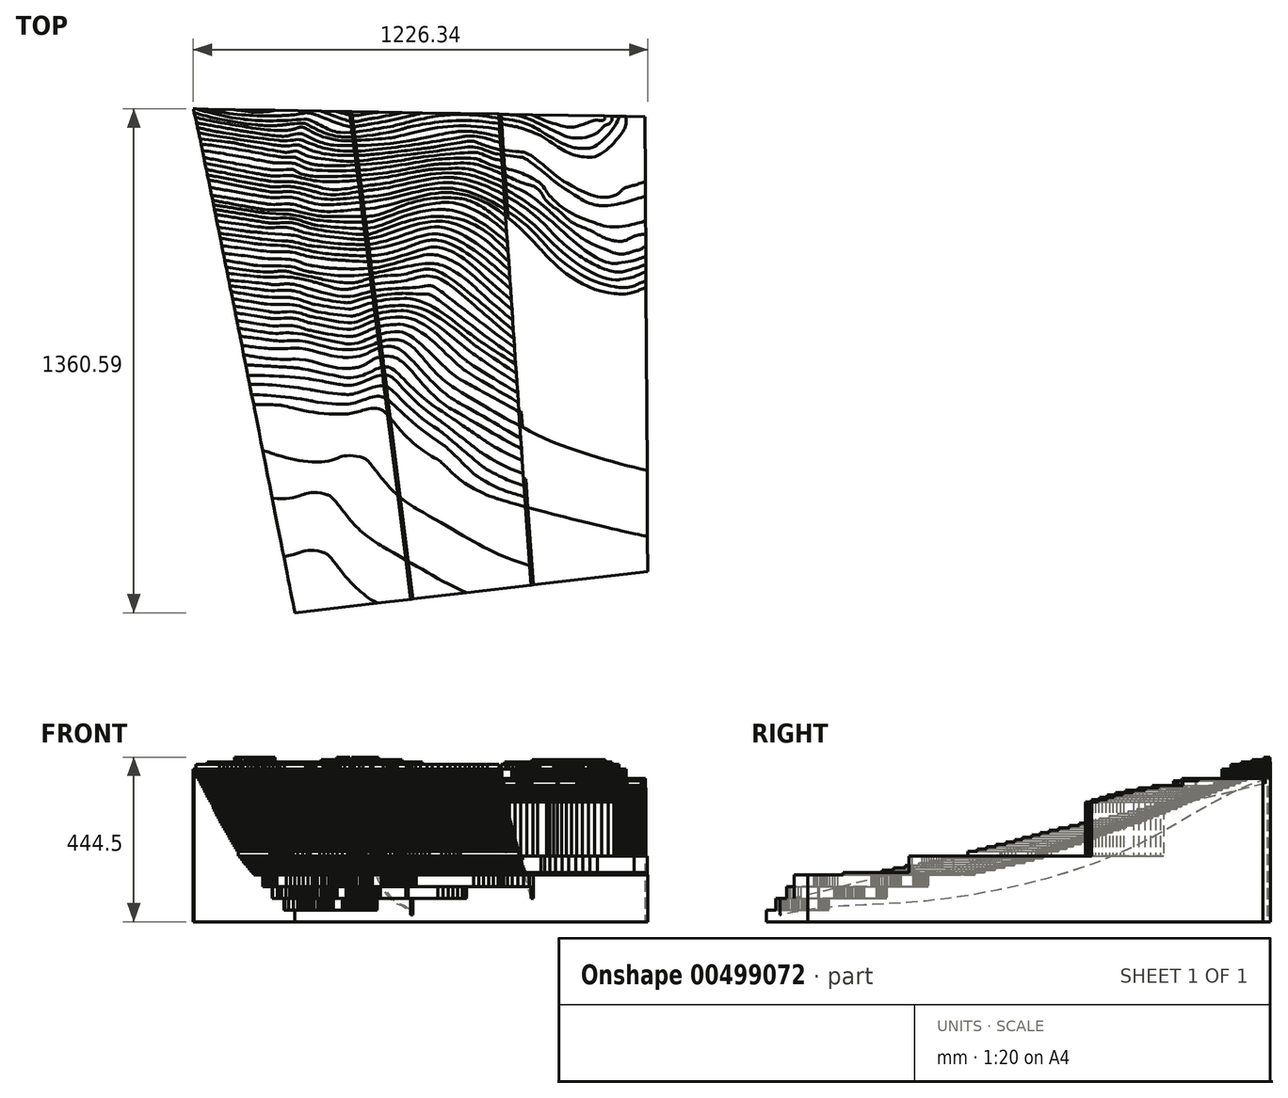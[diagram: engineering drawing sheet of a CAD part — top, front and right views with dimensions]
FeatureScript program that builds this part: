
annotation { "Feature Type Name" : "Feature", "Feature Type Description" : "" }
export const myFeature = defineFeature(function(context is Context, id is Id, definition is map)
    precondition{}
    {
        {
            var Q0;
            Q0=qCreatedBy(makeId("Top.planeOp"),FACE);
            var sketch = newSketch(context, id + "F0", { "sketchPlane" : qUnion([Q0])});
            skLineSegment(sketch, "E0", {"start": v(-613.2, 679.89) * mm, "end": v(-613.14, 679.9) * mm});
            skLineSegment(sketch, "E1", {"start": v(-613.14, 679.9) * mm, "end": v(-612.74, 678.97) * mm});
            skLineSegment(sketch, "E2", {"start": v(-612.74, 678.97) * mm, "end": v(-611.9, 676.1) * mm});
            skLineSegment(sketch, "E3", {"start": v(-611.9, 676.1) * mm, "end": v(-610.7, 671.38) * mm});
            skLineSegment(sketch, "E4", {"start": v(-610.7, 671.38) * mm, "end": v(-609.15, 664.84) * mm});
            skLineSegment(sketch, "E5", {"start": v(-609.15, 664.84) * mm, "end": v(-607.27, 656.56) * mm});
            skLineSegment(sketch, "E6", {"start": v(-607.27, 656.56) * mm, "end": v(-605.06, 646.58) * mm});
            skLineSegment(sketch, "E7", {"start": v(-605.06, 646.58) * mm, "end": v(-602.54, 634.99) * mm});
            skLineSegment(sketch, "E8", {"start": v(-602.54, 634.99) * mm, "end": v(-599.72, 621.83) * mm});
            skLineSegment(sketch, "E9", {"start": v(-599.72, 621.83) * mm, "end": v(-596.61, 607.18) * mm});
            skLineSegment(sketch, "E10", {"start": v(-596.61, 607.18) * mm, "end": v(-593.23, 591.1) * mm});
            skLineSegment(sketch, "E11", {"start": v(-593.23, 591.1) * mm, "end": v(-589.58, 573.63) * mm});
            skLineSegment(sketch, "E12", {"start": v(-589.58, 573.63) * mm, "end": v(-585.69, 554.85) * mm});
            skLineSegment(sketch, "E13", {"start": v(-585.69, 554.85) * mm, "end": v(-581.55, 534.83) * mm});
            skLineSegment(sketch, "E14", {"start": v(-581.55, 534.83) * mm, "end": v(-577.19, 513.62) * mm});
            skLineSegment(sketch, "E15", {"start": v(-577.19, 513.62) * mm, "end": v(-572.6, 491.29) * mm});
            skLineSegment(sketch, "E16", {"start": v(-572.6, 491.29) * mm, "end": v(-567.83, 467.9) * mm});
            skLineSegment(sketch, "E17", {"start": v(-567.83, 467.9) * mm, "end": v(-562.86, 443.5) * mm});
            skLineSegment(sketch, "E18", {"start": v(-562.86, 443.5) * mm, "end": v(-557.7, 418.17) * mm});
            skLineSegment(sketch, "E19", {"start": v(-557.7, 418.17) * mm, "end": v(-552.4, 391.97) * mm});
            skLineSegment(sketch, "E20", {"start": v(-552.4, 391.97) * mm, "end": v(-546.93, 364.95) * mm});
            skLineSegment(sketch, "E21", {"start": v(-546.93, 364.95) * mm, "end": v(-541.31, 337.18) * mm});
            skLineSegment(sketch, "E22", {"start": v(-541.31, 337.18) * mm, "end": v(-535.57, 308.73) * mm});
            skLineSegment(sketch, "E23", {"start": v(-535.57, 308.73) * mm, "end": v(-529.72, 279.65) * mm});
            skLineSegment(sketch, "E24", {"start": v(-529.72, 279.65) * mm, "end": v(-523.75, 250.01) * mm});
            skLineSegment(sketch, "E25", {"start": v(-523.75, 250.01) * mm, "end": v(-517.7, 219.87) * mm});
            skLineSegment(sketch, "E26", {"start": v(-517.7, 219.87) * mm, "end": v(-511.56, 189.3) * mm});
            skLineSegment(sketch, "E27", {"start": v(-511.56, 189.3) * mm, "end": v(-505.36, 158.34) * mm});
            skLineSegment(sketch, "E28", {"start": v(-505.36, 158.34) * mm, "end": v(-499.1, 127.08) * mm});
            skLineSegment(sketch, "E29", {"start": v(-499.1, 127.08) * mm, "end": v(-492.79, 95.56) * mm});
            skLineSegment(sketch, "E30", {"start": v(-492.79, 95.56) * mm, "end": v(-486.45, 63.85) * mm});
            skLineSegment(sketch, "E31", {"start": v(-486.45, 63.85) * mm, "end": v(-480.1, 32.02) * mm});
            skLineSegment(sketch, "E32", {"start": v(-480.1, 32.02) * mm, "end": v(-473.73, 0.13) * mm});
            skLineSegment(sketch, "E33", {"start": v(-473.73, 0.13) * mm, "end": v(-467.36, -31.77) * mm});
            skLineSegment(sketch, "E34", {"start": v(-467.36, -31.77) * mm, "end": v(-461.02, -63.6) * mm});
            skLineSegment(sketch, "E35", {"start": v(-461.02, -63.6) * mm, "end": v(-454.7, -95.31) * mm});
            skLineSegment(sketch, "E36", {"start": v(-454.7, -95.31) * mm, "end": v(-448.43, -126.84) * mm});
            skLineSegment(sketch, "E37", {"start": v(-448.43, -126.84) * mm, "end": v(-442.2, -158.12) * mm});
            skLineSegment(sketch, "E38", {"start": v(-442.2, -158.12) * mm, "end": v(-436.05, -189.08) * mm});
            skLineSegment(sketch, "E39", {"start": v(-436.05, -189.08) * mm, "end": v(-429.96, -219.67) * mm});
            skLineSegment(sketch, "E40", {"start": v(-429.96, -219.67) * mm, "end": v(-423.97, -249.82) * mm});
            skLineSegment(sketch, "E41", {"start": v(-423.97, -249.82) * mm, "end": v(-418.09, -279.48) * mm});
            skLineSegment(sketch, "E42", {"start": v(-418.09, -279.48) * mm, "end": v(-412.3, -308.58) * mm});
            skLineSegment(sketch, "E43", {"start": v(-412.3, -308.58) * mm, "end": v(-406.66, -337.06) * mm});
            skLineSegment(sketch, "E44", {"start": v(-406.66, -337.06) * mm, "end": v(-401.15, -364.85) * mm});
            skLineSegment(sketch, "E45", {"start": v(-401.15, -364.85) * mm, "end": v(-395.78, -391.89) * mm});
            skLineSegment(sketch, "E46", {"start": v(-395.78, -391.89) * mm, "end": v(-390.59, -418.12) * mm});
            skLineSegment(sketch, "E47", {"start": v(-390.59, -418.12) * mm, "end": v(-385.56, -443.48) * mm});
            skLineSegment(sketch, "E48", {"start": v(-385.56, -443.48) * mm, "end": v(-380.72, -467.9) * mm});
            skLineSegment(sketch, "E49", {"start": v(-380.72, -467.9) * mm, "end": v(-376.09, -491.34) * mm});
            skLineSegment(sketch, "E50", {"start": v(-376.09, -491.34) * mm, "end": v(-371.66, -513.7) * mm});
            skLineSegment(sketch, "E51", {"start": v(-371.66, -513.7) * mm, "end": v(-367.45, -534.95) * mm});
            skLineSegment(sketch, "E52", {"start": v(-367.45, -534.95) * mm, "end": v(-363.49, -555.02) * mm});
            skLineSegment(sketch, "E53", {"start": v(-363.49, -555.02) * mm, "end": v(-359.76, -573.83) * mm});
            skLineSegment(sketch, "E54", {"start": v(-359.76, -573.83) * mm, "end": v(-356.3, -591.34) * mm});
            skLineSegment(sketch, "E55", {"start": v(-356.3, -591.34) * mm, "end": v(-353.11, -607.47) * mm});
            skLineSegment(sketch, "E56", {"start": v(-353.11, -607.47) * mm, "end": v(-350.2, -622.18) * mm});
            skLineSegment(sketch, "E57", {"start": v(-350.2, -622.18) * mm, "end": v(-347.6, -635.38) * mm});
            skLineSegment(sketch, "E58", {"start": v(-347.6, -635.38) * mm, "end": v(-345.3, -647.03) * mm});
            skLineSegment(sketch, "E59", {"start": v(-345.3, -647.03) * mm, "end": v(-343.32, -657.06) * mm});
            skLineSegment(sketch, "E60", {"start": v(-343.32, -657.06) * mm, "end": v(-341.67, -665.4) * mm});
            skLineSegment(sketch, "E61", {"start": v(-341.67, -665.4) * mm, "end": v(-340.37, -672) * mm});
            skLineSegment(sketch, "E62", {"start": v(-340.37, -672) * mm, "end": v(-339.42, -676.8) * mm});
            skLineSegment(sketch, "E63", {"start": v(-339.42, -676.8) * mm, "end": v(-338.85, -679.71) * mm});
            skLineSegment(sketch, "E64", {"start": v(-338.85, -679.71) * mm, "end": v(-338.65, -680.7) * mm});
            skLineSegment(sketch, "E65", {"start": v(-338.65, -680.7) * mm, "end": v(-35.7, -645.1) * mm});
            skLineSegment(sketch, "E66", {"start": v(-35.7, -645.1) * mm, "end": v(613.2, -568.85) * mm});
            skLineSegment(sketch, "E67", {"start": v(613.2, -568.85) * mm, "end": v(605.8, 659.03) * mm});
            skLineSegment(sketch, "E68", {"start": v(605.8, 659.03) * mm, "end": v(-613.2, 679.89) * mm});
            skLineSegment(sketch, "E69", {"start": v(-185.14, 673.3) * mm, "end": v(-19.73, -643.77) * mm});
            skLineSegment(sketch, "E70", {"start": v(210.98, 665.78) * mm, "end": v(297.85, -605.9) * mm});
            skLineSegment(sketch, "E71", {"start": v(605.8, 600.01) * mm, "end": v(605.27, 598.86) * mm});
            skLineSegment(sketch, "E72", {"start": v(605.27, 598.86) * mm, "end": v(603.88, 595.32) * mm});
            skLineSegment(sketch, "E73", {"start": v(603.88, 595.32) * mm, "end": v(602.44, 590.8) * mm});
            skLineSegment(sketch, "E74", {"start": v(602.44, 590.8) * mm, "end": v(601.41, 586.4) * mm});
            skLineSegment(sketch, "E75", {"start": v(601.41, 586.4) * mm, "end": v(600.73, 582.17) * mm});
            skLineSegment(sketch, "E76", {"start": v(600.73, 582.17) * mm, "end": v(600.34, 578.06) * mm});
            skLineSegment(sketch, "E77", {"start": v(600.34, 578.06) * mm, "end": v(600.17, 574.07) * mm});
            skLineSegment(sketch, "E78", {"start": v(600.17, 574.07) * mm, "end": v(600.14, 570.2) * mm});
            skLineSegment(sketch, "E79", {"start": v(600.14, 570.2) * mm, "end": v(600.2, 566.43) * mm});
            skLineSegment(sketch, "E80", {"start": v(600.2, 566.43) * mm, "end": v(600.27, 562.76) * mm});
            skLineSegment(sketch, "E81", {"start": v(600.27, 562.76) * mm, "end": v(600.3, 559.18) * mm});
            skLineSegment(sketch, "E82", {"start": v(600.3, 559.18) * mm, "end": v(600.2, 555.69) * mm});
            skLineSegment(sketch, "E83", {"start": v(600.2, 555.69) * mm, "end": v(599.93, 552.26) * mm});
            skLineSegment(sketch, "E84", {"start": v(599.93, 552.26) * mm, "end": v(599.4, 548.9) * mm});
            skLineSegment(sketch, "E85", {"start": v(599.4, 548.9) * mm, "end": v(598.57, 545.6) * mm});
            skLineSegment(sketch, "E86", {"start": v(598.57, 545.6) * mm, "end": v(597.34, 542.34) * mm});
            skLineSegment(sketch, "E87", {"start": v(597.34, 542.34) * mm, "end": v(596.14, 539.9) * mm});
            skLineSegment(sketch, "E88", {"start": v(596.14, 539.9) * mm, "end": v(595.67, 539.13) * mm});
            skLineSegment(sketch, "E89", {"start": v(595.67, 539.13) * mm, "end": v(595.16, 538.27) * mm});
            skLineSegment(sketch, "E90", {"start": v(595.16, 538.27) * mm, "end": v(593.4, 535.81) * mm});
            skLineSegment(sketch, "E91", {"start": v(593.4, 535.81) * mm, "end": v(590.8, 532.83) * mm});
            skLineSegment(sketch, "E92", {"start": v(590.8, 532.83) * mm, "end": v(587.93, 530.12) * mm});
            skLineSegment(sketch, "E93", {"start": v(587.93, 530.12) * mm, "end": v(584.83, 527.67) * mm});
            skLineSegment(sketch, "E94", {"start": v(584.83, 527.67) * mm, "end": v(581.56, 525.43) * mm});
            skLineSegment(sketch, "E95", {"start": v(581.56, 525.43) * mm, "end": v(578.16, 523.35) * mm});
            skLineSegment(sketch, "E96", {"start": v(578.16, 523.35) * mm, "end": v(574.67, 521.39) * mm});
            skLineSegment(sketch, "E97", {"start": v(574.67, 521.39) * mm, "end": v(571.16, 519.51) * mm});
            skLineSegment(sketch, "E98", {"start": v(571.16, 519.51) * mm, "end": v(567.66, 517.68) * mm});
            skLineSegment(sketch, "E99", {"start": v(567.66, 517.68) * mm, "end": v(564.23, 515.85) * mm});
            skLineSegment(sketch, "E100", {"start": v(564.23, 515.85) * mm, "end": v(560.91, 513.97) * mm});
            skLineSegment(sketch, "E101", {"start": v(560.91, 513.97) * mm, "end": v(557.76, 512.02) * mm});
            skLineSegment(sketch, "E102", {"start": v(557.76, 512.02) * mm, "end": v(554.82, 509.94) * mm});
            skLineSegment(sketch, "E103", {"start": v(554.82, 509.94) * mm, "end": v(552.14, 507.7) * mm});
            skLineSegment(sketch, "E104", {"start": v(552.14, 507.7) * mm, "end": v(549.76, 505.25) * mm});
            skLineSegment(sketch, "E105", {"start": v(549.76, 505.25) * mm, "end": v(548.2, 503.26) * mm});
            skLineSegment(sketch, "E106", {"start": v(548.2, 503.26) * mm, "end": v(547.75, 502.56) * mm});
            skLineSegment(sketch, "E107", {"start": v(547.75, 502.56) * mm, "end": v(547.27, 501.83) * mm});
            skLineSegment(sketch, "E108", {"start": v(547.27, 501.83) * mm, "end": v(545.82, 499.63) * mm});
            skLineSegment(sketch, "E109", {"start": v(545.82, 499.63) * mm, "end": v(543.69, 496.55) * mm});
            skLineSegment(sketch, "E110", {"start": v(543.69, 496.55) * mm, "end": v(541.33, 493.35) * mm});
            skLineSegment(sketch, "E111", {"start": v(541.33, 493.35) * mm, "end": v(538.73, 490.1) * mm});
            skLineSegment(sketch, "E112", {"start": v(538.73, 490.1) * mm, "end": v(535.88, 486.82) * mm});
            skLineSegment(sketch, "E113", {"start": v(535.88, 486.82) * mm, "end": v(532.77, 483.59) * mm});
            skLineSegment(sketch, "E114", {"start": v(532.77, 483.59) * mm, "end": v(529.4, 480.44) * mm});
            skLineSegment(sketch, "E115", {"start": v(529.4, 480.44) * mm, "end": v(525.72, 477.44) * mm});
            skLineSegment(sketch, "E116", {"start": v(525.72, 477.44) * mm, "end": v(521.75, 474.61) * mm});
            skLineSegment(sketch, "E117", {"start": v(521.75, 474.61) * mm, "end": v(517.47, 472.03) * mm});
            skLineSegment(sketch, "E118", {"start": v(517.47, 472.03) * mm, "end": v(512.86, 469.73) * mm});
            skLineSegment(sketch, "E119", {"start": v(512.86, 469.73) * mm, "end": v(507.91, 467.77) * mm});
            skLineSegment(sketch, "E120", {"start": v(507.91, 467.77) * mm, "end": v(502.62, 466.19) * mm});
            skLineSegment(sketch, "E121", {"start": v(502.62, 466.19) * mm, "end": v(496.96, 465.04) * mm});
            skLineSegment(sketch, "E122", {"start": v(496.96, 465.04) * mm, "end": v(490.92, 464.38) * mm});
            skLineSegment(sketch, "E123", {"start": v(490.92, 464.38) * mm, "end": v(486.1, 464.22) * mm});
            skLineSegment(sketch, "E124", {"start": v(486.1, 464.22) * mm, "end": v(484.5, 464.26) * mm});
            skLineSegment(sketch, "E125", {"start": v(484.5, 464.26) * mm, "end": v(481.06, 464.34) * mm});
            skLineSegment(sketch, "E126", {"start": v(481.06, 464.34) * mm, "end": v(470.76, 464.96) * mm});
            skLineSegment(sketch, "E127", {"start": v(470.76, 464.96) * mm, "end": v(458.56, 466.4) * mm});
            skLineSegment(sketch, "E128", {"start": v(458.56, 466.4) * mm, "end": v(447.67, 468.54) * mm});
            skLineSegment(sketch, "E129", {"start": v(447.67, 468.54) * mm, "end": v(437.86, 471.4) * mm});
            skLineSegment(sketch, "E130", {"start": v(437.86, 471.4) * mm, "end": v(428.9, 474.96) * mm});
            skLineSegment(sketch, "E131", {"start": v(428.9, 474.96) * mm, "end": v(420.54, 479.23) * mm});
            skLineSegment(sketch, "E132", {"start": v(420.54, 479.23) * mm, "end": v(412.57, 484.19) * mm});
            skLineSegment(sketch, "E133", {"start": v(412.57, 484.19) * mm, "end": v(404.75, 489.83) * mm});
            skLineSegment(sketch, "E134", {"start": v(404.75, 489.83) * mm, "end": v(396.84, 496.16) * mm});
            skLineSegment(sketch, "E135", {"start": v(396.84, 496.16) * mm, "end": v(388.6, 503.17) * mm});
            skLineSegment(sketch, "E136", {"start": v(388.6, 503.17) * mm, "end": v(379.82, 510.84) * mm});
            skLineSegment(sketch, "E137", {"start": v(379.82, 510.84) * mm, "end": v(370.25, 519.18) * mm});
            skLineSegment(sketch, "E138", {"start": v(370.25, 519.18) * mm, "end": v(359.67, 528.18) * mm});
            skLineSegment(sketch, "E139", {"start": v(359.67, 528.18) * mm, "end": v(347.83, 537.83) * mm});
            skLineSegment(sketch, "E140", {"start": v(347.83, 537.83) * mm, "end": v(334.5, 548.13) * mm});
            skLineSegment(sketch, "E141", {"start": v(334.5, 548.13) * mm, "end": v(323.27, 556.4) * mm});
            skLineSegment(sketch, "E142", {"start": v(323.27, 556.4) * mm, "end": v(319.47, 559.07) * mm});
            skLineSegment(sketch, "E143", {"start": v(319.47, 559.07) * mm, "end": v(317.5, 560.46) * mm});
            skLineSegment(sketch, "E144", {"start": v(317.5, 560.46) * mm, "end": v(311.46, 564.41) * mm});
            skLineSegment(sketch, "E145", {"start": v(311.46, 564.41) * mm, "end": v(304.02, 568.78) * mm});
            skLineSegment(sketch, "E146", {"start": v(304.02, 568.78) * mm, "end": v(297.09, 572.28) * mm});
            skLineSegment(sketch, "E147", {"start": v(297.09, 572.28) * mm, "end": v(290.6, 575) * mm});
            skLineSegment(sketch, "E148", {"start": v(290.6, 575) * mm, "end": v(284.51, 577.07) * mm});
            skLineSegment(sketch, "E149", {"start": v(284.51, 577.07) * mm, "end": v(278.75, 578.57) * mm});
            skLineSegment(sketch, "E150", {"start": v(278.75, 578.57) * mm, "end": v(273.26, 579.6) * mm});
            skLineSegment(sketch, "E151", {"start": v(273.26, 579.6) * mm, "end": v(267.98, 580.29) * mm});
            skLineSegment(sketch, "E152", {"start": v(267.98, 580.29) * mm, "end": v(262.85, 580.7) * mm});
            skLineSegment(sketch, "E153", {"start": v(262.85, 580.7) * mm, "end": v(257.82, 580.98) * mm});
            skLineSegment(sketch, "E154", {"start": v(257.82, 580.98) * mm, "end": v(252.81, 581.2) * mm});
            skLineSegment(sketch, "E155", {"start": v(252.81, 581.2) * mm, "end": v(247.77, 581.47) * mm});
            skLineSegment(sketch, "E156", {"start": v(247.77, 581.47) * mm, "end": v(242.65, 581.9) * mm});
            skLineSegment(sketch, "E157", {"start": v(242.65, 581.9) * mm, "end": v(237.38, 582.57) * mm});
            skLineSegment(sketch, "E158", {"start": v(237.38, 582.57) * mm, "end": v(231.9, 583.6) * mm});
            skLineSegment(sketch, "E159", {"start": v(231.9, 583.6) * mm, "end": v(227.58, 584.68) * mm});
            skLineSegment(sketch, "E160", {"start": v(227.58, 584.68) * mm, "end": v(226.16, 585.1) * mm});
            skLineSegment(sketch, "E161", {"start": v(226.16, 585.1) * mm, "end": v(224.65, 585.56) * mm});
            skLineSegment(sketch, "E162", {"start": v(224.65, 585.56) * mm, "end": v(220.17, 586.96) * mm});
            skLineSegment(sketch, "E163", {"start": v(220.17, 586.96) * mm, "end": v(214, 588.97) * mm});
            skLineSegment(sketch, "E164", {"start": v(214, 588.97) * mm, "end": v(207.69, 591.08) * mm});
            skLineSegment(sketch, "E165", {"start": v(207.69, 591.08) * mm, "end": v(201.23, 593.26) * mm});
            skLineSegment(sketch, "E166", {"start": v(201.23, 593.26) * mm, "end": v(194.65, 595.43) * mm});
            skLineSegment(sketch, "E167", {"start": v(194.65, 595.43) * mm, "end": v(187.98, 597.57) * mm});
            skLineSegment(sketch, "E168", {"start": v(187.98, 597.57) * mm, "end": v(181.22, 599.6) * mm});
            skLineSegment(sketch, "E169", {"start": v(181.22, 599.6) * mm, "end": v(174.38, 601.51) * mm});
            skLineSegment(sketch, "E170", {"start": v(174.38, 601.51) * mm, "end": v(167.5, 603.23) * mm});
            skLineSegment(sketch, "E171", {"start": v(167.5, 603.23) * mm, "end": v(160.57, 604.71) * mm});
            skLineSegment(sketch, "E172", {"start": v(160.57, 604.71) * mm, "end": v(153.63, 605.9) * mm});
            skLineSegment(sketch, "E173", {"start": v(153.63, 605.9) * mm, "end": v(146.7, 606.76) * mm});
            skLineSegment(sketch, "E174", {"start": v(146.7, 606.76) * mm, "end": v(139.77, 607.24) * mm});
            skLineSegment(sketch, "E175", {"start": v(139.77, 607.24) * mm, "end": v(132.88, 607.27) * mm});
            skLineSegment(sketch, "E176", {"start": v(132.88, 607.27) * mm, "end": v(126.04, 606.83) * mm});
            skLineSegment(sketch, "E177", {"start": v(126.04, 606.83) * mm, "end": v(120.95, 606.17) * mm});
            skLineSegment(sketch, "E178", {"start": v(120.95, 606.17) * mm, "end": v(119.27, 605.86) * mm});
            skLineSegment(sketch, "E179", {"start": v(119.27, 605.86) * mm, "end": v(118.3, 605.68) * mm});
            skLineSegment(sketch, "E180", {"start": v(118.3, 605.68) * mm, "end": v(115.38, 605.14) * mm});
            skLineSegment(sketch, "E181", {"start": v(115.38, 605.14) * mm, "end": v(110.5, 604.26) * mm});
            skLineSegment(sketch, "E182", {"start": v(110.5, 604.26) * mm, "end": v(104.68, 603.22) * mm});
            skLineSegment(sketch, "E183", {"start": v(104.68, 603.22) * mm, "end": v(97.99, 602.04) * mm});
            skLineSegment(sketch, "E184", {"start": v(97.99, 602.04) * mm, "end": v(90.48, 600.74) * mm});
            skLineSegment(sketch, "E185", {"start": v(90.48, 600.74) * mm, "end": v(82.22, 599.31) * mm});
            skLineSegment(sketch, "E186", {"start": v(82.22, 599.31) * mm, "end": v(73.26, 597.8) * mm});
            skLineSegment(sketch, "E187", {"start": v(73.26, 597.8) * mm, "end": v(63.66, 596.18) * mm});
            skLineSegment(sketch, "E188", {"start": v(63.66, 596.18) * mm, "end": v(53.5, 594.5) * mm});
            skLineSegment(sketch, "E189", {"start": v(53.5, 594.5) * mm, "end": v(42.82, 592.75) * mm});
            skLineSegment(sketch, "E190", {"start": v(42.82, 592.75) * mm, "end": v(31.68, 590.95) * mm});
            skLineSegment(sketch, "E191", {"start": v(31.68, 590.95) * mm, "end": v(20.15, 589.12) * mm});
            skLineSegment(sketch, "E192", {"start": v(20.15, 589.12) * mm, "end": v(8.29, 587.27) * mm});
            skLineSegment(sketch, "E193", {"start": v(8.29, 587.27) * mm, "end": v(-3.85, 585.41) * mm});
            skLineSegment(sketch, "E194", {"start": v(-3.85, 585.41) * mm, "end": v(-16.2, 583.56) * mm});
            skLineSegment(sketch, "E195", {"start": v(-16.2, 583.56) * mm, "end": v(-28.7, 581.72) * mm});
            skLineSegment(sketch, "E196", {"start": v(-28.7, 581.72) * mm, "end": v(-41.28, 579.92) * mm});
            skLineSegment(sketch, "E197", {"start": v(-41.28, 579.92) * mm, "end": v(-53.9, 578.16) * mm});
            skLineSegment(sketch, "E198", {"start": v(-53.9, 578.16) * mm, "end": v(-66.5, 576.47) * mm});
            skLineSegment(sketch, "E199", {"start": v(-66.5, 576.47) * mm, "end": v(-79, 574.84) * mm});
            skLineSegment(sketch, "E200", {"start": v(-79, 574.84) * mm, "end": v(-91.35, 573.3) * mm});
            skLineSegment(sketch, "E201", {"start": v(-91.35, 573.3) * mm, "end": v(-103.5, 571.85) * mm});
            skLineSegment(sketch, "E202", {"start": v(-103.5, 571.85) * mm, "end": v(-115.37, 570.52) * mm});
            skLineSegment(sketch, "E203", {"start": v(-115.37, 570.52) * mm, "end": v(-126.91, 569.31) * mm});
            skLineSegment(sketch, "E204", {"start": v(-126.91, 569.31) * mm, "end": v(-138.07, 568.25) * mm});
            skLineSegment(sketch, "E205", {"start": v(-138.07, 568.25) * mm, "end": v(-148.77, 567.33) * mm});
            skLineSegment(sketch, "E206", {"start": v(-148.77, 567.33) * mm, "end": v(-158.96, 566.58) * mm});
            skLineSegment(sketch, "E207", {"start": v(-158.96, 566.58) * mm, "end": v(-168.58, 566.01) * mm});
            skLineSegment(sketch, "E208", {"start": v(-168.58, 566.01) * mm, "end": v(-177.56, 565.63) * mm});
            skLineSegment(sketch, "E209", {"start": v(-177.56, 565.63) * mm, "end": v(-185.86, 565.46) * mm});
            skLineSegment(sketch, "E210", {"start": v(-185.86, 565.46) * mm, "end": v(-193.4, 565.5) * mm});
            skLineSegment(sketch, "E211", {"start": v(-193.4, 565.5) * mm, "end": v(-198.44, 565.67) * mm});
            skLineSegment(sketch, "E212", {"start": v(-198.44, 565.67) * mm, "end": v(-200.12, 565.78) * mm});
            skLineSegment(sketch, "E213", {"start": v(-200.12, 565.78) * mm, "end": v(-202.26, 565.91) * mm});
            skLineSegment(sketch, "E214", {"start": v(-202.26, 565.91) * mm, "end": v(-208.66, 566.36) * mm});
            skLineSegment(sketch, "E215", {"start": v(-208.66, 566.36) * mm, "end": v(-216.6, 567) * mm});
            skLineSegment(sketch, "E216", {"start": v(-216.6, 567) * mm, "end": v(-224.03, 567.7) * mm});
            skLineSegment(sketch, "E217", {"start": v(-224.03, 567.7) * mm, "end": v(-231.06, 568.53) * mm});
            skLineSegment(sketch, "E218", {"start": v(-231.06, 568.53) * mm, "end": v(-237.8, 569.48) * mm});
            skLineSegment(sketch, "E219", {"start": v(-237.8, 569.48) * mm, "end": v(-244.32, 570.59) * mm});
            skLineSegment(sketch, "E220", {"start": v(-244.32, 570.59) * mm, "end": v(-250.74, 571.88) * mm});
            skLineSegment(sketch, "E221", {"start": v(-250.74, 571.88) * mm, "end": v(-257.17, 573.37) * mm});
            skLineSegment(sketch, "E222", {"start": v(-257.17, 573.37) * mm, "end": v(-263.68, 575.09) * mm});
            skLineSegment(sketch, "E223", {"start": v(-263.68, 575.09) * mm, "end": v(-270.4, 577.06) * mm});
            skLineSegment(sketch, "E224", {"start": v(-270.4, 577.06) * mm, "end": v(-277.4, 579.32) * mm});
            skLineSegment(sketch, "E225", {"start": v(-277.4, 579.32) * mm, "end": v(-284.8, 581.88) * mm});
            skLineSegment(sketch, "E226", {"start": v(-284.8, 581.88) * mm, "end": v(-292.7, 584.76) * mm});
            skLineSegment(sketch, "E227", {"start": v(-292.7, 584.76) * mm, "end": v(-301.2, 588) * mm});
            skLineSegment(sketch, "E228", {"start": v(-301.2, 588) * mm, "end": v(-310.4, 591.62) * mm});
            skLineSegment(sketch, "E229", {"start": v(-310.4, 591.62) * mm, "end": v(-317.88, 594.63) * mm});
            skLineSegment(sketch, "E230", {"start": v(-317.88, 594.63) * mm, "end": v(-320.38, 595.64) * mm});
            skLineSegment(sketch, "E231", {"start": v(-320.38, 595.64) * mm, "end": v(-321.66, 596.16) * mm});
            skLineSegment(sketch, "E232", {"start": v(-321.66, 596.16) * mm, "end": v(-325.77, 597.08) * mm});
            skLineSegment(sketch, "E233", {"start": v(-325.77, 597.08) * mm, "end": v(-331.45, 597.34) * mm});
            skLineSegment(sketch, "E234", {"start": v(-331.45, 597.34) * mm, "end": v(-337.54, 596.77) * mm});
            skLineSegment(sketch, "E235", {"start": v(-337.54, 596.77) * mm, "end": v(-344.17, 595.74) * mm});
            skLineSegment(sketch, "E236", {"start": v(-344.17, 595.74) * mm, "end": v(-351.48, 594.6) * mm});
            skLineSegment(sketch, "E237", {"start": v(-351.48, 594.6) * mm, "end": v(-359.6, 593.72) * mm});
            skLineSegment(sketch, "E238", {"start": v(-359.6, 593.72) * mm, "end": v(-368.63, 593.46) * mm});
            skLineSegment(sketch, "E239", {"start": v(-368.63, 593.46) * mm, "end": v(-376.23, 593.85) * mm});
            skLineSegment(sketch, "E240", {"start": v(-376.23, 593.85) * mm, "end": v(-378.74, 594.16) * mm});
            skLineSegment(sketch, "E241", {"start": v(-378.74, 594.16) * mm, "end": v(-382.7, 594.64) * mm});
            skLineSegment(sketch, "E242", {"start": v(-382.7, 594.64) * mm, "end": v(-394.59, 596.12) * mm});
            skLineSegment(sketch, "E243", {"start": v(-394.59, 596.12) * mm, "end": v(-409.77, 598.03) * mm});
            skLineSegment(sketch, "E244", {"start": v(-409.77, 598.03) * mm, "end": v(-424.3, 599.88) * mm});
            skLineSegment(sketch, "E245", {"start": v(-424.3, 599.88) * mm, "end": v(-438.15, 601.7) * mm});
            skLineSegment(sketch, "E246", {"start": v(-438.15, 601.7) * mm, "end": v(-451.33, 603.44) * mm});
            skLineSegment(sketch, "E247", {"start": v(-451.33, 603.44) * mm, "end": v(-463.84, 605.13) * mm});
            skLineSegment(sketch, "E248", {"start": v(-463.84, 605.13) * mm, "end": v(-475.66, 606.77) * mm});
            skLineSegment(sketch, "E249", {"start": v(-475.66, 606.77) * mm, "end": v(-486.8, 608.34) * mm});
            skLineSegment(sketch, "E250", {"start": v(-486.8, 608.34) * mm, "end": v(-497.26, 609.86) * mm});
            skLineSegment(sketch, "E251", {"start": v(-497.26, 609.86) * mm, "end": v(-507.02, 611.3) * mm});
            skLineSegment(sketch, "E252", {"start": v(-507.02, 611.3) * mm, "end": v(-516.1, 612.7) * mm});
            skLineSegment(sketch, "E253", {"start": v(-516.1, 612.7) * mm, "end": v(-524.45, 614.02) * mm});
            skLineSegment(sketch, "E254", {"start": v(-524.45, 614.02) * mm, "end": v(-532.11, 615.27) * mm});
            skLineSegment(sketch, "E255", {"start": v(-532.11, 615.27) * mm, "end": v(-539.06, 616.46) * mm});
            skLineSegment(sketch, "E256", {"start": v(-539.06, 616.46) * mm, "end": v(-545.3, 617.58) * mm});
            skLineSegment(sketch, "E257", {"start": v(-545.3, 617.58) * mm, "end": v(-549.44, 618.35) * mm});
            skLineSegment(sketch, "E258", {"start": v(-549.44, 618.35) * mm, "end": v(-550.82, 618.62) * mm});
            skLineSegment(sketch, "E259", {"start": v(-550.82, 618.62) * mm, "end": v(-552.1, 618.87) * mm});
            skLineSegment(sketch, "E260", {"start": v(-552.1, 618.87) * mm, "end": v(-555.94, 619.64) * mm});
            skLineSegment(sketch, "E261", {"start": v(-555.94, 619.64) * mm, "end": v(-560.97, 620.67) * mm});
            skLineSegment(sketch, "E262", {"start": v(-560.97, 620.67) * mm, "end": v(-565.86, 621.7) * mm});
            skLineSegment(sketch, "E263", {"start": v(-565.86, 621.7) * mm, "end": v(-570.6, 622.7) * mm});
            skLineSegment(sketch, "E264", {"start": v(-570.6, 622.7) * mm, "end": v(-575.13, 623.7) * mm});
            skLineSegment(sketch, "E265", {"start": v(-575.13, 623.7) * mm, "end": v(-579.45, 624.65) * mm});
            skLineSegment(sketch, "E266", {"start": v(-579.45, 624.65) * mm, "end": v(-583.5, 625.57) * mm});
            skLineSegment(sketch, "E267", {"start": v(-583.5, 625.57) * mm, "end": v(-587.26, 626.43) * mm});
            skLineSegment(sketch, "E268", {"start": v(-587.26, 626.43) * mm, "end": v(-590.7, 627.23) * mm});
            skLineSegment(sketch, "E269", {"start": v(-590.7, 627.23) * mm, "end": v(-593.8, 627.96) * mm});
            skLineSegment(sketch, "E270", {"start": v(-593.8, 627.96) * mm, "end": v(-596.5, 628.6) * mm});
            skLineSegment(sketch, "E271", {"start": v(-596.5, 628.6) * mm, "end": v(-598.78, 629.15) * mm});
            skLineSegment(sketch, "E272", {"start": v(-598.78, 629.15) * mm, "end": v(-600.6, 629.6) * mm});
            skLineSegment(sketch, "E273", {"start": v(-600.6, 629.6) * mm, "end": v(-601.95, 629.93) * mm});
            skLineSegment(sketch, "E274", {"start": v(-601.95, 629.93) * mm, "end": v(-602.79, 630.13) * mm});
            skLineSegment(sketch, "E275", {"start": v(-602.79, 630.13) * mm, "end": v(-603.07, 630.2) * mm});
            skLineSegment(sketch, "E276", {"start": v(551.81, 549.34) * mm, "end": v(552.44, 554.91) * mm});
            skLineSegment(sketch, "E277", {"start": v(552.44, 554.91) * mm, "end": v(551.81, 549.34) * mm});
            skLineSegment(sketch, "E278", {"start": v(607.88, 486.1) * mm, "end": v(606.78, 485.45) * mm});
            skLineSegment(sketch, "E279", {"start": v(606.78, 485.45) * mm, "end": v(603.41, 483.65) * mm});
            skLineSegment(sketch, "E280", {"start": v(603.41, 483.65) * mm, "end": v(598.9, 481.49) * mm});
            skLineSegment(sketch, "E281", {"start": v(598.9, 481.49) * mm, "end": v(594.36, 479.58) * mm});
            skLineSegment(sketch, "E282", {"start": v(594.36, 479.58) * mm, "end": v(589.84, 477.89) * mm});
            skLineSegment(sketch, "E283", {"start": v(589.84, 477.89) * mm, "end": v(585.37, 476.4) * mm});
            skLineSegment(sketch, "E284", {"start": v(585.37, 476.4) * mm, "end": v(580.97, 475.06) * mm});
            skLineSegment(sketch, "E285", {"start": v(580.97, 475.06) * mm, "end": v(576.68, 473.86) * mm});
            skLineSegment(sketch, "E286", {"start": v(576.68, 473.86) * mm, "end": v(572.53, 472.76) * mm});
            skLineSegment(sketch, "E287", {"start": v(572.53, 472.76) * mm, "end": v(568.54, 471.75) * mm});
            skLineSegment(sketch, "E288", {"start": v(568.54, 471.75) * mm, "end": v(564.76, 470.77) * mm});
            skLineSegment(sketch, "E289", {"start": v(564.76, 470.77) * mm, "end": v(561.2, 469.82) * mm});
            skLineSegment(sketch, "E290", {"start": v(561.2, 469.82) * mm, "end": v(557.9, 468.84) * mm});
            skLineSegment(sketch, "E291", {"start": v(557.9, 468.84) * mm, "end": v(554.9, 467.83) * mm});
            skLineSegment(sketch, "E292", {"start": v(554.9, 467.83) * mm, "end": v(552.2, 466.74) * mm});
            skLineSegment(sketch, "E293", {"start": v(552.2, 466.74) * mm, "end": v(549.87, 465.55) * mm});
            skLineSegment(sketch, "E294", {"start": v(549.87, 465.55) * mm, "end": v(548.38, 464.6) * mm});
            skLineSegment(sketch, "E295", {"start": v(548.38, 464.6) * mm, "end": v(547.92, 464.23) * mm});
            skLineSegment(sketch, "E296", {"start": v(547.92, 464.23) * mm, "end": v(547.48, 463.88) * mm});
            skLineSegment(sketch, "E297", {"start": v(547.48, 463.88) * mm, "end": v(546.2, 462.75) * mm});
            skLineSegment(sketch, "E298", {"start": v(546.2, 462.75) * mm, "end": v(544.47, 461.1) * mm});
            skLineSegment(sketch, "E299", {"start": v(544.47, 461.1) * mm, "end": v(542.71, 459.34) * mm});
            skLineSegment(sketch, "E300", {"start": v(542.71, 459.34) * mm, "end": v(540.86, 457.5) * mm});
            skLineSegment(sketch, "E301", {"start": v(540.86, 457.5) * mm, "end": v(538.87, 455.6) * mm});
            skLineSegment(sketch, "E302", {"start": v(538.87, 455.6) * mm, "end": v(536.69, 453.68) * mm});
            skLineSegment(sketch, "E303", {"start": v(536.69, 453.68) * mm, "end": v(534.26, 451.78) * mm});
            skLineSegment(sketch, "E304", {"start": v(534.26, 451.78) * mm, "end": v(531.55, 449.94) * mm});
            skLineSegment(sketch, "E305", {"start": v(531.55, 449.94) * mm, "end": v(528.5, 448.18) * mm});
            skLineSegment(sketch, "E306", {"start": v(528.5, 448.18) * mm, "end": v(525.04, 446.55) * mm});
            skLineSegment(sketch, "E307", {"start": v(525.04, 446.55) * mm, "end": v(521.15, 445.08) * mm});
            skLineSegment(sketch, "E308", {"start": v(521.15, 445.08) * mm, "end": v(516.77, 443.8) * mm});
            skLineSegment(sketch, "E309", {"start": v(516.77, 443.8) * mm, "end": v(511.84, 442.75) * mm});
            skLineSegment(sketch, "E310", {"start": v(511.84, 442.75) * mm, "end": v(506.31, 441.97) * mm});
            skLineSegment(sketch, "E311", {"start": v(506.31, 441.97) * mm, "end": v(500.15, 441.48) * mm});
            skLineSegment(sketch, "E312", {"start": v(500.15, 441.48) * mm, "end": v(495, 441.32) * mm});
            skLineSegment(sketch, "E313", {"start": v(495, 441.32) * mm, "end": v(493.3, 441.33) * mm});
            skLineSegment(sketch, "E314", {"start": v(493.3, 441.33) * mm, "end": v(491.4, 441.34) * mm});
            skLineSegment(sketch, "E315", {"start": v(491.4, 441.34) * mm, "end": v(485.72, 441.86) * mm});
            skLineSegment(sketch, "E316", {"start": v(485.72, 441.86) * mm, "end": v(477.55, 443.29) * mm});
            skLineSegment(sketch, "E317", {"start": v(477.55, 443.29) * mm, "end": v(468.94, 445.5) * mm});
            skLineSegment(sketch, "E318", {"start": v(468.94, 445.5) * mm, "end": v(460.03, 448.36) * mm});
            skLineSegment(sketch, "E319", {"start": v(460.03, 448.36) * mm, "end": v(450.97, 451.74) * mm});
            skLineSegment(sketch, "E320", {"start": v(450.97, 451.74) * mm, "end": v(441.91, 455.51) * mm});
            skLineSegment(sketch, "E321", {"start": v(441.91, 455.51) * mm, "end": v(433.01, 459.54) * mm});
            skLineSegment(sketch, "E322", {"start": v(433.01, 459.54) * mm, "end": v(424.4, 463.7) * mm});
            skLineSegment(sketch, "E323", {"start": v(424.4, 463.7) * mm, "end": v(416.26, 467.85) * mm});
            skLineSegment(sketch, "E324", {"start": v(416.26, 467.85) * mm, "end": v(408.7, 471.88) * mm});
            skLineSegment(sketch, "E325", {"start": v(408.7, 471.88) * mm, "end": v(401.9, 475.64) * mm});
            skLineSegment(sketch, "E326", {"start": v(401.9, 475.64) * mm, "end": v(396.01, 479) * mm});
            skLineSegment(sketch, "E327", {"start": v(396.01, 479) * mm, "end": v(391.16, 481.85) * mm});
            skLineSegment(sketch, "E328", {"start": v(391.16, 481.85) * mm, "end": v(387.51, 484.05) * mm});
            skLineSegment(sketch, "E329", {"start": v(387.51, 484.05) * mm, "end": v(385.22, 485.46) * mm});
            skLineSegment(sketch, "E330", {"start": v(385.22, 485.46) * mm, "end": v(384.42, 485.96) * mm});
            skLineSegment(sketch, "E331", {"start": v(384.42, 485.96) * mm, "end": v(382.25, 487.5) * mm});
            skLineSegment(sketch, "E332", {"start": v(382.25, 487.5) * mm, "end": v(375.81, 492.26) * mm});
            skLineSegment(sketch, "E333", {"start": v(375.81, 492.26) * mm, "end": v(367.48, 498.66) * mm});
            skLineSegment(sketch, "E334", {"start": v(367.48, 498.66) * mm, "end": v(359.4, 505.1) * mm});
            skLineSegment(sketch, "E335", {"start": v(359.4, 505.1) * mm, "end": v(351.57, 511.5) * mm});
            skLineSegment(sketch, "E336", {"start": v(351.57, 511.5) * mm, "end": v(344, 517.81) * mm});
            skLineSegment(sketch, "E337", {"start": v(344, 517.81) * mm, "end": v(336.68, 523.97) * mm});
            skLineSegment(sketch, "E338", {"start": v(336.68, 523.97) * mm, "end": v(329.61, 529.92) * mm});
            skLineSegment(sketch, "E339", {"start": v(329.61, 529.92) * mm, "end": v(322.8, 535.58) * mm});
            skLineSegment(sketch, "E340", {"start": v(322.8, 535.58) * mm, "end": v(316.21, 540.9) * mm});
            skLineSegment(sketch, "E341", {"start": v(316.21, 540.9) * mm, "end": v(309.87, 545.8) * mm});
            skLineSegment(sketch, "E342", {"start": v(309.87, 545.8) * mm, "end": v(303.77, 550.23) * mm});
            skLineSegment(sketch, "E343", {"start": v(303.77, 550.23) * mm, "end": v(297.9, 554.13) * mm});
            skLineSegment(sketch, "E344", {"start": v(297.9, 554.13) * mm, "end": v(292.28, 557.42) * mm});
            skLineSegment(sketch, "E345", {"start": v(292.28, 557.42) * mm, "end": v(286.88, 560.05) * mm});
            skLineSegment(sketch, "E346", {"start": v(286.88, 560.05) * mm, "end": v(281.7, 561.95) * mm});
            skLineSegment(sketch, "E347", {"start": v(281.7, 561.95) * mm, "end": v(278.01, 562.88) * mm});
            skLineSegment(sketch, "E348", {"start": v(278.01, 562.88) * mm, "end": v(276.76, 563.05) * mm});
            skLineSegment(sketch, "E349", {"start": v(276.76, 563.05) * mm, "end": v(275.56, 563.23) * mm});
            skLineSegment(sketch, "E350", {"start": v(275.56, 563.23) * mm, "end": v(271.94, 563.66) * mm});
            skLineSegment(sketch, "E351", {"start": v(271.94, 563.66) * mm, "end": v(265.25, 564.4) * mm});
            skLineSegment(sketch, "E352", {"start": v(265.25, 564.4) * mm, "end": v(257.16, 565.26) * mm});
            skLineSegment(sketch, "E353", {"start": v(257.16, 565.26) * mm, "end": v(248.15, 566.2) * mm});
            skLineSegment(sketch, "E354", {"start": v(248.15, 566.2) * mm, "end": v(238.7, 567.2) * mm});
            skLineSegment(sketch, "E355", {"start": v(238.7, 567.2) * mm, "end": v(229.3, 568.22) * mm});
            skLineSegment(sketch, "E356", {"start": v(229.3, 568.22) * mm, "end": v(220.41, 569.26) * mm});
            skLineSegment(sketch, "E357", {"start": v(220.41, 569.26) * mm, "end": v(214.49, 570) * mm});
            skLineSegment(sketch, "E358", {"start": v(214.49, 570) * mm, "end": v(212.52, 570.27) * mm});
            skLineSegment(sketch, "E359", {"start": v(212.52, 570.27) * mm, "end": v(211.54, 570.4) * mm});
            skLineSegment(sketch, "E360", {"start": v(211.54, 570.4) * mm, "end": v(208.62, 570.96) * mm});
            skLineSegment(sketch, "E361", {"start": v(208.62, 570.96) * mm, "end": v(204.2, 571.99) * mm});
            skLineSegment(sketch, "E362", {"start": v(204.2, 571.99) * mm, "end": v(199.38, 573.3) * mm});
            skLineSegment(sketch, "E363", {"start": v(199.38, 573.3) * mm, "end": v(194.22, 574.86) * mm});
            skLineSegment(sketch, "E364", {"start": v(194.22, 574.86) * mm, "end": v(188.82, 576.6) * mm});
            skLineSegment(sketch, "E365", {"start": v(188.82, 576.6) * mm, "end": v(183.25, 578.48) * mm});
            skLineSegment(sketch, "E366", {"start": v(183.25, 578.48) * mm, "end": v(177.63, 580.43) * mm});
            skLineSegment(sketch, "E367", {"start": v(177.63, 580.43) * mm, "end": v(172.01, 582.42) * mm});
            skLineSegment(sketch, "E368", {"start": v(172.01, 582.42) * mm, "end": v(166.51, 584.39) * mm});
            skLineSegment(sketch, "E369", {"start": v(166.51, 584.39) * mm, "end": v(161.2, 586.27) * mm});
            skLineSegment(sketch, "E370", {"start": v(161.2, 586.27) * mm, "end": v(156.17, 588.04) * mm});
            skLineSegment(sketch, "E371", {"start": v(156.17, 588.04) * mm, "end": v(151.52, 589.63) * mm});
            skLineSegment(sketch, "E372", {"start": v(151.52, 589.63) * mm, "end": v(147.32, 590.98) * mm});
            skLineSegment(sketch, "E373", {"start": v(147.32, 590.98) * mm, "end": v(143.66, 592.06) * mm});
            skLineSegment(sketch, "E374", {"start": v(143.66, 592.06) * mm, "end": v(140.64, 592.8) * mm});
            skLineSegment(sketch, "E375", {"start": v(140.64, 592.8) * mm, "end": v(138.92, 593.11) * mm});
            skLineSegment(sketch, "E376", {"start": v(138.92, 593.11) * mm, "end": v(138.35, 593.16) * mm});
            skLineSegment(sketch, "E377", {"start": v(138.35, 593.16) * mm, "end": v(137.69, 593.2) * mm});
            skLineSegment(sketch, "E378", {"start": v(137.69, 593.2) * mm, "end": v(135.7, 593.14) * mm});
            skLineSegment(sketch, "E379", {"start": v(135.7, 593.14) * mm, "end": v(131.72, 592.8) * mm});
            skLineSegment(sketch, "E380", {"start": v(131.72, 592.8) * mm, "end": v(126.58, 592.2) * mm});
            skLineSegment(sketch, "E381", {"start": v(126.58, 592.2) * mm, "end": v(120.46, 591.37) * mm});
            skLineSegment(sketch, "E382", {"start": v(120.46, 591.37) * mm, "end": v(113.55, 590.34) * mm});
            skLineSegment(sketch, "E383", {"start": v(113.55, 590.34) * mm, "end": v(106.03, 589.15) * mm});
            skLineSegment(sketch, "E384", {"start": v(106.03, 589.15) * mm, "end": v(98.09, 587.85) * mm});
            skLineSegment(sketch, "E385", {"start": v(98.09, 587.85) * mm, "end": v(89.9, 586.47) * mm});
            skLineSegment(sketch, "E386", {"start": v(89.9, 586.47) * mm, "end": v(81.65, 585.04) * mm});
            skLineSegment(sketch, "E387", {"start": v(81.65, 585.04) * mm, "end": v(73.52, 583.6) * mm});
            skLineSegment(sketch, "E388", {"start": v(73.52, 583.6) * mm, "end": v(65.7, 582.21) * mm});
            skLineSegment(sketch, "E389", {"start": v(65.7, 582.21) * mm, "end": v(58.38, 580.89) * mm});
            skLineSegment(sketch, "E390", {"start": v(58.38, 580.89) * mm, "end": v(51.72, 579.68) * mm});
            skLineSegment(sketch, "E391", {"start": v(51.72, 579.68) * mm, "end": v(45.92, 578.62) * mm});
            skLineSegment(sketch, "E392", {"start": v(45.92, 578.62) * mm, "end": v(41.15, 577.74) * mm});
            skLineSegment(sketch, "E393", {"start": v(41.15, 577.74) * mm, "end": v(38.5, 577.26) * mm});
            skLineSegment(sketch, "E394", {"start": v(38.5, 577.26) * mm, "end": v(37.61, 577.1) * mm});
            skLineSegment(sketch, "E395", {"start": v(37.61, 577.1) * mm, "end": v(37.15, 577) * mm});
            skLineSegment(sketch, "E396", {"start": v(37.15, 577) * mm, "end": v(35.75, 576.78) * mm});
            skLineSegment(sketch, "E397", {"start": v(35.75, 576.78) * mm, "end": v(33.07, 576.38) * mm});
            skLineSegment(sketch, "E398", {"start": v(33.07, 576.38) * mm, "end": v(29.63, 575.89) * mm});
            skLineSegment(sketch, "E399", {"start": v(29.63, 575.89) * mm, "end": v(25.47, 575.31) * mm});
            skLineSegment(sketch, "E400", {"start": v(25.47, 575.31) * mm, "end": v(20.66, 574.66) * mm});
            skLineSegment(sketch, "E401", {"start": v(20.66, 574.66) * mm, "end": v(15.24, 573.95) * mm});
            skLineSegment(sketch, "E402", {"start": v(15.24, 573.95) * mm, "end": v(9.26, 573.18) * mm});
            skLineSegment(sketch, "E403", {"start": v(9.26, 573.18) * mm, "end": v(2.78, 572.35) * mm});
            skLineSegment(sketch, "E404", {"start": v(2.78, 572.35) * mm, "end": v(-4.15, 571.48) * mm});
            skLineSegment(sketch, "E405", {"start": v(-4.15, 571.48) * mm, "end": v(-11.47, 570.56) * mm});
            skLineSegment(sketch, "E406", {"start": v(-11.47, 570.56) * mm, "end": v(-19.14, 569.62) * mm});
            skLineSegment(sketch, "E407", {"start": v(-19.14, 569.62) * mm, "end": v(-27.1, 568.64) * mm});
            skLineSegment(sketch, "E408", {"start": v(-27.1, 568.64) * mm, "end": v(-35.3, 567.65) * mm});
            skLineSegment(sketch, "E409", {"start": v(-35.3, 567.65) * mm, "end": v(-43.68, 566.64) * mm});
            skLineSegment(sketch, "E410", {"start": v(-43.68, 566.64) * mm, "end": v(-52.2, 565.63) * mm});
            skLineSegment(sketch, "E411", {"start": v(-52.2, 565.63) * mm, "end": v(-60.8, 564.62) * mm});
            skLineSegment(sketch, "E412", {"start": v(-60.8, 564.62) * mm, "end": v(-69.44, 563.62) * mm});
            skLineSegment(sketch, "E413", {"start": v(-69.44, 563.62) * mm, "end": v(-78.05, 562.63) * mm});
            skLineSegment(sketch, "E414", {"start": v(-78.05, 562.63) * mm, "end": v(-86.58, 561.66) * mm});
            skLineSegment(sketch, "E415", {"start": v(-86.58, 561.66) * mm, "end": v(-94.98, 560.72) * mm});
            skLineSegment(sketch, "E416", {"start": v(-94.98, 560.72) * mm, "end": v(-103.2, 559.82) * mm});
            skLineSegment(sketch, "E417", {"start": v(-103.2, 559.82) * mm, "end": v(-111.2, 558.95) * mm});
            skLineSegment(sketch, "E418", {"start": v(-111.2, 558.95) * mm, "end": v(-118.9, 558.14) * mm});
            skLineSegment(sketch, "E419", {"start": v(-118.9, 558.14) * mm, "end": v(-126.25, 557.38) * mm});
            skLineSegment(sketch, "E420", {"start": v(-126.25, 557.38) * mm, "end": v(-133.22, 556.68) * mm});
            skLineSegment(sketch, "E421", {"start": v(-133.22, 556.68) * mm, "end": v(-139.75, 556.05) * mm});
            skLineSegment(sketch, "E422", {"start": v(-139.75, 556.05) * mm, "end": v(-145.78, 555.5) * mm});
            skLineSegment(sketch, "E423", {"start": v(-145.78, 555.5) * mm, "end": v(-151.26, 555.03) * mm});
            skLineSegment(sketch, "E424", {"start": v(-151.26, 555.03) * mm, "end": v(-156.14, 554.64) * mm});
            skLineSegment(sketch, "E425", {"start": v(-156.14, 554.64) * mm, "end": v(-160.37, 554.36) * mm});
            skLineSegment(sketch, "E426", {"start": v(-160.37, 554.36) * mm, "end": v(-163.88, 554.18) * mm});
            skLineSegment(sketch, "E427", {"start": v(-163.88, 554.18) * mm, "end": v(-165.95, 554.1) * mm});
            skLineSegment(sketch, "E428", {"start": v(-165.95, 554.1) * mm, "end": v(-166.64, 554.1) * mm});
            skLineSegment(sketch, "E429", {"start": v(-166.64, 554.1) * mm, "end": v(-169.4, 554.08) * mm});
            skLineSegment(sketch, "E430", {"start": v(-169.4, 554.08) * mm, "end": v(-177.68, 554.06) * mm});
            skLineSegment(sketch, "E431", {"start": v(-177.68, 554.06) * mm, "end": v(-188.01, 554.07) * mm});
            skLineSegment(sketch, "E432", {"start": v(-188.01, 554.07) * mm, "end": v(-197.7, 554.17) * mm});
            skLineSegment(sketch, "E433", {"start": v(-197.7, 554.17) * mm, "end": v(-206.81, 554.36) * mm});
            skLineSegment(sketch, "E434", {"start": v(-206.81, 554.36) * mm, "end": v(-215.38, 554.64) * mm});
            skLineSegment(sketch, "E435", {"start": v(-215.38, 554.64) * mm, "end": v(-223.48, 555.04) * mm});
            skLineSegment(sketch, "E436", {"start": v(-223.48, 555.04) * mm, "end": v(-231.16, 555.55) * mm});
            skLineSegment(sketch, "E437", {"start": v(-231.16, 555.55) * mm, "end": v(-238.48, 556.19) * mm});
            skLineSegment(sketch, "E438", {"start": v(-238.48, 556.19) * mm, "end": v(-245.48, 556.96) * mm});
            skLineSegment(sketch, "E439", {"start": v(-245.48, 556.96) * mm, "end": v(-252.24, 557.88) * mm});
            skLineSegment(sketch, "E440", {"start": v(-252.24, 557.88) * mm, "end": v(-258.8, 558.96) * mm});
            skLineSegment(sketch, "E441", {"start": v(-258.8, 558.96) * mm, "end": v(-265.23, 560.2) * mm});
            skLineSegment(sketch, "E442", {"start": v(-265.23, 560.2) * mm, "end": v(-271.56, 561.63) * mm});
            skLineSegment(sketch, "E443", {"start": v(-271.56, 561.63) * mm, "end": v(-277.87, 563.24) * mm});
            skLineSegment(sketch, "E444", {"start": v(-277.87, 563.24) * mm, "end": v(-284.2, 565.04) * mm});
            skLineSegment(sketch, "E445", {"start": v(-284.2, 565.04) * mm, "end": v(-289.04, 566.53) * mm});
            skLineSegment(sketch, "E446", {"start": v(-289.04, 566.53) * mm, "end": v(-290.63, 567.05) * mm});
            skLineSegment(sketch, "E447", {"start": v(-290.63, 567.05) * mm, "end": v(-292.13, 567.54) * mm});
            skLineSegment(sketch, "E448", {"start": v(-292.13, 567.54) * mm, "end": v(-296.56, 569.15) * mm});
            skLineSegment(sketch, "E449", {"start": v(-296.56, 569.15) * mm, "end": v(-302.2, 571.38) * mm});
            skLineSegment(sketch, "E450", {"start": v(-302.2, 571.38) * mm, "end": v(-307.53, 573.67) * mm});
            skLineSegment(sketch, "E451", {"start": v(-307.53, 573.67) * mm, "end": v(-312.54, 575.9) * mm});
            skLineSegment(sketch, "E452", {"start": v(-312.54, 575.9) * mm, "end": v(-317.21, 577.96) * mm});
            skLineSegment(sketch, "E453", {"start": v(-317.21, 577.96) * mm, "end": v(-321.54, 579.78) * mm});
            skLineSegment(sketch, "E454", {"start": v(-321.54, 579.78) * mm, "end": v(-325.5, 581.23) * mm});
            skLineSegment(sketch, "E455", {"start": v(-325.5, 581.23) * mm, "end": v(-328.18, 582.03) * mm});
            skLineSegment(sketch, "E456", {"start": v(-328.18, 582.03) * mm, "end": v(-329.09, 582.22) * mm});
            skLineSegment(sketch, "E457", {"start": v(-329.09, 582.22) * mm, "end": v(-330, 582.42) * mm});
            skLineSegment(sketch, "E458", {"start": v(-330, 582.42) * mm, "end": v(-332.83, 582.62) * mm});
            skLineSegment(sketch, "E459", {"start": v(-332.83, 582.62) * mm, "end": v(-337.25, 582.47) * mm});
            skLineSegment(sketch, "E460", {"start": v(-337.25, 582.47) * mm, "end": v(-342.3, 581.96) * mm});
            skLineSegment(sketch, "E461", {"start": v(-342.3, 581.96) * mm, "end": v(-347.91, 581.28) * mm});
            skLineSegment(sketch, "E462", {"start": v(-347.91, 581.28) * mm, "end": v(-354.07, 580.6) * mm});
            skLineSegment(sketch, "E463", {"start": v(-354.07, 580.6) * mm, "end": v(-360.72, 580.12) * mm});
            skLineSegment(sketch, "E464", {"start": v(-360.72, 580.12) * mm, "end": v(-367.81, 580) * mm});
            skLineSegment(sketch, "E465", {"start": v(-367.81, 580) * mm, "end": v(-373.43, 580.27) * mm});
            skLineSegment(sketch, "E466", {"start": v(-373.43, 580.27) * mm, "end": v(-375.3, 580.46) * mm});
            skLineSegment(sketch, "E467", {"start": v(-375.3, 580.46) * mm, "end": v(-375.9, 580.52) * mm});
            skLineSegment(sketch, "E468", {"start": v(-375.9, 580.52) * mm, "end": v(-377.67, 580.73) * mm});
            skLineSegment(sketch, "E469", {"start": v(-377.67, 580.73) * mm, "end": v(-380.92, 581.14) * mm});
            skLineSegment(sketch, "E470", {"start": v(-380.92, 581.14) * mm, "end": v(-385, 581.68) * mm});
            skLineSegment(sketch, "E471", {"start": v(-385, 581.68) * mm, "end": v(-389.83, 582.34) * mm});
            skLineSegment(sketch, "E472", {"start": v(-389.83, 582.34) * mm, "end": v(-395.36, 583.12) * mm});
            skLineSegment(sketch, "E473", {"start": v(-395.36, 583.12) * mm, "end": v(-401.54, 584) * mm});
            skLineSegment(sketch, "E474", {"start": v(-401.54, 584) * mm, "end": v(-408.31, 584.98) * mm});
            skLineSegment(sketch, "E475", {"start": v(-408.31, 584.98) * mm, "end": v(-415.61, 586.05) * mm});
            skLineSegment(sketch, "E476", {"start": v(-415.61, 586.05) * mm, "end": v(-423.39, 587.2) * mm});
            skLineSegment(sketch, "E477", {"start": v(-423.39, 587.2) * mm, "end": v(-431.58, 588.4) * mm});
            skLineSegment(sketch, "E478", {"start": v(-431.58, 588.4) * mm, "end": v(-440.13, 589.7) * mm});
            skLineSegment(sketch, "E479", {"start": v(-440.13, 589.7) * mm, "end": v(-449, 591.02) * mm});
            skLineSegment(sketch, "E480", {"start": v(-449, 591.02) * mm, "end": v(-458.1, 592.4) * mm});
            skLineSegment(sketch, "E481", {"start": v(-458.1, 592.4) * mm, "end": v(-467.38, 593.82) * mm});
            skLineSegment(sketch, "E482", {"start": v(-467.38, 593.82) * mm, "end": v(-476.8, 595.27) * mm});
            skLineSegment(sketch, "E483", {"start": v(-476.8, 595.27) * mm, "end": v(-486.3, 596.74) * mm});
            skLineSegment(sketch, "E484", {"start": v(-486.3, 596.74) * mm, "end": v(-495.8, 598.22) * mm});
            skLineSegment(sketch, "E485", {"start": v(-495.8, 598.22) * mm, "end": v(-505.27, 599.7) * mm});
            skLineSegment(sketch, "E486", {"start": v(-505.27, 599.7) * mm, "end": v(-514.63, 601.19) * mm});
            skLineSegment(sketch, "E487", {"start": v(-514.63, 601.19) * mm, "end": v(-523.85, 602.66) * mm});
            skLineSegment(sketch, "E488", {"start": v(-523.85, 602.66) * mm, "end": v(-532.84, 604.1) * mm});
            skLineSegment(sketch, "E489", {"start": v(-532.84, 604.1) * mm, "end": v(-541.57, 605.52) * mm});
            skLineSegment(sketch, "E490", {"start": v(-541.57, 605.52) * mm, "end": v(-549.97, 606.9) * mm});
            skLineSegment(sketch, "E491", {"start": v(-549.97, 606.9) * mm, "end": v(-557.98, 608.22) * mm});
            skLineSegment(sketch, "E492", {"start": v(-557.98, 608.22) * mm, "end": v(-565.55, 609.5) * mm});
            skLineSegment(sketch, "E493", {"start": v(-565.55, 609.5) * mm, "end": v(-572.63, 610.7) * mm});
            skLineSegment(sketch, "E494", {"start": v(-572.63, 610.7) * mm, "end": v(-579.14, 611.85) * mm});
            skLineSegment(sketch, "E495", {"start": v(-579.14, 611.85) * mm, "end": v(-585.04, 612.9) * mm});
            skLineSegment(sketch, "E496", {"start": v(-585.04, 612.9) * mm, "end": v(-590.26, 613.87) * mm});
            skLineSegment(sketch, "E497", {"start": v(-590.26, 613.87) * mm, "end": v(-594.76, 614.74) * mm});
            skLineSegment(sketch, "E498", {"start": v(-594.76, 614.74) * mm, "end": v(-598.47, 615.51) * mm});
            skLineSegment(sketch, "E499", {"start": v(-598.47, 615.51) * mm, "end": v(-600.62, 615.99) * mm});
            skLineSegment(sketch, "E500", {"start": v(-600.62, 615.99) * mm, "end": v(-601.34, 616.16) * mm});
            skLineSegment(sketch, "E501", {"start": v(607.55, 443.93) * mm, "end": v(606.08, 443.6) * mm});
            skLineSegment(sketch, "E502", {"start": v(606.08, 443.6) * mm, "end": v(601.68, 442.47) * mm});
            skLineSegment(sketch, "E503", {"start": v(601.68, 442.47) * mm, "end": v(595.25, 440.67) * mm});
            skLineSegment(sketch, "E504", {"start": v(595.25, 440.67) * mm, "end": v(588.33, 438.62) * mm});
            skLineSegment(sketch, "E505", {"start": v(588.33, 438.62) * mm, "end": v(580.98, 436.38) * mm});
            skLineSegment(sketch, "E506", {"start": v(580.98, 436.38) * mm, "end": v(573.26, 434) * mm});
            skLineSegment(sketch, "E507", {"start": v(573.26, 434) * mm, "end": v(565.23, 431.59) * mm});
            skLineSegment(sketch, "E508", {"start": v(565.23, 431.59) * mm, "end": v(556.96, 429.18) * mm});
            skLineSegment(sketch, "E509", {"start": v(556.96, 429.18) * mm, "end": v(548.5, 426.85) * mm});
            skLineSegment(sketch, "E510", {"start": v(548.5, 426.85) * mm, "end": v(539.94, 424.66) * mm});
            skLineSegment(sketch, "E511", {"start": v(539.94, 424.66) * mm, "end": v(531.31, 422.7) * mm});
            skLineSegment(sketch, "E512", {"start": v(531.31, 422.7) * mm, "end": v(522.7, 421) * mm});
            skLineSegment(sketch, "E513", {"start": v(522.7, 421) * mm, "end": v(514.15, 419.67) * mm});
            skLineSegment(sketch, "E514", {"start": v(514.15, 419.67) * mm, "end": v(505.73, 418.75) * mm});
            skLineSegment(sketch, "E515", {"start": v(505.73, 418.75) * mm, "end": v(497.51, 418.32) * mm});
            skLineSegment(sketch, "E516", {"start": v(497.51, 418.32) * mm, "end": v(489.55, 418.43) * mm});
            skLineSegment(sketch, "E517", {"start": v(489.55, 418.43) * mm, "end": v(483.8, 418.9) * mm});
            skLineSegment(sketch, "E518", {"start": v(483.8, 418.9) * mm, "end": v(481.9, 419.17) * mm});
            skLineSegment(sketch, "E519", {"start": v(481.9, 419.17) * mm, "end": v(480.1, 419.43) * mm});
            skLineSegment(sketch, "E520", {"start": v(480.1, 419.43) * mm, "end": v(474.72, 420.36) * mm});
            skLineSegment(sketch, "E521", {"start": v(474.72, 420.36) * mm, "end": v(468.06, 421.78) * mm});
            skLineSegment(sketch, "E522", {"start": v(468.06, 421.78) * mm, "end": v(461.81, 423.45) * mm});
            skLineSegment(sketch, "E523", {"start": v(461.81, 423.45) * mm, "end": v(455.87, 425.4) * mm});
            skLineSegment(sketch, "E524", {"start": v(455.87, 425.4) * mm, "end": v(450.14, 427.63) * mm});
            skLineSegment(sketch, "E525", {"start": v(450.14, 427.63) * mm, "end": v(444.53, 430.16) * mm});
            skLineSegment(sketch, "E526", {"start": v(444.53, 430.16) * mm, "end": v(438.92, 433.02) * mm});
            skLineSegment(sketch, "E527", {"start": v(438.92, 433.02) * mm, "end": v(433.23, 436.22) * mm});
            skLineSegment(sketch, "E528", {"start": v(433.23, 436.22) * mm, "end": v(427.35, 439.77) * mm});
            skLineSegment(sketch, "E529", {"start": v(427.35, 439.77) * mm, "end": v(421.17, 443.7) * mm});
            skLineSegment(sketch, "E530", {"start": v(421.17, 443.7) * mm, "end": v(414.61, 448.01) * mm});
            skLineSegment(sketch, "E531", {"start": v(414.61, 448.01) * mm, "end": v(407.56, 452.73) * mm});
            skLineSegment(sketch, "E532", {"start": v(407.56, 452.73) * mm, "end": v(399.91, 457.88) * mm});
            skLineSegment(sketch, "E533", {"start": v(399.91, 457.88) * mm, "end": v(391.58, 463.46) * mm});
            skLineSegment(sketch, "E534", {"start": v(391.58, 463.46) * mm, "end": v(382.46, 469.5) * mm});
            skLineSegment(sketch, "E535", {"start": v(382.46, 469.5) * mm, "end": v(374.95, 474.4) * mm});
            skLineSegment(sketch, "E536", {"start": v(374.95, 474.4) * mm, "end": v(372.44, 476.01) * mm});
            skLineSegment(sketch, "E537", {"start": v(372.44, 476.01) * mm, "end": v(372.14, 476.2) * mm});
            skLineSegment(sketch, "E538", {"start": v(372.14, 476.2) * mm, "end": v(371.26, 476.82) * mm});
            skLineSegment(sketch, "E539", {"start": v(371.26, 476.82) * mm, "end": v(369.74, 477.95) * mm});
            skLineSegment(sketch, "E540", {"start": v(369.74, 477.95) * mm, "end": v(367.89, 479.39) * mm});
            skLineSegment(sketch, "E541", {"start": v(367.89, 479.39) * mm, "end": v(365.75, 481.1) * mm});
            skLineSegment(sketch, "E542", {"start": v(365.75, 481.1) * mm, "end": v(363.32, 483.05) * mm});
            skLineSegment(sketch, "E543", {"start": v(363.32, 483.05) * mm, "end": v(360.64, 485.24) * mm});
            skLineSegment(sketch, "E544", {"start": v(360.64, 485.24) * mm, "end": v(357.73, 487.63) * mm});
            skLineSegment(sketch, "E545", {"start": v(357.73, 487.63) * mm, "end": v(354.6, 490.21) * mm});
            skLineSegment(sketch, "E546", {"start": v(354.6, 490.21) * mm, "end": v(351.3, 492.96) * mm});
            skLineSegment(sketch, "E547", {"start": v(351.3, 492.96) * mm, "end": v(347.82, 495.84) * mm});
            skLineSegment(sketch, "E548", {"start": v(347.82, 495.84) * mm, "end": v(344.2, 498.84) * mm});
            skLineSegment(sketch, "E549", {"start": v(344.2, 498.84) * mm, "end": v(340.46, 501.94) * mm});
            skLineSegment(sketch, "E550", {"start": v(340.46, 501.94) * mm, "end": v(336.62, 505.1) * mm});
            skLineSegment(sketch, "E551", {"start": v(336.62, 505.1) * mm, "end": v(332.7, 508.33) * mm});
            skLineSegment(sketch, "E552", {"start": v(332.7, 508.33) * mm, "end": v(328.73, 511.58) * mm});
            skLineSegment(sketch, "E553", {"start": v(328.73, 511.58) * mm, "end": v(324.73, 514.83) * mm});
            skLineSegment(sketch, "E554", {"start": v(324.73, 514.83) * mm, "end": v(320.7, 518.07) * mm});
            skLineSegment(sketch, "E555", {"start": v(320.7, 518.07) * mm, "end": v(316.7, 521.27) * mm});
            skLineSegment(sketch, "E556", {"start": v(316.7, 521.27) * mm, "end": v(312.74, 524.4) * mm});
            skLineSegment(sketch, "E557", {"start": v(312.74, 524.4) * mm, "end": v(308.83, 527.45) * mm});
            skLineSegment(sketch, "E558", {"start": v(308.83, 527.45) * mm, "end": v(305, 530.39) * mm});
            skLineSegment(sketch, "E559", {"start": v(305, 530.39) * mm, "end": v(301.28, 533.2) * mm});
            skLineSegment(sketch, "E560", {"start": v(301.28, 533.2) * mm, "end": v(297.68, 535.86) * mm});
            skLineSegment(sketch, "E561", {"start": v(297.68, 535.86) * mm, "end": v(294.22, 538.35) * mm});
            skLineSegment(sketch, "E562", {"start": v(294.22, 538.35) * mm, "end": v(290.94, 540.64) * mm});
            skLineSegment(sketch, "E563", {"start": v(290.94, 540.64) * mm, "end": v(287.84, 542.7) * mm});
            skLineSegment(sketch, "E564", {"start": v(287.84, 542.7) * mm, "end": v(284.96, 544.54) * mm});
            skLineSegment(sketch, "E565", {"start": v(284.96, 544.54) * mm, "end": v(282.31, 546.1) * mm});
            skLineSegment(sketch, "E566", {"start": v(282.31, 546.1) * mm, "end": v(279.92, 547.37) * mm});
            skLineSegment(sketch, "E567", {"start": v(279.92, 547.37) * mm, "end": v(277.82, 548.34) * mm});
            skLineSegment(sketch, "E568", {"start": v(277.82, 548.34) * mm, "end": v(276.02, 548.97) * mm});
            skLineSegment(sketch, "E569", {"start": v(276.02, 548.97) * mm, "end": v(274.9, 549.23) * mm});
            skLineSegment(sketch, "E570", {"start": v(274.9, 549.23) * mm, "end": v(274.54, 549.25) * mm});
            skLineSegment(sketch, "E571", {"start": v(274.54, 549.25) * mm, "end": v(273, 549.36) * mm});
            skLineSegment(sketch, "E572", {"start": v(273, 549.36) * mm, "end": v(268.38, 549.84) * mm});
            skLineSegment(sketch, "E573", {"start": v(268.38, 549.84) * mm, "end": v(260.68, 550.8) * mm});
            skLineSegment(sketch, "E574", {"start": v(260.68, 550.8) * mm, "end": v(251.87, 552.01) * mm});
            skLineSegment(sketch, "E575", {"start": v(251.87, 552.01) * mm, "end": v(242.38, 553.38) * mm});
            skLineSegment(sketch, "E576", {"start": v(242.38, 553.38) * mm, "end": v(232.65, 554.82) * mm});
            skLineSegment(sketch, "E577", {"start": v(232.65, 554.82) * mm, "end": v(223.1, 556.23) * mm});
            skLineSegment(sketch, "E578", {"start": v(223.1, 556.23) * mm, "end": v(214.18, 557.5) * mm});
            skLineSegment(sketch, "E579", {"start": v(214.18, 557.5) * mm, "end": v(208.29, 558.28) * mm});
            skLineSegment(sketch, "E580", {"start": v(208.29, 558.28) * mm, "end": v(206.33, 558.52) * mm});
            skLineSegment(sketch, "E581", {"start": v(206.33, 558.52) * mm, "end": v(204.46, 558.75) * mm});
            skLineSegment(sketch, "E582", {"start": v(204.46, 558.75) * mm, "end": v(198.92, 560) * mm});
            skLineSegment(sketch, "E583", {"start": v(198.92, 560) * mm, "end": v(191.12, 562.44) * mm});
            skLineSegment(sketch, "E584", {"start": v(191.12, 562.44) * mm, "end": v(182.98, 565.5) * mm});
            skLineSegment(sketch, "E585", {"start": v(182.98, 565.5) * mm, "end": v(174.51, 568.8) * mm});
            skLineSegment(sketch, "E586", {"start": v(174.51, 568.8) * mm, "end": v(165.79, 572.03) * mm});
            skLineSegment(sketch, "E587", {"start": v(165.79, 572.03) * mm, "end": v(156.84, 574.8) * mm});
            skLineSegment(sketch, "E588", {"start": v(156.84, 574.8) * mm, "end": v(147.72, 576.78) * mm});
            skLineSegment(sketch, "E589", {"start": v(147.72, 576.78) * mm, "end": v(140.77, 577.57) * mm});
            skLineSegment(sketch, "E590", {"start": v(140.77, 577.57) * mm, "end": v(138.45, 577.6) * mm});
            skLineSegment(sketch, "E591", {"start": v(138.45, 577.6) * mm, "end": v(137.12, 577.62) * mm});
            skLineSegment(sketch, "E592", {"start": v(137.12, 577.62) * mm, "end": v(133.11, 577.5) * mm});
            skLineSegment(sketch, "E593", {"start": v(133.11, 577.5) * mm, "end": v(126.5, 577.05) * mm});
            skLineSegment(sketch, "E594", {"start": v(126.5, 577.05) * mm, "end": v(118.76, 576.33) * mm});
            skLineSegment(sketch, "E595", {"start": v(118.76, 576.33) * mm, "end": v(110.04, 575.36) * mm});
            skLineSegment(sketch, "E596", {"start": v(110.04, 575.36) * mm, "end": v(100.5, 574.18) * mm});
            skLineSegment(sketch, "E597", {"start": v(100.5, 574.18) * mm, "end": v(90.3, 572.82) * mm});
            skLineSegment(sketch, "E598", {"start": v(90.3, 572.82) * mm, "end": v(79.56, 571.34) * mm});
            skLineSegment(sketch, "E599", {"start": v(79.56, 571.34) * mm, "end": v(68.45, 569.76) * mm});
            skLineSegment(sketch, "E600", {"start": v(68.45, 569.76) * mm, "end": v(57.11, 568.12) * mm});
            skLineSegment(sketch, "E601", {"start": v(57.11, 568.12) * mm, "end": v(45.7, 566.47) * mm});
            skLineSegment(sketch, "E602", {"start": v(45.7, 566.47) * mm, "end": v(34.36, 564.83) * mm});
            skLineSegment(sketch, "E603", {"start": v(34.36, 564.83) * mm, "end": v(23.24, 563.26) * mm});
            skLineSegment(sketch, "E604", {"start": v(23.24, 563.26) * mm, "end": v(12.5, 561.78) * mm});
            skLineSegment(sketch, "E605", {"start": v(12.5, 561.78) * mm, "end": v(2.28, 560.45) * mm});
            skLineSegment(sketch, "E606", {"start": v(2.28, 560.45) * mm, "end": v(-7.27, 559.29) * mm});
            skLineSegment(sketch, "E607", {"start": v(-7.27, 559.29) * mm, "end": v(-13.81, 558.56) * mm});
            skLineSegment(sketch, "E608", {"start": v(-13.81, 558.56) * mm, "end": v(-16, 558.34) * mm});
            skLineSegment(sketch, "E609", {"start": v(-16, 558.34) * mm, "end": v(-18.6, 558.09) * mm});
            skLineSegment(sketch, "E610", {"start": v(-18.6, 558.09) * mm, "end": v(-26.4, 557.23) * mm});
            skLineSegment(sketch, "E611", {"start": v(-26.4, 557.23) * mm, "end": v(-37.76, 555.9) * mm});
            skLineSegment(sketch, "E612", {"start": v(-37.76, 555.9) * mm, "end": v(-49.87, 554.37) * mm});
            skLineSegment(sketch, "E613", {"start": v(-49.87, 554.37) * mm, "end": v(-62.57, 552.72) * mm});
            skLineSegment(sketch, "E614", {"start": v(-62.57, 552.72) * mm, "end": v(-75.68, 550.97) * mm});
            skLineSegment(sketch, "E615", {"start": v(-75.68, 550.97) * mm, "end": v(-89.04, 549.17) * mm});
            skLineSegment(sketch, "E616", {"start": v(-89.04, 549.17) * mm, "end": v(-102.45, 547.36) * mm});
            skLineSegment(sketch, "E617", {"start": v(-102.45, 547.36) * mm, "end": v(-115.75, 545.6) * mm});
            skLineSegment(sketch, "E618", {"start": v(-115.75, 545.6) * mm, "end": v(-128.77, 543.91) * mm});
            skLineSegment(sketch, "E619", {"start": v(-128.77, 543.91) * mm, "end": v(-141.33, 542.36) * mm});
            skLineSegment(sketch, "E620", {"start": v(-141.33, 542.36) * mm, "end": v(-153.24, 540.97) * mm});
            skLineSegment(sketch, "E621", {"start": v(-153.24, 540.97) * mm, "end": v(-164.35, 539.8) * mm});
            skLineSegment(sketch, "E622", {"start": v(-164.35, 539.8) * mm, "end": v(-174.47, 538.89) * mm});
            skLineSegment(sketch, "E623", {"start": v(-174.47, 538.89) * mm, "end": v(-183.42, 538.27) * mm});
            skLineSegment(sketch, "E624", {"start": v(-183.42, 538.27) * mm, "end": v(-191.04, 538) * mm});
            skLineSegment(sketch, "E625", {"start": v(-191.04, 538) * mm, "end": v(-195.63, 538.03) * mm});
            skLineSegment(sketch, "E626", {"start": v(-195.63, 538.03) * mm, "end": v(-197.15, 538.12) * mm});
            skLineSegment(sketch, "E627", {"start": v(-197.15, 538.12) * mm, "end": v(-199.72, 538.29) * mm});
            skLineSegment(sketch, "E628", {"start": v(-199.72, 538.29) * mm, "end": v(-207.42, 538.82) * mm});
            skLineSegment(sketch, "E629", {"start": v(-207.42, 538.82) * mm, "end": v(-217.24, 539.6) * mm});
            skLineSegment(sketch, "E630", {"start": v(-217.24, 539.6) * mm, "end": v(-226.84, 540.47) * mm});
            skLineSegment(sketch, "E631", {"start": v(-226.84, 540.47) * mm, "end": v(-236.47, 541.48) * mm});
            skLineSegment(sketch, "E632", {"start": v(-236.47, 541.48) * mm, "end": v(-246.36, 542.64) * mm});
            skLineSegment(sketch, "E633", {"start": v(-246.36, 542.64) * mm, "end": v(-256.76, 543.96) * mm});
            skLineSegment(sketch, "E634", {"start": v(-256.76, 543.96) * mm, "end": v(-267.9, 545.48) * mm});
            skLineSegment(sketch, "E635", {"start": v(-267.9, 545.48) * mm, "end": v(-277, 546.78) * mm});
            skLineSegment(sketch, "E636", {"start": v(-277, 546.78) * mm, "end": v(-280.03, 547.22) * mm});
            skLineSegment(sketch, "E637", {"start": v(-280.03, 547.22) * mm, "end": v(-281.56, 547.44) * mm});
            skLineSegment(sketch, "E638", {"start": v(-281.56, 547.44) * mm, "end": v(-286.13, 548.24) * mm});
            skLineSegment(sketch, "E639", {"start": v(-286.13, 548.24) * mm, "end": v(-291.78, 549.4) * mm});
            skLineSegment(sketch, "E640", {"start": v(-291.78, 549.4) * mm, "end": v(-296.97, 550.71) * mm});
            skLineSegment(sketch, "E641", {"start": v(-296.97, 550.71) * mm, "end": v(-301.74, 552.12) * mm});
            skLineSegment(sketch, "E642", {"start": v(-301.74, 552.12) * mm, "end": v(-306.11, 553.6) * mm});
            skLineSegment(sketch, "E643", {"start": v(-306.11, 553.6) * mm, "end": v(-310.11, 555.1) * mm});
            skLineSegment(sketch, "E644", {"start": v(-310.11, 555.1) * mm, "end": v(-313.76, 556.63) * mm});
            skLineSegment(sketch, "E645", {"start": v(-313.76, 556.63) * mm, "end": v(-317.09, 558.13) * mm});
            skLineSegment(sketch, "E646", {"start": v(-317.09, 558.13) * mm, "end": v(-320.1, 559.57) * mm});
            skLineSegment(sketch, "E647", {"start": v(-320.1, 559.57) * mm, "end": v(-322.85, 560.94) * mm});
            skLineSegment(sketch, "E648", {"start": v(-322.85, 560.94) * mm, "end": v(-325.34, 562.2) * mm});
            skLineSegment(sketch, "E649", {"start": v(-325.34, 562.2) * mm, "end": v(-327.6, 563.3) * mm});
            skLineSegment(sketch, "E650", {"start": v(-327.6, 563.3) * mm, "end": v(-329.65, 564.24) * mm});
            skLineSegment(sketch, "E651", {"start": v(-329.65, 564.24) * mm, "end": v(-331.52, 564.98) * mm});
            skLineSegment(sketch, "E652", {"start": v(-331.52, 564.98) * mm, "end": v(-333.22, 565.48) * mm});
            skLineSegment(sketch, "E653", {"start": v(-333.22, 565.48) * mm, "end": v(-334.4, 565.7) * mm});
            skLineSegment(sketch, "E654", {"start": v(-334.4, 565.7) * mm, "end": v(-334.8, 565.72) * mm});
            skLineSegment(sketch, "E655", {"start": v(-334.8, 565.72) * mm, "end": v(-335.6, 565.77) * mm});
            skLineSegment(sketch, "E656", {"start": v(-335.6, 565.77) * mm, "end": v(-338.01, 565.72) * mm});
            skLineSegment(sketch, "E657", {"start": v(-338.01, 565.72) * mm, "end": v(-341.56, 565.4) * mm});
            skLineSegment(sketch, "E658", {"start": v(-341.56, 565.4) * mm, "end": v(-345.35, 564.86) * mm});
            skLineSegment(sketch, "E659", {"start": v(-345.35, 564.86) * mm, "end": v(-349.32, 564.22) * mm});
            skLineSegment(sketch, "E660", {"start": v(-349.32, 564.22) * mm, "end": v(-353.4, 563.59) * mm});
            skLineSegment(sketch, "E661", {"start": v(-353.4, 563.59) * mm, "end": v(-357.48, 563.07) * mm});
            skLineSegment(sketch, "E662", {"start": v(-357.48, 563.07) * mm, "end": v(-361.52, 562.78) * mm});
            skLineSegment(sketch, "E663", {"start": v(-361.52, 562.78) * mm, "end": v(-364.45, 562.75) * mm});
            skLineSegment(sketch, "E664", {"start": v(-364.45, 562.75) * mm, "end": v(-365.42, 562.82) * mm});
            skLineSegment(sketch, "E665", {"start": v(-365.42, 562.82) * mm, "end": v(-366.65, 562.9) * mm});
            skLineSegment(sketch, "E666", {"start": v(-366.65, 562.9) * mm, "end": v(-370.31, 563.34) * mm});
            skLineSegment(sketch, "E667", {"start": v(-370.31, 563.34) * mm, "end": v(-377.34, 564.4) * mm});
            skLineSegment(sketch, "E668", {"start": v(-377.34, 564.4) * mm, "end": v(-386.5, 565.94) * mm});
            skLineSegment(sketch, "E669", {"start": v(-386.5, 565.94) * mm, "end": v(-397.76, 567.95) * mm});
            skLineSegment(sketch, "E670", {"start": v(-397.76, 567.95) * mm, "end": v(-411.1, 570.4) * mm});
            skLineSegment(sketch, "E671", {"start": v(-411.1, 570.4) * mm, "end": v(-426.52, 573.25) * mm});
            skLineSegment(sketch, "E672", {"start": v(-426.52, 573.25) * mm, "end": v(-443.99, 576.48) * mm});
            skLineSegment(sketch, "E673", {"start": v(-443.99, 576.48) * mm, "end": v(-458.61, 579.15) * mm});
            skLineSegment(sketch, "E674", {"start": v(-458.61, 579.15) * mm, "end": v(-463.48, 580.04) * mm});
            skLineSegment(sketch, "E675", {"start": v(-463.48, 580.04) * mm, "end": v(-465.79, 580.46) * mm});
            skLineSegment(sketch, "E676", {"start": v(-465.79, 580.46) * mm, "end": v(-472.69, 581.75) * mm});
            skLineSegment(sketch, "E677", {"start": v(-472.69, 581.75) * mm, "end": v(-479.98, 583.18) * mm});
            skLineSegment(sketch, "E678", {"start": v(-479.98, 583.18) * mm, "end": v(-485.63, 584.36) * mm});
            skLineSegment(sketch, "E679", {"start": v(-485.63, 584.36) * mm, "end": v(-489.93, 585.32) * mm});
            skLineSegment(sketch, "E680", {"start": v(-489.93, 585.32) * mm, "end": v(-493.16, 586.1) * mm});
            skLineSegment(sketch, "E681", {"start": v(-493.16, 586.1) * mm, "end": v(-495.59, 586.74) * mm});
            skLineSegment(sketch, "E682", {"start": v(-495.59, 586.74) * mm, "end": v(-497.5, 587.27) * mm});
            skLineSegment(sketch, "E683", {"start": v(-497.5, 587.27) * mm, "end": v(-499.2, 587.72) * mm});
            skLineSegment(sketch, "E684", {"start": v(-499.2, 587.72) * mm, "end": v(-500.93, 588.12) * mm});
            skLineSegment(sketch, "E685", {"start": v(-500.93, 588.12) * mm, "end": v(-503, 588.51) * mm});
            skLineSegment(sketch, "E686", {"start": v(-503, 588.51) * mm, "end": v(-505.68, 588.93) * mm});
            skLineSegment(sketch, "E687", {"start": v(-505.68, 588.93) * mm, "end": v(-509.24, 589.41) * mm});
            skLineSegment(sketch, "E688", {"start": v(-509.24, 589.41) * mm, "end": v(-513.98, 590) * mm});
            skLineSegment(sketch, "E689", {"start": v(-513.98, 590) * mm, "end": v(-520.17, 590.69) * mm});
            skLineSegment(sketch, "E690", {"start": v(-520.17, 590.69) * mm, "end": v(-528.08, 591.56) * mm});
            skLineSegment(sketch, "E691", {"start": v(-528.08, 591.56) * mm, "end": v(-535.53, 592.35) * mm});
            skLineSegment(sketch, "E692", {"start": v(-535.53, 592.35) * mm, "end": v(-538.01, 592.61) * mm});
            skLineSegment(sketch, "E693", {"start": v(-538.01, 592.61) * mm, "end": v(-596.84, 598.87) * mm});
            skLineSegment(sketch, "E694", {"start": v(607.08, 410.28) * mm, "end": v(604.55, 409.62) * mm});
            skLineSegment(sketch, "E695", {"start": v(604.55, 409.62) * mm, "end": v(596.9, 407.85) * mm});
            skLineSegment(sketch, "E696", {"start": v(596.9, 407.85) * mm, "end": v(587.07, 405.92) * mm});
            skLineSegment(sketch, "E697", {"start": v(587.07, 405.92) * mm, "end": v(577.56, 404.4) * mm});
            skLineSegment(sketch, "E698", {"start": v(577.56, 404.4) * mm, "end": v(568.32, 403.17) * mm});
            skLineSegment(sketch, "E699", {"start": v(568.32, 403.17) * mm, "end": v(559.3, 402.12) * mm});
            skLineSegment(sketch, "E700", {"start": v(559.3, 402.12) * mm, "end": v(550.5, 401.15) * mm});
            skLineSegment(sketch, "E701", {"start": v(550.5, 401.15) * mm, "end": v(541.82, 400.14) * mm});
            skLineSegment(sketch, "E702", {"start": v(541.82, 400.14) * mm, "end": v(535.4, 399.3) * mm});
            skLineSegment(sketch, "E703", {"start": v(535.4, 399.3) * mm, "end": v(533.26, 398.98) * mm});
            skLineSegment(sketch, "E704", {"start": v(533.26, 398.98) * mm, "end": v(531.32, 398.7) * mm});
            skLineSegment(sketch, "E705", {"start": v(531.32, 398.7) * mm, "end": v(525.56, 397.55) * mm});
            skLineSegment(sketch, "E706", {"start": v(525.56, 397.55) * mm, "end": v(519.28, 395.9) * mm});
            skLineSegment(sketch, "E707", {"start": v(519.28, 395.9) * mm, "end": v(514.07, 394.18) * mm});
            skLineSegment(sketch, "E708", {"start": v(514.07, 394.18) * mm, "end": v(509.58, 392.56) * mm});
            skLineSegment(sketch, "E709", {"start": v(509.58, 392.56) * mm, "end": v(505.46, 391.22) * mm});
            skLineSegment(sketch, "E710", {"start": v(505.46, 391.22) * mm, "end": v(501.36, 390.31) * mm});
            skLineSegment(sketch, "E711", {"start": v(501.36, 390.31) * mm, "end": v(496.94, 390) * mm});
            skLineSegment(sketch, "E712", {"start": v(496.94, 390) * mm, "end": v(493.1, 390.24) * mm});
            skLineSegment(sketch, "E713", {"start": v(493.1, 390.24) * mm, "end": v(491.83, 390.44) * mm});
            skLineSegment(sketch, "E714", {"start": v(491.83, 390.44) * mm, "end": v(490.95, 390.58) * mm});
            skLineSegment(sketch, "E715", {"start": v(490.95, 390.58) * mm, "end": v(488.34, 391.12) * mm});
            skLineSegment(sketch, "E716", {"start": v(488.34, 391.12) * mm, "end": v(483.5, 392.29) * mm});
            skLineSegment(sketch, "E717", {"start": v(483.5, 392.29) * mm, "end": v(477.47, 393.94) * mm});
            skLineSegment(sketch, "E718", {"start": v(477.47, 393.94) * mm, "end": v(470.4, 396.09) * mm});
            skLineSegment(sketch, "E719", {"start": v(470.4, 396.09) * mm, "end": v(462.46, 398.73) * mm});
            skLineSegment(sketch, "E720", {"start": v(462.46, 398.73) * mm, "end": v(453.77, 401.87) * mm});
            skLineSegment(sketch, "E721", {"start": v(453.77, 401.87) * mm, "end": v(444.5, 405.51) * mm});
            skLineSegment(sketch, "E722", {"start": v(444.5, 405.51) * mm, "end": v(434.82, 409.66) * mm});
            skLineSegment(sketch, "E723", {"start": v(434.82, 409.66) * mm, "end": v(424.84, 414.3) * mm});
            skLineSegment(sketch, "E724", {"start": v(424.84, 414.3) * mm, "end": v(414.74, 419.48) * mm});
            skLineSegment(sketch, "E725", {"start": v(414.74, 419.48) * mm, "end": v(404.67, 425.16) * mm});
            skLineSegment(sketch, "E726", {"start": v(404.67, 425.16) * mm, "end": v(394.77, 431.35) * mm});
            skLineSegment(sketch, "E727", {"start": v(394.77, 431.35) * mm, "end": v(385.2, 438.07) * mm});
            skLineSegment(sketch, "E728", {"start": v(385.2, 438.07) * mm, "end": v(376.1, 445.3) * mm});
            skLineSegment(sketch, "E729", {"start": v(376.1, 445.3) * mm, "end": v(367.65, 453.07) * mm});
            skLineSegment(sketch, "E730", {"start": v(367.65, 453.07) * mm, "end": v(361.8, 459.22) * mm});
            skLineSegment(sketch, "E731", {"start": v(361.8, 459.22) * mm, "end": v(359.97, 461.37) * mm});
            skLineSegment(sketch, "E732", {"start": v(359.97, 461.37) * mm, "end": v(359.03, 462.49) * mm});
            skLineSegment(sketch, "E733", {"start": v(359.03, 462.49) * mm, "end": v(356.1, 465.77) * mm});
            skLineSegment(sketch, "E734", {"start": v(356.1, 465.77) * mm, "end": v(351.58, 470.6) * mm});
            skLineSegment(sketch, "E735", {"start": v(351.58, 470.6) * mm, "end": v(346.5, 475.8) * mm});
            skLineSegment(sketch, "E736", {"start": v(346.5, 475.8) * mm, "end": v(340.98, 481.23) * mm});
            skLineSegment(sketch, "E737", {"start": v(340.98, 481.23) * mm, "end": v(335.1, 486.83) * mm});
            skLineSegment(sketch, "E738", {"start": v(335.1, 486.83) * mm, "end": v(328.97, 492.5) * mm});
            skLineSegment(sketch, "E739", {"start": v(328.97, 492.5) * mm, "end": v(322.69, 498.14) * mm});
            skLineSegment(sketch, "E740", {"start": v(322.69, 498.14) * mm, "end": v(316.35, 503.68) * mm});
            skLineSegment(sketch, "E741", {"start": v(316.35, 503.68) * mm, "end": v(310.06, 509) * mm});
            skLineSegment(sketch, "E742", {"start": v(310.06, 509) * mm, "end": v(303.93, 514.04) * mm});
            skLineSegment(sketch, "E743", {"start": v(303.93, 514.04) * mm, "end": v(298.04, 518.7) * mm});
            skLineSegment(sketch, "E744", {"start": v(298.04, 518.7) * mm, "end": v(292.5, 522.85) * mm});
            skLineSegment(sketch, "E745", {"start": v(292.5, 522.85) * mm, "end": v(287.43, 526.45) * mm});
            skLineSegment(sketch, "E746", {"start": v(287.43, 526.45) * mm, "end": v(282.9, 529.38) * mm});
            skLineSegment(sketch, "E747", {"start": v(282.9, 529.38) * mm, "end": v(279.02, 531.56) * mm});
            skLineSegment(sketch, "E748", {"start": v(279.02, 531.56) * mm, "end": v(276.7, 532.63) * mm});
            skLineSegment(sketch, "E749", {"start": v(276.7, 532.63) * mm, "end": v(275.89, 532.88) * mm});
            skLineSegment(sketch, "E750", {"start": v(275.89, 532.88) * mm, "end": v(275.12, 533.13) * mm});
            skLineSegment(sketch, "E751", {"start": v(275.12, 533.13) * mm, "end": v(272.76, 533.74) * mm});
            skLineSegment(sketch, "E752", {"start": v(272.76, 533.74) * mm, "end": v(268.88, 534.56) * mm});
            skLineSegment(sketch, "E753", {"start": v(268.88, 534.56) * mm, "end": v(264.35, 535.34) * mm});
            skLineSegment(sketch, "E754", {"start": v(264.35, 535.34) * mm, "end": v(259.3, 536.1) * mm});
            skLineSegment(sketch, "E755", {"start": v(259.3, 536.1) * mm, "end": v(253.82, 536.83) * mm});
            skLineSegment(sketch, "E756", {"start": v(253.82, 536.83) * mm, "end": v(248.03, 537.55) * mm});
            skLineSegment(sketch, "E757", {"start": v(248.03, 537.55) * mm, "end": v(242.04, 538.26) * mm});
            skLineSegment(sketch, "E758", {"start": v(242.04, 538.26) * mm, "end": v(235.96, 538.96) * mm});
            skLineSegment(sketch, "E759", {"start": v(235.96, 538.96) * mm, "end": v(229.9, 539.67) * mm});
            skLineSegment(sketch, "E760", {"start": v(229.9, 539.67) * mm, "end": v(223.97, 540.38) * mm});
            skLineSegment(sketch, "E761", {"start": v(223.97, 540.38) * mm, "end": v(218.28, 541.1) * mm});
            skLineSegment(sketch, "E762", {"start": v(218.28, 541.1) * mm, "end": v(212.95, 541.84) * mm});
            skLineSegment(sketch, "E763", {"start": v(212.95, 541.84) * mm, "end": v(208.07, 542.6) * mm});
            skLineSegment(sketch, "E764", {"start": v(208.07, 542.6) * mm, "end": v(203.76, 543.4) * mm});
            skLineSegment(sketch, "E765", {"start": v(203.76, 543.4) * mm, "end": v(200.13, 544.24) * mm});
            skLineSegment(sketch, "E766", {"start": v(200.13, 544.24) * mm, "end": v(197.99, 544.85) * mm});
            skLineSegment(sketch, "E767", {"start": v(197.99, 544.85) * mm, "end": v(197.3, 545.1) * mm});
            skLineSegment(sketch, "E768", {"start": v(197.3, 545.1) * mm, "end": v(195.99, 545.6) * mm});
            skLineSegment(sketch, "E769", {"start": v(195.99, 545.6) * mm, "end": v(192.1, 547.18) * mm});
            skLineSegment(sketch, "E770", {"start": v(192.1, 547.18) * mm, "end": v(186.21, 549.68) * mm});
            skLineSegment(sketch, "E771", {"start": v(186.21, 549.68) * mm, "end": v(179.85, 552.42) * mm});
            skLineSegment(sketch, "E772", {"start": v(179.85, 552.42) * mm, "end": v(173.2, 555.19) * mm});
            skLineSegment(sketch, "E773", {"start": v(173.2, 555.19) * mm, "end": v(166.43, 557.77) * mm});
            skLineSegment(sketch, "E774", {"start": v(166.43, 557.77) * mm, "end": v(159.75, 559.98) * mm});
            skLineSegment(sketch, "E775", {"start": v(159.75, 559.98) * mm, "end": v(153.34, 561.61) * mm});
            skLineSegment(sketch, "E776", {"start": v(153.34, 561.61) * mm, "end": v(148.88, 562.35) * mm});
            skLineSegment(sketch, "E777", {"start": v(148.88, 562.35) * mm, "end": v(147.39, 562.45) * mm});
            skLineSegment(sketch, "E778", {"start": v(147.39, 562.45) * mm, "end": v(146.38, 562.52) * mm});
            skLineSegment(sketch, "E779", {"start": v(146.38, 562.52) * mm, "end": v(143.34, 562.5) * mm});
            skLineSegment(sketch, "E780", {"start": v(143.34, 562.5) * mm, "end": v(137.03, 562.3) * mm});
            skLineSegment(sketch, "E781", {"start": v(137.03, 562.3) * mm, "end": v(128.72, 561.87) * mm});
            skLineSegment(sketch, "E782", {"start": v(128.72, 561.87) * mm, "end": v(118.69, 561.2) * mm});
            skLineSegment(sketch, "E783", {"start": v(118.69, 561.2) * mm, "end": v(107.17, 560.34) * mm});
            skLineSegment(sketch, "E784", {"start": v(107.17, 560.34) * mm, "end": v(94.45, 559.3) * mm});
            skLineSegment(sketch, "E785", {"start": v(94.45, 559.3) * mm, "end": v(80.8, 558.09) * mm});
            skLineSegment(sketch, "E786", {"start": v(80.8, 558.09) * mm, "end": v(66.45, 556.73) * mm});
            skLineSegment(sketch, "E787", {"start": v(66.45, 556.73) * mm, "end": v(51.69, 555.25) * mm});
            skLineSegment(sketch, "E788", {"start": v(51.69, 555.25) * mm, "end": v(36.77, 553.66) * mm});
            skLineSegment(sketch, "E789", {"start": v(36.77, 553.66) * mm, "end": v(21.97, 552) * mm});
            skLineSegment(sketch, "E790", {"start": v(21.97, 552) * mm, "end": v(7.53, 550.24) * mm});
            skLineSegment(sketch, "E791", {"start": v(7.53, 550.24) * mm, "end": v(-6.26, 548.44) * mm});
            skLineSegment(sketch, "E792", {"start": v(-6.26, 548.44) * mm, "end": v(-19.17, 546.62) * mm});
            skLineSegment(sketch, "E793", {"start": v(-19.17, 546.62) * mm, "end": v(-30.9, 544.77) * mm});
            skLineSegment(sketch, "E794", {"start": v(-30.9, 544.77) * mm, "end": v(-38.64, 543.43) * mm});
            skLineSegment(sketch, "E795", {"start": v(-38.64, 543.43) * mm, "end": v(-41.22, 542.93) * mm});
            skLineSegment(sketch, "E796", {"start": v(-41.22, 542.93) * mm, "end": v(-43.76, 542.45) * mm});
            skLineSegment(sketch, "E797", {"start": v(-43.76, 542.45) * mm, "end": v(-51.4, 541.13) * mm});
            skLineSegment(sketch, "E798", {"start": v(-51.4, 541.13) * mm, "end": v(-62.8, 539.38) * mm});
            skLineSegment(sketch, "E799", {"start": v(-62.8, 539.38) * mm, "end": v(-75.22, 537.69) * mm});
            skLineSegment(sketch, "E800", {"start": v(-75.22, 537.69) * mm, "end": v(-88.48, 536.08) * mm});
            skLineSegment(sketch, "E801", {"start": v(-88.48, 536.08) * mm, "end": v(-102.38, 534.56) * mm});
            skLineSegment(sketch, "E802", {"start": v(-102.38, 534.56) * mm, "end": v(-116.75, 533.13) * mm});
            skLineSegment(sketch, "E803", {"start": v(-116.75, 533.13) * mm, "end": v(-131.4, 531.8) * mm});
            skLineSegment(sketch, "E804", {"start": v(-131.4, 531.8) * mm, "end": v(-146.1, 530.6) * mm});
            skLineSegment(sketch, "E805", {"start": v(-146.1, 530.6) * mm, "end": v(-160.72, 529.51) * mm});
            skLineSegment(sketch, "E806", {"start": v(-160.72, 529.51) * mm, "end": v(-175.04, 528.56) * mm});
            skLineSegment(sketch, "E807", {"start": v(-175.04, 528.56) * mm, "end": v(-188.86, 527.76) * mm});
            skLineSegment(sketch, "E808", {"start": v(-188.86, 527.76) * mm, "end": v(-202.02, 527.12) * mm});
            skLineSegment(sketch, "E809", {"start": v(-202.02, 527.12) * mm, "end": v(-214.32, 526.65) * mm});
            skLineSegment(sketch, "E810", {"start": v(-214.32, 526.65) * mm, "end": v(-225.56, 526.35) * mm});
            skLineSegment(sketch, "E811", {"start": v(-225.56, 526.35) * mm, "end": v(-235.56, 526.23) * mm});
            skLineSegment(sketch, "E812", {"start": v(-235.56, 526.23) * mm, "end": v(-241.99, 526.26) * mm});
            skLineSegment(sketch, "E813", {"start": v(-241.99, 526.26) * mm, "end": v(-244.13, 526.31) * mm});
            skLineSegment(sketch, "E814", {"start": v(-244.13, 526.31) * mm, "end": v(-245.98, 526.36) * mm});
            skLineSegment(sketch, "E815", {"start": v(-245.98, 526.36) * mm, "end": v(-251.52, 526.55) * mm});
            skLineSegment(sketch, "E816", {"start": v(-251.52, 526.55) * mm, "end": v(-258.3, 526.87) * mm});
            skLineSegment(sketch, "E817", {"start": v(-258.3, 526.87) * mm, "end": v(-264.49, 527.27) * mm});
            skLineSegment(sketch, "E818", {"start": v(-264.49, 527.27) * mm, "end": v(-270.14, 527.74) * mm});
            skLineSegment(sketch, "E819", {"start": v(-270.14, 527.74) * mm, "end": v(-275.28, 528.27) * mm});
            skLineSegment(sketch, "E820", {"start": v(-275.28, 528.27) * mm, "end": v(-279.96, 528.85) * mm});
            skLineSegment(sketch, "E821", {"start": v(-279.96, 528.85) * mm, "end": v(-284.2, 529.48) * mm});
            skLineSegment(sketch, "E822", {"start": v(-284.2, 529.48) * mm, "end": v(-288.03, 530.14) * mm});
            skLineSegment(sketch, "E823", {"start": v(-288.03, 530.14) * mm, "end": v(-291.5, 530.82) * mm});
            skLineSegment(sketch, "E824", {"start": v(-291.5, 530.82) * mm, "end": v(-294.62, 531.52) * mm});
            skLineSegment(sketch, "E825", {"start": v(-294.62, 531.52) * mm, "end": v(-297.46, 532.23) * mm});
            skLineSegment(sketch, "E826", {"start": v(-297.46, 532.23) * mm, "end": v(-300.03, 532.93) * mm});
            skLineSegment(sketch, "E827", {"start": v(-300.03, 532.93) * mm, "end": v(-302.38, 533.62) * mm});
            skLineSegment(sketch, "E828", {"start": v(-302.38, 533.62) * mm, "end": v(-304.53, 534.3) * mm});
            skLineSegment(sketch, "E829", {"start": v(-304.53, 534.3) * mm, "end": v(-306.53, 534.94) * mm});
            skLineSegment(sketch, "E830", {"start": v(-306.53, 534.94) * mm, "end": v(-307.93, 535.4) * mm});
            skLineSegment(sketch, "E831", {"start": v(-307.93, 535.4) * mm, "end": v(-308.4, 535.54) * mm});
            skLineSegment(sketch, "E832", {"start": v(-308.4, 535.54) * mm, "end": v(-309.27, 535.81) * mm});
            skLineSegment(sketch, "E833", {"start": v(-309.27, 535.81) * mm, "end": v(-311.8, 536.83) * mm});
            skLineSegment(sketch, "E834", {"start": v(-311.8, 536.83) * mm, "end": v(-315.25, 538.49) * mm});
            skLineSegment(sketch, "E835", {"start": v(-315.25, 538.49) * mm, "end": v(-318.78, 540.38) * mm});
            skLineSegment(sketch, "E836", {"start": v(-318.78, 540.38) * mm, "end": v(-322.44, 542.39) * mm});
            skLineSegment(sketch, "E837", {"start": v(-322.44, 542.39) * mm, "end": v(-326.3, 544.4) * mm});
            skLineSegment(sketch, "E838", {"start": v(-326.3, 544.4) * mm, "end": v(-330.38, 546.3) * mm});
            skLineSegment(sketch, "E839", {"start": v(-330.38, 546.3) * mm, "end": v(-334.76, 547.95) * mm});
            skLineSegment(sketch, "E840", {"start": v(-334.76, 547.95) * mm, "end": v(-338.29, 549) * mm});
            skLineSegment(sketch, "E841", {"start": v(-338.29, 549) * mm, "end": v(-339.47, 549.25) * mm});
            skLineSegment(sketch, "E842", {"start": v(-339.47, 549.25) * mm, "end": v(-340.22, 549.42) * mm});
            skLineSegment(sketch, "E843", {"start": v(-340.22, 549.42) * mm, "end": v(-342.47, 549.75) * mm});
            skLineSegment(sketch, "E844", {"start": v(-342.47, 549.75) * mm, "end": v(-345.44, 549.95) * mm});
            skLineSegment(sketch, "E845", {"start": v(-345.44, 549.95) * mm, "end": v(-348.5, 549.93) * mm});
            skLineSegment(sketch, "E846", {"start": v(-348.5, 549.93) * mm, "end": v(-351.8, 549.76) * mm});
            skLineSegment(sketch, "E847", {"start": v(-351.8, 549.76) * mm, "end": v(-355.5, 549.54) * mm});
            skLineSegment(sketch, "E848", {"start": v(-355.5, 549.54) * mm, "end": v(-359.68, 549.33) * mm});
            skLineSegment(sketch, "E849", {"start": v(-359.68, 549.33) * mm, "end": v(-364.51, 549.2) * mm});
            skLineSegment(sketch, "E850", {"start": v(-364.51, 549.2) * mm, "end": v(-368.72, 549.22) * mm});
            skLineSegment(sketch, "E851", {"start": v(-368.72, 549.22) * mm, "end": v(-370.12, 549.25) * mm});
            skLineSegment(sketch, "E852", {"start": v(-370.12, 549.25) * mm, "end": v(-370.6, 549.26) * mm});
            skLineSegment(sketch, "E853", {"start": v(-370.6, 549.26) * mm, "end": v(-372.06, 549.4) * mm});
            skLineSegment(sketch, "E854", {"start": v(-372.06, 549.4) * mm, "end": v(-374.82, 549.73) * mm});
            skLineSegment(sketch, "E855", {"start": v(-374.82, 549.73) * mm, "end": v(-378.35, 550.24) * mm});
            skLineSegment(sketch, "E856", {"start": v(-378.35, 550.24) * mm, "end": v(-382.6, 550.92) * mm});
            skLineSegment(sketch, "E857", {"start": v(-382.6, 550.92) * mm, "end": v(-387.53, 551.75) * mm});
            skLineSegment(sketch, "E858", {"start": v(-387.53, 551.75) * mm, "end": v(-393.08, 552.72) * mm});
            skLineSegment(sketch, "E859", {"start": v(-393.08, 552.72) * mm, "end": v(-399.2, 553.81) * mm});
            skLineSegment(sketch, "E860", {"start": v(-399.2, 553.81) * mm, "end": v(-405.84, 555.02) * mm});
            skLineSegment(sketch, "E861", {"start": v(-405.84, 555.02) * mm, "end": v(-412.96, 556.33) * mm});
            skLineSegment(sketch, "E862", {"start": v(-412.96, 556.33) * mm, "end": v(-420.5, 557.73) * mm});
            skLineSegment(sketch, "E863", {"start": v(-420.5, 557.73) * mm, "end": v(-428.42, 559.2) * mm});
            skLineSegment(sketch, "E864", {"start": v(-428.42, 559.2) * mm, "end": v(-436.67, 560.72) * mm});
            skLineSegment(sketch, "E865", {"start": v(-436.67, 560.72) * mm, "end": v(-445.19, 562.3) * mm});
            skLineSegment(sketch, "E866", {"start": v(-445.19, 562.3) * mm, "end": v(-453.93, 563.91) * mm});
            skLineSegment(sketch, "E867", {"start": v(-453.93, 563.91) * mm, "end": v(-462.86, 565.54) * mm});
            skLineSegment(sketch, "E868", {"start": v(-462.86, 565.54) * mm, "end": v(-471.91, 567.18) * mm});
            skLineSegment(sketch, "E869", {"start": v(-471.91, 567.18) * mm, "end": v(-481.04, 568.81) * mm});
            skLineSegment(sketch, "E870", {"start": v(-481.04, 568.81) * mm, "end": v(-490.2, 570.43) * mm});
            skLineSegment(sketch, "E871", {"start": v(-490.2, 570.43) * mm, "end": v(-499.34, 572) * mm});
            skLineSegment(sketch, "E872", {"start": v(-499.34, 572) * mm, "end": v(-508.41, 573.55) * mm});
            skLineSegment(sketch, "E873", {"start": v(-508.41, 573.55) * mm, "end": v(-517.37, 575.03) * mm});
            skLineSegment(sketch, "E874", {"start": v(-517.37, 575.03) * mm, "end": v(-526.15, 576.43) * mm});
            skLineSegment(sketch, "E875", {"start": v(-526.15, 576.43) * mm, "end": v(-534.7, 577.76) * mm});
            skLineSegment(sketch, "E876", {"start": v(-534.7, 577.76) * mm, "end": v(-543, 578.98) * mm});
            skLineSegment(sketch, "E877", {"start": v(-543, 578.98) * mm, "end": v(-550.98, 580.1) * mm});
            skLineSegment(sketch, "E878", {"start": v(-550.98, 580.1) * mm, "end": v(-558.6, 581.08) * mm});
            skLineSegment(sketch, "E879", {"start": v(-558.6, 581.08) * mm, "end": v(-565.78, 581.93) * mm});
            skLineSegment(sketch, "E880", {"start": v(-565.78, 581.93) * mm, "end": v(-572.51, 582.64) * mm});
            skLineSegment(sketch, "E881", {"start": v(-572.51, 582.64) * mm, "end": v(-578.72, 583.17) * mm});
            skLineSegment(sketch, "E882", {"start": v(-578.72, 583.17) * mm, "end": v(-584.37, 583.53) * mm});
            skLineSegment(sketch, "E883", {"start": v(-584.37, 583.53) * mm, "end": v(-589.4, 583.7) * mm});
            skLineSegment(sketch, "E884", {"start": v(-589.4, 583.7) * mm, "end": v(-592.68, 583.7) * mm});
            skLineSegment(sketch, "E885", {"start": v(-592.68, 583.7) * mm, "end": v(-593.77, 583.67) * mm});
            skLineSegment(sketch, "E886", {"start": v(608.33, 377.68) * mm, "end": v(607.14, 377.33) * mm});
            skLineSegment(sketch, "E887", {"start": v(607.14, 377.33) * mm, "end": v(603.56, 376.28) * mm});
            skLineSegment(sketch, "E888", {"start": v(603.56, 376.28) * mm, "end": v(598.04, 374.67) * mm});
            skLineSegment(sketch, "E889", {"start": v(598.04, 374.67) * mm, "end": v(591.87, 372.91) * mm});
            skLineSegment(sketch, "E890", {"start": v(591.87, 372.91) * mm, "end": v(585.11, 371.08) * mm});
            skLineSegment(sketch, "E891", {"start": v(585.11, 371.08) * mm, "end": v(577.84, 369.23) * mm});
            skLineSegment(sketch, "E892", {"start": v(577.84, 369.23) * mm, "end": v(570.13, 367.44) * mm});
            skLineSegment(sketch, "E893", {"start": v(570.13, 367.44) * mm, "end": v(562.07, 365.76) * mm});
            skLineSegment(sketch, "E894", {"start": v(562.07, 365.76) * mm, "end": v(553.72, 364.26) * mm});
            skLineSegment(sketch, "E895", {"start": v(553.72, 364.26) * mm, "end": v(545.16, 363.02) * mm});
            skLineSegment(sketch, "E896", {"start": v(545.16, 363.02) * mm, "end": v(536.46, 362.1) * mm});
            skLineSegment(sketch, "E897", {"start": v(536.46, 362.1) * mm, "end": v(527.72, 361.55) * mm});
            skLineSegment(sketch, "E898", {"start": v(527.72, 361.55) * mm, "end": v(518.98, 361.45) * mm});
            skLineSegment(sketch, "E899", {"start": v(518.98, 361.45) * mm, "end": v(510.35, 361.87) * mm});
            skLineSegment(sketch, "E900", {"start": v(510.35, 361.87) * mm, "end": v(501.87, 362.87) * mm});
            skLineSegment(sketch, "E901", {"start": v(501.87, 362.87) * mm, "end": v(493.65, 364.52) * mm});
            skLineSegment(sketch, "E902", {"start": v(493.65, 364.52) * mm, "end": v(487.68, 366.2) * mm});
            skLineSegment(sketch, "E903", {"start": v(487.68, 366.2) * mm, "end": v(485.74, 366.88) * mm});
            skLineSegment(sketch, "E904", {"start": v(485.74, 366.88) * mm, "end": v(483.79, 367.57) * mm});
            skLineSegment(sketch, "E905", {"start": v(483.79, 367.57) * mm, "end": v(477.92, 369.62) * mm});
            skLineSegment(sketch, "E906", {"start": v(477.92, 369.62) * mm, "end": v(469.9, 372.38) * mm});
            skLineSegment(sketch, "E907", {"start": v(469.9, 372.38) * mm, "end": v(461.71, 375.22) * mm});
            skLineSegment(sketch, "E908", {"start": v(461.71, 375.22) * mm, "end": v(453.38, 378.2) * mm});
            skLineSegment(sketch, "E909", {"start": v(453.38, 378.2) * mm, "end": v(444.92, 381.37) * mm});
            skLineSegment(sketch, "E910", {"start": v(444.92, 381.37) * mm, "end": v(436.35, 384.79) * mm});
            skLineSegment(sketch, "E911", {"start": v(436.35, 384.79) * mm, "end": v(427.7, 388.5) * mm});
            skLineSegment(sketch, "E912", {"start": v(427.7, 388.5) * mm, "end": v(418.97, 392.58) * mm});
            skLineSegment(sketch, "E913", {"start": v(418.97, 392.58) * mm, "end": v(410.2, 397.07) * mm});
            skLineSegment(sketch, "E914", {"start": v(410.2, 397.07) * mm, "end": v(401.42, 402.02) * mm});
            skLineSegment(sketch, "E915", {"start": v(401.42, 402.02) * mm, "end": v(392.63, 407.5) * mm});
            skLineSegment(sketch, "E916", {"start": v(392.63, 407.5) * mm, "end": v(383.86, 413.54) * mm});
            skLineSegment(sketch, "E917", {"start": v(383.86, 413.54) * mm, "end": v(375.14, 420.22) * mm});
            skLineSegment(sketch, "E918", {"start": v(375.14, 420.22) * mm, "end": v(366.47, 427.59) * mm});
            skLineSegment(sketch, "E919", {"start": v(366.47, 427.59) * mm, "end": v(357.88, 435.7) * mm});
            skLineSegment(sketch, "E920", {"start": v(357.88, 435.7) * mm, "end": v(351.46, 442.31) * mm});
            skLineSegment(sketch, "E921", {"start": v(351.46, 442.31) * mm, "end": v(349.4, 444.6) * mm});
            skLineSegment(sketch, "E922", {"start": v(349.4, 444.6) * mm, "end": v(348.47, 445.63) * mm});
            skLineSegment(sketch, "E923", {"start": v(348.47, 445.63) * mm, "end": v(345.85, 448.91) * mm});
            skLineSegment(sketch, "E924", {"start": v(345.85, 448.91) * mm, "end": v(342.17, 453.96) * mm});
            skLineSegment(sketch, "E925", {"start": v(342.17, 453.96) * mm, "end": v(338.43, 459.4) * mm});
            skLineSegment(sketch, "E926", {"start": v(338.43, 459.4) * mm, "end": v(334.68, 464.95) * mm});
            skLineSegment(sketch, "E927", {"start": v(334.68, 464.95) * mm, "end": v(330.95, 470.27) * mm});
            skLineSegment(sketch, "E928", {"start": v(330.95, 470.27) * mm, "end": v(327.3, 475.04) * mm});
            skLineSegment(sketch, "E929", {"start": v(327.3, 475.04) * mm, "end": v(323.78, 478.96) * mm});
            skLineSegment(sketch, "E930", {"start": v(323.78, 478.96) * mm, "end": v(321.33, 481.13) * mm});
            skLineSegment(sketch, "E931", {"start": v(321.33, 481.13) * mm, "end": v(320.43, 481.7) * mm});
            skLineSegment(sketch, "E932", {"start": v(320.43, 481.7) * mm, "end": v(319.54, 482.27) * mm});
            skLineSegment(sketch, "E933", {"start": v(319.54, 482.27) * mm, "end": v(316.87, 483.96) * mm});
            skLineSegment(sketch, "E934", {"start": v(316.87, 483.96) * mm, "end": v(312.67, 486.57) * mm});
            skLineSegment(sketch, "E935", {"start": v(312.67, 486.57) * mm, "end": v(307.78, 489.5) * mm});
            skLineSegment(sketch, "E936", {"start": v(307.78, 489.5) * mm, "end": v(302.19, 492.66) * mm});
            skLineSegment(sketch, "E937", {"start": v(302.19, 492.66) * mm, "end": v(295.85, 496.01) * mm});
            skLineSegment(sketch, "E938", {"start": v(295.85, 496.01) * mm, "end": v(288.74, 499.5) * mm});
            skLineSegment(sketch, "E939", {"start": v(288.74, 499.5) * mm, "end": v(280.82, 503.06) * mm});
            skLineSegment(sketch, "E940", {"start": v(280.82, 503.06) * mm, "end": v(274.27, 505.79) * mm});
            skLineSegment(sketch, "E941", {"start": v(274.27, 505.79) * mm, "end": v(272.07, 506.65) * mm});
            skLineSegment(sketch, "E942", {"start": v(272.07, 506.65) * mm, "end": v(269.86, 507.5) * mm});
            skLineSegment(sketch, "E943", {"start": v(269.86, 507.5) * mm, "end": v(263.18, 509.93) * mm});
            skLineSegment(sketch, "E944", {"start": v(263.18, 509.93) * mm, "end": v(254.82, 512.68) * mm});
            skLineSegment(sketch, "E945", {"start": v(254.82, 512.68) * mm, "end": v(246.91, 514.97) * mm});
            skLineSegment(sketch, "E946", {"start": v(246.91, 514.97) * mm, "end": v(239.38, 516.88) * mm});
            skLineSegment(sketch, "E947", {"start": v(239.38, 516.88) * mm, "end": v(232.12, 518.47) * mm});
            skLineSegment(sketch, "E948", {"start": v(232.12, 518.47) * mm, "end": v(225.05, 519.84) * mm});
            skLineSegment(sketch, "E949", {"start": v(225.05, 519.84) * mm, "end": v(218.1, 521.05) * mm});
            skLineSegment(sketch, "E950", {"start": v(218.1, 521.05) * mm, "end": v(212.9, 521.9) * mm});
            skLineSegment(sketch, "E951", {"start": v(212.9, 521.9) * mm, "end": v(211.16, 522.17) * mm});
            skLineSegment(sketch, "E952", {"start": v(211.16, 522.17) * mm, "end": v(209.34, 522.46) * mm});
            skLineSegment(sketch, "E953", {"start": v(209.34, 522.46) * mm, "end": v(203.93, 523.8) * mm});
            skLineSegment(sketch, "E954", {"start": v(203.93, 523.8) * mm, "end": v(196.27, 526.29) * mm});
            skLineSegment(sketch, "E955", {"start": v(196.27, 526.29) * mm, "end": v(188.36, 529.4) * mm});
            skLineSegment(sketch, "E956", {"start": v(188.36, 529.4) * mm, "end": v(180.4, 532.84) * mm});
            skLineSegment(sketch, "E957", {"start": v(180.4, 532.84) * mm, "end": v(172.6, 536.38) * mm});
            skLineSegment(sketch, "E958", {"start": v(172.6, 536.38) * mm, "end": v(165.13, 539.73) * mm});
            skLineSegment(sketch, "E959", {"start": v(165.13, 539.73) * mm, "end": v(158.18, 542.64) * mm});
            skLineSegment(sketch, "E960", {"start": v(158.18, 542.64) * mm, "end": v(153.54, 544.37) * mm});
            skLineSegment(sketch, "E961", {"start": v(153.54, 544.37) * mm, "end": v(151.96, 544.84) * mm});
            skLineSegment(sketch, "E962", {"start": v(151.96, 544.84) * mm, "end": v(151.06, 545.12) * mm});
            skLineSegment(sketch, "E963", {"start": v(151.06, 545.12) * mm, "end": v(148.25, 545.63) * mm});
            skLineSegment(sketch, "E964", {"start": v(148.25, 545.63) * mm, "end": v(143.02, 546.23) * mm});
            skLineSegment(sketch, "E965", {"start": v(143.02, 546.23) * mm, "end": v(136.46, 546.66) * mm});
            skLineSegment(sketch, "E966", {"start": v(136.46, 546.66) * mm, "end": v(128.76, 546.9) * mm});
            skLineSegment(sketch, "E967", {"start": v(128.76, 546.9) * mm, "end": v(120.1, 547) * mm});
            skLineSegment(sketch, "E968", {"start": v(120.1, 547) * mm, "end": v(110.64, 546.93) * mm});
            skLineSegment(sketch, "E969", {"start": v(110.64, 546.93) * mm, "end": v(100.6, 546.72) * mm});
            skLineSegment(sketch, "E970", {"start": v(100.6, 546.72) * mm, "end": v(90.15, 546.37) * mm});
            skLineSegment(sketch, "E971", {"start": v(90.15, 546.37) * mm, "end": v(79.46, 545.9) * mm});
            skLineSegment(sketch, "E972", {"start": v(79.46, 545.9) * mm, "end": v(68.72, 545.3) * mm});
            skLineSegment(sketch, "E973", {"start": v(68.72, 545.3) * mm, "end": v(58.12, 544.6) * mm});
            skLineSegment(sketch, "E974", {"start": v(58.12, 544.6) * mm, "end": v(47.84, 543.78) * mm});
            skLineSegment(sketch, "E975", {"start": v(47.84, 543.78) * mm, "end": v(38.06, 542.87) * mm});
            skLineSegment(sketch, "E976", {"start": v(38.06, 542.87) * mm, "end": v(28.96, 541.88) * mm});
            skLineSegment(sketch, "E977", {"start": v(28.96, 541.88) * mm, "end": v(20.73, 540.8) * mm});
            skLineSegment(sketch, "E978", {"start": v(20.73, 540.8) * mm, "end": v(15.34, 539.98) * mm});
            skLineSegment(sketch, "E979", {"start": v(15.34, 539.98) * mm, "end": v(13.55, 539.66) * mm});
            skLineSegment(sketch, "E980", {"start": v(13.55, 539.66) * mm, "end": v(11.68, 539.33) * mm});
            skLineSegment(sketch, "E981", {"start": v(11.68, 539.33) * mm, "end": v(6.05, 538.34) * mm});
            skLineSegment(sketch, "E982", {"start": v(6.05, 538.34) * mm, "end": v(-3.1, 536.77) * mm});
            skLineSegment(sketch, "E983", {"start": v(-3.1, 536.77) * mm, "end": v(-13.68, 534.98) * mm});
            skLineSegment(sketch, "E984", {"start": v(-13.68, 534.98) * mm, "end": v(-25.44, 533.02) * mm});
            skLineSegment(sketch, "E985", {"start": v(-25.44, 533.02) * mm, "end": v(-38.14, 530.95) * mm});
            skLineSegment(sketch, "E986", {"start": v(-38.14, 530.95) * mm, "end": v(-51.54, 528.8) * mm});
            skLineSegment(sketch, "E987", {"start": v(-51.54, 528.8) * mm, "end": v(-65.4, 526.64) * mm});
            skLineSegment(sketch, "E988", {"start": v(-65.4, 526.64) * mm, "end": v(-79.5, 524.5) * mm});
            skLineSegment(sketch, "E989", {"start": v(-79.5, 524.5) * mm, "end": v(-93.56, 522.42) * mm});
            skLineSegment(sketch, "E990", {"start": v(-93.56, 522.42) * mm, "end": v(-107.38, 520.46) * mm});
            skLineSegment(sketch, "E991", {"start": v(-107.38, 520.46) * mm, "end": v(-120.7, 518.67) * mm});
            skLineSegment(sketch, "E992", {"start": v(-120.7, 518.67) * mm, "end": v(-133.3, 517.08) * mm});
            skLineSegment(sketch, "E993", {"start": v(-133.3, 517.08) * mm, "end": v(-144.9, 515.74) * mm});
            skLineSegment(sketch, "E994", {"start": v(-144.9, 515.74) * mm, "end": v(-155.31, 514.72) * mm});
            skLineSegment(sketch, "E995", {"start": v(-155.31, 514.72) * mm, "end": v(-164.27, 514.04) * mm});
            skLineSegment(sketch, "E996", {"start": v(-164.27, 514.04) * mm, "end": v(-169.72, 513.78) * mm});
            skLineSegment(sketch, "E997", {"start": v(-169.72, 513.78) * mm, "end": v(-171.53, 513.76) * mm});
            skLineSegment(sketch, "E998", {"start": v(-171.53, 513.76) * mm, "end": v(-174.94, 513.72) * mm});
            skLineSegment(sketch, "E999", {"start": v(-174.94, 513.72) * mm, "end": v(-185.13, 513.54) * mm});
            skLineSegment(sketch, "E1000", {"start": v(-185.13, 513.54) * mm, "end": v(-200.22, 513.21) * mm});
            skLineSegment(sketch, "E1001", {"start": v(-200.22, 513.21) * mm, "end": v(-216.31, 512.92) * mm});
            skLineSegment(sketch, "E1002", {"start": v(-216.31, 512.92) * mm, "end": v(-232.93, 512.79) * mm});
            skLineSegment(sketch, "E1003", {"start": v(-232.93, 512.79) * mm, "end": v(-249.58, 512.93) * mm});
            skLineSegment(sketch, "E1004", {"start": v(-249.58, 512.93) * mm, "end": v(-265.77, 513.47) * mm});
            skLineSegment(sketch, "E1005", {"start": v(-265.77, 513.47) * mm, "end": v(-281.03, 514.53) * mm});
            skLineSegment(sketch, "E1006", {"start": v(-281.03, 514.53) * mm, "end": v(-291.43, 515.7) * mm});
            skLineSegment(sketch, "E1007", {"start": v(-291.43, 515.7) * mm, "end": v(-294.87, 516.24) * mm});
            skLineSegment(sketch, "E1008", {"start": v(-294.87, 516.24) * mm, "end": v(-297.01, 516.58) * mm});
            skLineSegment(sketch, "E1009", {"start": v(-297.01, 516.58) * mm, "end": v(-303.4, 517.98) * mm});
            skLineSegment(sketch, "E1010", {"start": v(-303.4, 517.98) * mm, "end": v(-310.55, 520.1) * mm});
            skLineSegment(sketch, "E1011", {"start": v(-310.55, 520.1) * mm, "end": v(-316.64, 522.46) * mm});
            skLineSegment(sketch, "E1012", {"start": v(-316.64, 522.46) * mm, "end": v(-321.98, 524.92) * mm});
            skLineSegment(sketch, "E1013", {"start": v(-321.98, 524.92) * mm, "end": v(-326.9, 527.32) * mm});
            skLineSegment(sketch, "E1014", {"start": v(-326.9, 527.32) * mm, "end": v(-331.72, 529.52) * mm});
            skLineSegment(sketch, "E1015", {"start": v(-331.72, 529.52) * mm, "end": v(-336.77, 531.38) * mm});
            skLineSegment(sketch, "E1016", {"start": v(-336.77, 531.38) * mm, "end": v(-340.96, 532.5) * mm});
            skLineSegment(sketch, "E1017", {"start": v(-340.96, 532.5) * mm, "end": v(-342.37, 532.75) * mm});
            skLineSegment(sketch, "E1018", {"start": v(-342.37, 532.75) * mm, "end": v(-343.16, 532.9) * mm});
            skLineSegment(sketch, "E1019", {"start": v(-343.16, 532.9) * mm, "end": v(-345.53, 533.23) * mm});
            skLineSegment(sketch, "E1020", {"start": v(-345.53, 533.23) * mm, "end": v(-348.98, 533.62) * mm});
            skLineSegment(sketch, "E1021", {"start": v(-348.98, 533.62) * mm, "end": v(-352.65, 533.9) * mm});
            skLineSegment(sketch, "E1022", {"start": v(-352.65, 533.9) * mm, "end": v(-356.5, 534.11) * mm});
            skLineSegment(sketch, "E1023", {"start": v(-356.5, 534.11) * mm, "end": v(-360.45, 534.25) * mm});
            skLineSegment(sketch, "E1024", {"start": v(-360.45, 534.25) * mm, "end": v(-364.44, 534.32) * mm});
            skLineSegment(sketch, "E1025", {"start": v(-364.44, 534.32) * mm, "end": v(-368.4, 534.35) * mm});
            skLineSegment(sketch, "E1026", {"start": v(-368.4, 534.35) * mm, "end": v(-372.3, 534.33) * mm});
            skLineSegment(sketch, "E1027", {"start": v(-372.3, 534.33) * mm, "end": v(-376.05, 534.29) * mm});
            skLineSegment(sketch, "E1028", {"start": v(-376.05, 534.29) * mm, "end": v(-379.59, 534.22) * mm});
            skLineSegment(sketch, "E1029", {"start": v(-379.59, 534.22) * mm, "end": v(-382.86, 534.14) * mm});
            skLineSegment(sketch, "E1030", {"start": v(-382.86, 534.14) * mm, "end": v(-385.81, 534.07) * mm});
            skLineSegment(sketch, "E1031", {"start": v(-385.81, 534.07) * mm, "end": v(-388.37, 534) * mm});
            skLineSegment(sketch, "E1032", {"start": v(-388.37, 534) * mm, "end": v(-390.47, 533.96) * mm});
            skLineSegment(sketch, "E1033", {"start": v(-390.47, 533.96) * mm, "end": v(-392.06, 533.95) * mm});
            skLineSegment(sketch, "E1034", {"start": v(-392.06, 533.95) * mm, "end": v(-392.82, 533.96) * mm});
            skLineSegment(sketch, "E1035", {"start": v(-392.82, 533.96) * mm, "end": v(-393.07, 533.98) * mm});
            skLineSegment(sketch, "E1036", {"start": v(-393.07, 533.98) * mm, "end": v(-393.5, 534) * mm});
            skLineSegment(sketch, "E1037", {"start": v(-393.5, 534) * mm, "end": v(-394.75, 534.15) * mm});
            skLineSegment(sketch, "E1038", {"start": v(-394.75, 534.15) * mm, "end": v(-397.04, 534.48) * mm});
            skLineSegment(sketch, "E1039", {"start": v(-397.04, 534.48) * mm, "end": v(-399.94, 534.94) * mm});
            skLineSegment(sketch, "E1040", {"start": v(-399.94, 534.94) * mm, "end": v(-403.4, 535.53) * mm});
            skLineSegment(sketch, "E1041", {"start": v(-403.4, 535.53) * mm, "end": v(-407.38, 536.23) * mm});
            skLineSegment(sketch, "E1042", {"start": v(-407.38, 536.23) * mm, "end": v(-411.85, 537.05) * mm});
            skLineSegment(sketch, "E1043", {"start": v(-411.85, 537.05) * mm, "end": v(-416.79, 537.97) * mm});
            skLineSegment(sketch, "E1044", {"start": v(-416.79, 537.97) * mm, "end": v(-422.15, 538.98) * mm});
            skLineSegment(sketch, "E1045", {"start": v(-422.15, 538.98) * mm, "end": v(-427.9, 540.07) * mm});
            skLineSegment(sketch, "E1046", {"start": v(-427.9, 540.07) * mm, "end": v(-434.02, 541.24) * mm});
            skLineSegment(sketch, "E1047", {"start": v(-434.02, 541.24) * mm, "end": v(-440.45, 542.47) * mm});
            skLineSegment(sketch, "E1048", {"start": v(-440.45, 542.47) * mm, "end": v(-447.18, 543.76) * mm});
            skLineSegment(sketch, "E1049", {"start": v(-447.18, 543.76) * mm, "end": v(-454.16, 545.1) * mm});
            skLineSegment(sketch, "E1050", {"start": v(-454.16, 545.1) * mm, "end": v(-461.37, 546.47) * mm});
            skLineSegment(sketch, "E1051", {"start": v(-461.37, 546.47) * mm, "end": v(-468.76, 547.87) * mm});
            skLineSegment(sketch, "E1052", {"start": v(-468.76, 547.87) * mm, "end": v(-476.31, 549.3) * mm});
            skLineSegment(sketch, "E1053", {"start": v(-476.31, 549.3) * mm, "end": v(-483.98, 550.73) * mm});
            skLineSegment(sketch, "E1054", {"start": v(-483.98, 550.73) * mm, "end": v(-491.74, 552.16) * mm});
            skLineSegment(sketch, "E1055", {"start": v(-491.74, 552.16) * mm, "end": v(-499.55, 553.59) * mm});
            skLineSegment(sketch, "E1056", {"start": v(-499.55, 553.59) * mm, "end": v(-507.38, 555) * mm});
            skLineSegment(sketch, "E1057", {"start": v(-507.38, 555) * mm, "end": v(-515.2, 556.39) * mm});
            skLineSegment(sketch, "E1058", {"start": v(-515.2, 556.39) * mm, "end": v(-522.96, 557.74) * mm});
            skLineSegment(sketch, "E1059", {"start": v(-522.96, 557.74) * mm, "end": v(-530.64, 559.04) * mm});
            skLineSegment(sketch, "E1060", {"start": v(-530.64, 559.04) * mm, "end": v(-538.2, 560.3) * mm});
            skLineSegment(sketch, "E1061", {"start": v(-538.2, 560.3) * mm, "end": v(-545.62, 561.5) * mm});
            skLineSegment(sketch, "E1062", {"start": v(-545.62, 561.5) * mm, "end": v(-552.86, 562.62) * mm});
            skLineSegment(sketch, "E1063", {"start": v(-552.86, 562.62) * mm, "end": v(-559.87, 563.67) * mm});
            skLineSegment(sketch, "E1064", {"start": v(-559.87, 563.67) * mm, "end": v(-566.63, 564.63) * mm});
            skLineSegment(sketch, "E1065", {"start": v(-566.63, 564.63) * mm, "end": v(-573.11, 565.49) * mm});
            skLineSegment(sketch, "E1066", {"start": v(-573.11, 565.49) * mm, "end": v(-579.27, 566.24) * mm});
            skLineSegment(sketch, "E1067", {"start": v(-579.27, 566.24) * mm, "end": v(-585.07, 566.88) * mm});
            skLineSegment(sketch, "E1068", {"start": v(-585.07, 566.88) * mm, "end": v(-589.13, 567.28) * mm});
            skLineSegment(sketch, "E1069", {"start": v(-589.13, 567.28) * mm, "end": v(-590.49, 567.4) * mm});
            skLineSegment(sketch, "E1070", {"start": v(535.93, 660.64) * mm, "end": v(535.7, 659.07) * mm});
            skLineSegment(sketch, "E1071", {"start": v(535.7, 659.07) * mm, "end": v(534.47, 654.42) * mm});
            skLineSegment(sketch, "E1072", {"start": v(534.47, 654.42) * mm, "end": v(531.97, 647.76) * mm});
            skLineSegment(sketch, "E1073", {"start": v(531.97, 647.76) * mm, "end": v(528.54, 640.8) * mm});
            skLineSegment(sketch, "E1074", {"start": v(528.54, 640.8) * mm, "end": v(524.3, 633.64) * mm});
            skLineSegment(sketch, "E1075", {"start": v(524.3, 633.64) * mm, "end": v(519.39, 626.39) * mm});
            skLineSegment(sketch, "E1076", {"start": v(519.39, 626.39) * mm, "end": v(513.91, 619.17) * mm});
            skLineSegment(sketch, "E1077", {"start": v(513.91, 619.17) * mm, "end": v(508, 612.1) * mm});
            skLineSegment(sketch, "E1078", {"start": v(508, 612.1) * mm, "end": v(501.77, 605.28) * mm});
            skLineSegment(sketch, "E1079", {"start": v(501.77, 605.28) * mm, "end": v(495.34, 598.84) * mm});
            skLineSegment(sketch, "E1080", {"start": v(495.34, 598.84) * mm, "end": v(488.84, 592.89) * mm});
            skLineSegment(sketch, "E1081", {"start": v(488.84, 592.89) * mm, "end": v(482.4, 587.54) * mm});
            skLineSegment(sketch, "E1082", {"start": v(482.4, 587.54) * mm, "end": v(476.1, 582.9) * mm});
            skLineSegment(sketch, "E1083", {"start": v(476.1, 582.9) * mm, "end": v(470.12, 579.1) * mm});
            skLineSegment(sketch, "E1084", {"start": v(470.12, 579.1) * mm, "end": v(464.54, 576.25) * mm});
            skLineSegment(sketch, "E1085", {"start": v(464.54, 576.25) * mm, "end": v(459.5, 574.45) * mm});
            skLineSegment(sketch, "E1086", {"start": v(459.5, 574.45) * mm, "end": v(456.2, 573.83) * mm});
            skLineSegment(sketch, "E1087", {"start": v(456.2, 573.83) * mm, "end": v(455.11, 573.83) * mm});
            skLineSegment(sketch, "E1088", {"start": v(455.11, 573.83) * mm, "end": v(453.78, 573.83) * mm});
            skLineSegment(sketch, "E1089", {"start": v(453.78, 573.83) * mm, "end": v(449.78, 573.79) * mm});
            skLineSegment(sketch, "E1090", {"start": v(449.78, 573.79) * mm, "end": v(444.74, 573.69) * mm});
            skLineSegment(sketch, "E1091", {"start": v(444.74, 573.69) * mm, "end": v(439.88, 573.6) * mm});
            skLineSegment(sketch, "E1092", {"start": v(439.88, 573.6) * mm, "end": v(435.14, 573.57) * mm});
            skLineSegment(sketch, "E1093", {"start": v(435.14, 573.57) * mm, "end": v(430.43, 573.67) * mm});
            skLineSegment(sketch, "E1094", {"start": v(430.43, 573.67) * mm, "end": v(425.66, 573.97) * mm});
            skLineSegment(sketch, "E1095", {"start": v(425.66, 573.97) * mm, "end": v(420.76, 574.52) * mm});
            skLineSegment(sketch, "E1096", {"start": v(420.76, 574.52) * mm, "end": v(415.64, 575.38) * mm});
            skLineSegment(sketch, "E1097", {"start": v(415.64, 575.38) * mm, "end": v(410.23, 576.62) * mm});
            skLineSegment(sketch, "E1098", {"start": v(410.23, 576.62) * mm, "end": v(404.43, 578.3) * mm});
            skLineSegment(sketch, "E1099", {"start": v(404.43, 578.3) * mm, "end": v(398.16, 580.49) * mm});
            skLineSegment(sketch, "E1100", {"start": v(398.16, 580.49) * mm, "end": v(391.35, 583.24) * mm});
            skLineSegment(sketch, "E1101", {"start": v(391.35, 583.24) * mm, "end": v(383.9, 586.61) * mm});
            skLineSegment(sketch, "E1102", {"start": v(383.9, 586.61) * mm, "end": v(375.75, 590.67) * mm});
            skLineSegment(sketch, "E1103", {"start": v(375.75, 590.67) * mm, "end": v(366.8, 595.49) * mm});
            skLineSegment(sketch, "E1104", {"start": v(366.8, 595.49) * mm, "end": v(359.41, 599.67) * mm});
            skLineSegment(sketch, "E1105", {"start": v(359.41, 599.67) * mm, "end": v(356.98, 601.1) * mm});
            skLineSegment(sketch, "E1106", {"start": v(356.98, 601.1) * mm, "end": v(354.52, 602.55) * mm});
            skLineSegment(sketch, "E1107", {"start": v(354.52, 602.55) * mm, "end": v(347.19, 606.9) * mm});
            skLineSegment(sketch, "E1108", {"start": v(347.19, 606.9) * mm, "end": v(338.3, 612.23) * mm});
            skLineSegment(sketch, "E1109", {"start": v(338.3, 612.23) * mm, "end": v(330.2, 617.11) * mm});
            skLineSegment(sketch, "E1110", {"start": v(330.2, 617.11) * mm, "end": v(322.71, 621.57) * mm});
            skLineSegment(sketch, "E1111", {"start": v(322.71, 621.57) * mm, "end": v(315.7, 625.63) * mm});
            skLineSegment(sketch, "E1112", {"start": v(315.7, 625.63) * mm, "end": v(308.99, 629.34) * mm});
            skLineSegment(sketch, "E1113", {"start": v(308.99, 629.34) * mm, "end": v(302.45, 632.71) * mm});
            skLineSegment(sketch, "E1114", {"start": v(302.45, 632.71) * mm, "end": v(295.94, 635.78) * mm});
            skLineSegment(sketch, "E1115", {"start": v(295.94, 635.78) * mm, "end": v(289.31, 638.58) * mm});
            skLineSegment(sketch, "E1116", {"start": v(289.31, 638.58) * mm, "end": v(282.4, 641.13) * mm});
            skLineSegment(sketch, "E1117", {"start": v(282.4, 641.13) * mm, "end": v(275.07, 643.46) * mm});
            skLineSegment(sketch, "E1118", {"start": v(275.07, 643.46) * mm, "end": v(267.17, 645.6) * mm});
            skLineSegment(sketch, "E1119", {"start": v(267.17, 645.6) * mm, "end": v(258.55, 647.6) * mm});
            skLineSegment(sketch, "E1120", {"start": v(258.55, 647.6) * mm, "end": v(249.05, 649.46) * mm});
            skLineSegment(sketch, "E1121", {"start": v(249.05, 649.46) * mm, "end": v(238.55, 651.22) * mm});
            skLineSegment(sketch, "E1122", {"start": v(238.55, 651.22) * mm, "end": v(229.8, 652.51) * mm});
            skLineSegment(sketch, "E1123", {"start": v(229.8, 652.51) * mm, "end": v(226.87, 652.9) * mm});
            skLineSegment(sketch, "E1124", {"start": v(226.87, 652.9) * mm, "end": v(223.84, 653.32) * mm});
            skLineSegment(sketch, "E1125", {"start": v(223.84, 653.32) * mm, "end": v(214.74, 654.6) * mm});
            skLineSegment(sketch, "E1126", {"start": v(214.74, 654.6) * mm, "end": v(202.9, 656.32) * mm});
            skLineSegment(sketch, "E1127", {"start": v(202.9, 656.32) * mm, "end": v(191.27, 658.02) * mm});
            skLineSegment(sketch, "E1128", {"start": v(191.27, 658.02) * mm, "end": v(179.73, 659.64) * mm});
            skLineSegment(sketch, "E1129", {"start": v(179.73, 659.64) * mm, "end": v(168.19, 661.14) * mm});
            skLineSegment(sketch, "E1130", {"start": v(168.19, 661.14) * mm, "end": v(156.55, 662.47) * mm});
            skLineSegment(sketch, "E1131", {"start": v(156.55, 662.47) * mm, "end": v(144.73, 663.57) * mm});
            skLineSegment(sketch, "E1132", {"start": v(144.73, 663.57) * mm, "end": v(132.62, 664.4) * mm});
            skLineSegment(sketch, "E1133", {"start": v(132.62, 664.4) * mm, "end": v(120.14, 664.89) * mm});
            skLineSegment(sketch, "E1134", {"start": v(120.14, 664.89) * mm, "end": v(107.17, 665) * mm});
            skLineSegment(sketch, "E1135", {"start": v(107.17, 665) * mm, "end": v(93.63, 664.7) * mm});
            skLineSegment(sketch, "E1136", {"start": v(93.63, 664.7) * mm, "end": v(79.42, 663.9) * mm});
            skLineSegment(sketch, "E1137", {"start": v(79.42, 663.9) * mm, "end": v(64.44, 662.58) * mm});
            skLineSegment(sketch, "E1138", {"start": v(64.44, 662.58) * mm, "end": v(48.6, 660.68) * mm});
            skLineSegment(sketch, "E1139", {"start": v(48.6, 660.68) * mm, "end": v(31.8, 658.15) * mm});
            skLineSegment(sketch, "E1140", {"start": v(31.8, 658.15) * mm, "end": v(18.4, 655.8) * mm});
            skLineSegment(sketch, "E1141", {"start": v(18.4, 655.8) * mm, "end": v(13.95, 654.93) * mm});
            skLineSegment(sketch, "E1142", {"start": v(13.95, 654.93) * mm, "end": v(10.4, 654.24) * mm});
            skLineSegment(sketch, "E1143", {"start": v(10.4, 654.24) * mm, "end": v(-0.24, 652.1) * mm});
            skLineSegment(sketch, "E1144", {"start": v(-0.24, 652.1) * mm, "end": v(-12.26, 649.54) * mm});
            skLineSegment(sketch, "E1145", {"start": v(-12.26, 649.54) * mm, "end": v(-22.42, 647.22) * mm});
            skLineSegment(sketch, "E1146", {"start": v(-22.42, 647.22) * mm, "end": v(-31.03, 645.12) * mm});
            skLineSegment(sketch, "E1147", {"start": v(-31.03, 645.12) * mm, "end": v(-38.41, 643.2) * mm});
            skLineSegment(sketch, "E1148", {"start": v(-38.41, 643.2) * mm, "end": v(-44.86, 641.43) * mm});
            skLineSegment(sketch, "E1149", {"start": v(-44.86, 641.43) * mm, "end": v(-50.7, 639.78) * mm});
            skLineSegment(sketch, "E1150", {"start": v(-50.7, 639.78) * mm, "end": v(-56.22, 638.21) * mm});
            skLineSegment(sketch, "E1151", {"start": v(-56.22, 638.21) * mm, "end": v(-61.74, 636.7) * mm});
            skLineSegment(sketch, "E1152", {"start": v(-61.74, 636.7) * mm, "end": v(-67.57, 635.22) * mm});
            skLineSegment(sketch, "E1153", {"start": v(-67.57, 635.22) * mm, "end": v(-74.01, 633.73) * mm});
            skLineSegment(sketch, "E1154", {"start": v(-74.01, 633.73) * mm, "end": v(-81.4, 632.2) * mm});
            skLineSegment(sketch, "E1155", {"start": v(-81.4, 632.2) * mm, "end": v(-90, 630.6) * mm});
            skLineSegment(sketch, "E1156", {"start": v(-90, 630.6) * mm, "end": v(-100.16, 628.9) * mm});
            skLineSegment(sketch, "E1157", {"start": v(-100.16, 628.9) * mm, "end": v(-112.17, 627.06) * mm});
            skLineSegment(sketch, "E1158", {"start": v(-112.17, 627.06) * mm, "end": v(-122.8, 625.55) * mm});
            skLineSegment(sketch, "E1159", {"start": v(-122.8, 625.55) * mm, "end": v(-126.35, 625.06) * mm});
            skLineSegment(sketch, "E1160", {"start": v(-126.35, 625.06) * mm, "end": v(-128.5, 624.77) * mm});
            skLineSegment(sketch, "E1161", {"start": v(-128.5, 624.77) * mm, "end": v(-134.94, 623.73) * mm});
            skLineSegment(sketch, "E1162", {"start": v(-134.94, 623.73) * mm, "end": v(-144.28, 622.1) * mm});
            skLineSegment(sketch, "E1163", {"start": v(-144.28, 622.1) * mm, "end": v(-154.43, 620.37) * mm});
            skLineSegment(sketch, "E1164", {"start": v(-154.43, 620.37) * mm, "end": v(-165.48, 618.72) * mm});
            skLineSegment(sketch, "E1165", {"start": v(-165.48, 618.72) * mm, "end": v(-177.49, 617.33) * mm});
            skLineSegment(sketch, "E1166", {"start": v(-177.49, 617.33) * mm, "end": v(-190.53, 616.39) * mm});
            skLineSegment(sketch, "E1167", {"start": v(-190.53, 616.39) * mm, "end": v(-204.67, 616.09) * mm});
            skLineSegment(sketch, "E1168", {"start": v(-204.67, 616.09) * mm, "end": v(-216.18, 616.37) * mm});
            skLineSegment(sketch, "E1169", {"start": v(-216.18, 616.37) * mm, "end": v(-220, 616.62) * mm});
            skLineSegment(sketch, "E1170", {"start": v(-220, 616.62) * mm, "end": v(-221.34, 616.7) * mm});
            skLineSegment(sketch, "E1171", {"start": v(-221.34, 616.7) * mm, "end": v(-225.37, 617.32) * mm});
            skLineSegment(sketch, "E1172", {"start": v(-225.37, 617.32) * mm, "end": v(-231.08, 618.7) * mm});
            skLineSegment(sketch, "E1173", {"start": v(-231.08, 618.7) * mm, "end": v(-237.08, 620.67) * mm});
            skLineSegment(sketch, "E1174", {"start": v(-237.08, 620.67) * mm, "end": v(-243.3, 623.13) * mm});
            skLineSegment(sketch, "E1175", {"start": v(-243.3, 623.13) * mm, "end": v(-249.67, 625.95) * mm});
            skLineSegment(sketch, "E1176", {"start": v(-249.67, 625.95) * mm, "end": v(-256.12, 629.06) * mm});
            skLineSegment(sketch, "E1177", {"start": v(-256.12, 629.06) * mm, "end": v(-262.6, 632.33) * mm});
            skLineSegment(sketch, "E1178", {"start": v(-262.6, 632.33) * mm, "end": v(-269.02, 635.66) * mm});
            skLineSegment(sketch, "E1179", {"start": v(-269.02, 635.66) * mm, "end": v(-275.33, 638.96) * mm});
            skLineSegment(sketch, "E1180", {"start": v(-275.33, 638.96) * mm, "end": v(-281.46, 642.12) * mm});
            skLineSegment(sketch, "E1181", {"start": v(-281.46, 642.12) * mm, "end": v(-287.35, 645.04) * mm});
            skLineSegment(sketch, "E1182", {"start": v(-287.35, 645.04) * mm, "end": v(-292.92, 647.6) * mm});
            skLineSegment(sketch, "E1183", {"start": v(-292.92, 647.6) * mm, "end": v(-298.12, 649.73) * mm});
            skLineSegment(sketch, "E1184", {"start": v(-298.12, 649.73) * mm, "end": v(-302.87, 651.3) * mm});
            skLineSegment(sketch, "E1185", {"start": v(-302.87, 651.3) * mm, "end": v(-307.12, 652.2) * mm});
            skLineSegment(sketch, "E1186", {"start": v(-307.12, 652.2) * mm, "end": v(-309.87, 652.42) * mm});
            skLineSegment(sketch, "E1187", {"start": v(-309.87, 652.42) * mm, "end": v(-310.78, 652.35) * mm});
            skLineSegment(sketch, "E1188", {"start": v(-310.78, 652.35) * mm, "end": v(-313.86, 652.11) * mm});
            skLineSegment(sketch, "E1189", {"start": v(-313.86, 652.11) * mm, "end": v(-323.07, 651.41) * mm});
            skLineSegment(sketch, "E1190", {"start": v(-323.07, 651.41) * mm, "end": v(-334.85, 650.56) * mm});
            skLineSegment(sketch, "E1191", {"start": v(-334.85, 650.56) * mm, "end": v(-346.18, 649.82) * mm});
            skLineSegment(sketch, "E1192", {"start": v(-346.18, 649.82) * mm, "end": v(-357.1, 649.18) * mm});
            skLineSegment(sketch, "E1193", {"start": v(-357.1, 649.18) * mm, "end": v(-367.68, 648.64) * mm});
            skLineSegment(sketch, "E1194", {"start": v(-367.68, 648.64) * mm, "end": v(-377.96, 648.23) * mm});
            skLineSegment(sketch, "E1195", {"start": v(-377.96, 648.23) * mm, "end": v(-388, 647.94) * mm});
            skLineSegment(sketch, "E1196", {"start": v(-388, 647.94) * mm, "end": v(-397.84, 647.78) * mm});
            skLineSegment(sketch, "E1197", {"start": v(-397.84, 647.78) * mm, "end": v(-407.55, 647.75) * mm});
            skLineSegment(sketch, "E1198", {"start": v(-407.55, 647.75) * mm, "end": v(-417.18, 647.86) * mm});
            skLineSegment(sketch, "E1199", {"start": v(-417.18, 647.86) * mm, "end": v(-426.78, 648.11) * mm});
            skLineSegment(sketch, "E1200", {"start": v(-426.78, 648.11) * mm, "end": v(-436.4, 648.51) * mm});
            skLineSegment(sketch, "E1201", {"start": v(-436.4, 648.51) * mm, "end": v(-446.1, 649.07) * mm});
            skLineSegment(sketch, "E1202", {"start": v(-446.1, 649.07) * mm, "end": v(-455.93, 649.8) * mm});
            skLineSegment(sketch, "E1203", {"start": v(-455.93, 649.8) * mm, "end": v(-465.94, 650.67) * mm});
            skLineSegment(sketch, "E1204", {"start": v(-465.94, 650.67) * mm, "end": v(-473.63, 651.45) * mm});
            skLineSegment(sketch, "E1205", {"start": v(-473.63, 651.45) * mm, "end": v(-476.2, 651.73) * mm});
            skLineSegment(sketch, "E1206", {"start": v(-476.2, 651.73) * mm, "end": v(-478.83, 652.02) * mm});
            skLineSegment(sketch, "E1207", {"start": v(-478.83, 652.02) * mm, "end": v(-486.73, 653.06) * mm});
            skLineSegment(sketch, "E1208", {"start": v(-486.73, 653.06) * mm, "end": v(-497.65, 654.72) * mm});
            skLineSegment(sketch, "E1209", {"start": v(-497.65, 654.72) * mm, "end": v(-508.82, 656.65) * mm});
            skLineSegment(sketch, "E1210", {"start": v(-508.82, 656.65) * mm, "end": v(-520.1, 658.8) * mm});
            skLineSegment(sketch, "E1211", {"start": v(-520.1, 658.8) * mm, "end": v(-531.32, 661.13) * mm});
            skLineSegment(sketch, "E1212", {"start": v(-531.32, 661.13) * mm, "end": v(-542.34, 663.55) * mm});
            skLineSegment(sketch, "E1213", {"start": v(-542.34, 663.55) * mm, "end": v(-553.01, 666.03) * mm});
            skLineSegment(sketch, "E1214", {"start": v(-553.01, 666.03) * mm, "end": v(-563.2, 668.48) * mm});
            skLineSegment(sketch, "E1215", {"start": v(-563.2, 668.48) * mm, "end": v(-572.73, 670.87) * mm});
            skLineSegment(sketch, "E1216", {"start": v(-572.73, 670.87) * mm, "end": v(-581.48, 673.13) * mm});
            skLineSegment(sketch, "E1217", {"start": v(-581.48, 673.13) * mm, "end": v(-589.3, 675.2) * mm});
            skLineSegment(sketch, "E1218", {"start": v(-589.3, 675.2) * mm, "end": v(-596.01, 677.02) * mm});
            skLineSegment(sketch, "E1219", {"start": v(-596.01, 677.02) * mm, "end": v(-601.5, 678.55) * mm});
            skLineSegment(sketch, "E1220", {"start": v(-601.5, 678.55) * mm, "end": v(-605.6, 679.7) * mm});
            skLineSegment(sketch, "E1221", {"start": v(-605.6, 679.7) * mm, "end": v(-608.17, 680.44) * mm});
            skLineSegment(sketch, "E1222", {"start": v(-608.17, 680.44) * mm, "end": v(-609.06, 680.7) * mm});
            skLineSegment(sketch, "E1223", {"start": v(496.9, 661.06) * mm, "end": v(497.02, 660.6) * mm});
            skLineSegment(sketch, "E1224", {"start": v(497.02, 660.6) * mm, "end": v(497.43, 659.22) * mm});
            skLineSegment(sketch, "E1225", {"start": v(497.43, 659.22) * mm, "end": v(497.94, 657.52) * mm});
            skLineSegment(sketch, "E1226", {"start": v(497.94, 657.52) * mm, "end": v(498.32, 655.95) * mm});
            skLineSegment(sketch, "E1227", {"start": v(498.32, 655.95) * mm, "end": v(498.43, 654.5) * mm});
            skLineSegment(sketch, "E1228", {"start": v(498.43, 654.5) * mm, "end": v(498.13, 653.13) * mm});
            skLineSegment(sketch, "E1229", {"start": v(498.13, 653.13) * mm, "end": v(497.3, 651.85) * mm});
            skLineSegment(sketch, "E1230", {"start": v(497.3, 651.85) * mm, "end": v(495.78, 650.65) * mm});
            skLineSegment(sketch, "E1231", {"start": v(495.78, 650.65) * mm, "end": v(494.06, 649.73) * mm});
            skLineSegment(sketch, "E1232", {"start": v(494.06, 649.73) * mm, "end": v(493.46, 649.5) * mm});
            skLineSegment(sketch, "E1233", {"start": v(493.46, 649.5) * mm, "end": v(492.18, 648.96) * mm});
            skLineSegment(sketch, "E1234", {"start": v(492.18, 648.96) * mm, "end": v(487.94, 648.35) * mm});
            skLineSegment(sketch, "E1235", {"start": v(487.94, 648.35) * mm, "end": v(482.43, 648.71) * mm});
            skLineSegment(sketch, "E1236", {"start": v(482.43, 648.71) * mm, "end": v(476.9, 649.47) * mm});
            skLineSegment(sketch, "E1237", {"start": v(476.9, 649.47) * mm, "end": v(472.73, 649.66) * mm});
            skLineSegment(sketch, "E1238", {"start": v(472.73, 649.66) * mm, "end": v(471.37, 649.5) * mm});
            skLineSegment(sketch, "E1239", {"start": v(471.37, 649.5) * mm, "end": v(470.91, 649.43) * mm});
            skLineSegment(sketch, "E1240", {"start": v(470.91, 649.43) * mm, "end": v(469.58, 649.1) * mm});
            skLineSegment(sketch, "E1241", {"start": v(469.58, 649.1) * mm, "end": v(467.05, 648.31) * mm});
            skLineSegment(sketch, "E1242", {"start": v(467.05, 648.31) * mm, "end": v(463.87, 647.2) * mm});
            skLineSegment(sketch, "E1243", {"start": v(463.87, 647.2) * mm, "end": v(460.1, 645.83) * mm});
            skLineSegment(sketch, "E1244", {"start": v(460.1, 645.83) * mm, "end": v(455.86, 644.24) * mm});
            skLineSegment(sketch, "E1245", {"start": v(455.86, 644.24) * mm, "end": v(451.2, 642.5) * mm});
            skLineSegment(sketch, "E1246", {"start": v(451.2, 642.5) * mm, "end": v(446.22, 640.68) * mm});
            skLineSegment(sketch, "E1247", {"start": v(446.22, 640.68) * mm, "end": v(441, 638.84) * mm});
            skLineSegment(sketch, "E1248", {"start": v(441, 638.84) * mm, "end": v(435.63, 637.03) * mm});
            skLineSegment(sketch, "E1249", {"start": v(435.63, 637.03) * mm, "end": v(430.18, 635.32) * mm});
            skLineSegment(sketch, "E1250", {"start": v(430.18, 635.32) * mm, "end": v(424.75, 633.77) * mm});
            skLineSegment(sketch, "E1251", {"start": v(424.75, 633.77) * mm, "end": v(419.41, 632.44) * mm});
            skLineSegment(sketch, "E1252", {"start": v(419.41, 632.44) * mm, "end": v(414.25, 631.39) * mm});
            skLineSegment(sketch, "E1253", {"start": v(414.25, 631.39) * mm, "end": v(409.36, 630.67) * mm});
            skLineSegment(sketch, "E1254", {"start": v(409.36, 630.67) * mm, "end": v(404.8, 630.36) * mm});
            skLineSegment(sketch, "E1255", {"start": v(404.8, 630.36) * mm, "end": v(401.7, 630.4) * mm});
            skLineSegment(sketch, "E1256", {"start": v(401.7, 630.4) * mm, "end": v(400.68, 630.51) * mm});
            skLineSegment(sketch, "E1257", {"start": v(400.68, 630.51) * mm, "end": v(399.6, 630.63) * mm});
            skLineSegment(sketch, "E1258", {"start": v(399.6, 630.63) * mm, "end": v(396.35, 631.12) * mm});
            skLineSegment(sketch, "E1259", {"start": v(396.35, 631.12) * mm, "end": v(391.2, 632.1) * mm});
            skLineSegment(sketch, "E1260", {"start": v(391.2, 632.1) * mm, "end": v(385.33, 633.41) * mm});
            skLineSegment(sketch, "E1261", {"start": v(385.33, 633.41) * mm, "end": v(378.9, 635.03) * mm});
            skLineSegment(sketch, "E1262", {"start": v(378.9, 635.03) * mm, "end": v(371.99, 636.91) * mm});
            skLineSegment(sketch, "E1263", {"start": v(371.99, 636.91) * mm, "end": v(364.74, 639.03) * mm});
            skLineSegment(sketch, "E1264", {"start": v(364.74, 639.03) * mm, "end": v(357.29, 641.33) * mm});
            skLineSegment(sketch, "E1265", {"start": v(357.29, 641.33) * mm, "end": v(349.73, 643.8) * mm});
            skLineSegment(sketch, "E1266", {"start": v(349.73, 643.8) * mm, "end": v(342.2, 646.37) * mm});
            skLineSegment(sketch, "E1267", {"start": v(342.2, 646.37) * mm, "end": v(334.83, 649.04) * mm});
            skLineSegment(sketch, "E1268", {"start": v(334.83, 649.04) * mm, "end": v(327.72, 651.75) * mm});
            skLineSegment(sketch, "E1269", {"start": v(327.72, 651.75) * mm, "end": v(321, 654.47) * mm});
            skLineSegment(sketch, "E1270", {"start": v(321, 654.47) * mm, "end": v(314.8, 657.17) * mm});
            skLineSegment(sketch, "E1271", {"start": v(314.8, 657.17) * mm, "end": v(309.23, 659.8) * mm});
            skLineSegment(sketch, "E1272", {"start": v(309.23, 659.8) * mm, "end": v(304.43, 662.35) * mm});
            skLineSegment(sketch, "E1273", {"start": v(304.43, 662.35) * mm, "end": v(301.45, 664.1) * mm});
            skLineSegment(sketch, "E1274", {"start": v(301.45, 664.1) * mm, "end": v(300.5, 664.75) * mm});
            skLineSegment(sketch, "E1275", {"start": v(515.96, 661.3) * mm, "end": v(516.1, 660.6) * mm});
            skLineSegment(sketch, "E1276", {"start": v(516.1, 660.6) * mm, "end": v(516.5, 658.53) * mm});
            skLineSegment(sketch, "E1277", {"start": v(516.5, 658.53) * mm, "end": v(516.84, 656.03) * mm});
            skLineSegment(sketch, "E1278", {"start": v(516.84, 656.03) * mm, "end": v(516.98, 653.74) * mm});
            skLineSegment(sketch, "E1279", {"start": v(516.98, 653.74) * mm, "end": v(516.85, 651.6) * mm});
            skLineSegment(sketch, "E1280", {"start": v(516.85, 651.6) * mm, "end": v(516.41, 649.55) * mm});
            skLineSegment(sketch, "E1281", {"start": v(516.41, 649.55) * mm, "end": v(515.64, 647.52) * mm});
            skLineSegment(sketch, "E1282", {"start": v(515.64, 647.52) * mm, "end": v(514.48, 645.44) * mm});
            skLineSegment(sketch, "E1283", {"start": v(514.48, 645.44) * mm, "end": v(513.31, 643.79) * mm});
            skLineSegment(sketch, "E1284", {"start": v(513.31, 643.79) * mm, "end": v(512.9, 643.26) * mm});
            skLineSegment(sketch, "E1285", {"start": v(512.9, 643.26) * mm, "end": v(512.48, 642.75) * mm});
            skLineSegment(sketch, "E1286", {"start": v(512.48, 642.75) * mm, "end": v(511.07, 641.34) * mm});
            skLineSegment(sketch, "E1287", {"start": v(511.07, 641.34) * mm, "end": v(509.21, 639.98) * mm});
            skLineSegment(sketch, "E1288", {"start": v(509.21, 639.98) * mm, "end": v(507.3, 639) * mm});
            skLineSegment(sketch, "E1289", {"start": v(507.3, 639) * mm, "end": v(505.3, 638.26) * mm});
            skLineSegment(sketch, "E1290", {"start": v(505.3, 638.26) * mm, "end": v(503.22, 637.6) * mm});
            skLineSegment(sketch, "E1291", {"start": v(503.22, 637.6) * mm, "end": v(501, 636.85) * mm});
            skLineSegment(sketch, "E1292", {"start": v(501, 636.85) * mm, "end": v(498.66, 635.84) * mm});
            skLineSegment(sketch, "E1293", {"start": v(498.66, 635.84) * mm, "end": v(496.75, 634.82) * mm});
            skLineSegment(sketch, "E1294", {"start": v(496.75, 634.82) * mm, "end": v(496.15, 634.43) * mm});
            skLineSegment(sketch, "E1295", {"start": v(496.15, 634.43) * mm, "end": v(495.78, 634.2) * mm});
            skLineSegment(sketch, "E1296", {"start": v(495.78, 634.2) * mm, "end": v(494.8, 633.32) * mm});
            skLineSegment(sketch, "E1297", {"start": v(494.8, 633.32) * mm, "end": v(493.3, 631.69) * mm});
            skLineSegment(sketch, "E1298", {"start": v(493.3, 631.69) * mm, "end": v(491.56, 629.63) * mm});
            skLineSegment(sketch, "E1299", {"start": v(491.56, 629.63) * mm, "end": v(489.53, 627.22) * mm});
            skLineSegment(sketch, "E1300", {"start": v(489.53, 627.22) * mm, "end": v(487.13, 624.55) * mm});
            skLineSegment(sketch, "E1301", {"start": v(487.13, 624.55) * mm, "end": v(484.28, 621.7) * mm});
            skLineSegment(sketch, "E1302", {"start": v(484.28, 621.7) * mm, "end": v(480.92, 618.74) * mm});
            skLineSegment(sketch, "E1303", {"start": v(480.92, 618.74) * mm, "end": v(476.96, 615.76) * mm});
            skLineSegment(sketch, "E1304", {"start": v(476.96, 615.76) * mm, "end": v(472.34, 612.85) * mm});
            skLineSegment(sketch, "E1305", {"start": v(472.34, 612.85) * mm, "end": v(466.98, 610.08) * mm});
            skLineSegment(sketch, "E1306", {"start": v(466.98, 610.08) * mm, "end": v(460.82, 607.53) * mm});
            skLineSegment(sketch, "E1307", {"start": v(460.82, 607.53) * mm, "end": v(453.76, 605.3) * mm});
            skLineSegment(sketch, "E1308", {"start": v(453.76, 605.3) * mm, "end": v(445.76, 603.45) * mm});
            skLineSegment(sketch, "E1309", {"start": v(445.76, 603.45) * mm, "end": v(436.72, 602.07) * mm});
            skLineSegment(sketch, "E1310", {"start": v(436.72, 602.07) * mm, "end": v(426.58, 601.25) * mm});
            skLineSegment(sketch, "E1311", {"start": v(426.58, 601.25) * mm, "end": v(418.1, 601.02) * mm});
            skLineSegment(sketch, "E1312", {"start": v(418.1, 601.02) * mm, "end": v(415.28, 601.06) * mm});
            skLineSegment(sketch, "E1313", {"start": v(415.28, 601.06) * mm, "end": v(413.88, 601.08) * mm});
            skLineSegment(sketch, "E1314", {"start": v(413.88, 601.08) * mm, "end": v(409.72, 601.54) * mm});
            skLineSegment(sketch, "E1315", {"start": v(409.72, 601.54) * mm, "end": v(403.6, 602.77) * mm});
            skLineSegment(sketch, "E1316", {"start": v(403.6, 602.77) * mm, "end": v(396.96, 604.69) * mm});
            skLineSegment(sketch, "E1317", {"start": v(396.96, 604.69) * mm, "end": v(389.85, 607.21) * mm});
            skLineSegment(sketch, "E1318", {"start": v(389.85, 607.21) * mm, "end": v(382.32, 610.25) * mm});
            skLineSegment(sketch, "E1319", {"start": v(382.32, 610.25) * mm, "end": v(374.41, 613.74) * mm});
            skLineSegment(sketch, "E1320", {"start": v(374.41, 613.74) * mm, "end": v(366.18, 617.6) * mm});
            skLineSegment(sketch, "E1321", {"start": v(366.18, 617.6) * mm, "end": v(357.65, 621.73) * mm});
            skLineSegment(sketch, "E1322", {"start": v(357.65, 621.73) * mm, "end": v(348.9, 626.08) * mm});
            skLineSegment(sketch, "E1323", {"start": v(348.9, 626.08) * mm, "end": v(339.94, 630.55) * mm});
            skLineSegment(sketch, "E1324", {"start": v(339.94, 630.55) * mm, "end": v(330.84, 635.07) * mm});
            skLineSegment(sketch, "E1325", {"start": v(330.84, 635.07) * mm, "end": v(321.64, 639.55) * mm});
            skLineSegment(sketch, "E1326", {"start": v(321.64, 639.55) * mm, "end": v(312.38, 643.93) * mm});
            skLineSegment(sketch, "E1327", {"start": v(312.38, 643.93) * mm, "end": v(303.12, 648.11) * mm});
            skLineSegment(sketch, "E1328", {"start": v(303.12, 648.11) * mm, "end": v(293.9, 652.03) * mm});
            skLineSegment(sketch, "E1329", {"start": v(293.9, 652.03) * mm, "end": v(287.05, 654.75) * mm});
            skLineSegment(sketch, "E1330", {"start": v(287.05, 654.75) * mm, "end": v(284.75, 655.6) * mm});
            skLineSegment(sketch, "E1331", {"start": v(284.75, 655.6) * mm, "end": v(282.47, 656.44) * mm});
            skLineSegment(sketch, "E1332", {"start": v(282.47, 656.44) * mm, "end": v(275.54, 658.62) * mm});
            skLineSegment(sketch, "E1333", {"start": v(275.54, 658.62) * mm, "end": v(266.91, 660.77) * mm});
            skLineSegment(sketch, "E1334", {"start": v(266.91, 660.77) * mm, "end": v(258.8, 662.22) * mm});
            skLineSegment(sketch, "E1335", {"start": v(258.8, 662.22) * mm, "end": v(251.15, 663.18) * mm});
            skLineSegment(sketch, "E1336", {"start": v(251.15, 663.18) * mm, "end": v(243.89, 663.85) * mm});
            skLineSegment(sketch, "E1337", {"start": v(243.89, 663.85) * mm, "end": v(236.95, 664.43) * mm});
            skLineSegment(sketch, "E1338", {"start": v(236.95, 664.43) * mm, "end": v(230.27, 665.1) * mm});
            skLineSegment(sketch, "E1339", {"start": v(230.27, 665.1) * mm, "end": v(225.4, 665.77) * mm});
            skLineSegment(sketch, "E1340", {"start": v(225.4, 665.77) * mm, "end": v(223.78, 666.07) * mm});
            skLineSegment(sketch, "E1341", {"start": v(573.56, 659.15) * mm, "end": v(573.58, 657.98) * mm});
            skLineSegment(sketch, "E1342", {"start": v(573.58, 657.98) * mm, "end": v(573.8, 654.47) * mm});
            skLineSegment(sketch, "E1343", {"start": v(573.8, 654.47) * mm, "end": v(574.26, 649.95) * mm});
            skLineSegment(sketch, "E1344", {"start": v(574.26, 649.95) * mm, "end": v(574.82, 645.54) * mm});
            skLineSegment(sketch, "E1345", {"start": v(574.82, 645.54) * mm, "end": v(575.3, 641.22) * mm});
            skLineSegment(sketch, "E1346", {"start": v(575.3, 641.22) * mm, "end": v(575.57, 636.93) * mm});
            skLineSegment(sketch, "E1347", {"start": v(575.57, 636.93) * mm, "end": v(575.47, 632.64) * mm});
            skLineSegment(sketch, "E1348", {"start": v(575.47, 632.64) * mm, "end": v(574.85, 628.29) * mm});
            skLineSegment(sketch, "E1349", {"start": v(574.85, 628.29) * mm, "end": v(573.96, 624.93) * mm});
            skLineSegment(sketch, "E1350", {"start": v(573.96, 624.93) * mm, "end": v(573.56, 623.85) * mm});
            skLineSegment(sketch, "E1351", {"start": v(573.56, 623.85) * mm, "end": v(573.43, 623.5) * mm});
            skLineSegment(sketch, "E1352", {"start": v(573.43, 623.5) * mm, "end": v(572.98, 622.47) * mm});
            skLineSegment(sketch, "E1353", {"start": v(572.98, 622.47) * mm, "end": v(572.08, 620.6) * mm});
            skLineSegment(sketch, "E1354", {"start": v(572.08, 620.6) * mm, "end": v(570.88, 618.29) * mm});
            skLineSegment(sketch, "E1355", {"start": v(570.88, 618.29) * mm, "end": v(569.38, 615.56) * mm});
            skLineSegment(sketch, "E1356", {"start": v(569.38, 615.56) * mm, "end": v(567.6, 612.46) * mm});
            skLineSegment(sketch, "E1357", {"start": v(567.6, 612.46) * mm, "end": v(565.53, 609.02) * mm});
            skLineSegment(sketch, "E1358", {"start": v(565.53, 609.02) * mm, "end": v(563.19, 605.28) * mm});
            skLineSegment(sketch, "E1359", {"start": v(563.19, 605.28) * mm, "end": v(560.6, 601.28) * mm});
            skLineSegment(sketch, "E1360", {"start": v(560.6, 601.28) * mm, "end": v(557.74, 597.06) * mm});
            skLineSegment(sketch, "E1361", {"start": v(557.74, 597.06) * mm, "end": v(554.64, 592.64) * mm});
            skLineSegment(sketch, "E1362", {"start": v(554.64, 592.64) * mm, "end": v(551.31, 588.07) * mm});
            skLineSegment(sketch, "E1363", {"start": v(551.31, 588.07) * mm, "end": v(547.75, 583.4) * mm});
            skLineSegment(sketch, "E1364", {"start": v(547.75, 583.4) * mm, "end": v(543.98, 578.64) * mm});
            skLineSegment(sketch, "E1365", {"start": v(543.98, 578.64) * mm, "end": v(540, 573.84) * mm});
            skLineSegment(sketch, "E1366", {"start": v(540, 573.84) * mm, "end": v(535.82, 569.05) * mm});
            skLineSegment(sketch, "E1367", {"start": v(535.82, 569.05) * mm, "end": v(531.45, 564.28) * mm});
            skLineSegment(sketch, "E1368", {"start": v(531.45, 564.28) * mm, "end": v(526.9, 559.6) * mm});
            skLineSegment(sketch, "E1369", {"start": v(526.9, 559.6) * mm, "end": v(522.18, 555.01) * mm});
            skLineSegment(sketch, "E1370", {"start": v(522.18, 555.01) * mm, "end": v(517.3, 550.58) * mm});
            skLineSegment(sketch, "E1371", {"start": v(517.3, 550.58) * mm, "end": v(512.26, 546.33) * mm});
            skLineSegment(sketch, "E1372", {"start": v(512.26, 546.33) * mm, "end": v(507.07, 542.3) * mm});
            skLineSegment(sketch, "E1373", {"start": v(507.07, 542.3) * mm, "end": v(501.75, 538.53) * mm});
            skLineSegment(sketch, "E1374", {"start": v(501.75, 538.53) * mm, "end": v(496.3, 535.06) * mm});
            skLineSegment(sketch, "E1375", {"start": v(496.3, 535.06) * mm, "end": v(490.74, 531.92) * mm});
            skLineSegment(sketch, "E1376", {"start": v(490.74, 531.92) * mm, "end": v(485.07, 529.15) * mm});
            skLineSegment(sketch, "E1377", {"start": v(485.07, 529.15) * mm, "end": v(479.29, 526.8) * mm});
            skLineSegment(sketch, "E1378", {"start": v(479.29, 526.8) * mm, "end": v(473.42, 524.88) * mm});
            skLineSegment(sketch, "E1379", {"start": v(473.42, 524.88) * mm, "end": v(467.48, 523.44) * mm});
            skLineSegment(sketch, "E1380", {"start": v(467.48, 523.44) * mm, "end": v(461.45, 522.53) * mm});
            skLineSegment(sketch, "E1381", {"start": v(461.45, 522.53) * mm, "end": v(455.37, 522.17) * mm});
            skLineSegment(sketch, "E1382", {"start": v(455.37, 522.17) * mm, "end": v(449.23, 522.4) * mm});
            skLineSegment(sketch, "E1383", {"start": v(449.23, 522.4) * mm, "end": v(444.57, 522.98) * mm});
            skLineSegment(sketch, "E1384", {"start": v(444.57, 522.98) * mm, "end": v(443.04, 523.27) * mm});
            skLineSegment(sketch, "E1385", {"start": v(443.04, 523.27) * mm, "end": v(440, 523.86) * mm});
            skLineSegment(sketch, "E1386", {"start": v(440, 523.86) * mm, "end": v(430.93, 526.11) * mm});
            skLineSegment(sketch, "E1387", {"start": v(430.93, 526.11) * mm, "end": v(419.43, 529.77) * mm});
            skLineSegment(sketch, "E1388", {"start": v(419.43, 529.77) * mm, "end": v(408.52, 534.1) * mm});
            skLineSegment(sketch, "E1389", {"start": v(408.52, 534.1) * mm, "end": v(398.19, 539) * mm});
            skLineSegment(sketch, "E1390", {"start": v(398.19, 539) * mm, "end": v(388.44, 544.35) * mm});
            skLineSegment(sketch, "E1391", {"start": v(388.44, 544.35) * mm, "end": v(379.26, 550) * mm});
            skLineSegment(sketch, "E1392", {"start": v(379.26, 550) * mm, "end": v(370.64, 555.84) * mm});
            skLineSegment(sketch, "E1393", {"start": v(370.64, 555.84) * mm, "end": v(362.56, 561.74) * mm});
            skLineSegment(sketch, "E1394", {"start": v(362.56, 561.74) * mm, "end": v(355.03, 567.59) * mm});
            skLineSegment(sketch, "E1395", {"start": v(355.03, 567.59) * mm, "end": v(348.02, 573.24) * mm});
            skLineSegment(sketch, "E1396", {"start": v(348.02, 573.24) * mm, "end": v(341.54, 578.57) * mm});
            skLineSegment(sketch, "E1397", {"start": v(341.54, 578.57) * mm, "end": v(335.57, 583.47) * mm});
            skLineSegment(sketch, "E1398", {"start": v(335.57, 583.47) * mm, "end": v(330.1, 587.81) * mm});
            skLineSegment(sketch, "E1399", {"start": v(330.1, 587.81) * mm, "end": v(325.12, 591.46) * mm});
            skLineSegment(sketch, "E1400", {"start": v(325.12, 591.46) * mm, "end": v(320.63, 594.3) * mm});
            skLineSegment(sketch, "E1401", {"start": v(320.63, 594.3) * mm, "end": v(317.64, 595.82) * mm});
            skLineSegment(sketch, "E1402", {"start": v(317.64, 595.82) * mm, "end": v(316.6, 596.2) * mm});
            skLineSegment(sketch, "E1403", {"start": v(316.6, 596.2) * mm, "end": v(315.46, 596.62) * mm});
            skLineSegment(sketch, "E1404", {"start": v(315.46, 596.62) * mm, "end": v(312.03, 597.83) * mm});
            skLineSegment(sketch, "E1405", {"start": v(312.03, 597.83) * mm, "end": v(305.92, 599.92) * mm});
            skLineSegment(sketch, "E1406", {"start": v(305.92, 599.92) * mm, "end": v(298.4, 602.38) * mm});
            skLineSegment(sketch, "E1407", {"start": v(298.4, 602.38) * mm, "end": v(289.58, 605.14) * mm});
            skLineSegment(sketch, "E1408", {"start": v(289.58, 605.14) * mm, "end": v(279.55, 608.12) * mm});
            skLineSegment(sketch, "E1409", {"start": v(279.55, 608.12) * mm, "end": v(268.41, 611.26) * mm});
            skLineSegment(sketch, "E1410", {"start": v(268.41, 611.26) * mm, "end": v(256.29, 614.46) * mm});
            skLineSegment(sketch, "E1411", {"start": v(256.29, 614.46) * mm, "end": v(243.27, 617.66) * mm});
            skLineSegment(sketch, "E1412", {"start": v(243.27, 617.66) * mm, "end": v(229.47, 620.79) * mm});
            skLineSegment(sketch, "E1413", {"start": v(229.47, 620.79) * mm, "end": v(214.98, 623.76) * mm});
            skLineSegment(sketch, "E1414", {"start": v(214.98, 623.76) * mm, "end": v(199.93, 626.5) * mm});
            skLineSegment(sketch, "E1415", {"start": v(199.93, 626.5) * mm, "end": v(184.4, 628.95) * mm});
            skLineSegment(sketch, "E1416", {"start": v(184.4, 628.95) * mm, "end": v(168.52, 631) * mm});
            skLineSegment(sketch, "E1417", {"start": v(168.52, 631) * mm, "end": v(152.37, 632.62) * mm});
            skLineSegment(sketch, "E1418", {"start": v(152.37, 632.62) * mm, "end": v(136.07, 633.7) * mm});
            skLineSegment(sketch, "E1419", {"start": v(136.07, 633.7) * mm, "end": v(123.8, 634.13) * mm});
            skLineSegment(sketch, "E1420", {"start": v(123.8, 634.13) * mm, "end": v(119.71, 634.17) * mm});
            skLineSegment(sketch, "E1421", {"start": v(119.71, 634.17) * mm, "end": v(115.7, 634.2) * mm});
            skLineSegment(sketch, "E1422", {"start": v(115.7, 634.2) * mm, "end": v(103.67, 634.05) * mm});
            skLineSegment(sketch, "E1423", {"start": v(103.67, 634.05) * mm, "end": v(88.23, 633.44) * mm});
            skLineSegment(sketch, "E1424", {"start": v(88.23, 633.44) * mm, "end": v(73.37, 632.4) * mm});
            skLineSegment(sketch, "E1425", {"start": v(73.37, 632.4) * mm, "end": v(59.1, 630.97) * mm});
            skLineSegment(sketch, "E1426", {"start": v(59.1, 630.97) * mm, "end": v(45.4, 629.2) * mm});
            skLineSegment(sketch, "E1427", {"start": v(45.4, 629.2) * mm, "end": v(32.26, 627.17) * mm});
            skLineSegment(sketch, "E1428", {"start": v(32.26, 627.17) * mm, "end": v(19.68, 624.9) * mm});
            skLineSegment(sketch, "E1429", {"start": v(19.68, 624.9) * mm, "end": v(7.65, 622.47) * mm});
            skLineSegment(sketch, "E1430", {"start": v(7.65, 622.47) * mm, "end": v(-3.85, 619.92) * mm});
            skLineSegment(sketch, "E1431", {"start": v(-3.85, 619.92) * mm, "end": v(-14.8, 617.31) * mm});
            skLineSegment(sketch, "E1432", {"start": v(-14.8, 617.31) * mm, "end": v(-25.24, 614.7) * mm});
            skLineSegment(sketch, "E1433", {"start": v(-25.24, 614.7) * mm, "end": v(-35.15, 612.11) * mm});
            skLineSegment(sketch, "E1434", {"start": v(-35.15, 612.11) * mm, "end": v(-44.56, 609.64) * mm});
            skLineSegment(sketch, "E1435", {"start": v(-44.56, 609.64) * mm, "end": v(-53.46, 607.3) * mm});
            skLineSegment(sketch, "E1436", {"start": v(-53.46, 607.3) * mm, "end": v(-61.87, 605.19) * mm});
            skLineSegment(sketch, "E1437", {"start": v(-61.87, 605.19) * mm, "end": v(-67.8, 603.76) * mm});
            skLineSegment(sketch, "E1438", {"start": v(-67.8, 603.76) * mm, "end": v(-69.8, 603.32) * mm});
            skLineSegment(sketch, "E1439", {"start": v(-69.8, 603.32) * mm, "end": v(-70.64, 603.13) * mm});
            skLineSegment(sketch, "E1440", {"start": v(-70.64, 603.13) * mm, "end": v(-73.21, 602.74) * mm});
            skLineSegment(sketch, "E1441", {"start": v(-73.21, 602.74) * mm, "end": v(-78.61, 602.05) * mm});
            skLineSegment(sketch, "E1442", {"start": v(-78.61, 602.05) * mm, "end": v(-85.73, 601.28) * mm});
            skLineSegment(sketch, "E1443", {"start": v(-85.73, 601.28) * mm, "end": v(-94.28, 600.46) * mm});
            skLineSegment(sketch, "E1444", {"start": v(-94.28, 600.46) * mm, "end": v(-104, 599.6) * mm});
            skLineSegment(sketch, "E1445", {"start": v(-104, 599.6) * mm, "end": v(-114.6, 598.72) * mm});
            skLineSegment(sketch, "E1446", {"start": v(-114.6, 598.72) * mm, "end": v(-125.83, 597.85) * mm});
            skLineSegment(sketch, "E1447", {"start": v(-125.83, 597.85) * mm, "end": v(-137.4, 597.02) * mm});
            skLineSegment(sketch, "E1448", {"start": v(-137.4, 597.02) * mm, "end": v(-149.05, 596.24) * mm});
            skLineSegment(sketch, "E1449", {"start": v(-149.05, 596.24) * mm, "end": v(-160.49, 595.53) * mm});
            skLineSegment(sketch, "E1450", {"start": v(-160.49, 595.53) * mm, "end": v(-171.45, 594.93) * mm});
            skLineSegment(sketch, "E1451", {"start": v(-171.45, 594.93) * mm, "end": v(-181.67, 594.45) * mm});
            skLineSegment(sketch, "E1452", {"start": v(-181.67, 594.45) * mm, "end": v(-190.87, 594.12) * mm});
            skLineSegment(sketch, "E1453", {"start": v(-190.87, 594.12) * mm, "end": v(-198.77, 593.96) * mm});
            skLineSegment(sketch, "E1454", {"start": v(-198.77, 593.96) * mm, "end": v(-205.1, 593.99) * mm});
            skLineSegment(sketch, "E1455", {"start": v(-205.1, 593.99) * mm, "end": v(-208.47, 594.11) * mm});
            skLineSegment(sketch, "E1456", {"start": v(-208.47, 594.11) * mm, "end": v(-209.59, 594.23) * mm});
            skLineSegment(sketch, "E1457", {"start": v(-209.59, 594.23) * mm, "end": v(-212.92, 594.57) * mm});
            skLineSegment(sketch, "E1458", {"start": v(-212.92, 594.57) * mm, "end": v(-222.87, 595.83) * mm});
            skLineSegment(sketch, "E1459", {"start": v(-222.87, 595.83) * mm, "end": v(-234.77, 597.72) * mm});
            skLineSegment(sketch, "E1460", {"start": v(-234.77, 597.72) * mm, "end": v(-245.4, 599.86) * mm});
            skLineSegment(sketch, "E1461", {"start": v(-245.4, 599.86) * mm, "end": v(-254.87, 602.2) * mm});
            skLineSegment(sketch, "E1462", {"start": v(-254.87, 602.2) * mm, "end": v(-263.27, 604.7) * mm});
            skLineSegment(sketch, "E1463", {"start": v(-263.27, 604.7) * mm, "end": v(-270.71, 607.31) * mm});
            skLineSegment(sketch, "E1464", {"start": v(-270.71, 607.31) * mm, "end": v(-277.3, 609.99) * mm});
            skLineSegment(sketch, "E1465", {"start": v(-277.3, 609.99) * mm, "end": v(-283.12, 612.69) * mm});
            skLineSegment(sketch, "E1466", {"start": v(-283.12, 612.69) * mm, "end": v(-288.31, 615.37) * mm});
            skLineSegment(sketch, "E1467", {"start": v(-288.31, 615.37) * mm, "end": v(-292.95, 617.97) * mm});
            skLineSegment(sketch, "E1468", {"start": v(-292.95, 617.97) * mm, "end": v(-297.15, 620.47) * mm});
            skLineSegment(sketch, "E1469", {"start": v(-297.15, 620.47) * mm, "end": v(-301.02, 622.8) * mm});
            skLineSegment(sketch, "E1470", {"start": v(-301.02, 622.8) * mm, "end": v(-304.65, 624.94) * mm});
            skLineSegment(sketch, "E1471", {"start": v(-304.65, 624.94) * mm, "end": v(-308.15, 626.82) * mm});
            skLineSegment(sketch, "E1472", {"start": v(-308.15, 626.82) * mm, "end": v(-311.63, 628.41) * mm});
            skLineSegment(sketch, "E1473", {"start": v(-311.63, 628.41) * mm, "end": v(-314.28, 629.4) * mm});
            skLineSegment(sketch, "E1474", {"start": v(-314.28, 629.4) * mm, "end": v(-315.19, 629.66) * mm});
            skLineSegment(sketch, "E1475", {"start": v(-315.19, 629.66) * mm, "end": v(-315.7, 629.81) * mm});
            skLineSegment(sketch, "E1476", {"start": v(-315.7, 629.81) * mm, "end": v(-317.23, 630.2) * mm});
            skLineSegment(sketch, "E1477", {"start": v(-317.23, 630.2) * mm, "end": v(-319.11, 630.53) * mm});
            skLineSegment(sketch, "E1478", {"start": v(-319.11, 630.53) * mm, "end": v(-320.87, 630.69) * mm});
            skLineSegment(sketch, "E1479", {"start": v(-320.87, 630.69) * mm, "end": v(-322.53, 630.69) * mm});
            skLineSegment(sketch, "E1480", {"start": v(-322.53, 630.69) * mm, "end": v(-324.12, 630.54) * mm});
            skLineSegment(sketch, "E1481", {"start": v(-324.12, 630.54) * mm, "end": v(-325.7, 630.28) * mm});
            skLineSegment(sketch, "E1482", {"start": v(-325.7, 630.28) * mm, "end": v(-327.27, 629.9) * mm});
            skLineSegment(sketch, "E1483", {"start": v(-327.27, 629.9) * mm, "end": v(-328.89, 629.42) * mm});
            skLineSegment(sketch, "E1484", {"start": v(-328.89, 629.42) * mm, "end": v(-330.58, 628.87) * mm});
            skLineSegment(sketch, "E1485", {"start": v(-330.58, 628.87) * mm, "end": v(-332.38, 628.25) * mm});
            skLineSegment(sketch, "E1486", {"start": v(-332.38, 628.25) * mm, "end": v(-334.32, 627.58) * mm});
            skLineSegment(sketch, "E1487", {"start": v(-334.32, 627.58) * mm, "end": v(-336.44, 626.88) * mm});
            skLineSegment(sketch, "E1488", {"start": v(-336.44, 626.88) * mm, "end": v(-338.77, 626.17) * mm});
            skLineSegment(sketch, "E1489", {"start": v(-338.77, 626.17) * mm, "end": v(-341.34, 625.45) * mm});
            skLineSegment(sketch, "E1490", {"start": v(-341.34, 625.45) * mm, "end": v(-344.2, 624.75) * mm});
            skLineSegment(sketch, "E1491", {"start": v(-344.2, 624.75) * mm, "end": v(-347.36, 624.09) * mm});
            skLineSegment(sketch, "E1492", {"start": v(-347.36, 624.09) * mm, "end": v(-350.86, 623.47) * mm});
            skLineSegment(sketch, "E1493", {"start": v(-350.86, 623.47) * mm, "end": v(-354.75, 622.91) * mm});
            skLineSegment(sketch, "E1494", {"start": v(-354.75, 622.91) * mm, "end": v(-359.04, 622.44) * mm});
            skLineSegment(sketch, "E1495", {"start": v(-359.04, 622.44) * mm, "end": v(-363.79, 622.06) * mm});
            skLineSegment(sketch, "E1496", {"start": v(-363.79, 622.06) * mm, "end": v(-369, 621.79) * mm});
            skLineSegment(sketch, "E1497", {"start": v(-369, 621.79) * mm, "end": v(-374.75, 621.65) * mm});
            skLineSegment(sketch, "E1498", {"start": v(-374.75, 621.65) * mm, "end": v(-381.03, 621.65) * mm});
            skLineSegment(sketch, "E1499", {"start": v(-381.03, 621.65) * mm, "end": v(-387.9, 621.8) * mm});
            skLineSegment(sketch, "E1500", {"start": v(-387.9, 621.8) * mm, "end": v(-395.38, 622.15) * mm});
            skLineSegment(sketch, "E1501", {"start": v(-395.38, 622.15) * mm, "end": v(-403.5, 622.68) * mm});
            skLineSegment(sketch, "E1502", {"start": v(-403.5, 622.68) * mm, "end": v(-412.32, 623.4) * mm});
            skLineSegment(sketch, "E1503", {"start": v(-412.32, 623.4) * mm, "end": v(-421.85, 624.36) * mm});
            skLineSegment(sketch, "E1504", {"start": v(-421.85, 624.36) * mm, "end": v(-432.13, 625.56) * mm});
            skLineSegment(sketch, "E1505", {"start": v(-432.13, 625.56) * mm, "end": v(-443.2, 627.01) * mm});
            skLineSegment(sketch, "E1506", {"start": v(-443.2, 627.01) * mm, "end": v(-455.08, 628.74) * mm});
            skLineSegment(sketch, "E1507", {"start": v(-455.08, 628.74) * mm, "end": v(-464.63, 630.22) * mm});
            skLineSegment(sketch, "E1508", {"start": v(-464.63, 630.22) * mm, "end": v(-467.8, 630.74) * mm});
            skLineSegment(sketch, "E1509", {"start": v(-467.8, 630.74) * mm, "end": v(-469.45, 631.01) * mm});
            skLineSegment(sketch, "E1510", {"start": v(-469.45, 631.01) * mm, "end": v(-474.36, 631.82) * mm});
            skLineSegment(sketch, "E1511", {"start": v(-474.36, 631.82) * mm, "end": v(-481.81, 633.05) * mm});
            skLineSegment(sketch, "E1512", {"start": v(-481.81, 633.05) * mm, "end": v(-490.03, 634.42) * mm});
            skLineSegment(sketch, "E1513", {"start": v(-490.03, 634.42) * mm, "end": v(-498.9, 635.9) * mm});
            skLineSegment(sketch, "E1514", {"start": v(-498.9, 635.9) * mm, "end": v(-508.26, 637.5) * mm});
            skLineSegment(sketch, "E1515", {"start": v(-508.26, 637.5) * mm, "end": v(-518, 639.19) * mm});
            skLineSegment(sketch, "E1516", {"start": v(-518, 639.19) * mm, "end": v(-528, 640.95) * mm});
            skLineSegment(sketch, "E1517", {"start": v(-528, 640.95) * mm, "end": v(-538.1, 642.76) * mm});
            skLineSegment(sketch, "E1518", {"start": v(-538.1, 642.76) * mm, "end": v(-548.2, 644.6) * mm});
            skLineSegment(sketch, "E1519", {"start": v(-548.2, 644.6) * mm, "end": v(-558.16, 646.48) * mm});
            skLineSegment(sketch, "E1520", {"start": v(-558.16, 646.48) * mm, "end": v(-567.84, 648.36) * mm});
            skLineSegment(sketch, "E1521", {"start": v(-567.84, 648.36) * mm, "end": v(-577.12, 650.22) * mm});
            skLineSegment(sketch, "E1522", {"start": v(-577.12, 650.22) * mm, "end": v(-585.86, 652.06) * mm});
            skLineSegment(sketch, "E1523", {"start": v(-585.86, 652.06) * mm, "end": v(-593.94, 653.85) * mm});
            skLineSegment(sketch, "E1524", {"start": v(-593.94, 653.85) * mm, "end": v(-601.22, 655.57) * mm});
            skLineSegment(sketch, "E1525", {"start": v(-601.22, 655.57) * mm, "end": v(-606, 656.8) * mm});
            skLineSegment(sketch, "E1526", {"start": v(-606, 656.8) * mm, "end": v(-607.57, 657.22) * mm});
            skLineSegment(sketch, "E1527", {"start": v(605.27, 647.13) * mm, "end": v(601.54, 644.31) * mm});
            skLineSegment(sketch, "E1528", {"start": v(601.54, 644.31) * mm, "end": v(601.2, 644.06) * mm});
            skLineSegment(sketch, "E1529", {"start": v(601.2, 644.06) * mm, "end": v(600.24, 643.24) * mm});
            skLineSegment(sketch, "E1530", {"start": v(600.24, 643.24) * mm, "end": v(599.14, 642.09) * mm});
            skLineSegment(sketch, "E1531", {"start": v(599.14, 642.09) * mm, "end": v(598.21, 640.77) * mm});
            skLineSegment(sketch, "E1532", {"start": v(598.21, 640.77) * mm, "end": v(597.46, 639.2) * mm});
            skLineSegment(sketch, "E1533", {"start": v(597.46, 639.2) * mm, "end": v(596.86, 637.3) * mm});
            skLineSegment(sketch, "E1534", {"start": v(596.86, 637.3) * mm, "end": v(596.4, 634.99) * mm});
            skLineSegment(sketch, "E1535", {"start": v(596.4, 634.99) * mm, "end": v(596.09, 632.18) * mm});
            skLineSegment(sketch, "E1536", {"start": v(596.09, 632.18) * mm, "end": v(595.93, 629.64) * mm});
            skLineSegment(sketch, "E1537", {"start": v(595.93, 629.64) * mm, "end": v(595.9, 628.79) * mm});
            skLineSegment(sketch, "E1538", {"start": v(595.9, 628.79) * mm, "end": v(595.88, 628.27) * mm});
            skLineSegment(sketch, "E1539", {"start": v(595.88, 628.27) * mm, "end": v(595.7, 626.73) * mm});
            skLineSegment(sketch, "E1540", {"start": v(595.7, 626.73) * mm, "end": v(595.24, 624.27) * mm});
            skLineSegment(sketch, "E1541", {"start": v(595.24, 624.27) * mm, "end": v(594.5, 621.43) * mm});
            skLineSegment(sketch, "E1542", {"start": v(594.5, 621.43) * mm, "end": v(593.49, 618.2) * mm});
            skLineSegment(sketch, "E1543", {"start": v(593.49, 618.2) * mm, "end": v(592.2, 614.6) * mm});
            skLineSegment(sketch, "E1544", {"start": v(592.2, 614.6) * mm, "end": v(590.63, 610.66) * mm});
            skLineSegment(sketch, "E1545", {"start": v(590.63, 610.66) * mm, "end": v(588.78, 606.37) * mm});
            skLineSegment(sketch, "E1546", {"start": v(588.78, 606.37) * mm, "end": v(586.65, 601.75) * mm});
            skLineSegment(sketch, "E1547", {"start": v(586.65, 601.75) * mm, "end": v(584.22, 596.81) * mm});
            skLineSegment(sketch, "E1548", {"start": v(584.22, 596.81) * mm, "end": v(581.5, 591.57) * mm});
            skLineSegment(sketch, "E1549", {"start": v(581.5, 591.57) * mm, "end": v(578.5, 586.02) * mm});
            skLineSegment(sketch, "E1550", {"start": v(578.5, 586.02) * mm, "end": v(575.19, 580.2) * mm});
            skLineSegment(sketch, "E1551", {"start": v(575.19, 580.2) * mm, "end": v(571.58, 574.1) * mm});
            skLineSegment(sketch, "E1552", {"start": v(571.58, 574.1) * mm, "end": v(567.67, 567.75) * mm});
            skLineSegment(sketch, "E1553", {"start": v(567.67, 567.75) * mm, "end": v(563.45, 561.15) * mm});
            skLineSegment(sketch, "E1554", {"start": v(563.45, 561.15) * mm, "end": v(560.07, 556.01) * mm});
            skLineSegment(sketch, "E1555", {"start": v(560.07, 556.01) * mm, "end": v(558.92, 554.3) * mm});
            skLineSegment(sketch, "E1556", {"start": v(558.92, 554.3) * mm, "end": v(557.75, 552.57) * mm});
            skLineSegment(sketch, "E1557", {"start": v(557.75, 552.57) * mm, "end": v(554, 547.5) * mm});
            skLineSegment(sketch, "E1558", {"start": v(554, 547.5) * mm, "end": v(548.6, 540.98) * mm});
            skLineSegment(sketch, "E1559", {"start": v(548.6, 540.98) * mm, "end": v(542.85, 534.78) * mm});
            skLineSegment(sketch, "E1560", {"start": v(542.85, 534.78) * mm, "end": v(536.79, 528.91) * mm});
            skLineSegment(sketch, "E1561", {"start": v(536.79, 528.91) * mm, "end": v(530.49, 523.4) * mm});
            skLineSegment(sketch, "E1562", {"start": v(530.49, 523.4) * mm, "end": v(524.03, 518.27) * mm});
            skLineSegment(sketch, "E1563", {"start": v(524.03, 518.27) * mm, "end": v(517.49, 513.53) * mm});
            skLineSegment(sketch, "E1564", {"start": v(517.49, 513.53) * mm, "end": v(510.92, 509.21) * mm});
            skLineSegment(sketch, "E1565", {"start": v(510.92, 509.21) * mm, "end": v(504.4, 505.32) * mm});
            skLineSegment(sketch, "E1566", {"start": v(504.4, 505.32) * mm, "end": v(498.02, 501.9) * mm});
            skLineSegment(sketch, "E1567", {"start": v(498.02, 501.9) * mm, "end": v(491.84, 498.94) * mm});
            skLineSegment(sketch, "E1568", {"start": v(491.84, 498.94) * mm, "end": v(485.93, 496.48) * mm});
            skLineSegment(sketch, "E1569", {"start": v(485.93, 496.48) * mm, "end": v(480.36, 494.54) * mm});
            skLineSegment(sketch, "E1570", {"start": v(480.36, 494.54) * mm, "end": v(475.2, 493.14) * mm});
            skLineSegment(sketch, "E1571", {"start": v(475.2, 493.14) * mm, "end": v(470.53, 492.29) * mm});
            skLineSegment(sketch, "E1572", {"start": v(470.53, 492.29) * mm, "end": v(467.45, 492.01) * mm});
            skLineSegment(sketch, "E1573", {"start": v(467.45, 492.01) * mm, "end": v(466.42, 492.01) * mm});
            skLineSegment(sketch, "E1574", {"start": v(466.42, 492.01) * mm, "end": v(464.84, 492.02) * mm});
            skLineSegment(sketch, "E1575", {"start": v(464.84, 492.02) * mm, "end": v(460.1, 492.38) * mm});
            skLineSegment(sketch, "E1576", {"start": v(460.1, 492.38) * mm, "end": v(453.7, 493.34) * mm});
            skLineSegment(sketch, "E1577", {"start": v(453.7, 493.34) * mm, "end": v(447.28, 494.81) * mm});
            skLineSegment(sketch, "E1578", {"start": v(447.28, 494.81) * mm, "end": v(440.9, 496.73) * mm});
            skLineSegment(sketch, "E1579", {"start": v(440.9, 496.73) * mm, "end": v(434.6, 499.01) * mm});
            skLineSegment(sketch, "E1580", {"start": v(434.6, 499.01) * mm, "end": v(428.48, 501.57) * mm});
            skLineSegment(sketch, "E1581", {"start": v(428.48, 501.57) * mm, "end": v(422.56, 504.33) * mm});
            skLineSegment(sketch, "E1582", {"start": v(422.56, 504.33) * mm, "end": v(416.92, 507.2) * mm});
            skLineSegment(sketch, "E1583", {"start": v(416.92, 507.2) * mm, "end": v(411.62, 510.13) * mm});
            skLineSegment(sketch, "E1584", {"start": v(411.62, 510.13) * mm, "end": v(406.7, 513.01) * mm});
            skLineSegment(sketch, "E1585", {"start": v(406.7, 513.01) * mm, "end": v(402.25, 515.78) * mm});
            skLineSegment(sketch, "E1586", {"start": v(402.25, 515.78) * mm, "end": v(398.3, 518.35) * mm});
            skLineSegment(sketch, "E1587", {"start": v(398.3, 518.35) * mm, "end": v(394.92, 520.64) * mm});
            skLineSegment(sketch, "E1588", {"start": v(394.92, 520.64) * mm, "end": v(392.18, 522.58) * mm});
            skLineSegment(sketch, "E1589", {"start": v(392.18, 522.58) * mm, "end": v(390.12, 524.08) * mm});
            skLineSegment(sketch, "E1590", {"start": v(390.12, 524.08) * mm, "end": v(389.14, 524.82) * mm});
            skLineSegment(sketch, "E1591", {"start": v(389.14, 524.82) * mm, "end": v(388.82, 525.07) * mm});
            skLineSegment(sketch, "E1592", {"start": v(388.82, 525.07) * mm, "end": v(386.2, 527.1) * mm});
            skLineSegment(sketch, "E1593", {"start": v(386.2, 527.1) * mm, "end": v(378.34, 533.12) * mm});
            skLineSegment(sketch, "E1594", {"start": v(378.34, 533.12) * mm, "end": v(368.78, 540.41) * mm});
            skLineSegment(sketch, "E1595", {"start": v(368.78, 540.41) * mm, "end": v(360.05, 546.99) * mm});
            skLineSegment(sketch, "E1596", {"start": v(360.05, 546.99) * mm, "end": v(352.1, 552.9) * mm});
            skLineSegment(sketch, "E1597", {"start": v(352.1, 552.9) * mm, "end": v(344.84, 558.19) * mm});
            skLineSegment(sketch, "E1598", {"start": v(344.84, 558.19) * mm, "end": v(338.22, 562.9) * mm});
            skLineSegment(sketch, "E1599", {"start": v(338.22, 562.9) * mm, "end": v(332.16, 567.1) * mm});
            skLineSegment(sketch, "E1600", {"start": v(332.16, 567.1) * mm, "end": v(326.6, 570.8) * mm});
            skLineSegment(sketch, "E1601", {"start": v(326.6, 570.8) * mm, "end": v(321.45, 574.07) * mm});
            skLineSegment(sketch, "E1602", {"start": v(321.45, 574.07) * mm, "end": v(316.66, 576.95) * mm});
            skLineSegment(sketch, "E1603", {"start": v(316.66, 576.95) * mm, "end": v(312.15, 579.49) * mm});
            skLineSegment(sketch, "E1604", {"start": v(312.15, 579.49) * mm, "end": v(307.85, 581.73) * mm});
            skLineSegment(sketch, "E1605", {"start": v(307.85, 581.73) * mm, "end": v(303.7, 583.72) * mm});
            skLineSegment(sketch, "E1606", {"start": v(303.7, 583.72) * mm, "end": v(299.63, 585.51) * mm});
            skLineSegment(sketch, "E1607", {"start": v(299.63, 585.51) * mm, "end": v(295.56, 587.14) * mm});
            skLineSegment(sketch, "E1608", {"start": v(295.56, 587.14) * mm, "end": v(292.47, 588.3) * mm});
            skLineSegment(sketch, "E1609", {"start": v(292.47, 588.3) * mm, "end": v(291.43, 588.66) * mm});
            skLineSegment(sketch, "E1610", {"start": v(291.43, 588.66) * mm, "end": v(290.5, 588.99) * mm});
            skLineSegment(sketch, "E1611", {"start": v(290.5, 588.99) * mm, "end": v(287.73, 589.97) * mm});
            skLineSegment(sketch, "E1612", {"start": v(287.73, 589.97) * mm, "end": v(284.89, 590.96) * mm});
            skLineSegment(sketch, "E1613", {"start": v(284.89, 590.96) * mm, "end": v(282.7, 591.69) * mm});
            skLineSegment(sketch, "E1614", {"start": v(282.7, 591.69) * mm, "end": v(280.96, 592.21) * mm});
            skLineSegment(sketch, "E1615", {"start": v(280.96, 592.21) * mm, "end": v(279.5, 592.59) * mm});
            skLineSegment(sketch, "E1616", {"start": v(279.5, 592.59) * mm, "end": v(278.08, 592.87) * mm});
            skLineSegment(sketch, "E1617", {"start": v(278.08, 592.87) * mm, "end": v(276.55, 593.12) * mm});
            skLineSegment(sketch, "E1618", {"start": v(276.55, 593.12) * mm, "end": v(274.68, 593.38) * mm});
            skLineSegment(sketch, "E1619", {"start": v(274.68, 593.38) * mm, "end": v(272.3, 593.7) * mm});
            skLineSegment(sketch, "E1620", {"start": v(272.3, 593.7) * mm, "end": v(269.18, 594.17) * mm});
            skLineSegment(sketch, "E1621", {"start": v(269.18, 594.17) * mm, "end": v(265.16, 594.8) * mm});
            skLineSegment(sketch, "E1622", {"start": v(265.16, 594.8) * mm, "end": v(260.02, 595.69) * mm});
            skLineSegment(sketch, "E1623", {"start": v(260.02, 595.69) * mm, "end": v(253.58, 596.86) * mm});
            skLineSegment(sketch, "E1624", {"start": v(253.58, 596.86) * mm, "end": v(245.62, 598.38) * mm});
            skLineSegment(sketch, "E1625", {"start": v(245.62, 598.38) * mm, "end": v(235.97, 600.3) * mm});
            skLineSegment(sketch, "E1626", {"start": v(235.97, 600.3) * mm, "end": v(227.3, 602.08) * mm});
            skLineSegment(sketch, "E1627", {"start": v(227.3, 602.08) * mm, "end": v(224.42, 602.68) * mm});
            skLineSegment(sketch, "E1628", {"start": v(224.42, 602.68) * mm, "end": v(221.46, 603.3) * mm});
            skLineSegment(sketch, "E1629", {"start": v(221.46, 603.3) * mm, "end": v(212.57, 605.17) * mm});
            skLineSegment(sketch, "E1630", {"start": v(212.57, 605.17) * mm, "end": v(202.05, 607.4) * mm});
            skLineSegment(sketch, "E1631", {"start": v(202.05, 607.4) * mm, "end": v(192.73, 609.38) * mm});
            skLineSegment(sketch, "E1632", {"start": v(192.73, 609.38) * mm, "end": v(184.5, 611.12) * mm});
            skLineSegment(sketch, "E1633", {"start": v(184.5, 611.12) * mm, "end": v(177.22, 612.65) * mm});
            skLineSegment(sketch, "E1634", {"start": v(177.22, 612.65) * mm, "end": v(170.77, 613.96) * mm});
            skLineSegment(sketch, "E1635", {"start": v(170.77, 613.96) * mm, "end": v(165.02, 615.1) * mm});
            skLineSegment(sketch, "E1636", {"start": v(165.02, 615.1) * mm, "end": v(159.84, 616.06) * mm});
            skLineSegment(sketch, "E1637", {"start": v(159.84, 616.06) * mm, "end": v(155.11, 616.86) * mm});
            skLineSegment(sketch, "E1638", {"start": v(155.11, 616.86) * mm, "end": v(150.7, 617.52) * mm});
            skLineSegment(sketch, "E1639", {"start": v(150.7, 617.52) * mm, "end": v(146.5, 618.06) * mm});
            skLineSegment(sketch, "E1640", {"start": v(146.5, 618.06) * mm, "end": v(142.36, 618.48) * mm});
            skLineSegment(sketch, "E1641", {"start": v(142.36, 618.48) * mm, "end": v(138.16, 618.81) * mm});
            skLineSegment(sketch, "E1642", {"start": v(138.16, 618.81) * mm, "end": v(133.78, 619.06) * mm});
            skLineSegment(sketch, "E1643", {"start": v(133.78, 619.06) * mm, "end": v(129.08, 619.25) * mm});
            skLineSegment(sketch, "E1644", {"start": v(129.08, 619.25) * mm, "end": v(125.23, 619.35) * mm});
            skLineSegment(sketch, "E1645", {"start": v(125.23, 619.35) * mm, "end": v(123.95, 619.38) * mm});
            skLineSegment(sketch, "E1646", {"start": v(123.95, 619.38) * mm, "end": v(122.61, 619.4) * mm});
            skLineSegment(sketch, "E1647", {"start": v(122.61, 619.4) * mm, "end": v(118.6, 619.43) * mm});
            skLineSegment(sketch, "E1648", {"start": v(118.6, 619.43) * mm, "end": v(113.25, 619.35) * mm});
            skLineSegment(sketch, "E1649", {"start": v(113.25, 619.35) * mm, "end": v(107.83, 619.12) * mm});
            skLineSegment(sketch, "E1650", {"start": v(107.83, 619.12) * mm, "end": v(102.22, 618.73) * mm});
            skLineSegment(sketch, "E1651", {"start": v(102.22, 618.73) * mm, "end": v(96.34, 618.17) * mm});
            skLineSegment(sketch, "E1652", {"start": v(96.34, 618.17) * mm, "end": v(90.08, 617.42) * mm});
            skLineSegment(sketch, "E1653", {"start": v(90.08, 617.42) * mm, "end": v(83.36, 616.47) * mm});
            skLineSegment(sketch, "E1654", {"start": v(83.36, 616.47) * mm, "end": v(76.08, 615.3) * mm});
            skLineSegment(sketch, "E1655", {"start": v(76.08, 615.3) * mm, "end": v(68.14, 613.93) * mm});
            skLineSegment(sketch, "E1656", {"start": v(68.14, 613.93) * mm, "end": v(59.46, 612.3) * mm});
            skLineSegment(sketch, "E1657", {"start": v(59.46, 612.3) * mm, "end": v(49.93, 610.44) * mm});
            skLineSegment(sketch, "E1658", {"start": v(49.93, 610.44) * mm, "end": v(39.45, 608.32) * mm});
            skLineSegment(sketch, "E1659", {"start": v(39.45, 608.32) * mm, "end": v(27.94, 605.92) * mm});
            skLineSegment(sketch, "E1660", {"start": v(27.94, 605.92) * mm, "end": v(15.29, 603.23) * mm});
            skLineSegment(sketch, "E1661", {"start": v(15.29, 603.23) * mm, "end": v(1.41, 600.24) * mm});
            skLineSegment(sketch, "E1662", {"start": v(1.41, 600.24) * mm, "end": v(-9.98, 597.77) * mm});
            skLineSegment(sketch, "E1663", {"start": v(-9.98, 597.77) * mm, "end": v(-13.78, 596.95) * mm});
            skLineSegment(sketch, "E1664", {"start": v(-13.78, 596.95) * mm, "end": v(-17.81, 596.07) * mm});
            skLineSegment(sketch, "E1665", {"start": v(-17.81, 596.07) * mm, "end": v(-29.97, 593.71) * mm});
            skLineSegment(sketch, "E1666", {"start": v(-29.97, 593.71) * mm, "end": v(-46.65, 590.92) * mm});
            skLineSegment(sketch, "E1667", {"start": v(-46.65, 590.92) * mm, "end": v(-63.64, 588.52) * mm});
            skLineSegment(sketch, "E1668", {"start": v(-63.64, 588.52) * mm, "end": v(-80.8, 586.5) * mm});
            skLineSegment(sketch, "E1669", {"start": v(-80.8, 586.5) * mm, "end": v(-97.96, 584.85) * mm});
            skLineSegment(sketch, "E1670", {"start": v(-97.96, 584.85) * mm, "end": v(-114.95, 583.51) * mm});
            skLineSegment(sketch, "E1671", {"start": v(-114.95, 583.51) * mm, "end": v(-131.6, 582.48) * mm});
            skLineSegment(sketch, "E1672", {"start": v(-131.6, 582.48) * mm, "end": v(-147.77, 581.73) * mm});
            skLineSegment(sketch, "E1673", {"start": v(-147.77, 581.73) * mm, "end": v(-163.27, 581.22) * mm});
            skLineSegment(sketch, "E1674", {"start": v(-163.27, 581.22) * mm, "end": v(-177.96, 580.94) * mm});
            skLineSegment(sketch, "E1675", {"start": v(-177.96, 580.94) * mm, "end": v(-191.66, 580.86) * mm});
            skLineSegment(sketch, "E1676", {"start": v(-191.66, 580.86) * mm, "end": v(-204.2, 580.94) * mm});
            skLineSegment(sketch, "E1677", {"start": v(-204.2, 580.94) * mm, "end": v(-215.45, 581.17) * mm});
            skLineSegment(sketch, "E1678", {"start": v(-215.45, 581.17) * mm, "end": v(-225.21, 581.53) * mm});
            skLineSegment(sketch, "E1679", {"start": v(-225.21, 581.53) * mm, "end": v(-233.34, 581.97) * mm});
            skLineSegment(sketch, "E1680", {"start": v(-233.34, 581.97) * mm, "end": v(-238.08, 582.33) * mm});
            skLineSegment(sketch, "E1681", {"start": v(-238.08, 582.33) * mm, "end": v(-239.66, 582.48) * mm});
            skLineSegment(sketch, "E1682", {"start": v(-239.66, 582.48) * mm, "end": v(-241.19, 582.64) * mm});
            skLineSegment(sketch, "E1683", {"start": v(-241.19, 582.64) * mm, "end": v(-245.76, 583.33) * mm});
            skLineSegment(sketch, "E1684", {"start": v(-245.76, 583.33) * mm, "end": v(-251.97, 584.63) * mm});
            skLineSegment(sketch, "E1685", {"start": v(-251.97, 584.63) * mm, "end": v(-258.22, 586.32) * mm});
            skLineSegment(sketch, "E1686", {"start": v(-258.22, 586.32) * mm, "end": v(-264.47, 588.31) * mm});
            skLineSegment(sketch, "E1687", {"start": v(-264.47, 588.31) * mm, "end": v(-270.67, 590.56) * mm});
            skLineSegment(sketch, "E1688", {"start": v(-270.67, 590.56) * mm, "end": v(-276.76, 593) * mm});
            skLineSegment(sketch, "E1689", {"start": v(-276.76, 593) * mm, "end": v(-282.69, 595.55) * mm});
            skLineSegment(sketch, "E1690", {"start": v(-282.69, 595.55) * mm, "end": v(-288.4, 598.16) * mm});
            skLineSegment(sketch, "E1691", {"start": v(-288.4, 598.16) * mm, "end": v(-293.84, 600.75) * mm});
            skLineSegment(sketch, "E1692", {"start": v(-293.84, 600.75) * mm, "end": v(-298.97, 603.25) * mm});
            skLineSegment(sketch, "E1693", {"start": v(-298.97, 603.25) * mm, "end": v(-303.72, 605.62) * mm});
            skLineSegment(sketch, "E1694", {"start": v(-303.72, 605.62) * mm, "end": v(-308.05, 607.77) * mm});
            skLineSegment(sketch, "E1695", {"start": v(-308.05, 607.77) * mm, "end": v(-311.9, 609.64) * mm});
            skLineSegment(sketch, "E1696", {"start": v(-311.9, 609.64) * mm, "end": v(-315.2, 611.16) * mm});
            skLineSegment(sketch, "E1697", {"start": v(-315.2, 611.16) * mm, "end": v(-317.94, 612.28) * mm});
            skLineSegment(sketch, "E1698", {"start": v(-317.94, 612.28) * mm, "end": v(-319.5, 612.8) * mm});
            skLineSegment(sketch, "E1699", {"start": v(-319.5, 612.8) * mm, "end": v(-320.03, 612.91) * mm});
            skLineSegment(sketch, "E1700", {"start": v(-320.03, 612.91) * mm, "end": v(-321.3, 613.19) * mm});
            skLineSegment(sketch, "E1701", {"start": v(-321.3, 613.19) * mm, "end": v(-325.22, 613.38) * mm});
            skLineSegment(sketch, "E1702", {"start": v(-325.22, 613.38) * mm, "end": v(-331, 612.9) * mm});
            skLineSegment(sketch, "E1703", {"start": v(-331, 612.9) * mm, "end": v(-337.25, 611.77) * mm});
            skLineSegment(sketch, "E1704", {"start": v(-337.25, 611.77) * mm, "end": v(-343.87, 610.24) * mm});
            skLineSegment(sketch, "E1705", {"start": v(-343.87, 610.24) * mm, "end": v(-350.75, 608.6) * mm});
            skLineSegment(sketch, "E1706", {"start": v(-350.75, 608.6) * mm, "end": v(-357.77, 607.15) * mm});
            skLineSegment(sketch, "E1707", {"start": v(-357.77, 607.15) * mm, "end": v(-364.81, 606.14) * mm});
            skLineSegment(sketch, "E1708", {"start": v(-364.81, 606.14) * mm, "end": v(-370.04, 605.81) * mm});
            skLineSegment(sketch, "E1709", {"start": v(-370.04, 605.81) * mm, "end": v(-371.77, 605.86) * mm});
            skLineSegment(sketch, "E1710", {"start": v(-371.77, 605.86) * mm, "end": v(-372.96, 605.89) * mm});
            skLineSegment(sketch, "E1711", {"start": v(-372.96, 605.89) * mm, "end": v(-376.55, 606.06) * mm});
            skLineSegment(sketch, "E1712", {"start": v(-376.55, 606.06) * mm, "end": v(-381.8, 606.42) * mm});
            skLineSegment(sketch, "E1713", {"start": v(-381.8, 606.42) * mm, "end": v(-387.49, 606.93) * mm});
            skLineSegment(sketch, "E1714", {"start": v(-387.49, 606.93) * mm, "end": v(-393.53, 607.56) * mm});
            skLineSegment(sketch, "E1715", {"start": v(-393.53, 607.56) * mm, "end": v(-399.86, 608.3) * mm});
            skLineSegment(sketch, "E1716", {"start": v(-399.86, 608.3) * mm, "end": v(-406.42, 609.14) * mm});
            skLineSegment(sketch, "E1717", {"start": v(-406.42, 609.14) * mm, "end": v(-413.14, 610.05) * mm});
            skLineSegment(sketch, "E1718", {"start": v(-413.14, 610.05) * mm, "end": v(-419.96, 611.03) * mm});
            skLineSegment(sketch, "E1719", {"start": v(-419.96, 611.03) * mm, "end": v(-426.82, 612.04) * mm});
            skLineSegment(sketch, "E1720", {"start": v(-426.82, 612.04) * mm, "end": v(-433.64, 613.07) * mm});
            skLineSegment(sketch, "E1721", {"start": v(-433.64, 613.07) * mm, "end": v(-440.36, 614.12) * mm});
            skLineSegment(sketch, "E1722", {"start": v(-440.36, 614.12) * mm, "end": v(-446.93, 615.16) * mm});
            skLineSegment(sketch, "E1723", {"start": v(-446.93, 615.16) * mm, "end": v(-453.27, 616.18) * mm});
            skLineSegment(sketch, "E1724", {"start": v(-453.27, 616.18) * mm, "end": v(-459.32, 617.15) * mm});
            skLineSegment(sketch, "E1725", {"start": v(-459.32, 617.15) * mm, "end": v(-465.02, 618.06) * mm});
            skLineSegment(sketch, "E1726", {"start": v(-465.02, 618.06) * mm, "end": v(-468.98, 618.69) * mm});
            skLineSegment(sketch, "E1727", {"start": v(-468.98, 618.69) * mm, "end": v(-470.3, 618.9) * mm});
            skLineSegment(sketch, "E1728", {"start": v(-470.3, 618.9) * mm, "end": v(-471.05, 619.01) * mm});
            skLineSegment(sketch, "E1729", {"start": v(-471.05, 619.01) * mm, "end": v(-473.3, 619.37) * mm});
            skLineSegment(sketch, "E1730", {"start": v(-473.3, 619.37) * mm, "end": v(-476.7, 619.92) * mm});
            skLineSegment(sketch, "E1731", {"start": v(-476.7, 619.92) * mm, "end": v(-480.49, 620.55) * mm});
            skLineSegment(sketch, "E1732", {"start": v(-480.49, 620.55) * mm, "end": v(-484.62, 621.24) * mm});
            skLineSegment(sketch, "E1733", {"start": v(-484.62, 621.24) * mm, "end": v(-489.07, 621.99) * mm});
            skLineSegment(sketch, "E1734", {"start": v(-489.07, 621.99) * mm, "end": v(-493.8, 622.8) * mm});
            skLineSegment(sketch, "E1735", {"start": v(-493.8, 622.8) * mm, "end": v(-498.77, 623.65) * mm});
            skLineSegment(sketch, "E1736", {"start": v(-498.77, 623.65) * mm, "end": v(-503.95, 624.54) * mm});
            skLineSegment(sketch, "E1737", {"start": v(-503.95, 624.54) * mm, "end": v(-509.32, 625.47) * mm});
            skLineSegment(sketch, "E1738", {"start": v(-509.32, 625.47) * mm, "end": v(-514.83, 626.42) * mm});
            skLineSegment(sketch, "E1739", {"start": v(-514.83, 626.42) * mm, "end": v(-520.45, 627.4) * mm});
            skLineSegment(sketch, "E1740", {"start": v(-520.45, 627.4) * mm, "end": v(-526.15, 628.4) * mm});
            skLineSegment(sketch, "E1741", {"start": v(-526.15, 628.4) * mm, "end": v(-531.9, 629.41) * mm});
            skLineSegment(sketch, "E1742", {"start": v(-531.9, 629.41) * mm, "end": v(-537.66, 630.42) * mm});
            skLineSegment(sketch, "E1743", {"start": v(-537.66, 630.42) * mm, "end": v(-543.4, 631.43) * mm});
            skLineSegment(sketch, "E1744", {"start": v(-543.4, 631.43) * mm, "end": v(-549.1, 632.44) * mm});
            skLineSegment(sketch, "E1745", {"start": v(-549.1, 632.44) * mm, "end": v(-554.7, 633.43) * mm});
            skLineSegment(sketch, "E1746", {"start": v(-554.7, 633.43) * mm, "end": v(-560.17, 634.4) * mm});
            skLineSegment(sketch, "E1747", {"start": v(-560.17, 634.4) * mm, "end": v(-565.5, 635.34) * mm});
            skLineSegment(sketch, "E1748", {"start": v(-565.5, 635.34) * mm, "end": v(-570.64, 636.25) * mm});
            skLineSegment(sketch, "E1749", {"start": v(-570.64, 636.25) * mm, "end": v(-575.56, 637.13) * mm});
            skLineSegment(sketch, "E1750", {"start": v(-575.56, 637.13) * mm, "end": v(-580.23, 637.96) * mm});
            skLineSegment(sketch, "E1751", {"start": v(-580.23, 637.96) * mm, "end": v(-584.61, 638.74) * mm});
            skLineSegment(sketch, "E1752", {"start": v(-584.61, 638.74) * mm, "end": v(-588.67, 639.46) * mm});
            skLineSegment(sketch, "E1753", {"start": v(-588.67, 639.46) * mm, "end": v(-592.38, 640.12) * mm});
            skLineSegment(sketch, "E1754", {"start": v(-592.38, 640.12) * mm, "end": v(-595.7, 640.72) * mm});
            skLineSegment(sketch, "E1755", {"start": v(-595.7, 640.72) * mm, "end": v(-598.6, 641.24) * mm});
            skLineSegment(sketch, "E1756", {"start": v(-598.6, 641.24) * mm, "end": v(-601.05, 641.67) * mm});
            skLineSegment(sketch, "E1757", {"start": v(-601.05, 641.67) * mm, "end": v(-603.02, 642.03) * mm});
            skLineSegment(sketch, "E1758", {"start": v(-603.02, 642.03) * mm, "end": v(-604.46, 642.28) * mm});
            skLineSegment(sketch, "E1759", {"start": v(-604.46, 642.28) * mm, "end": v(-605.35, 642.44) * mm});
            skLineSegment(sketch, "E1760", {"start": v(-605.35, 642.44) * mm, "end": v(-605.65, 642.5) * mm});
            skLineSegment(sketch, "E1761", {"start": v(554.52, 660.49) * mm, "end": v(554.56, 659.45) * mm});
            skLineSegment(sketch, "E1762", {"start": v(554.56, 659.45) * mm, "end": v(554.75, 656.37) * mm});
            skLineSegment(sketch, "E1763", {"start": v(554.75, 656.37) * mm, "end": v(555, 652.39) * mm});
            skLineSegment(sketch, "E1764", {"start": v(555, 652.39) * mm, "end": v(555.16, 648.44) * mm});
            skLineSegment(sketch, "E1765", {"start": v(555.16, 648.44) * mm, "end": v(555.1, 644.44) * mm});
            skLineSegment(sketch, "E1766", {"start": v(555.1, 644.44) * mm, "end": v(554.68, 640.28) * mm});
            skLineSegment(sketch, "E1767", {"start": v(554.68, 640.28) * mm, "end": v(553.77, 635.88) * mm});
            skLineSegment(sketch, "E1768", {"start": v(553.77, 635.88) * mm, "end": v(552.27, 631.14) * mm});
            skLineSegment(sketch, "E1769", {"start": v(552.27, 631.14) * mm, "end": v(550.65, 627.23) * mm});
            skLineSegment(sketch, "E1770", {"start": v(550.65, 627.23) * mm, "end": v(550.04, 625.96) * mm});
            skLineSegment(sketch, "E1771", {"start": v(550.04, 625.96) * mm, "end": v(549.63, 625.13) * mm});
            skLineSegment(sketch, "E1772", {"start": v(549.63, 625.13) * mm, "end": v(548.25, 622.7) * mm});
            skLineSegment(sketch, "E1773", {"start": v(548.25, 622.7) * mm, "end": v(545.6, 618.41) * mm});
            skLineSegment(sketch, "E1774", {"start": v(545.6, 618.41) * mm, "end": v(542.13, 613.3) * mm});
            skLineSegment(sketch, "E1775", {"start": v(542.13, 613.3) * mm, "end": v(537.93, 607.5) * mm});
            skLineSegment(sketch, "E1776", {"start": v(537.93, 607.5) * mm, "end": v(533.07, 601.24) * mm});
            skLineSegment(sketch, "E1777", {"start": v(533.07, 601.24) * mm, "end": v(527.61, 594.65) * mm});
            skLineSegment(sketch, "E1778", {"start": v(527.61, 594.65) * mm, "end": v(521.64, 587.91) * mm});
            skLineSegment(sketch, "E1779", {"start": v(521.64, 587.91) * mm, "end": v(515.23, 581.2) * mm});
            skLineSegment(sketch, "E1780", {"start": v(515.23, 581.2) * mm, "end": v(508.43, 574.7) * mm});
            skLineSegment(sketch, "E1781", {"start": v(508.43, 574.7) * mm, "end": v(501.32, 568.57) * mm});
            skLineSegment(sketch, "E1782", {"start": v(501.32, 568.57) * mm, "end": v(493.98, 562.99) * mm});
            skLineSegment(sketch, "E1783", {"start": v(493.98, 562.99) * mm, "end": v(486.48, 558.13) * mm});
            skLineSegment(sketch, "E1784", {"start": v(486.48, 558.13) * mm, "end": v(478.88, 554.16) * mm});
            skLineSegment(sketch, "E1785", {"start": v(478.88, 554.16) * mm, "end": v(471.26, 551.26) * mm});
            skLineSegment(sketch, "E1786", {"start": v(471.26, 551.26) * mm, "end": v(463.7, 549.59) * mm});
            skLineSegment(sketch, "E1787", {"start": v(463.7, 549.59) * mm, "end": v(458.1, 549.2) * mm});
            skLineSegment(sketch, "E1788", {"start": v(458.1, 549.2) * mm, "end": v(456.24, 549.34) * mm});
            skLineSegment(sketch, "E1789", {"start": v(456.24, 549.34) * mm, "end": v(454.46, 549.46) * mm});
            skLineSegment(sketch, "E1790", {"start": v(454.46, 549.46) * mm, "end": v(449.1, 549.89) * mm});
            skLineSegment(sketch, "E1791", {"start": v(449.1, 549.89) * mm, "end": v(442.34, 550.54) * mm});
            skLineSegment(sketch, "E1792", {"start": v(442.34, 550.54) * mm, "end": v(435.93, 551.33) * mm});
            skLineSegment(sketch, "E1793", {"start": v(435.93, 551.33) * mm, "end": v(429.78, 552.28) * mm});
            skLineSegment(sketch, "E1794", {"start": v(429.78, 552.28) * mm, "end": v(423.86, 553.43) * mm});
            skLineSegment(sketch, "E1795", {"start": v(423.86, 553.43) * mm, "end": v(418.1, 554.8) * mm});
            skLineSegment(sketch, "E1796", {"start": v(418.1, 554.8) * mm, "end": v(412.43, 556.43) * mm});
            skLineSegment(sketch, "E1797", {"start": v(412.43, 556.43) * mm, "end": v(406.8, 558.35) * mm});
            skLineSegment(sketch, "E1798", {"start": v(406.8, 558.35) * mm, "end": v(401.15, 560.59) * mm});
            skLineSegment(sketch, "E1799", {"start": v(401.15, 560.59) * mm, "end": v(395.42, 563.18) * mm});
            skLineSegment(sketch, "E1800", {"start": v(395.42, 563.18) * mm, "end": v(389.56, 566.15) * mm});
            skLineSegment(sketch, "E1801", {"start": v(389.56, 566.15) * mm, "end": v(383.5, 569.53) * mm});
            skLineSegment(sketch, "E1802", {"start": v(383.5, 569.53) * mm, "end": v(377.17, 573.36) * mm});
            skLineSegment(sketch, "E1803", {"start": v(377.17, 573.36) * mm, "end": v(370.54, 577.67) * mm});
            skLineSegment(sketch, "E1804", {"start": v(370.54, 577.67) * mm, "end": v(363.52, 582.48) * mm});
            skLineSegment(sketch, "E1805", {"start": v(363.52, 582.48) * mm, "end": v(357.93, 586.48) * mm});
            skLineSegment(sketch, "E1806", {"start": v(357.93, 586.48) * mm, "end": v(356.08, 587.83) * mm});
            skLineSegment(sketch, "E1807", {"start": v(356.08, 587.83) * mm, "end": v(354.16, 589.23) * mm});
            skLineSegment(sketch, "E1808", {"start": v(354.16, 589.23) * mm, "end": v(348.3, 593.27) * mm});
            skLineSegment(sketch, "E1809", {"start": v(348.3, 593.27) * mm, "end": v(340.41, 598.31) * mm});
            skLineSegment(sketch, "E1810", {"start": v(340.41, 598.31) * mm, "end": v(332.44, 602.98) * mm});
            skLineSegment(sketch, "E1811", {"start": v(332.44, 602.98) * mm, "end": v(324.44, 607.29) * mm});
            skLineSegment(sketch, "E1812", {"start": v(324.44, 607.29) * mm, "end": v(316.47, 611.24) * mm});
            skLineSegment(sketch, "E1813", {"start": v(316.47, 611.24) * mm, "end": v(308.58, 614.85) * mm});
            skLineSegment(sketch, "E1814", {"start": v(308.58, 614.85) * mm, "end": v(300.81, 618.12) * mm});
            skLineSegment(sketch, "E1815", {"start": v(300.81, 618.12) * mm, "end": v(293.23, 621.08) * mm});
            skLineSegment(sketch, "E1816", {"start": v(293.23, 621.08) * mm, "end": v(285.88, 623.73) * mm});
            skLineSegment(sketch, "E1817", {"start": v(285.88, 623.73) * mm, "end": v(278.8, 626.07) * mm});
            skLineSegment(sketch, "E1818", {"start": v(278.8, 626.07) * mm, "end": v(272.08, 628.13) * mm});
            skLineSegment(sketch, "E1819", {"start": v(272.08, 628.13) * mm, "end": v(265.73, 629.9) * mm});
            skLineSegment(sketch, "E1820", {"start": v(265.73, 629.9) * mm, "end": v(259.82, 631.41) * mm});
            skLineSegment(sketch, "E1821", {"start": v(259.82, 631.41) * mm, "end": v(254.4, 632.66) * mm});
            skLineSegment(sketch, "E1822", {"start": v(254.4, 632.66) * mm, "end": v(249.52, 633.66) * mm});
            skLineSegment(sketch, "E1823", {"start": v(249.52, 633.66) * mm, "end": v(246.31, 634.26) * mm});
            skLineSegment(sketch, "E1824", {"start": v(246.31, 634.26) * mm, "end": v(245.24, 634.43) * mm});
            skLineSegment(sketch, "E1825", {"start": v(245.24, 634.43) * mm, "end": v(244.15, 634.61) * mm});
            skLineSegment(sketch, "E1826", {"start": v(244.15, 634.61) * mm, "end": v(240.9, 635.17) * mm});
            skLineSegment(sketch, "E1827", {"start": v(240.9, 635.17) * mm, "end": v(235.88, 636.04) * mm});
            skLineSegment(sketch, "E1828", {"start": v(235.88, 636.04) * mm, "end": v(230.22, 637.03) * mm});
            skLineSegment(sketch, "E1829", {"start": v(230.22, 637.03) * mm, "end": v(223.95, 638.1) * mm});
            skLineSegment(sketch, "E1830", {"start": v(223.95, 638.1) * mm, "end": v(217.13, 639.25) * mm});
            skLineSegment(sketch, "E1831", {"start": v(217.13, 639.25) * mm, "end": v(209.8, 640.43) * mm});
            skLineSegment(sketch, "E1832", {"start": v(209.8, 640.43) * mm, "end": v(202, 641.63) * mm});
            skLineSegment(sketch, "E1833", {"start": v(202, 641.63) * mm, "end": v(193.78, 642.82) * mm});
            skLineSegment(sketch, "E1834", {"start": v(193.78, 642.82) * mm, "end": v(185.2, 643.98) * mm});
            skLineSegment(sketch, "E1835", {"start": v(185.2, 643.98) * mm, "end": v(176.26, 645.07) * mm});
            skLineSegment(sketch, "E1836", {"start": v(176.26, 645.07) * mm, "end": v(167.05, 646.08) * mm});
            skLineSegment(sketch, "E1837", {"start": v(167.05, 646.08) * mm, "end": v(157.6, 646.99) * mm});
            skLineSegment(sketch, "E1838", {"start": v(157.6, 646.99) * mm, "end": v(147.94, 647.76) * mm});
            skLineSegment(sketch, "E1839", {"start": v(147.94, 647.76) * mm, "end": v(138.14, 648.37) * mm});
            skLineSegment(sketch, "E1840", {"start": v(138.14, 648.37) * mm, "end": v(128.23, 648.8) * mm});
            skLineSegment(sketch, "E1841", {"start": v(128.23, 648.8) * mm, "end": v(120.75, 649) * mm});
            skLineSegment(sketch, "E1842", {"start": v(120.75, 649) * mm, "end": v(118.25, 649.02) * mm});
            skLineSegment(sketch, "E1843", {"start": v(118.25, 649.02) * mm, "end": v(115.67, 649.05) * mm});
            skLineSegment(sketch, "E1844", {"start": v(115.67, 649.05) * mm, "end": v(107.9, 648.95) * mm});
            skLineSegment(sketch, "E1845", {"start": v(107.9, 648.95) * mm, "end": v(96.91, 648.54) * mm});
            skLineSegment(sketch, "E1846", {"start": v(96.91, 648.54) * mm, "end": v(85.46, 647.83) * mm});
            skLineSegment(sketch, "E1847", {"start": v(85.46, 647.83) * mm, "end": v(73.7, 646.87) * mm});
            skLineSegment(sketch, "E1848", {"start": v(73.7, 646.87) * mm, "end": v(61.78, 645.7) * mm});
            skLineSegment(sketch, "E1849", {"start": v(61.78, 645.7) * mm, "end": v(49.86, 644.34) * mm});
            skLineSegment(sketch, "E1850", {"start": v(49.86, 644.34) * mm, "end": v(38.12, 642.86) * mm});
            skLineSegment(sketch, "E1851", {"start": v(38.12, 642.86) * mm, "end": v(26.7, 641.29) * mm});
            skLineSegment(sketch, "E1852", {"start": v(26.7, 641.29) * mm, "end": v(15.75, 639.67) * mm});
            skLineSegment(sketch, "E1853", {"start": v(15.75, 639.67) * mm, "end": v(5.44, 638.04) * mm});
            skLineSegment(sketch, "E1854", {"start": v(5.44, 638.04) * mm, "end": v(-4.08, 636.43) * mm});
            skLineSegment(sketch, "E1855", {"start": v(-4.08, 636.43) * mm, "end": v(-12.63, 634.9) * mm});
            skLineSegment(sketch, "E1856", {"start": v(-12.63, 634.9) * mm, "end": v(-20.08, 633.5) * mm});
            skLineSegment(sketch, "E1857", {"start": v(-20.08, 633.5) * mm, "end": v(-26.25, 632.24) * mm});
            skLineSegment(sketch, "E1858", {"start": v(-26.25, 632.24) * mm, "end": v(-31, 631.18) * mm});
            skLineSegment(sketch, "E1859", {"start": v(-31, 631.18) * mm, "end": v(-33.38, 630.59) * mm});
            skLineSegment(sketch, "E1860", {"start": v(-33.38, 630.59) * mm, "end": v(-34.16, 630.35) * mm});
            skLineSegment(sketch, "E1861", {"start": v(-34.16, 630.35) * mm, "end": v(-34.75, 630.18) * mm});
            skLineSegment(sketch, "E1862", {"start": v(-34.75, 630.18) * mm, "end": v(-36.49, 629.64) * mm});
            skLineSegment(sketch, "E1863", {"start": v(-36.49, 629.64) * mm, "end": v(-38.86, 628.86) * mm});
            skLineSegment(sketch, "E1864", {"start": v(-38.86, 628.86) * mm, "end": v(-41.35, 628.02) * mm});
            skLineSegment(sketch, "E1865", {"start": v(-41.35, 628.02) * mm, "end": v(-44, 627.12) * mm});
            skLineSegment(sketch, "E1866", {"start": v(-44, 627.12) * mm, "end": v(-46.88, 626.18) * mm});
            skLineSegment(sketch, "E1867", {"start": v(-46.88, 626.18) * mm, "end": v(-50.05, 625.17) * mm});
            skLineSegment(sketch, "E1868", {"start": v(-50.05, 625.17) * mm, "end": v(-53.56, 624.12) * mm});
            skLineSegment(sketch, "E1869", {"start": v(-53.56, 624.12) * mm, "end": v(-57.46, 623.01) * mm});
            skLineSegment(sketch, "E1870", {"start": v(-57.46, 623.01) * mm, "end": v(-61.83, 621.86) * mm});
            skLineSegment(sketch, "E1871", {"start": v(-61.83, 621.86) * mm, "end": v(-66.7, 620.65) * mm});
            skLineSegment(sketch, "E1872", {"start": v(-66.7, 620.65) * mm, "end": v(-72.15, 619.4) * mm});
            skLineSegment(sketch, "E1873", {"start": v(-72.15, 619.4) * mm, "end": v(-78.23, 618.1) * mm});
            skLineSegment(sketch, "E1874", {"start": v(-78.23, 618.1) * mm, "end": v(-85, 616.75) * mm});
            skLineSegment(sketch, "E1875", {"start": v(-85, 616.75) * mm, "end": v(-92.51, 615.36) * mm});
            skLineSegment(sketch, "E1876", {"start": v(-92.51, 615.36) * mm, "end": v(-100.82, 613.93) * mm});
            skLineSegment(sketch, "E1877", {"start": v(-100.82, 613.93) * mm, "end": v(-107.7, 612.82) * mm});
            skLineSegment(sketch, "E1878", {"start": v(-107.7, 612.82) * mm, "end": v(-110, 612.46) * mm});
            skLineSegment(sketch, "E1879", {"start": v(-110, 612.46) * mm, "end": v(-114.58, 611.75) * mm});
            skLineSegment(sketch, "E1880", {"start": v(-114.58, 611.75) * mm, "end": v(-128.35, 609.73) * mm});
            skLineSegment(sketch, "E1881", {"start": v(-128.35, 609.73) * mm, "end": v(-145, 607.53) * mm});
            skLineSegment(sketch, "E1882", {"start": v(-145, 607.53) * mm, "end": v(-160.04, 605.84) * mm});
            skLineSegment(sketch, "E1883", {"start": v(-160.04, 605.84) * mm, "end": v(-173.6, 604.66) * mm});
            skLineSegment(sketch, "E1884", {"start": v(-173.6, 604.66) * mm, "end": v(-185.78, 603.99) * mm});
            skLineSegment(sketch, "E1885", {"start": v(-185.78, 603.99) * mm, "end": v(-196.69, 603.8) * mm});
            skLineSegment(sketch, "E1886", {"start": v(-196.69, 603.8) * mm, "end": v(-206.43, 604.1) * mm});
            skLineSegment(sketch, "E1887", {"start": v(-206.43, 604.1) * mm, "end": v(-212.97, 604.6) * mm});
            skLineSegment(sketch, "E1888", {"start": v(-212.97, 604.6) * mm, "end": v(-215.14, 604.87) * mm});
            skLineSegment(sketch, "E1889", {"start": v(-215.14, 604.87) * mm, "end": v(-217.12, 605.11) * mm});
            skLineSegment(sketch, "E1890", {"start": v(-217.12, 605.11) * mm, "end": v(-223.05, 605.93) * mm});
            skLineSegment(sketch, "E1891", {"start": v(-223.05, 605.93) * mm, "end": v(-230.5, 607.17) * mm});
            skLineSegment(sketch, "E1892", {"start": v(-230.5, 607.17) * mm, "end": v(-237.72, 608.66) * mm});
            skLineSegment(sketch, "E1893", {"start": v(-237.72, 608.66) * mm, "end": v(-244.92, 610.52) * mm});
            skLineSegment(sketch, "E1894", {"start": v(-244.92, 610.52) * mm, "end": v(-252.31, 612.84) * mm});
            skLineSegment(sketch, "E1895", {"start": v(-252.31, 612.84) * mm, "end": v(-260.13, 615.7) * mm});
            skLineSegment(sketch, "E1896", {"start": v(-260.13, 615.7) * mm, "end": v(-268.58, 619.22) * mm});
            skLineSegment(sketch, "E1897", {"start": v(-268.58, 619.22) * mm, "end": v(-275.57, 622.38) * mm});
            skLineSegment(sketch, "E1898", {"start": v(-275.57, 622.38) * mm, "end": v(-277.88, 623.48) * mm});
            skLineSegment(sketch, "E1899", {"start": v(-277.88, 623.48) * mm, "end": v(-279.02, 624.01) * mm});
            skLineSegment(sketch, "E1900", {"start": v(-279.02, 624.01) * mm, "end": v(-282.4, 625.65) * mm});
            skLineSegment(sketch, "E1901", {"start": v(-282.4, 625.65) * mm, "end": v(-286.43, 627.65) * mm});
            skLineSegment(sketch, "E1902", {"start": v(-286.43, 627.65) * mm, "end": v(-290.01, 629.47) * mm});
            skLineSegment(sketch, "E1903", {"start": v(-290.01, 629.47) * mm, "end": v(-293.18, 631.13) * mm});
            skLineSegment(sketch, "E1904", {"start": v(-293.18, 631.13) * mm, "end": v(-295.97, 632.63) * mm});
            skLineSegment(sketch, "E1905", {"start": v(-295.97, 632.63) * mm, "end": v(-298.42, 633.98) * mm});
            skLineSegment(sketch, "E1906", {"start": v(-298.42, 633.98) * mm, "end": v(-300.57, 635.18) * mm});
            skLineSegment(sketch, "E1907", {"start": v(-300.57, 635.18) * mm, "end": v(-302.45, 636.25) * mm});
            skLineSegment(sketch, "E1908", {"start": v(-302.45, 636.25) * mm, "end": v(-304.1, 637.2) * mm});
            skLineSegment(sketch, "E1909", {"start": v(-304.1, 637.2) * mm, "end": v(-305.57, 638.02) * mm});
            skLineSegment(sketch, "E1910", {"start": v(-305.57, 638.02) * mm, "end": v(-306.88, 638.72) * mm});
            skLineSegment(sketch, "E1911", {"start": v(-306.88, 638.72) * mm, "end": v(-308.08, 639.33) * mm});
            skLineSegment(sketch, "E1912", {"start": v(-308.08, 639.33) * mm, "end": v(-309.2, 639.83) * mm});
            skLineSegment(sketch, "E1913", {"start": v(-309.2, 639.83) * mm, "end": v(-310.26, 640.25) * mm});
            skLineSegment(sketch, "E1914", {"start": v(-310.26, 640.25) * mm, "end": v(-311.33, 640.58) * mm});
            skLineSegment(sketch, "E1915", {"start": v(-311.33, 640.58) * mm, "end": v(-312.15, 640.78) * mm});
            skLineSegment(sketch, "E1916", {"start": v(-312.15, 640.78) * mm, "end": v(-312.43, 640.83) * mm});
            skLineSegment(sketch, "E1917", {"start": v(-312.43, 640.83) * mm, "end": v(-312.98, 640.94) * mm});
            skLineSegment(sketch, "E1918", {"start": v(-312.98, 640.94) * mm, "end": v(-314.63, 641.21) * mm});
            skLineSegment(sketch, "E1919", {"start": v(-314.63, 641.21) * mm, "end": v(-316.94, 641.46) * mm});
            skLineSegment(sketch, "E1920", {"start": v(-316.94, 641.46) * mm, "end": v(-319.63, 641.56) * mm});
            skLineSegment(sketch, "E1921", {"start": v(-319.63, 641.56) * mm, "end": v(-323, 641.5) * mm});
            skLineSegment(sketch, "E1922", {"start": v(-323, 641.5) * mm, "end": v(-327.36, 641.26) * mm});
            skLineSegment(sketch, "E1923", {"start": v(-327.36, 641.26) * mm, "end": v(-332.98, 640.8) * mm});
            skLineSegment(sketch, "E1924", {"start": v(-332.98, 640.8) * mm, "end": v(-340.16, 640.15) * mm});
            skLineSegment(sketch, "E1925", {"start": v(-340.16, 640.15) * mm, "end": v(-346.94, 639.49) * mm});
            skLineSegment(sketch, "E1926", {"start": v(-346.94, 639.49) * mm, "end": v(-349.2, 639.25) * mm});
            skLineSegment(sketch, "E1927", {"start": v(-349.2, 639.25) * mm, "end": v(-350.35, 639.14) * mm});
            skLineSegment(sketch, "E1928", {"start": v(-350.35, 639.14) * mm, "end": v(-353.82, 638.78) * mm});
            skLineSegment(sketch, "E1929", {"start": v(-353.82, 638.78) * mm, "end": v(-357.71, 638.34) * mm});
            skLineSegment(sketch, "E1930", {"start": v(-357.71, 638.34) * mm, "end": v(-360.98, 637.96) * mm});
            skLineSegment(sketch, "E1931", {"start": v(-360.98, 637.96) * mm, "end": v(-363.72, 637.62) * mm});
            skLineSegment(sketch, "E1932", {"start": v(-363.72, 637.62) * mm, "end": v(-366.04, 637.3) * mm});
            skLineSegment(sketch, "E1933", {"start": v(-366.04, 637.3) * mm, "end": v(-368.04, 637.03) * mm});
            skLineSegment(sketch, "E1934", {"start": v(-368.04, 637.03) * mm, "end": v(-369.83, 636.77) * mm});
            skLineSegment(sketch, "E1935", {"start": v(-369.83, 636.77) * mm, "end": v(-371.5, 636.54) * mm});
            skLineSegment(sketch, "E1936", {"start": v(-371.5, 636.54) * mm, "end": v(-373.17, 636.32) * mm});
            skLineSegment(sketch, "E1937", {"start": v(-373.17, 636.32) * mm, "end": v(-374.94, 636.1) * mm});
            skLineSegment(sketch, "E1938", {"start": v(-374.94, 636.1) * mm, "end": v(-376.9, 635.9) * mm});
            skLineSegment(sketch, "E1939", {"start": v(-376.9, 635.9) * mm, "end": v(-379.16, 635.7) * mm});
            skLineSegment(sketch, "E1940", {"start": v(-379.16, 635.7) * mm, "end": v(-381.83, 635.49) * mm});
            skLineSegment(sketch, "E1941", {"start": v(-381.83, 635.49) * mm, "end": v(-385, 635.27) * mm});
            skLineSegment(sketch, "E1942", {"start": v(-385, 635.27) * mm, "end": v(-388.79, 635.04) * mm});
            skLineSegment(sketch, "E1943", {"start": v(-388.79, 635.04) * mm, "end": v(-392.17, 634.84) * mm});
            skLineSegment(sketch, "E1944", {"start": v(-392.17, 634.84) * mm, "end": v(-393.29, 634.79) * mm});
            skLineSegment(sketch, "E1945", {"start": v(-393.29, 634.79) * mm, "end": v(-395.68, 634.66) * mm});
            skLineSegment(sketch, "E1946", {"start": v(-395.68, 634.66) * mm, "end": v(-402.85, 634.47) * mm});
            skLineSegment(sketch, "E1947", {"start": v(-402.85, 634.47) * mm, "end": v(-411.8, 634.52) * mm});
            skLineSegment(sketch, "E1948", {"start": v(-411.8, 634.52) * mm, "end": v(-419.95, 634.84) * mm});
            skLineSegment(sketch, "E1949", {"start": v(-419.95, 634.84) * mm, "end": v(-427.08, 635.32) * mm});
            skLineSegment(sketch, "E1950", {"start": v(-427.08, 635.32) * mm, "end": v(-432.99, 635.88) * mm});
            skLineSegment(sketch, "E1951", {"start": v(-432.99, 635.88) * mm, "end": v(-437.46, 636.4) * mm});
            skLineSegment(sketch, "E1952", {"start": v(-437.46, 636.4) * mm, "end": v(-440.3, 636.78) * mm});
            skLineSegment(sketch, "E1953", {"start": v(-440.3, 636.78) * mm, "end": v(-441.29, 636.92) * mm});
            skLineSegment(sketch, "E1954", {"start": v(-441.29, 636.92) * mm, "end": v(-444.95, 637.17) * mm});
            skLineSegment(sketch, "E1955", {"start": v(-444.95, 637.17) * mm, "end": v(-455.92, 638.16) * mm});
            skLineSegment(sketch, "E1956", {"start": v(-455.92, 638.16) * mm, "end": v(-470.74, 639.84) * mm});
            skLineSegment(sketch, "E1957", {"start": v(-470.74, 639.84) * mm, "end": v(-485.6, 641.9) * mm});
            skLineSegment(sketch, "E1958", {"start": v(-485.6, 641.9) * mm, "end": v(-500.34, 644.26) * mm});
            skLineSegment(sketch, "E1959", {"start": v(-500.34, 644.26) * mm, "end": v(-514.8, 646.84) * mm});
            skLineSegment(sketch, "E1960", {"start": v(-514.8, 646.84) * mm, "end": v(-528.83, 649.59) * mm});
            skLineSegment(sketch, "E1961", {"start": v(-528.83, 649.59) * mm, "end": v(-542.26, 652.41) * mm});
            skLineSegment(sketch, "E1962", {"start": v(-542.26, 652.41) * mm, "end": v(-554.95, 655.25) * mm});
            skLineSegment(sketch, "E1963", {"start": v(-554.95, 655.25) * mm, "end": v(-566.73, 658.03) * mm});
            skLineSegment(sketch, "E1964", {"start": v(-566.73, 658.03) * mm, "end": v(-577.45, 660.67) * mm});
            skLineSegment(sketch, "E1965", {"start": v(-577.45, 660.67) * mm, "end": v(-586.95, 663.1) * mm});
            skLineSegment(sketch, "E1966", {"start": v(-586.95, 663.1) * mm, "end": v(-595.07, 665.26) * mm});
            skLineSegment(sketch, "E1967", {"start": v(-595.07, 665.26) * mm, "end": v(-601.67, 667.06) * mm});
            skLineSegment(sketch, "E1968", {"start": v(-601.67, 667.06) * mm, "end": v(-606.57, 668.44) * mm});
            skLineSegment(sketch, "E1969", {"start": v(-606.57, 668.44) * mm, "end": v(-609.62, 669.32) * mm});
            skLineSegment(sketch, "E1970", {"start": v(-609.62, 669.32) * mm, "end": v(-610.68, 669.63) * mm});
            skLineSegment(sketch, "E1971", {"start": v(5.7, 669.51) * mm, "end": v(4.71, 669.2) * mm});
            skLineSegment(sketch, "E1972", {"start": v(4.71, 669.2) * mm, "end": v(1.72, 668.36) * mm});
            skLineSegment(sketch, "E1973", {"start": v(1.72, 668.36) * mm, "end": v(-3.88, 666.86) * mm});
            skLineSegment(sketch, "E1974", {"start": v(-3.88, 666.86) * mm, "end": v(-10.9, 665.08) * mm});
            skLineSegment(sketch, "E1975", {"start": v(-10.9, 665.08) * mm, "end": v(-19.13, 663.06) * mm});
            skLineSegment(sketch, "E1976", {"start": v(-19.13, 663.06) * mm, "end": v(-28.38, 660.85) * mm});
            skLineSegment(sketch, "E1977", {"start": v(-28.38, 660.85) * mm, "end": v(-38.45, 658.5) * mm});
            skLineSegment(sketch, "E1978", {"start": v(-38.45, 658.5) * mm, "end": v(-49.12, 656.05) * mm});
            skLineSegment(sketch, "E1979", {"start": v(-49.12, 656.05) * mm, "end": v(-60.2, 653.57) * mm});
            skLineSegment(sketch, "E1980", {"start": v(-60.2, 653.57) * mm, "end": v(-71.48, 651.09) * mm});
            skLineSegment(sketch, "E1981", {"start": v(-71.48, 651.09) * mm, "end": v(-82.77, 648.66) * mm});
            skLineSegment(sketch, "E1982", {"start": v(-82.77, 648.66) * mm, "end": v(-93.87, 646.34) * mm});
            skLineSegment(sketch, "E1983", {"start": v(-93.87, 646.34) * mm, "end": v(-104.56, 644.17) * mm});
            skLineSegment(sketch, "E1984", {"start": v(-104.56, 644.17) * mm, "end": v(-114.65, 642.2) * mm});
            skLineSegment(sketch, "E1985", {"start": v(-114.65, 642.2) * mm, "end": v(-123.94, 640.47) * mm});
            skLineSegment(sketch, "E1986", {"start": v(-123.94, 640.47) * mm, "end": v(-132.22, 639.05) * mm});
            skLineSegment(sketch, "E1987", {"start": v(-132.22, 639.05) * mm, "end": v(-137.51, 638.22) * mm});
            skLineSegment(sketch, "E1988", {"start": v(-137.51, 638.22) * mm, "end": v(-139.28, 637.97) * mm});
            skLineSegment(sketch, "E1989", {"start": v(-139.28, 637.97) * mm, "end": v(-140.77, 637.76) * mm});
            skLineSegment(sketch, "E1990", {"start": v(-140.77, 637.76) * mm, "end": v(-145.25, 637.13) * mm});
            skLineSegment(sketch, "E1991", {"start": v(-145.25, 637.13) * mm, "end": v(-150.4, 636.36) * mm});
            skLineSegment(sketch, "E1992", {"start": v(-150.4, 636.36) * mm, "end": v(-154.85, 635.66) * mm});
            skLineSegment(sketch, "E1993", {"start": v(-154.85, 635.66) * mm, "end": v(-158.67, 635.04) * mm});
            skLineSegment(sketch, "E1994", {"start": v(-158.67, 635.04) * mm, "end": v(-161.95, 634.49) * mm});
            skLineSegment(sketch, "E1995", {"start": v(-161.95, 634.49) * mm, "end": v(-164.78, 634) * mm});
            skLineSegment(sketch, "E1996", {"start": v(-164.78, 634) * mm, "end": v(-167.24, 633.56) * mm});
            skLineSegment(sketch, "E1997", {"start": v(-167.24, 633.56) * mm, "end": v(-169.43, 633.2) * mm});
            skLineSegment(sketch, "E1998", {"start": v(-169.43, 633.2) * mm, "end": v(-171.44, 632.87) * mm});
            skLineSegment(sketch, "E1999", {"start": v(-171.44, 632.87) * mm, "end": v(-173.35, 632.6) * mm});
            skLineSegment(sketch, "E2000", {"start": v(-173.35, 632.6) * mm, "end": v(-175.26, 632.37) * mm});
            skLineSegment(sketch, "E2001", {"start": v(-175.26, 632.37) * mm, "end": v(-177.25, 632.18) * mm});
            skLineSegment(sketch, "E2002", {"start": v(-177.25, 632.18) * mm, "end": v(-179.4, 632.03) * mm});
            skLineSegment(sketch, "E2003", {"start": v(-179.4, 632.03) * mm, "end": v(-181.82, 631.91) * mm});
            skLineSegment(sketch, "E2004", {"start": v(-181.82, 631.91) * mm, "end": v(-184.6, 631.82) * mm});
            skLineSegment(sketch, "E2005", {"start": v(-184.6, 631.82) * mm, "end": v(-187, 631.77) * mm});
            skLineSegment(sketch, "E2006", {"start": v(-187, 631.77) * mm, "end": v(-187.8, 631.76) * mm});
            skLineSegment(sketch, "E2007", {"start": v(-187.8, 631.76) * mm, "end": v(-188.78, 631.75) * mm});
            skLineSegment(sketch, "E2008", {"start": v(-188.78, 631.75) * mm, "end": v(-191.74, 632.03) * mm});
            skLineSegment(sketch, "E2009", {"start": v(-191.74, 632.03) * mm, "end": v(-196.59, 632.9) * mm});
            skLineSegment(sketch, "E2010", {"start": v(-196.59, 632.9) * mm, "end": v(-202.21, 634.29) * mm});
            skLineSegment(sketch, "E2011", {"start": v(-202.21, 634.29) * mm, "end": v(-208.47, 636.11) * mm});
            skLineSegment(sketch, "E2012", {"start": v(-208.47, 636.11) * mm, "end": v(-215.23, 638.3) * mm});
            skLineSegment(sketch, "E2013", {"start": v(-215.23, 638.3) * mm, "end": v(-222.37, 640.8) * mm});
            skLineSegment(sketch, "E2014", {"start": v(-222.37, 640.8) * mm, "end": v(-229.74, 643.49) * mm});
            skLineSegment(sketch, "E2015", {"start": v(-229.74, 643.49) * mm, "end": v(-237.22, 646.33) * mm});
            skLineSegment(sketch, "E2016", {"start": v(-237.22, 646.33) * mm, "end": v(-244.67, 649.22) * mm});
            skLineSegment(sketch, "E2017", {"start": v(-244.67, 649.22) * mm, "end": v(-251.96, 652.11) * mm});
            skLineSegment(sketch, "E2018", {"start": v(-251.96, 652.11) * mm, "end": v(-258.96, 654.9) * mm});
            skLineSegment(sketch, "E2019", {"start": v(-258.96, 654.9) * mm, "end": v(-265.54, 657.53) * mm});
            skLineSegment(sketch, "E2020", {"start": v(-265.54, 657.53) * mm, "end": v(-271.56, 659.92) * mm});
            skLineSegment(sketch, "E2021", {"start": v(-271.56, 659.92) * mm, "end": v(-276.89, 661.99) * mm});
            skLineSegment(sketch, "E2022", {"start": v(-276.89, 661.99) * mm, "end": v(-281.4, 663.66) * mm});
            skLineSegment(sketch, "E2023", {"start": v(-281.4, 663.66) * mm, "end": v(-284.05, 664.6) * mm});
            skLineSegment(sketch, "E2024", {"start": v(-284.05, 664.6) * mm, "end": v(-284.94, 664.87) * mm});
            skLineSegment(sketch, "E2025", {"start": v(-284.94, 664.87) * mm, "end": v(-286.1, 665.23) * mm});
            skLineSegment(sketch, "E2026", {"start": v(-286.1, 665.23) * mm, "end": v(-289.57, 666.32) * mm});
            skLineSegment(sketch, "E2027", {"start": v(-289.57, 666.32) * mm, "end": v(-294.1, 667.6) * mm});
            skLineSegment(sketch, "E2028", {"start": v(-294.1, 667.6) * mm, "end": v(-299.03, 668.67) * mm});
            skLineSegment(sketch, "E2029", {"start": v(-299.03, 668.67) * mm, "end": v(-303.41, 669.34) * mm});
            skLineSegment(sketch, "E2030", {"start": v(-303.41, 669.34) * mm, "end": v(-304.88, 669.5) * mm});
            skLineSegment(sketch, "E2031", {"start": v(-304.88, 669.5) * mm, "end": v(-305.67, 669.59) * mm});
            skLineSegment(sketch, "E2032", {"start": v(-305.67, 669.59) * mm, "end": v(-308.09, 669.51) * mm});
            skLineSegment(sketch, "E2033", {"start": v(-308.09, 669.51) * mm, "end": v(-311.99, 669.01) * mm});
            skLineSegment(sketch, "E2034", {"start": v(-311.99, 669.01) * mm, "end": v(-316.52, 668.15) * mm});
            skLineSegment(sketch, "E2035", {"start": v(-316.52, 668.15) * mm, "end": v(-321.65, 667.06) * mm});
            skLineSegment(sketch, "E2036", {"start": v(-321.65, 667.06) * mm, "end": v(-327.31, 665.9) * mm});
            skLineSegment(sketch, "E2037", {"start": v(-327.31, 665.9) * mm, "end": v(-333.47, 664.79) * mm});
            skLineSegment(sketch, "E2038", {"start": v(-333.47, 664.79) * mm, "end": v(-340.05, 663.87) * mm});
            skLineSegment(sketch, "E2039", {"start": v(-340.05, 663.87) * mm, "end": v(-345.28, 663.4) * mm});
            skLineSegment(sketch, "E2040", {"start": v(-345.28, 663.4) * mm, "end": v(-347.03, 663.3) * mm});
            skLineSegment(sketch, "E2041", {"start": v(-347.03, 663.3) * mm, "end": v(-349.11, 663.2) * mm});
            skLineSegment(sketch, "E2042", {"start": v(-349.11, 663.2) * mm, "end": v(-355.37, 662.9) * mm});
            skLineSegment(sketch, "E2043", {"start": v(-355.37, 662.9) * mm, "end": v(-362.23, 662.55) * mm});
            skLineSegment(sketch, "E2044", {"start": v(-362.23, 662.55) * mm, "end": v(-367.77, 662.27) * mm});
            skLineSegment(sketch, "E2045", {"start": v(-367.77, 662.27) * mm, "end": v(-372.16, 662.06) * mm});
            skLineSegment(sketch, "E2046", {"start": v(-372.16, 662.06) * mm, "end": v(-375.57, 661.88) * mm});
            skLineSegment(sketch, "E2047", {"start": v(-375.57, 661.88) * mm, "end": v(-378.16, 661.75) * mm});
            skLineSegment(sketch, "E2048", {"start": v(-378.16, 661.75) * mm, "end": v(-380.1, 661.65) * mm});
            skLineSegment(sketch, "E2049", {"start": v(-380.1, 661.65) * mm, "end": v(-381.56, 661.58) * mm});
            skLineSegment(sketch, "E2050", {"start": v(-381.56, 661.58) * mm, "end": v(-382.7, 661.52) * mm});
            skLineSegment(sketch, "E2051", {"start": v(-382.7, 661.52) * mm, "end": v(-383.7, 661.47) * mm});
            skLineSegment(sketch, "E2052", {"start": v(-383.7, 661.47) * mm, "end": v(-384.7, 661.42) * mm});
            skLineSegment(sketch, "E2053", {"start": v(-384.7, 661.42) * mm, "end": v(-385.88, 661.36) * mm});
            skLineSegment(sketch, "E2054", {"start": v(-385.88, 661.36) * mm, "end": v(-387.41, 661.29) * mm});
            skLineSegment(sketch, "E2055", {"start": v(-387.41, 661.29) * mm, "end": v(-389.46, 661.2) * mm});
            skLineSegment(sketch, "E2056", {"start": v(-389.46, 661.2) * mm, "end": v(-392.19, 661.06) * mm});
            skLineSegment(sketch, "E2057", {"start": v(-392.19, 661.06) * mm, "end": v(-394.87, 660.93) * mm});
            skLineSegment(sketch, "E2058", {"start": v(-394.87, 660.93) * mm, "end": v(-395.76, 660.89) * mm});
            skLineSegment(sketch, "E2059", {"start": v(-395.76, 660.89) * mm, "end": v(-396.6, 660.85) * mm});
            skLineSegment(sketch, "E2060", {"start": v(-396.6, 660.85) * mm, "end": v(-399.15, 660.78) * mm});
            skLineSegment(sketch, "E2061", {"start": v(-399.15, 660.78) * mm, "end": v(-403.7, 660.72) * mm});
            skLineSegment(sketch, "E2062", {"start": v(-403.7, 660.72) * mm, "end": v(-409.32, 660.72) * mm});
            skLineSegment(sketch, "E2063", {"start": v(-409.32, 660.72) * mm, "end": v(-415.92, 660.8) * mm});
            skLineSegment(sketch, "E2064", {"start": v(-415.92, 660.8) * mm, "end": v(-423.42, 660.96) * mm});
            skLineSegment(sketch, "E2065", {"start": v(-423.42, 660.96) * mm, "end": v(-431.72, 661.22) * mm});
            skLineSegment(sketch, "E2066", {"start": v(-431.72, 661.22) * mm, "end": v(-440.74, 661.59) * mm});
            skLineSegment(sketch, "E2067", {"start": v(-440.74, 661.59) * mm, "end": v(-450.4, 662.08) * mm});
            skLineSegment(sketch, "E2068", {"start": v(-450.4, 662.08) * mm, "end": v(-460.58, 662.7) * mm});
            skLineSegment(sketch, "E2069", {"start": v(-460.58, 662.7) * mm, "end": v(-471.21, 663.47) * mm});
            skLineSegment(sketch, "E2070", {"start": v(-471.21, 663.47) * mm, "end": v(-482.2, 664.4) * mm});
            skLineSegment(sketch, "E2071", {"start": v(-482.2, 664.4) * mm, "end": v(-493.48, 665.5) * mm});
            skLineSegment(sketch, "E2072", {"start": v(-493.48, 665.5) * mm, "end": v(-504.93, 666.76) * mm});
            skLineSegment(sketch, "E2073", {"start": v(-504.93, 666.76) * mm, "end": v(-516.47, 668.23) * mm});
            skLineSegment(sketch, "E2074", {"start": v(-516.47, 668.23) * mm, "end": v(-528.02, 669.9) * mm});
            skLineSegment(sketch, "E2075", {"start": v(-528.02, 669.9) * mm, "end": v(-536.63, 671.28) * mm});
            skLineSegment(sketch, "E2076", {"start": v(-536.63, 671.28) * mm, "end": v(-539.49, 671.78) * mm});
            skLineSegment(sketch, "E2077", {"start": v(-539.49, 671.78) * mm, "end": v(-541.21, 672.09) * mm});
            skLineSegment(sketch, "E2078", {"start": v(-541.21, 672.09) * mm, "end": v(-546.38, 673.02) * mm});
            skLineSegment(sketch, "E2079", {"start": v(-546.38, 673.02) * mm, "end": v(-552.53, 674.17) * mm});
            skLineSegment(sketch, "E2080", {"start": v(-552.53, 674.17) * mm, "end": v(-558, 675.26) * mm});
            skLineSegment(sketch, "E2081", {"start": v(-558, 675.26) * mm, "end": v(-562.85, 676.28) * mm});
            skLineSegment(sketch, "E2082", {"start": v(-562.85, 676.28) * mm, "end": v(-567.12, 677.25) * mm});
            skLineSegment(sketch, "E2083", {"start": v(-567.12, 677.25) * mm, "end": v(-570.87, 678.16) * mm});
            skLineSegment(sketch, "E2084", {"start": v(-570.87, 678.16) * mm, "end": v(-574.14, 679.04) * mm});
            skLineSegment(sketch, "E2085", {"start": v(-574.14, 679.04) * mm, "end": v(-576.29, 679.67) * mm});
            skLineSegment(sketch, "E2086", {"start": v(-576.29, 679.67) * mm, "end": v(-577, 679.89) * mm});
            skLineSegment(sketch, "E2087", {"start": v(-389.3, 676.63) * mm, "end": v(-390.07, 676.48) * mm});
            skLineSegment(sketch, "E2088", {"start": v(-390.07, 676.48) * mm, "end": v(-392.4, 676.02) * mm});
            skLineSegment(sketch, "E2089", {"start": v(-392.4, 676.02) * mm, "end": v(-395.88, 675.34) * mm});
            skLineSegment(sketch, "E2090", {"start": v(-395.88, 675.34) * mm, "end": v(-399.78, 674.63) * mm});
            skLineSegment(sketch, "E2091", {"start": v(-399.78, 674.63) * mm, "end": v(-404.1, 673.92) * mm});
            skLineSegment(sketch, "E2092", {"start": v(-404.1, 673.92) * mm, "end": v(-408.85, 673.23) * mm});
            skLineSegment(sketch, "E2093", {"start": v(-408.85, 673.23) * mm, "end": v(-414.05, 672.6) * mm});
            skLineSegment(sketch, "E2094", {"start": v(-414.05, 672.6) * mm, "end": v(-419.73, 672.07) * mm});
            skLineSegment(sketch, "E2095", {"start": v(-419.73, 672.07) * mm, "end": v(-425.89, 671.66) * mm});
            skLineSegment(sketch, "E2096", {"start": v(-425.89, 671.66) * mm, "end": v(-432.54, 671.4) * mm});
            skLineSegment(sketch, "E2097", {"start": v(-432.54, 671.4) * mm, "end": v(-439.72, 671.33) * mm});
            skLineSegment(sketch, "E2098", {"start": v(-439.72, 671.33) * mm, "end": v(-447.42, 671.48) * mm});
            skLineSegment(sketch, "E2099", {"start": v(-447.42, 671.48) * mm, "end": v(-455.67, 671.88) * mm});
            skLineSegment(sketch, "E2100", {"start": v(-455.67, 671.88) * mm, "end": v(-464.48, 672.56) * mm});
            skLineSegment(sketch, "E2101", {"start": v(-464.48, 672.56) * mm, "end": v(-473.87, 673.55) * mm});
            skLineSegment(sketch, "E2102", {"start": v(-473.87, 673.55) * mm, "end": v(-483.86, 674.89) * mm});
            skLineSegment(sketch, "E2103", {"start": v(-483.86, 674.89) * mm, "end": v(-491.8, 676.14) * mm});
            skLineSegment(sketch, "E2104", {"start": v(-491.8, 676.14) * mm, "end": v(-494.45, 676.6) * mm});
            skLineSegment(sketch, "E2105", {"start": v(-494.45, 676.6) * mm, "end": v(-495.55, 676.8) * mm});
            skLineSegment(sketch, "E2106", {"start": v(-495.55, 676.8) * mm, "end": v(-505.96, 678.75) * mm});
            skLineSegment(sketch, "E2107", {"start": v(-505.96, 678.75) * mm, "end": v(-506.94, 678.95) * mm});
            skLineSegment(sketch, "E2108", {"start": v(-387.29, 677) * mm, "end": v(-387.45, 676.98) * mm});
            skLineSegment(sketch, "E2109", {"start": v(-387.45, 676.98) * mm, "end": v(-389.12, 676.66) * mm});
            skLineSegment(sketch, "E2110", {"start": v(-389.12, 676.66) * mm, "end": v(-389.3, 676.63) * mm});
            skLineSegment(sketch, "E2111", {"start": v(-46.92, 670.76) * mm, "end": v(-49.88, 670.1) * mm});
            skLineSegment(sketch, "E2112", {"start": v(-49.88, 670.1) * mm, "end": v(-58.75, 668.13) * mm});
            skLineSegment(sketch, "E2113", {"start": v(-58.75, 668.13) * mm, "end": v(-70.67, 665.55) * mm});
            skLineSegment(sketch, "E2114", {"start": v(-70.67, 665.55) * mm, "end": v(-82.44, 663.07) * mm});
            skLineSegment(sketch, "E2115", {"start": v(-82.44, 663.07) * mm, "end": v(-93.83, 660.73) * mm});
            skLineSegment(sketch, "E2116", {"start": v(-93.83, 660.73) * mm, "end": v(-104.6, 658.61) * mm});
            skLineSegment(sketch, "E2117", {"start": v(-104.6, 658.61) * mm, "end": v(-114.5, 656.76) * mm});
            skLineSegment(sketch, "E2118", {"start": v(-114.5, 656.76) * mm, "end": v(-123.33, 655.23) * mm});
            skLineSegment(sketch, "E2119", {"start": v(-123.33, 655.23) * mm, "end": v(-128.94, 654.35) * mm});
            skLineSegment(sketch, "E2120", {"start": v(-128.94, 654.35) * mm, "end": v(-130.81, 654.09) * mm});
            skLineSegment(sketch, "E2121", {"start": v(-130.81, 654.09) * mm, "end": v(-132.3, 653.88) * mm});
            skLineSegment(sketch, "E2122", {"start": v(-132.3, 653.88) * mm, "end": v(-136.77, 653.21) * mm});
            skLineSegment(sketch, "E2123", {"start": v(-136.77, 653.21) * mm, "end": v(-141.91, 652.38) * mm});
            skLineSegment(sketch, "E2124", {"start": v(-141.91, 652.38) * mm, "end": v(-146.33, 651.57) * mm});
            skLineSegment(sketch, "E2125", {"start": v(-146.33, 651.57) * mm, "end": v(-150.1, 650.8) * mm});
            skLineSegment(sketch, "E2126", {"start": v(-150.1, 650.8) * mm, "end": v(-153.33, 650.08) * mm});
            skLineSegment(sketch, "E2127", {"start": v(-153.33, 650.08) * mm, "end": v(-156.1, 649.4) * mm});
            skLineSegment(sketch, "E2128", {"start": v(-156.1, 649.4) * mm, "end": v(-158.52, 648.77) * mm});
            skLineSegment(sketch, "E2129", {"start": v(-158.52, 648.77) * mm, "end": v(-160.65, 648.18) * mm});
            skLineSegment(sketch, "E2130", {"start": v(-160.65, 648.18) * mm, "end": v(-162.6, 647.65) * mm});
            skLineSegment(sketch, "E2131", {"start": v(-162.6, 647.65) * mm, "end": v(-164.46, 647.18) * mm});
            skLineSegment(sketch, "E2132", {"start": v(-164.46, 647.18) * mm, "end": v(-166.32, 646.75) * mm});
            skLineSegment(sketch, "E2133", {"start": v(-166.32, 646.75) * mm, "end": v(-168.25, 646.4) * mm});
            skLineSegment(sketch, "E2134", {"start": v(-168.25, 646.4) * mm, "end": v(-170.37, 646.1) * mm});
            skLineSegment(sketch, "E2135", {"start": v(-170.37, 646.1) * mm, "end": v(-172.76, 645.87) * mm});
            skLineSegment(sketch, "E2136", {"start": v(-172.76, 645.87) * mm, "end": v(-175.5, 645.71) * mm});
            skLineSegment(sketch, "E2137", {"start": v(-175.5, 645.71) * mm, "end": v(-177.9, 645.64) * mm});
            skLineSegment(sketch, "E2138", {"start": v(-177.9, 645.64) * mm, "end": v(-178.7, 645.63) * mm});
            skLineSegment(sketch, "E2139", {"start": v(-178.7, 645.63) * mm, "end": v(-179.63, 645.62) * mm});
            skLineSegment(sketch, "E2140", {"start": v(-179.63, 645.62) * mm, "end": v(-182.4, 645.84) * mm});
            skLineSegment(sketch, "E2141", {"start": v(-182.4, 645.84) * mm, "end": v(-186.86, 646.53) * mm});
            skLineSegment(sketch, "E2142", {"start": v(-186.86, 646.53) * mm, "end": v(-191.96, 647.65) * mm});
            skLineSegment(sketch, "E2143", {"start": v(-191.96, 647.65) * mm, "end": v(-197.6, 649.13) * mm});
            skLineSegment(sketch, "E2144", {"start": v(-197.6, 649.13) * mm, "end": v(-203.69, 650.92) * mm});
            skLineSegment(sketch, "E2145", {"start": v(-203.69, 650.92) * mm, "end": v(-210.1, 652.97) * mm});
            skLineSegment(sketch, "E2146", {"start": v(-210.1, 652.97) * mm, "end": v(-216.73, 655.2) * mm});
            skLineSegment(sketch, "E2147", {"start": v(-216.73, 655.2) * mm, "end": v(-223.49, 657.57) * mm});
            skLineSegment(sketch, "E2148", {"start": v(-223.49, 657.57) * mm, "end": v(-230.25, 660.02) * mm});
            skLineSegment(sketch, "E2149", {"start": v(-230.25, 660.02) * mm, "end": v(-236.94, 662.5) * mm});
            skLineSegment(sketch, "E2150", {"start": v(-236.94, 662.5) * mm, "end": v(-243.43, 664.92) * mm});
            skLineSegment(sketch, "E2151", {"start": v(-243.43, 664.92) * mm, "end": v(-249.61, 667.27) * mm});
            skLineSegment(sketch, "E2152", {"start": v(-249.61, 667.27) * mm, "end": v(-255.4, 669.45) * mm});
            skLineSegment(sketch, "E2153", {"start": v(-255.4, 669.45) * mm, "end": v(-260.68, 671.44) * mm});
            skLineSegment(sketch, "E2154", {"start": v(-260.68, 671.44) * mm, "end": v(-265.34, 673.15) * mm});
            skLineSegment(sketch, "E2155", {"start": v(-265.34, 673.15) * mm, "end": v(-268.3, 674.2) * mm});
            skLineSegment(sketch, "E2156", {"start": v(-268.3, 674.2) * mm, "end": v(-269.28, 674.54) * mm});
            skLineSegment(sketch, "E2157", {"start": v(-108.97, 671.97) * mm, "end": v(-109.75, 671.84) * mm});
            skLineSegment(sketch, "E2158", {"start": v(-109.75, 671.84) * mm, "end": v(-116.77, 670.76) * mm});
            skLineSegment(sketch, "E2159", {"start": v(-116.77, 670.76) * mm, "end": v(-117.39, 670.67) * mm});
            skLineSegment(sketch, "E2160", {"start": v(-117.39, 670.67) * mm, "end": v(-120.31, 670.27) * mm});
            skLineSegment(sketch, "E2161", {"start": v(-120.31, 670.27) * mm, "end": v(-129.06, 668.96) * mm});
            skLineSegment(sketch, "E2162", {"start": v(-129.06, 668.96) * mm, "end": v(-138.73, 667.38) * mm});
            skLineSegment(sketch, "E2163", {"start": v(-138.73, 667.38) * mm, "end": v(-146.83, 665.96) * mm});
            skLineSegment(sketch, "E2164", {"start": v(-146.83, 665.96) * mm, "end": v(-153.77, 664.73) * mm});
            skLineSegment(sketch, "E2165", {"start": v(-153.77, 664.73) * mm, "end": v(-159.98, 663.7) * mm});
            skLineSegment(sketch, "E2166", {"start": v(-159.98, 663.7) * mm, "end": v(-165.87, 662.91) * mm});
            skLineSegment(sketch, "E2167", {"start": v(-165.87, 662.91) * mm, "end": v(-171.85, 662.38) * mm});
            skLineSegment(sketch, "E2168", {"start": v(-171.85, 662.38) * mm, "end": v(-176.73, 662.15) * mm});
            skLineSegment(sketch, "E2169", {"start": v(-176.73, 662.15) * mm, "end": v(-178.36, 662.13) * mm});
            skLineSegment(sketch, "E2170", {"start": v(-178.36, 662.13) * mm, "end": v(-179.37, 662.11) * mm});
            skLineSegment(sketch, "E2171", {"start": v(-179.37, 662.11) * mm, "end": v(-182.39, 662.34) * mm});
            skLineSegment(sketch, "E2172", {"start": v(-182.39, 662.34) * mm, "end": v(-187.35, 663.04) * mm});
            skLineSegment(sketch, "E2173", {"start": v(-187.35, 663.04) * mm, "end": v(-193.1, 664.16) * mm});
            skLineSegment(sketch, "E2174", {"start": v(-193.1, 664.16) * mm, "end": v(-199.5, 665.65) * mm});
            skLineSegment(sketch, "E2175", {"start": v(-199.5, 665.65) * mm, "end": v(-206.4, 667.45) * mm});
            skLineSegment(sketch, "E2176", {"start": v(-206.4, 667.45) * mm, "end": v(-213.68, 669.5) * mm});
            skLineSegment(sketch, "E2177", {"start": v(-213.68, 669.5) * mm, "end": v(-221.19, 671.73) * mm});
            skLineSegment(sketch, "E2178", {"start": v(-221.19, 671.73) * mm, "end": v(-226.89, 673.49) * mm});
            skLineSegment(sketch, "E2179", {"start": v(-226.89, 673.49) * mm, "end": v(-228.78, 674.08) * mm});
            skLineSegment(sketch, "E2180", {"start": v(608.4, 342.34) * mm, "end": v(607.11, 342.16) * mm});
            skLineSegment(sketch, "E2181", {"start": v(607.11, 342.16) * mm, "end": v(603.26, 341.65) * mm});
            skLineSegment(sketch, "E2182", {"start": v(603.26, 341.65) * mm, "end": v(599.53, 341.2) * mm});
            skLineSegment(sketch, "E2183", {"start": v(599.53, 341.2) * mm, "end": v(596.73, 340.87) * mm});
            skLineSegment(sketch, "E2184", {"start": v(596.73, 340.87) * mm, "end": v(594.37, 340.56) * mm});
            skLineSegment(sketch, "E2185", {"start": v(594.37, 340.56) * mm, "end": v(591.98, 340.15) * mm});
            skLineSegment(sketch, "E2186", {"start": v(591.98, 340.15) * mm, "end": v(589.05, 339.55) * mm});
            skLineSegment(sketch, "E2187", {"start": v(589.05, 339.55) * mm, "end": v(585.11, 338.63) * mm});
            skLineSegment(sketch, "E2188", {"start": v(585.11, 338.63) * mm, "end": v(581.03, 337.63) * mm});
            skLineSegment(sketch, "E2189", {"start": v(581.03, 337.63) * mm, "end": v(579.67, 337.29) * mm});
            skLineSegment(sketch, "E2190", {"start": v(579.67, 337.29) * mm, "end": v(578.9, 337.1) * mm});
            skLineSegment(sketch, "E2191", {"start": v(578.9, 337.1) * mm, "end": v(576.62, 336.37) * mm});
            skLineSegment(sketch, "E2192", {"start": v(576.62, 336.37) * mm, "end": v(573.76, 335.23) * mm});
            skLineSegment(sketch, "E2193", {"start": v(573.76, 335.23) * mm, "end": v(571.06, 333.93) * mm});
            skLineSegment(sketch, "E2194", {"start": v(571.06, 333.93) * mm, "end": v(568.44, 332.5) * mm});
            skLineSegment(sketch, "E2195", {"start": v(568.44, 332.5) * mm, "end": v(565.84, 331.01) * mm});
            skLineSegment(sketch, "E2196", {"start": v(565.84, 331.01) * mm, "end": v(563.22, 329.5) * mm});
            skLineSegment(sketch, "E2197", {"start": v(563.22, 329.5) * mm, "end": v(560.5, 328) * mm});
            skLineSegment(sketch, "E2198", {"start": v(560.5, 328) * mm, "end": v(557.65, 326.6) * mm});
            skLineSegment(sketch, "E2199", {"start": v(557.65, 326.6) * mm, "end": v(554.6, 325.3) * mm});
            skLineSegment(sketch, "E2200", {"start": v(554.6, 325.3) * mm, "end": v(551.27, 324.2) * mm});
            skLineSegment(sketch, "E2201", {"start": v(551.27, 324.2) * mm, "end": v(547.63, 323.3) * mm});
            skLineSegment(sketch, "E2202", {"start": v(547.63, 323.3) * mm, "end": v(543.6, 322.68) * mm});
            skLineSegment(sketch, "E2203", {"start": v(543.6, 322.68) * mm, "end": v(539.15, 322.38) * mm});
            skLineSegment(sketch, "E2204", {"start": v(539.15, 322.38) * mm, "end": v(534.2, 322.44) * mm});
            skLineSegment(sketch, "E2205", {"start": v(534.2, 322.44) * mm, "end": v(528.7, 322.93) * mm});
            skLineSegment(sketch, "E2206", {"start": v(528.7, 322.93) * mm, "end": v(524.12, 323.6) * mm});
            skLineSegment(sketch, "E2207", {"start": v(524.12, 323.6) * mm, "end": v(522.6, 323.89) * mm});
            skLineSegment(sketch, "E2208", {"start": v(522.6, 323.89) * mm, "end": v(521.05, 324.17) * mm});
            skLineSegment(sketch, "E2209", {"start": v(521.05, 324.17) * mm, "end": v(516.43, 325.18) * mm});
            skLineSegment(sketch, "E2210", {"start": v(516.43, 325.18) * mm, "end": v(510.74, 326.65) * mm});
            skLineSegment(sketch, "E2211", {"start": v(510.74, 326.65) * mm, "end": v(505.48, 328.27) * mm});
            skLineSegment(sketch, "E2212", {"start": v(505.48, 328.27) * mm, "end": v(500.58, 330.03) * mm});
            skLineSegment(sketch, "E2213", {"start": v(500.58, 330.03) * mm, "end": v(495.97, 331.92) * mm});
            skLineSegment(sketch, "E2214", {"start": v(495.97, 331.92) * mm, "end": v(491.6, 333.92) * mm});
            skLineSegment(sketch, "E2215", {"start": v(491.6, 333.92) * mm, "end": v(487.39, 336.02) * mm});
            skLineSegment(sketch, "E2216", {"start": v(487.39, 336.02) * mm, "end": v(483.29, 338.2) * mm});
            skLineSegment(sketch, "E2217", {"start": v(483.29, 338.2) * mm, "end": v(479.24, 340.44) * mm});
            skLineSegment(sketch, "E2218", {"start": v(479.24, 340.44) * mm, "end": v(475.17, 342.74) * mm});
            skLineSegment(sketch, "E2219", {"start": v(475.17, 342.74) * mm, "end": v(471.01, 345.07) * mm});
            skLineSegment(sketch, "E2220", {"start": v(471.01, 345.07) * mm, "end": v(466.72, 347.43) * mm});
            skLineSegment(sketch, "E2221", {"start": v(466.72, 347.43) * mm, "end": v(462.22, 349.8) * mm});
            skLineSegment(sketch, "E2222", {"start": v(462.22, 349.8) * mm, "end": v(457.45, 352.15) * mm});
            skLineSegment(sketch, "E2223", {"start": v(457.45, 352.15) * mm, "end": v(452.34, 354.48) * mm});
            skLineSegment(sketch, "E2224", {"start": v(452.34, 354.48) * mm, "end": v(448.23, 356.22) * mm});
            skLineSegment(sketch, "E2225", {"start": v(448.23, 356.22) * mm, "end": v(446.85, 356.77) * mm});
            skLineSegment(sketch, "E2226", {"start": v(446.85, 356.77) * mm, "end": v(445.49, 357.31) * mm});
            skLineSegment(sketch, "E2227", {"start": v(445.49, 357.31) * mm, "end": v(441.4, 358.93) * mm});
            skLineSegment(sketch, "E2228", {"start": v(441.4, 358.93) * mm, "end": v(436.47, 360.89) * mm});
            skLineSegment(sketch, "E2229", {"start": v(436.47, 360.89) * mm, "end": v(432.01, 362.66) * mm});
            skLineSegment(sketch, "E2230", {"start": v(432.01, 362.66) * mm, "end": v(427.97, 364.3) * mm});
            skLineSegment(sketch, "E2231", {"start": v(427.97, 364.3) * mm, "end": v(424.31, 365.81) * mm});
            skLineSegment(sketch, "E2232", {"start": v(424.31, 365.81) * mm, "end": v(421, 367.24) * mm});
            skLineSegment(sketch, "E2233", {"start": v(421, 367.24) * mm, "end": v(417.96, 368.62) * mm});
            skLineSegment(sketch, "E2234", {"start": v(417.96, 368.62) * mm, "end": v(415.17, 369.98) * mm});
            skLineSegment(sketch, "E2235", {"start": v(415.17, 369.98) * mm, "end": v(412.58, 371.34) * mm});
            skLineSegment(sketch, "E2236", {"start": v(412.58, 371.34) * mm, "end": v(410.15, 372.73) * mm});
            skLineSegment(sketch, "E2237", {"start": v(410.15, 372.73) * mm, "end": v(407.84, 374.2) * mm});
            skLineSegment(sketch, "E2238", {"start": v(407.84, 374.2) * mm, "end": v(405.59, 375.74) * mm});
            skLineSegment(sketch, "E2239", {"start": v(405.59, 375.74) * mm, "end": v(403.36, 377.43) * mm});
            skLineSegment(sketch, "E2240", {"start": v(403.36, 377.43) * mm, "end": v(401.12, 379.27) * mm});
            skLineSegment(sketch, "E2241", {"start": v(401.12, 379.27) * mm, "end": v(398.8, 381.3) * mm});
            skLineSegment(sketch, "E2242", {"start": v(398.8, 381.3) * mm, "end": v(396.98, 382.98) * mm});
            skLineSegment(sketch, "E2243", {"start": v(396.98, 382.98) * mm, "end": v(396.38, 383.54) * mm});
            skLineSegment(sketch, "E2244", {"start": v(396.38, 383.54) * mm, "end": v(395.21, 384.65) * mm});
            skLineSegment(sketch, "E2245", {"start": v(395.21, 384.65) * mm, "end": v(391.73, 388) * mm});
            skLineSegment(sketch, "E2246", {"start": v(391.73, 388) * mm, "end": v(387.67, 391.98) * mm});
            skLineSegment(sketch, "E2247", {"start": v(387.67, 391.98) * mm, "end": v(384.09, 395.52) * mm});
            skLineSegment(sketch, "E2248", {"start": v(384.09, 395.52) * mm, "end": v(380.84, 398.68) * mm});
            skLineSegment(sketch, "E2249", {"start": v(380.84, 398.68) * mm, "end": v(377.81, 401.5) * mm});
            skLineSegment(sketch, "E2250", {"start": v(377.81, 401.5) * mm, "end": v(374.89, 404.07) * mm});
            skLineSegment(sketch, "E2251", {"start": v(374.89, 404.07) * mm, "end": v(371.93, 406.42) * mm});
            skLineSegment(sketch, "E2252", {"start": v(371.93, 406.42) * mm, "end": v(369.62, 408.08) * mm});
            skLineSegment(sketch, "E2253", {"start": v(369.62, 408.08) * mm, "end": v(368.82, 408.6) * mm});
            skLineSegment(sketch, "E2254", {"start": v(368.82, 408.6) * mm, "end": v(368.44, 408.86) * mm});
            skLineSegment(sketch, "E2255", {"start": v(368.44, 408.86) * mm, "end": v(367.3, 409.6) * mm});
            skLineSegment(sketch, "E2256", {"start": v(367.3, 409.6) * mm, "end": v(365.9, 410.47) * mm});
            skLineSegment(sketch, "E2257", {"start": v(365.9, 410.47) * mm, "end": v(364.6, 411.25) * mm});
            skLineSegment(sketch, "E2258", {"start": v(364.6, 411.25) * mm, "end": v(363.37, 411.97) * mm});
            skLineSegment(sketch, "E2259", {"start": v(363.37, 411.97) * mm, "end": v(362.18, 412.67) * mm});
            skLineSegment(sketch, "E2260", {"start": v(362.18, 412.67) * mm, "end": v(361, 413.38) * mm});
            skLineSegment(sketch, "E2261", {"start": v(361, 413.38) * mm, "end": v(359.8, 414.14) * mm});
            skLineSegment(sketch, "E2262", {"start": v(359.8, 414.14) * mm, "end": v(358.55, 414.98) * mm});
            skLineSegment(sketch, "E2263", {"start": v(358.55, 414.98) * mm, "end": v(357.21, 415.92) * mm});
            skLineSegment(sketch, "E2264", {"start": v(357.21, 415.92) * mm, "end": v(355.76, 417) * mm});
            skLineSegment(sketch, "E2265", {"start": v(355.76, 417) * mm, "end": v(354.16, 418.27) * mm});
            skLineSegment(sketch, "E2266", {"start": v(354.16, 418.27) * mm, "end": v(352.38, 419.75) * mm});
            skLineSegment(sketch, "E2267", {"start": v(352.38, 419.75) * mm, "end": v(350.38, 421.46) * mm});
            skLineSegment(sketch, "E2268", {"start": v(350.38, 421.46) * mm, "end": v(348.15, 423.46) * mm});
            skLineSegment(sketch, "E2269", {"start": v(348.15, 423.46) * mm, "end": v(345.65, 425.76) * mm});
            skLineSegment(sketch, "E2270", {"start": v(345.65, 425.76) * mm, "end": v(343.54, 427.74) * mm});
            skLineSegment(sketch, "E2271", {"start": v(343.54, 427.74) * mm, "end": v(342.84, 428.4) * mm});
            skLineSegment(sketch, "E2272", {"start": v(342.84, 428.4) * mm, "end": v(341.48, 429.7) * mm});
            skLineSegment(sketch, "E2273", {"start": v(341.48, 429.7) * mm, "end": v(337.7, 433.91) * mm});
            skLineSegment(sketch, "E2274", {"start": v(337.7, 433.91) * mm, "end": v(333.9, 439.13) * mm});
            skLineSegment(sketch, "E2275", {"start": v(333.9, 439.13) * mm, "end": v(330.93, 444.1) * mm});
            skLineSegment(sketch, "E2276", {"start": v(330.93, 444.1) * mm, "end": v(328.35, 448.88) * mm});
            skLineSegment(sketch, "E2277", {"start": v(328.35, 448.88) * mm, "end": v(325.7, 453.48) * mm});
            skLineSegment(sketch, "E2278", {"start": v(325.7, 453.48) * mm, "end": v(322.54, 457.95) * mm});
            skLineSegment(sketch, "E2279", {"start": v(322.54, 457.95) * mm, "end": v(318.37, 462.33) * mm});
            skLineSegment(sketch, "E2280", {"start": v(318.37, 462.33) * mm, "end": v(314.22, 465.68) * mm});
            skLineSegment(sketch, "E2281", {"start": v(314.22, 465.68) * mm, "end": v(312.75, 466.66) * mm});
            skLineSegment(sketch, "E2282", {"start": v(312.75, 466.66) * mm, "end": v(311.98, 467.17) * mm});
            skLineSegment(sketch, "E2283", {"start": v(311.98, 467.17) * mm, "end": v(309.63, 468.61) * mm});
            skLineSegment(sketch, "E2284", {"start": v(309.63, 468.61) * mm, "end": v(306.73, 470.2) * mm});
            skLineSegment(sketch, "E2285", {"start": v(306.73, 470.2) * mm, "end": v(303.98, 471.49) * mm});
            skLineSegment(sketch, "E2286", {"start": v(303.98, 471.49) * mm, "end": v(301.34, 472.53) * mm});
            skLineSegment(sketch, "E2287", {"start": v(301.34, 472.53) * mm, "end": v(298.75, 473.37) * mm});
            skLineSegment(sketch, "E2288", {"start": v(298.75, 473.37) * mm, "end": v(296.16, 474.1) * mm});
            skLineSegment(sketch, "E2289", {"start": v(296.16, 474.1) * mm, "end": v(293.5, 474.75) * mm});
            skLineSegment(sketch, "E2290", {"start": v(293.5, 474.75) * mm, "end": v(290.75, 475.39) * mm});
            skLineSegment(sketch, "E2291", {"start": v(290.75, 475.39) * mm, "end": v(287.8, 476.07) * mm});
            skLineSegment(sketch, "E2292", {"start": v(287.8, 476.07) * mm, "end": v(284.66, 476.87) * mm});
            skLineSegment(sketch, "E2293", {"start": v(284.66, 476.87) * mm, "end": v(281.22, 477.83) * mm});
            skLineSegment(sketch, "E2294", {"start": v(281.22, 477.83) * mm, "end": v(277.45, 479.01) * mm});
            skLineSegment(sketch, "E2295", {"start": v(277.45, 479.01) * mm, "end": v(273.3, 480.48) * mm});
            skLineSegment(sketch, "E2296", {"start": v(273.3, 480.48) * mm, "end": v(268.7, 482.28) * mm});
            skLineSegment(sketch, "E2297", {"start": v(268.7, 482.28) * mm, "end": v(263.6, 484.5) * mm});
            skLineSegment(sketch, "E2298", {"start": v(263.6, 484.5) * mm, "end": v(259.35, 486.47) * mm});
            skLineSegment(sketch, "E2299", {"start": v(259.35, 486.47) * mm, "end": v(257.95, 487.16) * mm});
            skLineSegment(sketch, "E2300", {"start": v(257.95, 487.16) * mm, "end": v(256.4, 487.92) * mm});
            skLineSegment(sketch, "E2301", {"start": v(256.4, 487.92) * mm, "end": v(251.75, 490.17) * mm});
            skLineSegment(sketch, "E2302", {"start": v(251.75, 490.17) * mm, "end": v(245.07, 493.33) * mm});
            skLineSegment(sketch, "E2303", {"start": v(245.07, 493.33) * mm, "end": v(238, 496.6) * mm});
            skLineSegment(sketch, "E2304", {"start": v(238, 496.6) * mm, "end": v(230.61, 499.94) * mm});
            skLineSegment(sketch, "E2305", {"start": v(230.61, 499.94) * mm, "end": v(222.98, 503.32) * mm});
            skLineSegment(sketch, "E2306", {"start": v(222.98, 503.32) * mm, "end": v(215.18, 506.68) * mm});
            skLineSegment(sketch, "E2307", {"start": v(215.18, 506.68) * mm, "end": v(207.3, 510) * mm});
            skLineSegment(sketch, "E2308", {"start": v(207.3, 510) * mm, "end": v(199.39, 513.24) * mm});
            skLineSegment(sketch, "E2309", {"start": v(199.39, 513.24) * mm, "end": v(191.54, 516.35) * mm});
            skLineSegment(sketch, "E2310", {"start": v(191.54, 516.35) * mm, "end": v(183.82, 519.3) * mm});
            skLineSegment(sketch, "E2311", {"start": v(183.82, 519.3) * mm, "end": v(176.32, 522.02) * mm});
            skLineSegment(sketch, "E2312", {"start": v(176.32, 522.02) * mm, "end": v(169.1, 524.5) * mm});
            skLineSegment(sketch, "E2313", {"start": v(169.1, 524.5) * mm, "end": v(162.24, 526.7) * mm});
            skLineSegment(sketch, "E2314", {"start": v(162.24, 526.7) * mm, "end": v(155.82, 528.58) * mm});
            skLineSegment(sketch, "E2315", {"start": v(155.82, 528.58) * mm, "end": v(149.9, 530.09) * mm});
            skLineSegment(sketch, "E2316", {"start": v(149.9, 530.09) * mm, "end": v(145.92, 530.96) * mm});
            skLineSegment(sketch, "E2317", {"start": v(145.92, 530.96) * mm, "end": v(144.58, 531.19) * mm});
            skLineSegment(sketch, "E2318", {"start": v(144.58, 531.19) * mm, "end": v(142.16, 531.62) * mm});
            skLineSegment(sketch, "E2319", {"start": v(142.16, 531.62) * mm, "end": v(134.85, 532.6) * mm});
            skLineSegment(sketch, "E2320", {"start": v(134.85, 532.6) * mm, "end": v(125.57, 533.4) * mm});
            skLineSegment(sketch, "E2321", {"start": v(125.57, 533.4) * mm, "end": v(116.61, 533.7) * mm});
            skLineSegment(sketch, "E2322", {"start": v(116.61, 533.7) * mm, "end": v(107.81, 533.63) * mm});
            skLineSegment(sketch, "E2323", {"start": v(107.81, 533.63) * mm, "end": v(99.03, 533.3) * mm});
            skLineSegment(sketch, "E2324", {"start": v(99.03, 533.3) * mm, "end": v(90.12, 532.83) * mm});
            skLineSegment(sketch, "E2325", {"start": v(90.12, 532.83) * mm, "end": v(80.93, 532.34) * mm});
            skLineSegment(sketch, "E2326", {"start": v(80.93, 532.34) * mm, "end": v(73.72, 532.03) * mm});
            skLineSegment(sketch, "E2327", {"start": v(73.72, 532.03) * mm, "end": v(71.32, 531.96) * mm});
            skLineSegment(sketch, "E2328", {"start": v(71.32, 531.96) * mm, "end": v(70.12, 531.93) * mm});
            skLineSegment(sketch, "E2329", {"start": v(70.12, 531.93) * mm, "end": v(66.53, 531.82) * mm});
            skLineSegment(sketch, "E2330", {"start": v(66.53, 531.82) * mm, "end": v(62.17, 531.69) * mm});
            skLineSegment(sketch, "E2331", {"start": v(62.17, 531.69) * mm, "end": v(58.18, 531.55) * mm});
            skLineSegment(sketch, "E2332", {"start": v(58.18, 531.55) * mm, "end": v(54.46, 531.38) * mm});
            skLineSegment(sketch, "E2333", {"start": v(54.46, 531.38) * mm, "end": v(50.95, 531.2) * mm});
            skLineSegment(sketch, "E2334", {"start": v(50.95, 531.2) * mm, "end": v(47.56, 530.98) * mm});
            skLineSegment(sketch, "E2335", {"start": v(47.56, 530.98) * mm, "end": v(44.21, 530.71) * mm});
            skLineSegment(sketch, "E2336", {"start": v(44.21, 530.71) * mm, "end": v(40.84, 530.4) * mm});
            skLineSegment(sketch, "E2337", {"start": v(40.84, 530.4) * mm, "end": v(37.35, 530.01) * mm});
            skLineSegment(sketch, "E2338", {"start": v(37.35, 530.01) * mm, "end": v(33.67, 529.56) * mm});
            skLineSegment(sketch, "E2339", {"start": v(33.67, 529.56) * mm, "end": v(29.73, 529.03) * mm});
            skLineSegment(sketch, "E2340", {"start": v(29.73, 529.03) * mm, "end": v(25.44, 528.4) * mm});
            skLineSegment(sketch, "E2341", {"start": v(25.44, 528.4) * mm, "end": v(20.73, 527.67) * mm});
            skLineSegment(sketch, "E2342", {"start": v(20.73, 527.67) * mm, "end": v(15.52, 526.83) * mm});
            skLineSegment(sketch, "E2343", {"start": v(15.52, 526.83) * mm, "end": v(9.72, 525.88) * mm});
            skLineSegment(sketch, "E2344", {"start": v(9.72, 525.88) * mm, "end": v(4.89, 525.06) * mm});
            skLineSegment(sketch, "E2345", {"start": v(4.89, 525.06) * mm, "end": v(3.27, 524.79) * mm});
            skLineSegment(sketch, "E2346", {"start": v(3.27, 524.79) * mm, "end": v(1.28, 524.45) * mm});
            skLineSegment(sketch, "E2347", {"start": v(1.28, 524.45) * mm, "end": v(-4.67, 523.39) * mm});
            skLineSegment(sketch, "E2348", {"start": v(-4.67, 523.39) * mm, "end": v(-12.85, 521.86) * mm});
            skLineSegment(sketch, "E2349", {"start": v(-12.85, 521.86) * mm, "end": v(-21.28, 520.22) * mm});
            skLineSegment(sketch, "E2350", {"start": v(-21.28, 520.22) * mm, "end": v(-30.01, 518.5) * mm});
            skLineSegment(sketch, "E2351", {"start": v(-30.01, 518.5) * mm, "end": v(-39.07, 516.73) * mm});
            skLineSegment(sketch, "E2352", {"start": v(-39.07, 516.73) * mm, "end": v(-48.5, 514.92) * mm});
            skLineSegment(sketch, "E2353", {"start": v(-48.5, 514.92) * mm, "end": v(-58.32, 513.1) * mm});
            skLineSegment(sketch, "E2354", {"start": v(-58.32, 513.1) * mm, "end": v(-68.57, 511.29) * mm});
            skLineSegment(sketch, "E2355", {"start": v(-68.57, 511.29) * mm, "end": v(-79.29, 509.51) * mm});
            skLineSegment(sketch, "E2356", {"start": v(-79.29, 509.51) * mm, "end": v(-90.5, 507.8) * mm});
            skLineSegment(sketch, "E2357", {"start": v(-90.5, 507.8) * mm, "end": v(-102.25, 506.16) * mm});
            skLineSegment(sketch, "E2358", {"start": v(-102.25, 506.16) * mm, "end": v(-114.55, 504.63) * mm});
            skLineSegment(sketch, "E2359", {"start": v(-114.55, 504.63) * mm, "end": v(-127.46, 503.23) * mm});
            skLineSegment(sketch, "E2360", {"start": v(-127.46, 503.23) * mm, "end": v(-141, 501.98) * mm});
            skLineSegment(sketch, "E2361", {"start": v(-141, 501.98) * mm, "end": v(-155.19, 500.9) * mm});
            skLineSegment(sketch, "E2362", {"start": v(-155.19, 500.9) * mm, "end": v(-166.36, 500.22) * mm});
            skLineSegment(sketch, "E2363", {"start": v(-166.36, 500.22) * mm, "end": v(-170.08, 500.03) * mm});
            skLineSegment(sketch, "E2364", {"start": v(-170.08, 500.03) * mm, "end": v(-173.77, 499.84) * mm});
            skLineSegment(sketch, "E2365", {"start": v(-173.77, 499.84) * mm, "end": v(-184.83, 499.3) * mm});
            skLineSegment(sketch, "E2366", {"start": v(-184.83, 499.3) * mm, "end": v(-198.58, 498.67) * mm});
            skLineSegment(sketch, "E2367", {"start": v(-198.58, 498.67) * mm, "end": v(-211.38, 498.12) * mm});
            skLineSegment(sketch, "E2368", {"start": v(-211.38, 498.12) * mm, "end": v(-223.28, 497.68) * mm});
            skLineSegment(sketch, "E2369", {"start": v(-223.28, 497.68) * mm, "end": v(-234.33, 497.33) * mm});
            skLineSegment(sketch, "E2370", {"start": v(-234.33, 497.33) * mm, "end": v(-244.56, 497.1) * mm});
            skLineSegment(sketch, "E2371", {"start": v(-244.56, 497.1) * mm, "end": v(-254.02, 496.98) * mm});
            skLineSegment(sketch, "E2372", {"start": v(-254.02, 496.98) * mm, "end": v(-262.77, 496.97) * mm});
            skLineSegment(sketch, "E2373", {"start": v(-262.77, 496.97) * mm, "end": v(-270.85, 497.1) * mm});
            skLineSegment(sketch, "E2374", {"start": v(-270.85, 497.1) * mm, "end": v(-278.29, 497.34) * mm});
            skLineSegment(sketch, "E2375", {"start": v(-278.29, 497.34) * mm, "end": v(-285.15, 497.71) * mm});
            skLineSegment(sketch, "E2376", {"start": v(-285.15, 497.71) * mm, "end": v(-291.47, 498.23) * mm});
            skLineSegment(sketch, "E2377", {"start": v(-291.47, 498.23) * mm, "end": v(-297.3, 498.89) * mm});
            skLineSegment(sketch, "E2378", {"start": v(-297.3, 498.89) * mm, "end": v(-302.69, 499.69) * mm});
            skLineSegment(sketch, "E2379", {"start": v(-302.69, 499.69) * mm, "end": v(-307.67, 500.64) * mm});
            skLineSegment(sketch, "E2380", {"start": v(-307.67, 500.64) * mm, "end": v(-311.15, 501.45) * mm});
            skLineSegment(sketch, "E2381", {"start": v(-311.15, 501.45) * mm, "end": v(-312.3, 501.75) * mm});
            skLineSegment(sketch, "E2382", {"start": v(-312.3, 501.75) * mm, "end": v(-314.28, 502.28) * mm});
            skLineSegment(sketch, "E2383", {"start": v(-314.28, 502.28) * mm, "end": v(-320.18, 504.12) * mm});
            skLineSegment(sketch, "E2384", {"start": v(-320.18, 504.12) * mm, "end": v(-326.2, 506.44) * mm});
            skLineSegment(sketch, "E2385", {"start": v(-326.2, 506.44) * mm, "end": v(-330.77, 508.64) * mm});
            skLineSegment(sketch, "E2386", {"start": v(-330.77, 508.64) * mm, "end": v(-334.26, 510.68) * mm});
            skLineSegment(sketch, "E2387", {"start": v(-334.26, 510.68) * mm, "end": v(-337.05, 512.5) * mm});
            skLineSegment(sketch, "E2388", {"start": v(-337.05, 512.5) * mm, "end": v(-339.53, 514.03) * mm});
            skLineSegment(sketch, "E2389", {"start": v(-339.53, 514.03) * mm, "end": v(-342.09, 515.23) * mm});
            skLineSegment(sketch, "E2390", {"start": v(-342.09, 515.23) * mm, "end": v(-344.34, 515.9) * mm});
            skLineSegment(sketch, "E2391", {"start": v(-344.34, 515.9) * mm, "end": v(-345.1, 516.04) * mm});
            skLineSegment(sketch, "E2392", {"start": v(-345.1, 516.04) * mm, "end": v(-346.15, 516.22) * mm});
            skLineSegment(sketch, "E2393", {"start": v(-346.15, 516.22) * mm, "end": v(-349.37, 516.4) * mm});
            skLineSegment(sketch, "E2394", {"start": v(-349.37, 516.4) * mm, "end": v(-355.12, 516.36) * mm});
            skLineSegment(sketch, "E2395", {"start": v(-355.12, 516.36) * mm, "end": v(-361.96, 516.05) * mm});
            skLineSegment(sketch, "E2396", {"start": v(-361.96, 516.05) * mm, "end": v(-369.46, 515.6) * mm});
            skLineSegment(sketch, "E2397", {"start": v(-369.46, 515.6) * mm, "end": v(-377.21, 515.12) * mm});
            skLineSegment(sketch, "E2398", {"start": v(-377.21, 515.12) * mm, "end": v(-384.8, 514.74) * mm});
            skLineSegment(sketch, "E2399", {"start": v(-384.8, 514.74) * mm, "end": v(-391.8, 514.57) * mm});
            skLineSegment(sketch, "E2400", {"start": v(-391.8, 514.57) * mm, "end": v(-396.3, 514.65) * mm});
            skLineSegment(sketch, "E2401", {"start": v(-396.3, 514.65) * mm, "end": v(-397.79, 514.76) * mm});
            skLineSegment(sketch, "E2402", {"start": v(-397.79, 514.76) * mm, "end": v(-398.24, 514.8) * mm});
            skLineSegment(sketch, "E2403", {"start": v(-398.24, 514.8) * mm, "end": v(-399.59, 514.95) * mm});
            skLineSegment(sketch, "E2404", {"start": v(-399.59, 514.95) * mm, "end": v(-402.26, 515.32) * mm});
            skLineSegment(sketch, "E2405", {"start": v(-402.26, 515.32) * mm, "end": v(-405.76, 515.85) * mm});
            skLineSegment(sketch, "E2406", {"start": v(-405.76, 515.85) * mm, "end": v(-410.01, 516.53) * mm});
            skLineSegment(sketch, "E2407", {"start": v(-410.01, 516.53) * mm, "end": v(-414.96, 517.36) * mm});
            skLineSegment(sketch, "E2408", {"start": v(-414.96, 517.36) * mm, "end": v(-420.53, 518.32) * mm});
            skLineSegment(sketch, "E2409", {"start": v(-420.53, 518.32) * mm, "end": v(-426.69, 519.39) * mm});
            skLineSegment(sketch, "E2410", {"start": v(-426.69, 519.39) * mm, "end": v(-433.35, 520.56) * mm});
            skLineSegment(sketch, "E2411", {"start": v(-433.35, 520.56) * mm, "end": v(-440.46, 521.83) * mm});
            skLineSegment(sketch, "E2412", {"start": v(-440.46, 521.83) * mm, "end": v(-447.96, 523.18) * mm});
            skLineSegment(sketch, "E2413", {"start": v(-447.96, 523.18) * mm, "end": v(-455.78, 524.6) * mm});
            skLineSegment(sketch, "E2414", {"start": v(-455.78, 524.6) * mm, "end": v(-463.87, 526.07) * mm});
            skLineSegment(sketch, "E2415", {"start": v(-463.87, 526.07) * mm, "end": v(-472.16, 527.6) * mm});
            skLineSegment(sketch, "E2416", {"start": v(-472.16, 527.6) * mm, "end": v(-480.6, 529.15) * mm});
            skLineSegment(sketch, "E2417", {"start": v(-480.6, 529.15) * mm, "end": v(-489.11, 530.72) * mm});
            skLineSegment(sketch, "E2418", {"start": v(-489.11, 530.72) * mm, "end": v(-497.65, 532.3) * mm});
            skLineSegment(sketch, "E2419", {"start": v(-497.65, 532.3) * mm, "end": v(-506.14, 533.88) * mm});
            skLineSegment(sketch, "E2420", {"start": v(-506.14, 533.88) * mm, "end": v(-514.53, 535.44) * mm});
            skLineSegment(sketch, "E2421", {"start": v(-514.53, 535.44) * mm, "end": v(-522.76, 536.98) * mm});
            skLineSegment(sketch, "E2422", {"start": v(-522.76, 536.98) * mm, "end": v(-530.76, 538.48) * mm});
            skLineSegment(sketch, "E2423", {"start": v(-530.76, 538.48) * mm, "end": v(-538.47, 539.93) * mm});
            skLineSegment(sketch, "E2424", {"start": v(-538.47, 539.93) * mm, "end": v(-545.84, 541.3) * mm});
            skLineSegment(sketch, "E2425", {"start": v(-545.84, 541.3) * mm, "end": v(-552.8, 542.62) * mm});
            skLineSegment(sketch, "E2426", {"start": v(-552.8, 542.62) * mm, "end": v(-559.27, 543.84) * mm});
            skLineSegment(sketch, "E2427", {"start": v(-559.27, 543.84) * mm, "end": v(-565.22, 544.96) * mm});
            skLineSegment(sketch, "E2428", {"start": v(-565.22, 544.96) * mm, "end": v(-570.58, 545.98) * mm});
            skLineSegment(sketch, "E2429", {"start": v(-570.58, 545.98) * mm, "end": v(-575.28, 546.87) * mm});
            skLineSegment(sketch, "E2430", {"start": v(-575.28, 546.87) * mm, "end": v(-579.26, 547.62) * mm});
            skLineSegment(sketch, "E2431", {"start": v(-579.26, 547.62) * mm, "end": v(-582.47, 548.23) * mm});
            skLineSegment(sketch, "E2432", {"start": v(-582.47, 548.23) * mm, "end": v(-584.83, 548.68) * mm});
            skLineSegment(sketch, "E2433", {"start": v(-584.83, 548.68) * mm, "end": v(-586.3, 548.95) * mm});
            skLineSegment(sketch, "E2434", {"start": v(-586.3, 548.95) * mm, "end": v(-586.8, 549.05) * mm});
            skLineSegment(sketch, "E2435", {"start": v(609.45, 309.24) * mm, "end": v(608.25, 308.7) * mm});
            skLineSegment(sketch, "E2436", {"start": v(608.25, 308.7) * mm, "end": v(604.65, 307) * mm});
            skLineSegment(sketch, "E2437", {"start": v(604.65, 307) * mm, "end": v(601.1, 305.15) * mm});
            skLineSegment(sketch, "E2438", {"start": v(601.1, 305.15) * mm, "end": v(598.32, 303.6) * mm});
            skLineSegment(sketch, "E2439", {"start": v(598.32, 303.6) * mm, "end": v(595.9, 302.29) * mm});
            skLineSegment(sketch, "E2440", {"start": v(595.9, 302.29) * mm, "end": v(593.38, 301.07) * mm});
            skLineSegment(sketch, "E2441", {"start": v(593.38, 301.07) * mm, "end": v(590.32, 299.88) * mm});
            skLineSegment(sketch, "E2442", {"start": v(590.32, 299.88) * mm, "end": v(586.27, 298.6) * mm});
            skLineSegment(sketch, "E2443", {"start": v(586.27, 298.6) * mm, "end": v(582.16, 297.48) * mm});
            skLineSegment(sketch, "E2444", {"start": v(582.16, 297.48) * mm, "end": v(580.78, 297.13) * mm});
            skLineSegment(sketch, "E2445", {"start": v(580.78, 297.13) * mm, "end": v(579.98, 296.93) * mm});
            skLineSegment(sketch, "E2446", {"start": v(579.98, 296.93) * mm, "end": v(577.6, 296.25) * mm});
            skLineSegment(sketch, "E2447", {"start": v(577.6, 296.25) * mm, "end": v(574.37, 295.24) * mm});
            skLineSegment(sketch, "E2448", {"start": v(574.37, 295.24) * mm, "end": v(571.09, 294.13) * mm});
            skLineSegment(sketch, "E2449", {"start": v(571.09, 294.13) * mm, "end": v(567.73, 292.98) * mm});
            skLineSegment(sketch, "E2450", {"start": v(567.73, 292.98) * mm, "end": v(564.27, 291.85) * mm});
            skLineSegment(sketch, "E2451", {"start": v(564.27, 291.85) * mm, "end": v(560.7, 290.77) * mm});
            skLineSegment(sketch, "E2452", {"start": v(560.7, 290.77) * mm, "end": v(556.98, 289.8) * mm});
            skLineSegment(sketch, "E2453", {"start": v(556.98, 289.8) * mm, "end": v(553.1, 289) * mm});
            skLineSegment(sketch, "E2454", {"start": v(553.1, 289) * mm, "end": v(549.06, 288.4) * mm});
            skLineSegment(sketch, "E2455", {"start": v(549.06, 288.4) * mm, "end": v(544.8, 288.07) * mm});
            skLineSegment(sketch, "E2456", {"start": v(544.8, 288.07) * mm, "end": v(540.34, 288.03) * mm});
            skLineSegment(sketch, "E2457", {"start": v(540.34, 288.03) * mm, "end": v(535.63, 288.36) * mm});
            skLineSegment(sketch, "E2458", {"start": v(535.63, 288.36) * mm, "end": v(530.66, 289.09) * mm});
            skLineSegment(sketch, "E2459", {"start": v(530.66, 289.09) * mm, "end": v(525.42, 290.27) * mm});
            skLineSegment(sketch, "E2460", {"start": v(525.42, 290.27) * mm, "end": v(519.87, 291.97) * mm});
            skLineSegment(sketch, "E2461", {"start": v(519.87, 291.97) * mm, "end": v(515.46, 293.6) * mm});
            skLineSegment(sketch, "E2462", {"start": v(515.46, 293.6) * mm, "end": v(514.01, 294.22) * mm});
            skLineSegment(sketch, "E2463", {"start": v(514.01, 294.22) * mm, "end": v(511.78, 295.16) * mm});
            skLineSegment(sketch, "E2464", {"start": v(511.78, 295.16) * mm, "end": v(505.1, 297.96) * mm});
            skLineSegment(sketch, "E2465", {"start": v(505.1, 297.96) * mm, "end": v(496.94, 301.36) * mm});
            skLineSegment(sketch, "E2466", {"start": v(496.94, 301.36) * mm, "end": v(489.46, 304.47) * mm});
            skLineSegment(sketch, "E2467", {"start": v(489.46, 304.47) * mm, "end": v(482.62, 307.33) * mm});
            skLineSegment(sketch, "E2468", {"start": v(482.62, 307.33) * mm, "end": v(476.32, 310) * mm});
            skLineSegment(sketch, "E2469", {"start": v(476.32, 310) * mm, "end": v(470.5, 312.51) * mm});
            skLineSegment(sketch, "E2470", {"start": v(470.5, 312.51) * mm, "end": v(465.12, 314.92) * mm});
            skLineSegment(sketch, "E2471", {"start": v(465.12, 314.92) * mm, "end": v(460.07, 317.28) * mm});
            skLineSegment(sketch, "E2472", {"start": v(460.07, 317.28) * mm, "end": v(455.3, 319.63) * mm});
            skLineSegment(sketch, "E2473", {"start": v(455.3, 319.63) * mm, "end": v(450.76, 322.02) * mm});
            skLineSegment(sketch, "E2474", {"start": v(450.76, 322.02) * mm, "end": v(446.35, 324.5) * mm});
            skLineSegment(sketch, "E2475", {"start": v(446.35, 324.5) * mm, "end": v(442.02, 327.1) * mm});
            skLineSegment(sketch, "E2476", {"start": v(442.02, 327.1) * mm, "end": v(437.7, 329.9) * mm});
            skLineSegment(sketch, "E2477", {"start": v(437.7, 329.9) * mm, "end": v(433.31, 332.93) * mm});
            skLineSegment(sketch, "E2478", {"start": v(433.31, 332.93) * mm, "end": v(428.8, 336.23) * mm});
            skLineSegment(sketch, "E2479", {"start": v(428.8, 336.23) * mm, "end": v(425.26, 338.94) * mm});
            skLineSegment(sketch, "E2480", {"start": v(425.26, 338.94) * mm, "end": v(424.1, 339.86) * mm});
            skLineSegment(sketch, "E2481", {"start": v(424.1, 339.86) * mm, "end": v(421.7, 341.75) * mm});
            skLineSegment(sketch, "E2482", {"start": v(421.7, 341.75) * mm, "end": v(414.53, 347.42) * mm});
            skLineSegment(sketch, "E2483", {"start": v(414.53, 347.42) * mm, "end": v(404.75, 355.17) * mm});
            skLineSegment(sketch, "E2484", {"start": v(404.75, 355.17) * mm, "end": v(394.98, 363) * mm});
            skLineSegment(sketch, "E2485", {"start": v(394.98, 363) * mm, "end": v(385.43, 370.73) * mm});
            skLineSegment(sketch, "E2486", {"start": v(385.43, 370.73) * mm, "end": v(376.31, 378.25) * mm});
            skLineSegment(sketch, "E2487", {"start": v(376.31, 378.25) * mm, "end": v(367.84, 385.4) * mm});
            skLineSegment(sketch, "E2488", {"start": v(367.84, 385.4) * mm, "end": v(360.22, 392.07) * mm});
            skLineSegment(sketch, "E2489", {"start": v(360.22, 392.07) * mm, "end": v(355.28, 396.56) * mm});
            skLineSegment(sketch, "E2490", {"start": v(355.28, 396.56) * mm, "end": v(353.67, 398.1) * mm});
            skLineSegment(sketch, "E2491", {"start": v(353.67, 398.1) * mm, "end": v(352.09, 399.6) * mm});
            skLineSegment(sketch, "E2492", {"start": v(352.09, 399.6) * mm, "end": v(347.3, 404.08) * mm});
            skLineSegment(sketch, "E2493", {"start": v(347.3, 404.08) * mm, "end": v(340.2, 410.57) * mm});
            skLineSegment(sketch, "E2494", {"start": v(340.2, 410.57) * mm, "end": v(332.6, 417.34) * mm});
            skLineSegment(sketch, "E2495", {"start": v(332.6, 417.34) * mm, "end": v(324.7, 424.17) * mm});
            skLineSegment(sketch, "E2496", {"start": v(324.7, 424.17) * mm, "end": v(316.75, 430.83) * mm});
            skLineSegment(sketch, "E2497", {"start": v(316.75, 430.83) * mm, "end": v(308.93, 437.1) * mm});
            skLineSegment(sketch, "E2498", {"start": v(308.93, 437.1) * mm, "end": v(301.49, 442.75) * mm});
            skLineSegment(sketch, "E2499", {"start": v(301.49, 442.75) * mm, "end": v(296.38, 446.4) * mm});
            skLineSegment(sketch, "E2500", {"start": v(296.38, 446.4) * mm, "end": v(294.63, 447.56) * mm});
            skLineSegment(sketch, "E2501", {"start": v(294.63, 447.56) * mm, "end": v(293.86, 448.07) * mm});
            skLineSegment(sketch, "E2502", {"start": v(293.86, 448.07) * mm, "end": v(291.56, 449.57) * mm});
            skLineSegment(sketch, "E2503", {"start": v(291.56, 449.57) * mm, "end": v(288.78, 451.33) * mm});
            skLineSegment(sketch, "E2504", {"start": v(288.78, 451.33) * mm, "end": v(286.24, 452.86) * mm});
            skLineSegment(sketch, "E2505", {"start": v(286.24, 452.86) * mm, "end": v(283.87, 454.23) * mm});
            skLineSegment(sketch, "E2506", {"start": v(283.87, 454.23) * mm, "end": v(281.6, 455.46) * mm});
            skLineSegment(sketch, "E2507", {"start": v(281.6, 455.46) * mm, "end": v(279.35, 456.62) * mm});
            skLineSegment(sketch, "E2508", {"start": v(279.35, 456.62) * mm, "end": v(277.07, 457.73) * mm});
            skLineSegment(sketch, "E2509", {"start": v(277.07, 457.73) * mm, "end": v(274.7, 458.85) * mm});
            skLineSegment(sketch, "E2510", {"start": v(274.7, 458.85) * mm, "end": v(272.15, 460.02) * mm});
            skLineSegment(sketch, "E2511", {"start": v(272.15, 460.02) * mm, "end": v(269.37, 461.27) * mm});
            skLineSegment(sketch, "E2512", {"start": v(269.37, 461.27) * mm, "end": v(266.28, 462.66) * mm});
            skLineSegment(sketch, "E2513", {"start": v(266.28, 462.66) * mm, "end": v(262.83, 464.24) * mm});
            skLineSegment(sketch, "E2514", {"start": v(262.83, 464.24) * mm, "end": v(258.93, 466.03) * mm});
            skLineSegment(sketch, "E2515", {"start": v(258.93, 466.03) * mm, "end": v(254.54, 468.09) * mm});
            skLineSegment(sketch, "E2516", {"start": v(254.54, 468.09) * mm, "end": v(249.58, 470.46) * mm});
            skLineSegment(sketch, "E2517", {"start": v(249.58, 470.46) * mm, "end": v(245.37, 472.5) * mm});
            skLineSegment(sketch, "E2518", {"start": v(245.37, 472.5) * mm, "end": v(243.97, 473.19) * mm});
            skLineSegment(sketch, "E2519", {"start": v(243.97, 473.19) * mm, "end": v(242.42, 473.94) * mm});
            skLineSegment(sketch, "E2520", {"start": v(242.42, 473.94) * mm, "end": v(237.77, 476.2) * mm});
            skLineSegment(sketch, "E2521", {"start": v(237.77, 476.2) * mm, "end": v(231.1, 479.35) * mm});
            skLineSegment(sketch, "E2522", {"start": v(231.1, 479.35) * mm, "end": v(224.02, 482.62) * mm});
            skLineSegment(sketch, "E2523", {"start": v(224.02, 482.62) * mm, "end": v(216.64, 485.97) * mm});
            skLineSegment(sketch, "E2524", {"start": v(216.64, 485.97) * mm, "end": v(209, 489.34) * mm});
            skLineSegment(sketch, "E2525", {"start": v(209, 489.34) * mm, "end": v(201.2, 492.71) * mm});
            skLineSegment(sketch, "E2526", {"start": v(201.2, 492.71) * mm, "end": v(193.32, 496.03) * mm});
            skLineSegment(sketch, "E2527", {"start": v(193.32, 496.03) * mm, "end": v(185.4, 499.27) * mm});
            skLineSegment(sketch, "E2528", {"start": v(185.4, 499.27) * mm, "end": v(177.56, 502.37) * mm});
            skLineSegment(sketch, "E2529", {"start": v(177.56, 502.37) * mm, "end": v(169.84, 505.31) * mm});
            skLineSegment(sketch, "E2530", {"start": v(169.84, 505.31) * mm, "end": v(162.34, 508.05) * mm});
            skLineSegment(sketch, "E2531", {"start": v(162.34, 508.05) * mm, "end": v(155.12, 510.53) * mm});
            skLineSegment(sketch, "E2532", {"start": v(155.12, 510.53) * mm, "end": v(148.26, 512.73) * mm});
            skLineSegment(sketch, "E2533", {"start": v(148.26, 512.73) * mm, "end": v(141.84, 514.6) * mm});
            skLineSegment(sketch, "E2534", {"start": v(141.84, 514.6) * mm, "end": v(135.93, 516.12) * mm});
            skLineSegment(sketch, "E2535", {"start": v(135.93, 516.12) * mm, "end": v(131.94, 516.98) * mm});
            skLineSegment(sketch, "E2536", {"start": v(131.94, 516.98) * mm, "end": v(130.6, 517.21) * mm});
            skLineSegment(sketch, "E2537", {"start": v(130.6, 517.21) * mm, "end": v(128.19, 517.65) * mm});
            skLineSegment(sketch, "E2538", {"start": v(128.19, 517.65) * mm, "end": v(120.87, 518.63) * mm});
            skLineSegment(sketch, "E2539", {"start": v(120.87, 518.63) * mm, "end": v(111.6, 519.43) * mm});
            skLineSegment(sketch, "E2540", {"start": v(111.6, 519.43) * mm, "end": v(102.64, 519.73) * mm});
            skLineSegment(sketch, "E2541", {"start": v(102.64, 519.73) * mm, "end": v(93.84, 519.65) * mm});
            skLineSegment(sketch, "E2542", {"start": v(93.84, 519.65) * mm, "end": v(85.05, 519.32) * mm});
            skLineSegment(sketch, "E2543", {"start": v(85.05, 519.32) * mm, "end": v(76.14, 518.85) * mm});
            skLineSegment(sketch, "E2544", {"start": v(76.14, 518.85) * mm, "end": v(66.96, 518.37) * mm});
            skLineSegment(sketch, "E2545", {"start": v(66.96, 518.37) * mm, "end": v(59.74, 518.06) * mm});
            skLineSegment(sketch, "E2546", {"start": v(59.74, 518.06) * mm, "end": v(57.34, 517.99) * mm});
            skLineSegment(sketch, "E2547", {"start": v(57.34, 517.99) * mm, "end": v(56.14, 517.96) * mm});
            skLineSegment(sketch, "E2548", {"start": v(56.14, 517.96) * mm, "end": v(52.55, 517.85) * mm});
            skLineSegment(sketch, "E2549", {"start": v(52.55, 517.85) * mm, "end": v(48.2, 517.71) * mm});
            skLineSegment(sketch, "E2550", {"start": v(48.2, 517.71) * mm, "end": v(44.2, 517.57) * mm});
            skLineSegment(sketch, "E2551", {"start": v(44.2, 517.57) * mm, "end": v(40.49, 517.41) * mm});
            skLineSegment(sketch, "E2552", {"start": v(40.49, 517.41) * mm, "end": v(36.97, 517.22) * mm});
            skLineSegment(sketch, "E2553", {"start": v(36.97, 517.22) * mm, "end": v(33.58, 517) * mm});
            skLineSegment(sketch, "E2554", {"start": v(33.58, 517) * mm, "end": v(30.24, 516.74) * mm});
            skLineSegment(sketch, "E2555", {"start": v(30.24, 516.74) * mm, "end": v(26.86, 516.42) * mm});
            skLineSegment(sketch, "E2556", {"start": v(26.86, 516.42) * mm, "end": v(23.37, 516.04) * mm});
            skLineSegment(sketch, "E2557", {"start": v(23.37, 516.04) * mm, "end": v(19.7, 515.59) * mm});
            skLineSegment(sketch, "E2558", {"start": v(19.7, 515.59) * mm, "end": v(15.75, 515.05) * mm});
            skLineSegment(sketch, "E2559", {"start": v(15.75, 515.05) * mm, "end": v(11.46, 514.42) * mm});
            skLineSegment(sketch, "E2560", {"start": v(11.46, 514.42) * mm, "end": v(6.75, 513.7) * mm});
            skLineSegment(sketch, "E2561", {"start": v(6.75, 513.7) * mm, "end": v(1.54, 512.86) * mm});
            skLineSegment(sketch, "E2562", {"start": v(1.54, 512.86) * mm, "end": v(-4.25, 511.9) * mm});
            skLineSegment(sketch, "E2563", {"start": v(-4.25, 511.9) * mm, "end": v(-9.1, 511.09) * mm});
            skLineSegment(sketch, "E2564", {"start": v(-9.1, 511.09) * mm, "end": v(-10.7, 510.81) * mm});
            skLineSegment(sketch, "E2565", {"start": v(-10.7, 510.81) * mm, "end": v(-12.71, 510.47) * mm});
            skLineSegment(sketch, "E2566", {"start": v(-12.71, 510.47) * mm, "end": v(-18.74, 509.4) * mm});
            skLineSegment(sketch, "E2567", {"start": v(-18.74, 509.4) * mm, "end": v(-27.19, 507.82) * mm});
            skLineSegment(sketch, "E2568", {"start": v(-27.19, 507.82) * mm, "end": v(-36.04, 506.13) * mm});
            skLineSegment(sketch, "E2569", {"start": v(-36.04, 506.13) * mm, "end": v(-45.32, 504.33) * mm});
            skLineSegment(sketch, "E2570", {"start": v(-45.32, 504.33) * mm, "end": v(-55.03, 502.45) * mm});
            skLineSegment(sketch, "E2571", {"start": v(-55.03, 502.45) * mm, "end": v(-65.17, 500.54) * mm});
            skLineSegment(sketch, "E2572", {"start": v(-65.17, 500.54) * mm, "end": v(-75.77, 498.61) * mm});
            skLineSegment(sketch, "E2573", {"start": v(-75.77, 498.61) * mm, "end": v(-86.82, 496.7) * mm});
            skLineSegment(sketch, "E2574", {"start": v(-86.82, 496.7) * mm, "end": v(-98.33, 494.82) * mm});
            skLineSegment(sketch, "E2575", {"start": v(-98.33, 494.82) * mm, "end": v(-110.31, 493.02) * mm});
            skLineSegment(sketch, "E2576", {"start": v(-110.31, 493.02) * mm, "end": v(-122.78, 491.31) * mm});
            skLineSegment(sketch, "E2577", {"start": v(-122.78, 491.31) * mm, "end": v(-135.73, 489.73) * mm});
            skLineSegment(sketch, "E2578", {"start": v(-135.73, 489.73) * mm, "end": v(-149.18, 488.3) * mm});
            skLineSegment(sketch, "E2579", {"start": v(-149.18, 488.3) * mm, "end": v(-163.14, 487.06) * mm});
            skLineSegment(sketch, "E2580", {"start": v(-163.14, 487.06) * mm, "end": v(-177.61, 486.02) * mm});
            skLineSegment(sketch, "E2581", {"start": v(-177.61, 486.02) * mm, "end": v(-188.86, 485.39) * mm});
            skLineSegment(sketch, "E2582", {"start": v(-188.86, 485.39) * mm, "end": v(-192.6, 485.22) * mm});
            skLineSegment(sketch, "E2583", {"start": v(-192.6, 485.22) * mm, "end": v(-194.88, 485.12) * mm});
            skLineSegment(sketch, "E2584", {"start": v(-194.88, 485.12) * mm, "end": v(-201.69, 484.8) * mm});
            skLineSegment(sketch, "E2585", {"start": v(-201.69, 484.8) * mm, "end": v(-210.3, 484.4) * mm});
            skLineSegment(sketch, "E2586", {"start": v(-210.3, 484.4) * mm, "end": v(-218.52, 484.01) * mm});
            skLineSegment(sketch, "E2587", {"start": v(-218.52, 484.01) * mm, "end": v(-226.43, 483.7) * mm});
            skLineSegment(sketch, "E2588", {"start": v(-226.43, 483.7) * mm, "end": v(-234.1, 483.46) * mm});
            skLineSegment(sketch, "E2589", {"start": v(-234.1, 483.46) * mm, "end": v(-241.59, 483.34) * mm});
            skLineSegment(sketch, "E2590", {"start": v(-241.59, 483.34) * mm, "end": v(-249, 483.37) * mm});
            skLineSegment(sketch, "E2591", {"start": v(-249, 483.37) * mm, "end": v(-256.39, 483.56) * mm});
            skLineSegment(sketch, "E2592", {"start": v(-256.39, 483.56) * mm, "end": v(-263.84, 483.96) * mm});
            skLineSegment(sketch, "E2593", {"start": v(-263.84, 483.96) * mm, "end": v(-271.44, 484.58) * mm});
            skLineSegment(sketch, "E2594", {"start": v(-271.44, 484.58) * mm, "end": v(-279.25, 485.45) * mm});
            skLineSegment(sketch, "E2595", {"start": v(-279.25, 485.45) * mm, "end": v(-287.36, 486.6) * mm});
            skLineSegment(sketch, "E2596", {"start": v(-287.36, 486.6) * mm, "end": v(-295.83, 488.07) * mm});
            skLineSegment(sketch, "E2597", {"start": v(-295.83, 488.07) * mm, "end": v(-304.75, 489.87) * mm});
            skLineSegment(sketch, "E2598", {"start": v(-304.75, 489.87) * mm, "end": v(-314.19, 492.04) * mm});
            skLineSegment(sketch, "E2599", {"start": v(-314.19, 492.04) * mm, "end": v(-321.72, 493.93) * mm});
            skLineSegment(sketch, "E2600", {"start": v(-321.72, 493.93) * mm, "end": v(-324.22, 494.6) * mm});
            skLineSegment(sketch, "E2601", {"start": v(-324.22, 494.6) * mm, "end": v(-325.24, 494.86) * mm});
            skLineSegment(sketch, "E2602", {"start": v(-325.24, 494.86) * mm, "end": v(-328.3, 495.69) * mm});
            skLineSegment(sketch, "E2603", {"start": v(-328.3, 495.69) * mm, "end": v(-331.66, 496.58) * mm});
            skLineSegment(sketch, "E2604", {"start": v(-331.66, 496.58) * mm, "end": v(-334.38, 497.32) * mm});
            skLineSegment(sketch, "E2605", {"start": v(-334.38, 497.32) * mm, "end": v(-336.54, 497.9) * mm});
            skLineSegment(sketch, "E2606", {"start": v(-336.54, 497.9) * mm, "end": v(-338.2, 498.35) * mm});
            skLineSegment(sketch, "E2607", {"start": v(-338.2, 498.35) * mm, "end": v(-339.47, 498.69) * mm});
            skLineSegment(sketch, "E2608", {"start": v(-339.47, 498.69) * mm, "end": v(-340.4, 498.93) * mm});
            skLineSegment(sketch, "E2609", {"start": v(-340.4, 498.93) * mm, "end": v(-341.09, 499.1) * mm});
            skLineSegment(sketch, "E2610", {"start": v(-341.09, 499.1) * mm, "end": v(-341.6, 499.22) * mm});
            skLineSegment(sketch, "E2611", {"start": v(-341.6, 499.22) * mm, "end": v(-342, 499.3) * mm});
            skLineSegment(sketch, "E2612", {"start": v(-342, 499.3) * mm, "end": v(-342.4, 499.36) * mm});
            skLineSegment(sketch, "E2613", {"start": v(-342.4, 499.36) * mm, "end": v(-342.86, 499.41) * mm});
            skLineSegment(sketch, "E2614", {"start": v(-342.86, 499.41) * mm, "end": v(-343.45, 499.5) * mm});
            skLineSegment(sketch, "E2615", {"start": v(-343.45, 499.5) * mm, "end": v(-344.26, 499.62) * mm});
            skLineSegment(sketch, "E2616", {"start": v(-344.26, 499.62) * mm, "end": v(-345.36, 499.8) * mm});
            skLineSegment(sketch, "E2617", {"start": v(-345.36, 499.8) * mm, "end": v(-346.47, 499.98) * mm});
            skLineSegment(sketch, "E2618", {"start": v(-346.47, 499.98) * mm, "end": v(-346.84, 500.04) * mm});
            skLineSegment(sketch, "E2619", {"start": v(-346.84, 500.04) * mm, "end": v(-347.88, 500.23) * mm});
            skLineSegment(sketch, "E2620", {"start": v(-347.88, 500.23) * mm, "end": v(-351.07, 500.41) * mm});
            skLineSegment(sketch, "E2621", {"start": v(-351.07, 500.41) * mm, "end": v(-356.74, 500.38) * mm});
            skLineSegment(sketch, "E2622", {"start": v(-356.74, 500.38) * mm, "end": v(-363.45, 500.1) * mm});
            skLineSegment(sketch, "E2623", {"start": v(-363.45, 500.1) * mm, "end": v(-370.82, 499.66) * mm});
            skLineSegment(sketch, "E2624", {"start": v(-370.82, 499.66) * mm, "end": v(-378.43, 499.2) * mm});
            skLineSegment(sketch, "E2625", {"start": v(-378.43, 499.2) * mm, "end": v(-385.89, 498.85) * mm});
            skLineSegment(sketch, "E2626", {"start": v(-385.89, 498.85) * mm, "end": v(-392.8, 498.7) * mm});
            skLineSegment(sketch, "E2627", {"start": v(-392.8, 498.7) * mm, "end": v(-397.28, 498.78) * mm});
            skLineSegment(sketch, "E2628", {"start": v(-397.28, 498.78) * mm, "end": v(-398.76, 498.89) * mm});
            skLineSegment(sketch, "E2629", {"start": v(-398.76, 498.89) * mm, "end": v(-399.06, 498.9) * mm});
            skLineSegment(sketch, "E2630", {"start": v(-399.06, 498.9) * mm, "end": v(-399.94, 498.98) * mm});
            skLineSegment(sketch, "E2631", {"start": v(-399.94, 498.98) * mm, "end": v(-401.1, 499.06) * mm});
            skLineSegment(sketch, "E2632", {"start": v(-401.1, 499.06) * mm, "end": v(-402.24, 499.15) * mm});
            skLineSegment(sketch, "E2633", {"start": v(-402.24, 499.15) * mm, "end": v(-403.42, 499.25) * mm});
            skLineSegment(sketch, "E2634", {"start": v(-403.42, 499.25) * mm, "end": v(-404.68, 499.38) * mm});
            skLineSegment(sketch, "E2635", {"start": v(-404.68, 499.38) * mm, "end": v(-406.03, 499.52) * mm});
            skLineSegment(sketch, "E2636", {"start": v(-406.03, 499.52) * mm, "end": v(-407.52, 499.7) * mm});
            skLineSegment(sketch, "E2637", {"start": v(-407.52, 499.7) * mm, "end": v(-409.17, 499.92) * mm});
            skLineSegment(sketch, "E2638", {"start": v(-409.17, 499.92) * mm, "end": v(-411.02, 500.18) * mm});
            skLineSegment(sketch, "E2639", {"start": v(-411.02, 500.18) * mm, "end": v(-413.1, 500.5) * mm});
            skLineSegment(sketch, "E2640", {"start": v(-413.1, 500.5) * mm, "end": v(-415.45, 500.87) * mm});
            skLineSegment(sketch, "E2641", {"start": v(-415.45, 500.87) * mm, "end": v(-418.1, 501.3) * mm});
            skLineSegment(sketch, "E2642", {"start": v(-418.1, 501.3) * mm, "end": v(-421.06, 501.8) * mm});
            skLineSegment(sketch, "E2643", {"start": v(-421.06, 501.8) * mm, "end": v(-424.4, 502.4) * mm});
            skLineSegment(sketch, "E2644", {"start": v(-424.4, 502.4) * mm, "end": v(-428.13, 503.06) * mm});
            skLineSegment(sketch, "E2645", {"start": v(-428.13, 503.06) * mm, "end": v(-432.29, 503.82) * mm});
            skLineSegment(sketch, "E2646", {"start": v(-432.29, 503.82) * mm, "end": v(-436.9, 504.67) * mm});
            skLineSegment(sketch, "E2647", {"start": v(-436.9, 504.67) * mm, "end": v(-442.02, 505.63) * mm});
            skLineSegment(sketch, "E2648", {"start": v(-442.02, 505.63) * mm, "end": v(-447.65, 506.7) * mm});
            skLineSegment(sketch, "E2649", {"start": v(-447.65, 506.7) * mm, "end": v(-453.85, 507.88) * mm});
            skLineSegment(sketch, "E2650", {"start": v(-453.85, 507.88) * mm, "end": v(-460.64, 509.19) * mm});
            skLineSegment(sketch, "E2651", {"start": v(-460.64, 509.19) * mm, "end": v(-468.04, 510.63) * mm});
            skLineSegment(sketch, "E2652", {"start": v(-468.04, 510.63) * mm, "end": v(-476.11, 512.2) * mm});
            skLineSegment(sketch, "E2653", {"start": v(-476.11, 512.2) * mm, "end": v(-484.87, 513.92) * mm});
            skLineSegment(sketch, "E2654", {"start": v(-484.87, 513.92) * mm, "end": v(-494.34, 515.79) * mm});
            skLineSegment(sketch, "E2655", {"start": v(-494.34, 515.79) * mm, "end": v(-504.58, 517.8) * mm});
            skLineSegment(sketch, "E2656", {"start": v(-504.58, 517.8) * mm, "end": v(-515.6, 520) * mm});
            skLineSegment(sketch, "E2657", {"start": v(-515.6, 520) * mm, "end": v(-527.44, 522.35) * mm});
            skLineSegment(sketch, "E2658", {"start": v(-527.44, 522.35) * mm, "end": v(-540.13, 524.87) * mm});
            skLineSegment(sketch, "E2659", {"start": v(-540.13, 524.87) * mm, "end": v(-553.7, 527.58) * mm});
            skLineSegment(sketch, "E2660", {"start": v(-553.7, 527.58) * mm, "end": v(-568.2, 530.48) * mm});
            skLineSegment(sketch, "E2661", {"start": v(-568.2, 530.48) * mm, "end": v(-579.79, 532.8) * mm});
            skLineSegment(sketch, "E2662", {"start": v(-579.79, 532.8) * mm, "end": v(-583.65, 533.58) * mm});
            skLineSegment(sketch, "E2663", {"start": v(608.7, 215.06) * mm, "end": v(607.77, 214.94) * mm});
            skLineSegment(sketch, "E2664", {"start": v(607.77, 214.94) * mm, "end": v(604.98, 214.35) * mm});
            skLineSegment(sketch, "E2665", {"start": v(604.98, 214.35) * mm, "end": v(601.42, 213.27) * mm});
            skLineSegment(sketch, "E2666", {"start": v(601.42, 213.27) * mm, "end": v(597.94, 211.9) * mm});
            skLineSegment(sketch, "E2667", {"start": v(597.94, 211.9) * mm, "end": v(594.47, 210.3) * mm});
            skLineSegment(sketch, "E2668", {"start": v(594.47, 210.3) * mm, "end": v(590.95, 208.56) * mm});
            skLineSegment(sketch, "E2669", {"start": v(590.95, 208.56) * mm, "end": v(587.28, 206.73) * mm});
            skLineSegment(sketch, "E2670", {"start": v(587.28, 206.73) * mm, "end": v(583.4, 204.88) * mm});
            skLineSegment(sketch, "E2671", {"start": v(583.4, 204.88) * mm, "end": v(579.26, 203.1) * mm});
            skLineSegment(sketch, "E2672", {"start": v(579.26, 203.1) * mm, "end": v(574.75, 201.43) * mm});
            skLineSegment(sketch, "E2673", {"start": v(574.75, 201.43) * mm, "end": v(569.81, 199.97) * mm});
            skLineSegment(sketch, "E2674", {"start": v(569.81, 199.97) * mm, "end": v(564.38, 198.76) * mm});
            skLineSegment(sketch, "E2675", {"start": v(564.38, 198.76) * mm, "end": v(558.37, 197.89) * mm});
            skLineSegment(sketch, "E2676", {"start": v(558.37, 197.89) * mm, "end": v(551.71, 197.42) * mm});
            skLineSegment(sketch, "E2677", {"start": v(551.71, 197.42) * mm, "end": v(544.33, 197.42) * mm});
            skLineSegment(sketch, "E2678", {"start": v(544.33, 197.42) * mm, "end": v(536.16, 197.96) * mm});
            skLineSegment(sketch, "E2679", {"start": v(536.16, 197.96) * mm, "end": v(529.37, 198.76) * mm});
            skLineSegment(sketch, "E2680", {"start": v(529.37, 198.76) * mm, "end": v(527.12, 199.11) * mm});
            skLineSegment(sketch, "E2681", {"start": v(527.12, 199.11) * mm, "end": v(523.53, 199.67) * mm});
            skLineSegment(sketch, "E2682", {"start": v(523.53, 199.67) * mm, "end": v(512.83, 201.75) * mm});
            skLineSegment(sketch, "E2683", {"start": v(512.83, 201.75) * mm, "end": v(498.8, 205.15) * mm});
            skLineSegment(sketch, "E2684", {"start": v(498.8, 205.15) * mm, "end": v(485.03, 209.3) * mm});
            skLineSegment(sketch, "E2685", {"start": v(485.03, 209.3) * mm, "end": v(471.51, 214.19) * mm});
            skLineSegment(sketch, "E2686", {"start": v(471.51, 214.19) * mm, "end": v(458.23, 219.8) * mm});
            skLineSegment(sketch, "E2687", {"start": v(458.23, 219.8) * mm, "end": v(445.17, 226.13) * mm});
            skLineSegment(sketch, "E2688", {"start": v(445.17, 226.13) * mm, "end": v(432.35, 233.15) * mm});
            skLineSegment(sketch, "E2689", {"start": v(432.35, 233.15) * mm, "end": v(419.73, 240.86) * mm});
            skLineSegment(sketch, "E2690", {"start": v(419.73, 240.86) * mm, "end": v(407.33, 249.24) * mm});
            skLineSegment(sketch, "E2691", {"start": v(407.33, 249.24) * mm, "end": v(395.13, 258.28) * mm});
            skLineSegment(sketch, "E2692", {"start": v(395.13, 258.28) * mm, "end": v(383.12, 267.96) * mm});
            skLineSegment(sketch, "E2693", {"start": v(383.12, 267.96) * mm, "end": v(371.3, 278.27) * mm});
            skLineSegment(sketch, "E2694", {"start": v(371.3, 278.27) * mm, "end": v(359.65, 289.2) * mm});
            skLineSegment(sketch, "E2695", {"start": v(359.65, 289.2) * mm, "end": v(348.17, 300.75) * mm});
            skLineSegment(sketch, "E2696", {"start": v(348.17, 300.75) * mm, "end": v(336.86, 312.88) * mm});
            skLineSegment(sketch, "E2697", {"start": v(336.86, 312.88) * mm, "end": v(328.44, 322.37) * mm});
            skLineSegment(sketch, "E2698", {"start": v(328.44, 322.37) * mm, "end": v(325.7, 325.58) * mm});
            skLineSegment(sketch, "E2699", {"start": v(325.7, 325.58) * mm, "end": v(322.88, 328.89) * mm});
            skLineSegment(sketch, "E2700", {"start": v(322.88, 328.89) * mm, "end": v(314.06, 338.5) * mm});
            skLineSegment(sketch, "E2701", {"start": v(314.06, 338.5) * mm, "end": v(301.4, 351.24) * mm});
            skLineSegment(sketch, "E2702", {"start": v(301.4, 351.24) * mm, "end": v(287.84, 363.72) * mm});
            skLineSegment(sketch, "E2703", {"start": v(287.84, 363.72) * mm, "end": v(273.49, 375.84) * mm});
            skLineSegment(sketch, "E2704", {"start": v(273.49, 375.84) * mm, "end": v(258.46, 387.54) * mm});
            skLineSegment(sketch, "E2705", {"start": v(258.46, 387.54) * mm, "end": v(242.88, 398.73) * mm});
            skLineSegment(sketch, "E2706", {"start": v(242.88, 398.73) * mm, "end": v(226.86, 409.35) * mm});
            skLineSegment(sketch, "E2707", {"start": v(226.86, 409.35) * mm, "end": v(210.52, 419.3) * mm});
            skLineSegment(sketch, "E2708", {"start": v(210.52, 419.3) * mm, "end": v(193.97, 428.5) * mm});
            skLineSegment(sketch, "E2709", {"start": v(193.97, 428.5) * mm, "end": v(177.34, 436.89) * mm});
            skLineSegment(sketch, "E2710", {"start": v(177.34, 436.89) * mm, "end": v(160.74, 444.37) * mm});
            skLineSegment(sketch, "E2711", {"start": v(160.74, 444.37) * mm, "end": v(144.28, 450.88) * mm});
            skLineSegment(sketch, "E2712", {"start": v(144.28, 450.88) * mm, "end": v(128.09, 456.32) * mm});
            skLineSegment(sketch, "E2713", {"start": v(128.09, 456.32) * mm, "end": v(112.27, 460.63) * mm});
            skLineSegment(sketch, "E2714", {"start": v(112.27, 460.63) * mm, "end": v(96.96, 463.72) * mm});
            skLineSegment(sketch, "E2715", {"start": v(96.96, 463.72) * mm, "end": v(85.94, 465.22) * mm});
            skLineSegment(sketch, "E2716", {"start": v(85.94, 465.22) * mm, "end": v(82.26, 465.5) * mm});
            skLineSegment(sketch, "E2717", {"start": v(82.26, 465.5) * mm, "end": v(78.66, 465.79) * mm});
            skLineSegment(sketch, "E2718", {"start": v(78.66, 465.79) * mm, "end": v(67.84, 466.1) * mm});
            skLineSegment(sketch, "E2719", {"start": v(67.84, 466.1) * mm, "end": v(53.32, 465.76) * mm});
            skLineSegment(sketch, "E2720", {"start": v(53.32, 465.76) * mm, "end": v(38.71, 464.57) * mm});
            skLineSegment(sketch, "E2721", {"start": v(38.71, 464.57) * mm, "end": v(24.05, 462.67) * mm});
            skLineSegment(sketch, "E2722", {"start": v(24.05, 462.67) * mm, "end": v(9.34, 460.18) * mm});
            skLineSegment(sketch, "E2723", {"start": v(9.34, 460.18) * mm, "end": v(-5.4, 457.22) * mm});
            skLineSegment(sketch, "E2724", {"start": v(-5.4, 457.22) * mm, "end": v(-20.13, 453.9) * mm});
            skLineSegment(sketch, "E2725", {"start": v(-20.13, 453.9) * mm, "end": v(-34.84, 450.36) * mm});
            skLineSegment(sketch, "E2726", {"start": v(-34.84, 450.36) * mm, "end": v(-49.52, 446.7) * mm});
            skLineSegment(sketch, "E2727", {"start": v(-49.52, 446.7) * mm, "end": v(-64.13, 443.04) * mm});
            skLineSegment(sketch, "E2728", {"start": v(-64.13, 443.04) * mm, "end": v(-78.67, 439.5) * mm});
            skLineSegment(sketch, "E2729", {"start": v(-78.67, 439.5) * mm, "end": v(-93.1, 436.21) * mm});
            skLineSegment(sketch, "E2730", {"start": v(-93.1, 436.21) * mm, "end": v(-107.4, 433.3) * mm});
            skLineSegment(sketch, "E2731", {"start": v(-107.4, 433.3) * mm, "end": v(-121.57, 430.85) * mm});
            skLineSegment(sketch, "E2732", {"start": v(-121.57, 430.85) * mm, "end": v(-135.57, 429.02) * mm});
            skLineSegment(sketch, "E2733", {"start": v(-135.57, 429.02) * mm, "end": v(-145.93, 428.1) * mm});
            skLineSegment(sketch, "E2734", {"start": v(-145.93, 428.1) * mm, "end": v(-149.38, 427.91) * mm});
            skLineSegment(sketch, "E2735", {"start": v(-149.38, 427.91) * mm, "end": v(-152.7, 427.74) * mm});
            skLineSegment(sketch, "E2736", {"start": v(-152.7, 427.74) * mm, "end": v(-162.6, 427.14) * mm});
            skLineSegment(sketch, "E2737", {"start": v(-162.6, 427.14) * mm, "end": v(-174.87, 426.26) * mm});
            skLineSegment(sketch, "E2738", {"start": v(-174.87, 426.26) * mm, "end": v(-186.3, 425.32) * mm});
            skLineSegment(sketch, "E2739", {"start": v(-186.3, 425.32) * mm, "end": v(-196.98, 424.37) * mm});
            skLineSegment(sketch, "E2740", {"start": v(-196.98, 424.37) * mm, "end": v(-207.01, 423.45) * mm});
            skLineSegment(sketch, "E2741", {"start": v(-207.01, 423.45) * mm, "end": v(-216.5, 422.61) * mm});
            skLineSegment(sketch, "E2742", {"start": v(-216.5, 422.61) * mm, "end": v(-225.54, 421.9) * mm});
            skLineSegment(sketch, "E2743", {"start": v(-225.54, 421.9) * mm, "end": v(-234.23, 421.35) * mm});
            skLineSegment(sketch, "E2744", {"start": v(-234.23, 421.35) * mm, "end": v(-242.67, 421.02) * mm});
            skLineSegment(sketch, "E2745", {"start": v(-242.67, 421.02) * mm, "end": v(-250.95, 420.95) * mm});
            skLineSegment(sketch, "E2746", {"start": v(-250.95, 420.95) * mm, "end": v(-259.18, 421.2) * mm});
            skLineSegment(sketch, "E2747", {"start": v(-259.18, 421.2) * mm, "end": v(-267.46, 421.78) * mm});
            skLineSegment(sketch, "E2748", {"start": v(-267.46, 421.78) * mm, "end": v(-275.88, 422.77) * mm});
            skLineSegment(sketch, "E2749", {"start": v(-275.88, 422.77) * mm, "end": v(-284.54, 424.21) * mm});
            skLineSegment(sketch, "E2750", {"start": v(-284.54, 424.21) * mm, "end": v(-293.55, 426.14) * mm});
            skLineSegment(sketch, "E2751", {"start": v(-293.55, 426.14) * mm, "end": v(-300.65, 427.93) * mm});
            skLineSegment(sketch, "E2752", {"start": v(-300.65, 427.93) * mm, "end": v(-303, 428.6) * mm});
            skLineSegment(sketch, "E2753", {"start": v(-303, 428.6) * mm, "end": v(-304.25, 428.95) * mm});
            skLineSegment(sketch, "E2754", {"start": v(-304.25, 428.95) * mm, "end": v(-307.97, 430.15) * mm});
            skLineSegment(sketch, "E2755", {"start": v(-307.97, 430.15) * mm, "end": v(-313.06, 431.92) * mm});
            skLineSegment(sketch, "E2756", {"start": v(-313.06, 431.92) * mm, "end": v(-318.32, 433.82) * mm});
            skLineSegment(sketch, "E2757", {"start": v(-318.32, 433.82) * mm, "end": v(-323.86, 435.72) * mm});
            skLineSegment(sketch, "E2758", {"start": v(-323.86, 435.72) * mm, "end": v(-329.76, 437.53) * mm});
            skLineSegment(sketch, "E2759", {"start": v(-329.76, 437.53) * mm, "end": v(-336.1, 439.14) * mm});
            skLineSegment(sketch, "E2760", {"start": v(-336.1, 439.14) * mm, "end": v(-342.97, 440.44) * mm});
            skLineSegment(sketch, "E2761", {"start": v(-342.97, 440.44) * mm, "end": v(-348.57, 441.17) * mm});
            skLineSegment(sketch, "E2762", {"start": v(-348.57, 441.17) * mm, "end": v(-350.44, 441.33) * mm});
            skLineSegment(sketch, "E2763", {"start": v(-350.44, 441.33) * mm, "end": v(-352.7, 441.52) * mm});
            skLineSegment(sketch, "E2764", {"start": v(-352.7, 441.52) * mm, "end": v(-359.5, 441.8) * mm});
            skLineSegment(sketch, "E2765", {"start": v(-359.5, 441.8) * mm, "end": v(-367.48, 441.71) * mm});
            skLineSegment(sketch, "E2766", {"start": v(-367.48, 441.71) * mm, "end": v(-374.72, 441.3) * mm});
            skLineSegment(sketch, "E2767", {"start": v(-374.72, 441.3) * mm, "end": v(-381.56, 440.74) * mm});
            skLineSegment(sketch, "E2768", {"start": v(-381.56, 440.74) * mm, "end": v(-388.35, 440.26) * mm});
            skLineSegment(sketch, "E2769", {"start": v(-388.35, 440.26) * mm, "end": v(-395.42, 440.06) * mm});
            skLineSegment(sketch, "E2770", {"start": v(-395.42, 440.06) * mm, "end": v(-403.12, 440.35) * mm});
            skLineSegment(sketch, "E2771", {"start": v(-403.12, 440.35) * mm, "end": v(-409.62, 441) * mm});
            skLineSegment(sketch, "E2772", {"start": v(-409.62, 441) * mm, "end": v(-411.78, 441.33) * mm});
            skLineSegment(sketch, "E2773", {"start": v(-411.78, 441.33) * mm, "end": v(-412.53, 441.44) * mm});
            skLineSegment(sketch, "E2774", {"start": v(-412.53, 441.44) * mm, "end": v(-414.78, 441.8) * mm});
            skLineSegment(sketch, "E2775", {"start": v(-414.78, 441.8) * mm, "end": v(-418.33, 442.36) * mm});
            skLineSegment(sketch, "E2776", {"start": v(-418.33, 442.36) * mm, "end": v(-422.39, 443.01) * mm});
            skLineSegment(sketch, "E2777", {"start": v(-422.39, 443.01) * mm, "end": v(-426.91, 443.76) * mm});
            skLineSegment(sketch, "E2778", {"start": v(-426.91, 443.76) * mm, "end": v(-431.86, 444.58) * mm});
            skLineSegment(sketch, "E2779", {"start": v(-431.86, 444.58) * mm, "end": v(-437.18, 445.48) * mm});
            skLineSegment(sketch, "E2780", {"start": v(-437.18, 445.48) * mm, "end": v(-442.85, 446.43) * mm});
            skLineSegment(sketch, "E2781", {"start": v(-442.85, 446.43) * mm, "end": v(-448.81, 447.44) * mm});
            skLineSegment(sketch, "E2782", {"start": v(-448.81, 447.44) * mm, "end": v(-455.03, 448.5) * mm});
            skLineSegment(sketch, "E2783", {"start": v(-455.03, 448.5) * mm, "end": v(-461.45, 449.6) * mm});
            skLineSegment(sketch, "E2784", {"start": v(-461.45, 449.6) * mm, "end": v(-468.05, 450.74) * mm});
            skLineSegment(sketch, "E2785", {"start": v(-468.05, 450.74) * mm, "end": v(-474.77, 451.9) * mm});
            skLineSegment(sketch, "E2786", {"start": v(-474.77, 451.9) * mm, "end": v(-481.58, 453.07) * mm});
            skLineSegment(sketch, "E2787", {"start": v(-481.58, 453.07) * mm, "end": v(-488.43, 454.26) * mm});
            skLineSegment(sketch, "E2788", {"start": v(-488.43, 454.26) * mm, "end": v(-495.28, 455.45) * mm});
            skLineSegment(sketch, "E2789", {"start": v(-495.28, 455.45) * mm, "end": v(-502.08, 456.63) * mm});
            skLineSegment(sketch, "E2790", {"start": v(-502.08, 456.63) * mm, "end": v(-508.8, 457.8) * mm});
            skLineSegment(sketch, "E2791", {"start": v(-508.8, 457.8) * mm, "end": v(-515.4, 458.95) * mm});
            skLineSegment(sketch, "E2792", {"start": v(-515.4, 458.95) * mm, "end": v(-521.83, 460.08) * mm});
            skLineSegment(sketch, "E2793", {"start": v(-521.83, 460.08) * mm, "end": v(-528.04, 461.16) * mm});
            skLineSegment(sketch, "E2794", {"start": v(-528.04, 461.16) * mm, "end": v(-534, 462.2) * mm});
            skLineSegment(sketch, "E2795", {"start": v(-534, 462.2) * mm, "end": v(-539.66, 463.2) * mm});
            skLineSegment(sketch, "E2796", {"start": v(-539.66, 463.2) * mm, "end": v(-544.99, 464.14) * mm});
            skLineSegment(sketch, "E2797", {"start": v(-544.99, 464.14) * mm, "end": v(-549.93, 465) * mm});
            skLineSegment(sketch, "E2798", {"start": v(-549.93, 465) * mm, "end": v(-554.45, 465.8) * mm});
            skLineSegment(sketch, "E2799", {"start": v(-554.45, 465.8) * mm, "end": v(-558.5, 466.51) * mm});
            skLineSegment(sketch, "E2800", {"start": v(-558.5, 466.51) * mm, "end": v(-562.06, 467.14) * mm});
            skLineSegment(sketch, "E2801", {"start": v(-562.06, 467.14) * mm, "end": v(-565.05, 467.66) * mm});
            skLineSegment(sketch, "E2802", {"start": v(-565.05, 467.66) * mm, "end": v(-567.46, 468.09) * mm});
            skLineSegment(sketch, "E2803", {"start": v(-567.46, 468.09) * mm, "end": v(-569.23, 468.4) * mm});
            skLineSegment(sketch, "E2804", {"start": v(-569.23, 468.4) * mm, "end": v(-570.32, 468.6) * mm});
            skLineSegment(sketch, "E2805", {"start": v(-570.32, 468.6) * mm, "end": v(-570.7, 468.66) * mm});
            skLineSegment(sketch, "E2806", {"start": v(608.7, 196.71) * mm, "end": v(607.77, 196.59) * mm});
            skLineSegment(sketch, "E2807", {"start": v(607.77, 196.59) * mm, "end": v(604.99, 196.03) * mm});
            skLineSegment(sketch, "E2808", {"start": v(604.99, 196.03) * mm, "end": v(601.44, 195.05) * mm});
            skLineSegment(sketch, "E2809", {"start": v(601.44, 195.05) * mm, "end": v(597.98, 193.83) * mm});
            skLineSegment(sketch, "E2810", {"start": v(597.98, 193.83) * mm, "end": v(594.53, 192.43) * mm});
            skLineSegment(sketch, "E2811", {"start": v(594.53, 192.43) * mm, "end": v(591.03, 190.89) * mm});
            skLineSegment(sketch, "E2812", {"start": v(591.03, 190.89) * mm, "end": v(587.4, 189.27) * mm});
            skLineSegment(sketch, "E2813", {"start": v(587.4, 189.27) * mm, "end": v(583.54, 187.63) * mm});
            skLineSegment(sketch, "E2814", {"start": v(583.54, 187.63) * mm, "end": v(579.41, 186.02) * mm});
            skLineSegment(sketch, "E2815", {"start": v(579.41, 186.02) * mm, "end": v(574.92, 184.5) * mm});
            skLineSegment(sketch, "E2816", {"start": v(574.92, 184.5) * mm, "end": v(570, 183.11) * mm});
            skLineSegment(sketch, "E2817", {"start": v(570, 183.11) * mm, "end": v(564.56, 181.92) * mm});
            skLineSegment(sketch, "E2818", {"start": v(564.56, 181.92) * mm, "end": v(558.54, 180.97) * mm});
            skLineSegment(sketch, "E2819", {"start": v(558.54, 180.97) * mm, "end": v(551.87, 180.33) * mm});
            skLineSegment(sketch, "E2820", {"start": v(551.87, 180.33) * mm, "end": v(544.45, 180.05) * mm});
            skLineSegment(sketch, "E2821", {"start": v(544.45, 180.05) * mm, "end": v(536.23, 180.17) * mm});
            skLineSegment(sketch, "E2822", {"start": v(536.23, 180.17) * mm, "end": v(529.4, 180.56) * mm});
            skLineSegment(sketch, "E2823", {"start": v(529.4, 180.56) * mm, "end": v(527.12, 180.76) * mm});
            skLineSegment(sketch, "E2824", {"start": v(527.12, 180.76) * mm, "end": v(522.14, 181.2) * mm});
            skLineSegment(sketch, "E2825", {"start": v(522.14, 181.2) * mm, "end": v(507.26, 183.4) * mm});
            skLineSegment(sketch, "E2826", {"start": v(507.26, 183.4) * mm, "end": v(488.3, 187.59) * mm});
            skLineSegment(sketch, "E2827", {"start": v(488.3, 187.59) * mm, "end": v(470.26, 193.16) * mm});
            skLineSegment(sketch, "E2828", {"start": v(470.26, 193.16) * mm, "end": v(453.13, 199.92) * mm});
            skLineSegment(sketch, "E2829", {"start": v(453.13, 199.92) * mm, "end": v(436.92, 207.68) * mm});
            skLineSegment(sketch, "E2830", {"start": v(436.92, 207.68) * mm, "end": v(421.63, 216.25) * mm});
            skLineSegment(sketch, "E2831", {"start": v(421.63, 216.25) * mm, "end": v(407.26, 225.44) * mm});
            skLineSegment(sketch, "E2832", {"start": v(407.26, 225.44) * mm, "end": v(393.83, 235.08) * mm});
            skLineSegment(sketch, "E2833", {"start": v(393.83, 235.08) * mm, "end": v(381.32, 244.96) * mm});
            skLineSegment(sketch, "E2834", {"start": v(381.32, 244.96) * mm, "end": v(369.76, 254.9) * mm});
            skLineSegment(sketch, "E2835", {"start": v(369.76, 254.9) * mm, "end": v(359.15, 264.71) * mm});
            skLineSegment(sketch, "E2836", {"start": v(359.15, 264.71) * mm, "end": v(349.48, 274.21) * mm});
            skLineSegment(sketch, "E2837", {"start": v(349.48, 274.21) * mm, "end": v(340.77, 283.2) * mm});
            skLineSegment(sketch, "E2838", {"start": v(340.77, 283.2) * mm, "end": v(333, 291.51) * mm});
            skLineSegment(sketch, "E2839", {"start": v(333, 291.51) * mm, "end": v(326.2, 298.93) * mm});
            skLineSegment(sketch, "E2840", {"start": v(326.2, 298.93) * mm, "end": v(321.84, 303.71) * mm});
            skLineSegment(sketch, "E2841", {"start": v(321.84, 303.71) * mm, "end": v(320.38, 305.29) * mm});
            skLineSegment(sketch, "E2842", {"start": v(320.38, 305.29) * mm, "end": v(316.12, 309.87) * mm});
            skLineSegment(sketch, "E2843", {"start": v(316.12, 309.87) * mm, "end": v(303.2, 323.46) * mm});
            skLineSegment(sketch, "E2844", {"start": v(303.2, 323.46) * mm, "end": v(286.61, 340.3) * mm});
            skLineSegment(sketch, "E2845", {"start": v(286.61, 340.3) * mm, "end": v(270.57, 355.82) * mm});
            skLineSegment(sketch, "E2846", {"start": v(270.57, 355.82) * mm, "end": v(255.02, 370.07) * mm});
            skLineSegment(sketch, "E2847", {"start": v(255.02, 370.07) * mm, "end": v(239.9, 383.07) * mm});
            skLineSegment(sketch, "E2848", {"start": v(239.9, 383.07) * mm, "end": v(225.13, 394.87) * mm});
            skLineSegment(sketch, "E2849", {"start": v(225.13, 394.87) * mm, "end": v(210.68, 405.5) * mm});
            skLineSegment(sketch, "E2850", {"start": v(210.68, 405.5) * mm, "end": v(196.5, 414.97) * mm});
            skLineSegment(sketch, "E2851", {"start": v(196.5, 414.97) * mm, "end": v(182.5, 423.34) * mm});
            skLineSegment(sketch, "E2852", {"start": v(182.5, 423.34) * mm, "end": v(168.64, 430.64) * mm});
            skLineSegment(sketch, "E2853", {"start": v(168.64, 430.64) * mm, "end": v(154.87, 436.9) * mm});
            skLineSegment(sketch, "E2854", {"start": v(154.87, 436.9) * mm, "end": v(141.11, 442.14) * mm});
            skLineSegment(sketch, "E2855", {"start": v(141.11, 442.14) * mm, "end": v(127.33, 446.4) * mm});
            skLineSegment(sketch, "E2856", {"start": v(127.33, 446.4) * mm, "end": v(113.45, 449.74) * mm});
            skLineSegment(sketch, "E2857", {"start": v(113.45, 449.74) * mm, "end": v(99.43, 452.15) * mm});
            skLineSegment(sketch, "E2858", {"start": v(99.43, 452.15) * mm, "end": v(88.76, 453.42) * mm});
            skLineSegment(sketch, "E2859", {"start": v(88.76, 453.42) * mm, "end": v(85.2, 453.7) * mm});
            skLineSegment(sketch, "E2860", {"start": v(85.2, 453.7) * mm, "end": v(81.6, 453.97) * mm});
            skLineSegment(sketch, "E2861", {"start": v(81.6, 453.97) * mm, "end": v(70.75, 454.22) * mm});
            skLineSegment(sketch, "E2862", {"start": v(70.75, 454.22) * mm, "end": v(56.13, 453.66) * mm});
            skLineSegment(sketch, "E2863", {"start": v(56.13, 453.66) * mm, "end": v(41.38, 452.15) * mm});
            skLineSegment(sketch, "E2864", {"start": v(41.38, 452.15) * mm, "end": v(26.52, 449.84) * mm});
            skLineSegment(sketch, "E2865", {"start": v(26.52, 449.84) * mm, "end": v(11.6, 446.85) * mm});
            skLineSegment(sketch, "E2866", {"start": v(11.6, 446.85) * mm, "end": v(-3.39, 443.34) * mm});
            skLineSegment(sketch, "E2867", {"start": v(-3.39, 443.34) * mm, "end": v(-18.39, 439.43) * mm});
            skLineSegment(sketch, "E2868", {"start": v(-18.39, 439.43) * mm, "end": v(-33.38, 435.27) * mm});
            skLineSegment(sketch, "E2869", {"start": v(-33.38, 435.27) * mm, "end": v(-48.32, 431) * mm});
            skLineSegment(sketch, "E2870", {"start": v(-48.32, 431) * mm, "end": v(-63.2, 426.75) * mm});
            skLineSegment(sketch, "E2871", {"start": v(-63.2, 426.75) * mm, "end": v(-77.99, 422.67) * mm});
            skLineSegment(sketch, "E2872", {"start": v(-77.99, 422.67) * mm, "end": v(-92.64, 418.89) * mm});
            skLineSegment(sketch, "E2873", {"start": v(-92.64, 418.89) * mm, "end": v(-107.14, 415.54) * mm});
            skLineSegment(sketch, "E2874", {"start": v(-107.14, 415.54) * mm, "end": v(-121.44, 412.79) * mm});
            skLineSegment(sketch, "E2875", {"start": v(-121.44, 412.79) * mm, "end": v(-135.54, 410.75) * mm});
            skLineSegment(sketch, "E2876", {"start": v(-135.54, 410.75) * mm, "end": v(-145.92, 409.74) * mm});
            skLineSegment(sketch, "E2877", {"start": v(-145.92, 409.74) * mm, "end": v(-149.38, 409.56) * mm});
            skLineSegment(sketch, "E2878", {"start": v(-149.38, 409.56) * mm, "end": v(-152.7, 409.4) * mm});
            skLineSegment(sketch, "E2879", {"start": v(-152.7, 409.4) * mm, "end": v(-162.6, 408.79) * mm});
            skLineSegment(sketch, "E2880", {"start": v(-162.6, 408.79) * mm, "end": v(-174.87, 407.91) * mm});
            skLineSegment(sketch, "E2881", {"start": v(-174.87, 407.91) * mm, "end": v(-186.3, 406.97) * mm});
            skLineSegment(sketch, "E2882", {"start": v(-186.3, 406.97) * mm, "end": v(-196.98, 406.02) * mm});
            skLineSegment(sketch, "E2883", {"start": v(-196.98, 406.02) * mm, "end": v(-207.01, 405.1) * mm});
            skLineSegment(sketch, "E2884", {"start": v(-207.01, 405.1) * mm, "end": v(-216.5, 404.26) * mm});
            skLineSegment(sketch, "E2885", {"start": v(-216.5, 404.26) * mm, "end": v(-225.54, 403.54) * mm});
            skLineSegment(sketch, "E2886", {"start": v(-225.54, 403.54) * mm, "end": v(-234.23, 403) * mm});
            skLineSegment(sketch, "E2887", {"start": v(-234.23, 403) * mm, "end": v(-242.67, 402.67) * mm});
            skLineSegment(sketch, "E2888", {"start": v(-242.67, 402.67) * mm, "end": v(-250.95, 402.6) * mm});
            skLineSegment(sketch, "E2889", {"start": v(-250.95, 402.6) * mm, "end": v(-259.18, 402.84) * mm});
            skLineSegment(sketch, "E2890", {"start": v(-259.18, 402.84) * mm, "end": v(-267.46, 403.43) * mm});
            skLineSegment(sketch, "E2891", {"start": v(-267.46, 403.43) * mm, "end": v(-275.88, 404.42) * mm});
            skLineSegment(sketch, "E2892", {"start": v(-275.88, 404.42) * mm, "end": v(-284.54, 405.86) * mm});
            skLineSegment(sketch, "E2893", {"start": v(-284.54, 405.86) * mm, "end": v(-293.55, 407.78) * mm});
            skLineSegment(sketch, "E2894", {"start": v(-293.55, 407.78) * mm, "end": v(-300.65, 409.58) * mm});
            skLineSegment(sketch, "E2895", {"start": v(-300.65, 409.58) * mm, "end": v(-303, 410.25) * mm});
            skLineSegment(sketch, "E2896", {"start": v(-303, 410.25) * mm, "end": v(-304.25, 410.6) * mm});
            skLineSegment(sketch, "E2897", {"start": v(-304.25, 410.6) * mm, "end": v(-307.97, 411.8) * mm});
            skLineSegment(sketch, "E2898", {"start": v(-307.97, 411.8) * mm, "end": v(-313.06, 413.57) * mm});
            skLineSegment(sketch, "E2899", {"start": v(-313.06, 413.57) * mm, "end": v(-318.32, 415.47) * mm});
            skLineSegment(sketch, "E2900", {"start": v(-318.32, 415.47) * mm, "end": v(-323.86, 417.36) * mm});
            skLineSegment(sketch, "E2901", {"start": v(-323.86, 417.36) * mm, "end": v(-329.76, 419.18) * mm});
            skLineSegment(sketch, "E2902", {"start": v(-329.76, 419.18) * mm, "end": v(-336.1, 420.78) * mm});
            skLineSegment(sketch, "E2903", {"start": v(-336.1, 420.78) * mm, "end": v(-342.97, 422.09) * mm});
            skLineSegment(sketch, "E2904", {"start": v(-342.97, 422.09) * mm, "end": v(-348.57, 422.82) * mm});
            skLineSegment(sketch, "E2905", {"start": v(-348.57, 422.82) * mm, "end": v(-350.44, 422.98) * mm});
            skLineSegment(sketch, "E2906", {"start": v(-350.44, 422.98) * mm, "end": v(-352.7, 423.17) * mm});
            skLineSegment(sketch, "E2907", {"start": v(-352.7, 423.17) * mm, "end": v(-359.5, 423.44) * mm});
            skLineSegment(sketch, "E2908", {"start": v(-359.5, 423.44) * mm, "end": v(-367.48, 423.36) * mm});
            skLineSegment(sketch, "E2909", {"start": v(-367.48, 423.36) * mm, "end": v(-374.72, 422.94) * mm});
            skLineSegment(sketch, "E2910", {"start": v(-374.72, 422.94) * mm, "end": v(-381.56, 422.39) * mm});
            skLineSegment(sketch, "E2911", {"start": v(-381.56, 422.39) * mm, "end": v(-388.35, 421.9) * mm});
            skLineSegment(sketch, "E2912", {"start": v(-388.35, 421.9) * mm, "end": v(-395.42, 421.7) * mm});
            skLineSegment(sketch, "E2913", {"start": v(-395.42, 421.7) * mm, "end": v(-403.12, 422) * mm});
            skLineSegment(sketch, "E2914", {"start": v(-403.12, 422) * mm, "end": v(-409.62, 422.65) * mm});
            skLineSegment(sketch, "E2915", {"start": v(-409.62, 422.65) * mm, "end": v(-411.78, 422.98) * mm});
            skLineSegment(sketch, "E2916", {"start": v(-411.78, 422.98) * mm, "end": v(-412.53, 423.1) * mm});
            skLineSegment(sketch, "E2917", {"start": v(-412.53, 423.1) * mm, "end": v(-414.77, 423.43) * mm});
            skLineSegment(sketch, "E2918", {"start": v(-414.77, 423.43) * mm, "end": v(-418.3, 423.98) * mm});
            skLineSegment(sketch, "E2919", {"start": v(-418.3, 423.98) * mm, "end": v(-422.32, 424.6) * mm});
            skLineSegment(sketch, "E2920", {"start": v(-422.32, 424.6) * mm, "end": v(-426.8, 425.3) * mm});
            skLineSegment(sketch, "E2921", {"start": v(-426.8, 425.3) * mm, "end": v(-431.68, 426.06) * mm});
            skLineSegment(sketch, "E2922", {"start": v(-431.68, 426.06) * mm, "end": v(-436.94, 426.89) * mm});
            skLineSegment(sketch, "E2923", {"start": v(-436.94, 426.89) * mm, "end": v(-442.52, 427.77) * mm});
            skLineSegment(sketch, "E2924", {"start": v(-442.52, 427.77) * mm, "end": v(-448.4, 428.7) * mm});
            skLineSegment(sketch, "E2925", {"start": v(-448.4, 428.7) * mm, "end": v(-454.51, 429.66) * mm});
            skLineSegment(sketch, "E2926", {"start": v(-454.51, 429.66) * mm, "end": v(-460.83, 430.66) * mm});
            skLineSegment(sketch, "E2927", {"start": v(-460.83, 430.66) * mm, "end": v(-467.32, 431.7) * mm});
            skLineSegment(sketch, "E2928", {"start": v(-467.32, 431.7) * mm, "end": v(-473.93, 432.74) * mm});
            skLineSegment(sketch, "E2929", {"start": v(-473.93, 432.74) * mm, "end": v(-480.62, 433.8) * mm});
            skLineSegment(sketch, "E2930", {"start": v(-480.62, 433.8) * mm, "end": v(-487.34, 434.87) * mm});
            skLineSegment(sketch, "E2931", {"start": v(-487.34, 434.87) * mm, "end": v(-494.07, 435.95) * mm});
            skLineSegment(sketch, "E2932", {"start": v(-494.07, 435.95) * mm, "end": v(-500.75, 437) * mm});
            skLineSegment(sketch, "E2933", {"start": v(-500.75, 437) * mm, "end": v(-507.35, 438.06) * mm});
            skLineSegment(sketch, "E2934", {"start": v(-507.35, 438.06) * mm, "end": v(-513.82, 439.1) * mm});
            skLineSegment(sketch, "E2935", {"start": v(-513.82, 439.1) * mm, "end": v(-520.12, 440.1) * mm});
            skLineSegment(sketch, "E2936", {"start": v(-520.12, 440.1) * mm, "end": v(-526.22, 441.07) * mm});
            skLineSegment(sketch, "E2937", {"start": v(-526.22, 441.07) * mm, "end": v(-532.06, 442) * mm});
            skLineSegment(sketch, "E2938", {"start": v(-532.06, 442) * mm, "end": v(-537.62, 442.9) * mm});
            skLineSegment(sketch, "E2939", {"start": v(-537.62, 442.9) * mm, "end": v(-542.84, 443.73) * mm});
            skLineSegment(sketch, "E2940", {"start": v(-542.84, 443.73) * mm, "end": v(-547.68, 444.5) * mm});
            skLineSegment(sketch, "E2941", {"start": v(-547.68, 444.5) * mm, "end": v(-552.12, 445.21) * mm});
            skLineSegment(sketch, "E2942", {"start": v(-552.12, 445.21) * mm, "end": v(-556.1, 445.85) * mm});
            skLineSegment(sketch, "E2943", {"start": v(-556.1, 445.85) * mm, "end": v(-559.57, 446.4) * mm});
            skLineSegment(sketch, "E2944", {"start": v(-559.57, 446.4) * mm, "end": v(-562.5, 446.87) * mm});
            skLineSegment(sketch, "E2945", {"start": v(-562.5, 446.87) * mm, "end": v(-564.86, 447.25) * mm});
            skLineSegment(sketch, "E2946", {"start": v(-564.86, 447.25) * mm, "end": v(-566.6, 447.53) * mm});
            skLineSegment(sketch, "E2947", {"start": v(-566.6, 447.53) * mm, "end": v(-567.67, 447.7) * mm});
            skLineSegment(sketch, "E2948", {"start": v(-567.67, 447.7) * mm, "end": v(-568.03, 447.76) * mm});
            skLineSegment(sketch, "E2949", {"start": v(608.55, 177.07) * mm, "end": v(606.71, 176.62) * mm});
            skLineSegment(sketch, "E2950", {"start": v(606.71, 176.62) * mm, "end": v(601.18, 175.26) * mm});
            skLineSegment(sketch, "E2951", {"start": v(601.18, 175.26) * mm, "end": v(594.84, 173.72) * mm});
            skLineSegment(sketch, "E2952", {"start": v(594.84, 173.72) * mm, "end": v(589.4, 172.41) * mm});
            skLineSegment(sketch, "E2953", {"start": v(589.4, 172.41) * mm, "end": v(584.7, 171.32) * mm});
            skLineSegment(sketch, "E2954", {"start": v(584.7, 171.32) * mm, "end": v(580.63, 170.42) * mm});
            skLineSegment(sketch, "E2955", {"start": v(580.63, 170.42) * mm, "end": v(577.02, 169.67) * mm});
            skLineSegment(sketch, "E2956", {"start": v(577.02, 169.67) * mm, "end": v(573.76, 169.06) * mm});
            skLineSegment(sketch, "E2957", {"start": v(573.76, 169.06) * mm, "end": v(570.7, 168.55) * mm});
            skLineSegment(sketch, "E2958", {"start": v(570.7, 168.55) * mm, "end": v(567.71, 168.1) * mm});
            skLineSegment(sketch, "E2959", {"start": v(567.71, 168.1) * mm, "end": v(564.65, 167.72) * mm});
            skLineSegment(sketch, "E2960", {"start": v(564.65, 167.72) * mm, "end": v(561.37, 167.36) * mm});
            skLineSegment(sketch, "E2961", {"start": v(561.37, 167.36) * mm, "end": v(557.74, 166.98) * mm});
            skLineSegment(sketch, "E2962", {"start": v(557.74, 166.98) * mm, "end": v(553.62, 166.58) * mm});
            skLineSegment(sketch, "E2963", {"start": v(553.62, 166.58) * mm, "end": v(548.89, 166.11) * mm});
            skLineSegment(sketch, "E2964", {"start": v(548.89, 166.11) * mm, "end": v(543.39, 165.56) * mm});
            skLineSegment(sketch, "E2965", {"start": v(543.39, 165.56) * mm, "end": v(538.58, 165.05) * mm});
            skLineSegment(sketch, "E2966", {"start": v(538.58, 165.05) * mm, "end": v(536.98, 164.89) * mm});
            skLineSegment(sketch, "E2967", {"start": v(536.98, 164.89) * mm, "end": v(534.48, 164.62) * mm});
            skLineSegment(sketch, "E2968", {"start": v(534.48, 164.62) * mm, "end": v(526.94, 164.13) * mm});
            skLineSegment(sketch, "E2969", {"start": v(526.94, 164.13) * mm, "end": v(517.07, 164.03) * mm});
            skLineSegment(sketch, "E2970", {"start": v(517.07, 164.03) * mm, "end": v(507.39, 164.53) * mm});
            skLineSegment(sketch, "E2971", {"start": v(507.39, 164.53) * mm, "end": v(497.89, 165.6) * mm});
            skLineSegment(sketch, "E2972", {"start": v(497.89, 165.6) * mm, "end": v(488.58, 167.22) * mm});
            skLineSegment(sketch, "E2973", {"start": v(488.58, 167.22) * mm, "end": v(479.46, 169.33) * mm});
            skLineSegment(sketch, "E2974", {"start": v(479.46, 169.33) * mm, "end": v(470.54, 171.91) * mm});
            skLineSegment(sketch, "E2975", {"start": v(470.54, 171.91) * mm, "end": v(461.82, 174.93) * mm});
            skLineSegment(sketch, "E2976", {"start": v(461.82, 174.93) * mm, "end": v(453.3, 178.34) * mm});
            skLineSegment(sketch, "E2977", {"start": v(453.3, 178.34) * mm, "end": v(444.99, 182.12) * mm});
            skLineSegment(sketch, "E2978", {"start": v(444.99, 182.12) * mm, "end": v(436.88, 186.22) * mm});
            skLineSegment(sketch, "E2979", {"start": v(436.88, 186.22) * mm, "end": v(428.99, 190.61) * mm});
            skLineSegment(sketch, "E2980", {"start": v(428.99, 190.61) * mm, "end": v(421.3, 195.26) * mm});
            skLineSegment(sketch, "E2981", {"start": v(421.3, 195.26) * mm, "end": v(413.84, 200.13) * mm});
            skLineSegment(sketch, "E2982", {"start": v(413.84, 200.13) * mm, "end": v(406.6, 205.2) * mm});
            skLineSegment(sketch, "E2983", {"start": v(406.6, 205.2) * mm, "end": v(399.58, 210.4) * mm});
            skLineSegment(sketch, "E2984", {"start": v(399.58, 210.4) * mm, "end": v(392.79, 215.73) * mm});
            skLineSegment(sketch, "E2985", {"start": v(392.79, 215.73) * mm, "end": v(386.22, 221.14) * mm});
            skLineSegment(sketch, "E2986", {"start": v(386.22, 221.14) * mm, "end": v(379.9, 226.59) * mm});
            skLineSegment(sketch, "E2987", {"start": v(379.9, 226.59) * mm, "end": v(373.8, 232.05) * mm});
            skLineSegment(sketch, "E2988", {"start": v(373.8, 232.05) * mm, "end": v(367.95, 237.49) * mm});
            skLineSegment(sketch, "E2989", {"start": v(367.95, 237.49) * mm, "end": v(362.34, 242.87) * mm});
            skLineSegment(sketch, "E2990", {"start": v(362.34, 242.87) * mm, "end": v(356.97, 248.15) * mm});
            skLineSegment(sketch, "E2991", {"start": v(356.97, 248.15) * mm, "end": v(351.85, 253.3) * mm});
            skLineSegment(sketch, "E2992", {"start": v(351.85, 253.3) * mm, "end": v(346.99, 258.3) * mm});
            skLineSegment(sketch, "E2993", {"start": v(346.99, 258.3) * mm, "end": v(342.37, 263.09) * mm});
            skLineSegment(sketch, "E2994", {"start": v(342.37, 263.09) * mm, "end": v(338.02, 267.64) * mm});
            skLineSegment(sketch, "E2995", {"start": v(338.02, 267.64) * mm, "end": v(333.93, 271.92) * mm});
            skLineSegment(sketch, "E2996", {"start": v(333.93, 271.92) * mm, "end": v(330.1, 275.9) * mm});
            skLineSegment(sketch, "E2997", {"start": v(330.1, 275.9) * mm, "end": v(326.53, 279.54) * mm});
            skLineSegment(sketch, "E2998", {"start": v(326.53, 279.54) * mm, "end": v(323.24, 282.8) * mm});
            skLineSegment(sketch, "E2999", {"start": v(323.24, 282.8) * mm, "end": v(320.99, 284.95) * mm});
            skLineSegment(sketch, "E3000", {"start": v(320.99, 284.95) * mm, "end": v(320.22, 285.65) * mm});
            skLineSegment(sketch, "E3001", {"start": v(320.22, 285.65) * mm, "end": v(317.6, 288.05) * mm});
            skLineSegment(sketch, "E3002", {"start": v(317.6, 288.05) * mm, "end": v(309.71, 295.26) * mm});
            skLineSegment(sketch, "E3003", {"start": v(309.71, 295.26) * mm, "end": v(299.56, 304.54) * mm});
            skLineSegment(sketch, "E3004", {"start": v(299.56, 304.54) * mm, "end": v(289.77, 313.48) * mm});
            skLineSegment(sketch, "E3005", {"start": v(289.77, 313.48) * mm, "end": v(280.31, 322.08) * mm});
            skLineSegment(sketch, "E3006", {"start": v(280.31, 322.08) * mm, "end": v(271.17, 330.36) * mm});
            skLineSegment(sketch, "E3007", {"start": v(271.17, 330.36) * mm, "end": v(262.35, 338.3) * mm});
            skLineSegment(sketch, "E3008", {"start": v(262.35, 338.3) * mm, "end": v(253.81, 345.93) * mm});
            skLineSegment(sketch, "E3009", {"start": v(253.81, 345.93) * mm, "end": v(245.56, 353.23) * mm});
            skLineSegment(sketch, "E3010", {"start": v(245.56, 353.23) * mm, "end": v(237.58, 360.21) * mm});
            skLineSegment(sketch, "E3011", {"start": v(237.58, 360.21) * mm, "end": v(229.84, 366.87) * mm});
            skLineSegment(sketch, "E3012", {"start": v(229.84, 366.87) * mm, "end": v(222.35, 373.23) * mm});
            skLineSegment(sketch, "E3013", {"start": v(222.35, 373.23) * mm, "end": v(215.07, 379.27) * mm});
            skLineSegment(sketch, "E3014", {"start": v(215.07, 379.27) * mm, "end": v(208, 385.01) * mm});
            skLineSegment(sketch, "E3015", {"start": v(208, 385.01) * mm, "end": v(201.14, 390.44) * mm});
            skLineSegment(sketch, "E3016", {"start": v(201.14, 390.44) * mm, "end": v(194.45, 395.57) * mm});
            skLineSegment(sketch, "E3017", {"start": v(194.45, 395.57) * mm, "end": v(187.93, 400.4) * mm});
            skLineSegment(sketch, "E3018", {"start": v(187.93, 400.4) * mm, "end": v(181.56, 404.94) * mm});
            skLineSegment(sketch, "E3019", {"start": v(181.56, 404.94) * mm, "end": v(175.32, 409.18) * mm});
            skLineSegment(sketch, "E3020", {"start": v(175.32, 409.18) * mm, "end": v(169.22, 413.13) * mm});
            skLineSegment(sketch, "E3021", {"start": v(169.22, 413.13) * mm, "end": v(163.22, 416.8) * mm});
            skLineSegment(sketch, "E3022", {"start": v(163.22, 416.8) * mm, "end": v(157.31, 420.17) * mm});
            skLineSegment(sketch, "E3023", {"start": v(157.31, 420.17) * mm, "end": v(151.48, 423.27) * mm});
            skLineSegment(sketch, "E3024", {"start": v(151.48, 423.27) * mm, "end": v(145.73, 426.08) * mm});
            skLineSegment(sketch, "E3025", {"start": v(145.73, 426.08) * mm, "end": v(140.02, 428.62) * mm});
            skLineSegment(sketch, "E3026", {"start": v(140.02, 428.62) * mm, "end": v(134.36, 430.9) * mm});
            skLineSegment(sketch, "E3027", {"start": v(134.36, 430.9) * mm, "end": v(128.71, 432.9) * mm});
            skLineSegment(sketch, "E3028", {"start": v(128.71, 432.9) * mm, "end": v(123.08, 434.62) * mm});
            skLineSegment(sketch, "E3029", {"start": v(123.08, 434.62) * mm, "end": v(117.44, 436.08) * mm});
            skLineSegment(sketch, "E3030", {"start": v(117.44, 436.08) * mm, "end": v(111.79, 437.29) * mm});
            skLineSegment(sketch, "E3031", {"start": v(111.79, 437.29) * mm, "end": v(106.1, 438.23) * mm});
            skLineSegment(sketch, "E3032", {"start": v(106.1, 438.23) * mm, "end": v(100.36, 438.91) * mm});
            skLineSegment(sketch, "E3033", {"start": v(100.36, 438.91) * mm, "end": v(96.01, 439.27) * mm});
            skLineSegment(sketch, "E3034", {"start": v(96.01, 439.27) * mm, "end": v(94.56, 439.35) * mm});
            skLineSegment(sketch, "E3035", {"start": v(94.56, 439.35) * mm, "end": v(91.41, 439.51) * mm});
            skLineSegment(sketch, "E3036", {"start": v(91.41, 439.51) * mm, "end": v(81.96, 439.84) * mm});
            skLineSegment(sketch, "E3037", {"start": v(81.96, 439.84) * mm, "end": v(69.94, 439.99) * mm});
            skLineSegment(sketch, "E3038", {"start": v(69.94, 439.99) * mm, "end": v(58.48, 439.8) * mm});
            skLineSegment(sketch, "E3039", {"start": v(58.48, 439.8) * mm, "end": v(47.56, 439.3) * mm});
            skLineSegment(sketch, "E3040", {"start": v(47.56, 439.3) * mm, "end": v(37.14, 438.52) * mm});
            skLineSegment(sketch, "E3041", {"start": v(37.14, 438.52) * mm, "end": v(27.2, 437.47) * mm});
            skLineSegment(sketch, "E3042", {"start": v(27.2, 437.47) * mm, "end": v(17.72, 436.18) * mm});
            skLineSegment(sketch, "E3043", {"start": v(17.72, 436.18) * mm, "end": v(8.66, 434.67) * mm});
            skLineSegment(sketch, "E3044", {"start": v(8.66, 434.67) * mm, "end": v(0, 432.96) * mm});
            skLineSegment(sketch, "E3045", {"start": v(0, 432.96) * mm, "end": v(-8.29, 431.08) * mm});
            skLineSegment(sketch, "E3046", {"start": v(-8.29, 431.08) * mm, "end": v(-16.22, 429.04) * mm});
            skLineSegment(sketch, "E3047", {"start": v(-16.22, 429.04) * mm, "end": v(-23.84, 426.87) * mm});
            skLineSegment(sketch, "E3048", {"start": v(-23.84, 426.87) * mm, "end": v(-31.17, 424.6) * mm});
            skLineSegment(sketch, "E3049", {"start": v(-31.17, 424.6) * mm, "end": v(-38.22, 422.23) * mm});
            skLineSegment(sketch, "E3050", {"start": v(-38.22, 422.23) * mm, "end": v(-45.04, 419.8) * mm});
            skLineSegment(sketch, "E3051", {"start": v(-45.04, 419.8) * mm, "end": v(-51.63, 417.32) * mm});
            skLineSegment(sketch, "E3052", {"start": v(-51.63, 417.32) * mm, "end": v(-58.04, 414.83) * mm});
            skLineSegment(sketch, "E3053", {"start": v(-58.04, 414.83) * mm, "end": v(-64.3, 412.34) * mm});
            skLineSegment(sketch, "E3054", {"start": v(-64.3, 412.34) * mm, "end": v(-70.4, 409.86) * mm});
            skLineSegment(sketch, "E3055", {"start": v(-70.4, 409.86) * mm, "end": v(-76.4, 407.44) * mm});
            skLineSegment(sketch, "E3056", {"start": v(-76.4, 407.44) * mm, "end": v(-82.33, 405.08) * mm});
            skLineSegment(sketch, "E3057", {"start": v(-82.33, 405.08) * mm, "end": v(-88.19, 402.82) * mm});
            skLineSegment(sketch, "E3058", {"start": v(-88.19, 402.82) * mm, "end": v(-94.02, 400.66) * mm});
            skLineSegment(sketch, "E3059", {"start": v(-94.02, 400.66) * mm, "end": v(-99.85, 398.64) * mm});
            skLineSegment(sketch, "E3060", {"start": v(-99.85, 398.64) * mm, "end": v(-105.7, 396.77) * mm});
            skLineSegment(sketch, "E3061", {"start": v(-105.7, 396.77) * mm, "end": v(-111.6, 395.08) * mm});
            skLineSegment(sketch, "E3062", {"start": v(-111.6, 395.08) * mm, "end": v(-117.59, 393.6) * mm});
            skLineSegment(sketch, "E3063", {"start": v(-117.59, 393.6) * mm, "end": v(-123.67, 392.33) * mm});
            skLineSegment(sketch, "E3064", {"start": v(-123.67, 392.33) * mm, "end": v(-129.88, 391.3) * mm});
            skLineSegment(sketch, "E3065", {"start": v(-129.88, 391.3) * mm, "end": v(-136.24, 390.55) * mm});
            skLineSegment(sketch, "E3066", {"start": v(-136.24, 390.55) * mm, "end": v(-142.79, 390.08) * mm});
            skLineSegment(sketch, "E3067", {"start": v(-142.79, 390.08) * mm, "end": v(-147.85, 389.92) * mm});
            skLineSegment(sketch, "E3068", {"start": v(-147.85, 389.92) * mm, "end": v(-149.54, 389.92) * mm});
            skLineSegment(sketch, "E3069", {"start": v(-149.54, 389.92) * mm, "end": v(-153.07, 389.93) * mm});
            skLineSegment(sketch, "E3070", {"start": v(-153.07, 389.93) * mm, "end": v(-163.67, 389.9) * mm});
            skLineSegment(sketch, "E3071", {"start": v(-163.67, 389.9) * mm, "end": v(-176.27, 389.85) * mm});
            skLineSegment(sketch, "E3072", {"start": v(-176.27, 389.85) * mm, "end": v(-187.46, 389.75) * mm});
            skLineSegment(sketch, "E3073", {"start": v(-187.46, 389.75) * mm, "end": v(-197.38, 389.62) * mm});
            skLineSegment(sketch, "E3074", {"start": v(-197.38, 389.62) * mm, "end": v(-206.15, 389.49) * mm});
            skLineSegment(sketch, "E3075", {"start": v(-206.15, 389.49) * mm, "end": v(-213.92, 389.34) * mm});
            skLineSegment(sketch, "E3076", {"start": v(-213.92, 389.34) * mm, "end": v(-220.81, 389.2) * mm});
            skLineSegment(sketch, "E3077", {"start": v(-220.81, 389.2) * mm, "end": v(-226.96, 389.08) * mm});
            skLineSegment(sketch, "E3078", {"start": v(-226.96, 389.08) * mm, "end": v(-232.5, 388.98) * mm});
            skLineSegment(sketch, "E3079", {"start": v(-232.5, 388.98) * mm, "end": v(-237.55, 388.92) * mm});
            skLineSegment(sketch, "E3080", {"start": v(-237.55, 388.92) * mm, "end": v(-242.26, 388.92) * mm});
            skLineSegment(sketch, "E3081", {"start": v(-242.26, 388.92) * mm, "end": v(-246.76, 388.97) * mm});
            skLineSegment(sketch, "E3082", {"start": v(-246.76, 388.97) * mm, "end": v(-251.17, 389.1) * mm});
            skLineSegment(sketch, "E3083", {"start": v(-251.17, 389.1) * mm, "end": v(-255.63, 389.3) * mm});
            skLineSegment(sketch, "E3084", {"start": v(-255.63, 389.3) * mm, "end": v(-260.28, 389.6) * mm});
            skLineSegment(sketch, "E3085", {"start": v(-260.28, 389.6) * mm, "end": v(-264, 389.89) * mm});
            skLineSegment(sketch, "E3086", {"start": v(-264, 389.89) * mm, "end": v(-265.23, 390) * mm});
            skLineSegment(sketch, "E3087", {"start": v(-265.23, 390) * mm, "end": v(-267.93, 390.23) * mm});
            skLineSegment(sketch, "E3088", {"start": v(-267.93, 390.23) * mm, "end": v(-276, 391.35) * mm});
            skLineSegment(sketch, "E3089", {"start": v(-276, 391.35) * mm, "end": v(-287.44, 393.42) * mm});
            skLineSegment(sketch, "E3090", {"start": v(-287.44, 393.42) * mm, "end": v(-299.22, 395.95) * mm});
            skLineSegment(sketch, "E3091", {"start": v(-299.22, 395.95) * mm, "end": v(-311.01, 398.7) * mm});
            skLineSegment(sketch, "E3092", {"start": v(-311.01, 398.7) * mm, "end": v(-322.5, 401.42) * mm});
            skLineSegment(sketch, "E3093", {"start": v(-322.5, 401.42) * mm, "end": v(-333.33, 403.86) * mm});
            skLineSegment(sketch, "E3094", {"start": v(-333.33, 403.86) * mm, "end": v(-343.2, 405.76) * mm});
            skLineSegment(sketch, "E3095", {"start": v(-343.2, 405.76) * mm, "end": v(-349.62, 406.7) * mm});
            skLineSegment(sketch, "E3096", {"start": v(-349.62, 406.7) * mm, "end": v(-351.77, 406.88) * mm});
            skLineSegment(sketch, "E3097", {"start": v(-351.77, 406.88) * mm, "end": v(-354.13, 407.08) * mm});
            skLineSegment(sketch, "E3098", {"start": v(-354.13, 407.08) * mm, "end": v(-361.22, 407.41) * mm});
            skLineSegment(sketch, "E3099", {"start": v(-361.22, 407.41) * mm, "end": v(-370.23, 407.5) * mm});
            skLineSegment(sketch, "E3100", {"start": v(-370.23, 407.5) * mm, "end": v(-378.93, 407.3) * mm});
            skLineSegment(sketch, "E3101", {"start": v(-378.93, 407.3) * mm, "end": v(-387.45, 407) * mm});
            skLineSegment(sketch, "E3102", {"start": v(-387.45, 407) * mm, "end": v(-395.91, 406.79) * mm});
            skLineSegment(sketch, "E3103", {"start": v(-395.91, 406.79) * mm, "end": v(-404.44, 406.81) * mm});
            skLineSegment(sketch, "E3104", {"start": v(-404.44, 406.81) * mm, "end": v(-413.17, 407.26) * mm});
            skLineSegment(sketch, "E3105", {"start": v(-413.17, 407.26) * mm, "end": v(-419.97, 407.96) * mm});
            skLineSegment(sketch, "E3106", {"start": v(-419.97, 407.96) * mm, "end": v(-422.22, 408.3) * mm});
            skLineSegment(sketch, "E3107", {"start": v(-422.22, 408.3) * mm, "end": v(-422.96, 408.42) * mm});
            skLineSegment(sketch, "E3108", {"start": v(-422.96, 408.42) * mm, "end": v(-425.17, 408.76) * mm});
            skLineSegment(sketch, "E3109", {"start": v(-425.17, 408.76) * mm, "end": v(-428.57, 409.3) * mm});
            skLineSegment(sketch, "E3110", {"start": v(-428.57, 409.3) * mm, "end": v(-432.4, 409.94) * mm});
            skLineSegment(sketch, "E3111", {"start": v(-432.4, 409.94) * mm, "end": v(-436.6, 410.64) * mm});
            skLineSegment(sketch, "E3112", {"start": v(-436.6, 410.64) * mm, "end": v(-441.14, 411.42) * mm});
            skLineSegment(sketch, "E3113", {"start": v(-441.14, 411.42) * mm, "end": v(-446, 412.25) * mm});
            skLineSegment(sketch, "E3114", {"start": v(-446, 412.25) * mm, "end": v(-451.12, 413.15) * mm});
            skLineSegment(sketch, "E3115", {"start": v(-451.12, 413.15) * mm, "end": v(-456.5, 414.09) * mm});
            skLineSegment(sketch, "E3116", {"start": v(-456.5, 414.09) * mm, "end": v(-462.06, 415.07) * mm});
            skLineSegment(sketch, "E3117", {"start": v(-462.06, 415.07) * mm, "end": v(-467.8, 416.1) * mm});
            skLineSegment(sketch, "E3118", {"start": v(-467.8, 416.1) * mm, "end": v(-473.66, 417.14) * mm});
            skLineSegment(sketch, "E3119", {"start": v(-473.66, 417.14) * mm, "end": v(-479.62, 418.2) * mm});
            skLineSegment(sketch, "E3120", {"start": v(-479.62, 418.2) * mm, "end": v(-485.64, 419.29) * mm});
            skLineSegment(sketch, "E3121", {"start": v(-485.64, 419.29) * mm, "end": v(-491.68, 420.38) * mm});
            skLineSegment(sketch, "E3122", {"start": v(-491.68, 420.38) * mm, "end": v(-497.7, 421.47) * mm});
            skLineSegment(sketch, "E3123", {"start": v(-497.7, 421.47) * mm, "end": v(-503.69, 422.55) * mm});
            skLineSegment(sketch, "E3124", {"start": v(-503.69, 422.55) * mm, "end": v(-509.58, 423.63) * mm});
            skLineSegment(sketch, "E3125", {"start": v(-509.58, 423.63) * mm, "end": v(-515.35, 424.68) * mm});
            skLineSegment(sketch, "E3126", {"start": v(-515.35, 424.68) * mm, "end": v(-520.97, 425.7) * mm});
            skLineSegment(sketch, "E3127", {"start": v(-520.97, 425.7) * mm, "end": v(-526.4, 426.7) * mm});
            skLineSegment(sketch, "E3128", {"start": v(-526.4, 426.7) * mm, "end": v(-531.6, 427.66) * mm});
            skLineSegment(sketch, "E3129", {"start": v(-531.6, 427.66) * mm, "end": v(-536.53, 428.56) * mm});
            skLineSegment(sketch, "E3130", {"start": v(-536.53, 428.56) * mm, "end": v(-541.16, 429.41) * mm});
            skLineSegment(sketch, "E3131", {"start": v(-541.16, 429.41) * mm, "end": v(-545.46, 430.2) * mm});
            skLineSegment(sketch, "E3132", {"start": v(-545.46, 430.2) * mm, "end": v(-549.38, 430.93) * mm});
            skLineSegment(sketch, "E3133", {"start": v(-549.38, 430.93) * mm, "end": v(-552.9, 431.58) * mm});
            skLineSegment(sketch, "E3134", {"start": v(-552.9, 431.58) * mm, "end": v(-555.98, 432.15) * mm});
            skLineSegment(sketch, "E3135", {"start": v(-555.98, 432.15) * mm, "end": v(-558.58, 432.63) * mm});
            skLineSegment(sketch, "E3136", {"start": v(-558.58, 432.63) * mm, "end": v(-560.66, 433.01) * mm});
            skLineSegment(sketch, "E3137", {"start": v(-560.66, 433.01) * mm, "end": v(-562.19, 433.3) * mm});
            skLineSegment(sketch, "E3138", {"start": v(-562.19, 433.3) * mm, "end": v(-563.14, 433.47) * mm});
            skLineSegment(sketch, "E3139", {"start": v(-563.14, 433.47) * mm, "end": v(-563.46, 433.53) * mm});
            skLineSegment(sketch, "E3140", {"start": v(609.59, 239.23) * mm, "end": v(608.68, 239.1) * mm});
            skLineSegment(sketch, "E3141", {"start": v(608.68, 239.1) * mm, "end": v(605.99, 238.62) * mm});
            skLineSegment(sketch, "E3142", {"start": v(605.99, 238.62) * mm, "end": v(602.78, 237.84) * mm});
            skLineSegment(sketch, "E3143", {"start": v(602.78, 237.84) * mm, "end": v(599.85, 236.9) * mm});
            skLineSegment(sketch, "E3144", {"start": v(599.85, 236.9) * mm, "end": v(597.1, 235.83) * mm});
            skLineSegment(sketch, "E3145", {"start": v(597.1, 235.83) * mm, "end": v(594.4, 234.64) * mm});
            skLineSegment(sketch, "E3146", {"start": v(594.4, 234.64) * mm, "end": v(591.66, 233.34) * mm});
            skLineSegment(sketch, "E3147", {"start": v(591.66, 233.34) * mm, "end": v(588.76, 231.97) * mm});
            skLineSegment(sketch, "E3148", {"start": v(588.76, 231.97) * mm, "end": v(585.61, 230.53) * mm});
            skLineSegment(sketch, "E3149", {"start": v(585.61, 230.53) * mm, "end": v(582.09, 229.04) * mm});
            skLineSegment(sketch, "E3150", {"start": v(582.09, 229.04) * mm, "end": v(578.1, 227.53) * mm});
            skLineSegment(sketch, "E3151", {"start": v(578.1, 227.53) * mm, "end": v(573.5, 226) * mm});
            skLineSegment(sketch, "E3152", {"start": v(573.5, 226) * mm, "end": v(568.23, 224.48) * mm});
            skLineSegment(sketch, "E3153", {"start": v(568.23, 224.48) * mm, "end": v(562.15, 223) * mm});
            skLineSegment(sketch, "E3154", {"start": v(562.15, 223) * mm, "end": v(555.17, 221.55) * mm});
            skLineSegment(sketch, "E3155", {"start": v(555.17, 221.55) * mm, "end": v(547.17, 220.17) * mm});
            skLineSegment(sketch, "E3156", {"start": v(547.17, 220.17) * mm, "end": v(540.33, 219.16) * mm});
            skLineSegment(sketch, "E3157", {"start": v(540.33, 219.16) * mm, "end": v(538.04, 218.86) * mm});
            skLineSegment(sketch, "E3158", {"start": v(538.04, 218.86) * mm, "end": v(535.3, 218.5) * mm});
            skLineSegment(sketch, "E3159", {"start": v(535.3, 218.5) * mm, "end": v(526.95, 218.29) * mm});
            skLineSegment(sketch, "E3160", {"start": v(526.95, 218.29) * mm, "end": v(515.28, 219.3) * mm});
            skLineSegment(sketch, "E3161", {"start": v(515.28, 219.3) * mm, "end": v(503.13, 221.77) * mm});
            skLineSegment(sketch, "E3162", {"start": v(503.13, 221.77) * mm, "end": v(490.54, 225.61) * mm});
            skLineSegment(sketch, "E3163", {"start": v(490.54, 225.61) * mm, "end": v(477.61, 230.72) * mm});
            skLineSegment(sketch, "E3164", {"start": v(477.61, 230.72) * mm, "end": v(464.4, 236.98) * mm});
            skLineSegment(sketch, "E3165", {"start": v(464.4, 236.98) * mm, "end": v(451, 244.3) * mm});
            skLineSegment(sketch, "E3166", {"start": v(451, 244.3) * mm, "end": v(437.46, 252.56) * mm});
            skLineSegment(sketch, "E3167", {"start": v(437.46, 252.56) * mm, "end": v(423.87, 261.67) * mm});
            skLineSegment(sketch, "E3168", {"start": v(423.87, 261.67) * mm, "end": v(410.3, 271.52) * mm});
            skLineSegment(sketch, "E3169", {"start": v(410.3, 271.52) * mm, "end": v(396.83, 282) * mm});
            skLineSegment(sketch, "E3170", {"start": v(396.83, 282) * mm, "end": v(383.52, 293.03) * mm});
            skLineSegment(sketch, "E3171", {"start": v(383.52, 293.03) * mm, "end": v(370.46, 304.48) * mm});
            skLineSegment(sketch, "E3172", {"start": v(370.46, 304.48) * mm, "end": v(357.7, 316.24) * mm});
            skLineSegment(sketch, "E3173", {"start": v(357.7, 316.24) * mm, "end": v(345.35, 328.24) * mm});
            skLineSegment(sketch, "E3174", {"start": v(345.35, 328.24) * mm, "end": v(336.4, 337.28) * mm});
            skLineSegment(sketch, "E3175", {"start": v(336.4, 337.28) * mm, "end": v(333.46, 340.34) * mm});
            skLineSegment(sketch, "E3176", {"start": v(333.46, 340.34) * mm, "end": v(330.44, 343.48) * mm});
            skLineSegment(sketch, "E3177", {"start": v(330.44, 343.48) * mm, "end": v(321.17, 352.68) * mm});
            skLineSegment(sketch, "E3178", {"start": v(321.17, 352.68) * mm, "end": v(308.03, 364.98) * mm});
            skLineSegment(sketch, "E3179", {"start": v(308.03, 364.98) * mm, "end": v(294.14, 377.15) * mm});
            skLineSegment(sketch, "E3180", {"start": v(294.14, 377.15) * mm, "end": v(279.59, 389.1) * mm});
            skLineSegment(sketch, "E3181", {"start": v(279.59, 389.1) * mm, "end": v(264.47, 400.72) * mm});
            skLineSegment(sketch, "E3182", {"start": v(264.47, 400.72) * mm, "end": v(248.9, 411.93) * mm});
            skLineSegment(sketch, "E3183", {"start": v(248.9, 411.93) * mm, "end": v(232.99, 422.63) * mm});
            skLineSegment(sketch, "E3184", {"start": v(232.99, 422.63) * mm, "end": v(216.8, 432.72) * mm});
            skLineSegment(sketch, "E3185", {"start": v(216.8, 432.72) * mm, "end": v(200.46, 442.11) * mm});
            skLineSegment(sketch, "E3186", {"start": v(200.46, 442.11) * mm, "end": v(184.06, 450.71) * mm});
            skLineSegment(sketch, "E3187", {"start": v(184.06, 450.71) * mm, "end": v(167.7, 458.42) * mm});
            skLineSegment(sketch, "E3188", {"start": v(167.7, 458.42) * mm, "end": v(151.48, 465.14) * mm});
            skLineSegment(sketch, "E3189", {"start": v(151.48, 465.14) * mm, "end": v(135.5, 470.78) * mm});
            skLineSegment(sketch, "E3190", {"start": v(135.5, 470.78) * mm, "end": v(119.87, 475.25) * mm});
            skLineSegment(sketch, "E3191", {"start": v(119.87, 475.25) * mm, "end": v(104.67, 478.44) * mm});
            skLineSegment(sketch, "E3192", {"start": v(104.67, 478.44) * mm, "end": v(93.69, 479.98) * mm});
            skLineSegment(sketch, "E3193", {"start": v(93.69, 479.98) * mm, "end": v(90.01, 480.27) * mm});
            skLineSegment(sketch, "E3194", {"start": v(90.01, 480.27) * mm, "end": v(86.42, 480.55) * mm});
            skLineSegment(sketch, "E3195", {"start": v(86.42, 480.55) * mm, "end": v(75.6, 480.87) * mm});
            skLineSegment(sketch, "E3196", {"start": v(75.6, 480.87) * mm, "end": v(61.08, 480.52) * mm});
            skLineSegment(sketch, "E3197", {"start": v(61.08, 480.52) * mm, "end": v(46.47, 479.33) * mm});
            skLineSegment(sketch, "E3198", {"start": v(46.47, 479.33) * mm, "end": v(31.8, 477.44) * mm});
            skLineSegment(sketch, "E3199", {"start": v(31.8, 477.44) * mm, "end": v(17.1, 474.95) * mm});
            skLineSegment(sketch, "E3200", {"start": v(17.1, 474.95) * mm, "end": v(2.36, 471.99) * mm});
            skLineSegment(sketch, "E3201", {"start": v(2.36, 471.99) * mm, "end": v(-12.37, 468.67) * mm});
            skLineSegment(sketch, "E3202", {"start": v(-12.37, 468.67) * mm, "end": v(-27.09, 465.12) * mm});
            skLineSegment(sketch, "E3203", {"start": v(-27.09, 465.12) * mm, "end": v(-41.76, 461.45) * mm});
            skLineSegment(sketch, "E3204", {"start": v(-41.76, 461.45) * mm, "end": v(-56.37, 457.8) * mm});
            skLineSegment(sketch, "E3205", {"start": v(-56.37, 457.8) * mm, "end": v(-70.9, 454.27) * mm});
            skLineSegment(sketch, "E3206", {"start": v(-70.9, 454.27) * mm, "end": v(-85.34, 450.98) * mm});
            skLineSegment(sketch, "E3207", {"start": v(-85.34, 450.98) * mm, "end": v(-99.65, 448.06) * mm});
            skLineSegment(sketch, "E3208", {"start": v(-99.65, 448.06) * mm, "end": v(-113.81, 445.62) * mm});
            skLineSegment(sketch, "E3209", {"start": v(-113.81, 445.62) * mm, "end": v(-127.81, 443.79) * mm});
            skLineSegment(sketch, "E3210", {"start": v(-127.81, 443.79) * mm, "end": v(-138.17, 442.86) * mm});
            skLineSegment(sketch, "E3211", {"start": v(-138.17, 442.86) * mm, "end": v(-141.63, 442.68) * mm});
            skLineSegment(sketch, "E3212", {"start": v(-141.63, 442.68) * mm, "end": v(-144.93, 442.5) * mm});
            skLineSegment(sketch, "E3213", {"start": v(-144.93, 442.5) * mm, "end": v(-154.84, 441.9) * mm});
            skLineSegment(sketch, "E3214", {"start": v(-154.84, 441.9) * mm, "end": v(-167.11, 441.02) * mm});
            skLineSegment(sketch, "E3215", {"start": v(-167.11, 441.02) * mm, "end": v(-178.54, 440.09) * mm});
            skLineSegment(sketch, "E3216", {"start": v(-178.54, 440.09) * mm, "end": v(-189.22, 439.13) * mm});
            skLineSegment(sketch, "E3217", {"start": v(-189.22, 439.13) * mm, "end": v(-199.25, 438.21) * mm});
            skLineSegment(sketch, "E3218", {"start": v(-199.25, 438.21) * mm, "end": v(-208.74, 437.38) * mm});
            skLineSegment(sketch, "E3219", {"start": v(-208.74, 437.38) * mm, "end": v(-217.78, 436.66) * mm});
            skLineSegment(sketch, "E3220", {"start": v(-217.78, 436.66) * mm, "end": v(-226.47, 436.11) * mm});
            skLineSegment(sketch, "E3221", {"start": v(-226.47, 436.11) * mm, "end": v(-234.9, 435.78) * mm});
            skLineSegment(sketch, "E3222", {"start": v(-234.9, 435.78) * mm, "end": v(-243.2, 435.71) * mm});
            skLineSegment(sketch, "E3223", {"start": v(-243.2, 435.71) * mm, "end": v(-251.42, 435.95) * mm});
            skLineSegment(sketch, "E3224", {"start": v(-251.42, 435.95) * mm, "end": v(-259.7, 436.54) * mm});
            skLineSegment(sketch, "E3225", {"start": v(-259.7, 436.54) * mm, "end": v(-268.12, 437.53) * mm});
            skLineSegment(sketch, "E3226", {"start": v(-268.12, 437.53) * mm, "end": v(-276.79, 438.97) * mm});
            skLineSegment(sketch, "E3227", {"start": v(-276.79, 438.97) * mm, "end": v(-285.8, 440.9) * mm});
            skLineSegment(sketch, "E3228", {"start": v(-285.8, 440.9) * mm, "end": v(-292.9, 442.7) * mm});
            skLineSegment(sketch, "E3229", {"start": v(-292.9, 442.7) * mm, "end": v(-295.24, 443.36) * mm});
            skLineSegment(sketch, "E3230", {"start": v(-295.24, 443.36) * mm, "end": v(-296.56, 443.74) * mm});
            skLineSegment(sketch, "E3231", {"start": v(-296.56, 443.74) * mm, "end": v(-300.52, 444.93) * mm});
            skLineSegment(sketch, "E3232", {"start": v(-300.52, 444.93) * mm, "end": v(-306.42, 446.75) * mm});
            skLineSegment(sketch, "E3233", {"start": v(-306.42, 446.75) * mm, "end": v(-312.84, 448.7) * mm});
            skLineSegment(sketch, "E3234", {"start": v(-312.84, 448.7) * mm, "end": v(-319.7, 450.69) * mm});
            skLineSegment(sketch, "E3235", {"start": v(-319.7, 450.69) * mm, "end": v(-326.92, 452.58) * mm});
            skLineSegment(sketch, "E3236", {"start": v(-326.92, 452.58) * mm, "end": v(-334.4, 454.25) * mm});
            skLineSegment(sketch, "E3237", {"start": v(-334.4, 454.25) * mm, "end": v(-342.09, 455.6) * mm});
            skLineSegment(sketch, "E3238", {"start": v(-342.09, 455.6) * mm, "end": v(-347.92, 456.35) * mm});
            skLineSegment(sketch, "E3239", {"start": v(-347.92, 456.35) * mm, "end": v(-349.87, 456.5) * mm});
            skLineSegment(sketch, "E3240", {"start": v(-349.87, 456.5) * mm, "end": v(-351.03, 456.6) * mm});
            skLineSegment(sketch, "E3241", {"start": v(-351.03, 456.6) * mm, "end": v(-354.51, 456.8) * mm});
            skLineSegment(sketch, "E3242", {"start": v(-354.51, 456.8) * mm, "end": v(-358.77, 456.9) * mm});
            skLineSegment(sketch, "E3243", {"start": v(-358.77, 456.9) * mm, "end": v(-362.73, 456.85) * mm});
            skLineSegment(sketch, "E3244", {"start": v(-362.73, 456.85) * mm, "end": v(-366.48, 456.68) * mm});
            skLineSegment(sketch, "E3245", {"start": v(-366.48, 456.68) * mm, "end": v(-370.08, 456.43) * mm});
            skLineSegment(sketch, "E3246", {"start": v(-370.08, 456.43) * mm, "end": v(-373.62, 456.13) * mm});
            skLineSegment(sketch, "E3247", {"start": v(-373.62, 456.13) * mm, "end": v(-377.19, 455.83) * mm});
            skLineSegment(sketch, "E3248", {"start": v(-377.19, 455.83) * mm, "end": v(-380.85, 455.55) * mm});
            skLineSegment(sketch, "E3249", {"start": v(-380.85, 455.55) * mm, "end": v(-384.69, 455.35) * mm});
            skLineSegment(sketch, "E3250", {"start": v(-384.69, 455.35) * mm, "end": v(-388.79, 455.26) * mm});
            skLineSegment(sketch, "E3251", {"start": v(-388.79, 455.26) * mm, "end": v(-393.22, 455.31) * mm});
            skLineSegment(sketch, "E3252", {"start": v(-393.22, 455.31) * mm, "end": v(-398.07, 455.55) * mm});
            skLineSegment(sketch, "E3253", {"start": v(-398.07, 455.55) * mm, "end": v(-403.42, 456) * mm});
            skLineSegment(sketch, "E3254", {"start": v(-403.42, 456) * mm, "end": v(-409.34, 456.72) * mm});
            skLineSegment(sketch, "E3255", {"start": v(-409.34, 456.72) * mm, "end": v(-415.92, 457.73) * mm});
            skLineSegment(sketch, "E3256", {"start": v(-415.92, 457.73) * mm, "end": v(-421.4, 458.7) * mm});
            skLineSegment(sketch, "E3257", {"start": v(-421.4, 458.7) * mm, "end": v(-423.22, 459.07) * mm});
            skLineSegment(sketch, "E3258", {"start": v(-423.22, 459.07) * mm, "end": v(-423.96, 459.21) * mm});
            skLineSegment(sketch, "E3259", {"start": v(-423.96, 459.21) * mm, "end": v(-426.18, 459.65) * mm});
            skLineSegment(sketch, "E3260", {"start": v(-426.18, 459.65) * mm, "end": v(-429.65, 460.34) * mm});
            skLineSegment(sketch, "E3261", {"start": v(-429.65, 460.34) * mm, "end": v(-433.6, 461.11) * mm});
            skLineSegment(sketch, "E3262", {"start": v(-433.6, 461.11) * mm, "end": v(-437.97, 461.97) * mm});
            skLineSegment(sketch, "E3263", {"start": v(-437.97, 461.97) * mm, "end": v(-442.74, 462.91) * mm});
            skLineSegment(sketch, "E3264", {"start": v(-442.74, 462.91) * mm, "end": v(-447.85, 463.92) * mm});
            skLineSegment(sketch, "E3265", {"start": v(-447.85, 463.92) * mm, "end": v(-453.28, 464.99) * mm});
            skLineSegment(sketch, "E3266", {"start": v(-453.28, 464.99) * mm, "end": v(-458.99, 466.11) * mm});
            skLineSegment(sketch, "E3267", {"start": v(-458.99, 466.11) * mm, "end": v(-464.93, 467.28) * mm});
            skLineSegment(sketch, "E3268", {"start": v(-464.93, 467.28) * mm, "end": v(-471.06, 468.5) * mm});
            skLineSegment(sketch, "E3269", {"start": v(-471.06, 468.5) * mm, "end": v(-477.34, 469.73) * mm});
            skLineSegment(sketch, "E3270", {"start": v(-477.34, 469.73) * mm, "end": v(-483.74, 470.98) * mm});
            skLineSegment(sketch, "E3271", {"start": v(-483.74, 470.98) * mm, "end": v(-490.22, 472.26) * mm});
            skLineSegment(sketch, "E3272", {"start": v(-490.22, 472.26) * mm, "end": v(-496.72, 473.54) * mm});
            skLineSegment(sketch, "E3273", {"start": v(-496.72, 473.54) * mm, "end": v(-503.23, 474.82) * mm});
            skLineSegment(sketch, "E3274", {"start": v(-503.23, 474.82) * mm, "end": v(-509.69, 476.1) * mm});
            skLineSegment(sketch, "E3275", {"start": v(-509.69, 476.1) * mm, "end": v(-516.06, 477.34) * mm});
            skLineSegment(sketch, "E3276", {"start": v(-516.06, 477.34) * mm, "end": v(-522.31, 478.58) * mm});
            skLineSegment(sketch, "E3277", {"start": v(-522.31, 478.58) * mm, "end": v(-528.4, 479.78) * mm});
            skLineSegment(sketch, "E3278", {"start": v(-528.4, 479.78) * mm, "end": v(-534.29, 480.93) * mm});
            skLineSegment(sketch, "E3279", {"start": v(-534.29, 480.93) * mm, "end": v(-539.93, 482.04) * mm});
            skLineSegment(sketch, "E3280", {"start": v(-539.93, 482.04) * mm, "end": v(-545.3, 483.1) * mm});
            skLineSegment(sketch, "E3281", {"start": v(-545.3, 483.1) * mm, "end": v(-550.33, 484.09) * mm});
            skLineSegment(sketch, "E3282", {"start": v(-550.33, 484.09) * mm, "end": v(-555, 485) * mm});
            skLineSegment(sketch, "E3283", {"start": v(-555, 485) * mm, "end": v(-559.28, 485.85) * mm});
            skLineSegment(sketch, "E3284", {"start": v(-559.28, 485.85) * mm, "end": v(-563.11, 486.6) * mm});
            skLineSegment(sketch, "E3285", {"start": v(-563.11, 486.6) * mm, "end": v(-566.47, 487.26) * mm});
            skLineSegment(sketch, "E3286", {"start": v(-566.47, 487.26) * mm, "end": v(-569.3, 487.82) * mm});
            skLineSegment(sketch, "E3287", {"start": v(-569.3, 487.82) * mm, "end": v(-571.57, 488.26) * mm});
            skLineSegment(sketch, "E3288", {"start": v(-571.57, 488.26) * mm, "end": v(-573.24, 488.6) * mm});
            skLineSegment(sketch, "E3289", {"start": v(-573.24, 488.6) * mm, "end": v(-574.27, 488.8) * mm});
            skLineSegment(sketch, "E3290", {"start": v(-574.27, 488.8) * mm, "end": v(-574.63, 488.87) * mm});
            skLineSegment(sketch, "E3291", {"start": v(609.59, 258.64) * mm, "end": v(608.74, 258.53) * mm});
            skLineSegment(sketch, "E3292", {"start": v(608.74, 258.53) * mm, "end": v(606.21, 258.17) * mm});
            skLineSegment(sketch, "E3293", {"start": v(606.21, 258.17) * mm, "end": v(603.62, 257.75) * mm});
            skLineSegment(sketch, "E3294", {"start": v(603.62, 257.75) * mm, "end": v(601.63, 257.37) * mm});
            skLineSegment(sketch, "E3295", {"start": v(601.63, 257.37) * mm, "end": v(600.06, 256.98) * mm});
            skLineSegment(sketch, "E3296", {"start": v(600.06, 256.98) * mm, "end": v(598.73, 256.55) * mm});
            skLineSegment(sketch, "E3297", {"start": v(598.73, 256.55) * mm, "end": v(597.45, 256.06) * mm});
            skLineSegment(sketch, "E3298", {"start": v(597.45, 256.06) * mm, "end": v(596.03, 255.48) * mm});
            skLineSegment(sketch, "E3299", {"start": v(596.03, 255.48) * mm, "end": v(594.3, 254.76) * mm});
            skLineSegment(sketch, "E3300", {"start": v(594.3, 254.76) * mm, "end": v(592.07, 253.87) * mm});
            skLineSegment(sketch, "E3301", {"start": v(592.07, 253.87) * mm, "end": v(589.17, 252.8) * mm});
            skLineSegment(sketch, "E3302", {"start": v(589.17, 252.8) * mm, "end": v(585.4, 251.5) * mm});
            skLineSegment(sketch, "E3303", {"start": v(585.4, 251.5) * mm, "end": v(580.59, 249.93) * mm});
            skLineSegment(sketch, "E3304", {"start": v(580.59, 249.93) * mm, "end": v(574.54, 248.08) * mm});
            skLineSegment(sketch, "E3305", {"start": v(574.54, 248.08) * mm, "end": v(567.09, 245.9) * mm});
            skLineSegment(sketch, "E3306", {"start": v(567.09, 245.9) * mm, "end": v(558.04, 243.37) * mm});
            skLineSegment(sketch, "E3307", {"start": v(558.04, 243.37) * mm, "end": v(549.92, 241.18) * mm});
            skLineSegment(sketch, "E3308", {"start": v(549.92, 241.18) * mm, "end": v(547.21, 240.46) * mm});
            skLineSegment(sketch, "E3309", {"start": v(547.21, 240.46) * mm, "end": v(546.3, 240.22) * mm});
            skLineSegment(sketch, "E3310", {"start": v(546.3, 240.22) * mm, "end": v(543.51, 239.7) * mm});
            skLineSegment(sketch, "E3311", {"start": v(543.51, 239.7) * mm, "end": v(539.46, 239.3) * mm});
            skLineSegment(sketch, "E3312", {"start": v(539.46, 239.3) * mm, "end": v(535.08, 239.25) * mm});
            skLineSegment(sketch, "E3313", {"start": v(535.08, 239.25) * mm, "end": v(530.39, 239.53) * mm});
            skLineSegment(sketch, "E3314", {"start": v(530.39, 239.53) * mm, "end": v(525.4, 240.14) * mm});
            skLineSegment(sketch, "E3315", {"start": v(525.4, 240.14) * mm, "end": v(520.15, 241.07) * mm});
            skLineSegment(sketch, "E3316", {"start": v(520.15, 241.07) * mm, "end": v(514.65, 242.31) * mm});
            skLineSegment(sketch, "E3317", {"start": v(514.65, 242.31) * mm, "end": v(508.91, 243.86) * mm});
            skLineSegment(sketch, "E3318", {"start": v(508.91, 243.86) * mm, "end": v(502.96, 245.7) * mm});
            skLineSegment(sketch, "E3319", {"start": v(502.96, 245.7) * mm, "end": v(496.8, 247.84) * mm});
            skLineSegment(sketch, "E3320", {"start": v(496.8, 247.84) * mm, "end": v(490.48, 250.26) * mm});
            skLineSegment(sketch, "E3321", {"start": v(490.48, 250.26) * mm, "end": v(484, 252.94) * mm});
            skLineSegment(sketch, "E3322", {"start": v(484, 252.94) * mm, "end": v(477.37, 255.9) * mm});
            skLineSegment(sketch, "E3323", {"start": v(477.37, 255.9) * mm, "end": v(470.63, 259.1) * mm});
            skLineSegment(sketch, "E3324", {"start": v(470.63, 259.1) * mm, "end": v(463.79, 262.56) * mm});
            skLineSegment(sketch, "E3325", {"start": v(463.79, 262.56) * mm, "end": v(456.86, 266.25) * mm});
            skLineSegment(sketch, "E3326", {"start": v(456.86, 266.25) * mm, "end": v(449.87, 270.18) * mm});
            skLineSegment(sketch, "E3327", {"start": v(449.87, 270.18) * mm, "end": v(442.84, 274.33) * mm});
            skLineSegment(sketch, "E3328", {"start": v(442.84, 274.33) * mm, "end": v(435.78, 278.7) * mm});
            skLineSegment(sketch, "E3329", {"start": v(435.78, 278.7) * mm, "end": v(428.72, 283.28) * mm});
            skLineSegment(sketch, "E3330", {"start": v(428.72, 283.28) * mm, "end": v(421.66, 288.06) * mm});
            skLineSegment(sketch, "E3331", {"start": v(421.66, 288.06) * mm, "end": v(414.64, 293.02) * mm});
            skLineSegment(sketch, "E3332", {"start": v(414.64, 293.02) * mm, "end": v(407.68, 298.18) * mm});
            skLineSegment(sketch, "E3333", {"start": v(407.68, 298.18) * mm, "end": v(400.78, 303.5) * mm});
            skLineSegment(sketch, "E3334", {"start": v(400.78, 303.5) * mm, "end": v(393.96, 309) * mm});
            skLineSegment(sketch, "E3335", {"start": v(393.96, 309) * mm, "end": v(387.26, 314.65) * mm});
            skLineSegment(sketch, "E3336", {"start": v(387.26, 314.65) * mm, "end": v(380.69, 320.46) * mm});
            skLineSegment(sketch, "E3337", {"start": v(380.69, 320.46) * mm, "end": v(374.26, 326.41) * mm});
            skLineSegment(sketch, "E3338", {"start": v(374.26, 326.41) * mm, "end": v(367.99, 332.5) * mm});
            skLineSegment(sketch, "E3339", {"start": v(367.99, 332.5) * mm, "end": v(361.9, 338.7) * mm});
            skLineSegment(sketch, "E3340", {"start": v(361.9, 338.7) * mm, "end": v(356.02, 345.04) * mm});
            skLineSegment(sketch, "E3341", {"start": v(356.02, 345.04) * mm, "end": v(351.75, 349.85) * mm});
            skLineSegment(sketch, "E3342", {"start": v(351.75, 349.85) * mm, "end": v(350.36, 351.48) * mm});
            skLineSegment(sketch, "E3343", {"start": v(350.36, 351.48) * mm, "end": v(348.96, 353.13) * mm});
            skLineSegment(sketch, "E3344", {"start": v(348.96, 353.13) * mm, "end": v(344.64, 357.97) * mm});
            skLineSegment(sketch, "E3345", {"start": v(344.64, 357.97) * mm, "end": v(338.55, 364.44) * mm});
            skLineSegment(sketch, "E3346", {"start": v(338.55, 364.44) * mm, "end": v(332.13, 370.9) * mm});
            skLineSegment(sketch, "E3347", {"start": v(332.13, 370.9) * mm, "end": v(325.39, 377.3) * mm});
            skLineSegment(sketch, "E3348", {"start": v(325.39, 377.3) * mm, "end": v(318.35, 383.65) * mm});
            skLineSegment(sketch, "E3349", {"start": v(318.35, 383.65) * mm, "end": v(311.04, 389.94) * mm});
            skLineSegment(sketch, "E3350", {"start": v(311.04, 389.94) * mm, "end": v(303.48, 396.15) * mm});
            skLineSegment(sketch, "E3351", {"start": v(303.48, 396.15) * mm, "end": v(295.68, 402.28) * mm});
            skLineSegment(sketch, "E3352", {"start": v(295.68, 402.28) * mm, "end": v(287.66, 408.31) * mm});
            skLineSegment(sketch, "E3353", {"start": v(287.66, 408.31) * mm, "end": v(279.45, 414.24) * mm});
            skLineSegment(sketch, "E3354", {"start": v(279.45, 414.24) * mm, "end": v(271.08, 420.04) * mm});
            skLineSegment(sketch, "E3355", {"start": v(271.08, 420.04) * mm, "end": v(262.54, 425.71) * mm});
            skLineSegment(sketch, "E3356", {"start": v(262.54, 425.71) * mm, "end": v(253.88, 431.24) * mm});
            skLineSegment(sketch, "E3357", {"start": v(253.88, 431.24) * mm, "end": v(245.1, 436.62) * mm});
            skLineSegment(sketch, "E3358", {"start": v(245.1, 436.62) * mm, "end": v(236.25, 441.83) * mm});
            skLineSegment(sketch, "E3359", {"start": v(236.25, 441.83) * mm, "end": v(227.32, 446.86) * mm});
            skLineSegment(sketch, "E3360", {"start": v(227.32, 446.86) * mm, "end": v(218.33, 451.7) * mm});
            skLineSegment(sketch, "E3361", {"start": v(218.33, 451.7) * mm, "end": v(209.33, 456.35) * mm});
            skLineSegment(sketch, "E3362", {"start": v(209.33, 456.35) * mm, "end": v(200.31, 460.78) * mm});
            skLineSegment(sketch, "E3363", {"start": v(200.31, 460.78) * mm, "end": v(191.3, 465) * mm});
            skLineSegment(sketch, "E3364", {"start": v(191.3, 465) * mm, "end": v(182.34, 468.97) * mm});
            skLineSegment(sketch, "E3365", {"start": v(182.34, 468.97) * mm, "end": v(173.42, 472.7) * mm});
            skLineSegment(sketch, "E3366", {"start": v(173.42, 472.7) * mm, "end": v(164.58, 476.18) * mm});
            skLineSegment(sketch, "E3367", {"start": v(164.58, 476.18) * mm, "end": v(155.84, 479.39) * mm});
            skLineSegment(sketch, "E3368", {"start": v(155.84, 479.39) * mm, "end": v(147.2, 482.32) * mm});
            skLineSegment(sketch, "E3369", {"start": v(147.2, 482.32) * mm, "end": v(138.71, 484.95) * mm});
            skLineSegment(sketch, "E3370", {"start": v(138.71, 484.95) * mm, "end": v(130.37, 487.29) * mm});
            skLineSegment(sketch, "E3371", {"start": v(130.37, 487.29) * mm, "end": v(122.22, 489.3) * mm});
            skLineSegment(sketch, "E3372", {"start": v(122.22, 489.3) * mm, "end": v(114.26, 491) * mm});
            skLineSegment(sketch, "E3373", {"start": v(114.26, 491) * mm, "end": v(106.52, 492.36) * mm});
            skLineSegment(sketch, "E3374", {"start": v(106.52, 492.36) * mm, "end": v(99.02, 493.37) * mm});
            skLineSegment(sketch, "E3375", {"start": v(99.02, 493.37) * mm, "end": v(93.6, 493.9) * mm});
            skLineSegment(sketch, "E3376", {"start": v(93.6, 493.9) * mm, "end": v(91.78, 494.03) * mm});
            skLineSegment(sketch, "E3377", {"start": v(91.78, 494.03) * mm, "end": v(88.22, 494.26) * mm});
            skLineSegment(sketch, "E3378", {"start": v(88.22, 494.26) * mm, "end": v(77.5, 494.57) * mm});
            skLineSegment(sketch, "E3379", {"start": v(77.5, 494.57) * mm, "end": v(63.42, 494.38) * mm});
            skLineSegment(sketch, "E3380", {"start": v(63.42, 494.38) * mm, "end": v(49.5, 493.52) * mm});
            skLineSegment(sketch, "E3381", {"start": v(49.5, 493.52) * mm, "end": v(35.7, 492.08) * mm});
            skLineSegment(sketch, "E3382", {"start": v(35.7, 492.08) * mm, "end": v(22.03, 490.16) * mm});
            skLineSegment(sketch, "E3383", {"start": v(22.03, 490.16) * mm, "end": v(8.46, 487.84) * mm});
            skLineSegment(sketch, "E3384", {"start": v(8.46, 487.84) * mm, "end": v(-5.03, 485.2) * mm});
            skLineSegment(sketch, "E3385", {"start": v(-5.03, 485.2) * mm, "end": v(-18.46, 482.33) * mm});
            skLineSegment(sketch, "E3386", {"start": v(-18.46, 482.33) * mm, "end": v(-31.87, 479.32) * mm});
            skLineSegment(sketch, "E3387", {"start": v(-31.87, 479.32) * mm, "end": v(-45.25, 476.24) * mm});
            skLineSegment(sketch, "E3388", {"start": v(-45.25, 476.24) * mm, "end": v(-58.63, 473.2) * mm});
            skLineSegment(sketch, "E3389", {"start": v(-58.63, 473.2) * mm, "end": v(-72.05, 470.28) * mm});
            skLineSegment(sketch, "E3390", {"start": v(-72.05, 470.28) * mm, "end": v(-85.51, 467.55) * mm});
            skLineSegment(sketch, "E3391", {"start": v(-85.51, 467.55) * mm, "end": v(-99.04, 465.1) * mm});
            skLineSegment(sketch, "E3392", {"start": v(-99.04, 465.1) * mm, "end": v(-112.65, 463.04) * mm});
            skLineSegment(sketch, "E3393", {"start": v(-112.65, 463.04) * mm, "end": v(-122.94, 461.77) * mm});
            skLineSegment(sketch, "E3394", {"start": v(-122.94, 461.77) * mm, "end": v(-126.37, 461.43) * mm});
            skLineSegment(sketch, "E3395", {"start": v(-126.37, 461.43) * mm, "end": v(-129.66, 461.11) * mm});
            skLineSegment(sketch, "E3396", {"start": v(-129.66, 461.11) * mm, "end": v(-139.53, 460.02) * mm});
            skLineSegment(sketch, "E3397", {"start": v(-139.53, 460.02) * mm, "end": v(-151.71, 458.49) * mm});
            skLineSegment(sketch, "E3398", {"start": v(-151.71, 458.49) * mm, "end": v(-163.04, 456.89) * mm});
            skLineSegment(sketch, "E3399", {"start": v(-163.04, 456.89) * mm, "end": v(-173.6, 455.28) * mm});
            skLineSegment(sketch, "E3400", {"start": v(-173.6, 455.28) * mm, "end": v(-183.5, 453.71) * mm});
            skLineSegment(sketch, "E3401", {"start": v(-183.5, 453.71) * mm, "end": v(-192.85, 452.24) * mm});
            skLineSegment(sketch, "E3402", {"start": v(-192.85, 452.24) * mm, "end": v(-201.75, 450.92) * mm});
            skLineSegment(sketch, "E3403", {"start": v(-201.75, 450.92) * mm, "end": v(-210.3, 449.8) * mm});
            skLineSegment(sketch, "E3404", {"start": v(-210.3, 449.8) * mm, "end": v(-218.59, 448.93) * mm});
            skLineSegment(sketch, "E3405", {"start": v(-218.59, 448.93) * mm, "end": v(-226.74, 448.37) * mm});
            skLineSegment(sketch, "E3406", {"start": v(-226.74, 448.37) * mm, "end": v(-234.85, 448.18) * mm});
            skLineSegment(sketch, "E3407", {"start": v(-234.85, 448.18) * mm, "end": v(-243.02, 448.4) * mm});
            skLineSegment(sketch, "E3408", {"start": v(-243.02, 448.4) * mm, "end": v(-251.34, 449.09) * mm});
            skLineSegment(sketch, "E3409", {"start": v(-251.34, 449.09) * mm, "end": v(-259.94, 450.3) * mm});
            skLineSegment(sketch, "E3410", {"start": v(-259.94, 450.3) * mm, "end": v(-268.9, 452.09) * mm});
            skLineSegment(sketch, "E3411", {"start": v(-268.9, 452.09) * mm, "end": v(-275.99, 453.83) * mm});
            skLineSegment(sketch, "E3412", {"start": v(-275.99, 453.83) * mm, "end": v(-278.33, 454.5) * mm});
            skLineSegment(sketch, "E3413", {"start": v(-278.33, 454.5) * mm, "end": v(-279.02, 454.7) * mm});
            skLineSegment(sketch, "E3414", {"start": v(-279.02, 454.7) * mm, "end": v(-281.07, 455.27) * mm});
            skLineSegment(sketch, "E3415", {"start": v(-281.07, 455.27) * mm, "end": v(-284.31, 456.17) * mm});
            skLineSegment(sketch, "E3416", {"start": v(-284.31, 456.17) * mm, "end": v(-287.98, 457.18) * mm});
            skLineSegment(sketch, "E3417", {"start": v(-287.98, 457.18) * mm, "end": v(-292.03, 458.26) * mm});
            skLineSegment(sketch, "E3418", {"start": v(-292.03, 458.26) * mm, "end": v(-296.4, 459.42) * mm});
            skLineSegment(sketch, "E3419", {"start": v(-296.4, 459.42) * mm, "end": v(-301.04, 460.6) * mm});
            skLineSegment(sketch, "E3420", {"start": v(-301.04, 460.6) * mm, "end": v(-305.88, 461.82) * mm});
            skLineSegment(sketch, "E3421", {"start": v(-305.88, 461.82) * mm, "end": v(-310.87, 463.03) * mm});
            skLineSegment(sketch, "E3422", {"start": v(-310.87, 463.03) * mm, "end": v(-315.94, 464.22) * mm});
            skLineSegment(sketch, "E3423", {"start": v(-315.94, 464.22) * mm, "end": v(-321.05, 465.36) * mm});
            skLineSegment(sketch, "E3424", {"start": v(-321.05, 465.36) * mm, "end": v(-326.13, 466.43) * mm});
            skLineSegment(sketch, "E3425", {"start": v(-326.13, 466.43) * mm, "end": v(-331.13, 467.42) * mm});
            skLineSegment(sketch, "E3426", {"start": v(-331.13, 467.42) * mm, "end": v(-335.98, 468.3) * mm});
            skLineSegment(sketch, "E3427", {"start": v(-335.98, 468.3) * mm, "end": v(-340.64, 469.04) * mm});
            skLineSegment(sketch, "E3428", {"start": v(-340.64, 469.04) * mm, "end": v(-345.03, 469.64) * mm});
            skLineSegment(sketch, "E3429", {"start": v(-345.03, 469.64) * mm, "end": v(-348.1, 469.97) * mm});
            skLineSegment(sketch, "E3430", {"start": v(-348.1, 469.97) * mm, "end": v(-349.12, 470.05) * mm});
            skLineSegment(sketch, "E3431", {"start": v(-349.12, 470.05) * mm, "end": v(-351.35, 470.24) * mm});
            skLineSegment(sketch, "E3432", {"start": v(-351.35, 470.24) * mm, "end": v(-358.05, 470.53) * mm});
            skLineSegment(sketch, "E3433", {"start": v(-358.05, 470.53) * mm, "end": v(-365.7, 470.5) * mm});
            skLineSegment(sketch, "E3434", {"start": v(-365.7, 470.5) * mm, "end": v(-372.48, 470.13) * mm});
            skLineSegment(sketch, "E3435", {"start": v(-372.48, 470.13) * mm, "end": v(-378.8, 469.64) * mm});
            skLineSegment(sketch, "E3436", {"start": v(-378.8, 469.64) * mm, "end": v(-385.05, 469.22) * mm});
            skLineSegment(sketch, "E3437", {"start": v(-385.05, 469.22) * mm, "end": v(-391.66, 469.08) * mm});
            skLineSegment(sketch, "E3438", {"start": v(-391.66, 469.08) * mm, "end": v(-399.03, 469.4) * mm});
            skLineSegment(sketch, "E3439", {"start": v(-399.03, 469.4) * mm, "end": v(-405.44, 470.08) * mm});
            skLineSegment(sketch, "E3440", {"start": v(-405.44, 470.08) * mm, "end": v(-407.56, 470.4) * mm});
            skLineSegment(sketch, "E3441", {"start": v(-407.56, 470.4) * mm, "end": v(-408.32, 470.51) * mm});
            skLineSegment(sketch, "E3442", {"start": v(-408.32, 470.51) * mm, "end": v(-410.6, 470.88) * mm});
            skLineSegment(sketch, "E3443", {"start": v(-410.6, 470.88) * mm, "end": v(-414.24, 471.48) * mm});
            skLineSegment(sketch, "E3444", {"start": v(-414.24, 471.48) * mm, "end": v(-418.44, 472.2) * mm});
            skLineSegment(sketch, "E3445", {"start": v(-418.44, 472.2) * mm, "end": v(-423.16, 473.03) * mm});
            skLineSegment(sketch, "E3446", {"start": v(-423.16, 473.03) * mm, "end": v(-428.36, 473.95) * mm});
            skLineSegment(sketch, "E3447", {"start": v(-428.36, 473.95) * mm, "end": v(-433.97, 474.97) * mm});
            skLineSegment(sketch, "E3448", {"start": v(-433.97, 474.97) * mm, "end": v(-439.97, 476.06) * mm});
            skLineSegment(sketch, "E3449", {"start": v(-439.97, 476.06) * mm, "end": v(-446.3, 477.23) * mm});
            skLineSegment(sketch, "E3450", {"start": v(-446.3, 477.23) * mm, "end": v(-452.9, 478.46) * mm});
            skLineSegment(sketch, "E3451", {"start": v(-452.9, 478.46) * mm, "end": v(-459.76, 479.73) * mm});
            skLineSegment(sketch, "E3452", {"start": v(-459.76, 479.73) * mm, "end": v(-466.8, 481.06) * mm});
            skLineSegment(sketch, "E3453", {"start": v(-466.8, 481.06) * mm, "end": v(-474, 482.4) * mm});
            skLineSegment(sketch, "E3454", {"start": v(-474, 482.4) * mm, "end": v(-481.29, 483.79) * mm});
            skLineSegment(sketch, "E3455", {"start": v(-481.29, 483.79) * mm, "end": v(-488.63, 485.19) * mm});
            skLineSegment(sketch, "E3456", {"start": v(-488.63, 485.19) * mm, "end": v(-495.98, 486.59) * mm});
            skLineSegment(sketch, "E3457", {"start": v(-495.98, 486.59) * mm, "end": v(-503.3, 487.98) * mm});
            skLineSegment(sketch, "E3458", {"start": v(-503.3, 487.98) * mm, "end": v(-510.53, 489.37) * mm});
            skLineSegment(sketch, "E3459", {"start": v(-510.53, 489.37) * mm, "end": v(-517.63, 490.73) * mm});
            skLineSegment(sketch, "E3460", {"start": v(-517.63, 490.73) * mm, "end": v(-524.55, 492.06) * mm});
            skLineSegment(sketch, "E3461", {"start": v(-524.55, 492.06) * mm, "end": v(-531.25, 493.35) * mm});
            skLineSegment(sketch, "E3462", {"start": v(-531.25, 493.35) * mm, "end": v(-537.68, 494.6) * mm});
            skLineSegment(sketch, "E3463", {"start": v(-537.68, 494.6) * mm, "end": v(-543.79, 495.78) * mm});
            skLineSegment(sketch, "E3464", {"start": v(-543.79, 495.78) * mm, "end": v(-549.54, 496.89) * mm});
            skLineSegment(sketch, "E3465", {"start": v(-549.54, 496.89) * mm, "end": v(-554.88, 497.93) * mm});
            skLineSegment(sketch, "E3466", {"start": v(-554.88, 497.93) * mm, "end": v(-559.76, 498.87) * mm});
            skLineSegment(sketch, "E3467", {"start": v(-559.76, 498.87) * mm, "end": v(-564.15, 499.72) * mm});
            skLineSegment(sketch, "E3468", {"start": v(-564.15, 499.72) * mm, "end": v(-567.99, 500.47) * mm});
            skLineSegment(sketch, "E3469", {"start": v(-567.99, 500.47) * mm, "end": v(-571.23, 501.1) * mm});
            skLineSegment(sketch, "E3470", {"start": v(-571.23, 501.1) * mm, "end": v(-573.83, 501.6) * mm});
            skLineSegment(sketch, "E3471", {"start": v(-573.83, 501.6) * mm, "end": v(-575.75, 501.98) * mm});
            skLineSegment(sketch, "E3472", {"start": v(-575.75, 501.98) * mm, "end": v(-576.93, 502.22) * mm});
            skLineSegment(sketch, "E3473", {"start": v(-576.93, 502.22) * mm, "end": v(-577.34, 502.3) * mm});
            skLineSegment(sketch, "E3474", {"start": v(608.4, 280.43) * mm, "end": v(607.51, 280.31) * mm});
            skLineSegment(sketch, "E3475", {"start": v(607.51, 280.31) * mm, "end": v(604.88, 279.88) * mm});
            skLineSegment(sketch, "E3476", {"start": v(604.88, 279.88) * mm, "end": v(601.87, 279.25) * mm});
            skLineSegment(sketch, "E3477", {"start": v(601.87, 279.25) * mm, "end": v(599.23, 278.55) * mm});
            skLineSegment(sketch, "E3478", {"start": v(599.23, 278.55) * mm, "end": v(596.8, 277.78) * mm});
            skLineSegment(sketch, "E3479", {"start": v(596.8, 277.78) * mm, "end": v(594.45, 276.94) * mm});
            skLineSegment(sketch, "E3480", {"start": v(594.45, 276.94) * mm, "end": v(592.02, 276.03) * mm});
            skLineSegment(sketch, "E3481", {"start": v(592.02, 276.03) * mm, "end": v(589.37, 275.04) * mm});
            skLineSegment(sketch, "E3482", {"start": v(589.37, 275.04) * mm, "end": v(586.35, 273.98) * mm});
            skLineSegment(sketch, "E3483", {"start": v(586.35, 273.98) * mm, "end": v(582.82, 272.85) * mm});
            skLineSegment(sketch, "E3484", {"start": v(582.82, 272.85) * mm, "end": v(578.63, 271.65) * mm});
            skLineSegment(sketch, "E3485", {"start": v(578.63, 271.65) * mm, "end": v(573.62, 270.38) * mm});
            skLineSegment(sketch, "E3486", {"start": v(573.62, 270.38) * mm, "end": v(567.66, 269.04) * mm});
            skLineSegment(sketch, "E3487", {"start": v(567.66, 269.04) * mm, "end": v(560.6, 267.62) * mm});
            skLineSegment(sketch, "E3488", {"start": v(560.6, 267.62) * mm, "end": v(552.3, 266.14) * mm});
            skLineSegment(sketch, "E3489", {"start": v(552.3, 266.14) * mm, "end": v(542.59, 264.58) * mm});
            skLineSegment(sketch, "E3490", {"start": v(542.59, 264.58) * mm, "end": v(534.15, 263.35) * mm});
            skLineSegment(sketch, "E3491", {"start": v(534.15, 263.35) * mm, "end": v(531.34, 262.96) * mm});
            skLineSegment(sketch, "E3492", {"start": v(531.34, 262.96) * mm, "end": v(529.53, 262.71) * mm});
            skLineSegment(sketch, "E3493", {"start": v(529.53, 262.71) * mm, "end": v(524.03, 262.47) * mm});
            skLineSegment(sketch, "E3494", {"start": v(524.03, 262.47) * mm, "end": v(516.4, 262.95) * mm});
            skLineSegment(sketch, "E3495", {"start": v(516.4, 262.95) * mm, "end": v(508.44, 264.38) * mm});
            skLineSegment(sketch, "E3496", {"start": v(508.44, 264.38) * mm, "end": v(500.15, 266.72) * mm});
            skLineSegment(sketch, "E3497", {"start": v(500.15, 266.72) * mm, "end": v(491.53, 269.95) * mm});
            skLineSegment(sketch, "E3498", {"start": v(491.53, 269.95) * mm, "end": v(482.6, 274.05) * mm});
            skLineSegment(sketch, "E3499", {"start": v(482.6, 274.05) * mm, "end": v(473.33, 279) * mm});
            skLineSegment(sketch, "E3500", {"start": v(473.33, 279) * mm, "end": v(463.73, 284.75) * mm});
            skLineSegment(sketch, "E3501", {"start": v(463.73, 284.75) * mm, "end": v(453.81, 291.3) * mm});
            skLineSegment(sketch, "E3502", {"start": v(453.81, 291.3) * mm, "end": v(443.56, 298.6) * mm});
            skLineSegment(sketch, "E3503", {"start": v(443.56, 298.6) * mm, "end": v(432.99, 306.65) * mm});
            skLineSegment(sketch, "E3504", {"start": v(432.99, 306.65) * mm, "end": v(422.08, 315.4) * mm});
            skLineSegment(sketch, "E3505", {"start": v(422.08, 315.4) * mm, "end": v(410.85, 324.85) * mm});
            skLineSegment(sketch, "E3506", {"start": v(410.85, 324.85) * mm, "end": v(399.3, 334.96) * mm});
            skLineSegment(sketch, "E3507", {"start": v(399.3, 334.96) * mm, "end": v(387.41, 345.7) * mm});
            skLineSegment(sketch, "E3508", {"start": v(387.41, 345.7) * mm, "end": v(378.24, 354.18) * mm});
            skLineSegment(sketch, "E3509", {"start": v(378.24, 354.18) * mm, "end": v(375.2, 357.04) * mm});
            skLineSegment(sketch, "E3510", {"start": v(375.2, 357.04) * mm, "end": v(373.62, 358.52) * mm});
            skLineSegment(sketch, "E3511", {"start": v(373.62, 358.52) * mm, "end": v(368.82, 362.94) * mm});
            skLineSegment(sketch, "E3512", {"start": v(368.82, 362.94) * mm, "end": v(362.16, 368.92) * mm});
            skLineSegment(sketch, "E3513", {"start": v(362.16, 368.92) * mm, "end": v(355.2, 375) * mm});
            skLineSegment(sketch, "E3514", {"start": v(355.2, 375) * mm, "end": v(348, 381.1) * mm});
            skLineSegment(sketch, "E3515", {"start": v(348, 381.1) * mm, "end": v(340.54, 387.26) * mm});
            skLineSegment(sketch, "E3516", {"start": v(340.54, 387.26) * mm, "end": v(332.85, 393.44) * mm});
            skLineSegment(sketch, "E3517", {"start": v(332.85, 393.44) * mm, "end": v(324.95, 399.63) * mm});
            skLineSegment(sketch, "E3518", {"start": v(324.95, 399.63) * mm, "end": v(316.85, 405.8) * mm});
            skLineSegment(sketch, "E3519", {"start": v(316.85, 405.8) * mm, "end": v(308.57, 411.94) * mm});
            skLineSegment(sketch, "E3520", {"start": v(308.57, 411.94) * mm, "end": v(300.13, 418.04) * mm});
            skLineSegment(sketch, "E3521", {"start": v(300.13, 418.04) * mm, "end": v(291.54, 424.07) * mm});
            skLineSegment(sketch, "E3522", {"start": v(291.54, 424.07) * mm, "end": v(282.83, 430.02) * mm});
            skLineSegment(sketch, "E3523", {"start": v(282.83, 430.02) * mm, "end": v(274, 435.87) * mm});
            skLineSegment(sketch, "E3524", {"start": v(274, 435.87) * mm, "end": v(265.07, 441.61) * mm});
            skLineSegment(sketch, "E3525", {"start": v(265.07, 441.61) * mm, "end": v(256.06, 447.23) * mm});
            skLineSegment(sketch, "E3526", {"start": v(256.06, 447.23) * mm, "end": v(247, 452.69) * mm});
            skLineSegment(sketch, "E3527", {"start": v(247, 452.69) * mm, "end": v(237.87, 457.98) * mm});
            skLineSegment(sketch, "E3528", {"start": v(237.87, 457.98) * mm, "end": v(228.72, 463.1) * mm});
            skLineSegment(sketch, "E3529", {"start": v(228.72, 463.1) * mm, "end": v(219.56, 468) * mm});
            skLineSegment(sketch, "E3530", {"start": v(219.56, 468) * mm, "end": v(210.4, 472.7) * mm});
            skLineSegment(sketch, "E3531", {"start": v(210.4, 472.7) * mm, "end": v(201.26, 477.17) * mm});
            skLineSegment(sketch, "E3532", {"start": v(201.26, 477.17) * mm, "end": v(192.16, 481.4) * mm});
            skLineSegment(sketch, "E3533", {"start": v(192.16, 481.4) * mm, "end": v(183.11, 485.34) * mm});
            skLineSegment(sketch, "E3534", {"start": v(183.11, 485.34) * mm, "end": v(174.13, 489) * mm});
            skLineSegment(sketch, "E3535", {"start": v(174.13, 489) * mm, "end": v(165.24, 492.37) * mm});
            skLineSegment(sketch, "E3536", {"start": v(165.24, 492.37) * mm, "end": v(156.45, 495.41) * mm});
            skLineSegment(sketch, "E3537", {"start": v(156.45, 495.41) * mm, "end": v(147.78, 498.13) * mm});
            skLineSegment(sketch, "E3538", {"start": v(147.78, 498.13) * mm, "end": v(139.24, 500.48) * mm});
            skLineSegment(sketch, "E3539", {"start": v(139.24, 500.48) * mm, "end": v(130.86, 502.47) * mm});
            skLineSegment(sketch, "E3540", {"start": v(130.86, 502.47) * mm, "end": v(122.65, 504.08) * mm});
            skLineSegment(sketch, "E3541", {"start": v(122.65, 504.08) * mm, "end": v(114.62, 505.28) * mm});
            skLineSegment(sketch, "E3542", {"start": v(114.62, 505.28) * mm, "end": v(108.76, 505.92) * mm});
            skLineSegment(sketch, "E3543", {"start": v(108.76, 505.92) * mm, "end": v(106.8, 506.06) * mm});
            skLineSegment(sketch, "E3544", {"start": v(106.8, 506.06) * mm, "end": v(102.5, 506.37) * mm});
            skLineSegment(sketch, "E3545", {"start": v(102.5, 506.37) * mm, "end": v(89.58, 506.93) * mm});
            skLineSegment(sketch, "E3546", {"start": v(89.58, 506.93) * mm, "end": v(73.07, 507.01) * mm});
            skLineSegment(sketch, "E3547", {"start": v(73.07, 507.01) * mm, "end": v(57.2, 506.4) * mm});
            skLineSegment(sketch, "E3548", {"start": v(57.2, 506.4) * mm, "end": v(41.9, 505.18) * mm});
            skLineSegment(sketch, "E3549", {"start": v(41.9, 505.18) * mm, "end": v(27.1, 503.45) * mm});
            skLineSegment(sketch, "E3550", {"start": v(27.1, 503.45) * mm, "end": v(12.73, 501.28) * mm});
            skLineSegment(sketch, "E3551", {"start": v(12.73, 501.28) * mm, "end": v(-1.25, 498.77) * mm});
            skLineSegment(sketch, "E3552", {"start": v(-1.25, 498.77) * mm, "end": v(-14.93, 496.02) * mm});
            skLineSegment(sketch, "E3553", {"start": v(-14.93, 496.02) * mm, "end": v(-28.38, 493.09) * mm});
            skLineSegment(sketch, "E3554", {"start": v(-28.38, 493.09) * mm, "end": v(-41.65, 490.1) * mm});
            skLineSegment(sketch, "E3555", {"start": v(-41.65, 490.1) * mm, "end": v(-54.82, 487.1) * mm});
            skLineSegment(sketch, "E3556", {"start": v(-54.82, 487.1) * mm, "end": v(-67.95, 484.21) * mm});
            skLineSegment(sketch, "E3557", {"start": v(-67.95, 484.21) * mm, "end": v(-81.11, 481.51) * mm});
            skLineSegment(sketch, "E3558", {"start": v(-81.11, 481.51) * mm, "end": v(-94.36, 479.08) * mm});
            skLineSegment(sketch, "E3559", {"start": v(-94.36, 479.08) * mm, "end": v(-107.79, 477.03) * mm});
            skLineSegment(sketch, "E3560", {"start": v(-107.79, 477.03) * mm, "end": v(-118.01, 475.76) * mm});
            skLineSegment(sketch, "E3561", {"start": v(-118.01, 475.76) * mm, "end": v(-121.43, 475.42) * mm});
            skLineSegment(sketch, "E3562", {"start": v(-121.43, 475.42) * mm, "end": v(-124.72, 475.1) * mm});
            skLineSegment(sketch, "E3563", {"start": v(-124.72, 475.1) * mm, "end": v(-134.58, 474) * mm});
            skLineSegment(sketch, "E3564", {"start": v(-134.58, 474) * mm, "end": v(-146.77, 472.48) * mm});
            skLineSegment(sketch, "E3565", {"start": v(-146.77, 472.48) * mm, "end": v(-158.1, 470.88) * mm});
            skLineSegment(sketch, "E3566", {"start": v(-158.1, 470.88) * mm, "end": v(-168.66, 469.27) * mm});
            skLineSegment(sketch, "E3567", {"start": v(-168.66, 469.27) * mm, "end": v(-178.56, 467.7) * mm});
            skLineSegment(sketch, "E3568", {"start": v(-178.56, 467.7) * mm, "end": v(-187.9, 466.23) * mm});
            skLineSegment(sketch, "E3569", {"start": v(-187.9, 466.23) * mm, "end": v(-196.8, 464.9) * mm});
            skLineSegment(sketch, "E3570", {"start": v(-196.8, 464.9) * mm, "end": v(-205.35, 463.78) * mm});
            skLineSegment(sketch, "E3571", {"start": v(-205.35, 463.78) * mm, "end": v(-213.65, 462.92) * mm});
            skLineSegment(sketch, "E3572", {"start": v(-213.65, 462.92) * mm, "end": v(-221.8, 462.36) * mm});
            skLineSegment(sketch, "E3573", {"start": v(-221.8, 462.36) * mm, "end": v(-229.9, 462.17) * mm});
            skLineSegment(sketch, "E3574", {"start": v(-229.9, 462.17) * mm, "end": v(-238.07, 462.39) * mm});
            skLineSegment(sketch, "E3575", {"start": v(-238.07, 462.39) * mm, "end": v(-246.4, 463.07) * mm});
            skLineSegment(sketch, "E3576", {"start": v(-246.4, 463.07) * mm, "end": v(-255, 464.28) * mm});
            skLineSegment(sketch, "E3577", {"start": v(-255, 464.28) * mm, "end": v(-263.96, 466.07) * mm});
            skLineSegment(sketch, "E3578", {"start": v(-263.96, 466.07) * mm, "end": v(-271.05, 467.82) * mm});
            skLineSegment(sketch, "E3579", {"start": v(-271.05, 467.82) * mm, "end": v(-273.39, 468.49) * mm});
            skLineSegment(sketch, "E3580", {"start": v(-273.39, 468.49) * mm, "end": v(-274.08, 468.68) * mm});
            skLineSegment(sketch, "E3581", {"start": v(-274.08, 468.68) * mm, "end": v(-276.18, 469.25) * mm});
            skLineSegment(sketch, "E3582", {"start": v(-276.18, 469.25) * mm, "end": v(-279.54, 470.13) * mm});
            skLineSegment(sketch, "E3583", {"start": v(-279.54, 470.13) * mm, "end": v(-283.41, 471.1) * mm});
            skLineSegment(sketch, "E3584", {"start": v(-283.41, 471.1) * mm, "end": v(-287.73, 472.14) * mm});
            skLineSegment(sketch, "E3585", {"start": v(-287.73, 472.14) * mm, "end": v(-292.4, 473.23) * mm});
            skLineSegment(sketch, "E3586", {"start": v(-292.4, 473.23) * mm, "end": v(-297.39, 474.36) * mm});
            skLineSegment(sketch, "E3587", {"start": v(-297.39, 474.36) * mm, "end": v(-302.6, 475.5) * mm});
            skLineSegment(sketch, "E3588", {"start": v(-302.6, 475.5) * mm, "end": v(-307.96, 476.65) * mm});
            skLineSegment(sketch, "E3589", {"start": v(-307.96, 476.65) * mm, "end": v(-313.42, 477.77) * mm});
            skLineSegment(sketch, "E3590", {"start": v(-313.42, 477.77) * mm, "end": v(-318.9, 478.84) * mm});
            skLineSegment(sketch, "E3591", {"start": v(-318.9, 478.84) * mm, "end": v(-324.32, 479.86) * mm});
            skLineSegment(sketch, "E3592", {"start": v(-324.32, 479.86) * mm, "end": v(-329.62, 480.78) * mm});
            skLineSegment(sketch, "E3593", {"start": v(-329.62, 480.78) * mm, "end": v(-334.74, 481.62) * mm});
            skLineSegment(sketch, "E3594", {"start": v(-334.74, 481.62) * mm, "end": v(-339.6, 482.33) * mm});
            skLineSegment(sketch, "E3595", {"start": v(-339.6, 482.33) * mm, "end": v(-344.12, 482.9) * mm});
            skLineSegment(sketch, "E3596", {"start": v(-344.12, 482.9) * mm, "end": v(-347.21, 483.22) * mm});
            skLineSegment(sketch, "E3597", {"start": v(-347.21, 483.22) * mm, "end": v(-348.25, 483.3) * mm});
            skLineSegment(sketch, "E3598", {"start": v(-348.25, 483.3) * mm, "end": v(-350.52, 483.5) * mm});
            skLineSegment(sketch, "E3599", {"start": v(-350.52, 483.5) * mm, "end": v(-357.37, 483.87) * mm});
            skLineSegment(sketch, "E3600", {"start": v(-357.37, 483.87) * mm, "end": v(-365.52, 484.05) * mm});
            skLineSegment(sketch, "E3601", {"start": v(-365.52, 484.05) * mm, "end": v(-373, 484) * mm});
            skLineSegment(sketch, "E3602", {"start": v(-373, 484) * mm, "end": v(-380.12, 483.86) * mm});
            skLineSegment(sketch, "E3603", {"start": v(-380.12, 483.86) * mm, "end": v(-387.2, 483.8) * mm});
            skLineSegment(sketch, "E3604", {"start": v(-387.2, 483.8) * mm, "end": v(-394.5, 483.96) * mm});
            skLineSegment(sketch, "E3605", {"start": v(-394.5, 483.96) * mm, "end": v(-402.37, 484.5) * mm});
            skLineSegment(sketch, "E3606", {"start": v(-402.37, 484.5) * mm, "end": v(-408.92, 485.26) * mm});
            skLineSegment(sketch, "E3607", {"start": v(-408.92, 485.26) * mm, "end": v(-411.1, 485.58) * mm});
            skLineSegment(sketch, "E3608", {"start": v(-411.1, 485.58) * mm, "end": v(-411.85, 485.7) * mm});
            skLineSegment(sketch, "E3609", {"start": v(-411.85, 485.7) * mm, "end": v(-414.13, 486.06) * mm});
            skLineSegment(sketch, "E3610", {"start": v(-414.13, 486.06) * mm, "end": v(-417.76, 486.66) * mm});
            skLineSegment(sketch, "E3611", {"start": v(-417.76, 486.66) * mm, "end": v(-421.96, 487.37) * mm});
            skLineSegment(sketch, "E3612", {"start": v(-421.96, 487.37) * mm, "end": v(-426.67, 488.2) * mm});
            skLineSegment(sketch, "E3613", {"start": v(-426.67, 488.2) * mm, "end": v(-431.85, 489.1) * mm});
            skLineSegment(sketch, "E3614", {"start": v(-431.85, 489.1) * mm, "end": v(-437.45, 490.1) * mm});
            skLineSegment(sketch, "E3615", {"start": v(-437.45, 490.1) * mm, "end": v(-443.43, 491.2) * mm});
            skLineSegment(sketch, "E3616", {"start": v(-443.43, 491.2) * mm, "end": v(-449.74, 492.35) * mm});
            skLineSegment(sketch, "E3617", {"start": v(-449.74, 492.35) * mm, "end": v(-456.33, 493.55) * mm});
            skLineSegment(sketch, "E3618", {"start": v(-456.33, 493.55) * mm, "end": v(-463.16, 494.82) * mm});
            skLineSegment(sketch, "E3619", {"start": v(-463.16, 494.82) * mm, "end": v(-470.18, 496.12) * mm});
            skLineSegment(sketch, "E3620", {"start": v(-470.18, 496.12) * mm, "end": v(-477.35, 497.46) * mm});
            skLineSegment(sketch, "E3621", {"start": v(-477.35, 497.46) * mm, "end": v(-484.62, 498.82) * mm});
            skLineSegment(sketch, "E3622", {"start": v(-484.62, 498.82) * mm, "end": v(-491.94, 500.2) * mm});
            skLineSegment(sketch, "E3623", {"start": v(-491.94, 500.2) * mm, "end": v(-499.26, 501.57) * mm});
            skLineSegment(sketch, "E3624", {"start": v(-499.26, 501.57) * mm, "end": v(-506.55, 502.95) * mm});
            skLineSegment(sketch, "E3625", {"start": v(-506.55, 502.95) * mm, "end": v(-513.76, 504.31) * mm});
            skLineSegment(sketch, "E3626", {"start": v(-513.76, 504.31) * mm, "end": v(-520.83, 505.66) * mm});
            skLineSegment(sketch, "E3627", {"start": v(-520.83, 505.66) * mm, "end": v(-527.73, 506.97) * mm});
            skLineSegment(sketch, "E3628", {"start": v(-527.73, 506.97) * mm, "end": v(-534.4, 508.24) * mm});
            skLineSegment(sketch, "E3629", {"start": v(-534.4, 508.24) * mm, "end": v(-540.8, 509.46) * mm});
            skLineSegment(sketch, "E3630", {"start": v(-540.8, 509.46) * mm, "end": v(-546.9, 510.63) * mm});
            skLineSegment(sketch, "E3631", {"start": v(-546.9, 510.63) * mm, "end": v(-552.62, 511.72) * mm});
            skLineSegment(sketch, "E3632", {"start": v(-552.62, 511.72) * mm, "end": v(-557.94, 512.74) * mm});
            skLineSegment(sketch, "E3633", {"start": v(-557.94, 512.74) * mm, "end": v(-562.81, 513.68) * mm});
            skLineSegment(sketch, "E3634", {"start": v(-562.81, 513.68) * mm, "end": v(-567.18, 514.51) * mm});
            skLineSegment(sketch, "E3635", {"start": v(-567.18, 514.51) * mm, "end": v(-571, 515.25) * mm});
            skLineSegment(sketch, "E3636", {"start": v(-571, 515.25) * mm, "end": v(-574.23, 515.87) * mm});
            skLineSegment(sketch, "E3637", {"start": v(-574.23, 515.87) * mm, "end": v(-576.83, 516.37) * mm});
            skLineSegment(sketch, "E3638", {"start": v(-576.83, 516.37) * mm, "end": v(-578.73, 516.73) * mm});
            skLineSegment(sketch, "E3639", {"start": v(-578.73, 516.73) * mm, "end": v(-579.91, 516.97) * mm});
            skLineSegment(sketch, "E3640", {"start": v(-579.91, 516.97) * mm, "end": v(-580.32, 517.04) * mm});
            skLineSegment(sketch, "E3641", {"start": v(608.4, 99.62) * mm, "end": v(608.35, 99.55) * mm});
            skLineSegment(sketch, "E3642", {"start": v(608.35, 99.55) * mm, "end": v(608.14, 99.36) * mm});
            skLineSegment(sketch, "E3643", {"start": v(608.14, 99.36) * mm, "end": v(607.64, 99.08) * mm});
            skLineSegment(sketch, "E3644", {"start": v(607.64, 99.08) * mm, "end": v(606.74, 98.72) * mm});
            skLineSegment(sketch, "E3645", {"start": v(606.74, 98.72) * mm, "end": v(605.3, 98.34) * mm});
            skLineSegment(sketch, "E3646", {"start": v(605.3, 98.34) * mm, "end": v(603.24, 97.95) * mm});
            skLineSegment(sketch, "E3647", {"start": v(603.24, 97.95) * mm, "end": v(600.4, 97.57) * mm});
            skLineSegment(sketch, "E3648", {"start": v(600.4, 97.57) * mm, "end": v(596.7, 97.23) * mm});
            skLineSegment(sketch, "E3649", {"start": v(596.7, 97.23) * mm, "end": v(591.98, 96.98) * mm});
            skLineSegment(sketch, "E3650", {"start": v(591.98, 96.98) * mm, "end": v(586.16, 96.82) * mm});
            skLineSegment(sketch, "E3651", {"start": v(586.16, 96.82) * mm, "end": v(579.1, 96.8) * mm});
            skLineSegment(sketch, "E3652", {"start": v(579.1, 96.8) * mm, "end": v(570.68, 96.94) * mm});
            skLineSegment(sketch, "E3653", {"start": v(570.68, 96.94) * mm, "end": v(560.8, 97.26) * mm});
            skLineSegment(sketch, "E3654", {"start": v(560.8, 97.26) * mm, "end": v(549.3, 97.8) * mm});
            skLineSegment(sketch, "E3655", {"start": v(549.3, 97.8) * mm, "end": v(536.12, 98.57) * mm});
            skLineSegment(sketch, "E3656", {"start": v(536.12, 98.57) * mm, "end": v(524.85, 99.34) * mm});
            skLineSegment(sketch, "E3657", {"start": v(524.85, 99.34) * mm, "end": v(521.1, 99.62) * mm});
            skLineSegment(sketch, "E3658", {"start": v(521.1, 99.62) * mm, "end": v(517.16, 99.92) * mm});
            skLineSegment(sketch, "E3659", {"start": v(517.16, 99.92) * mm, "end": v(505.38, 101.33) * mm});
            skLineSegment(sketch, "E3660", {"start": v(505.38, 101.33) * mm, "end": v(490.17, 104) * mm});
            skLineSegment(sketch, "E3661", {"start": v(490.17, 104) * mm, "end": v(475.53, 107.5) * mm});
            skLineSegment(sketch, "E3662", {"start": v(475.53, 107.5) * mm, "end": v(461.46, 111.72) * mm});
            skLineSegment(sketch, "E3663", {"start": v(461.46, 111.72) * mm, "end": v(448.01, 116.56) * mm});
            skLineSegment(sketch, "E3664", {"start": v(448.01, 116.56) * mm, "end": v(435.2, 121.9) * mm});
            skLineSegment(sketch, "E3665", {"start": v(435.2, 121.9) * mm, "end": v(423.06, 127.64) * mm});
            skLineSegment(sketch, "E3666", {"start": v(423.06, 127.64) * mm, "end": v(411.63, 133.65) * mm});
            skLineSegment(sketch, "E3667", {"start": v(411.63, 133.65) * mm, "end": v(400.93, 139.81) * mm});
            skLineSegment(sketch, "E3668", {"start": v(400.93, 139.81) * mm, "end": v(391, 146.03) * mm});
            skLineSegment(sketch, "E3669", {"start": v(391, 146.03) * mm, "end": v(381.85, 152.19) * mm});
            skLineSegment(sketch, "E3670", {"start": v(381.85, 152.19) * mm, "end": v(373.52, 158.17) * mm});
            skLineSegment(sketch, "E3671", {"start": v(373.52, 158.17) * mm, "end": v(366.05, 163.85) * mm});
            skLineSegment(sketch, "E3672", {"start": v(366.05, 163.85) * mm, "end": v(359.46, 169.14) * mm});
            skLineSegment(sketch, "E3673", {"start": v(359.46, 169.14) * mm, "end": v(353.8, 173.9) * mm});
            skLineSegment(sketch, "E3674", {"start": v(353.8, 173.9) * mm, "end": v(350.23, 177) * mm});
            skLineSegment(sketch, "E3675", {"start": v(350.23, 177) * mm, "end": v(349.06, 178.05) * mm});
            skLineSegment(sketch, "E3676", {"start": v(349.06, 178.05) * mm, "end": v(347.93, 179.05) * mm});
            skLineSegment(sketch, "E3677", {"start": v(347.93, 179.05) * mm, "end": v(344.61, 182.13) * mm});
            skLineSegment(sketch, "E3678", {"start": v(344.61, 182.13) * mm, "end": v(339.76, 186.8) * mm});
            skLineSegment(sketch, "E3679", {"start": v(339.76, 186.8) * mm, "end": v(334.5, 192.06) * mm});
            skLineSegment(sketch, "E3680", {"start": v(334.5, 192.06) * mm, "end": v(328.8, 197.87) * mm});
            skLineSegment(sketch, "E3681", {"start": v(328.8, 197.87) * mm, "end": v(322.68, 204.24) * mm});
            skLineSegment(sketch, "E3682", {"start": v(322.68, 204.24) * mm, "end": v(316.11, 211.14) * mm});
            skLineSegment(sketch, "E3683", {"start": v(316.11, 211.14) * mm, "end": v(309.1, 218.58) * mm});
            skLineSegment(sketch, "E3684", {"start": v(309.1, 218.58) * mm, "end": v(301.61, 226.54) * mm});
            skLineSegment(sketch, "E3685", {"start": v(301.61, 226.54) * mm, "end": v(293.66, 235) * mm});
            skLineSegment(sketch, "E3686", {"start": v(293.66, 235) * mm, "end": v(285.23, 243.95) * mm});
            skLineSegment(sketch, "E3687", {"start": v(285.23, 243.95) * mm, "end": v(276.3, 253.4) * mm});
            skLineSegment(sketch, "E3688", {"start": v(276.3, 253.4) * mm, "end": v(266.88, 263.3) * mm});
            skLineSegment(sketch, "E3689", {"start": v(266.88, 263.3) * mm, "end": v(256.94, 273.67) * mm});
            skLineSegment(sketch, "E3690", {"start": v(256.94, 273.67) * mm, "end": v(246.48, 284.5) * mm});
            skLineSegment(sketch, "E3691", {"start": v(246.48, 284.5) * mm, "end": v(235.5, 295.74) * mm});
            skLineSegment(sketch, "E3692", {"start": v(235.5, 295.74) * mm, "end": v(226.86, 304.52) * mm});
            skLineSegment(sketch, "E3693", {"start": v(226.86, 304.52) * mm, "end": v(223.97, 307.43) * mm});
            skLineSegment(sketch, "E3694", {"start": v(223.97, 307.43) * mm, "end": v(221.1, 310.31) * mm});
            skLineSegment(sketch, "E3695", {"start": v(221.1, 310.31) * mm, "end": v(212.32, 318.76) * mm});
            skLineSegment(sketch, "E3696", {"start": v(212.32, 318.76) * mm, "end": v(200.95, 329.02) * mm});
            skLineSegment(sketch, "E3697", {"start": v(200.95, 329.02) * mm, "end": v(189.85, 338.25) * mm});
            skLineSegment(sketch, "E3698", {"start": v(189.85, 338.25) * mm, "end": v(178.99, 346.52) * mm});
            skLineSegment(sketch, "E3699", {"start": v(178.99, 346.52) * mm, "end": v(168.34, 353.87) * mm});
            skLineSegment(sketch, "E3700", {"start": v(168.34, 353.87) * mm, "end": v(157.89, 360.35) * mm});
            skLineSegment(sketch, "E3701", {"start": v(157.89, 360.35) * mm, "end": v(147.62, 366.03) * mm});
            skLineSegment(sketch, "E3702", {"start": v(147.62, 366.03) * mm, "end": v(137.5, 370.95) * mm});
            skLineSegment(sketch, "E3703", {"start": v(137.5, 370.95) * mm, "end": v(127.51, 375.18) * mm});
            skLineSegment(sketch, "E3704", {"start": v(127.51, 375.18) * mm, "end": v(117.63, 378.75) * mm});
            skLineSegment(sketch, "E3705", {"start": v(117.63, 378.75) * mm, "end": v(107.85, 381.72) * mm});
            skLineSegment(sketch, "E3706", {"start": v(107.85, 381.72) * mm, "end": v(98.12, 384.16) * mm});
            skLineSegment(sketch, "E3707", {"start": v(98.12, 384.16) * mm, "end": v(88.45, 386.1) * mm});
            skLineSegment(sketch, "E3708", {"start": v(88.45, 386.1) * mm, "end": v(78.8, 387.62) * mm});
            skLineSegment(sketch, "E3709", {"start": v(78.8, 387.62) * mm, "end": v(69.15, 388.74) * mm});
            skLineSegment(sketch, "E3710", {"start": v(69.15, 388.74) * mm, "end": v(61.9, 389.38) * mm});
            skLineSegment(sketch, "E3711", {"start": v(61.9, 389.38) * mm, "end": v(59.48, 389.54) * mm});
            skLineSegment(sketch, "E3712", {"start": v(59.48, 389.54) * mm, "end": v(57.53, 389.68) * mm});
            skLineSegment(sketch, "E3713", {"start": v(57.53, 389.68) * mm, "end": v(51.7, 389.9) * mm});
            skLineSegment(sketch, "E3714", {"start": v(51.7, 389.9) * mm, "end": v(43.85, 389.93) * mm});
            skLineSegment(sketch, "E3715", {"start": v(43.85, 389.93) * mm, "end": v(35.96, 389.66) * mm});
            skLineSegment(sketch, "E3716", {"start": v(35.96, 389.66) * mm, "end": v(28.05, 389.1) * mm});
            skLineSegment(sketch, "E3717", {"start": v(28.05, 389.1) * mm, "end": v(20.13, 388.28) * mm});
            skLineSegment(sketch, "E3718", {"start": v(20.13, 388.28) * mm, "end": v(12.21, 387.22) * mm});
            skLineSegment(sketch, "E3719", {"start": v(12.21, 387.22) * mm, "end": v(4.3, 385.94) * mm});
            skLineSegment(sketch, "E3720", {"start": v(4.3, 385.94) * mm, "end": v(-3.55, 384.45) * mm});
            skLineSegment(sketch, "E3721", {"start": v(-3.55, 384.45) * mm, "end": v(-11.37, 382.78) * mm});
            skLineSegment(sketch, "E3722", {"start": v(-11.37, 382.78) * mm, "end": v(-19.12, 380.94) * mm});
            skLineSegment(sketch, "E3723", {"start": v(-19.12, 380.94) * mm, "end": v(-26.8, 378.97) * mm});
            skLineSegment(sketch, "E3724", {"start": v(-26.8, 378.97) * mm, "end": v(-34.38, 376.88) * mm});
            skLineSegment(sketch, "E3725", {"start": v(-34.38, 376.88) * mm, "end": v(-41.86, 374.68) * mm});
            skLineSegment(sketch, "E3726", {"start": v(-41.86, 374.68) * mm, "end": v(-49.2, 372.4) * mm});
            skLineSegment(sketch, "E3727", {"start": v(-49.2, 372.4) * mm, "end": v(-56.42, 370.07) * mm});
            skLineSegment(sketch, "E3728", {"start": v(-56.42, 370.07) * mm, "end": v(-63.47, 367.7) * mm});
            skLineSegment(sketch, "E3729", {"start": v(-63.47, 367.7) * mm, "end": v(-70.36, 365.3) * mm});
            skLineSegment(sketch, "E3730", {"start": v(-70.36, 365.3) * mm, "end": v(-77.06, 362.9) * mm});
            skLineSegment(sketch, "E3731", {"start": v(-77.06, 362.9) * mm, "end": v(-83.57, 360.52) * mm});
            skLineSegment(sketch, "E3732", {"start": v(-83.57, 360.52) * mm, "end": v(-89.86, 358.19) * mm});
            skLineSegment(sketch, "E3733", {"start": v(-89.86, 358.19) * mm, "end": v(-95.93, 355.91) * mm});
            skLineSegment(sketch, "E3734", {"start": v(-95.93, 355.91) * mm, "end": v(-101.75, 353.72) * mm});
            skLineSegment(sketch, "E3735", {"start": v(-101.75, 353.72) * mm, "end": v(-107.31, 351.63) * mm});
            skLineSegment(sketch, "E3736", {"start": v(-107.31, 351.63) * mm, "end": v(-112.6, 349.66) * mm});
            skLineSegment(sketch, "E3737", {"start": v(-112.6, 349.66) * mm, "end": v(-117.6, 347.83) * mm});
            skLineSegment(sketch, "E3738", {"start": v(-117.6, 347.83) * mm, "end": v(-122.3, 346.17) * mm});
            skLineSegment(sketch, "E3739", {"start": v(-122.3, 346.17) * mm, "end": v(-126.68, 344.68) * mm});
            skLineSegment(sketch, "E3740", {"start": v(-126.68, 344.68) * mm, "end": v(-130.72, 343.4) * mm});
            skLineSegment(sketch, "E3741", {"start": v(-130.72, 343.4) * mm, "end": v(-134.41, 342.35) * mm});
            skLineSegment(sketch, "E3742", {"start": v(-134.41, 342.35) * mm, "end": v(-137.75, 341.54) * mm});
            skLineSegment(sketch, "E3743", {"start": v(-137.75, 341.54) * mm, "end": v(-140.7, 341) * mm});
            skLineSegment(sketch, "E3744", {"start": v(-140.7, 341) * mm, "end": v(-142.62, 340.76) * mm});
            skLineSegment(sketch, "E3745", {"start": v(-142.62, 340.76) * mm, "end": v(-143.26, 340.73) * mm});
            skLineSegment(sketch, "E3746", {"start": v(-143.26, 340.73) * mm, "end": v(-144.64, 340.66) * mm});
            skLineSegment(sketch, "E3747", {"start": v(-144.64, 340.66) * mm, "end": v(-148.8, 340.63) * mm});
            skLineSegment(sketch, "E3748", {"start": v(-148.8, 340.63) * mm, "end": v(-155.87, 340.78) * mm});
            skLineSegment(sketch, "E3749", {"start": v(-155.87, 340.78) * mm, "end": v(-164.27, 341.16) * mm});
            skLineSegment(sketch, "E3750", {"start": v(-164.27, 341.16) * mm, "end": v(-173.78, 341.76) * mm});
            skLineSegment(sketch, "E3751", {"start": v(-173.78, 341.76) * mm, "end": v(-184.22, 342.56) * mm});
            skLineSegment(sketch, "E3752", {"start": v(-184.22, 342.56) * mm, "end": v(-195.39, 343.55) * mm});
            skLineSegment(sketch, "E3753", {"start": v(-195.39, 343.55) * mm, "end": v(-207.08, 344.7) * mm});
            skLineSegment(sketch, "E3754", {"start": v(-207.08, 344.7) * mm, "end": v(-219.1, 346) * mm});
            skLineSegment(sketch, "E3755", {"start": v(-219.1, 346) * mm, "end": v(-231.24, 347.43) * mm});
            skLineSegment(sketch, "E3756", {"start": v(-231.24, 347.43) * mm, "end": v(-243.3, 348.98) * mm});
            skLineSegment(sketch, "E3757", {"start": v(-243.3, 348.98) * mm, "end": v(-255.1, 350.63) * mm});
            skLineSegment(sketch, "E3758", {"start": v(-255.1, 350.63) * mm, "end": v(-266.42, 352.37) * mm});
            skLineSegment(sketch, "E3759", {"start": v(-266.42, 352.37) * mm, "end": v(-277.08, 354.17) * mm});
            skLineSegment(sketch, "E3760", {"start": v(-277.08, 354.17) * mm, "end": v(-286.86, 356.02) * mm});
            skLineSegment(sketch, "E3761", {"start": v(-286.86, 356.02) * mm, "end": v(-295.56, 357.9) * mm});
            skLineSegment(sketch, "E3762", {"start": v(-295.56, 357.9) * mm, "end": v(-301.15, 359.29) * mm});
            skLineSegment(sketch, "E3763", {"start": v(-301.15, 359.29) * mm, "end": v(-303, 359.8) * mm});
            skLineSegment(sketch, "E3764", {"start": v(-303, 359.8) * mm, "end": v(-304.25, 360.17) * mm});
            skLineSegment(sketch, "E3765", {"start": v(-304.25, 360.17) * mm, "end": v(-307.97, 361.36) * mm});
            skLineSegment(sketch, "E3766", {"start": v(-307.97, 361.36) * mm, "end": v(-313.06, 363.13) * mm});
            skLineSegment(sketch, "E3767", {"start": v(-313.06, 363.13) * mm, "end": v(-318.32, 365.03) * mm});
            skLineSegment(sketch, "E3768", {"start": v(-318.32, 365.03) * mm, "end": v(-323.86, 366.93) * mm});
            skLineSegment(sketch, "E3769", {"start": v(-323.86, 366.93) * mm, "end": v(-329.76, 368.74) * mm});
            skLineSegment(sketch, "E3770", {"start": v(-329.76, 368.74) * mm, "end": v(-336.1, 370.35) * mm});
            skLineSegment(sketch, "E3771", {"start": v(-336.1, 370.35) * mm, "end": v(-342.97, 371.65) * mm});
            skLineSegment(sketch, "E3772", {"start": v(-342.97, 371.65) * mm, "end": v(-348.57, 372.39) * mm});
            skLineSegment(sketch, "E3773", {"start": v(-348.57, 372.39) * mm, "end": v(-350.44, 372.54) * mm});
            skLineSegment(sketch, "E3774", {"start": v(-350.44, 372.54) * mm, "end": v(-352.7, 372.73) * mm});
            skLineSegment(sketch, "E3775", {"start": v(-352.7, 372.73) * mm, "end": v(-359.5, 373) * mm});
            skLineSegment(sketch, "E3776", {"start": v(-359.5, 373) * mm, "end": v(-367.48, 372.93) * mm});
            skLineSegment(sketch, "E3777", {"start": v(-367.48, 372.93) * mm, "end": v(-374.72, 372.5) * mm});
            skLineSegment(sketch, "E3778", {"start": v(-374.72, 372.5) * mm, "end": v(-381.56, 371.95) * mm});
            skLineSegment(sketch, "E3779", {"start": v(-381.56, 371.95) * mm, "end": v(-388.35, 371.47) * mm});
            skLineSegment(sketch, "E3780", {"start": v(-388.35, 371.47) * mm, "end": v(-395.42, 371.27) * mm});
            skLineSegment(sketch, "E3781", {"start": v(-395.42, 371.27) * mm, "end": v(-403.12, 371.56) * mm});
            skLineSegment(sketch, "E3782", {"start": v(-403.12, 371.56) * mm, "end": v(-409.62, 372.22) * mm});
            skLineSegment(sketch, "E3783", {"start": v(-409.62, 372.22) * mm, "end": v(-411.78, 372.54) * mm});
            skLineSegment(sketch, "E3784", {"start": v(-411.78, 372.54) * mm, "end": v(-412.51, 372.65) * mm});
            skLineSegment(sketch, "E3785", {"start": v(-412.51, 372.65) * mm, "end": v(-414.73, 373) * mm});
            skLineSegment(sketch, "E3786", {"start": v(-414.73, 373) * mm, "end": v(-418.16, 373.52) * mm});
            skLineSegment(sketch, "E3787", {"start": v(-418.16, 373.52) * mm, "end": v(-422.02, 374.11) * mm});
            skLineSegment(sketch, "E3788", {"start": v(-422.02, 374.11) * mm, "end": v(-426.27, 374.78) * mm});
            skLineSegment(sketch, "E3789", {"start": v(-426.27, 374.78) * mm, "end": v(-430.88, 375.5) * mm});
            skLineSegment(sketch, "E3790", {"start": v(-430.88, 375.5) * mm, "end": v(-435.8, 376.27) * mm});
            skLineSegment(sketch, "E3791", {"start": v(-435.8, 376.27) * mm, "end": v(-441.02, 377.09) * mm});
            skLineSegment(sketch, "E3792", {"start": v(-441.02, 377.09) * mm, "end": v(-446.47, 377.95) * mm});
            skLineSegment(sketch, "E3793", {"start": v(-446.47, 377.95) * mm, "end": v(-452.14, 378.85) * mm});
            skLineSegment(sketch, "E3794", {"start": v(-452.14, 378.85) * mm, "end": v(-457.99, 379.77) * mm});
            skLineSegment(sketch, "E3795", {"start": v(-457.99, 379.77) * mm, "end": v(-463.97, 380.72) * mm});
            skLineSegment(sketch, "E3796", {"start": v(-463.97, 380.72) * mm, "end": v(-470.04, 381.68) * mm});
            skLineSegment(sketch, "E3797", {"start": v(-470.04, 381.68) * mm, "end": v(-476.18, 382.66) * mm});
            skLineSegment(sketch, "E3798", {"start": v(-476.18, 382.66) * mm, "end": v(-482.35, 383.64) * mm});
            skLineSegment(sketch, "E3799", {"start": v(-482.35, 383.64) * mm, "end": v(-488.5, 384.62) * mm});
            skLineSegment(sketch, "E3800", {"start": v(-488.5, 384.62) * mm, "end": v(-494.61, 385.59) * mm});
            skLineSegment(sketch, "E3801", {"start": v(-494.61, 385.59) * mm, "end": v(-500.63, 386.55) * mm});
            skLineSegment(sketch, "E3802", {"start": v(-500.63, 386.55) * mm, "end": v(-506.53, 387.49) * mm});
            skLineSegment(sketch, "E3803", {"start": v(-506.53, 387.49) * mm, "end": v(-512.28, 388.4) * mm});
            skLineSegment(sketch, "E3804", {"start": v(-512.28, 388.4) * mm, "end": v(-517.83, 389.3) * mm});
            skLineSegment(sketch, "E3805", {"start": v(-517.83, 389.3) * mm, "end": v(-523.14, 390.14) * mm});
            skLineSegment(sketch, "E3806", {"start": v(-523.14, 390.14) * mm, "end": v(-528.19, 390.95) * mm});
            skLineSegment(sketch, "E3807", {"start": v(-528.19, 390.95) * mm, "end": v(-532.93, 391.7) * mm});
            skLineSegment(sketch, "E3808", {"start": v(-532.93, 391.7) * mm, "end": v(-537.32, 392.4) * mm});
            skLineSegment(sketch, "E3809", {"start": v(-537.32, 392.4) * mm, "end": v(-541.34, 393.05) * mm});
            skLineSegment(sketch, "E3810", {"start": v(-541.34, 393.05) * mm, "end": v(-544.94, 393.63) * mm});
            skLineSegment(sketch, "E3811", {"start": v(-544.94, 393.63) * mm, "end": v(-548.1, 394.13) * mm});
            skLineSegment(sketch, "E3812", {"start": v(-548.1, 394.13) * mm, "end": v(-550.75, 394.56) * mm});
            skLineSegment(sketch, "E3813", {"start": v(-550.75, 394.56) * mm, "end": v(-552.88, 394.9) * mm});
            skLineSegment(sketch, "E3814", {"start": v(-552.88, 394.9) * mm, "end": v(-554.45, 395.15) * mm});
            skLineSegment(sketch, "E3815", {"start": v(-554.45, 395.15) * mm, "end": v(-555.42, 395.3) * mm});
            skLineSegment(sketch, "E3816", {"start": v(-555.42, 395.3) * mm, "end": v(-555.75, 395.36) * mm});
            skLineSegment(sketch, "E3817", {"start": v(608.93, 81.28) * mm, "end": v(608.63, 81.23) * mm});
            skLineSegment(sketch, "E3818", {"start": v(608.63, 81.23) * mm, "end": v(607.7, 81.1) * mm});
            skLineSegment(sketch, "E3819", {"start": v(607.7, 81.1) * mm, "end": v(606.12, 80.92) * mm});
            skLineSegment(sketch, "E3820", {"start": v(606.12, 80.92) * mm, "end": v(603.84, 80.7) * mm});
            skLineSegment(sketch, "E3821", {"start": v(603.84, 80.7) * mm, "end": v(600.84, 80.48) * mm});
            skLineSegment(sketch, "E3822", {"start": v(600.84, 80.48) * mm, "end": v(597.06, 80.28) * mm});
            skLineSegment(sketch, "E3823", {"start": v(597.06, 80.28) * mm, "end": v(592.5, 80.13) * mm});
            skLineSegment(sketch, "E3824", {"start": v(592.5, 80.13) * mm, "end": v(587.1, 80.04) * mm});
            skLineSegment(sketch, "E3825", {"start": v(587.1, 80.04) * mm, "end": v(580.82, 80.05) * mm});
            skLineSegment(sketch, "E3826", {"start": v(580.82, 80.05) * mm, "end": v(573.65, 80.17) * mm});
            skLineSegment(sketch, "E3827", {"start": v(573.65, 80.17) * mm, "end": v(565.53, 80.44) * mm});
            skLineSegment(sketch, "E3828", {"start": v(565.53, 80.44) * mm, "end": v(556.44, 80.88) * mm});
            skLineSegment(sketch, "E3829", {"start": v(556.44, 80.88) * mm, "end": v(546.34, 81.5) * mm});
            skLineSegment(sketch, "E3830", {"start": v(546.34, 81.5) * mm, "end": v(535.19, 82.36) * mm});
            skLineSegment(sketch, "E3831", {"start": v(535.19, 82.36) * mm, "end": v(522.96, 83.45) * mm});
            skLineSegment(sketch, "E3832", {"start": v(522.96, 83.45) * mm, "end": v(512.95, 84.44) * mm});
            skLineSegment(sketch, "E3833", {"start": v(512.95, 84.44) * mm, "end": v(509.62, 84.8) * mm});
            skLineSegment(sketch, "E3834", {"start": v(509.62, 84.8) * mm, "end": v(505.94, 85.2) * mm});
            skLineSegment(sketch, "E3835", {"start": v(505.94, 85.2) * mm, "end": v(494.94, 86.84) * mm});
            skLineSegment(sketch, "E3836", {"start": v(494.94, 86.84) * mm, "end": v(480.38, 89.73) * mm});
            skLineSegment(sketch, "E3837", {"start": v(480.38, 89.73) * mm, "end": v(466.04, 93.36) * mm});
            skLineSegment(sketch, "E3838", {"start": v(466.04, 93.36) * mm, "end": v(451.97, 97.65) * mm});
            skLineSegment(sketch, "E3839", {"start": v(451.97, 97.65) * mm, "end": v(438.28, 102.49) * mm});
            skLineSegment(sketch, "E3840", {"start": v(438.28, 102.49) * mm, "end": v(425.04, 107.8) * mm});
            skLineSegment(sketch, "E3841", {"start": v(425.04, 107.8) * mm, "end": v(412.33, 113.47) * mm});
            skLineSegment(sketch, "E3842", {"start": v(412.33, 113.47) * mm, "end": v(400.24, 119.42) * mm});
            skLineSegment(sketch, "E3843", {"start": v(400.24, 119.42) * mm, "end": v(388.85, 125.54) * mm});
            skLineSegment(sketch, "E3844", {"start": v(388.85, 125.54) * mm, "end": v(378.24, 131.76) * mm});
            skLineSegment(sketch, "E3845", {"start": v(378.24, 131.76) * mm, "end": v(368.49, 137.96) * mm});
            skLineSegment(sketch, "E3846", {"start": v(368.49, 137.96) * mm, "end": v(359.68, 144.05) * mm});
            skLineSegment(sketch, "E3847", {"start": v(359.68, 144.05) * mm, "end": v(351.9, 149.95) * mm});
            skLineSegment(sketch, "E3848", {"start": v(351.9, 149.95) * mm, "end": v(345.23, 155.55) * mm});
            skLineSegment(sketch, "E3849", {"start": v(345.23, 155.55) * mm, "end": v(339.74, 160.77) * mm});
            skLineSegment(sketch, "E3850", {"start": v(339.74, 160.77) * mm, "end": v(336.51, 164.25) * mm});
            skLineSegment(sketch, "E3851", {"start": v(336.51, 164.25) * mm, "end": v(335.53, 165.49) * mm});
            skLineSegment(sketch, "E3852", {"start": v(335.53, 165.49) * mm, "end": v(334.3, 167.03) * mm});
            skLineSegment(sketch, "E3853", {"start": v(334.3, 167.03) * mm, "end": v(330.57, 171.58) * mm});
            skLineSegment(sketch, "E3854", {"start": v(330.57, 171.58) * mm, "end": v(325.33, 177.75) * mm});
            skLineSegment(sketch, "E3855", {"start": v(325.33, 177.75) * mm, "end": v(319.8, 184.02) * mm});
            skLineSegment(sketch, "E3856", {"start": v(319.8, 184.02) * mm, "end": v(313.95, 190.45) * mm});
            skLineSegment(sketch, "E3857", {"start": v(313.95, 190.45) * mm, "end": v(307.76, 197.08) * mm});
            skLineSegment(sketch, "E3858", {"start": v(307.76, 197.08) * mm, "end": v(301.2, 203.94) * mm});
            skLineSegment(sketch, "E3859", {"start": v(301.2, 203.94) * mm, "end": v(294.26, 211.08) * mm});
            skLineSegment(sketch, "E3860", {"start": v(294.26, 211.08) * mm, "end": v(286.9, 218.55) * mm});
            skLineSegment(sketch, "E3861", {"start": v(286.9, 218.55) * mm, "end": v(279.12, 226.37) * mm});
            skLineSegment(sketch, "E3862", {"start": v(279.12, 226.37) * mm, "end": v(270.87, 234.6) * mm});
            skLineSegment(sketch, "E3863", {"start": v(270.87, 234.6) * mm, "end": v(262.14, 243.29) * mm});
            skLineSegment(sketch, "E3864", {"start": v(262.14, 243.29) * mm, "end": v(252.9, 252.46) * mm});
            skLineSegment(sketch, "E3865", {"start": v(252.9, 252.46) * mm, "end": v(243.14, 262.16) * mm});
            skLineSegment(sketch, "E3866", {"start": v(243.14, 262.16) * mm, "end": v(232.82, 272.43) * mm});
            skLineSegment(sketch, "E3867", {"start": v(232.82, 272.43) * mm, "end": v(221.93, 283.32) * mm});
            skLineSegment(sketch, "E3868", {"start": v(221.93, 283.32) * mm, "end": v(213.3, 291.98) * mm});
            skLineSegment(sketch, "E3869", {"start": v(213.3, 291.98) * mm, "end": v(210.44, 294.87) * mm});
            skLineSegment(sketch, "E3870", {"start": v(210.44, 294.87) * mm, "end": v(207.54, 297.79) * mm});
            skLineSegment(sketch, "E3871", {"start": v(207.54, 297.79) * mm, "end": v(198.57, 306.27) * mm});
            skLineSegment(sketch, "E3872", {"start": v(198.57, 306.27) * mm, "end": v(186.61, 316.7) * mm});
            skLineSegment(sketch, "E3873", {"start": v(186.61, 316.7) * mm, "end": v(174.62, 326.18) * mm});
            skLineSegment(sketch, "E3874", {"start": v(174.62, 326.18) * mm, "end": v(162.67, 334.75) * mm});
            skLineSegment(sketch, "E3875", {"start": v(162.67, 334.75) * mm, "end": v(150.83, 342.45) * mm});
            skLineSegment(sketch, "E3876", {"start": v(150.83, 342.45) * mm, "end": v(139.15, 349.3) * mm});
            skLineSegment(sketch, "E3877", {"start": v(139.15, 349.3) * mm, "end": v(127.7, 355.3) * mm});
            skLineSegment(sketch, "E3878", {"start": v(127.7, 355.3) * mm, "end": v(116.55, 360.52) * mm});
            skLineSegment(sketch, "E3879", {"start": v(116.55, 360.52) * mm, "end": v(105.77, 364.97) * mm});
            skLineSegment(sketch, "E3880", {"start": v(105.77, 364.97) * mm, "end": v(95.41, 368.68) * mm});
            skLineSegment(sketch, "E3881", {"start": v(95.41, 368.68) * mm, "end": v(85.55, 371.68) * mm});
            skLineSegment(sketch, "E3882", {"start": v(85.55, 371.68) * mm, "end": v(76.25, 374) * mm});
            skLineSegment(sketch, "E3883", {"start": v(76.25, 374) * mm, "end": v(67.57, 375.65) * mm});
            skLineSegment(sketch, "E3884", {"start": v(67.57, 375.65) * mm, "end": v(59.59, 376.68) * mm});
            skLineSegment(sketch, "E3885", {"start": v(59.59, 376.68) * mm, "end": v(52.36, 377.12) * mm});
            skLineSegment(sketch, "E3886", {"start": v(52.36, 377.12) * mm, "end": v(47.54, 377.1) * mm});
            skLineSegment(sketch, "E3887", {"start": v(47.54, 377.1) * mm, "end": v(45.94, 376.99) * mm});
            skLineSegment(sketch, "E3888", {"start": v(45.94, 376.99) * mm, "end": v(41.55, 376.69) * mm});
            skLineSegment(sketch, "E3889", {"start": v(41.55, 376.69) * mm, "end": v(28.38, 375.38) * mm});
            skLineSegment(sketch, "E3890", {"start": v(28.38, 375.38) * mm, "end": v(12.29, 373.12) * mm});
            skLineSegment(sketch, "E3891", {"start": v(12.29, 373.12) * mm, "end": v(-2.5, 370.3) * mm});
            skLineSegment(sketch, "E3892", {"start": v(-2.5, 370.3) * mm, "end": v(-16.18, 367.03) * mm});
            skLineSegment(sketch, "E3893", {"start": v(-16.18, 367.03) * mm, "end": v(-28.9, 363.4) * mm});
            skLineSegment(sketch, "E3894", {"start": v(-28.9, 363.4) * mm, "end": v(-40.87, 359.51) * mm});
            skLineSegment(sketch, "E3895", {"start": v(-40.87, 359.51) * mm, "end": v(-52.25, 355.46) * mm});
            skLineSegment(sketch, "E3896", {"start": v(-52.25, 355.46) * mm, "end": v(-63.22, 351.34) * mm});
            skLineSegment(sketch, "E3897", {"start": v(-63.22, 351.34) * mm, "end": v(-73.96, 347.24) * mm});
            skLineSegment(sketch, "E3898", {"start": v(-73.96, 347.24) * mm, "end": v(-84.65, 343.28) * mm});
            skLineSegment(sketch, "E3899", {"start": v(-84.65, 343.28) * mm, "end": v(-95.46, 339.53) * mm});
            skLineSegment(sketch, "E3900", {"start": v(-95.46, 339.53) * mm, "end": v(-106.58, 336.11) * mm});
            skLineSegment(sketch, "E3901", {"start": v(-106.58, 336.11) * mm, "end": v(-118.19, 333.1) * mm});
            skLineSegment(sketch, "E3902", {"start": v(-118.19, 333.1) * mm, "end": v(-130.46, 330.62) * mm});
            skLineSegment(sketch, "E3903", {"start": v(-130.46, 330.62) * mm, "end": v(-143.56, 328.74) * mm});
            skLineSegment(sketch, "E3904", {"start": v(-143.56, 328.74) * mm, "end": v(-154.15, 327.76) * mm});
            skLineSegment(sketch, "E3905", {"start": v(-154.15, 327.76) * mm, "end": v(-157.69, 327.57) * mm});
            skLineSegment(sketch, "E3906", {"start": v(-157.69, 327.57) * mm, "end": v(-159, 327.5) * mm});
            skLineSegment(sketch, "E3907", {"start": v(-159, 327.5) * mm, "end": v(-162.95, 327.48) * mm});
            skLineSegment(sketch, "E3908", {"start": v(-162.95, 327.48) * mm, "end": v(-169.8, 327.64) * mm});
            skLineSegment(sketch, "E3909", {"start": v(-169.8, 327.64) * mm, "end": v(-178, 328.06) * mm});
            skLineSegment(sketch, "E3910", {"start": v(-178, 328.06) * mm, "end": v(-187.38, 328.7) * mm});
            skLineSegment(sketch, "E3911", {"start": v(-187.38, 328.7) * mm, "end": v(-197.72, 329.54) * mm});
            skLineSegment(sketch, "E3912", {"start": v(-197.72, 329.54) * mm, "end": v(-208.82, 330.57) * mm});
            skLineSegment(sketch, "E3913", {"start": v(-208.82, 330.57) * mm, "end": v(-220.47, 331.77) * mm});
            skLineSegment(sketch, "E3914", {"start": v(-220.47, 331.77) * mm, "end": v(-232.46, 333.13) * mm});
            skLineSegment(sketch, "E3915", {"start": v(-232.46, 333.13) * mm, "end": v(-244.6, 334.62) * mm});
            skLineSegment(sketch, "E3916", {"start": v(-244.6, 334.62) * mm, "end": v(-256.7, 336.23) * mm});
            skLineSegment(sketch, "E3917", {"start": v(-256.7, 336.23) * mm, "end": v(-268.51, 337.93) * mm});
            skLineSegment(sketch, "E3918", {"start": v(-268.51, 337.93) * mm, "end": v(-279.87, 339.71) * mm});
            skLineSegment(sketch, "E3919", {"start": v(-279.87, 339.71) * mm, "end": v(-290.55, 341.55) * mm});
            skLineSegment(sketch, "E3920", {"start": v(-290.55, 341.55) * mm, "end": v(-300.36, 343.44) * mm});
            skLineSegment(sketch, "E3921", {"start": v(-300.36, 343.44) * mm, "end": v(-309.09, 345.34) * mm});
            skLineSegment(sketch, "E3922", {"start": v(-309.09, 345.34) * mm, "end": v(-314.68, 346.73) * mm});
            skLineSegment(sketch, "E3923", {"start": v(-314.68, 346.73) * mm, "end": v(-316.53, 347.25) * mm});
            skLineSegment(sketch, "E3924", {"start": v(-316.53, 347.25) * mm, "end": v(-317.78, 347.61) * mm});
            skLineSegment(sketch, "E3925", {"start": v(-317.78, 347.61) * mm, "end": v(-321.5, 348.8) * mm});
            skLineSegment(sketch, "E3926", {"start": v(-321.5, 348.8) * mm, "end": v(-326.59, 350.58) * mm});
            skLineSegment(sketch, "E3927", {"start": v(-326.59, 350.58) * mm, "end": v(-331.85, 352.47) * mm});
            skLineSegment(sketch, "E3928", {"start": v(-331.85, 352.47) * mm, "end": v(-337.4, 354.37) * mm});
            skLineSegment(sketch, "E3929", {"start": v(-337.4, 354.37) * mm, "end": v(-343.3, 356.18) * mm});
            skLineSegment(sketch, "E3930", {"start": v(-343.3, 356.18) * mm, "end": v(-349.63, 357.8) * mm});
            skLineSegment(sketch, "E3931", {"start": v(-349.63, 357.8) * mm, "end": v(-356.5, 359.1) * mm});
            skLineSegment(sketch, "E3932", {"start": v(-356.5, 359.1) * mm, "end": v(-362.1, 359.83) * mm});
            skLineSegment(sketch, "E3933", {"start": v(-362.1, 359.83) * mm, "end": v(-363.97, 359.98) * mm});
            skLineSegment(sketch, "E3934", {"start": v(-363.97, 359.98) * mm, "end": v(-366.23, 360.17) * mm});
            skLineSegment(sketch, "E3935", {"start": v(-366.23, 360.17) * mm, "end": v(-373.03, 360.45) * mm});
            skLineSegment(sketch, "E3936", {"start": v(-373.03, 360.45) * mm, "end": v(-381, 360.37) * mm});
            skLineSegment(sketch, "E3937", {"start": v(-381, 360.37) * mm, "end": v(-388.25, 359.95) * mm});
            skLineSegment(sketch, "E3938", {"start": v(-388.25, 359.95) * mm, "end": v(-395.1, 359.4) * mm});
            skLineSegment(sketch, "E3939", {"start": v(-395.1, 359.4) * mm, "end": v(-401.88, 358.91) * mm});
            skLineSegment(sketch, "E3940", {"start": v(-401.88, 358.91) * mm, "end": v(-408.95, 358.72) * mm});
            skLineSegment(sketch, "E3941", {"start": v(-408.95, 358.72) * mm, "end": v(-416.65, 359) * mm});
            skLineSegment(sketch, "E3942", {"start": v(-416.65, 359) * mm, "end": v(-423.15, 359.66) * mm});
            skLineSegment(sketch, "E3943", {"start": v(-423.15, 359.66) * mm, "end": v(-425.3, 359.98) * mm});
            skLineSegment(sketch, "E3944", {"start": v(-425.3, 359.98) * mm, "end": v(-426.86, 360.22) * mm});
            skLineSegment(sketch, "E3945", {"start": v(-426.86, 360.22) * mm, "end": v(-431.5, 360.9) * mm});
            skLineSegment(sketch, "E3946", {"start": v(-431.5, 360.9) * mm, "end": v(-439.07, 362.01) * mm});
            skLineSegment(sketch, "E3947", {"start": v(-439.07, 362.01) * mm, "end": v(-447.76, 363.26) * mm});
            skLineSegment(sketch, "E3948", {"start": v(-447.76, 363.26) * mm, "end": v(-457.34, 364.63) * mm});
            skLineSegment(sketch, "E3949", {"start": v(-457.34, 364.63) * mm, "end": v(-467.56, 366.08) * mm});
            skLineSegment(sketch, "E3950", {"start": v(-467.56, 366.08) * mm, "end": v(-478.17, 367.58) * mm});
            skLineSegment(sketch, "E3951", {"start": v(-478.17, 367.58) * mm, "end": v(-488.94, 369.1) * mm});
            skLineSegment(sketch, "E3952", {"start": v(-488.94, 369.1) * mm, "end": v(-499.6, 370.6) * mm});
            skLineSegment(sketch, "E3953", {"start": v(-499.6, 370.6) * mm, "end": v(-509.94, 372.04) * mm});
            skLineSegment(sketch, "E3954", {"start": v(-509.94, 372.04) * mm, "end": v(-519.69, 373.4) * mm});
            skLineSegment(sketch, "E3955", {"start": v(-519.69, 373.4) * mm, "end": v(-528.6, 374.64) * mm});
            skLineSegment(sketch, "E3956", {"start": v(-528.6, 374.64) * mm, "end": v(-536.45, 375.74) * mm});
            skLineSegment(sketch, "E3957", {"start": v(-536.45, 375.74) * mm, "end": v(-542.98, 376.65) * mm});
            skLineSegment(sketch, "E3958", {"start": v(-542.98, 376.65) * mm, "end": v(-547.94, 377.33) * mm});
            skLineSegment(sketch, "E3959", {"start": v(-547.94, 377.33) * mm, "end": v(-551.1, 377.77) * mm});
            skLineSegment(sketch, "E3960", {"start": v(-551.1, 377.77) * mm, "end": v(-552.21, 377.92) * mm});
            skLineSegment(sketch, "E3961", {"start": v(608.33, 57.5) * mm, "end": v(605.31, 57.62) * mm});
            skLineSegment(sketch, "E3962", {"start": v(605.31, 57.62) * mm, "end": v(596.26, 58) * mm});
            skLineSegment(sketch, "E3963", {"start": v(596.26, 58) * mm, "end": v(585.4, 58.53) * mm});
            skLineSegment(sketch, "E3964", {"start": v(585.4, 58.53) * mm, "end": v(575.63, 59.09) * mm});
            skLineSegment(sketch, "E3965", {"start": v(575.63, 59.09) * mm, "end": v(566.83, 59.66) * mm});
            skLineSegment(sketch, "E3966", {"start": v(566.83, 59.66) * mm, "end": v(558.89, 60.25) * mm});
            skLineSegment(sketch, "E3967", {"start": v(558.89, 60.25) * mm, "end": v(551.68, 60.87) * mm});
            skLineSegment(sketch, "E3968", {"start": v(551.68, 60.87) * mm, "end": v(545.1, 61.5) * mm});
            skLineSegment(sketch, "E3969", {"start": v(545.1, 61.5) * mm, "end": v(539, 62.17) * mm});
            skLineSegment(sketch, "E3970", {"start": v(539, 62.17) * mm, "end": v(533.28, 62.85) * mm});
            skLineSegment(sketch, "E3971", {"start": v(533.28, 62.85) * mm, "end": v(527.83, 63.56) * mm});
            skLineSegment(sketch, "E3972", {"start": v(527.83, 63.56) * mm, "end": v(522.51, 64.29) * mm});
            skLineSegment(sketch, "E3973", {"start": v(522.51, 64.29) * mm, "end": v(517.23, 65.04) * mm});
            skLineSegment(sketch, "E3974", {"start": v(517.23, 65.04) * mm, "end": v(511.85, 65.8) * mm});
            skLineSegment(sketch, "E3975", {"start": v(511.85, 65.8) * mm, "end": v(506.25, 66.6) * mm});
            skLineSegment(sketch, "E3976", {"start": v(506.25, 66.6) * mm, "end": v(500.32, 67.4) * mm});
            skLineSegment(sketch, "E3977", {"start": v(500.32, 67.4) * mm, "end": v(495.54, 68.02) * mm});
            skLineSegment(sketch, "E3978", {"start": v(495.54, 68.02) * mm, "end": v(493.95, 68.22) * mm});
            skLineSegment(sketch, "E3979", {"start": v(493.95, 68.22) * mm, "end": v(490.82, 68.62) * mm});
            skLineSegment(sketch, "E3980", {"start": v(490.82, 68.62) * mm, "end": v(481.5, 70.24) * mm});
            skLineSegment(sketch, "E3981", {"start": v(481.5, 70.24) * mm, "end": v(468.88, 73.1) * mm});
            skLineSegment(sketch, "E3982", {"start": v(468.88, 73.1) * mm, "end": v(456.2, 76.73) * mm});
            skLineSegment(sketch, "E3983", {"start": v(456.2, 76.73) * mm, "end": v(443.54, 81.02) * mm});
            skLineSegment(sketch, "E3984", {"start": v(443.54, 81.02) * mm, "end": v(431.03, 85.88) * mm});
            skLineSegment(sketch, "E3985", {"start": v(431.03, 85.88) * mm, "end": v(418.75, 91.2) * mm});
            skLineSegment(sketch, "E3986", {"start": v(418.75, 91.2) * mm, "end": v(406.82, 96.91) * mm});
            skLineSegment(sketch, "E3987", {"start": v(406.82, 96.91) * mm, "end": v(395.34, 102.9) * mm});
            skLineSegment(sketch, "E3988", {"start": v(395.34, 102.9) * mm, "end": v(384.4, 109.05) * mm});
            skLineSegment(sketch, "E3989", {"start": v(384.4, 109.05) * mm, "end": v(374.11, 115.3) * mm});
            skLineSegment(sketch, "E3990", {"start": v(374.11, 115.3) * mm, "end": v(364.58, 121.53) * mm});
            skLineSegment(sketch, "E3991", {"start": v(364.58, 121.53) * mm, "end": v(355.9, 127.66) * mm});
            skLineSegment(sketch, "E3992", {"start": v(355.9, 127.66) * mm, "end": v(348.2, 133.58) * mm});
            skLineSegment(sketch, "E3993", {"start": v(348.2, 133.58) * mm, "end": v(341.54, 139.2) * mm});
            skLineSegment(sketch, "E3994", {"start": v(341.54, 139.2) * mm, "end": v(336.06, 144.43) * mm});
            skLineSegment(sketch, "E3995", {"start": v(336.06, 144.43) * mm, "end": v(332.83, 147.92) * mm});
            skLineSegment(sketch, "E3996", {"start": v(332.83, 147.92) * mm, "end": v(331.84, 149.16) * mm});
            skLineSegment(sketch, "E3997", {"start": v(331.84, 149.16) * mm, "end": v(330.6, 150.7) * mm});
            skLineSegment(sketch, "E3998", {"start": v(330.6, 150.7) * mm, "end": v(326.87, 155.3) * mm});
            skLineSegment(sketch, "E3999", {"start": v(326.87, 155.3) * mm, "end": v(321.62, 161.58) * mm});
            skLineSegment(sketch, "E4000", {"start": v(321.62, 161.58) * mm, "end": v(316.06, 168.02) * mm});
            skLineSegment(sketch, "E4001", {"start": v(316.06, 168.02) * mm, "end": v(310.16, 174.66) * mm});
            skLineSegment(sketch, "E4002", {"start": v(310.16, 174.66) * mm, "end": v(303.89, 181.5) * mm});
            skLineSegment(sketch, "E4003", {"start": v(303.89, 181.5) * mm, "end": v(297.22, 188.6) * mm});
            skLineSegment(sketch, "E4004", {"start": v(297.22, 188.6) * mm, "end": v(290.13, 195.95) * mm});
            skLineSegment(sketch, "E4005", {"start": v(290.13, 195.95) * mm, "end": v(282.57, 203.59) * mm});
            skLineSegment(sketch, "E4006", {"start": v(282.57, 203.59) * mm, "end": v(274.53, 211.53) * mm});
            skLineSegment(sketch, "E4007", {"start": v(274.53, 211.53) * mm, "end": v(265.98, 219.81) * mm});
            skLineSegment(sketch, "E4008", {"start": v(265.98, 219.81) * mm, "end": v(256.88, 228.44) * mm});
            skLineSegment(sketch, "E4009", {"start": v(256.88, 228.44) * mm, "end": v(247.2, 237.46) * mm});
            skLineSegment(sketch, "E4010", {"start": v(247.2, 237.46) * mm, "end": v(236.93, 246.88) * mm});
            skLineSegment(sketch, "E4011", {"start": v(236.93, 246.88) * mm, "end": v(226.02, 256.72) * mm});
            skLineSegment(sketch, "E4012", {"start": v(226.02, 256.72) * mm, "end": v(214.45, 267.02) * mm});
            skLineSegment(sketch, "E4013", {"start": v(214.45, 267.02) * mm, "end": v(205.26, 275.1) * mm});
            skLineSegment(sketch, "E4014", {"start": v(205.26, 275.1) * mm, "end": v(202.19, 277.79) * mm});
            skLineSegment(sketch, "E4015", {"start": v(202.19, 277.79) * mm, "end": v(199.72, 279.94) * mm});
            skLineSegment(sketch, "E4016", {"start": v(199.72, 279.94) * mm, "end": v(192.21, 286.3) * mm});
            skLineSegment(sketch, "E4017", {"start": v(192.21, 286.3) * mm, "end": v(182.1, 294.53) * mm});
            skLineSegment(sketch, "E4018", {"start": v(182.1, 294.53) * mm, "end": v(171.92, 302.45) * mm});
            skLineSegment(sketch, "E4019", {"start": v(171.92, 302.45) * mm, "end": v(161.69, 310) * mm});
            skLineSegment(sketch, "E4020", {"start": v(161.69, 310) * mm, "end": v(151.44, 317.19) * mm});
            skLineSegment(sketch, "E4021", {"start": v(151.44, 317.19) * mm, "end": v(141.23, 323.96) * mm});
            skLineSegment(sketch, "E4022", {"start": v(141.23, 323.96) * mm, "end": v(131.08, 330.28) * mm});
            skLineSegment(sketch, "E4023", {"start": v(131.08, 330.28) * mm, "end": v(121.05, 336.12) * mm});
            skLineSegment(sketch, "E4024", {"start": v(121.05, 336.12) * mm, "end": v(111.16, 341.44) * mm});
            skLineSegment(sketch, "E4025", {"start": v(111.16, 341.44) * mm, "end": v(101.46, 346.2) * mm});
            skLineSegment(sketch, "E4026", {"start": v(101.46, 346.2) * mm, "end": v(92, 350.4) * mm});
            skLineSegment(sketch, "E4027", {"start": v(92, 350.4) * mm, "end": v(82.8, 353.97) * mm});
            skLineSegment(sketch, "E4028", {"start": v(82.8, 353.97) * mm, "end": v(73.9, 356.9) * mm});
            skLineSegment(sketch, "E4029", {"start": v(73.9, 356.9) * mm, "end": v(65.35, 359.14) * mm});
            skLineSegment(sketch, "E4030", {"start": v(65.35, 359.14) * mm, "end": v(57.18, 360.66) * mm});
            skLineSegment(sketch, "E4031", {"start": v(57.18, 360.66) * mm, "end": v(51.39, 361.33) * mm});
            skLineSegment(sketch, "E4032", {"start": v(51.39, 361.33) * mm, "end": v(49.45, 361.43) * mm});
            skLineSegment(sketch, "E4033", {"start": v(49.45, 361.43) * mm, "end": v(46.63, 361.58) * mm});
            skLineSegment(sketch, "E4034", {"start": v(46.63, 361.58) * mm, "end": v(38.15, 361.37) * mm});
            skLineSegment(sketch, "E4035", {"start": v(38.15, 361.37) * mm, "end": v(26.38, 360.13) * mm});
            skLineSegment(sketch, "E4036", {"start": v(26.38, 360.13) * mm, "end": v(14.2, 357.9) * mm});
            skLineSegment(sketch, "E4037", {"start": v(14.2, 357.9) * mm, "end": v(1.63, 354.85) * mm});
            skLineSegment(sketch, "E4038", {"start": v(1.63, 354.85) * mm, "end": v(-11.27, 351.12) * mm});
            skLineSegment(sketch, "E4039", {"start": v(-11.27, 351.12) * mm, "end": v(-24.45, 346.9) * mm});
            skLineSegment(sketch, "E4040", {"start": v(-24.45, 346.9) * mm, "end": v(-37.87, 342.33) * mm});
            skLineSegment(sketch, "E4041", {"start": v(-37.87, 342.33) * mm, "end": v(-51.48, 337.6) * mm});
            skLineSegment(sketch, "E4042", {"start": v(-51.48, 337.6) * mm, "end": v(-65.25, 332.86) * mm});
            skLineSegment(sketch, "E4043", {"start": v(-65.25, 332.86) * mm, "end": v(-79.1, 328.28) * mm});
            skLineSegment(sketch, "E4044", {"start": v(-79.1, 328.28) * mm, "end": v(-93.02, 324.03) * mm});
            skLineSegment(sketch, "E4045", {"start": v(-93.02, 324.03) * mm, "end": v(-106.95, 320.26) * mm});
            skLineSegment(sketch, "E4046", {"start": v(-106.95, 320.26) * mm, "end": v(-120.83, 317.15) * mm});
            skLineSegment(sketch, "E4047", {"start": v(-120.83, 317.15) * mm, "end": v(-134.64, 314.87) * mm});
            skLineSegment(sketch, "E4048", {"start": v(-134.64, 314.87) * mm, "end": v(-148.31, 313.57) * mm});
            skLineSegment(sketch, "E4049", {"start": v(-148.31, 313.57) * mm, "end": v(-158.44, 313.3) * mm});
            skLineSegment(sketch, "E4050", {"start": v(-158.44, 313.3) * mm, "end": v(-161.8, 313.42) * mm});
            skLineSegment(sketch, "E4051", {"start": v(-161.8, 313.42) * mm, "end": v(-163.03, 313.47) * mm});
            skLineSegment(sketch, "E4052", {"start": v(-163.03, 313.47) * mm, "end": v(-166.7, 313.58) * mm});
            skLineSegment(sketch, "E4053", {"start": v(-166.7, 313.58) * mm, "end": v(-172.54, 313.76) * mm});
            skLineSegment(sketch, "E4054", {"start": v(-172.54, 313.76) * mm, "end": v(-179.22, 313.98) * mm});
            skLineSegment(sketch, "E4055", {"start": v(-179.22, 313.98) * mm, "end": v(-186.68, 314.26) * mm});
            skLineSegment(sketch, "E4056", {"start": v(-186.68, 314.26) * mm, "end": v(-194.85, 314.62) * mm});
            skLineSegment(sketch, "E4057", {"start": v(-194.85, 314.62) * mm, "end": v(-203.66, 315.09) * mm});
            skLineSegment(sketch, "E4058", {"start": v(-203.66, 315.09) * mm, "end": v(-213.03, 315.68) * mm});
            skLineSegment(sketch, "E4059", {"start": v(-213.03, 315.68) * mm, "end": v(-222.9, 316.42) * mm});
            skLineSegment(sketch, "E4060", {"start": v(-222.9, 316.42) * mm, "end": v(-233.2, 317.33) * mm});
            skLineSegment(sketch, "E4061", {"start": v(-233.2, 317.33) * mm, "end": v(-243.83, 318.43) * mm});
            skLineSegment(sketch, "E4062", {"start": v(-243.83, 318.43) * mm, "end": v(-254.75, 319.74) * mm});
            skLineSegment(sketch, "E4063", {"start": v(-254.75, 319.74) * mm, "end": v(-265.88, 321.29) * mm});
            skLineSegment(sketch, "E4064", {"start": v(-265.88, 321.29) * mm, "end": v(-277.14, 323.09) * mm});
            skLineSegment(sketch, "E4065", {"start": v(-277.14, 323.09) * mm, "end": v(-288.46, 325.17) * mm});
            skLineSegment(sketch, "E4066", {"start": v(-288.46, 325.17) * mm, "end": v(-299.78, 327.55) * mm});
            skLineSegment(sketch, "E4067", {"start": v(-299.78, 327.55) * mm, "end": v(-308.21, 329.52) * mm});
            skLineSegment(sketch, "E4068", {"start": v(-308.21, 329.52) * mm, "end": v(-311, 330.24) * mm});
            skLineSegment(sketch, "E4069", {"start": v(-311, 330.24) * mm, "end": v(-312.21, 330.55) * mm});
            skLineSegment(sketch, "E4070", {"start": v(-312.21, 330.55) * mm, "end": v(-315.8, 331.56) * mm});
            skLineSegment(sketch, "E4071", {"start": v(-315.8, 331.56) * mm, "end": v(-320.34, 332.94) * mm});
            skLineSegment(sketch, "E4072", {"start": v(-320.34, 332.94) * mm, "end": v(-324.83, 334.32) * mm});
            skLineSegment(sketch, "E4073", {"start": v(-324.83, 334.32) * mm, "end": v(-329.47, 335.67) * mm});
            skLineSegment(sketch, "E4074", {"start": v(-329.47, 335.67) * mm, "end": v(-334.47, 336.94) * mm});
            skLineSegment(sketch, "E4075", {"start": v(-334.47, 336.94) * mm, "end": v(-340.02, 338.09) * mm});
            skLineSegment(sketch, "E4076", {"start": v(-340.02, 338.09) * mm, "end": v(-346.32, 339.07) * mm});
            skLineSegment(sketch, "E4077", {"start": v(-346.32, 339.07) * mm, "end": v(-351.76, 339.69) * mm});
            skLineSegment(sketch, "E4078", {"start": v(-351.76, 339.69) * mm, "end": v(-353.58, 339.84) * mm});
            skLineSegment(sketch, "E4079", {"start": v(-353.58, 339.84) * mm, "end": v(-358.45, 340.24) * mm});
            skLineSegment(sketch, "E4080", {"start": v(-358.45, 340.24) * mm, "end": v(-373.1, 341.16) * mm});
            skLineSegment(sketch, "E4081", {"start": v(-373.1, 341.16) * mm, "end": v(-392.67, 342.26) * mm});
            skLineSegment(sketch, "E4082", {"start": v(-392.67, 342.26) * mm, "end": v(-412.01, 343.65) * mm});
            skLineSegment(sketch, "E4083", {"start": v(-412.01, 343.65) * mm, "end": v(-426.17, 345.15) * mm});
            skLineSegment(sketch, "E4084", {"start": v(-426.17, 345.15) * mm, "end": v(-430.86, 345.86) * mm});
            skLineSegment(sketch, "E4085", {"start": v(-430.86, 345.86) * mm, "end": v(-431.42, 345.95) * mm});
            skLineSegment(sketch, "E4086", {"start": v(-431.42, 345.95) * mm, "end": v(-433.12, 346.2) * mm});
            skLineSegment(sketch, "E4087", {"start": v(-433.12, 346.2) * mm, "end": v(-435.05, 346.45) * mm});
            skLineSegment(sketch, "E4088", {"start": v(-435.05, 346.45) * mm, "end": v(-436.69, 346.65) * mm});
            skLineSegment(sketch, "E4089", {"start": v(-436.69, 346.65) * mm, "end": v(-438.07, 346.8) * mm});
            skLineSegment(sketch, "E4090", {"start": v(-438.07, 346.8) * mm, "end": v(-439.25, 346.9) * mm});
            skLineSegment(sketch, "E4091", {"start": v(-439.25, 346.9) * mm, "end": v(-440.27, 346.97) * mm});
            skLineSegment(sketch, "E4092", {"start": v(-440.27, 346.97) * mm, "end": v(-441.16, 347) * mm});
            skLineSegment(sketch, "E4093", {"start": v(-441.16, 347) * mm, "end": v(-441.97, 347.02) * mm});
            skLineSegment(sketch, "E4094", {"start": v(-441.97, 347.02) * mm, "end": v(-442.75, 347.02) * mm});
            skLineSegment(sketch, "E4095", {"start": v(-442.75, 347.02) * mm, "end": v(-443.53, 347.01) * mm});
            skLineSegment(sketch, "E4096", {"start": v(-443.53, 347.01) * mm, "end": v(-444.36, 347) * mm});
            skLineSegment(sketch, "E4097", {"start": v(-444.36, 347) * mm, "end": v(-445.28, 347.01) * mm});
            skLineSegment(sketch, "E4098", {"start": v(-445.28, 347.01) * mm, "end": v(-446.34, 347.04) * mm});
            skLineSegment(sketch, "E4099", {"start": v(-446.34, 347.04) * mm, "end": v(-447.57, 347.09) * mm});
            skLineSegment(sketch, "E4100", {"start": v(-447.57, 347.09) * mm, "end": v(-449.02, 347.17) * mm});
            skLineSegment(sketch, "E4101", {"start": v(-449.02, 347.17) * mm, "end": v(-450.74, 347.3) * mm});
            skLineSegment(sketch, "E4102", {"start": v(-450.74, 347.3) * mm, "end": v(-452.76, 347.47) * mm});
            skLineSegment(sketch, "E4103", {"start": v(-452.76, 347.47) * mm, "end": v(-455.13, 347.7) * mm});
            skLineSegment(sketch, "E4104", {"start": v(-455.13, 347.7) * mm, "end": v(-457.89, 348) * mm});
            skLineSegment(sketch, "E4105", {"start": v(-457.89, 348) * mm, "end": v(-461.08, 348.37) * mm});
            skLineSegment(sketch, "E4106", {"start": v(-461.08, 348.37) * mm, "end": v(-464.74, 348.82) * mm});
            skLineSegment(sketch, "E4107", {"start": v(-464.74, 348.82) * mm, "end": v(-468.93, 349.37) * mm});
            skLineSegment(sketch, "E4108", {"start": v(-468.93, 349.37) * mm, "end": v(-473.67, 350) * mm});
            skLineSegment(sketch, "E4109", {"start": v(-473.67, 350) * mm, "end": v(-479.02, 350.75) * mm});
            skLineSegment(sketch, "E4110", {"start": v(-479.02, 350.75) * mm, "end": v(-485.02, 351.6) * mm});
            skLineSegment(sketch, "E4111", {"start": v(-485.02, 351.6) * mm, "end": v(-491.7, 352.58) * mm});
            skLineSegment(sketch, "E4112", {"start": v(-491.7, 352.58) * mm, "end": v(-499.12, 353.69) * mm});
            skLineSegment(sketch, "E4113", {"start": v(-499.12, 353.69) * mm, "end": v(-507.31, 354.93) * mm});
            skLineSegment(sketch, "E4114", {"start": v(-507.31, 354.93) * mm, "end": v(-516.32, 356.32) * mm});
            skLineSegment(sketch, "E4115", {"start": v(-516.32, 356.32) * mm, "end": v(-526.19, 357.86) * mm});
            skLineSegment(sketch, "E4116", {"start": v(-526.19, 357.86) * mm, "end": v(-536.96, 359.56) * mm});
            skLineSegment(sketch, "E4117", {"start": v(-536.96, 359.56) * mm, "end": v(-545.74, 360.96) * mm});
            skLineSegment(sketch, "E4118", {"start": v(-545.74, 360.96) * mm, "end": v(-548.67, 361.43) * mm});
            skLineSegment(sketch, "E4119", {"start": v(608.55, 29.8) * mm, "end": v(605.45, 30.2) * mm});
            skLineSegment(sketch, "E4120", {"start": v(605.45, 30.2) * mm, "end": v(596.14, 31.47) * mm});
            skLineSegment(sketch, "E4121", {"start": v(596.14, 31.47) * mm, "end": v(584.68, 33.1) * mm});
            skLineSegment(sketch, "E4122", {"start": v(584.68, 33.1) * mm, "end": v(574.07, 34.66) * mm});
            skLineSegment(sketch, "E4123", {"start": v(574.07, 34.66) * mm, "end": v(564.25, 36.18) * mm});
            skLineSegment(sketch, "E4124", {"start": v(564.25, 36.18) * mm, "end": v(555.13, 37.67) * mm});
            skLineSegment(sketch, "E4125", {"start": v(555.13, 37.67) * mm, "end": v(546.65, 39.11) * mm});
            skLineSegment(sketch, "E4126", {"start": v(546.65, 39.11) * mm, "end": v(538.71, 40.53) * mm});
            skLineSegment(sketch, "E4127", {"start": v(538.71, 40.53) * mm, "end": v(531.25, 41.9) * mm});
            skLineSegment(sketch, "E4128", {"start": v(531.25, 41.9) * mm, "end": v(524.18, 43.26) * mm});
            skLineSegment(sketch, "E4129", {"start": v(524.18, 43.26) * mm, "end": v(517.43, 44.6) * mm});
            skLineSegment(sketch, "E4130", {"start": v(517.43, 44.6) * mm, "end": v(510.92, 45.9) * mm});
            skLineSegment(sketch, "E4131", {"start": v(510.92, 45.9) * mm, "end": v(504.58, 47.2) * mm});
            skLineSegment(sketch, "E4132", {"start": v(504.58, 47.2) * mm, "end": v(498.32, 48.5) * mm});
            skLineSegment(sketch, "E4133", {"start": v(498.32, 48.5) * mm, "end": v(492.06, 49.78) * mm});
            skLineSegment(sketch, "E4134", {"start": v(492.06, 49.78) * mm, "end": v(485.74, 51.06) * mm});
            skLineSegment(sketch, "E4135", {"start": v(485.74, 51.06) * mm, "end": v(480.88, 52.02) * mm});
            skLineSegment(sketch, "E4136", {"start": v(480.88, 52.02) * mm, "end": v(479.26, 52.34) * mm});
            skLineSegment(sketch, "E4137", {"start": v(479.26, 52.34) * mm, "end": v(476.34, 52.9) * mm});
            skLineSegment(sketch, "E4138", {"start": v(476.34, 52.9) * mm, "end": v(467.66, 54.96) * mm});
            skLineSegment(sketch, "E4139", {"start": v(467.66, 54.96) * mm, "end": v(455.95, 58.29) * mm});
            skLineSegment(sketch, "E4140", {"start": v(455.95, 58.29) * mm, "end": v(444.24, 62.22) * mm});
            skLineSegment(sketch, "E4141", {"start": v(444.24, 62.22) * mm, "end": v(432.61, 66.7) * mm});
            skLineSegment(sketch, "E4142", {"start": v(432.61, 66.7) * mm, "end": v(421.13, 71.61) * mm});
            skLineSegment(sketch, "E4143", {"start": v(421.13, 71.61) * mm, "end": v(409.89, 76.9) * mm});
            skLineSegment(sketch, "E4144", {"start": v(409.89, 76.9) * mm, "end": v(398.96, 82.48) * mm});
            skLineSegment(sketch, "E4145", {"start": v(398.96, 82.48) * mm, "end": v(388.44, 88.25) * mm});
            skLineSegment(sketch, "E4146", {"start": v(388.44, 88.25) * mm, "end": v(378.4, 94.16) * mm});
            skLineSegment(sketch, "E4147", {"start": v(378.4, 94.16) * mm, "end": v(368.91, 100.1) * mm});
            skLineSegment(sketch, "E4148", {"start": v(368.91, 100.1) * mm, "end": v(360.08, 106.01) * mm});
            skLineSegment(sketch, "E4149", {"start": v(360.08, 106.01) * mm, "end": v(351.98, 111.8) * mm});
            skLineSegment(sketch, "E4150", {"start": v(351.98, 111.8) * mm, "end": v(344.69, 117.38) * mm});
            skLineSegment(sketch, "E4151", {"start": v(344.69, 117.38) * mm, "end": v(338.29, 122.67) * mm});
            skLineSegment(sketch, "E4152", {"start": v(338.29, 122.67) * mm, "end": v(332.86, 127.6) * mm});
            skLineSegment(sketch, "E4153", {"start": v(332.86, 127.6) * mm, "end": v(329.54, 130.92) * mm});
            skLineSegment(sketch, "E4154", {"start": v(329.54, 130.92) * mm, "end": v(328.5, 132.08) * mm});
            skLineSegment(sketch, "E4155", {"start": v(328.5, 132.08) * mm, "end": v(327.13, 133.6) * mm});
            skLineSegment(sketch, "E4156", {"start": v(327.13, 133.6) * mm, "end": v(323, 138.1) * mm});
            skLineSegment(sketch, "E4157", {"start": v(323, 138.1) * mm, "end": v(317.28, 144.26) * mm});
            skLineSegment(sketch, "E4158", {"start": v(317.28, 144.26) * mm, "end": v(311.32, 150.55) * mm});
            skLineSegment(sketch, "E4159", {"start": v(311.32, 150.55) * mm, "end": v(305.08, 157.01) * mm});
            skLineSegment(sketch, "E4160", {"start": v(305.08, 157.01) * mm, "end": v(298.52, 163.68) * mm});
            skLineSegment(sketch, "E4161", {"start": v(298.52, 163.68) * mm, "end": v(291.6, 170.57) * mm});
            skLineSegment(sketch, "E4162", {"start": v(291.6, 170.57) * mm, "end": v(284.32, 177.73) * mm});
            skLineSegment(sketch, "E4163", {"start": v(284.32, 177.73) * mm, "end": v(276.6, 185.16) * mm});
            skLineSegment(sketch, "E4164", {"start": v(276.6, 185.16) * mm, "end": v(268.44, 192.92) * mm});
            skLineSegment(sketch, "E4165", {"start": v(268.44, 192.92) * mm, "end": v(259.8, 201.01) * mm});
            skLineSegment(sketch, "E4166", {"start": v(259.8, 201.01) * mm, "end": v(250.63, 209.48) * mm});
            skLineSegment(sketch, "E4167", {"start": v(250.63, 209.48) * mm, "end": v(240.92, 218.34) * mm});
            skLineSegment(sketch, "E4168", {"start": v(240.92, 218.34) * mm, "end": v(230.61, 227.64) * mm});
            skLineSegment(sketch, "E4169", {"start": v(230.61, 227.64) * mm, "end": v(219.69, 237.39) * mm});
            skLineSegment(sketch, "E4170", {"start": v(219.69, 237.39) * mm, "end": v(208.11, 247.62) * mm});
            skLineSegment(sketch, "E4171", {"start": v(208.11, 247.62) * mm, "end": v(198.92, 255.7) * mm});
            skLineSegment(sketch, "E4172", {"start": v(198.92, 255.7) * mm, "end": v(195.85, 258.37) * mm});
            skLineSegment(sketch, "E4173", {"start": v(195.85, 258.37) * mm, "end": v(193.38, 260.52) * mm});
            skLineSegment(sketch, "E4174", {"start": v(193.38, 260.52) * mm, "end": v(185.93, 266.89) * mm});
            skLineSegment(sketch, "E4175", {"start": v(185.93, 266.89) * mm, "end": v(175.97, 275.14) * mm});
            skLineSegment(sketch, "E4176", {"start": v(175.97, 275.14) * mm, "end": v(165.99, 283.08) * mm});
            skLineSegment(sketch, "E4177", {"start": v(165.99, 283.08) * mm, "end": v(156.01, 290.68) * mm});
            skLineSegment(sketch, "E4178", {"start": v(156.01, 290.68) * mm, "end": v(146.05, 297.9) * mm});
            skLineSegment(sketch, "E4179", {"start": v(146.05, 297.9) * mm, "end": v(136.13, 304.7) * mm});
            skLineSegment(sketch, "E4180", {"start": v(136.13, 304.7) * mm, "end": v(126.27, 311.06) * mm});
            skLineSegment(sketch, "E4181", {"start": v(126.27, 311.06) * mm, "end": v(116.48, 316.93) * mm});
            skLineSegment(sketch, "E4182", {"start": v(116.48, 316.93) * mm, "end": v(106.79, 322.28) * mm});
            skLineSegment(sketch, "E4183", {"start": v(106.79, 322.28) * mm, "end": v(97.2, 327.07) * mm});
            skLineSegment(sketch, "E4184", {"start": v(97.2, 327.07) * mm, "end": v(87.75, 331.26) * mm});
            skLineSegment(sketch, "E4185", {"start": v(87.75, 331.26) * mm, "end": v(78.45, 334.82) * mm});
            skLineSegment(sketch, "E4186", {"start": v(78.45, 334.82) * mm, "end": v(69.31, 337.7) * mm});
            skLineSegment(sketch, "E4187", {"start": v(69.31, 337.7) * mm, "end": v(60.36, 339.9) * mm});
            skLineSegment(sketch, "E4188", {"start": v(60.36, 339.9) * mm, "end": v(51.62, 341.35) * mm});
            skLineSegment(sketch, "E4189", {"start": v(51.62, 341.35) * mm, "end": v(45.24, 341.95) * mm});
            skLineSegment(sketch, "E4190", {"start": v(45.24, 341.95) * mm, "end": v(43.1, 342.02) * mm});
            skLineSegment(sketch, "E4191", {"start": v(43.1, 342.02) * mm, "end": v(40.39, 342.1) * mm});
            skLineSegment(sketch, "E4192", {"start": v(40.39, 342.1) * mm, "end": v(32.23, 341.87) * mm});
            skLineSegment(sketch, "E4193", {"start": v(32.23, 341.87) * mm, "end": v(21.62, 340.8) * mm});
            skLineSegment(sketch, "E4194", {"start": v(21.62, 340.8) * mm, "end": v(11.16, 338.92) * mm});
            skLineSegment(sketch, "E4195", {"start": v(11.16, 338.92) * mm, "end": v(0.72, 336.38) * mm});
            skLineSegment(sketch, "E4196", {"start": v(0.72, 336.38) * mm, "end": v(-9.83, 333.3) * mm});
            skLineSegment(sketch, "E4197", {"start": v(-9.83, 333.3) * mm, "end": v(-20.61, 329.8) * mm});
            skLineSegment(sketch, "E4198", {"start": v(-20.61, 329.8) * mm, "end": v(-31.75, 326) * mm});
            skLineSegment(sketch, "E4199", {"start": v(-31.75, 326) * mm, "end": v(-43.38, 322.06) * mm});
            skLineSegment(sketch, "E4200", {"start": v(-43.38, 322.06) * mm, "end": v(-55.61, 318.07) * mm});
            skLineSegment(sketch, "E4201", {"start": v(-55.61, 318.07) * mm, "end": v(-68.58, 314.19) * mm});
            skLineSegment(sketch, "E4202", {"start": v(-68.58, 314.19) * mm, "end": v(-82.42, 310.51) * mm});
            skLineSegment(sketch, "E4203", {"start": v(-82.42, 310.51) * mm, "end": v(-97.24, 307.19) * mm});
            skLineSegment(sketch, "E4204", {"start": v(-97.24, 307.19) * mm, "end": v(-113.17, 304.34) * mm});
            skLineSegment(sketch, "E4205", {"start": v(-113.17, 304.34) * mm, "end": v(-130.34, 302.1) * mm});
            skLineSegment(sketch, "E4206", {"start": v(-130.34, 302.1) * mm, "end": v(-148.88, 300.58) * mm});
            skLineSegment(sketch, "E4207", {"start": v(-148.88, 300.58) * mm, "end": v(-163.9, 299.97) * mm});
            skLineSegment(sketch, "E4208", {"start": v(-163.9, 299.97) * mm, "end": v(-168.9, 299.92) * mm});
            skLineSegment(sketch, "E4209", {"start": v(-168.9, 299.92) * mm, "end": v(-170.11, 299.91) * mm});
            skLineSegment(sketch, "E4210", {"start": v(-170.11, 299.91) * mm, "end": v(-173.71, 299.95) * mm});
            skLineSegment(sketch, "E4211", {"start": v(-173.71, 299.95) * mm, "end": v(-179.24, 300.12) * mm});
            skLineSegment(sketch, "E4212", {"start": v(-179.24, 300.12) * mm, "end": v(-185.43, 300.42) * mm});
            skLineSegment(sketch, "E4213", {"start": v(-185.43, 300.42) * mm, "end": v(-192.22, 300.82) * mm});
            skLineSegment(sketch, "E4214", {"start": v(-192.22, 300.82) * mm, "end": v(-199.53, 301.33) * mm});
            skLineSegment(sketch, "E4215", {"start": v(-199.53, 301.33) * mm, "end": v(-207.29, 301.92) * mm});
            skLineSegment(sketch, "E4216", {"start": v(-207.29, 301.92) * mm, "end": v(-215.43, 302.6) * mm});
            skLineSegment(sketch, "E4217", {"start": v(-215.43, 302.6) * mm, "end": v(-223.9, 303.33) * mm});
            skLineSegment(sketch, "E4218", {"start": v(-223.9, 303.33) * mm, "end": v(-232.61, 304.13) * mm});
            skLineSegment(sketch, "E4219", {"start": v(-232.61, 304.13) * mm, "end": v(-241.5, 304.96) * mm});
            skLineSegment(sketch, "E4220", {"start": v(-241.5, 304.96) * mm, "end": v(-250.52, 305.83) * mm});
            skLineSegment(sketch, "E4221", {"start": v(-250.52, 305.83) * mm, "end": v(-259.57, 306.72) * mm});
            skLineSegment(sketch, "E4222", {"start": v(-259.57, 306.72) * mm, "end": v(-268.6, 307.61) * mm});
            skLineSegment(sketch, "E4223", {"start": v(-268.6, 307.61) * mm, "end": v(-277.54, 308.5) * mm});
            skLineSegment(sketch, "E4224", {"start": v(-277.54, 308.5) * mm, "end": v(-286.32, 309.38) * mm});
            skLineSegment(sketch, "E4225", {"start": v(-286.32, 309.38) * mm, "end": v(-292.73, 310.02) * mm});
            skLineSegment(sketch, "E4226", {"start": v(-292.73, 310.02) * mm, "end": v(-294.87, 310.23) * mm});
            skLineSegment(sketch, "E4227", {"start": v(-294.87, 310.23) * mm, "end": v(-296.27, 310.37) * mm});
            skLineSegment(sketch, "E4228", {"start": v(-296.27, 310.37) * mm, "end": v(-300.46, 311.08) * mm});
            skLineSegment(sketch, "E4229", {"start": v(-300.46, 311.08) * mm, "end": v(-306.87, 312.48) * mm});
            skLineSegment(sketch, "E4230", {"start": v(-306.87, 312.48) * mm, "end": v(-313.96, 314.26) * mm});
            skLineSegment(sketch, "E4231", {"start": v(-313.96, 314.26) * mm, "end": v(-321.54, 316.23) * mm});
            skLineSegment(sketch, "E4232", {"start": v(-321.54, 316.23) * mm, "end": v(-329.45, 318.23) * mm});
            skLineSegment(sketch, "E4233", {"start": v(-329.45, 318.23) * mm, "end": v(-337.54, 320.06) * mm});
            skLineSegment(sketch, "E4234", {"start": v(-337.54, 320.06) * mm, "end": v(-345.64, 321.55) * mm});
            skLineSegment(sketch, "E4235", {"start": v(-345.64, 321.55) * mm, "end": v(-351.6, 322.36) * mm});
            skLineSegment(sketch, "E4236", {"start": v(-351.6, 322.36) * mm, "end": v(-353.58, 322.52) * mm});
            skLineSegment(sketch, "E4237", {"start": v(-353.58, 322.52) * mm, "end": v(-358.52, 322.94) * mm});
            skLineSegment(sketch, "E4238", {"start": v(-358.52, 322.94) * mm, "end": v(-373.35, 323.91) * mm});
            skLineSegment(sketch, "E4239", {"start": v(-373.35, 323.91) * mm, "end": v(-393.47, 325.13) * mm});
            skLineSegment(sketch, "E4240", {"start": v(-393.47, 325.13) * mm, "end": v(-413.36, 326.66) * mm});
            skLineSegment(sketch, "E4241", {"start": v(-413.36, 326.66) * mm, "end": v(-427.7, 328.21) * mm});
            skLineSegment(sketch, "E4242", {"start": v(-427.7, 328.21) * mm, "end": v(-432.45, 328.93) * mm});
            skLineSegment(sketch, "E4243", {"start": v(-432.45, 328.93) * mm, "end": v(-433.96, 329.16) * mm});
            skLineSegment(sketch, "E4244", {"start": v(-433.96, 329.16) * mm, "end": v(-438.48, 329.82) * mm});
            skLineSegment(sketch, "E4245", {"start": v(-438.48, 329.82) * mm, "end": v(-445.6, 330.85) * mm});
            skLineSegment(sketch, "E4246", {"start": v(-445.6, 330.85) * mm, "end": v(-453.6, 332) * mm});
            skLineSegment(sketch, "E4247", {"start": v(-453.6, 332) * mm, "end": v(-462.28, 333.22) * mm});
            skLineSegment(sketch, "E4248", {"start": v(-462.28, 333.22) * mm, "end": v(-471.42, 334.5) * mm});
            skLineSegment(sketch, "E4249", {"start": v(-471.42, 334.5) * mm, "end": v(-480.85, 335.8) * mm});
            skLineSegment(sketch, "E4250", {"start": v(-480.85, 335.8) * mm, "end": v(-490.33, 337.1) * mm});
            skLineSegment(sketch, "E4251", {"start": v(-490.33, 337.1) * mm, "end": v(-499.68, 338.39) * mm});
            skLineSegment(sketch, "E4252", {"start": v(-499.68, 338.39) * mm, "end": v(-508.7, 339.62) * mm});
            skLineSegment(sketch, "E4253", {"start": v(-508.7, 339.62) * mm, "end": v(-517.17, 340.78) * mm});
            skLineSegment(sketch, "E4254", {"start": v(-517.17, 340.78) * mm, "end": v(-524.9, 341.83) * mm});
            skLineSegment(sketch, "E4255", {"start": v(-524.9, 341.83) * mm, "end": v(-531.67, 342.74) * mm});
            skLineSegment(sketch, "E4256", {"start": v(-531.67, 342.74) * mm, "end": v(-537.3, 343.5) * mm});
            skLineSegment(sketch, "E4257", {"start": v(-537.3, 343.5) * mm, "end": v(-541.57, 344.08) * mm});
            skLineSegment(sketch, "E4258", {"start": v(-541.57, 344.08) * mm, "end": v(-544.28, 344.45) * mm});
            skLineSegment(sketch, "E4259", {"start": v(-544.28, 344.45) * mm, "end": v(-545.22, 344.58) * mm});
            skLineSegment(sketch, "E4260", {"start": v(608.4, 3.3) * mm, "end": v(605.26, 3.72) * mm});
            skLineSegment(sketch, "E4261", {"start": v(605.26, 3.72) * mm, "end": v(595.86, 5.03) * mm});
            skLineSegment(sketch, "E4262", {"start": v(595.86, 5.03) * mm, "end": v(584.01, 6.8) * mm});
            skLineSegment(sketch, "E4263", {"start": v(584.01, 6.8) * mm, "end": v(572.82, 8.6) * mm});
            skLineSegment(sketch, "E4264", {"start": v(572.82, 8.6) * mm, "end": v(562.24, 10.43) * mm});
            skLineSegment(sketch, "E4265", {"start": v(562.24, 10.43) * mm, "end": v(552.22, 12.3) * mm});
            skLineSegment(sketch, "E4266", {"start": v(552.22, 12.3) * mm, "end": v(542.73, 14.2) * mm});
            skLineSegment(sketch, "E4267", {"start": v(542.73, 14.2) * mm, "end": v(533.72, 16.14) * mm});
            skLineSegment(sketch, "E4268", {"start": v(533.72, 16.14) * mm, "end": v(525.14, 18.1) * mm});
            skLineSegment(sketch, "E4269", {"start": v(525.14, 18.1) * mm, "end": v(516.96, 20.1) * mm});
            skLineSegment(sketch, "E4270", {"start": v(516.96, 20.1) * mm, "end": v(509.13, 22.1) * mm});
            skLineSegment(sketch, "E4271", {"start": v(509.13, 22.1) * mm, "end": v(501.61, 24.13) * mm});
            skLineSegment(sketch, "E4272", {"start": v(501.61, 24.13) * mm, "end": v(494.36, 26.18) * mm});
            skLineSegment(sketch, "E4273", {"start": v(494.36, 26.18) * mm, "end": v(487.32, 28.25) * mm});
            skLineSegment(sketch, "E4274", {"start": v(487.32, 28.25) * mm, "end": v(480.47, 30.33) * mm});
            skLineSegment(sketch, "E4275", {"start": v(480.47, 30.33) * mm, "end": v(473.75, 32.42) * mm});
            skLineSegment(sketch, "E4276", {"start": v(473.75, 32.42) * mm, "end": v(468.78, 34) * mm});
            skLineSegment(sketch, "E4277", {"start": v(468.78, 34) * mm, "end": v(467.13, 34.52) * mm});
            skLineSegment(sketch, "E4278", {"start": v(467.13, 34.52) * mm, "end": v(463.8, 35.59) * mm});
            skLineSegment(sketch, "E4279", {"start": v(463.8, 35.59) * mm, "end": v(453.88, 38.95) * mm});
            skLineSegment(sketch, "E4280", {"start": v(453.88, 38.95) * mm, "end": v(441.16, 43.6) * mm});
            skLineSegment(sketch, "E4281", {"start": v(441.16, 43.6) * mm, "end": v(428.97, 48.4) * mm});
            skLineSegment(sketch, "E4282", {"start": v(428.97, 48.4) * mm, "end": v(417.34, 53.34) * mm});
            skLineSegment(sketch, "E4283", {"start": v(417.34, 53.34) * mm, "end": v(406.28, 58.37) * mm});
            skLineSegment(sketch, "E4284", {"start": v(406.28, 58.37) * mm, "end": v(395.82, 63.46) * mm});
            skLineSegment(sketch, "E4285", {"start": v(395.82, 63.46) * mm, "end": v(385.98, 68.56) * mm});
            skLineSegment(sketch, "E4286", {"start": v(385.98, 68.56) * mm, "end": v(376.78, 73.64) * mm});
            skLineSegment(sketch, "E4287", {"start": v(376.78, 73.64) * mm, "end": v(368.23, 78.65) * mm});
            skLineSegment(sketch, "E4288", {"start": v(368.23, 78.65) * mm, "end": v(360.36, 83.55) * mm});
            skLineSegment(sketch, "E4289", {"start": v(360.36, 83.55) * mm, "end": v(353.19, 88.32) * mm});
            skLineSegment(sketch, "E4290", {"start": v(353.19, 88.32) * mm, "end": v(346.73, 92.9) * mm});
            skLineSegment(sketch, "E4291", {"start": v(346.73, 92.9) * mm, "end": v(341.01, 97.26) * mm});
            skLineSegment(sketch, "E4292", {"start": v(341.01, 97.26) * mm, "end": v(336.06, 101.36) * mm});
            skLineSegment(sketch, "E4293", {"start": v(336.06, 101.36) * mm, "end": v(331.88, 105.16) * mm});
            skLineSegment(sketch, "E4294", {"start": v(331.88, 105.16) * mm, "end": v(329.3, 107.72) * mm});
            skLineSegment(sketch, "E4295", {"start": v(329.3, 107.72) * mm, "end": v(328.5, 108.62) * mm});
            skLineSegment(sketch, "E4296", {"start": v(328.5, 108.62) * mm, "end": v(327.12, 110.13) * mm});
            skLineSegment(sketch, "E4297", {"start": v(327.12, 110.13) * mm, "end": v(322.98, 114.64) * mm});
            skLineSegment(sketch, "E4298", {"start": v(322.98, 114.64) * mm, "end": v(317.26, 120.77) * mm});
            skLineSegment(sketch, "E4299", {"start": v(317.26, 120.77) * mm, "end": v(311.29, 127.06) * mm});
            skLineSegment(sketch, "E4300", {"start": v(311.29, 127.06) * mm, "end": v(305.04, 133.52) * mm});
            skLineSegment(sketch, "E4301", {"start": v(305.04, 133.52) * mm, "end": v(298.47, 140.18) * mm});
            skLineSegment(sketch, "E4302", {"start": v(298.47, 140.18) * mm, "end": v(291.57, 147.07) * mm});
            skLineSegment(sketch, "E4303", {"start": v(291.57, 147.07) * mm, "end": v(284.28, 154.23) * mm});
            skLineSegment(sketch, "E4304", {"start": v(284.28, 154.23) * mm, "end": v(276.57, 161.67) * mm});
            skLineSegment(sketch, "E4305", {"start": v(276.57, 161.67) * mm, "end": v(268.41, 169.43) * mm});
            skLineSegment(sketch, "E4306", {"start": v(268.41, 169.43) * mm, "end": v(259.77, 177.53) * mm});
            skLineSegment(sketch, "E4307", {"start": v(259.77, 177.53) * mm, "end": v(250.61, 186) * mm});
            skLineSegment(sketch, "E4308", {"start": v(250.61, 186) * mm, "end": v(240.9, 194.87) * mm});
            skLineSegment(sketch, "E4309", {"start": v(240.9, 194.87) * mm, "end": v(230.6, 204.17) * mm});
            skLineSegment(sketch, "E4310", {"start": v(230.6, 204.17) * mm, "end": v(219.68, 213.93) * mm});
            skLineSegment(sketch, "E4311", {"start": v(219.68, 213.93) * mm, "end": v(208.11, 224.16) * mm});
            skLineSegment(sketch, "E4312", {"start": v(208.11, 224.16) * mm, "end": v(198.92, 232.23) * mm});
            skLineSegment(sketch, "E4313", {"start": v(198.92, 232.23) * mm, "end": v(195.85, 234.91) * mm});
            skLineSegment(sketch, "E4314", {"start": v(195.85, 234.91) * mm, "end": v(193.37, 237.08) * mm});
            skLineSegment(sketch, "E4315", {"start": v(193.37, 237.08) * mm, "end": v(185.9, 243.51) * mm});
            skLineSegment(sketch, "E4316", {"start": v(185.9, 243.51) * mm, "end": v(175.84, 252) * mm});
            skLineSegment(sketch, "E4317", {"start": v(175.84, 252) * mm, "end": v(165.72, 260.3) * mm});
            skLineSegment(sketch, "E4318", {"start": v(165.72, 260.3) * mm, "end": v(155.56, 268.37) * mm});
            skLineSegment(sketch, "E4319", {"start": v(155.56, 268.37) * mm, "end": v(145.38, 276.15) * mm});
            skLineSegment(sketch, "E4320", {"start": v(145.38, 276.15) * mm, "end": v(135.2, 283.57) * mm});
            skLineSegment(sketch, "E4321", {"start": v(135.2, 283.57) * mm, "end": v(125.08, 290.6) * mm});
            skLineSegment(sketch, "E4322", {"start": v(125.08, 290.6) * mm, "end": v(115.02, 297.15) * mm});
            skLineSegment(sketch, "E4323", {"start": v(115.02, 297.15) * mm, "end": v(105.05, 303.17) * mm});
            skLineSegment(sketch, "E4324", {"start": v(105.05, 303.17) * mm, "end": v(95.2, 308.62) * mm});
            skLineSegment(sketch, "E4325", {"start": v(95.2, 308.62) * mm, "end": v(85.5, 313.44) * mm});
            skLineSegment(sketch, "E4326", {"start": v(85.5, 313.44) * mm, "end": v(75.98, 317.55) * mm});
            skLineSegment(sketch, "E4327", {"start": v(75.98, 317.55) * mm, "end": v(66.66, 320.91) * mm});
            skLineSegment(sketch, "E4328", {"start": v(66.66, 320.91) * mm, "end": v(57.57, 323.47) * mm});
            skLineSegment(sketch, "E4329", {"start": v(57.57, 323.47) * mm, "end": v(48.74, 325.15) * mm});
            skLineSegment(sketch, "E4330", {"start": v(48.74, 325.15) * mm, "end": v(42.33, 325.83) * mm});
            skLineSegment(sketch, "E4331", {"start": v(42.33, 325.83) * mm, "end": v(40.19, 325.9) * mm});
            skLineSegment(sketch, "E4332", {"start": v(40.19, 325.9) * mm, "end": v(38.83, 325.94) * mm});
            skLineSegment(sketch, "E4333", {"start": v(38.83, 325.94) * mm, "end": v(34.73, 325.93) * mm});
            skLineSegment(sketch, "E4334", {"start": v(34.73, 325.93) * mm, "end": v(29.41, 325.67) * mm});
            skLineSegment(sketch, "E4335", {"start": v(29.41, 325.67) * mm, "end": v(24.2, 325.16) * mm});
            skLineSegment(sketch, "E4336", {"start": v(24.2, 325.16) * mm, "end": v(19.08, 324.4) * mm});
            skLineSegment(sketch, "E4337", {"start": v(19.08, 324.4) * mm, "end": v(14.03, 323.41) * mm});
            skLineSegment(sketch, "E4338", {"start": v(14.03, 323.41) * mm, "end": v(9.03, 322.22) * mm});
            skLineSegment(sketch, "E4339", {"start": v(9.03, 322.22) * mm, "end": v(4.05, 320.84) * mm});
            skLineSegment(sketch, "E4340", {"start": v(4.05, 320.84) * mm, "end": v(-0.93, 319.3) * mm});
            skLineSegment(sketch, "E4341", {"start": v(-0.93, 319.3) * mm, "end": v(-5.92, 317.61) * mm});
            skLineSegment(sketch, "E4342", {"start": v(-5.92, 317.61) * mm, "end": v(-10.95, 315.8) * mm});
            skLineSegment(sketch, "E4343", {"start": v(-10.95, 315.8) * mm, "end": v(-16.05, 313.88) * mm});
            skLineSegment(sketch, "E4344", {"start": v(-16.05, 313.88) * mm, "end": v(-21.23, 311.87) * mm});
            skLineSegment(sketch, "E4345", {"start": v(-21.23, 311.87) * mm, "end": v(-26.52, 309.8) * mm});
            skLineSegment(sketch, "E4346", {"start": v(-26.52, 309.8) * mm, "end": v(-31.93, 307.68) * mm});
            skLineSegment(sketch, "E4347", {"start": v(-31.93, 307.68) * mm, "end": v(-37.49, 305.52) * mm});
            skLineSegment(sketch, "E4348", {"start": v(-37.49, 305.52) * mm, "end": v(-43.22, 303.37) * mm});
            skLineSegment(sketch, "E4349", {"start": v(-43.22, 303.37) * mm, "end": v(-49.14, 301.22) * mm});
            skLineSegment(sketch, "E4350", {"start": v(-49.14, 301.22) * mm, "end": v(-55.28, 299.1) * mm});
            skLineSegment(sketch, "E4351", {"start": v(-55.28, 299.1) * mm, "end": v(-61.65, 297.04) * mm});
            skLineSegment(sketch, "E4352", {"start": v(-61.65, 297.04) * mm, "end": v(-68.28, 295.04) * mm});
            skLineSegment(sketch, "E4353", {"start": v(-68.28, 295.04) * mm, "end": v(-75.19, 293.13) * mm});
            skLineSegment(sketch, "E4354", {"start": v(-75.19, 293.13) * mm, "end": v(-82.4, 291.34) * mm});
            skLineSegment(sketch, "E4355", {"start": v(-82.4, 291.34) * mm, "end": v(-89.92, 289.67) * mm});
            skLineSegment(sketch, "E4356", {"start": v(-89.92, 289.67) * mm, "end": v(-97.8, 288.15) * mm});
            skLineSegment(sketch, "E4357", {"start": v(-97.8, 288.15) * mm, "end": v(-106.03, 286.8) * mm});
            skLineSegment(sketch, "E4358", {"start": v(-106.03, 286.8) * mm, "end": v(-114.66, 285.64) * mm});
            skLineSegment(sketch, "E4359", {"start": v(-114.66, 285.64) * mm, "end": v(-123.7, 284.69) * mm});
            skLineSegment(sketch, "E4360", {"start": v(-123.7, 284.69) * mm, "end": v(-133.16, 283.96) * mm});
            skLineSegment(sketch, "E4361", {"start": v(-133.16, 283.96) * mm, "end": v(-143.07, 283.48) * mm});
            skLineSegment(sketch, "E4362", {"start": v(-143.07, 283.48) * mm, "end": v(-153.46, 283.27) * mm});
            skLineSegment(sketch, "E4363", {"start": v(-153.46, 283.27) * mm, "end": v(-164.35, 283.34) * mm});
            skLineSegment(sketch, "E4364", {"start": v(-164.35, 283.34) * mm, "end": v(-172.9, 283.59) * mm});
            skLineSegment(sketch, "E4365", {"start": v(-172.9, 283.59) * mm, "end": v(-175.75, 283.72) * mm});
            skLineSegment(sketch, "E4366", {"start": v(-175.75, 283.72) * mm, "end": v(-176.92, 283.78) * mm});
            skLineSegment(sketch, "E4367", {"start": v(-176.92, 283.78) * mm, "end": v(-180.45, 283.93) * mm});
            skLineSegment(sketch, "E4368", {"start": v(-180.45, 283.93) * mm, "end": v(-185.68, 284.17) * mm});
            skLineSegment(sketch, "E4369", {"start": v(-185.68, 284.17) * mm, "end": v(-191.39, 284.44) * mm});
            skLineSegment(sketch, "E4370", {"start": v(-191.39, 284.44) * mm, "end": v(-197.52, 284.75) * mm});
            skLineSegment(sketch, "E4371", {"start": v(-197.52, 284.75) * mm, "end": v(-204.04, 285.1) * mm});
            skLineSegment(sketch, "E4372", {"start": v(-204.04, 285.1) * mm, "end": v(-210.88, 285.52) * mm});
            skLineSegment(sketch, "E4373", {"start": v(-210.88, 285.52) * mm, "end": v(-218, 286) * mm});
            skLineSegment(sketch, "E4374", {"start": v(-218, 286) * mm, "end": v(-225.35, 286.54) * mm});
            skLineSegment(sketch, "E4375", {"start": v(-225.35, 286.54) * mm, "end": v(-232.87, 287.16) * mm});
            skLineSegment(sketch, "E4376", {"start": v(-232.87, 287.16) * mm, "end": v(-240.5, 287.87) * mm});
            skLineSegment(sketch, "E4377", {"start": v(-240.5, 287.87) * mm, "end": v(-248.22, 288.67) * mm});
            skLineSegment(sketch, "E4378", {"start": v(-248.22, 288.67) * mm, "end": v(-255.95, 289.58) * mm});
            skLineSegment(sketch, "E4379", {"start": v(-255.95, 289.58) * mm, "end": v(-263.65, 290.59) * mm});
            skLineSegment(sketch, "E4380", {"start": v(-263.65, 290.59) * mm, "end": v(-271.27, 291.72) * mm});
            skLineSegment(sketch, "E4381", {"start": v(-271.27, 291.72) * mm, "end": v(-278.75, 292.97) * mm});
            skLineSegment(sketch, "E4382", {"start": v(-278.75, 292.97) * mm, "end": v(-284.23, 293.99) * mm});
            skLineSegment(sketch, "E4383", {"start": v(-284.23, 293.99) * mm, "end": v(-286.05, 294.36) * mm});
            skLineSegment(sketch, "E4384", {"start": v(-286.05, 294.36) * mm, "end": v(-287.82, 294.72) * mm});
            skLineSegment(sketch, "E4385", {"start": v(-287.82, 294.72) * mm, "end": v(-293.1, 295.88) * mm});
            skLineSegment(sketch, "E4386", {"start": v(-293.1, 295.88) * mm, "end": v(-301.05, 297.71) * mm});
            skLineSegment(sketch, "E4387", {"start": v(-301.05, 297.71) * mm, "end": v(-309.62, 299.75) * mm});
            skLineSegment(sketch, "E4388", {"start": v(-309.62, 299.75) * mm, "end": v(-318.6, 301.87) * mm});
            skLineSegment(sketch, "E4389", {"start": v(-318.6, 301.87) * mm, "end": v(-327.7, 303.96) * mm});
            skLineSegment(sketch, "E4390", {"start": v(-327.7, 303.96) * mm, "end": v(-336.74, 305.9) * mm});
            skLineSegment(sketch, "E4391", {"start": v(-336.74, 305.9) * mm, "end": v(-345.45, 307.55) * mm});
            skLineSegment(sketch, "E4392", {"start": v(-345.45, 307.55) * mm, "end": v(-351.54, 308.55) * mm});
            skLineSegment(sketch, "E4393", {"start": v(-351.54, 308.55) * mm, "end": v(-353.58, 308.82) * mm});
            skLineSegment(sketch, "E4394", {"start": v(-353.58, 308.82) * mm, "end": v(-356.58, 309.22) * mm});
            skLineSegment(sketch, "E4395", {"start": v(-356.58, 309.22) * mm, "end": v(-365.62, 310.23) * mm});
            skLineSegment(sketch, "E4396", {"start": v(-365.62, 310.23) * mm, "end": v(-376.45, 311.14) * mm});
            skLineSegment(sketch, "E4397", {"start": v(-376.45, 311.14) * mm, "end": v(-386.5, 311.73) * mm});
            skLineSegment(sketch, "E4398", {"start": v(-386.5, 311.73) * mm, "end": v(-396.23, 312.16) * mm});
            skLineSegment(sketch, "E4399", {"start": v(-396.23, 312.16) * mm, "end": v(-406.06, 312.59) * mm});
            skLineSegment(sketch, "E4400", {"start": v(-406.06, 312.59) * mm, "end": v(-416.44, 313.18) * mm});
            skLineSegment(sketch, "E4401", {"start": v(-416.44, 313.18) * mm, "end": v(-427.8, 314.1) * mm});
            skLineSegment(sketch, "E4402", {"start": v(-427.8, 314.1) * mm, "end": v(-437.38, 315.12) * mm});
            skLineSegment(sketch, "E4403", {"start": v(-437.38, 315.12) * mm, "end": v(-440.56, 315.52) * mm});
            skLineSegment(sketch, "E4404", {"start": v(-440.56, 315.52) * mm, "end": v(-442.05, 315.7) * mm});
            skLineSegment(sketch, "E4405", {"start": v(-442.05, 315.7) * mm, "end": v(-446.5, 316.3) * mm});
            skLineSegment(sketch, "E4406", {"start": v(-446.5, 316.3) * mm, "end": v(-453.29, 317.25) * mm});
            skLineSegment(sketch, "E4407", {"start": v(-453.29, 317.25) * mm, "end": v(-460.77, 318.33) * mm});
            skLineSegment(sketch, "E4408", {"start": v(-460.77, 318.33) * mm, "end": v(-468.78, 319.52) * mm});
            skLineSegment(sketch, "E4409", {"start": v(-468.78, 319.52) * mm, "end": v(-477.13, 320.78) * mm});
            skLineSegment(sketch, "E4410", {"start": v(-477.13, 320.78) * mm, "end": v(-485.66, 322.1) * mm});
            skLineSegment(sketch, "E4411", {"start": v(-485.66, 322.1) * mm, "end": v(-494.2, 323.42) * mm});
            skLineSegment(sketch, "E4412", {"start": v(-494.2, 323.42) * mm, "end": v(-502.56, 324.74) * mm});
            skLineSegment(sketch, "E4413", {"start": v(-502.56, 324.74) * mm, "end": v(-510.58, 326) * mm});
            skLineSegment(sketch, "E4414", {"start": v(-510.58, 326) * mm, "end": v(-518.1, 327.2) * mm});
            skLineSegment(sketch, "E4415", {"start": v(-518.1, 327.2) * mm, "end": v(-524.92, 328.3) * mm});
            skLineSegment(sketch, "E4416", {"start": v(-524.92, 328.3) * mm, "end": v(-530.9, 329.27) * mm});
            skLineSegment(sketch, "E4417", {"start": v(-530.9, 329.27) * mm, "end": v(-535.83, 330.07) * mm});
            skLineSegment(sketch, "E4418", {"start": v(-535.83, 330.07) * mm, "end": v(-539.58, 330.68) * mm});
            skLineSegment(sketch, "E4419", {"start": v(-539.58, 330.68) * mm, "end": v(-541.95, 331.07) * mm});
            skLineSegment(sketch, "E4420", {"start": v(-541.95, 331.07) * mm, "end": v(-542.78, 331.2) * mm});
            skLineSegment(sketch, "E4421", {"start": v(608.4, 120.59) * mm, "end": v(608.35, 120.52) * mm});
            skLineSegment(sketch, "E4422", {"start": v(608.35, 120.52) * mm, "end": v(608.14, 120.33) * mm});
            skLineSegment(sketch, "E4423", {"start": v(608.14, 120.33) * mm, "end": v(607.64, 120.05) * mm});
            skLineSegment(sketch, "E4424", {"start": v(607.64, 120.05) * mm, "end": v(606.74, 119.7) * mm});
            skLineSegment(sketch, "E4425", {"start": v(606.74, 119.7) * mm, "end": v(605.3, 119.3) * mm});
            skLineSegment(sketch, "E4426", {"start": v(605.3, 119.3) * mm, "end": v(603.24, 118.91) * mm});
            skLineSegment(sketch, "E4427", {"start": v(603.24, 118.91) * mm, "end": v(600.4, 118.53) * mm});
            skLineSegment(sketch, "E4428", {"start": v(600.4, 118.53) * mm, "end": v(596.7, 118.2) * mm});
            skLineSegment(sketch, "E4429", {"start": v(596.7, 118.2) * mm, "end": v(591.98, 117.94) * mm});
            skLineSegment(sketch, "E4430", {"start": v(591.98, 117.94) * mm, "end": v(586.16, 117.79) * mm});
            skLineSegment(sketch, "E4431", {"start": v(586.16, 117.79) * mm, "end": v(579.1, 117.77) * mm});
            skLineSegment(sketch, "E4432", {"start": v(579.1, 117.77) * mm, "end": v(570.68, 117.9) * mm});
            skLineSegment(sketch, "E4433", {"start": v(570.68, 117.9) * mm, "end": v(560.8, 118.22) * mm});
            skLineSegment(sketch, "E4434", {"start": v(560.8, 118.22) * mm, "end": v(549.3, 118.76) * mm});
            skLineSegment(sketch, "E4435", {"start": v(549.3, 118.76) * mm, "end": v(536.12, 119.54) * mm});
            skLineSegment(sketch, "E4436", {"start": v(536.12, 119.54) * mm, "end": v(524.85, 120.3) * mm});
            skLineSegment(sketch, "E4437", {"start": v(524.85, 120.3) * mm, "end": v(521.1, 120.59) * mm});
            skLineSegment(sketch, "E4438", {"start": v(521.1, 120.59) * mm, "end": v(517.16, 120.88) * mm});
            skLineSegment(sketch, "E4439", {"start": v(517.16, 120.88) * mm, "end": v(505.38, 122.3) * mm});
            skLineSegment(sketch, "E4440", {"start": v(505.38, 122.3) * mm, "end": v(490.17, 124.96) * mm});
            skLineSegment(sketch, "E4441", {"start": v(490.17, 124.96) * mm, "end": v(475.53, 128.46) * mm});
            skLineSegment(sketch, "E4442", {"start": v(475.53, 128.46) * mm, "end": v(461.46, 132.69) * mm});
            skLineSegment(sketch, "E4443", {"start": v(461.46, 132.69) * mm, "end": v(448.01, 137.53) * mm});
            skLineSegment(sketch, "E4444", {"start": v(448.01, 137.53) * mm, "end": v(435.2, 142.87) * mm});
            skLineSegment(sketch, "E4445", {"start": v(435.2, 142.87) * mm, "end": v(423.06, 148.6) * mm});
            skLineSegment(sketch, "E4446", {"start": v(423.06, 148.6) * mm, "end": v(411.63, 154.6) * mm});
            skLineSegment(sketch, "E4447", {"start": v(411.63, 154.6) * mm, "end": v(400.93, 160.78) * mm});
            skLineSegment(sketch, "E4448", {"start": v(400.93, 160.78) * mm, "end": v(391, 167) * mm});
            skLineSegment(sketch, "E4449", {"start": v(391, 167) * mm, "end": v(381.85, 173.15) * mm});
            skLineSegment(sketch, "E4450", {"start": v(381.85, 173.15) * mm, "end": v(373.52, 179.13) * mm});
            skLineSegment(sketch, "E4451", {"start": v(373.52, 179.13) * mm, "end": v(366.05, 184.82) * mm});
            skLineSegment(sketch, "E4452", {"start": v(366.05, 184.82) * mm, "end": v(359.46, 190.1) * mm});
            skLineSegment(sketch, "E4453", {"start": v(359.46, 190.1) * mm, "end": v(353.8, 194.87) * mm});
            skLineSegment(sketch, "E4454", {"start": v(353.8, 194.87) * mm, "end": v(350.23, 197.97) * mm});
            skLineSegment(sketch, "E4455", {"start": v(350.23, 197.97) * mm, "end": v(349.06, 199.01) * mm});
            skLineSegment(sketch, "E4456", {"start": v(349.06, 199.01) * mm, "end": v(347.93, 200.02) * mm});
            skLineSegment(sketch, "E4457", {"start": v(347.93, 200.02) * mm, "end": v(344.66, 203.15) * mm});
            skLineSegment(sketch, "E4458", {"start": v(344.66, 203.15) * mm, "end": v(339.94, 207.97) * mm});
            skLineSegment(sketch, "E4459", {"start": v(339.94, 207.97) * mm, "end": v(334.87, 213.43) * mm});
            skLineSegment(sketch, "E4460", {"start": v(334.87, 213.43) * mm, "end": v(329.43, 219.5) * mm});
            skLineSegment(sketch, "E4461", {"start": v(329.43, 219.5) * mm, "end": v(323.57, 226.16) * mm});
            skLineSegment(sketch, "E4462", {"start": v(323.57, 226.16) * mm, "end": v(317.28, 233.36) * mm});
            skLineSegment(sketch, "E4463", {"start": v(317.28, 233.36) * mm, "end": v(310.52, 241.08) * mm});
            skLineSegment(sketch, "E4464", {"start": v(310.52, 241.08) * mm, "end": v(303.27, 249.27) * mm});
            skLineSegment(sketch, "E4465", {"start": v(303.27, 249.27) * mm, "end": v(295.5, 257.93) * mm});
            skLineSegment(sketch, "E4466", {"start": v(295.5, 257.93) * mm, "end": v(287.17, 267) * mm});
            skLineSegment(sketch, "E4467", {"start": v(287.17, 267) * mm, "end": v(278.26, 276.45) * mm});
            skLineSegment(sketch, "E4468", {"start": v(278.26, 276.45) * mm, "end": v(268.75, 286.26) * mm});
            skLineSegment(sketch, "E4469", {"start": v(268.75, 286.26) * mm, "end": v(258.58, 296.4) * mm});
            skLineSegment(sketch, "E4470", {"start": v(258.58, 296.4) * mm, "end": v(247.76, 306.82) * mm});
            skLineSegment(sketch, "E4471", {"start": v(247.76, 306.82) * mm, "end": v(236.23, 317.49) * mm});
            skLineSegment(sketch, "E4472", {"start": v(236.23, 317.49) * mm, "end": v(227.06, 325.7) * mm});
            skLineSegment(sketch, "E4473", {"start": v(227.06, 325.7) * mm, "end": v(223.97, 328.4) * mm});
            skLineSegment(sketch, "E4474", {"start": v(223.97, 328.4) * mm, "end": v(220.81, 331.14) * mm});
            skLineSegment(sketch, "E4475", {"start": v(220.81, 331.14) * mm, "end": v(211.18, 339.21) * mm});
            skLineSegment(sketch, "E4476", {"start": v(211.18, 339.21) * mm, "end": v(198.76, 349.08) * mm});
            skLineSegment(sketch, "E4477", {"start": v(198.76, 349.08) * mm, "end": v(186.73, 358.04) * mm});
            skLineSegment(sketch, "E4478", {"start": v(186.73, 358.04) * mm, "end": v(175.07, 366.12) * mm});
            skLineSegment(sketch, "E4479", {"start": v(175.07, 366.12) * mm, "end": v(163.78, 373.36) * mm});
            skLineSegment(sketch, "E4480", {"start": v(163.78, 373.36) * mm, "end": v(152.86, 379.8) * mm});
            skLineSegment(sketch, "E4481", {"start": v(152.86, 379.8) * mm, "end": v(142.31, 385.47) * mm});
            skLineSegment(sketch, "E4482", {"start": v(142.31, 385.47) * mm, "end": v(132.13, 390.41) * mm});
            skLineSegment(sketch, "E4483", {"start": v(132.13, 390.41) * mm, "end": v(122.3, 394.67) * mm});
            skLineSegment(sketch, "E4484", {"start": v(122.3, 394.67) * mm, "end": v(112.85, 398.27) * mm});
            skLineSegment(sketch, "E4485", {"start": v(112.85, 398.27) * mm, "end": v(103.75, 401.26) * mm});
            skLineSegment(sketch, "E4486", {"start": v(103.75, 401.26) * mm, "end": v(95, 403.67) * mm});
            skLineSegment(sketch, "E4487", {"start": v(95, 403.67) * mm, "end": v(86.62, 405.54) * mm});
            skLineSegment(sketch, "E4488", {"start": v(86.62, 405.54) * mm, "end": v(78.58, 406.92) * mm});
            skLineSegment(sketch, "E4489", {"start": v(78.58, 406.92) * mm, "end": v(70.9, 407.82) * mm});
            skLineSegment(sketch, "E4490", {"start": v(70.9, 407.82) * mm, "end": v(65.4, 408.23) * mm});
            skLineSegment(sketch, "E4491", {"start": v(65.4, 408.23) * mm, "end": v(63.55, 408.3) * mm});
            skLineSegment(sketch, "E4492", {"start": v(63.55, 408.3) * mm, "end": v(59.21, 408.47) * mm});
            skLineSegment(sketch, "E4493", {"start": v(59.21, 408.47) * mm, "end": v(46.17, 408.38) * mm});
            skLineSegment(sketch, "E4494", {"start": v(46.17, 408.38) * mm, "end": v(29.58, 407.31) * mm});
            skLineSegment(sketch, "E4495", {"start": v(29.58, 407.31) * mm, "end": v(13.74, 405.26) * mm});
            skLineSegment(sketch, "E4496", {"start": v(13.74, 405.26) * mm, "end": v(-1.4, 402.36) * mm});
            skLineSegment(sketch, "E4497", {"start": v(-1.4, 402.36) * mm, "end": v(-15.88, 398.78) * mm});
            skLineSegment(sketch, "E4498", {"start": v(-15.88, 398.78) * mm, "end": v(-29.75, 394.67) * mm});
            skLineSegment(sketch, "E4499", {"start": v(-29.75, 394.67) * mm, "end": v(-43.05, 390.17) * mm});
            skLineSegment(sketch, "E4500", {"start": v(-43.05, 390.17) * mm, "end": v(-55.84, 385.43) * mm});
            skLineSegment(sketch, "E4501", {"start": v(-55.84, 385.43) * mm, "end": v(-68.15, 380.61) * mm});
            skLineSegment(sketch, "E4502", {"start": v(-68.15, 380.61) * mm, "end": v(-80.03, 375.86) * mm});
            skLineSegment(sketch, "E4503", {"start": v(-80.03, 375.86) * mm, "end": v(-91.55, 371.34) * mm});
            skLineSegment(sketch, "E4504", {"start": v(-91.55, 371.34) * mm, "end": v(-102.73, 367.17) * mm});
            skLineSegment(sketch, "E4505", {"start": v(-102.73, 367.17) * mm, "end": v(-113.62, 363.54) * mm});
            skLineSegment(sketch, "E4506", {"start": v(-113.62, 363.54) * mm, "end": v(-124.28, 360.58) * mm});
            skLineSegment(sketch, "E4507", {"start": v(-124.28, 360.58) * mm, "end": v(-134.74, 358.43) * mm});
            skLineSegment(sketch, "E4508", {"start": v(-134.74, 358.43) * mm, "end": v(-142.47, 357.42) * mm});
            skLineSegment(sketch, "E4509", {"start": v(-142.47, 357.42) * mm, "end": v(-145.06, 357.27) * mm});
            skLineSegment(sketch, "E4510", {"start": v(-145.06, 357.27) * mm, "end": v(-146.39, 357.19) * mm});
            skLineSegment(sketch, "E4511", {"start": v(-146.39, 357.19) * mm, "end": v(-150.38, 357.06) * mm});
            skLineSegment(sketch, "E4512", {"start": v(-150.38, 357.06) * mm, "end": v(-156.82, 356.98) * mm});
            skLineSegment(sketch, "E4513", {"start": v(-156.82, 356.98) * mm, "end": v(-164.25, 357.06) * mm});
            skLineSegment(sketch, "E4514", {"start": v(-164.25, 357.06) * mm, "end": v(-172.52, 357.25) * mm});
            skLineSegment(sketch, "E4515", {"start": v(-172.52, 357.25) * mm, "end": v(-181.49, 357.57) * mm});
            skLineSegment(sketch, "E4516", {"start": v(-181.49, 357.57) * mm, "end": v(-191.01, 358) * mm});
            skLineSegment(sketch, "E4517", {"start": v(-191.01, 358) * mm, "end": v(-200.96, 358.54) * mm});
            skLineSegment(sketch, "E4518", {"start": v(-200.96, 358.54) * mm, "end": v(-211.18, 359.17) * mm});
            skLineSegment(sketch, "E4519", {"start": v(-211.18, 359.17) * mm, "end": v(-221.54, 359.9) * mm});
            skLineSegment(sketch, "E4520", {"start": v(-221.54, 359.9) * mm, "end": v(-231.9, 360.71) * mm});
            skLineSegment(sketch, "E4521", {"start": v(-231.9, 360.71) * mm, "end": v(-242.1, 361.6) * mm});
            skLineSegment(sketch, "E4522", {"start": v(-242.1, 361.6) * mm, "end": v(-252.03, 362.55) * mm});
            skLineSegment(sketch, "E4523", {"start": v(-252.03, 362.55) * mm, "end": v(-261.52, 363.57) * mm});
            skLineSegment(sketch, "E4524", {"start": v(-261.52, 363.57) * mm, "end": v(-270.46, 364.64) * mm});
            skLineSegment(sketch, "E4525", {"start": v(-270.46, 364.64) * mm, "end": v(-278.67, 365.76) * mm});
            skLineSegment(sketch, "E4526", {"start": v(-278.67, 365.76) * mm, "end": v(-284.2, 366.6) * mm});
            skLineSegment(sketch, "E4527", {"start": v(-284.2, 366.6) * mm, "end": v(-286.05, 366.91) * mm});
            skLineSegment(sketch, "E4528", {"start": v(-286.05, 366.91) * mm, "end": v(-286.72, 367.03) * mm});
            skLineSegment(sketch, "E4529", {"start": v(-286.72, 367.03) * mm, "end": v(-288.74, 367.46) * mm});
            skLineSegment(sketch, "E4530", {"start": v(-288.74, 367.46) * mm, "end": v(-291.84, 368.25) * mm});
            skLineSegment(sketch, "E4531", {"start": v(-291.84, 368.25) * mm, "end": v(-295.3, 369.24) * mm});
            skLineSegment(sketch, "E4532", {"start": v(-295.3, 369.24) * mm, "end": v(-299.06, 370.4) * mm});
            skLineSegment(sketch, "E4533", {"start": v(-299.06, 370.4) * mm, "end": v(-303.1, 371.7) * mm});
            skLineSegment(sketch, "E4534", {"start": v(-303.1, 371.7) * mm, "end": v(-307.37, 373.09) * mm});
            skLineSegment(sketch, "E4535", {"start": v(-307.37, 373.09) * mm, "end": v(-311.81, 374.55) * mm});
            skLineSegment(sketch, "E4536", {"start": v(-311.81, 374.55) * mm, "end": v(-316.39, 376.03) * mm});
            skLineSegment(sketch, "E4537", {"start": v(-316.39, 376.03) * mm, "end": v(-321.06, 377.5) * mm});
            skLineSegment(sketch, "E4538", {"start": v(-321.06, 377.5) * mm, "end": v(-325.77, 378.95) * mm});
            skLineSegment(sketch, "E4539", {"start": v(-325.77, 378.95) * mm, "end": v(-330.48, 380.3) * mm});
            skLineSegment(sketch, "E4540", {"start": v(-330.48, 380.3) * mm, "end": v(-335.14, 381.56) * mm});
            skLineSegment(sketch, "E4541", {"start": v(-335.14, 381.56) * mm, "end": v(-339.72, 382.67) * mm});
            skLineSegment(sketch, "E4542", {"start": v(-339.72, 382.67) * mm, "end": v(-344.16, 383.6) * mm});
            skLineSegment(sketch, "E4543", {"start": v(-344.16, 383.6) * mm, "end": v(-348.42, 384.3) * mm});
            skLineSegment(sketch, "E4544", {"start": v(-348.42, 384.3) * mm, "end": v(-351.43, 384.68) * mm});
            skLineSegment(sketch, "E4545", {"start": v(-351.43, 384.68) * mm, "end": v(-352.45, 384.76) * mm});
            skLineSegment(sketch, "E4546", {"start": v(-352.45, 384.76) * mm, "end": v(-354.76, 384.96) * mm});
            skLineSegment(sketch, "E4547", {"start": v(-354.76, 384.96) * mm, "end": v(-361.71, 385.3) * mm});
            skLineSegment(sketch, "E4548", {"start": v(-361.71, 385.3) * mm, "end": v(-370.25, 385.41) * mm});
            skLineSegment(sketch, "E4549", {"start": v(-370.25, 385.41) * mm, "end": v(-378.28, 385.26) * mm});
            skLineSegment(sketch, "E4550", {"start": v(-378.28, 385.26) * mm, "end": v(-386.02, 385) * mm});
            skLineSegment(sketch, "E4551", {"start": v(-386.02, 385) * mm, "end": v(-393.71, 384.84) * mm});
            skLineSegment(sketch, "E4552", {"start": v(-393.71, 384.84) * mm, "end": v(-401.57, 384.9) * mm});
            skLineSegment(sketch, "E4553", {"start": v(-401.57, 384.9) * mm, "end": v(-409.82, 385.38) * mm});
            skLineSegment(sketch, "E4554", {"start": v(-409.82, 385.38) * mm, "end": v(-416.48, 386.1) * mm});
            skLineSegment(sketch, "E4555", {"start": v(-416.48, 386.1) * mm, "end": v(-418.69, 386.43) * mm});
            skLineSegment(sketch, "E4556", {"start": v(-418.69, 386.43) * mm, "end": v(-419.43, 386.54) * mm});
            skLineSegment(sketch, "E4557", {"start": v(-419.43, 386.54) * mm, "end": v(-421.64, 386.88) * mm});
            skLineSegment(sketch, "E4558", {"start": v(-421.64, 386.88) * mm, "end": v(-425.03, 387.4) * mm});
            skLineSegment(sketch, "E4559", {"start": v(-425.03, 387.4) * mm, "end": v(-428.83, 388) * mm});
            skLineSegment(sketch, "E4560", {"start": v(-428.83, 388) * mm, "end": v(-433, 388.66) * mm});
            skLineSegment(sketch, "E4561", {"start": v(-433, 388.66) * mm, "end": v(-437.52, 389.37) * mm});
            skLineSegment(sketch, "E4562", {"start": v(-437.52, 389.37) * mm, "end": v(-442.33, 390.14) * mm});
            skLineSegment(sketch, "E4563", {"start": v(-442.33, 390.14) * mm, "end": v(-447.42, 390.95) * mm});
            skLineSegment(sketch, "E4564", {"start": v(-447.42, 390.95) * mm, "end": v(-452.74, 391.8) * mm});
            skLineSegment(sketch, "E4565", {"start": v(-452.74, 391.8) * mm, "end": v(-458.26, 392.7) * mm});
            skLineSegment(sketch, "E4566", {"start": v(-458.26, 392.7) * mm, "end": v(-463.94, 393.6) * mm});
            skLineSegment(sketch, "E4567", {"start": v(-463.94, 393.6) * mm, "end": v(-469.74, 394.54) * mm});
            skLineSegment(sketch, "E4568", {"start": v(-469.74, 394.54) * mm, "end": v(-475.64, 395.5) * mm});
            skLineSegment(sketch, "E4569", {"start": v(-475.64, 395.5) * mm, "end": v(-481.6, 396.47) * mm});
            skLineSegment(sketch, "E4570", {"start": v(-481.6, 396.47) * mm, "end": v(-487.57, 397.44) * mm});
            skLineSegment(sketch, "E4571", {"start": v(-487.57, 397.44) * mm, "end": v(-493.53, 398.4) * mm});
            skLineSegment(sketch, "E4572", {"start": v(-493.53, 398.4) * mm, "end": v(-499.44, 399.37) * mm});
            skLineSegment(sketch, "E4573", {"start": v(-499.44, 399.37) * mm, "end": v(-505.27, 400.32) * mm});
            skLineSegment(sketch, "E4574", {"start": v(-505.27, 400.32) * mm, "end": v(-510.98, 401.25) * mm});
            skLineSegment(sketch, "E4575", {"start": v(-510.98, 401.25) * mm, "end": v(-516.53, 402.15) * mm});
            skLineSegment(sketch, "E4576", {"start": v(-516.53, 402.15) * mm, "end": v(-521.9, 403.03) * mm});
            skLineSegment(sketch, "E4577", {"start": v(-521.9, 403.03) * mm, "end": v(-527.02, 403.87) * mm});
            skLineSegment(sketch, "E4578", {"start": v(-527.02, 403.87) * mm, "end": v(-531.9, 404.67) * mm});
            skLineSegment(sketch, "E4579", {"start": v(-531.9, 404.67) * mm, "end": v(-536.48, 405.42) * mm});
            skLineSegment(sketch, "E4580", {"start": v(-536.48, 405.42) * mm, "end": v(-540.72, 406.11) * mm});
            skLineSegment(sketch, "E4581", {"start": v(-540.72, 406.11) * mm, "end": v(-544.6, 406.75) * mm});
            skLineSegment(sketch, "E4582", {"start": v(-544.6, 406.75) * mm, "end": v(-548.08, 407.32) * mm});
            skLineSegment(sketch, "E4583", {"start": v(-548.08, 407.32) * mm, "end": v(-551.11, 407.81) * mm});
            skLineSegment(sketch, "E4584", {"start": v(-551.11, 407.81) * mm, "end": v(-553.68, 408.24) * mm});
            skLineSegment(sketch, "E4585", {"start": v(-553.68, 408.24) * mm, "end": v(-555.73, 408.57) * mm});
            skLineSegment(sketch, "E4586", {"start": v(-555.73, 408.57) * mm, "end": v(-557.25, 408.82) * mm});
            skLineSegment(sketch, "E4587", {"start": v(-557.25, 408.82) * mm, "end": v(-558.18, 408.98) * mm});
            skLineSegment(sketch, "E4588", {"start": v(-558.18, 408.98) * mm, "end": v(-558.5, 409.03) * mm});
            skLineSegment(sketch, "E4589", {"start": v(608.55, 152.89) * mm, "end": v(608.33, 152.74) * mm});
            skLineSegment(sketch, "E4590", {"start": v(608.33, 152.74) * mm, "end": v(607.65, 152.3) * mm});
            skLineSegment(sketch, "E4591", {"start": v(607.65, 152.3) * mm, "end": v(606.5, 151.64) * mm});
            skLineSegment(sketch, "E4592", {"start": v(606.5, 151.64) * mm, "end": v(604.85, 150.77) * mm});
            skLineSegment(sketch, "E4593", {"start": v(604.85, 150.77) * mm, "end": v(602.72, 149.75) * mm});
            skLineSegment(sketch, "E4594", {"start": v(602.72, 149.75) * mm, "end": v(600.08, 148.6) * mm});
            skLineSegment(sketch, "E4595", {"start": v(600.08, 148.6) * mm, "end": v(596.92, 147.38) * mm});
            skLineSegment(sketch, "E4596", {"start": v(596.92, 147.38) * mm, "end": v(593.22, 146.12) * mm});
            skLineSegment(sketch, "E4597", {"start": v(593.22, 146.12) * mm, "end": v(588.98, 144.86) * mm});
            skLineSegment(sketch, "E4598", {"start": v(588.98, 144.86) * mm, "end": v(584.17, 143.63) * mm});
            skLineSegment(sketch, "E4599", {"start": v(584.17, 143.63) * mm, "end": v(578.8, 142.5) * mm});
            skLineSegment(sketch, "E4600", {"start": v(578.8, 142.5) * mm, "end": v(572.84, 141.47) * mm});
            skLineSegment(sketch, "E4601", {"start": v(572.84, 141.47) * mm, "end": v(566.28, 140.6) * mm});
            skLineSegment(sketch, "E4602", {"start": v(566.28, 140.6) * mm, "end": v(559.12, 139.93) * mm});
            skLineSegment(sketch, "E4603", {"start": v(559.12, 139.93) * mm, "end": v(551.33, 139.5) * mm});
            skLineSegment(sketch, "E4604", {"start": v(551.33, 139.5) * mm, "end": v(545.02, 139.35) * mm});
            skLineSegment(sketch, "E4605", {"start": v(545.02, 139.35) * mm, "end": v(542.91, 139.35) * mm});
            skLineSegment(sketch, "E4606", {"start": v(542.91, 139.35) * mm, "end": v(538.96, 139.35) * mm});
            skLineSegment(sketch, "E4607", {"start": v(538.96, 139.35) * mm, "end": v(527.1, 139.9) * mm});
            skLineSegment(sketch, "E4608", {"start": v(527.1, 139.9) * mm, "end": v(511.73, 141.44) * mm});
            skLineSegment(sketch, "E4609", {"start": v(511.73, 141.44) * mm, "end": v(496.85, 143.89) * mm});
            skLineSegment(sketch, "E4610", {"start": v(496.85, 143.89) * mm, "end": v(482.49, 147.12) * mm});
            skLineSegment(sketch, "E4611", {"start": v(482.49, 147.12) * mm, "end": v(468.7, 151.03) * mm});
            skLineSegment(sketch, "E4612", {"start": v(468.7, 151.03) * mm, "end": v(455.5, 155.51) * mm});
            skLineSegment(sketch, "E4613", {"start": v(455.5, 155.51) * mm, "end": v(442.98, 160.45) * mm});
            skLineSegment(sketch, "E4614", {"start": v(442.98, 160.45) * mm, "end": v(431.14, 165.73) * mm});
            skLineSegment(sketch, "E4615", {"start": v(431.14, 165.73) * mm, "end": v(420.04, 171.25) * mm});
            skLineSegment(sketch, "E4616", {"start": v(420.04, 171.25) * mm, "end": v(409.72, 176.9) * mm});
            skLineSegment(sketch, "E4617", {"start": v(409.72, 176.9) * mm, "end": v(400.21, 182.56) * mm});
            skLineSegment(sketch, "E4618", {"start": v(400.21, 182.56) * mm, "end": v(391.57, 188.13) * mm});
            skLineSegment(sketch, "E4619", {"start": v(391.57, 188.13) * mm, "end": v(383.83, 193.5) * mm});
            skLineSegment(sketch, "E4620", {"start": v(383.83, 193.5) * mm, "end": v(377.03, 198.55) * mm});
            skLineSegment(sketch, "E4621", {"start": v(377.03, 198.55) * mm, "end": v(371.23, 203.18) * mm});
            skLineSegment(sketch, "E4622", {"start": v(371.23, 203.18) * mm, "end": v(367.62, 206.22) * mm});
            skLineSegment(sketch, "E4623", {"start": v(367.62, 206.22) * mm, "end": v(366.45, 207.27) * mm});
            skLineSegment(sketch, "E4624", {"start": v(366.45, 207.27) * mm, "end": v(365.32, 208.27) * mm});
            skLineSegment(sketch, "E4625", {"start": v(365.32, 208.27) * mm, "end": v(362, 211.35) * mm});
            skLineSegment(sketch, "E4626", {"start": v(362, 211.35) * mm, "end": v(357.15, 216.03) * mm});
            skLineSegment(sketch, "E4627", {"start": v(357.15, 216.03) * mm, "end": v(351.88, 221.28) * mm});
            skLineSegment(sketch, "E4628", {"start": v(351.88, 221.28) * mm, "end": v(346.2, 227.1) * mm});
            skLineSegment(sketch, "E4629", {"start": v(346.2, 227.1) * mm, "end": v(340.07, 233.46) * mm});
            skLineSegment(sketch, "E4630", {"start": v(340.07, 233.46) * mm, "end": v(333.5, 240.37) * mm});
            skLineSegment(sketch, "E4631", {"start": v(333.5, 240.37) * mm, "end": v(326.48, 247.8) * mm});
            skLineSegment(sketch, "E4632", {"start": v(326.48, 247.8) * mm, "end": v(319, 255.76) * mm});
            skLineSegment(sketch, "E4633", {"start": v(319, 255.76) * mm, "end": v(311.05, 264.22) * mm});
            skLineSegment(sketch, "E4634", {"start": v(311.05, 264.22) * mm, "end": v(302.62, 273.17) * mm});
            skLineSegment(sketch, "E4635", {"start": v(302.62, 273.17) * mm, "end": v(293.7, 282.61) * mm});
            skLineSegment(sketch, "E4636", {"start": v(293.7, 282.61) * mm, "end": v(284.27, 292.52) * mm});
            skLineSegment(sketch, "E4637", {"start": v(284.27, 292.52) * mm, "end": v(274.33, 302.9) * mm});
            skLineSegment(sketch, "E4638", {"start": v(274.33, 302.9) * mm, "end": v(263.87, 313.71) * mm});
            skLineSegment(sketch, "E4639", {"start": v(263.87, 313.71) * mm, "end": v(252.88, 324.96) * mm});
            skLineSegment(sketch, "E4640", {"start": v(252.88, 324.96) * mm, "end": v(244.25, 333.74) * mm});
            skLineSegment(sketch, "E4641", {"start": v(244.25, 333.74) * mm, "end": v(241.36, 336.65) * mm});
            skLineSegment(sketch, "E4642", {"start": v(241.36, 336.65) * mm, "end": v(238.45, 339.58) * mm});
            skLineSegment(sketch, "E4643", {"start": v(238.45, 339.58) * mm, "end": v(229.5, 348.16) * mm});
            skLineSegment(sketch, "E4644", {"start": v(229.5, 348.16) * mm, "end": v(217.52, 358.92) * mm});
            skLineSegment(sketch, "E4645", {"start": v(217.52, 358.92) * mm, "end": v(205.47, 368.92) * mm});
            skLineSegment(sketch, "E4646", {"start": v(205.47, 368.92) * mm, "end": v(193.39, 378.15) * mm});
            skLineSegment(sketch, "E4647", {"start": v(193.39, 378.15) * mm, "end": v(181.3, 386.6) * mm});
            skLineSegment(sketch, "E4648", {"start": v(181.3, 386.6) * mm, "end": v(169.24, 394.29) * mm});
            skLineSegment(sketch, "E4649", {"start": v(169.24, 394.29) * mm, "end": v(157.24, 401.19) * mm});
            skLineSegment(sketch, "E4650", {"start": v(157.24, 401.19) * mm, "end": v(145.34, 407.3) * mm});
            skLineSegment(sketch, "E4651", {"start": v(145.34, 407.3) * mm, "end": v(133.57, 412.6) * mm});
            skLineSegment(sketch, "E4652", {"start": v(133.57, 412.6) * mm, "end": v(121.98, 417.12) * mm});
            skLineSegment(sketch, "E4653", {"start": v(121.98, 417.12) * mm, "end": v(110.58, 420.83) * mm});
            skLineSegment(sketch, "E4654", {"start": v(110.58, 420.83) * mm, "end": v(99.42, 423.72) * mm});
            skLineSegment(sketch, "E4655", {"start": v(99.42, 423.72) * mm, "end": v(88.53, 425.8) * mm});
            skLineSegment(sketch, "E4656", {"start": v(88.53, 425.8) * mm, "end": v(77.95, 427.04) * mm});
            skLineSegment(sketch, "E4657", {"start": v(77.95, 427.04) * mm, "end": v(67.7, 427.46) * mm});
            skLineSegment(sketch, "E4658", {"start": v(67.7, 427.46) * mm, "end": v(60.29, 427.26) * mm});
            skLineSegment(sketch, "E4659", {"start": v(60.29, 427.26) * mm, "end": v(57.83, 427.04) * mm});
            skLineSegment(sketch, "E4660", {"start": v(57.83, 427.04) * mm, "end": v(53.6, 426.68) * mm});
            skLineSegment(sketch, "E4661", {"start": v(53.6, 426.68) * mm, "end": v(40.95, 425.2) * mm});
            skLineSegment(sketch, "E4662", {"start": v(40.95, 425.2) * mm, "end": v(24.6, 422.66) * mm});
            skLineSegment(sketch, "E4663", {"start": v(24.6, 422.66) * mm, "end": v(8.82, 419.55) * mm});
            skLineSegment(sketch, "E4664", {"start": v(8.82, 419.55) * mm, "end": v(-6.39, 415.97) * mm});
            skLineSegment(sketch, "E4665", {"start": v(-6.39, 415.97) * mm, "end": v(-21, 412.03) * mm});
            skLineSegment(sketch, "E4666", {"start": v(-21, 412.03) * mm, "end": v(-34.98, 407.83) * mm});
            skLineSegment(sketch, "E4667", {"start": v(-34.98, 407.83) * mm, "end": v(-48.33, 403.48) * mm});
            skLineSegment(sketch, "E4668", {"start": v(-48.33, 403.48) * mm, "end": v(-61.01, 399.08) * mm});
            skLineSegment(sketch, "E4669", {"start": v(-61.01, 399.08) * mm, "end": v(-73.01, 394.74) * mm});
            skLineSegment(sketch, "E4670", {"start": v(-73.01, 394.74) * mm, "end": v(-84.31, 390.56) * mm});
            skLineSegment(sketch, "E4671", {"start": v(-84.31, 390.56) * mm, "end": v(-94.88, 386.65) * mm});
            skLineSegment(sketch, "E4672", {"start": v(-94.88, 386.65) * mm, "end": v(-104.7, 383.12) * mm});
            skLineSegment(sketch, "E4673", {"start": v(-104.7, 383.12) * mm, "end": v(-113.77, 380.06) * mm});
            skLineSegment(sketch, "E4674", {"start": v(-113.77, 380.06) * mm, "end": v(-122.03, 377.59) * mm});
            skLineSegment(sketch, "E4675", {"start": v(-122.03, 377.59) * mm, "end": v(-129.5, 375.8) * mm});
            skLineSegment(sketch, "E4676", {"start": v(-129.5, 375.8) * mm, "end": v(-134.46, 374.97) * mm});
            skLineSegment(sketch, "E4677", {"start": v(-134.46, 374.97) * mm, "end": v(-136.13, 374.82) * mm});
            skLineSegment(sketch, "E4678", {"start": v(-136.13, 374.82) * mm, "end": v(-137.48, 374.7) * mm});
            skLineSegment(sketch, "E4679", {"start": v(-137.48, 374.7) * mm, "end": v(-141.54, 374.45) * mm});
            skLineSegment(sketch, "E4680", {"start": v(-141.54, 374.45) * mm, "end": v(-148.26, 374.17) * mm});
            skLineSegment(sketch, "E4681", {"start": v(-148.26, 374.17) * mm, "end": v(-156.11, 374) * mm});
            skLineSegment(sketch, "E4682", {"start": v(-156.11, 374) * mm, "end": v(-164.95, 373.92) * mm});
            skLineSegment(sketch, "E4683", {"start": v(-164.95, 373.92) * mm, "end": v(-174.59, 373.95) * mm});
            skLineSegment(sketch, "E4684", {"start": v(-174.59, 373.95) * mm, "end": v(-184.88, 374.07) * mm});
            skLineSegment(sketch, "E4685", {"start": v(-184.88, 374.07) * mm, "end": v(-195.65, 374.3) * mm});
            skLineSegment(sketch, "E4686", {"start": v(-195.65, 374.3) * mm, "end": v(-206.73, 374.63) * mm});
            skLineSegment(sketch, "E4687", {"start": v(-206.73, 374.63) * mm, "end": v(-217.98, 375.06) * mm});
            skLineSegment(sketch, "E4688", {"start": v(-217.98, 375.06) * mm, "end": v(-229.2, 375.6) * mm});
            skLineSegment(sketch, "E4689", {"start": v(-229.2, 375.6) * mm, "end": v(-240.26, 376.26) * mm});
            skLineSegment(sketch, "E4690", {"start": v(-240.26, 376.26) * mm, "end": v(-250.97, 377.01) * mm});
            skLineSegment(sketch, "E4691", {"start": v(-250.97, 377.01) * mm, "end": v(-261.17, 377.88) * mm});
            skLineSegment(sketch, "E4692", {"start": v(-261.17, 377.88) * mm, "end": v(-270.7, 378.85) * mm});
            skLineSegment(sketch, "E4693", {"start": v(-270.7, 378.85) * mm, "end": v(-279.4, 379.94) * mm});
            skLineSegment(sketch, "E4694", {"start": v(-279.4, 379.94) * mm, "end": v(-285.19, 380.8) * mm});
            skLineSegment(sketch, "E4695", {"start": v(-285.19, 380.8) * mm, "end": v(-287.1, 381.14) * mm});
            skLineSegment(sketch, "E4696", {"start": v(-287.1, 381.14) * mm, "end": v(-288.57, 381.4) * mm});
            skLineSegment(sketch, "E4697", {"start": v(-288.57, 381.4) * mm, "end": v(-292.93, 382.34) * mm});
            skLineSegment(sketch, "E4698", {"start": v(-292.93, 382.34) * mm, "end": v(-300.05, 384.05) * mm});
            skLineSegment(sketch, "E4699", {"start": v(-300.05, 384.05) * mm, "end": v(-308.14, 386.08) * mm});
            skLineSegment(sketch, "E4700", {"start": v(-308.14, 386.08) * mm, "end": v(-316.9, 388.26) * mm});
            skLineSegment(sketch, "E4701", {"start": v(-316.9, 388.26) * mm, "end": v(-325.98, 390.4) * mm});
            skLineSegment(sketch, "E4702", {"start": v(-325.98, 390.4) * mm, "end": v(-335.1, 392.35) * mm});
            skLineSegment(sketch, "E4703", {"start": v(-335.1, 392.35) * mm, "end": v(-343.93, 393.9) * mm});
            skLineSegment(sketch, "E4704", {"start": v(-343.93, 393.9) * mm, "end": v(-350.09, 394.72) * mm});
            skLineSegment(sketch, "E4705", {"start": v(-350.09, 394.72) * mm, "end": v(-352.15, 394.89) * mm});
            skLineSegment(sketch, "E4706", {"start": v(-352.15, 394.89) * mm, "end": v(-356.88, 395.28) * mm});
            skLineSegment(sketch, "E4707", {"start": v(-356.88, 395.28) * mm, "end": v(-371.1, 396.05) * mm});
            skLineSegment(sketch, "E4708", {"start": v(-371.1, 396.05) * mm, "end": v(-389.4, 396.77) * mm});
            skLineSegment(sketch, "E4709", {"start": v(-389.4, 396.77) * mm, "end": v(-407.48, 397.8) * mm});
            skLineSegment(sketch, "E4710", {"start": v(-407.48, 397.8) * mm, "end": v(-421.2, 399.15) * mm});
            skLineSegment(sketch, "E4711", {"start": v(-421.2, 399.15) * mm, "end": v(-425.75, 399.84) * mm});
            skLineSegment(sketch, "E4712", {"start": v(-425.75, 399.84) * mm, "end": v(-426.48, 399.95) * mm});
            skLineSegment(sketch, "E4713", {"start": v(-426.48, 399.95) * mm, "end": v(-428.68, 400.28) * mm});
            skLineSegment(sketch, "E4714", {"start": v(-428.68, 400.28) * mm, "end": v(-432.03, 400.8) * mm});
            skLineSegment(sketch, "E4715", {"start": v(-432.03, 400.8) * mm, "end": v(-435.77, 401.38) * mm});
            skLineSegment(sketch, "E4716", {"start": v(-435.77, 401.38) * mm, "end": v(-439.86, 402.02) * mm});
            skLineSegment(sketch, "E4717", {"start": v(-439.86, 402.02) * mm, "end": v(-444.27, 402.7) * mm});
            skLineSegment(sketch, "E4718", {"start": v(-444.27, 402.7) * mm, "end": v(-448.97, 403.44) * mm});
            skLineSegment(sketch, "E4719", {"start": v(-448.97, 403.44) * mm, "end": v(-453.92, 404.22) * mm});
            skLineSegment(sketch, "E4720", {"start": v(-453.92, 404.22) * mm, "end": v(-459.08, 405.04) * mm});
            skLineSegment(sketch, "E4721", {"start": v(-459.08, 405.04) * mm, "end": v(-464.43, 405.88) * mm});
            skLineSegment(sketch, "E4722", {"start": v(-464.43, 405.88) * mm, "end": v(-469.93, 406.76) * mm});
            skLineSegment(sketch, "E4723", {"start": v(-469.93, 406.76) * mm, "end": v(-475.55, 407.65) * mm});
            skLineSegment(sketch, "E4724", {"start": v(-475.55, 407.65) * mm, "end": v(-481.25, 408.56) * mm});
            skLineSegment(sketch, "E4725", {"start": v(-481.25, 408.56) * mm, "end": v(-487, 409.47) * mm});
            skLineSegment(sketch, "E4726", {"start": v(-487, 409.47) * mm, "end": v(-492.77, 410.4) * mm});
            skLineSegment(sketch, "E4727", {"start": v(-492.77, 410.4) * mm, "end": v(-498.51, 411.3) * mm});
            skLineSegment(sketch, "E4728", {"start": v(-498.51, 411.3) * mm, "end": v(-504.21, 412.22) * mm});
            skLineSegment(sketch, "E4729", {"start": v(-504.21, 412.22) * mm, "end": v(-509.83, 413.12) * mm});
            skLineSegment(sketch, "E4730", {"start": v(-509.83, 413.12) * mm, "end": v(-515.32, 414) * mm});
            skLineSegment(sketch, "E4731", {"start": v(-515.32, 414) * mm, "end": v(-520.66, 414.85) * mm});
            skLineSegment(sketch, "E4732", {"start": v(-520.66, 414.85) * mm, "end": v(-525.82, 415.68) * mm});
            skLineSegment(sketch, "E4733", {"start": v(-525.82, 415.68) * mm, "end": v(-530.76, 416.47) * mm});
            skLineSegment(sketch, "E4734", {"start": v(-530.76, 416.47) * mm, "end": v(-535.44, 417.22) * mm});
            skLineSegment(sketch, "E4735", {"start": v(-535.44, 417.22) * mm, "end": v(-539.84, 417.93) * mm});
            skLineSegment(sketch, "E4736", {"start": v(-539.84, 417.93) * mm, "end": v(-543.92, 418.58) * mm});
            skLineSegment(sketch, "E4737", {"start": v(-543.92, 418.58) * mm, "end": v(-547.64, 419.18) * mm});
            skLineSegment(sketch, "E4738", {"start": v(-547.64, 419.18) * mm, "end": v(-550.98, 419.72) * mm});
            skLineSegment(sketch, "E4739", {"start": v(-550.98, 419.72) * mm, "end": v(-553.9, 420.18) * mm});
            skLineSegment(sketch, "E4740", {"start": v(-553.9, 420.18) * mm, "end": v(-556.36, 420.58) * mm});
            skLineSegment(sketch, "E4741", {"start": v(-556.36, 420.58) * mm, "end": v(-558.33, 420.9) * mm});
            skLineSegment(sketch, "E4742", {"start": v(-558.33, 420.9) * mm, "end": v(-559.78, 421.13) * mm});
            skLineSegment(sketch, "E4743", {"start": v(-559.78, 421.13) * mm, "end": v(-560.68, 421.28) * mm});
            skLineSegment(sketch, "E4744", {"start": v(-560.68, 421.28) * mm, "end": v(-560.98, 421.32) * mm});
            skLineSegment(sketch, "E4745", {"start": v(609.59, -19.79) * mm, "end": v(608.94, -19.8) * mm});
            skLineSegment(sketch, "E4746", {"start": v(608.94, -19.8) * mm, "end": v(606.98, -19.72) * mm});
            skLineSegment(sketch, "E4747", {"start": v(606.98, -19.72) * mm, "end": v(603.78, -19.43) * mm});
            skLineSegment(sketch, "E4748", {"start": v(603.78, -19.43) * mm, "end": v(600.03, -18.95) * mm});
            skLineSegment(sketch, "E4749", {"start": v(600.03, -18.95) * mm, "end": v(595.75, -18.28) * mm});
            skLineSegment(sketch, "E4750", {"start": v(595.75, -18.28) * mm, "end": v(590.99, -17.43) * mm});
            skLineSegment(sketch, "E4751", {"start": v(590.99, -17.43) * mm, "end": v(585.77, -16.41) * mm});
            skLineSegment(sketch, "E4752", {"start": v(585.77, -16.41) * mm, "end": v(580.13, -15.23) * mm});
            skLineSegment(sketch, "E4753", {"start": v(580.13, -15.23) * mm, "end": v(574.12, -13.9) * mm});
            skLineSegment(sketch, "E4754", {"start": v(574.12, -13.9) * mm, "end": v(567.76, -12.43) * mm});
            skLineSegment(sketch, "E4755", {"start": v(567.76, -12.43) * mm, "end": v(561.08, -10.83) * mm});
            skLineSegment(sketch, "E4756", {"start": v(561.08, -10.83) * mm, "end": v(554.13, -9.1) * mm});
            skLineSegment(sketch, "E4757", {"start": v(554.13, -9.1) * mm, "end": v(546.94, -7.28) * mm});
            skLineSegment(sketch, "E4758", {"start": v(546.94, -7.28) * mm, "end": v(539.54, -5.35) * mm});
            skLineSegment(sketch, "E4759", {"start": v(539.54, -5.35) * mm, "end": v(531.97, -3.33) * mm});
            skLineSegment(sketch, "E4760", {"start": v(531.97, -3.33) * mm, "end": v(524.27, -1.23) * mm});
            skLineSegment(sketch, "E4761", {"start": v(524.27, -1.23) * mm, "end": v(516.47, 0.93) * mm});
            skLineSegment(sketch, "E4762", {"start": v(516.47, 0.93) * mm, "end": v(508.6, 3.15) * mm});
            skLineSegment(sketch, "E4763", {"start": v(508.6, 3.15) * mm, "end": v(500.7, 5.42) * mm});
            skLineSegment(sketch, "E4764", {"start": v(500.7, 5.42) * mm, "end": v(492.82, 7.73) * mm});
            skLineSegment(sketch, "E4765", {"start": v(492.82, 7.73) * mm, "end": v(484.97, 10.07) * mm});
            skLineSegment(sketch, "E4766", {"start": v(484.97, 10.07) * mm, "end": v(477.2, 12.43) * mm});
            skLineSegment(sketch, "E4767", {"start": v(477.2, 12.43) * mm, "end": v(469.54, 14.8) * mm});
            skLineSegment(sketch, "E4768", {"start": v(469.54, 14.8) * mm, "end": v(462.02, 17.15) * mm});
            skLineSegment(sketch, "E4769", {"start": v(462.02, 17.15) * mm, "end": v(454.69, 19.5) * mm});
            skLineSegment(sketch, "E4770", {"start": v(454.69, 19.5) * mm, "end": v(447.57, 21.83) * mm});
            skLineSegment(sketch, "E4771", {"start": v(447.57, 21.83) * mm, "end": v(440.71, 24.13) * mm});
            skLineSegment(sketch, "E4772", {"start": v(440.71, 24.13) * mm, "end": v(434.14, 26.38) * mm});
            skLineSegment(sketch, "E4773", {"start": v(434.14, 26.38) * mm, "end": v(427.88, 28.57) * mm});
            skLineSegment(sketch, "E4774", {"start": v(427.88, 28.57) * mm, "end": v(421.98, 30.71) * mm});
            skLineSegment(sketch, "E4775", {"start": v(421.98, 30.71) * mm, "end": v(416.49, 32.77) * mm});
            skLineSegment(sketch, "E4776", {"start": v(416.49, 32.77) * mm, "end": v(411.41, 34.75) * mm});
            skLineSegment(sketch, "E4777", {"start": v(411.41, 34.75) * mm, "end": v(407.95, 36.16) * mm});
            skLineSegment(sketch, "E4778", {"start": v(407.95, 36.16) * mm, "end": v(406.8, 36.64) * mm});
            skLineSegment(sketch, "E4779", {"start": v(406.8, 36.64) * mm, "end": v(404.68, 37.53) * mm});
            skLineSegment(sketch, "E4780", {"start": v(404.68, 37.53) * mm, "end": v(398.38, 40.33) * mm});
            skLineSegment(sketch, "E4781", {"start": v(398.38, 40.33) * mm, "end": v(390.51, 44.06) * mm});
            skLineSegment(sketch, "E4782", {"start": v(390.51, 44.06) * mm, "end": v(383.15, 47.87) * mm});
            skLineSegment(sketch, "E4783", {"start": v(383.15, 47.87) * mm, "end": v(376.2, 51.78) * mm});
            skLineSegment(sketch, "E4784", {"start": v(376.2, 51.78) * mm, "end": v(369.61, 55.8) * mm});
            skLineSegment(sketch, "E4785", {"start": v(369.61, 55.8) * mm, "end": v(363.31, 59.97) * mm});
            skLineSegment(sketch, "E4786", {"start": v(363.31, 59.97) * mm, "end": v(357.22, 64.3) * mm});
            skLineSegment(sketch, "E4787", {"start": v(357.22, 64.3) * mm, "end": v(351.29, 68.83) * mm});
            skLineSegment(sketch, "E4788", {"start": v(351.29, 68.83) * mm, "end": v(345.43, 73.58) * mm});
            skLineSegment(sketch, "E4789", {"start": v(345.43, 73.58) * mm, "end": v(339.58, 78.56) * mm});
            skLineSegment(sketch, "E4790", {"start": v(339.58, 78.56) * mm, "end": v(333.66, 83.8) * mm});
            skLineSegment(sketch, "E4791", {"start": v(333.66, 83.8) * mm, "end": v(327.62, 89.33) * mm});
            skLineSegment(sketch, "E4792", {"start": v(327.62, 89.33) * mm, "end": v(321.39, 95.18) * mm});
            skLineSegment(sketch, "E4793", {"start": v(321.39, 95.18) * mm, "end": v(314.88, 101.36) * mm});
            skLineSegment(sketch, "E4794", {"start": v(314.88, 101.36) * mm, "end": v(308.03, 107.9) * mm});
            skLineSegment(sketch, "E4795", {"start": v(308.03, 107.9) * mm, "end": v(302.6, 113.08) * mm});
            skLineSegment(sketch, "E4796", {"start": v(302.6, 113.08) * mm, "end": v(300.79, 114.8) * mm});
            skLineSegment(sketch, "E4797", {"start": v(300.79, 114.8) * mm, "end": v(298.94, 116.57) * mm});
            skLineSegment(sketch, "E4798", {"start": v(298.94, 116.57) * mm, "end": v(293.36, 121.79) * mm});
            skLineSegment(sketch, "E4799", {"start": v(293.36, 121.79) * mm, "end": v(286, 128.53) * mm});
            skLineSegment(sketch, "E4800", {"start": v(286, 128.53) * mm, "end": v(278.66, 135.1) * mm});
            skLineSegment(sketch, "E4801", {"start": v(278.66, 135.1) * mm, "end": v(271.28, 141.6) * mm});
            skLineSegment(sketch, "E4802", {"start": v(271.28, 141.6) * mm, "end": v(263.81, 148.07) * mm});
            skLineSegment(sketch, "E4803", {"start": v(263.81, 148.07) * mm, "end": v(256.2, 154.59) * mm});
            skLineSegment(sketch, "E4804", {"start": v(256.2, 154.59) * mm, "end": v(248.4, 161.23) * mm});
            skLineSegment(sketch, "E4805", {"start": v(248.4, 161.23) * mm, "end": v(240.36, 168.07) * mm});
            skLineSegment(sketch, "E4806", {"start": v(240.36, 168.07) * mm, "end": v(232.02, 175.18) * mm});
            skLineSegment(sketch, "E4807", {"start": v(232.02, 175.18) * mm, "end": v(223.34, 182.62) * mm});
            skLineSegment(sketch, "E4808", {"start": v(223.34, 182.62) * mm, "end": v(214.25, 190.47) * mm});
            skLineSegment(sketch, "E4809", {"start": v(214.25, 190.47) * mm, "end": v(204.72, 198.8) * mm});
            skLineSegment(sketch, "E4810", {"start": v(204.72, 198.8) * mm, "end": v(194.68, 207.69) * mm});
            skLineSegment(sketch, "E4811", {"start": v(194.68, 207.69) * mm, "end": v(184.1, 217.2) * mm});
            skLineSegment(sketch, "E4812", {"start": v(184.1, 217.2) * mm, "end": v(172.9, 227.4) * mm});
            skLineSegment(sketch, "E4813", {"start": v(172.9, 227.4) * mm, "end": v(164, 235.62) * mm});
            skLineSegment(sketch, "E4814", {"start": v(164, 235.62) * mm, "end": v(161.04, 238.37) * mm});
            skLineSegment(sketch, "E4815", {"start": v(161.04, 238.37) * mm, "end": v(158.11, 241.1) * mm});
            skLineSegment(sketch, "E4816", {"start": v(158.11, 241.1) * mm, "end": v(149.2, 249.13) * mm});
            skLineSegment(sketch, "E4817", {"start": v(149.2, 249.13) * mm, "end": v(138.03, 258.71) * mm});
            skLineSegment(sketch, "E4818", {"start": v(138.03, 258.71) * mm, "end": v(127.52, 267.18) * mm});
            skLineSegment(sketch, "E4819", {"start": v(127.52, 267.18) * mm, "end": v(117.62, 274.6) * mm});
            skLineSegment(sketch, "E4820", {"start": v(117.62, 274.6) * mm, "end": v(108.3, 281.05) * mm});
            skLineSegment(sketch, "E4821", {"start": v(108.3, 281.05) * mm, "end": v(99.54, 286.58) * mm});
            skLineSegment(sketch, "E4822", {"start": v(99.54, 286.58) * mm, "end": v(91.28, 291.27) * mm});
            skLineSegment(sketch, "E4823", {"start": v(91.28, 291.27) * mm, "end": v(83.5, 295.19) * mm});
            skLineSegment(sketch, "E4824", {"start": v(83.5, 295.19) * mm, "end": v(76.17, 298.4) * mm});
            skLineSegment(sketch, "E4825", {"start": v(76.17, 298.4) * mm, "end": v(69.25, 300.98) * mm});
            skLineSegment(sketch, "E4826", {"start": v(69.25, 300.98) * mm, "end": v(62.7, 302.99) * mm});
            skLineSegment(sketch, "E4827", {"start": v(62.7, 302.99) * mm, "end": v(56.5, 304.5) * mm});
            skLineSegment(sketch, "E4828", {"start": v(56.5, 304.5) * mm, "end": v(50.6, 305.57) * mm});
            skLineSegment(sketch, "E4829", {"start": v(50.6, 305.57) * mm, "end": v(44.99, 306.29) * mm});
            skLineSegment(sketch, "E4830", {"start": v(44.99, 306.29) * mm, "end": v(39.61, 306.7) * mm});
            skLineSegment(sketch, "E4831", {"start": v(39.61, 306.7) * mm, "end": v(35.73, 306.86) * mm});
            skLineSegment(sketch, "E4832", {"start": v(35.73, 306.86) * mm, "end": v(34.44, 306.9) * mm});
            skLineSegment(sketch, "E4833", {"start": v(34.44, 306.9) * mm, "end": v(33.09, 306.92) * mm});
            skLineSegment(sketch, "E4834", {"start": v(33.09, 306.92) * mm, "end": v(29.03, 306.53) * mm});
            skLineSegment(sketch, "E4835", {"start": v(29.03, 306.53) * mm, "end": v(22.22, 305.32) * mm});
            skLineSegment(sketch, "E4836", {"start": v(22.22, 305.32) * mm, "end": v(14.19, 303.4) * mm});
            skLineSegment(sketch, "E4837", {"start": v(14.19, 303.4) * mm, "end": v(5.11, 300.88) * mm});
            skLineSegment(sketch, "E4838", {"start": v(5.11, 300.88) * mm, "end": v(-4.82, 297.89) * mm});
            skLineSegment(sketch, "E4839", {"start": v(-4.82, 297.89) * mm, "end": v(-15.45, 294.53) * mm});
            skLineSegment(sketch, "E4840", {"start": v(-15.45, 294.53) * mm, "end": v(-26.58, 290.94) * mm});
            skLineSegment(sketch, "E4841", {"start": v(-26.58, 290.94) * mm, "end": v(-38.04, 287.23) * mm});
            skLineSegment(sketch, "E4842", {"start": v(-38.04, 287.23) * mm, "end": v(-49.65, 283.51) * mm});
            skLineSegment(sketch, "E4843", {"start": v(-49.65, 283.51) * mm, "end": v(-61.24, 279.92) * mm});
            skLineSegment(sketch, "E4844", {"start": v(-61.24, 279.92) * mm, "end": v(-72.6, 276.56) * mm});
            skLineSegment(sketch, "E4845", {"start": v(-72.6, 276.56) * mm, "end": v(-83.6, 273.56) * mm});
            skLineSegment(sketch, "E4846", {"start": v(-83.6, 273.56) * mm, "end": v(-94.02, 271.04) * mm});
            skLineSegment(sketch, "E4847", {"start": v(-94.02, 271.04) * mm, "end": v(-103.7, 269.11) * mm});
            skLineSegment(sketch, "E4848", {"start": v(-103.7, 269.11) * mm, "end": v(-112.44, 267.9) * mm});
            skLineSegment(sketch, "E4849", {"start": v(-112.44, 267.9) * mm, "end": v(-118.18, 267.5) * mm});
            skLineSegment(sketch, "E4850", {"start": v(-118.18, 267.5) * mm, "end": v(-120.1, 267.52) * mm});
            skLineSegment(sketch, "E4851", {"start": v(-120.1, 267.52) * mm, "end": v(-123.17, 267.56) * mm});
            skLineSegment(sketch, "E4852", {"start": v(-123.17, 267.56) * mm, "end": v(-132.4, 267.66) * mm});
            skLineSegment(sketch, "E4853", {"start": v(-132.4, 267.66) * mm, "end": v(-144.06, 267.8) * mm});
            skLineSegment(sketch, "E4854", {"start": v(-144.06, 267.8) * mm, "end": v(-155.04, 268) * mm});
            skLineSegment(sketch, "E4855", {"start": v(-155.04, 268) * mm, "end": v(-165.3, 268.25) * mm});
            skLineSegment(sketch, "E4856", {"start": v(-165.3, 268.25) * mm, "end": v(-174.82, 268.6) * mm});
            skLineSegment(sketch, "E4857", {"start": v(-174.82, 268.6) * mm, "end": v(-183.55, 269.1) * mm});
            skLineSegment(sketch, "E4858", {"start": v(-183.55, 269.1) * mm, "end": v(-191.45, 269.74) * mm});
            skLineSegment(sketch, "E4859", {"start": v(-191.45, 269.74) * mm, "end": v(-196.73, 270.32) * mm});
            skLineSegment(sketch, "E4860", {"start": v(-196.73, 270.32) * mm, "end": v(-198.49, 270.57) * mm});
            skLineSegment(sketch, "E4861", {"start": v(-198.49, 270.57) * mm, "end": v(-200.1, 270.64) * mm});
            skLineSegment(sketch, "E4862", {"start": v(-200.1, 270.64) * mm, "end": v(-204.98, 270.86) * mm});
            skLineSegment(sketch, "E4863", {"start": v(-204.98, 270.86) * mm, "end": v(-210.88, 271.13) * mm});
            skLineSegment(sketch, "E4864", {"start": v(-210.88, 271.13) * mm, "end": v(-216.3, 271.4) * mm});
            skLineSegment(sketch, "E4865", {"start": v(-216.3, 271.4) * mm, "end": v(-221.36, 271.7) * mm});
            skLineSegment(sketch, "E4866", {"start": v(-221.36, 271.7) * mm, "end": v(-226.17, 272.01) * mm});
            skLineSegment(sketch, "E4867", {"start": v(-226.17, 272.01) * mm, "end": v(-230.84, 272.36) * mm});
            skLineSegment(sketch, "E4868", {"start": v(-230.84, 272.36) * mm, "end": v(-235.49, 272.76) * mm});
            skLineSegment(sketch, "E4869", {"start": v(-235.49, 272.76) * mm, "end": v(-240.22, 273.21) * mm});
            skLineSegment(sketch, "E4870", {"start": v(-240.22, 273.21) * mm, "end": v(-245.16, 273.74) * mm});
            skLineSegment(sketch, "E4871", {"start": v(-245.16, 273.74) * mm, "end": v(-250.4, 274.34) * mm});
            skLineSegment(sketch, "E4872", {"start": v(-250.4, 274.34) * mm, "end": v(-256.09, 275.03) * mm});
            skLineSegment(sketch, "E4873", {"start": v(-256.09, 275.03) * mm, "end": v(-262.3, 275.83) * mm});
            skLineSegment(sketch, "E4874", {"start": v(-262.3, 275.83) * mm, "end": v(-269.18, 276.73) * mm});
            skLineSegment(sketch, "E4875", {"start": v(-269.18, 276.73) * mm, "end": v(-276.83, 277.77) * mm});
            skLineSegment(sketch, "E4876", {"start": v(-276.83, 277.77) * mm, "end": v(-285.35, 278.93) * mm});
            skLineSegment(sketch, "E4877", {"start": v(-285.35, 278.93) * mm, "end": v(-292.49, 279.92) * mm});
            skLineSegment(sketch, "E4878", {"start": v(-292.49, 279.92) * mm, "end": v(-294.87, 280.24) * mm});
            skLineSegment(sketch, "E4879", {"start": v(-294.87, 280.24) * mm, "end": v(-296.57, 280.48) * mm});
            skLineSegment(sketch, "E4880", {"start": v(-296.57, 280.48) * mm, "end": v(-301.64, 281.46) * mm});
            skLineSegment(sketch, "E4881", {"start": v(-301.64, 281.46) * mm, "end": v(-308.54, 283.14) * mm});
            skLineSegment(sketch, "E4882", {"start": v(-308.54, 283.14) * mm, "end": v(-315.57, 285.1) * mm});
            skLineSegment(sketch, "E4883", {"start": v(-315.57, 285.1) * mm, "end": v(-322.73, 287.21) * mm});
            skLineSegment(sketch, "E4884", {"start": v(-322.73, 287.21) * mm, "end": v(-330.02, 289.28) * mm});
            skLineSegment(sketch, "E4885", {"start": v(-330.02, 289.28) * mm, "end": v(-337.46, 291.14) * mm});
            skLineSegment(sketch, "E4886", {"start": v(-337.46, 291.14) * mm, "end": v(-345.04, 292.65) * mm});
            skLineSegment(sketch, "E4887", {"start": v(-345.04, 292.65) * mm, "end": v(-350.84, 293.46) * mm});
            skLineSegment(sketch, "E4888", {"start": v(-350.84, 293.46) * mm, "end": v(-352.78, 293.62) * mm});
            skLineSegment(sketch, "E4889", {"start": v(-352.78, 293.62) * mm, "end": v(-355.1, 293.8) * mm});
            skLineSegment(sketch, "E4890", {"start": v(-355.1, 293.8) * mm, "end": v(-362.07, 294.2) * mm});
            skLineSegment(sketch, "E4891", {"start": v(-362.07, 294.2) * mm, "end": v(-370.74, 294.43) * mm});
            skLineSegment(sketch, "E4892", {"start": v(-370.74, 294.43) * mm, "end": v(-379.08, 294.44) * mm});
            skLineSegment(sketch, "E4893", {"start": v(-379.08, 294.44) * mm, "end": v(-387.37, 294.4) * mm});
            skLineSegment(sketch, "E4894", {"start": v(-387.37, 294.4) * mm, "end": v(-395.93, 294.43) * mm});
            skLineSegment(sketch, "E4895", {"start": v(-395.93, 294.43) * mm, "end": v(-405.04, 294.7) * mm});
            skLineSegment(sketch, "E4896", {"start": v(-405.04, 294.7) * mm, "end": v(-415, 295.33) * mm});
            skLineSegment(sketch, "E4897", {"start": v(-415, 295.33) * mm, "end": v(-423.33, 296.13) * mm});
            skLineSegment(sketch, "E4898", {"start": v(-423.33, 296.13) * mm, "end": v(-426.1, 296.47) * mm});
            skLineSegment(sketch, "E4899", {"start": v(-426.1, 296.47) * mm, "end": v(-427.57, 296.65) * mm});
            skLineSegment(sketch, "E4900", {"start": v(-427.57, 296.65) * mm, "end": v(-431.99, 297.21) * mm});
            skLineSegment(sketch, "E4901", {"start": v(-431.99, 297.21) * mm, "end": v(-438.99, 298.1) * mm});
            skLineSegment(sketch, "E4902", {"start": v(-438.99, 298.1) * mm, "end": v(-446.9, 299.1) * mm});
            skLineSegment(sketch, "E4903", {"start": v(-446.9, 299.1) * mm, "end": v(-455.5, 300.2) * mm});
            skLineSegment(sketch, "E4904", {"start": v(-455.5, 300.2) * mm, "end": v(-464.58, 301.38) * mm});
            skLineSegment(sketch, "E4905", {"start": v(-464.58, 301.38) * mm, "end": v(-473.97, 302.6) * mm});
            skLineSegment(sketch, "E4906", {"start": v(-473.97, 302.6) * mm, "end": v(-483.43, 303.82) * mm});
            skLineSegment(sketch, "E4907", {"start": v(-483.43, 303.82) * mm, "end": v(-492.77, 305.03) * mm});
            skLineSegment(sketch, "E4908", {"start": v(-492.77, 305.03) * mm, "end": v(-501.78, 306.2) * mm});
            skLineSegment(sketch, "E4909", {"start": v(-501.78, 306.2) * mm, "end": v(-510.25, 307.31) * mm});
            skLineSegment(sketch, "E4910", {"start": v(-510.25, 307.31) * mm, "end": v(-517.99, 308.32) * mm});
            skLineSegment(sketch, "E4911", {"start": v(-517.99, 308.32) * mm, "end": v(-524.78, 309.21) * mm});
            skLineSegment(sketch, "E4912", {"start": v(-524.78, 309.21) * mm, "end": v(-530.42, 309.95) * mm});
            skLineSegment(sketch, "E4913", {"start": v(-530.42, 309.95) * mm, "end": v(-534.7, 310.5) * mm});
            skLineSegment(sketch, "E4914", {"start": v(-534.7, 310.5) * mm, "end": v(-537.42, 310.87) * mm});
            skLineSegment(sketch, "E4915", {"start": v(-537.42, 310.87) * mm, "end": v(-538.37, 311) * mm});
            skLineSegment(sketch, "E4916", {"start": v(607.08, -42.39) * mm, "end": v(606.43, -42.4) * mm});
            skLineSegment(sketch, "E4917", {"start": v(606.43, -42.4) * mm, "end": v(604.47, -42.32) * mm});
            skLineSegment(sketch, "E4918", {"start": v(604.47, -42.32) * mm, "end": v(601.27, -42.04) * mm});
            skLineSegment(sketch, "E4919", {"start": v(601.27, -42.04) * mm, "end": v(597.52, -41.56) * mm});
            skLineSegment(sketch, "E4920", {"start": v(597.52, -41.56) * mm, "end": v(593.24, -40.89) * mm});
            skLineSegment(sketch, "E4921", {"start": v(593.24, -40.89) * mm, "end": v(588.48, -40.04) * mm});
            skLineSegment(sketch, "E4922", {"start": v(588.48, -40.04) * mm, "end": v(583.26, -39.01) * mm});
            skLineSegment(sketch, "E4923", {"start": v(583.26, -39.01) * mm, "end": v(577.62, -37.83) * mm});
            skLineSegment(sketch, "E4924", {"start": v(577.62, -37.83) * mm, "end": v(571.6, -36.5) * mm});
            skLineSegment(sketch, "E4925", {"start": v(571.6, -36.5) * mm, "end": v(565.25, -35.03) * mm});
            skLineSegment(sketch, "E4926", {"start": v(565.25, -35.03) * mm, "end": v(558.57, -33.43) * mm});
            skLineSegment(sketch, "E4927", {"start": v(558.57, -33.43) * mm, "end": v(551.62, -31.7) * mm});
            skLineSegment(sketch, "E4928", {"start": v(551.62, -31.7) * mm, "end": v(544.43, -29.88) * mm});
            skLineSegment(sketch, "E4929", {"start": v(544.43, -29.88) * mm, "end": v(537.03, -27.95) * mm});
            skLineSegment(sketch, "E4930", {"start": v(537.03, -27.95) * mm, "end": v(529.47, -25.94) * mm});
            skLineSegment(sketch, "E4931", {"start": v(529.47, -25.94) * mm, "end": v(521.77, -23.84) * mm});
            skLineSegment(sketch, "E4932", {"start": v(521.77, -23.84) * mm, "end": v(513.96, -21.67) * mm});
            skLineSegment(sketch, "E4933", {"start": v(513.96, -21.67) * mm, "end": v(506.1, -19.45) * mm});
            skLineSegment(sketch, "E4934", {"start": v(506.1, -19.45) * mm, "end": v(498.2, -17.18) * mm});
            skLineSegment(sketch, "E4935", {"start": v(498.2, -17.18) * mm, "end": v(490.3, -14.87) * mm});
            skLineSegment(sketch, "E4936", {"start": v(490.3, -14.87) * mm, "end": v(482.46, -12.53) * mm});
            skLineSegment(sketch, "E4937", {"start": v(482.46, -12.53) * mm, "end": v(474.69, -10.17) * mm});
            skLineSegment(sketch, "E4938", {"start": v(474.69, -10.17) * mm, "end": v(467.02, -7.81) * mm});
            skLineSegment(sketch, "E4939", {"start": v(467.02, -7.81) * mm, "end": v(459.51, -5.45) * mm});
            skLineSegment(sketch, "E4940", {"start": v(459.51, -5.45) * mm, "end": v(452.18, -3.1) * mm});
            skLineSegment(sketch, "E4941", {"start": v(452.18, -3.1) * mm, "end": v(445.06, -0.77) * mm});
            skLineSegment(sketch, "E4942", {"start": v(445.06, -0.77) * mm, "end": v(438.2, 1.52) * mm});
            skLineSegment(sketch, "E4943", {"start": v(438.2, 1.52) * mm, "end": v(431.62, 3.77) * mm});
            skLineSegment(sketch, "E4944", {"start": v(431.62, 3.77) * mm, "end": v(425.37, 5.97) * mm});
            skLineSegment(sketch, "E4945", {"start": v(425.37, 5.97) * mm, "end": v(419.48, 8.1) * mm});
            skLineSegment(sketch, "E4946", {"start": v(419.48, 8.1) * mm, "end": v(413.97, 10.17) * mm});
            skLineSegment(sketch, "E4947", {"start": v(413.97, 10.17) * mm, "end": v(408.9, 12.15) * mm});
            skLineSegment(sketch, "E4948", {"start": v(408.9, 12.15) * mm, "end": v(405.44, 13.55) * mm});
            skLineSegment(sketch, "E4949", {"start": v(405.44, 13.55) * mm, "end": v(404.3, 14.03) * mm});
            skLineSegment(sketch, "E4950", {"start": v(404.3, 14.03) * mm, "end": v(402.18, 14.93) * mm});
            skLineSegment(sketch, "E4951", {"start": v(402.18, 14.93) * mm, "end": v(395.87, 17.72) * mm});
            skLineSegment(sketch, "E4952", {"start": v(395.87, 17.72) * mm, "end": v(388, 21.46) * mm});
            skLineSegment(sketch, "E4953", {"start": v(388, 21.46) * mm, "end": v(380.64, 25.27) * mm});
            skLineSegment(sketch, "E4954", {"start": v(380.64, 25.27) * mm, "end": v(373.69, 29.17) * mm});
            skLineSegment(sketch, "E4955", {"start": v(373.69, 29.17) * mm, "end": v(367.1, 33.2) * mm});
            skLineSegment(sketch, "E4956", {"start": v(367.1, 33.2) * mm, "end": v(360.8, 37.37) * mm});
            skLineSegment(sketch, "E4957", {"start": v(360.8, 37.37) * mm, "end": v(354.71, 41.7) * mm});
            skLineSegment(sketch, "E4958", {"start": v(354.71, 41.7) * mm, "end": v(348.78, 46.23) * mm});
            skLineSegment(sketch, "E4959", {"start": v(348.78, 46.23) * mm, "end": v(342.92, 50.98) * mm});
            skLineSegment(sketch, "E4960", {"start": v(342.92, 50.98) * mm, "end": v(337.06, 55.96) * mm});
            skLineSegment(sketch, "E4961", {"start": v(337.06, 55.96) * mm, "end": v(331.16, 61.2) * mm});
            skLineSegment(sketch, "E4962", {"start": v(331.16, 61.2) * mm, "end": v(325.12, 66.73) * mm});
            skLineSegment(sketch, "E4963", {"start": v(325.12, 66.73) * mm, "end": v(318.88, 72.58) * mm});
            skLineSegment(sketch, "E4964", {"start": v(318.88, 72.58) * mm, "end": v(312.37, 78.75) * mm});
            skLineSegment(sketch, "E4965", {"start": v(312.37, 78.75) * mm, "end": v(305.53, 85.29) * mm});
            skLineSegment(sketch, "E4966", {"start": v(305.53, 85.29) * mm, "end": v(300.09, 90.48) * mm});
            skLineSegment(sketch, "E4967", {"start": v(300.09, 90.48) * mm, "end": v(298.28, 92.2) * mm});
            skLineSegment(sketch, "E4968", {"start": v(298.28, 92.2) * mm, "end": v(296.43, 93.96) * mm});
            skLineSegment(sketch, "E4969", {"start": v(296.43, 93.96) * mm, "end": v(290.85, 99.18) * mm});
            skLineSegment(sketch, "E4970", {"start": v(290.85, 99.18) * mm, "end": v(283.5, 105.93) * mm});
            skLineSegment(sketch, "E4971", {"start": v(283.5, 105.93) * mm, "end": v(276.15, 112.5) * mm});
            skLineSegment(sketch, "E4972", {"start": v(276.15, 112.5) * mm, "end": v(268.77, 119) * mm});
            skLineSegment(sketch, "E4973", {"start": v(268.77, 119) * mm, "end": v(261.3, 125.46) * mm});
            skLineSegment(sketch, "E4974", {"start": v(261.3, 125.46) * mm, "end": v(253.7, 131.99) * mm});
            skLineSegment(sketch, "E4975", {"start": v(253.7, 131.99) * mm, "end": v(245.9, 138.63) * mm});
            skLineSegment(sketch, "E4976", {"start": v(245.9, 138.63) * mm, "end": v(237.85, 145.47) * mm});
            skLineSegment(sketch, "E4977", {"start": v(237.85, 145.47) * mm, "end": v(229.51, 152.58) * mm});
            skLineSegment(sketch, "E4978", {"start": v(229.51, 152.58) * mm, "end": v(220.82, 160.02) * mm});
            skLineSegment(sketch, "E4979", {"start": v(220.82, 160.02) * mm, "end": v(211.74, 167.87) * mm});
            skLineSegment(sketch, "E4980", {"start": v(211.74, 167.87) * mm, "end": v(202.2, 176.2) * mm});
            skLineSegment(sketch, "E4981", {"start": v(202.2, 176.2) * mm, "end": v(192.17, 185.08) * mm});
            skLineSegment(sketch, "E4982", {"start": v(192.17, 185.08) * mm, "end": v(181.58, 194.6) * mm});
            skLineSegment(sketch, "E4983", {"start": v(181.58, 194.6) * mm, "end": v(170.38, 204.8) * mm});
            skLineSegment(sketch, "E4984", {"start": v(170.38, 204.8) * mm, "end": v(161.48, 213.01) * mm});
            skLineSegment(sketch, "E4985", {"start": v(161.48, 213.01) * mm, "end": v(158.53, 215.77) * mm});
            skLineSegment(sketch, "E4986", {"start": v(158.53, 215.77) * mm, "end": v(155.58, 218.52) * mm});
            skLineSegment(sketch, "E4987", {"start": v(155.58, 218.52) * mm, "end": v(146.58, 226.58) * mm});
            skLineSegment(sketch, "E4988", {"start": v(146.58, 226.58) * mm, "end": v(135.13, 236.3) * mm});
            skLineSegment(sketch, "E4989", {"start": v(135.13, 236.3) * mm, "end": v(124.17, 244.96) * mm});
            skLineSegment(sketch, "E4990", {"start": v(124.17, 244.96) * mm, "end": v(113.69, 252.65) * mm});
            skLineSegment(sketch, "E4991", {"start": v(113.69, 252.65) * mm, "end": v(103.68, 259.4) * mm});
            skLineSegment(sketch, "E4992", {"start": v(103.68, 259.4) * mm, "end": v(94.15, 265.25) * mm});
            skLineSegment(sketch, "E4993", {"start": v(94.15, 265.25) * mm, "end": v(85.07, 270.27) * mm});
            skLineSegment(sketch, "E4994", {"start": v(85.07, 270.27) * mm, "end": v(76.44, 274.51) * mm});
            skLineSegment(sketch, "E4995", {"start": v(76.44, 274.51) * mm, "end": v(68.26, 278.03) * mm});
            skLineSegment(sketch, "E4996", {"start": v(68.26, 278.03) * mm, "end": v(60.51, 280.87) * mm});
            skLineSegment(sketch, "E4997", {"start": v(60.51, 280.87) * mm, "end": v(53.2, 283.08) * mm});
            skLineSegment(sketch, "E4998", {"start": v(53.2, 283.08) * mm, "end": v(46.31, 284.73) * mm});
            skLineSegment(sketch, "E4999", {"start": v(46.31, 284.73) * mm, "end": v(39.84, 285.86) * mm});
            skLineSegment(sketch, "E5000", {"start": v(39.84, 285.86) * mm, "end": v(33.77, 286.52) * mm});
            skLineSegment(sketch, "E5001", {"start": v(33.77, 286.52) * mm, "end": v(28.11, 286.76) * mm});
            skLineSegment(sketch, "E5002", {"start": v(28.11, 286.76) * mm, "end": v(24.15, 286.73) * mm});
            skLineSegment(sketch, "E5003", {"start": v(24.15, 286.73) * mm, "end": v(22.84, 286.65) * mm});
            skLineSegment(sketch, "E5004", {"start": v(22.84, 286.65) * mm, "end": v(21.3, 286.57) * mm});
            skLineSegment(sketch, "E5005", {"start": v(21.3, 286.57) * mm, "end": v(16.66, 286.02) * mm});
            skLineSegment(sketch, "E5006", {"start": v(16.66, 286.02) * mm, "end": v(9.41, 284.77) * mm});
            skLineSegment(sketch, "E5007", {"start": v(9.41, 284.77) * mm, "end": v(1.22, 283) * mm});
            skLineSegment(sketch, "E5008", {"start": v(1.22, 283) * mm, "end": v(-7.76, 280.77) * mm});
            skLineSegment(sketch, "E5009", {"start": v(-7.76, 280.77) * mm, "end": v(-17.4, 278.2) * mm});
            skLineSegment(sketch, "E5010", {"start": v(-17.4, 278.2) * mm, "end": v(-27.54, 275.34) * mm});
            skLineSegment(sketch, "E5011", {"start": v(-27.54, 275.34) * mm, "end": v(-38.06, 272.3) * mm});
            skLineSegment(sketch, "E5012", {"start": v(-38.06, 272.3) * mm, "end": v(-48.8, 269.15) * mm});
            skLineSegment(sketch, "E5013", {"start": v(-48.8, 269.15) * mm, "end": v(-59.64, 265.98) * mm});
            skLineSegment(sketch, "E5014", {"start": v(-59.64, 265.98) * mm, "end": v(-70.42, 262.87) * mm});
            skLineSegment(sketch, "E5015", {"start": v(-70.42, 262.87) * mm, "end": v(-81.01, 259.91) * mm});
            skLineSegment(sketch, "E5016", {"start": v(-81.01, 259.91) * mm, "end": v(-91.27, 257.18) * mm});
            skLineSegment(sketch, "E5017", {"start": v(-91.27, 257.18) * mm, "end": v(-101.05, 254.77) * mm});
            skLineSegment(sketch, "E5018", {"start": v(-101.05, 254.77) * mm, "end": v(-110.2, 252.75) * mm});
            skLineSegment(sketch, "E5019", {"start": v(-110.2, 252.75) * mm, "end": v(-118.61, 251.22) * mm});
            skLineSegment(sketch, "E5020", {"start": v(-118.61, 251.22) * mm, "end": v(-124.24, 250.43) * mm});
            skLineSegment(sketch, "E5021", {"start": v(-124.24, 250.43) * mm, "end": v(-126.12, 250.25) * mm});
            skLineSegment(sketch, "E5022", {"start": v(-126.12, 250.25) * mm, "end": v(-129.35, 249.95) * mm});
            skLineSegment(sketch, "E5023", {"start": v(-129.35, 249.95) * mm, "end": v(-139.07, 249.2) * mm});
            skLineSegment(sketch, "E5024", {"start": v(-139.07, 249.2) * mm, "end": v(-152.04, 248.44) * mm});
            skLineSegment(sketch, "E5025", {"start": v(-152.04, 248.44) * mm, "end": v(-164.87, 247.94) * mm});
            skLineSegment(sketch, "E5026", {"start": v(-164.87, 247.94) * mm, "end": v(-177.39, 247.7) * mm});
            skLineSegment(sketch, "E5027", {"start": v(-177.39, 247.7) * mm, "end": v(-189.42, 247.68) * mm});
            skLineSegment(sketch, "E5028", {"start": v(-189.42, 247.68) * mm, "end": v(-200.78, 247.9) * mm});
            skLineSegment(sketch, "E5029", {"start": v(-200.78, 247.9) * mm, "end": v(-211.32, 248.31) * mm});
            skLineSegment(sketch, "E5030", {"start": v(-211.32, 248.31) * mm, "end": v(-218.46, 248.73) * mm});
            skLineSegment(sketch, "E5031", {"start": v(-218.46, 248.73) * mm, "end": v(-220.84, 248.92) * mm});
            skLineSegment(sketch, "E5032", {"start": v(-220.84, 248.92) * mm, "end": v(-222.4, 248.98) * mm});
            skLineSegment(sketch, "E5033", {"start": v(-222.4, 248.98) * mm, "end": v(-227.08, 249.18) * mm});
            skLineSegment(sketch, "E5034", {"start": v(-227.08, 249.18) * mm, "end": v(-232.28, 249.4) * mm});
            skLineSegment(sketch, "E5035", {"start": v(-232.28, 249.4) * mm, "end": v(-236.6, 249.6) * mm});
            skLineSegment(sketch, "E5036", {"start": v(-236.6, 249.6) * mm, "end": v(-240.22, 249.8) * mm});
            skLineSegment(sketch, "E5037", {"start": v(-240.22, 249.8) * mm, "end": v(-243.34, 250) * mm});
            skLineSegment(sketch, "E5038", {"start": v(-243.34, 250) * mm, "end": v(-246.12, 250.22) * mm});
            skLineSegment(sketch, "E5039", {"start": v(-246.12, 250.22) * mm, "end": v(-248.75, 250.47) * mm});
            skLineSegment(sketch, "E5040", {"start": v(-248.75, 250.47) * mm, "end": v(-251.4, 250.78) * mm});
            skLineSegment(sketch, "E5041", {"start": v(-251.4, 250.78) * mm, "end": v(-254.25, 251.15) * mm});
            skLineSegment(sketch, "E5042", {"start": v(-254.25, 251.15) * mm, "end": v(-257.48, 251.62) * mm});
            skLineSegment(sketch, "E5043", {"start": v(-257.48, 251.62) * mm, "end": v(-261.27, 252.18) * mm});
            skLineSegment(sketch, "E5044", {"start": v(-261.27, 252.18) * mm, "end": v(-265.8, 252.85) * mm});
            skLineSegment(sketch, "E5045", {"start": v(-265.8, 252.85) * mm, "end": v(-271.25, 253.66) * mm});
            skLineSegment(sketch, "E5046", {"start": v(-271.25, 253.66) * mm, "end": v(-277.79, 254.61) * mm});
            skLineSegment(sketch, "E5047", {"start": v(-277.79, 254.61) * mm, "end": v(-285.6, 255.73) * mm});
            skLineSegment(sketch, "E5048", {"start": v(-285.6, 255.73) * mm, "end": v(-292.55, 256.7) * mm});
            skLineSegment(sketch, "E5049", {"start": v(-292.55, 256.7) * mm, "end": v(-294.87, 257.02) * mm});
            skLineSegment(sketch, "E5050", {"start": v(-294.87, 257.02) * mm, "end": v(-296.6, 257.26) * mm});
            skLineSegment(sketch, "E5051", {"start": v(-296.6, 257.26) * mm, "end": v(-301.75, 258.39) * mm});
            skLineSegment(sketch, "E5052", {"start": v(-301.75, 258.39) * mm, "end": v(-308.95, 260.45) * mm});
            skLineSegment(sketch, "E5053", {"start": v(-308.95, 260.45) * mm, "end": v(-316.39, 262.98) * mm});
            skLineSegment(sketch, "E5054", {"start": v(-316.39, 262.98) * mm, "end": v(-324.02, 265.7) * mm});
            skLineSegment(sketch, "E5055", {"start": v(-324.02, 265.7) * mm, "end": v(-331.8, 268.4) * mm});
            skLineSegment(sketch, "E5056", {"start": v(-331.8, 268.4) * mm, "end": v(-339.65, 270.82) * mm});
            skLineSegment(sketch, "E5057", {"start": v(-339.65, 270.82) * mm, "end": v(-347.53, 272.72) * mm});
            skLineSegment(sketch, "E5058", {"start": v(-347.53, 272.72) * mm, "end": v(-353.4, 273.67) * mm});
            skLineSegment(sketch, "E5059", {"start": v(-353.4, 273.67) * mm, "end": v(-355.37, 273.83) * mm});
            skLineSegment(sketch, "E5060", {"start": v(-355.37, 273.83) * mm, "end": v(-357.77, 274.03) * mm});
            skLineSegment(sketch, "E5061", {"start": v(-357.77, 274.03) * mm, "end": v(-364.97, 274.45) * mm});
            skLineSegment(sketch, "E5062", {"start": v(-364.97, 274.45) * mm, "end": v(-374.37, 274.78) * mm});
            skLineSegment(sketch, "E5063", {"start": v(-374.37, 274.78) * mm, "end": v(-383.64, 274.93) * mm});
            skLineSegment(sketch, "E5064", {"start": v(-383.64, 274.93) * mm, "end": v(-392.8, 275.03) * mm});
            skLineSegment(sketch, "E5065", {"start": v(-392.8, 275.03) * mm, "end": v(-401.9, 275.2) * mm});
            skLineSegment(sketch, "E5066", {"start": v(-401.9, 275.2) * mm, "end": v(-411, 275.57) * mm});
            skLineSegment(sketch, "E5067", {"start": v(-411, 275.57) * mm, "end": v(-420.11, 276.26) * mm});
            skLineSegment(sketch, "E5068", {"start": v(-420.11, 276.26) * mm, "end": v(-427.03, 277.05) * mm});
            skLineSegment(sketch, "E5069", {"start": v(-427.03, 277.05) * mm, "end": v(-429.31, 277.4) * mm});
            skLineSegment(sketch, "E5070", {"start": v(-429.31, 277.4) * mm, "end": v(-430.8, 277.62) * mm});
            skLineSegment(sketch, "E5071", {"start": v(-430.8, 277.62) * mm, "end": v(-435.27, 278.26) * mm});
            skLineSegment(sketch, "E5072", {"start": v(-435.27, 278.26) * mm, "end": v(-442.14, 279.22) * mm});
            skLineSegment(sketch, "E5073", {"start": v(-442.14, 279.22) * mm, "end": v(-449.77, 280.24) * mm});
            skLineSegment(sketch, "E5074", {"start": v(-449.77, 280.24) * mm, "end": v(-457.97, 281.3) * mm});
            skLineSegment(sketch, "E5075", {"start": v(-457.97, 281.3) * mm, "end": v(-466.55, 282.4) * mm});
            skLineSegment(sketch, "E5076", {"start": v(-466.55, 282.4) * mm, "end": v(-475.33, 283.49) * mm});
            skLineSegment(sketch, "E5077", {"start": v(-475.33, 283.49) * mm, "end": v(-484.14, 284.58) * mm});
            skLineSegment(sketch, "E5078", {"start": v(-484.14, 284.58) * mm, "end": v(-492.8, 285.63) * mm});
            skLineSegment(sketch, "E5079", {"start": v(-492.8, 285.63) * mm, "end": v(-501.1, 286.63) * mm});
            skLineSegment(sketch, "E5080", {"start": v(-501.1, 286.63) * mm, "end": v(-508.9, 287.56) * mm});
            skLineSegment(sketch, "E5081", {"start": v(-508.9, 287.56) * mm, "end": v(-515.99, 288.4) * mm});
            skLineSegment(sketch, "E5082", {"start": v(-515.99, 288.4) * mm, "end": v(-522.2, 289.14) * mm});
            skLineSegment(sketch, "E5083", {"start": v(-522.2, 289.14) * mm, "end": v(-527.34, 289.74) * mm});
            skLineSegment(sketch, "E5084", {"start": v(-527.34, 289.74) * mm, "end": v(-531.24, 290.2) * mm});
            skLineSegment(sketch, "E5085", {"start": v(-531.24, 290.2) * mm, "end": v(-533.71, 290.48) * mm});
            skLineSegment(sketch, "E5086", {"start": v(-533.71, 290.48) * mm, "end": v(-534.58, 290.58) * mm});
            skLineSegment(sketch, "E5087", {"start": v(609.9, -67.08) * mm, "end": v(609.24, -67.09) * mm});
            skLineSegment(sketch, "E5088", {"start": v(609.24, -67.09) * mm, "end": v(607.25, -66.99) * mm});
            skLineSegment(sketch, "E5089", {"start": v(607.25, -66.99) * mm, "end": v(603.93, -66.65) * mm});
            skLineSegment(sketch, "E5090", {"start": v(603.93, -66.65) * mm, "end": v(599.97, -66.08) * mm});
            skLineSegment(sketch, "E5091", {"start": v(599.97, -66.08) * mm, "end": v(595.43, -65.28) * mm});
            skLineSegment(sketch, "E5092", {"start": v(595.43, -65.28) * mm, "end": v(590.33, -64.27) * mm});
            skLineSegment(sketch, "E5093", {"start": v(590.33, -64.27) * mm, "end": v(584.71, -63.07) * mm});
            skLineSegment(sketch, "E5094", {"start": v(584.71, -63.07) * mm, "end": v(578.64, -61.67) * mm});
            skLineSegment(sketch, "E5095", {"start": v(578.64, -61.67) * mm, "end": v(572.13, -60.1) * mm});
            skLineSegment(sketch, "E5096", {"start": v(572.13, -60.1) * mm, "end": v(565.24, -58.36) * mm});
            skLineSegment(sketch, "E5097", {"start": v(565.24, -58.36) * mm, "end": v(558, -56.47) * mm});
            skLineSegment(sketch, "E5098", {"start": v(558, -56.47) * mm, "end": v(550.44, -54.44) * mm});
            skLineSegment(sketch, "E5099", {"start": v(550.44, -54.44) * mm, "end": v(542.63, -52.27) * mm});
            skLineSegment(sketch, "E5100", {"start": v(542.63, -52.27) * mm, "end": v(534.6, -50) * mm});
            skLineSegment(sketch, "E5101", {"start": v(534.6, -50) * mm, "end": v(526.38, -47.61) * mm});
            skLineSegment(sketch, "E5102", {"start": v(526.38, -47.61) * mm, "end": v(518.02, -45.13) * mm});
            skLineSegment(sketch, "E5103", {"start": v(518.02, -45.13) * mm, "end": v(509.57, -42.57) * mm});
            skLineSegment(sketch, "E5104", {"start": v(509.57, -42.57) * mm, "end": v(501.05, -39.94) * mm});
            skLineSegment(sketch, "E5105", {"start": v(501.05, -39.94) * mm, "end": v(492.51, -37.25) * mm});
            skLineSegment(sketch, "E5106", {"start": v(492.51, -37.25) * mm, "end": v(484, -34.51) * mm});
            skLineSegment(sketch, "E5107", {"start": v(484, -34.51) * mm, "end": v(475.56, -31.74) * mm});
            skLineSegment(sketch, "E5108", {"start": v(475.56, -31.74) * mm, "end": v(467.21, -28.95) * mm});
            skLineSegment(sketch, "E5109", {"start": v(467.21, -28.95) * mm, "end": v(459.01, -26.14) * mm});
            skLineSegment(sketch, "E5110", {"start": v(459.01, -26.14) * mm, "end": v(451, -23.34) * mm});
            skLineSegment(sketch, "E5111", {"start": v(451, -23.34) * mm, "end": v(443.22, -20.54) * mm});
            skLineSegment(sketch, "E5112", {"start": v(443.22, -20.54) * mm, "end": v(435.7, -17.77) * mm});
            skLineSegment(sketch, "E5113", {"start": v(435.7, -17.77) * mm, "end": v(428.5, -15.04) * mm});
            skLineSegment(sketch, "E5114", {"start": v(428.5, -15.04) * mm, "end": v(421.65, -12.36) * mm});
            skLineSegment(sketch, "E5115", {"start": v(421.65, -12.36) * mm, "end": v(415.2, -9.73) * mm});
            skLineSegment(sketch, "E5116", {"start": v(415.2, -9.73) * mm, "end": v(409.17, -7.18) * mm});
            skLineSegment(sketch, "E5117", {"start": v(409.17, -7.18) * mm, "end": v(403.62, -4.7) * mm});
            skLineSegment(sketch, "E5118", {"start": v(403.62, -4.7) * mm, "end": v(398.59, -2.33) * mm});
            skLineSegment(sketch, "E5119", {"start": v(398.59, -2.33) * mm, "end": v(395.22, -0.65) * mm});
            skLineSegment(sketch, "E5120", {"start": v(395.22, -0.65) * mm, "end": v(394.1, -0.06) * mm});
            skLineSegment(sketch, "E5121", {"start": v(394.1, -0.06) * mm, "end": v(392.1, 1) * mm});
            skLineSegment(sketch, "E5122", {"start": v(392.1, 1) * mm, "end": v(386.06, 4.19) * mm});
            skLineSegment(sketch, "E5123", {"start": v(386.06, 4.19) * mm, "end": v(378.53, 8.17) * mm});
            skLineSegment(sketch, "E5124", {"start": v(378.53, 8.17) * mm, "end": v(371.47, 11.96) * mm});
            skLineSegment(sketch, "E5125", {"start": v(371.47, 11.96) * mm, "end": v(364.8, 15.6) * mm});
            skLineSegment(sketch, "E5126", {"start": v(364.8, 15.6) * mm, "end": v(358.46, 19.17) * mm});
            skLineSegment(sketch, "E5127", {"start": v(358.46, 19.17) * mm, "end": v(352.37, 22.72) * mm});
            skLineSegment(sketch, "E5128", {"start": v(352.37, 22.72) * mm, "end": v(346.47, 26.32) * mm});
            skLineSegment(sketch, "E5129", {"start": v(346.47, 26.32) * mm, "end": v(340.68, 30.03) * mm});
            skLineSegment(sketch, "E5130", {"start": v(340.68, 30.03) * mm, "end": v(334.96, 33.9) * mm});
            skLineSegment(sketch, "E5131", {"start": v(334.96, 33.9) * mm, "end": v(329.22, 38.01) * mm});
            skLineSegment(sketch, "E5132", {"start": v(329.22, 38.01) * mm, "end": v(323.4, 42.41) * mm});
            skLineSegment(sketch, "E5133", {"start": v(323.4, 42.41) * mm, "end": v(317.42, 47.17) * mm});
            skLineSegment(sketch, "E5134", {"start": v(317.42, 47.17) * mm, "end": v(311.24, 52.34) * mm});
            skLineSegment(sketch, "E5135", {"start": v(311.24, 52.34) * mm, "end": v(304.76, 58) * mm});
            skLineSegment(sketch, "E5136", {"start": v(304.76, 58) * mm, "end": v(297.94, 64.19) * mm});
            skLineSegment(sketch, "E5137", {"start": v(297.94, 64.19) * mm, "end": v(292.5, 69.27) * mm});
            skLineSegment(sketch, "E5138", {"start": v(292.5, 69.27) * mm, "end": v(290.7, 70.98) * mm});
            skLineSegment(sketch, "E5139", {"start": v(290.7, 70.98) * mm, "end": v(288.85, 72.74) * mm});
            skLineSegment(sketch, "E5140", {"start": v(288.85, 72.74) * mm, "end": v(283.27, 77.96) * mm});
            skLineSegment(sketch, "E5141", {"start": v(283.27, 77.96) * mm, "end": v(275.91, 84.7) * mm});
            skLineSegment(sketch, "E5142", {"start": v(275.91, 84.7) * mm, "end": v(268.57, 91.28) * mm});
            skLineSegment(sketch, "E5143", {"start": v(268.57, 91.28) * mm, "end": v(261.18, 97.77) * mm});
            skLineSegment(sketch, "E5144", {"start": v(261.18, 97.77) * mm, "end": v(253.72, 104.24) * mm});
            skLineSegment(sketch, "E5145", {"start": v(253.72, 104.24) * mm, "end": v(246.11, 110.76) * mm});
            skLineSegment(sketch, "E5146", {"start": v(246.11, 110.76) * mm, "end": v(238.3, 117.4) * mm});
            skLineSegment(sketch, "E5147", {"start": v(238.3, 117.4) * mm, "end": v(230.27, 124.24) * mm});
            skLineSegment(sketch, "E5148", {"start": v(230.27, 124.24) * mm, "end": v(221.93, 131.35) * mm});
            skLineSegment(sketch, "E5149", {"start": v(221.93, 131.35) * mm, "end": v(213.24, 138.8) * mm});
            skLineSegment(sketch, "E5150", {"start": v(213.24, 138.8) * mm, "end": v(204.16, 146.64) * mm});
            skLineSegment(sketch, "E5151", {"start": v(204.16, 146.64) * mm, "end": v(194.62, 154.98) * mm});
            skLineSegment(sketch, "E5152", {"start": v(194.62, 154.98) * mm, "end": v(184.59, 163.86) * mm});
            skLineSegment(sketch, "E5153", {"start": v(184.59, 163.86) * mm, "end": v(174, 173.37) * mm});
            skLineSegment(sketch, "E5154", {"start": v(174, 173.37) * mm, "end": v(162.8, 183.57) * mm});
            skLineSegment(sketch, "E5155", {"start": v(162.8, 183.57) * mm, "end": v(153.9, 191.79) * mm});
            skLineSegment(sketch, "E5156", {"start": v(153.9, 191.79) * mm, "end": v(150.95, 194.54) * mm});
            skLineSegment(sketch, "E5157", {"start": v(150.95, 194.54) * mm, "end": v(148.02, 197.27) * mm});
            skLineSegment(sketch, "E5158", {"start": v(148.02, 197.27) * mm, "end": v(139.1, 205.3) * mm});
            skLineSegment(sketch, "E5159", {"start": v(139.1, 205.3) * mm, "end": v(127.94, 214.88) * mm});
            skLineSegment(sketch, "E5160", {"start": v(127.94, 214.88) * mm, "end": v(117.43, 223.35) * mm});
            skLineSegment(sketch, "E5161", {"start": v(117.43, 223.35) * mm, "end": v(107.53, 230.77) * mm});
            skLineSegment(sketch, "E5162", {"start": v(107.53, 230.77) * mm, "end": v(98.21, 237.22) * mm});
            skLineSegment(sketch, "E5163", {"start": v(98.21, 237.22) * mm, "end": v(89.45, 242.75) * mm});
            skLineSegment(sketch, "E5164", {"start": v(89.45, 242.75) * mm, "end": v(81.19, 247.44) * mm});
            skLineSegment(sketch, "E5165", {"start": v(81.19, 247.44) * mm, "end": v(73.41, 251.36) * mm});
            skLineSegment(sketch, "E5166", {"start": v(73.41, 251.36) * mm, "end": v(66.08, 254.57) * mm});
            skLineSegment(sketch, "E5167", {"start": v(66.08, 254.57) * mm, "end": v(59.16, 257.15) * mm});
            skLineSegment(sketch, "E5168", {"start": v(59.16, 257.15) * mm, "end": v(52.61, 259.16) * mm});
            skLineSegment(sketch, "E5169", {"start": v(52.61, 259.16) * mm, "end": v(46.4, 260.67) * mm});
            skLineSegment(sketch, "E5170", {"start": v(46.4, 260.67) * mm, "end": v(40.52, 261.74) * mm});
            skLineSegment(sketch, "E5171", {"start": v(40.52, 261.74) * mm, "end": v(34.9, 262.46) * mm});
            skLineSegment(sketch, "E5172", {"start": v(34.9, 262.46) * mm, "end": v(29.52, 262.87) * mm});
            skLineSegment(sketch, "E5173", {"start": v(29.52, 262.87) * mm, "end": v(25.64, 263.04) * mm});
            skLineSegment(sketch, "E5174", {"start": v(25.64, 263.04) * mm, "end": v(24.34, 263.07) * mm});
            skLineSegment(sketch, "E5175", {"start": v(24.34, 263.07) * mm, "end": v(23, 263.09) * mm});
            skLineSegment(sketch, "E5176", {"start": v(23, 263.09) * mm, "end": v(18.97, 262.92) * mm});
            skLineSegment(sketch, "E5177", {"start": v(18.97, 262.92) * mm, "end": v(12.25, 262.35) * mm});
            skLineSegment(sketch, "E5178", {"start": v(12.25, 262.35) * mm, "end": v(4.35, 261.4) * mm});
            skLineSegment(sketch, "E5179", {"start": v(4.35, 261.4) * mm, "end": v(-4.55, 260.1) * mm});
            skLineSegment(sketch, "E5180", {"start": v(-4.55, 260.1) * mm, "end": v(-14.28, 258.52) * mm});
            skLineSegment(sketch, "E5181", {"start": v(-14.28, 258.52) * mm, "end": v(-24.68, 256.7) * mm});
            skLineSegment(sketch, "E5182", {"start": v(-24.68, 256.7) * mm, "end": v(-35.56, 254.7) * mm});
            skLineSegment(sketch, "E5183", {"start": v(-35.56, 254.7) * mm, "end": v(-46.78, 252.55) * mm});
            skLineSegment(sketch, "E5184", {"start": v(-46.78, 252.55) * mm, "end": v(-58.13, 250.31) * mm});
            skLineSegment(sketch, "E5185", {"start": v(-58.13, 250.31) * mm, "end": v(-69.48, 248.03) * mm});
            skLineSegment(sketch, "E5186", {"start": v(-69.48, 248.03) * mm, "end": v(-80.62, 245.74) * mm});
            skLineSegment(sketch, "E5187", {"start": v(-80.62, 245.74) * mm, "end": v(-91.42, 243.52) * mm});
            skLineSegment(sketch, "E5188", {"start": v(-91.42, 243.52) * mm, "end": v(-101.67, 241.4) * mm});
            skLineSegment(sketch, "E5189", {"start": v(-101.67, 241.4) * mm, "end": v(-111.23, 239.4) * mm});
            skLineSegment(sketch, "E5190", {"start": v(-111.23, 239.4) * mm, "end": v(-119.9, 237.63) * mm});
            skLineSegment(sketch, "E5191", {"start": v(-119.9, 237.63) * mm, "end": v(-125.63, 236.47) * mm});
            skLineSegment(sketch, "E5192", {"start": v(-125.63, 236.47) * mm, "end": v(-127.54, 236.1) * mm});
            skLineSegment(sketch, "E5193", {"start": v(-127.54, 236.1) * mm, "end": v(-130.96, 235.42) * mm});
            skLineSegment(sketch, "E5194", {"start": v(-130.96, 235.42) * mm, "end": v(-141.23, 233.62) * mm});
            skLineSegment(sketch, "E5195", {"start": v(-141.23, 233.62) * mm, "end": v(-154.3, 231.73) * mm});
            skLineSegment(sketch, "E5196", {"start": v(-154.3, 231.73) * mm, "end": v(-166.8, 230.37) * mm});
            skLineSegment(sketch, "E5197", {"start": v(-166.8, 230.37) * mm, "end": v(-178.8, 229.5) * mm});
            skLineSegment(sketch, "E5198", {"start": v(-178.8, 229.5) * mm, "end": v(-190.36, 229.06) * mm});
            skLineSegment(sketch, "E5199", {"start": v(-190.36, 229.06) * mm, "end": v(-201.5, 229.02) * mm});
            skLineSegment(sketch, "E5200", {"start": v(-201.5, 229.02) * mm, "end": v(-212.3, 229.34) * mm});
            skLineSegment(sketch, "E5201", {"start": v(-212.3, 229.34) * mm, "end": v(-222.8, 229.96) * mm});
            skLineSegment(sketch, "E5202", {"start": v(-222.8, 229.96) * mm, "end": v(-233.05, 230.83) * mm});
            skLineSegment(sketch, "E5203", {"start": v(-233.05, 230.83) * mm, "end": v(-243.1, 231.92) * mm});
            skLineSegment(sketch, "E5204", {"start": v(-243.1, 231.92) * mm, "end": v(-253, 233.19) * mm});
            skLineSegment(sketch, "E5205", {"start": v(-253, 233.19) * mm, "end": v(-262.83, 234.57) * mm});
            skLineSegment(sketch, "E5206", {"start": v(-262.83, 234.57) * mm, "end": v(-272.6, 236.04) * mm});
            skLineSegment(sketch, "E5207", {"start": v(-272.6, 236.04) * mm, "end": v(-282.4, 237.54) * mm});
            skLineSegment(sketch, "E5208", {"start": v(-282.4, 237.54) * mm, "end": v(-292.27, 239.03) * mm});
            skLineSegment(sketch, "E5209", {"start": v(-292.27, 239.03) * mm, "end": v(-299.75, 240.12) * mm});
            skLineSegment(sketch, "E5210", {"start": v(-299.75, 240.12) * mm, "end": v(-302.24, 240.46) * mm});
            skLineSegment(sketch, "E5211", {"start": v(-302.24, 240.46) * mm, "end": v(-303.88, 240.68) * mm});
            skLineSegment(sketch, "E5212", {"start": v(-303.88, 240.68) * mm, "end": v(-308.74, 241.71) * mm});
            skLineSegment(sketch, "E5213", {"start": v(-308.74, 241.71) * mm, "end": v(-314.9, 243.47) * mm});
            skLineSegment(sketch, "E5214", {"start": v(-314.9, 243.47) * mm, "end": v(-320.87, 245.58) * mm});
            skLineSegment(sketch, "E5215", {"start": v(-320.87, 245.58) * mm, "end": v(-326.82, 247.83) * mm});
            skLineSegment(sketch, "E5216", {"start": v(-326.82, 247.83) * mm, "end": v(-332.9, 250.05) * mm});
            skLineSegment(sketch, "E5217", {"start": v(-332.9, 250.05) * mm, "end": v(-339.3, 252.05) * mm});
            skLineSegment(sketch, "E5218", {"start": v(-339.3, 252.05) * mm, "end": v(-346.13, 253.64) * mm});
            skLineSegment(sketch, "E5219", {"start": v(-346.13, 253.64) * mm, "end": v(-351.7, 254.49) * mm});
            skLineSegment(sketch, "E5220", {"start": v(-351.7, 254.49) * mm, "end": v(-353.58, 254.64) * mm});
            skLineSegment(sketch, "E5221", {"start": v(-353.58, 254.64) * mm, "end": v(-356.2, 254.86) * mm});
            skLineSegment(sketch, "E5222", {"start": v(-356.2, 254.86) * mm, "end": v(-364.1, 255.25) * mm});
            skLineSegment(sketch, "E5223", {"start": v(-364.1, 255.25) * mm, "end": v(-375.97, 255.55) * mm});
            skLineSegment(sketch, "E5224", {"start": v(-375.97, 255.55) * mm, "end": v(-388.7, 255.66) * mm});
            skLineSegment(sketch, "E5225", {"start": v(-388.7, 255.66) * mm, "end": v(-401.83, 255.72) * mm});
            skLineSegment(sketch, "E5226", {"start": v(-401.83, 255.72) * mm, "end": v(-414.9, 255.85) * mm});
            skLineSegment(sketch, "E5227", {"start": v(-414.9, 255.85) * mm, "end": v(-427.47, 256.18) * mm});
            skLineSegment(sketch, "E5228", {"start": v(-427.47, 256.18) * mm, "end": v(-439.04, 256.85) * mm});
            skLineSegment(sketch, "E5229", {"start": v(-439.04, 256.85) * mm, "end": v(-446.65, 257.6) * mm});
            skLineSegment(sketch, "E5230", {"start": v(-446.65, 257.6) * mm, "end": v(-449.17, 257.97) * mm});
            skLineSegment(sketch, "E5231", {"start": v(-449.17, 257.97) * mm, "end": v(-450.6, 258.19) * mm});
            skLineSegment(sketch, "E5232", {"start": v(-450.6, 258.19) * mm, "end": v(-454.86, 258.85) * mm});
            skLineSegment(sketch, "E5233", {"start": v(-454.86, 258.85) * mm, "end": v(-460.99, 259.84) * mm});
            skLineSegment(sketch, "E5234", {"start": v(-460.99, 259.84) * mm, "end": v(-467.45, 260.9) * mm});
            skLineSegment(sketch, "E5235", {"start": v(-467.45, 260.9) * mm, "end": v(-474.14, 262.03) * mm});
            skLineSegment(sketch, "E5236", {"start": v(-474.14, 262.03) * mm, "end": v(-480.93, 263.2) * mm});
            skLineSegment(sketch, "E5237", {"start": v(-480.93, 263.2) * mm, "end": v(-487.73, 264.38) * mm});
            skLineSegment(sketch, "E5238", {"start": v(-487.73, 264.38) * mm, "end": v(-494.4, 265.55) * mm});
            skLineSegment(sketch, "E5239", {"start": v(-494.4, 265.55) * mm, "end": v(-500.86, 266.7) * mm});
            skLineSegment(sketch, "E5240", {"start": v(-500.86, 266.7) * mm, "end": v(-506.97, 267.79) * mm});
            skLineSegment(sketch, "E5241", {"start": v(-506.97, 267.79) * mm, "end": v(-512.63, 268.8) * mm});
            skLineSegment(sketch, "E5242", {"start": v(-512.63, 268.8) * mm, "end": v(-517.73, 269.73) * mm});
            skLineSegment(sketch, "E5243", {"start": v(-517.73, 269.73) * mm, "end": v(-522.16, 270.54) * mm});
            skLineSegment(sketch, "E5244", {"start": v(-522.16, 270.54) * mm, "end": v(-525.8, 271.2) * mm});
            skLineSegment(sketch, "E5245", {"start": v(-525.8, 271.2) * mm, "end": v(-528.53, 271.7) * mm});
            skLineSegment(sketch, "E5246", {"start": v(-528.53, 271.7) * mm, "end": v(-530.25, 272.02) * mm});
            skLineSegment(sketch, "E5247", {"start": v(-530.25, 272.02) * mm, "end": v(-530.85, 272.14) * mm});
            skLineSegment(sketch, "E5248", {"start": v(610.28, -125.44) * mm, "end": v(605.97, -124.55) * mm});
            skLineSegment(sketch, "E5249", {"start": v(605.97, -124.55) * mm, "end": v(593.06, -121.78) * mm});
            skLineSegment(sketch, "E5250", {"start": v(593.06, -121.78) * mm, "end": v(575.53, -117.77) * mm});
            skLineSegment(sketch, "E5251", {"start": v(575.53, -117.77) * mm, "end": v(557.74, -113.4) * mm});
            skLineSegment(sketch, "E5252", {"start": v(557.74, -113.4) * mm, "end": v(539.72, -108.64) * mm});
            skLineSegment(sketch, "E5253", {"start": v(539.72, -108.64) * mm, "end": v(521.52, -103.47) * mm});
            skLineSegment(sketch, "E5254", {"start": v(521.52, -103.47) * mm, "end": v(503.17, -97.85) * mm});
            skLineSegment(sketch, "E5255", {"start": v(503.17, -97.85) * mm, "end": v(484.72, -91.75) * mm});
            skLineSegment(sketch, "E5256", {"start": v(484.72, -91.75) * mm, "end": v(466.22, -85.16) * mm});
            skLineSegment(sketch, "E5257", {"start": v(466.22, -85.16) * mm, "end": v(447.7, -78.04) * mm});
            skLineSegment(sketch, "E5258", {"start": v(447.7, -78.04) * mm, "end": v(429.19, -70.38) * mm});
            skLineSegment(sketch, "E5259", {"start": v(429.19, -70.38) * mm, "end": v(410.75, -62.13) * mm});
            skLineSegment(sketch, "E5260", {"start": v(410.75, -62.13) * mm, "end": v(392.42, -53.29) * mm});
            skLineSegment(sketch, "E5261", {"start": v(392.42, -53.29) * mm, "end": v(374.23, -43.8) * mm});
            skLineSegment(sketch, "E5262", {"start": v(374.23, -43.8) * mm, "end": v(356.23, -33.67) * mm});
            skLineSegment(sketch, "E5263", {"start": v(356.23, -33.67) * mm, "end": v(338.46, -22.85) * mm});
            skLineSegment(sketch, "E5264", {"start": v(338.46, -22.85) * mm, "end": v(325.29, -14.28) * mm});
            skLineSegment(sketch, "E5265", {"start": v(325.29, -14.28) * mm, "end": v(320.97, -11.32) * mm});
            skLineSegment(sketch, "E5266", {"start": v(320.97, -11.32) * mm, "end": v(317, -8.6) * mm});
            skLineSegment(sketch, "E5267", {"start": v(317, -8.6) * mm, "end": v(305.12, -0.39) * mm});
            skLineSegment(sketch, "E5268", {"start": v(305.12, -0.39) * mm, "end": v(289.7, 10.38) * mm});
            skLineSegment(sketch, "E5269", {"start": v(289.7, 10.38) * mm, "end": v(274.7, 20.98) * mm});
            skLineSegment(sketch, "E5270", {"start": v(274.7, 20.98) * mm, "end": v(260.13, 31.38) * mm});
            skLineSegment(sketch, "E5271", {"start": v(260.13, 31.38) * mm, "end": v(245.99, 41.59) * mm});
            skLineSegment(sketch, "E5272", {"start": v(245.99, 41.59) * mm, "end": v(232.27, 51.59) * mm});
            skLineSegment(sketch, "E5273", {"start": v(232.27, 51.59) * mm, "end": v(219, 61.37) * mm});
            skLineSegment(sketch, "E5274", {"start": v(219, 61.37) * mm, "end": v(206.15, 70.91) * mm});
            skLineSegment(sketch, "E5275", {"start": v(206.15, 70.91) * mm, "end": v(193.74, 80.22) * mm});
            skLineSegment(sketch, "E5276", {"start": v(193.74, 80.22) * mm, "end": v(181.76, 89.27) * mm});
            skLineSegment(sketch, "E5277", {"start": v(181.76, 89.27) * mm, "end": v(170.22, 98.06) * mm});
            skLineSegment(sketch, "E5278", {"start": v(170.22, 98.06) * mm, "end": v(159.12, 106.57) * mm});
            skLineSegment(sketch, "E5279", {"start": v(159.12, 106.57) * mm, "end": v(148.45, 114.79) * mm});
            skLineSegment(sketch, "E5280", {"start": v(148.45, 114.79) * mm, "end": v(138.23, 122.72) * mm});
            skLineSegment(sketch, "E5281", {"start": v(138.23, 122.72) * mm, "end": v(128.45, 130.33) * mm});
            skLineSegment(sketch, "E5282", {"start": v(128.45, 130.33) * mm, "end": v(119.1, 137.63) * mm});
            skLineSegment(sketch, "E5283", {"start": v(119.1, 137.63) * mm, "end": v(110.2, 144.6) * mm});
            skLineSegment(sketch, "E5284", {"start": v(110.2, 144.6) * mm, "end": v(101.76, 151.22) * mm});
            skLineSegment(sketch, "E5285", {"start": v(101.76, 151.22) * mm, "end": v(93.76, 157.5) * mm});
            skLineSegment(sketch, "E5286", {"start": v(93.76, 157.5) * mm, "end": v(86.2, 163.4) * mm});
            skLineSegment(sketch, "E5287", {"start": v(86.2, 163.4) * mm, "end": v(79.1, 168.94) * mm});
            skLineSegment(sketch, "E5288", {"start": v(79.1, 168.94) * mm, "end": v(72.43, 174.08) * mm});
            skLineSegment(sketch, "E5289", {"start": v(72.43, 174.08) * mm, "end": v(66.23, 178.83) * mm});
            skLineSegment(sketch, "E5290", {"start": v(66.23, 178.83) * mm, "end": v(60.47, 183.17) * mm});
            skLineSegment(sketch, "E5291", {"start": v(60.47, 183.17) * mm, "end": v(55.17, 187.09) * mm});
            skLineSegment(sketch, "E5292", {"start": v(55.17, 187.09) * mm, "end": v(50.33, 190.58) * mm});
            skLineSegment(sketch, "E5293", {"start": v(50.33, 190.58) * mm, "end": v(45.94, 193.62) * mm});
            skLineSegment(sketch, "E5294", {"start": v(45.94, 193.62) * mm, "end": v(42, 196.22) * mm});
            skLineSegment(sketch, "E5295", {"start": v(42, 196.22) * mm, "end": v(38.54, 198.35) * mm});
            skLineSegment(sketch, "E5296", {"start": v(38.54, 198.35) * mm, "end": v(35.52, 200) * mm});
            skLineSegment(sketch, "E5297", {"start": v(35.52, 200) * mm, "end": v(32.97, 201.18) * mm});
            skLineSegment(sketch, "E5298", {"start": v(32.97, 201.18) * mm, "end": v(31.41, 201.73) * mm});
            skLineSegment(sketch, "E5299", {"start": v(31.41, 201.73) * mm, "end": v(30.89, 201.85) * mm});
            skLineSegment(sketch, "E5300", {"start": v(30.89, 201.85) * mm, "end": v(29.38, 202.2) * mm});
            skLineSegment(sketch, "E5301", {"start": v(29.38, 202.2) * mm, "end": v(24.76, 202.71) * mm});
            skLineSegment(sketch, "E5302", {"start": v(24.76, 202.71) * mm, "end": v(18.53, 202.67) * mm});
            skLineSegment(sketch, "E5303", {"start": v(18.53, 202.67) * mm, "end": v(11.98, 201.95) * mm});
            skLineSegment(sketch, "E5304", {"start": v(11.98, 201.95) * mm, "end": v(4.92, 200.8) * mm});
            skLineSegment(sketch, "E5305", {"start": v(4.92, 200.8) * mm, "end": v(-2.87, 199.45) * mm});
            skLineSegment(sketch, "E5306", {"start": v(-2.87, 199.45) * mm, "end": v(-11.57, 198.13) * mm});
            skLineSegment(sketch, "E5307", {"start": v(-11.57, 198.13) * mm, "end": v(-21.4, 197.08) * mm});
            skLineSegment(sketch, "E5308", {"start": v(-21.4, 197.08) * mm, "end": v(-29.75, 196.6) * mm});
            skLineSegment(sketch, "E5309", {"start": v(-29.75, 196.6) * mm, "end": v(-32.54, 196.54) * mm});
            skLineSegment(sketch, "E5310", {"start": v(-32.54, 196.54) * mm, "end": v(-34.5, 196.5) * mm});
            skLineSegment(sketch, "E5311", {"start": v(-34.5, 196.5) * mm, "end": v(-40.35, 196.34) * mm});
            skLineSegment(sketch, "E5312", {"start": v(-40.35, 196.34) * mm, "end": v(-48.89, 195.98) * mm});
            skLineSegment(sketch, "E5313", {"start": v(-48.89, 195.98) * mm, "end": v(-58.04, 195.5) * mm});
            skLineSegment(sketch, "E5314", {"start": v(-58.04, 195.5) * mm, "end": v(-67.7, 194.9) * mm});
            skLineSegment(sketch, "E5315", {"start": v(-67.7, 194.9) * mm, "end": v(-77.75, 194.2) * mm});
            skLineSegment(sketch, "E5316", {"start": v(-77.75, 194.2) * mm, "end": v(-88.08, 193.42) * mm});
            skLineSegment(sketch, "E5317", {"start": v(-88.08, 193.42) * mm, "end": v(-98.57, 192.57) * mm});
            skLineSegment(sketch, "E5318", {"start": v(-98.57, 192.57) * mm, "end": v(-106.47, 191.9) * mm});
            skLineSegment(sketch, "E5319", {"start": v(-106.47, 191.9) * mm, "end": v(-109.1, 191.68) * mm});
            skLineSegment(sketch, "E5320", {"start": v(-109.1, 191.68) * mm, "end": v(-112.19, 191.4) * mm});
            skLineSegment(sketch, "E5321", {"start": v(-112.19, 191.4) * mm, "end": v(-121.38, 190.02) * mm});
            skLineSegment(sketch, "E5322", {"start": v(-121.38, 190.02) * mm, "end": v(-133.63, 187.44) * mm});
            skLineSegment(sketch, "E5323", {"start": v(-133.63, 187.44) * mm, "end": v(-145.73, 184.3) * mm});
            skLineSegment(sketch, "E5324", {"start": v(-145.73, 184.3) * mm, "end": v(-157.51, 180.96) * mm});
            skLineSegment(sketch, "E5325", {"start": v(-157.51, 180.96) * mm, "end": v(-168.83, 177.8) * mm});
            skLineSegment(sketch, "E5326", {"start": v(-168.83, 177.8) * mm, "end": v(-179.54, 175.2) * mm});
            skLineSegment(sketch, "E5327", {"start": v(-179.54, 175.2) * mm, "end": v(-189.5, 173.53) * mm});
            skLineSegment(sketch, "E5328", {"start": v(-189.5, 173.53) * mm, "end": v(-196.28, 173.05) * mm});
            skLineSegment(sketch, "E5329", {"start": v(-196.28, 173.05) * mm, "end": v(-198.53, 173.16) * mm});
            skLineSegment(sketch, "E5330", {"start": v(-198.53, 173.16) * mm, "end": v(-201.79, 173.3) * mm});
            skLineSegment(sketch, "E5331", {"start": v(-201.79, 173.3) * mm, "end": v(-211.54, 174.04) * mm});
            skLineSegment(sketch, "E5332", {"start": v(-211.54, 174.04) * mm, "end": v(-223.48, 175.4) * mm});
            skLineSegment(sketch, "E5333", {"start": v(-223.48, 175.4) * mm, "end": v(-234.7, 177.2) * mm});
            skLineSegment(sketch, "E5334", {"start": v(-234.7, 177.2) * mm, "end": v(-245.55, 179.43) * mm});
            skLineSegment(sketch, "E5335", {"start": v(-245.55, 179.43) * mm, "end": v(-256.37, 182.06) * mm});
            skLineSegment(sketch, "E5336", {"start": v(-256.37, 182.06) * mm, "end": v(-267.53, 185.06) * mm});
            skLineSegment(sketch, "E5337", {"start": v(-267.53, 185.06) * mm, "end": v(-279.35, 188.4) * mm});
            skLineSegment(sketch, "E5338", {"start": v(-279.35, 188.4) * mm, "end": v(-288.98, 191.15) * mm});
            skLineSegment(sketch, "E5339", {"start": v(-288.98, 191.15) * mm, "end": v(-292.2, 192.06) * mm});
            skLineSegment(sketch, "E5340", {"start": v(-292.2, 192.06) * mm, "end": v(-293.55, 192.45) * mm});
            skLineSegment(sketch, "E5341", {"start": v(-293.55, 192.45) * mm, "end": v(-297.6, 193.71) * mm});
            skLineSegment(sketch, "E5342", {"start": v(-297.6, 193.71) * mm, "end": v(-303.84, 195.74) * mm});
            skLineSegment(sketch, "E5343", {"start": v(-303.84, 195.74) * mm, "end": v(-310.75, 198) * mm});
            skLineSegment(sketch, "E5344", {"start": v(-310.75, 198) * mm, "end": v(-318.16, 200.3) * mm});
            skLineSegment(sketch, "E5345", {"start": v(-318.16, 200.3) * mm, "end": v(-325.94, 202.53) * mm});
            skLineSegment(sketch, "E5346", {"start": v(-325.94, 202.53) * mm, "end": v(-333.91, 204.5) * mm});
            skLineSegment(sketch, "E5347", {"start": v(-333.91, 204.5) * mm, "end": v(-341.94, 206.05) * mm});
            skLineSegment(sketch, "E5348", {"start": v(-341.94, 206.05) * mm, "end": v(-347.87, 206.88) * mm});
            skLineSegment(sketch, "E5349", {"start": v(-347.87, 206.88) * mm, "end": v(-349.85, 207.04) * mm});
            skLineSegment(sketch, "E5350", {"start": v(-349.85, 207.04) * mm, "end": v(-351, 207.14) * mm});
            skLineSegment(sketch, "E5351", {"start": v(-351, 207.14) * mm, "end": v(-354.48, 207.35) * mm});
            skLineSegment(sketch, "E5352", {"start": v(-354.48, 207.35) * mm, "end": v(-358.68, 207.48) * mm});
            skLineSegment(sketch, "E5353", {"start": v(-358.68, 207.48) * mm, "end": v(-362.52, 207.47) * mm});
            skLineSegment(sketch, "E5354", {"start": v(-362.52, 207.47) * mm, "end": v(-366.06, 207.34) * mm});
            skLineSegment(sketch, "E5355", {"start": v(-366.06, 207.34) * mm, "end": v(-369.35, 207.12) * mm});
            skLineSegment(sketch, "E5356", {"start": v(-369.35, 207.12) * mm, "end": v(-372.46, 206.83) * mm});
            skLineSegment(sketch, "E5357", {"start": v(-372.46, 206.83) * mm, "end": v(-375.43, 206.5) * mm});
            skLineSegment(sketch, "E5358", {"start": v(-375.43, 206.5) * mm, "end": v(-378.33, 206.18) * mm});
            skLineSegment(sketch, "E5359", {"start": v(-378.33, 206.18) * mm, "end": v(-381.22, 205.86) * mm});
            skLineSegment(sketch, "E5360", {"start": v(-381.22, 205.86) * mm, "end": v(-384.15, 205.6) * mm});
            skLineSegment(sketch, "E5361", {"start": v(-384.15, 205.6) * mm, "end": v(-387.19, 205.4) * mm});
            skLineSegment(sketch, "E5362", {"start": v(-387.19, 205.4) * mm, "end": v(-390.38, 205.31) * mm});
            skLineSegment(sketch, "E5363", {"start": v(-390.38, 205.31) * mm, "end": v(-393.8, 205.35) * mm});
            skLineSegment(sketch, "E5364", {"start": v(-393.8, 205.35) * mm, "end": v(-397.48, 205.54) * mm});
            skLineSegment(sketch, "E5365", {"start": v(-397.48, 205.54) * mm, "end": v(-401.5, 205.9) * mm});
            skLineSegment(sketch, "E5366", {"start": v(-401.5, 205.9) * mm, "end": v(-404.81, 206.33) * mm});
            skLineSegment(sketch, "E5367", {"start": v(-404.81, 206.33) * mm, "end": v(-405.91, 206.5) * mm});
            skLineSegment(sketch, "E5368", {"start": v(-405.91, 206.5) * mm, "end": v(-407.42, 206.72) * mm});
            skLineSegment(sketch, "E5369", {"start": v(-407.42, 206.72) * mm, "end": v(-411.95, 207.34) * mm});
            skLineSegment(sketch, "E5370", {"start": v(-411.95, 207.34) * mm, "end": v(-419.1, 208.23) * mm});
            skLineSegment(sketch, "E5371", {"start": v(-419.1, 208.23) * mm, "end": v(-427.13, 209.15) * mm});
            skLineSegment(sketch, "E5372", {"start": v(-427.13, 209.15) * mm, "end": v(-435.84, 210.09) * mm});
            skLineSegment(sketch, "E5373", {"start": v(-435.84, 210.09) * mm, "end": v(-445.05, 211.03) * mm});
            skLineSegment(sketch, "E5374", {"start": v(-445.05, 211.03) * mm, "end": v(-454.53, 211.96) * mm});
            skLineSegment(sketch, "E5375", {"start": v(-454.53, 211.96) * mm, "end": v(-464.08, 212.86) * mm});
            skLineSegment(sketch, "E5376", {"start": v(-464.08, 212.86) * mm, "end": v(-473.5, 213.73) * mm});
            skLineSegment(sketch, "E5377", {"start": v(-473.5, 213.73) * mm, "end": v(-482.57, 214.55) * mm});
            skLineSegment(sketch, "E5378", {"start": v(-482.57, 214.55) * mm, "end": v(-491.1, 215.3) * mm});
            skLineSegment(sketch, "E5379", {"start": v(-491.1, 215.3) * mm, "end": v(-498.9, 215.98) * mm});
            skLineSegment(sketch, "E5380", {"start": v(-498.9, 215.98) * mm, "end": v(-505.72, 216.56) * mm});
            skLineSegment(sketch, "E5381", {"start": v(-505.72, 216.56) * mm, "end": v(-511.39, 217.03) * mm});
            skLineSegment(sketch, "E5382", {"start": v(-511.39, 217.03) * mm, "end": v(-515.7, 217.4) * mm});
            skLineSegment(sketch, "E5383", {"start": v(-515.7, 217.4) * mm, "end": v(-518.42, 217.61) * mm});
            skLineSegment(sketch, "E5384", {"start": v(-518.42, 217.61) * mm, "end": v(-519.38, 217.7) * mm});
            skLineSegment(sketch, "E5385", {"start": v(609.9, -152.68) * mm, "end": v(605.75, -151.7) * mm});
            skLineSegment(sketch, "E5386", {"start": v(605.75, -151.7) * mm, "end": v(593.34, -148.52) * mm});
            skLineSegment(sketch, "E5387", {"start": v(593.34, -148.52) * mm, "end": v(576.11, -143.75) * mm});
            skLineSegment(sketch, "E5388", {"start": v(576.11, -143.75) * mm, "end": v(558.3, -138.4) * mm});
            skLineSegment(sketch, "E5389", {"start": v(558.3, -138.4) * mm, "end": v(539.99, -132.51) * mm});
            skLineSegment(sketch, "E5390", {"start": v(539.99, -132.51) * mm, "end": v(521.28, -126.1) * mm});
            skLineSegment(sketch, "E5391", {"start": v(521.28, -126.1) * mm, "end": v(502.28, -119.19) * mm});
            skLineSegment(sketch, "E5392", {"start": v(502.28, -119.19) * mm, "end": v(483.07, -111.82) * mm});
            skLineSegment(sketch, "E5393", {"start": v(483.07, -111.82) * mm, "end": v(463.74, -104.02) * mm});
            skLineSegment(sketch, "E5394", {"start": v(463.74, -104.02) * mm, "end": v(444.39, -95.8) * mm});
            skLineSegment(sketch, "E5395", {"start": v(444.39, -95.8) * mm, "end": v(425.11, -87.22) * mm});
            skLineSegment(sketch, "E5396", {"start": v(425.11, -87.22) * mm, "end": v(406, -78.3) * mm});
            skLineSegment(sketch, "E5397", {"start": v(406, -78.3) * mm, "end": v(387.16, -69.04) * mm});
            skLineSegment(sketch, "E5398", {"start": v(387.16, -69.04) * mm, "end": v(368.66, -59.5) * mm});
            skLineSegment(sketch, "E5399", {"start": v(368.66, -59.5) * mm, "end": v(350.62, -49.7) * mm});
            skLineSegment(sketch, "E5400", {"start": v(350.62, -49.7) * mm, "end": v(333.11, -39.65) * mm});
            skLineSegment(sketch, "E5401", {"start": v(333.11, -39.65) * mm, "end": v(320.43, -32.03) * mm});
            skLineSegment(sketch, "E5402", {"start": v(320.43, -32.03) * mm, "end": v(316.25, -29.41) * mm});
            skLineSegment(sketch, "E5403", {"start": v(316.25, -29.41) * mm, "end": v(312.15, -26.85) * mm});
            skLineSegment(sketch, "E5404", {"start": v(312.15, -26.85) * mm, "end": v(299.92, -19.1) * mm});
            skLineSegment(sketch, "E5405", {"start": v(299.92, -19.1) * mm, "end": v(284.04, -8.84) * mm});
            skLineSegment(sketch, "E5406", {"start": v(284.04, -8.84) * mm, "end": v(268.61, 1.32) * mm});
            skLineSegment(sketch, "E5407", {"start": v(268.61, 1.32) * mm, "end": v(253.63, 11.37) * mm});
            skLineSegment(sketch, "E5408", {"start": v(253.63, 11.37) * mm, "end": v(239.1, 21.3) * mm});
            skLineSegment(sketch, "E5409", {"start": v(239.1, 21.3) * mm, "end": v(225.01, 31.1) * mm});
            skLineSegment(sketch, "E5410", {"start": v(225.01, 31.1) * mm, "end": v(211.37, 40.73) * mm});
            skLineSegment(sketch, "E5411", {"start": v(211.37, 40.73) * mm, "end": v(198.19, 50.18) * mm});
            skLineSegment(sketch, "E5412", {"start": v(198.19, 50.18) * mm, "end": v(185.45, 59.45) * mm});
            skLineSegment(sketch, "E5413", {"start": v(185.45, 59.45) * mm, "end": v(173.17, 68.5) * mm});
            skLineSegment(sketch, "E5414", {"start": v(173.17, 68.5) * mm, "end": v(161.34, 77.33) * mm});
            skLineSegment(sketch, "E5415", {"start": v(161.34, 77.33) * mm, "end": v(149.97, 85.92) * mm});
            skLineSegment(sketch, "E5416", {"start": v(149.97, 85.92) * mm, "end": v(139.05, 94.24) * mm});
            skLineSegment(sketch, "E5417", {"start": v(139.05, 94.24) * mm, "end": v(128.58, 102.29) * mm});
            skLineSegment(sketch, "E5418", {"start": v(128.58, 102.29) * mm, "end": v(118.58, 110.04) * mm});
            skLineSegment(sketch, "E5419", {"start": v(118.58, 110.04) * mm, "end": v(109.02, 117.48) * mm});
            skLineSegment(sketch, "E5420", {"start": v(109.02, 117.48) * mm, "end": v(99.93, 124.6) * mm});
            skLineSegment(sketch, "E5421", {"start": v(99.93, 124.6) * mm, "end": v(91.3, 131.35) * mm});
            skLineSegment(sketch, "E5422", {"start": v(91.3, 131.35) * mm, "end": v(83.12, 137.75) * mm});
            skLineSegment(sketch, "E5423", {"start": v(83.12, 137.75) * mm, "end": v(75.4, 143.77) * mm});
            skLineSegment(sketch, "E5424", {"start": v(75.4, 143.77) * mm, "end": v(68.14, 149.4) * mm});
            skLineSegment(sketch, "E5425", {"start": v(68.14, 149.4) * mm, "end": v(61.36, 154.6) * mm});
            skLineSegment(sketch, "E5426", {"start": v(61.36, 154.6) * mm, "end": v(55.02, 159.37) * mm});
            skLineSegment(sketch, "E5427", {"start": v(55.02, 159.37) * mm, "end": v(49.16, 163.7) * mm});
            skLineSegment(sketch, "E5428", {"start": v(49.16, 163.7) * mm, "end": v(43.76, 167.55) * mm});
            skLineSegment(sketch, "E5429", {"start": v(43.76, 167.55) * mm, "end": v(38.82, 170.92) * mm});
            skLineSegment(sketch, "E5430", {"start": v(38.82, 170.92) * mm, "end": v(34.34, 173.8) * mm});
            skLineSegment(sketch, "E5431", {"start": v(34.34, 173.8) * mm, "end": v(30.34, 176.15) * mm});
            skLineSegment(sketch, "E5432", {"start": v(30.34, 176.15) * mm, "end": v(26.8, 177.97) * mm});
            skLineSegment(sketch, "E5433", {"start": v(26.8, 177.97) * mm, "end": v(23.74, 179.23) * mm});
            skLineSegment(sketch, "E5434", {"start": v(23.74, 179.23) * mm, "end": v(21.13, 179.93) * mm});
            skLineSegment(sketch, "E5435", {"start": v(21.13, 179.93) * mm, "end": v(19.53, 180.09) * mm});
            skLineSegment(sketch, "E5436", {"start": v(19.53, 180.09) * mm, "end": v(19, 180.03) * mm});
            skLineSegment(sketch, "E5437", {"start": v(19, 180.03) * mm, "end": v(17.12, 179.85) * mm});
            skLineSegment(sketch, "E5438", {"start": v(17.12, 179.85) * mm, "end": v(11.43, 179.54) * mm});
            skLineSegment(sketch, "E5439", {"start": v(11.43, 179.54) * mm, "end": v(3.92, 179.53) * mm});
            skLineSegment(sketch, "E5440", {"start": v(3.92, 179.53) * mm, "end": v(-3.71, 179.84) * mm});
            skLineSegment(sketch, "E5441", {"start": v(-3.71, 179.84) * mm, "end": v(-11.67, 180.37) * mm});
            skLineSegment(sketch, "E5442", {"start": v(-11.67, 180.37) * mm, "end": v(-20.16, 180.96) * mm});
            skLineSegment(sketch, "E5443", {"start": v(-20.16, 180.96) * mm, "end": v(-29.37, 181.49) * mm});
            skLineSegment(sketch, "E5444", {"start": v(-29.37, 181.49) * mm, "end": v(-39.5, 181.82) * mm});
            skLineSegment(sketch, "E5445", {"start": v(-39.5, 181.82) * mm, "end": v(-47.93, 181.87) * mm});
            skLineSegment(sketch, "E5446", {"start": v(-47.93, 181.87) * mm, "end": v(-50.75, 181.82) * mm});
            skLineSegment(sketch, "E5447", {"start": v(-50.75, 181.82) * mm, "end": v(-52.8, 181.79) * mm});
            skLineSegment(sketch, "E5448", {"start": v(-52.8, 181.79) * mm, "end": v(-58.94, 181.48) * mm});
            skLineSegment(sketch, "E5449", {"start": v(-58.94, 181.48) * mm, "end": v(-68.5, 180.77) * mm});
            skLineSegment(sketch, "E5450", {"start": v(-68.5, 180.77) * mm, "end": v(-79.08, 179.75) * mm});
            skLineSegment(sketch, "E5451", {"start": v(-79.08, 179.75) * mm, "end": v(-90.37, 178.48) * mm});
            skLineSegment(sketch, "E5452", {"start": v(-90.37, 178.48) * mm, "end": v(-102.05, 177.02) * mm});
            skLineSegment(sketch, "E5453", {"start": v(-102.05, 177.02) * mm, "end": v(-113.78, 175.44) * mm});
            skLineSegment(sketch, "E5454", {"start": v(-113.78, 175.44) * mm, "end": v(-125.23, 173.8) * mm});
            skLineSegment(sketch, "E5455", {"start": v(-125.23, 173.8) * mm, "end": v(-133.37, 172.58) * mm});
            skLineSegment(sketch, "E5456", {"start": v(-133.37, 172.58) * mm, "end": v(-136.08, 172.17) * mm});
            skLineSegment(sketch, "E5457", {"start": v(-136.08, 172.17) * mm, "end": v(-137.52, 171.95) * mm});
            skLineSegment(sketch, "E5458", {"start": v(-137.52, 171.95) * mm, "end": v(-141.83, 171.16) * mm});
            skLineSegment(sketch, "E5459", {"start": v(-141.83, 171.16) * mm, "end": v(-147.17, 170) * mm});
            skLineSegment(sketch, "E5460", {"start": v(-147.17, 170) * mm, "end": v(-152.16, 168.72) * mm});
            skLineSegment(sketch, "E5461", {"start": v(-152.16, 168.72) * mm, "end": v(-156.84, 167.36) * mm});
            skLineSegment(sketch, "E5462", {"start": v(-156.84, 167.36) * mm, "end": v(-161.24, 165.94) * mm});
            skLineSegment(sketch, "E5463", {"start": v(-161.24, 165.94) * mm, "end": v(-165.4, 164.52) * mm});
            skLineSegment(sketch, "E5464", {"start": v(-165.4, 164.52) * mm, "end": v(-169.38, 163.1) * mm});
            skLineSegment(sketch, "E5465", {"start": v(-169.38, 163.1) * mm, "end": v(-173.2, 161.73) * mm});
            skLineSegment(sketch, "E5466", {"start": v(-173.2, 161.73) * mm, "end": v(-176.93, 160.45) * mm});
            skLineSegment(sketch, "E5467", {"start": v(-176.93, 160.45) * mm, "end": v(-180.58, 159.3) * mm});
            skLineSegment(sketch, "E5468", {"start": v(-180.58, 159.3) * mm, "end": v(-184.22, 158.27) * mm});
            skLineSegment(sketch, "E5469", {"start": v(-184.22, 158.27) * mm, "end": v(-187.87, 157.45) * mm});
            skLineSegment(sketch, "E5470", {"start": v(-187.87, 157.45) * mm, "end": v(-191.58, 156.83) * mm});
            skLineSegment(sketch, "E5471", {"start": v(-191.58, 156.83) * mm, "end": v(-195.4, 156.47) * mm});
            skLineSegment(sketch, "E5472", {"start": v(-195.4, 156.47) * mm, "end": v(-199.35, 156.4) * mm});
            skLineSegment(sketch, "E5473", {"start": v(-199.35, 156.4) * mm, "end": v(-202.47, 156.53) * mm});
            skLineSegment(sketch, "E5474", {"start": v(-202.47, 156.53) * mm, "end": v(-203.5, 156.63) * mm});
            skLineSegment(sketch, "E5475", {"start": v(-203.5, 156.63) * mm, "end": v(-206.66, 156.94) * mm});
            skLineSegment(sketch, "E5476", {"start": v(-206.66, 156.94) * mm, "end": v(-216.15, 158.02) * mm});
            skLineSegment(sketch, "E5477", {"start": v(-216.15, 158.02) * mm, "end": v(-227.41, 159.55) * mm});
            skLineSegment(sketch, "E5478", {"start": v(-227.41, 159.55) * mm, "end": v(-237.74, 161.27) * mm});
            skLineSegment(sketch, "E5479", {"start": v(-237.74, 161.27) * mm, "end": v(-247.6, 163.17) * mm});
            skLineSegment(sketch, "E5480", {"start": v(-247.6, 163.17) * mm, "end": v(-257.43, 165.28) * mm});
            skLineSegment(sketch, "E5481", {"start": v(-257.43, 165.28) * mm, "end": v(-267.7, 167.61) * mm});
            skLineSegment(sketch, "E5482", {"start": v(-267.7, 167.61) * mm, "end": v(-278.84, 170.18) * mm});
            skLineSegment(sketch, "E5483", {"start": v(-278.84, 170.18) * mm, "end": v(-288.21, 172.3) * mm});
            skLineSegment(sketch, "E5484", {"start": v(-288.21, 172.3) * mm, "end": v(-291.34, 173) * mm});
            skLineSegment(sketch, "E5485", {"start": v(-291.34, 173) * mm, "end": v(-292.72, 173.3) * mm});
            skLineSegment(sketch, "E5486", {"start": v(-292.72, 173.3) * mm, "end": v(-296.82, 174.5) * mm});
            skLineSegment(sketch, "E5487", {"start": v(-296.82, 174.5) * mm, "end": v(-303.1, 176.6) * mm});
            skLineSegment(sketch, "E5488", {"start": v(-303.1, 176.6) * mm, "end": v(-310.05, 179.1) * mm});
            skLineSegment(sketch, "E5489", {"start": v(-310.05, 179.1) * mm, "end": v(-317.5, 181.76) * mm});
            skLineSegment(sketch, "E5490", {"start": v(-317.5, 181.76) * mm, "end": v(-325.29, 184.37) * mm});
            skLineSegment(sketch, "E5491", {"start": v(-325.29, 184.37) * mm, "end": v(-333.27, 186.69) * mm});
            skLineSegment(sketch, "E5492", {"start": v(-333.27, 186.69) * mm, "end": v(-341.3, 188.5) * mm});
            skLineSegment(sketch, "E5493", {"start": v(-341.3, 188.5) * mm, "end": v(-347.23, 189.43) * mm});
            skLineSegment(sketch, "E5494", {"start": v(-347.23, 189.43) * mm, "end": v(-349.22, 189.6) * mm});
            skLineSegment(sketch, "E5495", {"start": v(-349.22, 189.6) * mm, "end": v(-351.58, 189.79) * mm});
            skLineSegment(sketch, "E5496", {"start": v(-351.58, 189.79) * mm, "end": v(-358.7, 190.1) * mm});
            skLineSegment(sketch, "E5497", {"start": v(-358.7, 190.1) * mm, "end": v(-367.85, 190.14) * mm});
            skLineSegment(sketch, "E5498", {"start": v(-367.85, 190.14) * mm, "end": v(-376.74, 189.89) * mm});
            skLineSegment(sketch, "E5499", {"start": v(-376.74, 189.89) * mm, "end": v(-385.46, 189.53) * mm});
            skLineSegment(sketch, "E5500", {"start": v(-385.46, 189.53) * mm, "end": v(-394.14, 189.24) * mm});
            skLineSegment(sketch, "E5501", {"start": v(-394.14, 189.24) * mm, "end": v(-402.85, 189.2) * mm});
            skLineSegment(sketch, "E5502", {"start": v(-402.85, 189.2) * mm, "end": v(-411.7, 189.61) * mm});
            skLineSegment(sketch, "E5503", {"start": v(-411.7, 189.61) * mm, "end": v(-418.54, 190.3) * mm});
            skLineSegment(sketch, "E5504", {"start": v(-418.54, 190.3) * mm, "end": v(-420.8, 190.64) * mm});
            skLineSegment(sketch, "E5505", {"start": v(-420.8, 190.64) * mm, "end": v(-422.27, 190.86) * mm});
            skLineSegment(sketch, "E5506", {"start": v(-422.27, 190.86) * mm, "end": v(-426.65, 191.49) * mm});
            skLineSegment(sketch, "E5507", {"start": v(-426.65, 191.49) * mm, "end": v(-433.22, 192.4) * mm});
            skLineSegment(sketch, "E5508", {"start": v(-433.22, 192.4) * mm, "end": v(-440.36, 193.34) * mm});
            skLineSegment(sketch, "E5509", {"start": v(-440.36, 193.34) * mm, "end": v(-447.93, 194.3) * mm});
            skLineSegment(sketch, "E5510", {"start": v(-447.93, 194.3) * mm, "end": v(-455.76, 195.28) * mm});
            skLineSegment(sketch, "E5511", {"start": v(-455.76, 195.28) * mm, "end": v(-463.72, 196.25) * mm});
            skLineSegment(sketch, "E5512", {"start": v(-463.72, 196.25) * mm, "end": v(-471.64, 197.2) * mm});
            skLineSegment(sketch, "E5513", {"start": v(-471.64, 197.2) * mm, "end": v(-479.38, 198.11) * mm});
            skLineSegment(sketch, "E5514", {"start": v(-479.38, 198.11) * mm, "end": v(-486.78, 198.98) * mm});
            skLineSegment(sketch, "E5515", {"start": v(-486.78, 198.98) * mm, "end": v(-493.68, 199.77) * mm});
            skLineSegment(sketch, "E5516", {"start": v(-493.68, 199.77) * mm, "end": v(-499.95, 200.48) * mm});
            skLineSegment(sketch, "E5517", {"start": v(-499.95, 200.48) * mm, "end": v(-505.41, 201.1) * mm});
            skLineSegment(sketch, "E5518", {"start": v(-505.41, 201.1) * mm, "end": v(-509.93, 201.6) * mm});
            skLineSegment(sketch, "E5519", {"start": v(-509.93, 201.6) * mm, "end": v(-513.34, 202) * mm});
            skLineSegment(sketch, "E5520", {"start": v(-513.34, 202) * mm, "end": v(-515.5, 202.23) * mm});
            skLineSegment(sketch, "E5521", {"start": v(-515.5, 202.23) * mm, "end": v(-516.26, 202.31) * mm});
            skLineSegment(sketch, "E5522", {"start": v(610.28, -108.88) * mm, "end": v(605.97, -108) * mm});
            skLineSegment(sketch, "E5523", {"start": v(605.97, -108) * mm, "end": v(593.1, -105.15) * mm});
            skLineSegment(sketch, "E5524", {"start": v(593.1, -105.15) * mm, "end": v(575.65, -100.99) * mm});
            skLineSegment(sketch, "E5525", {"start": v(575.65, -100.99) * mm, "end": v(557.99, -96.37) * mm});
            skLineSegment(sketch, "E5526", {"start": v(557.99, -96.37) * mm, "end": v(540.13, -91.3) * mm});
            skLineSegment(sketch, "E5527", {"start": v(540.13, -91.3) * mm, "end": v(522.12, -85.76) * mm});
            skLineSegment(sketch, "E5528", {"start": v(522.12, -85.76) * mm, "end": v(503.97, -79.74) * mm});
            skLineSegment(sketch, "E5529", {"start": v(503.97, -79.74) * mm, "end": v(485.73, -73.25) * mm});
            skLineSegment(sketch, "E5530", {"start": v(485.73, -73.25) * mm, "end": v(467.41, -66.27) * mm});
            skLineSegment(sketch, "E5531", {"start": v(467.41, -66.27) * mm, "end": v(449.06, -58.79) * mm});
            skLineSegment(sketch, "E5532", {"start": v(449.06, -58.79) * mm, "end": v(430.7, -50.81) * mm});
            skLineSegment(sketch, "E5533", {"start": v(430.7, -50.81) * mm, "end": v(412.37, -42.32) * mm});
            skLineSegment(sketch, "E5534", {"start": v(412.37, -42.32) * mm, "end": v(394.1, -33.3) * mm});
            skLineSegment(sketch, "E5535", {"start": v(394.1, -33.3) * mm, "end": v(375.9, -23.77) * mm});
            skLineSegment(sketch, "E5536", {"start": v(375.9, -23.77) * mm, "end": v(357.82, -13.7) * mm});
            skLineSegment(sketch, "E5537", {"start": v(357.82, -13.7) * mm, "end": v(339.89, -3.1) * mm});
            skLineSegment(sketch, "E5538", {"start": v(339.89, -3.1) * mm, "end": v(326.54, 5.21) * mm});
            skLineSegment(sketch, "E5539", {"start": v(326.54, 5.21) * mm, "end": v(322.14, 8.06) * mm});
            skLineSegment(sketch, "E5540", {"start": v(322.14, 8.06) * mm, "end": v(319.35, 9.88) * mm});
            skLineSegment(sketch, "E5541", {"start": v(319.35, 9.88) * mm, "end": v(311.04, 15.4) * mm});
            skLineSegment(sketch, "E5542", {"start": v(311.04, 15.4) * mm, "end": v(299.98, 23.03) * mm});
            skLineSegment(sketch, "E5543", {"start": v(299.98, 23.03) * mm, "end": v(288.97, 30.89) * mm});
            skLineSegment(sketch, "E5544", {"start": v(288.97, 30.89) * mm, "end": v(278.02, 38.96) * mm});
            skLineSegment(sketch, "E5545", {"start": v(278.02, 38.96) * mm, "end": v(267.14, 47.2) * mm});
            skLineSegment(sketch, "E5546", {"start": v(267.14, 47.2) * mm, "end": v(256.35, 55.6) * mm});
            skLineSegment(sketch, "E5547", {"start": v(256.35, 55.6) * mm, "end": v(245.64, 64.11) * mm});
            skLineSegment(sketch, "E5548", {"start": v(245.64, 64.11) * mm, "end": v(235.04, 72.72) * mm});
            skLineSegment(sketch, "E5549", {"start": v(235.04, 72.72) * mm, "end": v(224.55, 81.38) * mm});
            skLineSegment(sketch, "E5550", {"start": v(224.55, 81.38) * mm, "end": v(214.2, 90.07) * mm});
            skLineSegment(sketch, "E5551", {"start": v(214.2, 90.07) * mm, "end": v(203.98, 98.75) * mm});
            skLineSegment(sketch, "E5552", {"start": v(203.98, 98.75) * mm, "end": v(193.91, 107.4) * mm});
            skLineSegment(sketch, "E5553", {"start": v(193.91, 107.4) * mm, "end": v(184, 115.97) * mm});
            skLineSegment(sketch, "E5554", {"start": v(184, 115.97) * mm, "end": v(174.27, 124.45) * mm});
            skLineSegment(sketch, "E5555", {"start": v(174.27, 124.45) * mm, "end": v(164.71, 132.81) * mm});
            skLineSegment(sketch, "E5556", {"start": v(164.71, 132.81) * mm, "end": v(155.35, 141.01) * mm});
            skLineSegment(sketch, "E5557", {"start": v(155.35, 141.01) * mm, "end": v(146.2, 149.02) * mm});
            skLineSegment(sketch, "E5558", {"start": v(146.2, 149.02) * mm, "end": v(137.26, 156.81) * mm});
            skLineSegment(sketch, "E5559", {"start": v(137.26, 156.81) * mm, "end": v(128.55, 164.35) * mm});
            skLineSegment(sketch, "E5560", {"start": v(128.55, 164.35) * mm, "end": v(120.08, 171.6) * mm});
            skLineSegment(sketch, "E5561", {"start": v(120.08, 171.6) * mm, "end": v(111.86, 178.56) * mm});
            skLineSegment(sketch, "E5562", {"start": v(111.86, 178.56) * mm, "end": v(103.9, 185.16) * mm});
            skLineSegment(sketch, "E5563", {"start": v(103.9, 185.16) * mm, "end": v(96.22, 191.39) * mm});
            skLineSegment(sketch, "E5564", {"start": v(96.22, 191.39) * mm, "end": v(88.82, 197.22) * mm});
            skLineSegment(sketch, "E5565", {"start": v(88.82, 197.22) * mm, "end": v(81.7, 202.61) * mm});
            skLineSegment(sketch, "E5566", {"start": v(81.7, 202.61) * mm, "end": v(74.9, 207.54) * mm});
            skLineSegment(sketch, "E5567", {"start": v(74.9, 207.54) * mm, "end": v(68.42, 211.97) * mm});
            skLineSegment(sketch, "E5568", {"start": v(68.42, 211.97) * mm, "end": v(62.27, 215.88) * mm});
            skLineSegment(sketch, "E5569", {"start": v(62.27, 215.88) * mm, "end": v(56.46, 219.22) * mm});
            skLineSegment(sketch, "E5570", {"start": v(56.46, 219.22) * mm, "end": v(51, 221.99) * mm});
            skLineSegment(sketch, "E5571", {"start": v(51, 221.99) * mm, "end": v(45.9, 224.13) * mm});
            skLineSegment(sketch, "E5572", {"start": v(45.9, 224.13) * mm, "end": v(42.37, 225.31) * mm});
            skLineSegment(sketch, "E5573", {"start": v(42.37, 225.31) * mm, "end": v(41.17, 225.62) * mm});
            skLineSegment(sketch, "E5574", {"start": v(41.17, 225.62) * mm, "end": v(39.13, 226.14) * mm});
            skLineSegment(sketch, "E5575", {"start": v(39.13, 226.14) * mm, "end": v(32.95, 227.42) * mm});
            skLineSegment(sketch, "E5576", {"start": v(32.95, 227.42) * mm, "end": v(25.4, 228.49) * mm});
            skLineSegment(sketch, "E5577", {"start": v(25.4, 228.49) * mm, "end": v(18.42, 228.91) * mm});
            skLineSegment(sketch, "E5578", {"start": v(18.42, 228.91) * mm, "end": v(11.9, 228.76) * mm});
            skLineSegment(sketch, "E5579", {"start": v(11.9, 228.76) * mm, "end": v(5.72, 228.13) * mm});
            skLineSegment(sketch, "E5580", {"start": v(5.72, 228.13) * mm, "end": v(-0.22, 227.1) * mm});
            skLineSegment(sketch, "E5581", {"start": v(-0.22, 227.1) * mm, "end": v(-6.04, 225.73) * mm});
            skLineSegment(sketch, "E5582", {"start": v(-6.04, 225.73) * mm, "end": v(-11.84, 224.13) * mm});
            skLineSegment(sketch, "E5583", {"start": v(-11.84, 224.13) * mm, "end": v(-17.72, 222.36) * mm});
            skLineSegment(sketch, "E5584", {"start": v(-17.72, 222.36) * mm, "end": v(-23.8, 220.5) * mm});
            skLineSegment(sketch, "E5585", {"start": v(-23.8, 220.5) * mm, "end": v(-30.2, 218.66) * mm});
            skLineSegment(sketch, "E5586", {"start": v(-30.2, 218.66) * mm, "end": v(-37.01, 216.89) * mm});
            skLineSegment(sketch, "E5587", {"start": v(-37.01, 216.89) * mm, "end": v(-44.34, 215.28) * mm});
            skLineSegment(sketch, "E5588", {"start": v(-44.34, 215.28) * mm, "end": v(-52.32, 213.92) * mm});
            skLineSegment(sketch, "E5589", {"start": v(-52.32, 213.92) * mm, "end": v(-61.03, 212.88) * mm});
            skLineSegment(sketch, "E5590", {"start": v(-61.03, 212.88) * mm, "end": v(-68.2, 212.34) * mm});
            skLineSegment(sketch, "E5591", {"start": v(-68.2, 212.34) * mm, "end": v(-70.6, 212.25) * mm});
            skLineSegment(sketch, "E5592", {"start": v(-70.6, 212.25) * mm, "end": v(-73.7, 212.12) * mm});
            skLineSegment(sketch, "E5593", {"start": v(-73.7, 212.12) * mm, "end": v(-82.97, 211.58) * mm});
            skLineSegment(sketch, "E5594", {"start": v(-82.97, 211.58) * mm, "end": v(-94.9, 210.63) * mm});
            skLineSegment(sketch, "E5595", {"start": v(-94.9, 210.63) * mm, "end": v(-106.36, 209.44) * mm});
            skLineSegment(sketch, "E5596", {"start": v(-106.36, 209.44) * mm, "end": v(-117.32, 208.06) * mm});
            skLineSegment(sketch, "E5597", {"start": v(-117.32, 208.06) * mm, "end": v(-127.75, 206.52) * mm});
            skLineSegment(sketch, "E5598", {"start": v(-127.75, 206.52) * mm, "end": v(-137.6, 204.89) * mm});
            skLineSegment(sketch, "E5599", {"start": v(-137.6, 204.89) * mm, "end": v(-146.86, 203.2) * mm});
            skLineSegment(sketch, "E5600", {"start": v(-146.86, 203.2) * mm, "end": v(-155.49, 201.48) * mm});
            skLineSegment(sketch, "E5601", {"start": v(-155.49, 201.48) * mm, "end": v(-163.46, 199.8) * mm});
            skLineSegment(sketch, "E5602", {"start": v(-163.46, 199.8) * mm, "end": v(-170.73, 198.2) * mm});
            skLineSegment(sketch, "E5603", {"start": v(-170.73, 198.2) * mm, "end": v(-177.28, 196.73) * mm});
            skLineSegment(sketch, "E5604", {"start": v(-177.28, 196.73) * mm, "end": v(-183.07, 195.42) * mm});
            skLineSegment(sketch, "E5605", {"start": v(-183.07, 195.42) * mm, "end": v(-188.07, 194.32) * mm});
            skLineSegment(sketch, "E5606", {"start": v(-188.07, 194.32) * mm, "end": v(-192.25, 193.48) * mm});
            skLineSegment(sketch, "E5607", {"start": v(-192.25, 193.48) * mm, "end": v(-195.57, 192.95) * mm});
            skLineSegment(sketch, "E5608", {"start": v(-195.57, 192.95) * mm, "end": v(-197.4, 192.76) * mm});
            skLineSegment(sketch, "E5609", {"start": v(-197.4, 192.76) * mm, "end": v(-198, 192.76) * mm});
            skLineSegment(sketch, "E5610", {"start": v(-198, 192.76) * mm, "end": v(-199.61, 192.76) * mm});
            skLineSegment(sketch, "E5611", {"start": v(-199.61, 192.76) * mm, "end": v(-204.43, 192.81) * mm});
            skLineSegment(sketch, "E5612", {"start": v(-204.43, 192.81) * mm, "end": v(-210.1, 192.97) * mm});
            skLineSegment(sketch, "E5613", {"start": v(-210.1, 192.97) * mm, "end": v(-215.12, 193.25) * mm});
            skLineSegment(sketch, "E5614", {"start": v(-215.12, 193.25) * mm, "end": v(-219.6, 193.64) * mm});
            skLineSegment(sketch, "E5615", {"start": v(-219.6, 193.64) * mm, "end": v(-223.66, 194.15) * mm});
            skLineSegment(sketch, "E5616", {"start": v(-223.66, 194.15) * mm, "end": v(-227.4, 194.78) * mm});
            skLineSegment(sketch, "E5617", {"start": v(-227.4, 194.78) * mm, "end": v(-230.93, 195.52) * mm});
            skLineSegment(sketch, "E5618", {"start": v(-230.93, 195.52) * mm, "end": v(-234.36, 196.4) * mm});
            skLineSegment(sketch, "E5619", {"start": v(-234.36, 196.4) * mm, "end": v(-237.82, 197.4) * mm});
            skLineSegment(sketch, "E5620", {"start": v(-237.82, 197.4) * mm, "end": v(-241.38, 198.52) * mm});
            skLineSegment(sketch, "E5621", {"start": v(-241.38, 198.52) * mm, "end": v(-245.2, 199.77) * mm});
            skLineSegment(sketch, "E5622", {"start": v(-245.2, 199.77) * mm, "end": v(-249.34, 201.16) * mm});
            skLineSegment(sketch, "E5623", {"start": v(-249.34, 201.16) * mm, "end": v(-253.94, 202.68) * mm});
            skLineSegment(sketch, "E5624", {"start": v(-253.94, 202.68) * mm, "end": v(-259.1, 204.34) * mm});
            skLineSegment(sketch, "E5625", {"start": v(-259.1, 204.34) * mm, "end": v(-264.94, 206.14) * mm});
            skLineSegment(sketch, "E5626", {"start": v(-264.94, 206.14) * mm, "end": v(-269.9, 207.6) * mm});
            skLineSegment(sketch, "E5627", {"start": v(-269.9, 207.6) * mm, "end": v(-271.56, 208.08) * mm});
            skLineSegment(sketch, "E5628", {"start": v(-271.56, 208.08) * mm, "end": v(-272.3, 208.3) * mm});
            skLineSegment(sketch, "E5629", {"start": v(-272.3, 208.3) * mm, "end": v(-274.56, 208.93) * mm});
            skLineSegment(sketch, "E5630", {"start": v(-274.56, 208.93) * mm, "end": v(-278.18, 209.93) * mm});
            skLineSegment(sketch, "E5631", {"start": v(-278.18, 209.93) * mm, "end": v(-282.35, 211.06) * mm});
            skLineSegment(sketch, "E5632", {"start": v(-282.35, 211.06) * mm, "end": v(-286.98, 212.3) * mm});
            skLineSegment(sketch, "E5633", {"start": v(-286.98, 212.3) * mm, "end": v(-291.99, 213.6) * mm});
            skLineSegment(sketch, "E5634", {"start": v(-291.99, 213.6) * mm, "end": v(-297.31, 214.96) * mm});
            skLineSegment(sketch, "E5635", {"start": v(-297.31, 214.96) * mm, "end": v(-302.86, 216.34) * mm});
            skLineSegment(sketch, "E5636", {"start": v(-302.86, 216.34) * mm, "end": v(-308.57, 217.72) * mm});
            skLineSegment(sketch, "E5637", {"start": v(-308.57, 217.72) * mm, "end": v(-314.35, 219.08) * mm});
            skLineSegment(sketch, "E5638", {"start": v(-314.35, 219.08) * mm, "end": v(-320.14, 220.38) * mm});
            skLineSegment(sketch, "E5639", {"start": v(-320.14, 220.38) * mm, "end": v(-325.85, 221.6) * mm});
            skLineSegment(sketch, "E5640", {"start": v(-325.85, 221.6) * mm, "end": v(-331.4, 222.72) * mm});
            skLineSegment(sketch, "E5641", {"start": v(-331.4, 222.72) * mm, "end": v(-336.72, 223.7) * mm});
            skLineSegment(sketch, "E5642", {"start": v(-336.72, 223.7) * mm, "end": v(-341.73, 224.54) * mm});
            skLineSegment(sketch, "E5643", {"start": v(-341.73, 224.54) * mm, "end": v(-346.36, 225.18) * mm});
            skLineSegment(sketch, "E5644", {"start": v(-346.36, 225.18) * mm, "end": v(-349.47, 225.53) * mm});
            skLineSegment(sketch, "E5645", {"start": v(-349.47, 225.53) * mm, "end": v(-350.51, 225.62) * mm});
            skLineSegment(sketch, "E5646", {"start": v(-350.51, 225.62) * mm, "end": v(-352.74, 225.8) * mm});
            skLineSegment(sketch, "E5647", {"start": v(-352.74, 225.8) * mm, "end": v(-359.43, 226.24) * mm});
            skLineSegment(sketch, "E5648", {"start": v(-359.43, 226.24) * mm, "end": v(-367.05, 226.53) * mm});
            skLineSegment(sketch, "E5649", {"start": v(-367.05, 226.53) * mm, "end": v(-373.83, 226.57) * mm});
            skLineSegment(sketch, "E5650", {"start": v(-373.83, 226.57) * mm, "end": v(-380.2, 226.43) * mm});
            skLineSegment(sketch, "E5651", {"start": v(-380.2, 226.43) * mm, "end": v(-386.63, 226.19) * mm});
            skLineSegment(sketch, "E5652", {"start": v(-386.63, 226.19) * mm, "end": v(-393.57, 225.92) * mm});
            skLineSegment(sketch, "E5653", {"start": v(-393.57, 225.92) * mm, "end": v(-401.45, 225.7) * mm});
            skLineSegment(sketch, "E5654", {"start": v(-401.45, 225.7) * mm, "end": v(-408.4, 225.62) * mm});
            skLineSegment(sketch, "E5655", {"start": v(-408.4, 225.62) * mm, "end": v(-410.72, 225.62) * mm});
            skLineSegment(sketch, "E5656", {"start": v(-410.72, 225.62) * mm, "end": v(-412.24, 225.62) * mm});
            skLineSegment(sketch, "E5657", {"start": v(-412.24, 225.62) * mm, "end": v(-416.8, 225.74) * mm});
            skLineSegment(sketch, "E5658", {"start": v(-416.8, 225.74) * mm, "end": v(-423.95, 226.1) * mm});
            skLineSegment(sketch, "E5659", {"start": v(-423.95, 226.1) * mm, "end": v(-431.97, 226.64) * mm});
            skLineSegment(sketch, "E5660", {"start": v(-431.97, 226.64) * mm, "end": v(-440.64, 227.36) * mm});
            skLineSegment(sketch, "E5661", {"start": v(-440.64, 227.36) * mm, "end": v(-449.78, 228.2) * mm});
            skLineSegment(sketch, "E5662", {"start": v(-449.78, 228.2) * mm, "end": v(-459.18, 229.13) * mm});
            skLineSegment(sketch, "E5663", {"start": v(-459.18, 229.13) * mm, "end": v(-468.64, 230.14) * mm});
            skLineSegment(sketch, "E5664", {"start": v(-468.64, 230.14) * mm, "end": v(-477.95, 231.17) * mm});
            skLineSegment(sketch, "E5665", {"start": v(-477.95, 231.17) * mm, "end": v(-486.93, 232.2) * mm});
            skLineSegment(sketch, "E5666", {"start": v(-486.93, 232.2) * mm, "end": v(-495.36, 233.21) * mm});
            skLineSegment(sketch, "E5667", {"start": v(-495.36, 233.21) * mm, "end": v(-503.04, 234.15) * mm});
            skLineSegment(sketch, "E5668", {"start": v(-503.04, 234.15) * mm, "end": v(-509.78, 235) * mm});
            skLineSegment(sketch, "E5669", {"start": v(-509.78, 235) * mm, "end": v(-515.37, 235.7) * mm});
            skLineSegment(sketch, "E5670", {"start": v(-515.37, 235.7) * mm, "end": v(-519.61, 236.25) * mm});
            skLineSegment(sketch, "E5671", {"start": v(-519.61, 236.25) * mm, "end": v(-522.3, 236.6) * mm});
            skLineSegment(sketch, "E5672", {"start": v(-522.3, 236.6) * mm, "end": v(-523.25, 236.73) * mm});
            skLineSegment(sketch, "E5673", {"start": v(610.28, -90.56) * mm, "end": v(605.97, -89.67) * mm});
            skLineSegment(sketch, "E5674", {"start": v(605.97, -89.67) * mm, "end": v(593.07, -86.87) * mm});
            skLineSegment(sketch, "E5675", {"start": v(593.07, -86.87) * mm, "end": v(575.55, -82.82) * mm});
            skLineSegment(sketch, "E5676", {"start": v(575.55, -82.82) * mm, "end": v(557.77, -78.37) * mm});
            skLineSegment(sketch, "E5677", {"start": v(557.77, -78.37) * mm, "end": v(539.78, -73.5) * mm});
            skLineSegment(sketch, "E5678", {"start": v(539.78, -73.5) * mm, "end": v(521.6, -68.2) * mm});
            skLineSegment(sketch, "E5679", {"start": v(521.6, -68.2) * mm, "end": v(503.3, -62.4) * mm});
            skLineSegment(sketch, "E5680", {"start": v(503.3, -62.4) * mm, "end": v(484.91, -56.14) * mm});
            skLineSegment(sketch, "E5681", {"start": v(484.91, -56.14) * mm, "end": v(466.46, -49.35) * mm});
            skLineSegment(sketch, "E5682", {"start": v(466.46, -49.35) * mm, "end": v(448, -42.02) * mm});
            skLineSegment(sketch, "E5683", {"start": v(448, -42.02) * mm, "end": v(429.6, -34.13) * mm});
            skLineSegment(sketch, "E5684", {"start": v(429.6, -34.13) * mm, "end": v(411.25, -25.66) * mm});
            skLineSegment(sketch, "E5685", {"start": v(411.25, -25.66) * mm, "end": v(393.02, -16.57) * mm});
            skLineSegment(sketch, "E5686", {"start": v(393.02, -16.57) * mm, "end": v(374.96, -6.84) * mm});
            skLineSegment(sketch, "E5687", {"start": v(374.96, -6.84) * mm, "end": v(357.1, 3.54) * mm});
            skLineSegment(sketch, "E5688", {"start": v(357.1, 3.54) * mm, "end": v(339.47, 14.6) * mm});
            skLineSegment(sketch, "E5689", {"start": v(339.47, 14.6) * mm, "end": v(326.42, 23.36) * mm});
            skLineSegment(sketch, "E5690", {"start": v(326.42, 23.36) * mm, "end": v(322.14, 26.38) * mm});
            skLineSegment(sketch, "E5691", {"start": v(322.14, 26.38) * mm, "end": v(319.94, 27.93) * mm});
            skLineSegment(sketch, "E5692", {"start": v(319.94, 27.93) * mm, "end": v(313.4, 32.67) * mm});
            skLineSegment(sketch, "E5693", {"start": v(313.4, 32.67) * mm, "end": v(304.42, 39.36) * mm});
            skLineSegment(sketch, "E5694", {"start": v(304.42, 39.36) * mm, "end": v(295.2, 46.42) * mm});
            skLineSegment(sketch, "E5695", {"start": v(295.2, 46.42) * mm, "end": v(285.75, 53.8) * mm});
            skLineSegment(sketch, "E5696", {"start": v(285.75, 53.8) * mm, "end": v(276.12, 61.5) * mm});
            skLineSegment(sketch, "E5697", {"start": v(276.12, 61.5) * mm, "end": v(266.34, 69.44) * mm});
            skLineSegment(sketch, "E5698", {"start": v(266.34, 69.44) * mm, "end": v(256.42, 77.6) * mm});
            skLineSegment(sketch, "E5699", {"start": v(256.42, 77.6) * mm, "end": v(246.4, 85.95) * mm});
            skLineSegment(sketch, "E5700", {"start": v(246.4, 85.95) * mm, "end": v(236.29, 94.44) * mm});
            skLineSegment(sketch, "E5701", {"start": v(236.29, 94.44) * mm, "end": v(226.13, 103.04) * mm});
            skLineSegment(sketch, "E5702", {"start": v(226.13, 103.04) * mm, "end": v(215.93, 111.7) * mm});
            skLineSegment(sketch, "E5703", {"start": v(215.93, 111.7) * mm, "end": v(205.74, 120.41) * mm});
            skLineSegment(sketch, "E5704", {"start": v(205.74, 120.41) * mm, "end": v(195.57, 129.11) * mm});
            skLineSegment(sketch, "E5705", {"start": v(195.57, 129.11) * mm, "end": v(185.44, 137.76) * mm});
            skLineSegment(sketch, "E5706", {"start": v(185.44, 137.76) * mm, "end": v(175.4, 146.34) * mm});
            skLineSegment(sketch, "E5707", {"start": v(175.4, 146.34) * mm, "end": v(165.44, 154.8) * mm});
            skLineSegment(sketch, "E5708", {"start": v(165.44, 154.8) * mm, "end": v(155.62, 163.11) * mm});
            skLineSegment(sketch, "E5709", {"start": v(155.62, 163.11) * mm, "end": v(145.95, 171.23) * mm});
            skLineSegment(sketch, "E5710", {"start": v(145.95, 171.23) * mm, "end": v(136.47, 179.12) * mm});
            skLineSegment(sketch, "E5711", {"start": v(136.47, 179.12) * mm, "end": v(127.18, 186.75) * mm});
            skLineSegment(sketch, "E5712", {"start": v(127.18, 186.75) * mm, "end": v(118.12, 194.07) * mm});
            skLineSegment(sketch, "E5713", {"start": v(118.12, 194.07) * mm, "end": v(109.32, 201.05) * mm});
            skLineSegment(sketch, "E5714", {"start": v(109.32, 201.05) * mm, "end": v(100.8, 207.65) * mm});
            skLineSegment(sketch, "E5715", {"start": v(100.8, 207.65) * mm, "end": v(92.6, 213.84) * mm});
            skLineSegment(sketch, "E5716", {"start": v(92.6, 213.84) * mm, "end": v(84.73, 219.58) * mm});
            skLineSegment(sketch, "E5717", {"start": v(84.73, 219.58) * mm, "end": v(77.21, 224.83) * mm});
            skLineSegment(sketch, "E5718", {"start": v(77.21, 224.83) * mm, "end": v(70.1, 229.55) * mm});
            skLineSegment(sketch, "E5719", {"start": v(70.1, 229.55) * mm, "end": v(63.38, 233.7) * mm});
            skLineSegment(sketch, "E5720", {"start": v(63.38, 233.7) * mm, "end": v(57.1, 237.25) * mm});
            skLineSegment(sketch, "E5721", {"start": v(57.1, 237.25) * mm, "end": v(51.29, 240.17) * mm});
            skLineSegment(sketch, "E5722", {"start": v(51.29, 240.17) * mm, "end": v(45.97, 242.41) * mm});
            skLineSegment(sketch, "E5723", {"start": v(45.97, 242.41) * mm, "end": v(42.39, 243.63) * mm});
            skLineSegment(sketch, "E5724", {"start": v(42.39, 243.63) * mm, "end": v(41.17, 243.94) * mm});
            skLineSegment(sketch, "E5725", {"start": v(41.17, 243.94) * mm, "end": v(39.13, 244.46) * mm});
            skLineSegment(sketch, "E5726", {"start": v(39.13, 244.46) * mm, "end": v(32.95, 245.73) * mm});
            skLineSegment(sketch, "E5727", {"start": v(32.95, 245.73) * mm, "end": v(25.4, 246.77) * mm});
            skLineSegment(sketch, "E5728", {"start": v(25.4, 246.77) * mm, "end": v(18.43, 247.14) * mm});
            skLineSegment(sketch, "E5729", {"start": v(18.43, 247.14) * mm, "end": v(11.9, 246.94) * mm});
            skLineSegment(sketch, "E5730", {"start": v(11.9, 246.94) * mm, "end": v(5.72, 246.25) * mm});
            skLineSegment(sketch, "E5731", {"start": v(5.72, 246.25) * mm, "end": v(-0.21, 245.15) * mm});
            skLineSegment(sketch, "E5732", {"start": v(-0.21, 245.15) * mm, "end": v(-6.03, 243.73) * mm});
            skLineSegment(sketch, "E5733", {"start": v(-6.03, 243.73) * mm, "end": v(-11.82, 242.07) * mm});
            skLineSegment(sketch, "E5734", {"start": v(-11.82, 242.07) * mm, "end": v(-17.71, 240.26) * mm});
            skLineSegment(sketch, "E5735", {"start": v(-17.71, 240.26) * mm, "end": v(-23.8, 238.39) * mm});
            skLineSegment(sketch, "E5736", {"start": v(-23.8, 238.39) * mm, "end": v(-30.19, 236.53) * mm});
            skLineSegment(sketch, "E5737", {"start": v(-30.19, 236.53) * mm, "end": v(-37, 234.78) * mm});
            skLineSegment(sketch, "E5738", {"start": v(-37, 234.78) * mm, "end": v(-44.33, 233.23) * mm});
            skLineSegment(sketch, "E5739", {"start": v(-44.33, 233.23) * mm, "end": v(-52.3, 231.95) * mm});
            skLineSegment(sketch, "E5740", {"start": v(-52.3, 231.95) * mm, "end": v(-61.03, 231.03) * mm});
            skLineSegment(sketch, "E5741", {"start": v(-61.03, 231.03) * mm, "end": v(-68.2, 230.62) * mm});
            skLineSegment(sketch, "E5742", {"start": v(-68.2, 230.62) * mm, "end": v(-70.6, 230.56) * mm});
            skLineSegment(sketch, "E5743", {"start": v(-70.6, 230.56) * mm, "end": v(-73.03, 230.5) * mm});
            skLineSegment(sketch, "E5744", {"start": v(-73.03, 230.5) * mm, "end": v(-80.31, 230.23) * mm});
            skLineSegment(sketch, "E5745", {"start": v(-80.31, 230.23) * mm, "end": v(-89.4, 229.67) * mm});
            skLineSegment(sketch, "E5746", {"start": v(-89.4, 229.67) * mm, "end": v(-97.9, 228.91) * mm});
            skLineSegment(sketch, "E5747", {"start": v(-97.9, 228.91) * mm, "end": v(-105.83, 228) * mm});
            skLineSegment(sketch, "E5748", {"start": v(-105.83, 228) * mm, "end": v(-113.21, 226.92) * mm});
            skLineSegment(sketch, "E5749", {"start": v(-113.21, 226.92) * mm, "end": v(-120.09, 225.72) * mm});
            skLineSegment(sketch, "E5750", {"start": v(-120.09, 225.72) * mm, "end": v(-126.48, 224.43) * mm});
            skLineSegment(sketch, "E5751", {"start": v(-126.48, 224.43) * mm, "end": v(-132.41, 223.08) * mm});
            skLineSegment(sketch, "E5752", {"start": v(-132.41, 223.08) * mm, "end": v(-137.92, 221.67) * mm});
            skLineSegment(sketch, "E5753", {"start": v(-137.92, 221.67) * mm, "end": v(-143.02, 220.24) * mm});
            skLineSegment(sketch, "E5754", {"start": v(-143.02, 220.24) * mm, "end": v(-147.76, 218.82) * mm});
            skLineSegment(sketch, "E5755", {"start": v(-147.76, 218.82) * mm, "end": v(-152.14, 217.42) * mm});
            skLineSegment(sketch, "E5756", {"start": v(-152.14, 217.42) * mm, "end": v(-156.2, 216.09) * mm});
            skLineSegment(sketch, "E5757", {"start": v(-156.2, 216.09) * mm, "end": v(-159.99, 214.83) * mm});
            skLineSegment(sketch, "E5758", {"start": v(-159.99, 214.83) * mm, "end": v(-163.5, 213.67) * mm});
            skLineSegment(sketch, "E5759", {"start": v(-163.5, 213.67) * mm, "end": v(-165.96, 212.89) * mm});
            skLineSegment(sketch, "E5760", {"start": v(-165.96, 212.89) * mm, "end": v(-166.78, 212.64) * mm});
            skLineSegment(sketch, "E5761", {"start": v(-166.78, 212.64) * mm, "end": v(-167.65, 212.38) * mm});
            skLineSegment(sketch, "E5762", {"start": v(-167.65, 212.38) * mm, "end": v(-170.33, 211.79) * mm});
            skLineSegment(sketch, "E5763", {"start": v(-170.33, 211.79) * mm, "end": v(-174.58, 211.13) * mm});
            skLineSegment(sketch, "E5764", {"start": v(-174.58, 211.13) * mm, "end": v(-179.47, 210.68) * mm});
            skLineSegment(sketch, "E5765", {"start": v(-179.47, 210.68) * mm, "end": v(-184.93, 210.42) * mm});
            skLineSegment(sketch, "E5766", {"start": v(-184.93, 210.42) * mm, "end": v(-190.9, 210.36) * mm});
            skLineSegment(sketch, "E5767", {"start": v(-190.9, 210.36) * mm, "end": v(-197.3, 210.48) * mm});
            skLineSegment(sketch, "E5768", {"start": v(-197.3, 210.48) * mm, "end": v(-204.08, 210.8) * mm});
            skLineSegment(sketch, "E5769", {"start": v(-204.08, 210.8) * mm, "end": v(-211.17, 211.3) * mm});
            skLineSegment(sketch, "E5770", {"start": v(-211.17, 211.3) * mm, "end": v(-218.5, 212) * mm});
            skLineSegment(sketch, "E5771", {"start": v(-218.5, 212) * mm, "end": v(-226, 212.87) * mm});
            skLineSegment(sketch, "E5772", {"start": v(-226, 212.87) * mm, "end": v(-233.61, 213.93) * mm});
            skLineSegment(sketch, "E5773", {"start": v(-233.61, 213.93) * mm, "end": v(-241.27, 215.16) * mm});
            skLineSegment(sketch, "E5774", {"start": v(-241.27, 215.16) * mm, "end": v(-248.9, 216.57) * mm});
            skLineSegment(sketch, "E5775", {"start": v(-248.9, 216.57) * mm, "end": v(-256.45, 218.16) * mm});
            skLineSegment(sketch, "E5776", {"start": v(-256.45, 218.16) * mm, "end": v(-263.85, 219.91) * mm});
            skLineSegment(sketch, "E5777", {"start": v(-263.85, 219.91) * mm, "end": v(-269.24, 221.33) * mm});
            skLineSegment(sketch, "E5778", {"start": v(-269.24, 221.33) * mm, "end": v(-271.03, 221.84) * mm});
            skLineSegment(sketch, "E5779", {"start": v(-271.03, 221.84) * mm, "end": v(-272.55, 222.27) * mm});
            skLineSegment(sketch, "E5780", {"start": v(-272.55, 222.27) * mm, "end": v(-277.2, 223.33) * mm});
            skLineSegment(sketch, "E5781", {"start": v(-277.2, 223.33) * mm, "end": v(-284.86, 224.83) * mm});
            skLineSegment(sketch, "E5782", {"start": v(-284.86, 224.83) * mm, "end": v(-293.84, 226.43) * mm});
            skLineSegment(sketch, "E5783", {"start": v(-293.84, 226.43) * mm, "end": v(-303.9, 228.22) * mm});
            skLineSegment(sketch, "E5784", {"start": v(-303.9, 228.22) * mm, "end": v(-314.86, 230.3) * mm});
            skLineSegment(sketch, "E5785", {"start": v(-314.86, 230.3) * mm, "end": v(-326.5, 232.76) * mm});
            skLineSegment(sketch, "E5786", {"start": v(-326.5, 232.76) * mm, "end": v(-338.6, 235.7) * mm});
            skLineSegment(sketch, "E5787", {"start": v(-338.6, 235.7) * mm, "end": v(-347.92, 238.28) * mm});
            skLineSegment(sketch, "E5788", {"start": v(-347.92, 238.28) * mm, "end": v(-351, 239.23) * mm});
            skLineSegment(sketch, "E5789", {"start": v(-351, 239.23) * mm, "end": v(-352.1, 239.57) * mm});
            skLineSegment(sketch, "E5790", {"start": v(-352.1, 239.57) * mm, "end": v(-355.46, 240.5) * mm});
            skLineSegment(sketch, "E5791", {"start": v(-355.46, 240.5) * mm, "end": v(-359.6, 241.43) * mm});
            skLineSegment(sketch, "E5792", {"start": v(-359.6, 241.43) * mm, "end": v(-363.46, 242.07) * mm});
            skLineSegment(sketch, "E5793", {"start": v(-363.46, 242.07) * mm, "end": v(-367.08, 242.46) * mm});
            skLineSegment(sketch, "E5794", {"start": v(-367.08, 242.46) * mm, "end": v(-370.53, 242.62) * mm});
            skLineSegment(sketch, "E5795", {"start": v(-370.53, 242.62) * mm, "end": v(-373.85, 242.6) * mm});
            skLineSegment(sketch, "E5796", {"start": v(-373.85, 242.6) * mm, "end": v(-377.1, 242.4) * mm});
            skLineSegment(sketch, "E5797", {"start": v(-377.1, 242.4) * mm, "end": v(-380.3, 242.1) * mm});
            skLineSegment(sketch, "E5798", {"start": v(-380.3, 242.1) * mm, "end": v(-383.55, 241.7) * mm});
            skLineSegment(sketch, "E5799", {"start": v(-383.55, 241.7) * mm, "end": v(-386.87, 241.25) * mm});
            skLineSegment(sketch, "E5800", {"start": v(-386.87, 241.25) * mm, "end": v(-390.31, 240.77) * mm});
            skLineSegment(sketch, "E5801", {"start": v(-390.31, 240.77) * mm, "end": v(-393.94, 240.3) * mm});
            skLineSegment(sketch, "E5802", {"start": v(-393.94, 240.3) * mm, "end": v(-397.8, 239.89) * mm});
            skLineSegment(sketch, "E5803", {"start": v(-397.8, 239.89) * mm, "end": v(-401.93, 239.54) * mm});
            skLineSegment(sketch, "E5804", {"start": v(-401.93, 239.54) * mm, "end": v(-406.4, 239.31) * mm});
            skLineSegment(sketch, "E5805", {"start": v(-406.4, 239.31) * mm, "end": v(-410.03, 239.23) * mm});
            skLineSegment(sketch, "E5806", {"start": v(-410.03, 239.23) * mm, "end": v(-411.25, 239.23) * mm});
            skLineSegment(sketch, "E5807", {"start": v(-411.25, 239.23) * mm, "end": v(-412.78, 239.23) * mm});
            skLineSegment(sketch, "E5808", {"start": v(-412.78, 239.23) * mm, "end": v(-417.37, 239.39) * mm});
            skLineSegment(sketch, "E5809", {"start": v(-417.37, 239.39) * mm, "end": v(-424.62, 239.84) * mm});
            skLineSegment(sketch, "E5810", {"start": v(-424.62, 239.84) * mm, "end": v(-432.8, 240.54) * mm});
            skLineSegment(sketch, "E5811", {"start": v(-432.8, 240.54) * mm, "end": v(-441.69, 241.44) * mm});
            skLineSegment(sketch, "E5812", {"start": v(-441.69, 241.44) * mm, "end": v(-451.07, 242.51) * mm});
            skLineSegment(sketch, "E5813", {"start": v(-451.07, 242.51) * mm, "end": v(-460.75, 243.7) * mm});
            skLineSegment(sketch, "E5814", {"start": v(-460.75, 243.7) * mm, "end": v(-470.5, 244.98) * mm});
            skLineSegment(sketch, "E5815", {"start": v(-470.5, 244.98) * mm, "end": v(-480.12, 246.3) * mm});
            skLineSegment(sketch, "E5816", {"start": v(-480.12, 246.3) * mm, "end": v(-489.4, 247.62) * mm});
            skLineSegment(sketch, "E5817", {"start": v(-489.4, 247.62) * mm, "end": v(-498.13, 248.9) * mm});
            skLineSegment(sketch, "E5818", {"start": v(-498.13, 248.9) * mm, "end": v(-506.1, 250.1) * mm});
            skLineSegment(sketch, "E5819", {"start": v(-506.1, 250.1) * mm, "end": v(-513.08, 251.17) * mm});
            skLineSegment(sketch, "E5820", {"start": v(-513.08, 251.17) * mm, "end": v(-518.88, 252.07) * mm});
            skLineSegment(sketch, "E5821", {"start": v(-518.88, 252.07) * mm, "end": v(-523.29, 252.77) * mm});
            skLineSegment(sketch, "E5822", {"start": v(-523.29, 252.77) * mm, "end": v(-526.08, 253.22) * mm});
            skLineSegment(sketch, "E5823", {"start": v(-526.08, 253.22) * mm, "end": v(-527.06, 253.38) * mm});
            skLineSegment(sketch, "E5824", {"start": v(610.28, -228.81) * mm, "end": v(605.62, -227.58) * mm});
            skLineSegment(sketch, "E5825", {"start": v(605.62, -227.58) * mm, "end": v(591.7, -223.76) * mm});
            skLineSegment(sketch, "E5826", {"start": v(591.7, -223.76) * mm, "end": v(573.02, -218.41) * mm});
            skLineSegment(sketch, "E5827", {"start": v(573.02, -218.41) * mm, "end": v(554.33, -212.8) * mm});
            skLineSegment(sketch, "E5828", {"start": v(554.33, -212.8) * mm, "end": v(535.7, -206.98) * mm});
            skLineSegment(sketch, "E5829", {"start": v(535.7, -206.98) * mm, "end": v(517.22, -200.97) * mm});
            skLineSegment(sketch, "E5830", {"start": v(517.22, -200.97) * mm, "end": v(498.97, -194.81) * mm});
            skLineSegment(sketch, "E5831", {"start": v(498.97, -194.81) * mm, "end": v(481.04, -188.54) * mm});
            skLineSegment(sketch, "E5832", {"start": v(481.04, -188.54) * mm, "end": v(463.5, -182.18) * mm});
            skLineSegment(sketch, "E5833", {"start": v(463.5, -182.18) * mm, "end": v(446.44, -175.8) * mm});
            skLineSegment(sketch, "E5834", {"start": v(446.44, -175.8) * mm, "end": v(429.93, -169.39) * mm});
            skLineSegment(sketch, "E5835", {"start": v(429.93, -169.39) * mm, "end": v(414.06, -163.02) * mm});
            skLineSegment(sketch, "E5836", {"start": v(414.06, -163.02) * mm, "end": v(398.92, -156.71) * mm});
            skLineSegment(sketch, "E5837", {"start": v(398.92, -156.71) * mm, "end": v(384.58, -150.5) * mm});
            skLineSegment(sketch, "E5838", {"start": v(384.58, -150.5) * mm, "end": v(371.12, -144.44) * mm});
            skLineSegment(sketch, "E5839", {"start": v(371.12, -144.44) * mm, "end": v(358.63, -138.54) * mm});
            skLineSegment(sketch, "E5840", {"start": v(358.63, -138.54) * mm, "end": v(350.03, -134.31) * mm});
            skLineSegment(sketch, "E5841", {"start": v(350.03, -134.31) * mm, "end": v(347.19, -132.86) * mm});
            skLineSegment(sketch, "E5842", {"start": v(347.19, -132.86) * mm, "end": v(344.29, -131.37) * mm});
            skLineSegment(sketch, "E5843", {"start": v(344.29, -131.37) * mm, "end": v(335.61, -126.84) * mm});
            skLineSegment(sketch, "E5844", {"start": v(335.61, -126.84) * mm, "end": v(322.79, -120) * mm});
            skLineSegment(sketch, "E5845", {"start": v(322.79, -120) * mm, "end": v(308.92, -112.46) * mm});
            skLineSegment(sketch, "E5846", {"start": v(308.92, -112.46) * mm, "end": v(294.2, -104.32) * mm});
            skLineSegment(sketch, "E5847", {"start": v(294.2, -104.32) * mm, "end": v(278.82, -95.69) * mm});
            skLineSegment(sketch, "E5848", {"start": v(278.82, -95.69) * mm, "end": v(263, -86.68) * mm});
            skLineSegment(sketch, "E5849", {"start": v(263, -86.68) * mm, "end": v(246.91, -77.4) * mm});
            skLineSegment(sketch, "E5850", {"start": v(246.91, -77.4) * mm, "end": v(230.78, -67.97) * mm});
            skLineSegment(sketch, "E5851", {"start": v(230.78, -67.97) * mm, "end": v(214.79, -58.48) * mm});
            skLineSegment(sketch, "E5852", {"start": v(214.79, -58.48) * mm, "end": v(199.14, -49.06) * mm});
            skLineSegment(sketch, "E5853", {"start": v(199.14, -49.06) * mm, "end": v(184.03, -39.82) * mm});
            skLineSegment(sketch, "E5854", {"start": v(184.03, -39.82) * mm, "end": v(169.66, -30.86) * mm});
            skLineSegment(sketch, "E5855", {"start": v(169.66, -30.86) * mm, "end": v(156.22, -22.3) * mm});
            skLineSegment(sketch, "E5856", {"start": v(156.22, -22.3) * mm, "end": v(143.92, -14.23) * mm});
            skLineSegment(sketch, "E5857", {"start": v(143.92, -14.23) * mm, "end": v(132.96, -6.78) * mm});
            skLineSegment(sketch, "E5858", {"start": v(132.96, -6.78) * mm, "end": v(125.86, -1.78) * mm});
            skLineSegment(sketch, "E5859", {"start": v(125.86, -1.78) * mm, "end": v(123.53, -0.06) * mm});
            skLineSegment(sketch, "E5860", {"start": v(123.53, -0.06) * mm, "end": v(121.28, 1.59) * mm});
            skLineSegment(sketch, "E5861", {"start": v(121.28, 1.59) * mm, "end": v(114.74, 6.82) * mm});
            skLineSegment(sketch, "E5862", {"start": v(114.74, 6.82) * mm, "end": v(105.6, 14.68) * mm});
            skLineSegment(sketch, "E5863", {"start": v(105.6, 14.68) * mm, "end": v(96.12, 23.33) * mm});
            skLineSegment(sketch, "E5864", {"start": v(96.12, 23.33) * mm, "end": v(86.3, 32.57) * mm});
            skLineSegment(sketch, "E5865", {"start": v(86.3, 32.57) * mm, "end": v(76.19, 42.2) * mm});
            skLineSegment(sketch, "E5866", {"start": v(76.19, 42.2) * mm, "end": v(65.77, 52.04) * mm});
            skLineSegment(sketch, "E5867", {"start": v(65.77, 52.04) * mm, "end": v(55.08, 61.86) * mm});
            skLineSegment(sketch, "E5868", {"start": v(55.08, 61.86) * mm, "end": v(44.13, 71.5) * mm});
            skLineSegment(sketch, "E5869", {"start": v(44.13, 71.5) * mm, "end": v(32.94, 80.73) * mm});
            skLineSegment(sketch, "E5870", {"start": v(32.94, 80.73) * mm, "end": v(21.51, 89.37) * mm});
            skLineSegment(sketch, "E5871", {"start": v(21.51, 89.37) * mm, "end": v(9.88, 97.22) * mm});
            skLineSegment(sketch, "E5872", {"start": v(9.88, 97.22) * mm, "end": v(-1.95, 104.1) * mm});
            skLineSegment(sketch, "E5873", {"start": v(-1.95, 104.1) * mm, "end": v(-13.96, 109.77) * mm});
            skLineSegment(sketch, "E5874", {"start": v(-13.96, 109.77) * mm, "end": v(-26.14, 114.08) * mm});
            skLineSegment(sketch, "E5875", {"start": v(-26.14, 114.08) * mm, "end": v(-38.45, 116.8) * mm});
            skLineSegment(sketch, "E5876", {"start": v(-38.45, 116.8) * mm, "end": v(-47.8, 117.76) * mm});
            skLineSegment(sketch, "E5877", {"start": v(-47.8, 117.76) * mm, "end": v(-50.9, 117.76) * mm});
            skLineSegment(sketch, "E5878", {"start": v(-50.9, 117.76) * mm, "end": v(-54.85, 117.76) * mm});
            skLineSegment(sketch, "E5879", {"start": v(-54.85, 117.76) * mm, "end": v(-66.68, 117.39) * mm});
            skLineSegment(sketch, "E5880", {"start": v(-66.68, 117.39) * mm, "end": v(-80.86, 116.34) * mm});
            skLineSegment(sketch, "E5881", {"start": v(-80.86, 116.34) * mm, "end": v(-93.58, 114.72) * mm});
            skLineSegment(sketch, "E5882", {"start": v(-93.58, 114.72) * mm, "end": v(-105, 112.62) * mm});
            skLineSegment(sketch, "E5883", {"start": v(-105, 112.62) * mm, "end": v(-115.27, 110.13) * mm});
            skLineSegment(sketch, "E5884", {"start": v(-115.27, 110.13) * mm, "end": v(-124.54, 107.35) * mm});
            skLineSegment(sketch, "E5885", {"start": v(-124.54, 107.35) * mm, "end": v(-132.95, 104.37) * mm});
            skLineSegment(sketch, "E5886", {"start": v(-132.95, 104.37) * mm, "end": v(-140.65, 101.3) * mm});
            skLineSegment(sketch, "E5887", {"start": v(-140.65, 101.3) * mm, "end": v(-147.8, 98.24) * mm});
            skLineSegment(sketch, "E5888", {"start": v(-147.8, 98.24) * mm, "end": v(-154.54, 95.26) * mm});
            skLineSegment(sketch, "E5889", {"start": v(-154.54, 95.26) * mm, "end": v(-161.02, 92.49) * mm});
            skLineSegment(sketch, "E5890", {"start": v(-161.02, 92.49) * mm, "end": v(-167.4, 90) * mm});
            skLineSegment(sketch, "E5891", {"start": v(-167.4, 90) * mm, "end": v(-173.82, 87.9) * mm});
            skLineSegment(sketch, "E5892", {"start": v(-173.82, 87.9) * mm, "end": v(-180.43, 86.27) * mm});
            skLineSegment(sketch, "E5893", {"start": v(-180.43, 86.27) * mm, "end": v(-187.38, 85.22) * mm});
            skLineSegment(sketch, "E5894", {"start": v(-187.38, 85.22) * mm, "end": v(-192.97, 84.85) * mm});
            skLineSegment(sketch, "E5895", {"start": v(-192.97, 84.85) * mm, "end": v(-194.83, 84.85) * mm});
            skLineSegment(sketch, "E5896", {"start": v(-194.83, 84.85) * mm, "end": v(-198.44, 85.04) * mm});
            skLineSegment(sketch, "E5897", {"start": v(-198.44, 85.04) * mm, "end": v(-209.24, 85.96) * mm});
            skLineSegment(sketch, "E5898", {"start": v(-209.24, 85.96) * mm, "end": v(-222.89, 87.65) * mm});
            skLineSegment(sketch, "E5899", {"start": v(-222.89, 87.65) * mm, "end": v(-235.9, 89.79) * mm});
            skLineSegment(sketch, "E5900", {"start": v(-235.9, 89.79) * mm, "end": v(-248.47, 92.21) * mm});
            skLineSegment(sketch, "E5901", {"start": v(-248.47, 92.21) * mm, "end": v(-260.7, 94.78) * mm});
            skLineSegment(sketch, "E5902", {"start": v(-260.7, 94.78) * mm, "end": v(-272.8, 97.34) * mm});
            skLineSegment(sketch, "E5903", {"start": v(-272.8, 97.34) * mm, "end": v(-284.9, 99.74) * mm});
            skLineSegment(sketch, "E5904", {"start": v(-284.9, 99.74) * mm, "end": v(-294.06, 101.37) * mm});
            skLineSegment(sketch, "E5905", {"start": v(-294.06, 101.37) * mm, "end": v(-297.13, 101.83) * mm});
            skLineSegment(sketch, "E5906", {"start": v(-297.13, 101.83) * mm, "end": v(-298.41, 102.03) * mm});
            skLineSegment(sketch, "E5907", {"start": v(-298.41, 102.03) * mm, "end": v(-302.21, 102.9) * mm});
            skLineSegment(sketch, "E5908", {"start": v(-302.21, 102.9) * mm, "end": v(-307.34, 104.46) * mm});
            skLineSegment(sketch, "E5909", {"start": v(-307.34, 104.46) * mm, "end": v(-312.61, 106.32) * mm});
            skLineSegment(sketch, "E5910", {"start": v(-312.61, 106.32) * mm, "end": v(-318.14, 108.33) * mm});
            skLineSegment(sketch, "E5911", {"start": v(-318.14, 108.33) * mm, "end": v(-324, 110.32) * mm});
            skLineSegment(sketch, "E5912", {"start": v(-324, 110.32) * mm, "end": v(-330.3, 112.14) * mm});
            skLineSegment(sketch, "E5913", {"start": v(-330.3, 112.14) * mm, "end": v(-337.12, 113.6) * mm});
            skLineSegment(sketch, "E5914", {"start": v(-337.12, 113.6) * mm, "end": v(-342.7, 114.41) * mm});
            skLineSegment(sketch, "E5915", {"start": v(-342.7, 114.41) * mm, "end": v(-344.58, 114.57) * mm});
            skLineSegment(sketch, "E5916", {"start": v(-344.58, 114.57) * mm, "end": v(-346.84, 114.76) * mm});
            skLineSegment(sketch, "E5917", {"start": v(-346.84, 114.76) * mm, "end": v(-353.64, 115.03) * mm});
            skLineSegment(sketch, "E5918", {"start": v(-353.64, 115.03) * mm, "end": v(-361.61, 114.95) * mm});
            skLineSegment(sketch, "E5919", {"start": v(-361.61, 114.95) * mm, "end": v(-368.85, 114.53) * mm});
            skLineSegment(sketch, "E5920", {"start": v(-368.85, 114.53) * mm, "end": v(-375.7, 113.98) * mm});
            skLineSegment(sketch, "E5921", {"start": v(-375.7, 113.98) * mm, "end": v(-382.49, 113.5) * mm});
            skLineSegment(sketch, "E5922", {"start": v(-382.49, 113.5) * mm, "end": v(-389.56, 113.3) * mm});
            skLineSegment(sketch, "E5923", {"start": v(-389.56, 113.3) * mm, "end": v(-397.25, 113.59) * mm});
            skLineSegment(sketch, "E5924", {"start": v(-397.25, 113.59) * mm, "end": v(-403.76, 114.24) * mm});
            skLineSegment(sketch, "E5925", {"start": v(-403.76, 114.24) * mm, "end": v(-405.91, 114.57) * mm});
            skLineSegment(sketch, "E5926", {"start": v(-405.91, 114.57) * mm, "end": v(-407.37, 114.79) * mm});
            skLineSegment(sketch, "E5927", {"start": v(-407.37, 114.79) * mm, "end": v(-411.75, 115.46) * mm});
            skLineSegment(sketch, "E5928", {"start": v(-411.75, 115.46) * mm, "end": v(-418.33, 116.47) * mm});
            skLineSegment(sketch, "E5929", {"start": v(-418.33, 116.47) * mm, "end": v(-425.48, 117.58) * mm});
            skLineSegment(sketch, "E5930", {"start": v(-425.48, 117.58) * mm, "end": v(-433.06, 118.77) * mm});
            skLineSegment(sketch, "E5931", {"start": v(-433.06, 118.77) * mm, "end": v(-440.9, 120) * mm});
            skLineSegment(sketch, "E5932", {"start": v(-440.9, 120) * mm, "end": v(-448.88, 121.26) * mm});
            skLineSegment(sketch, "E5933", {"start": v(-448.88, 121.26) * mm, "end": v(-456.82, 122.52) * mm});
            skLineSegment(sketch, "E5934", {"start": v(-456.82, 122.52) * mm, "end": v(-464.57, 123.75) * mm});
            skLineSegment(sketch, "E5935", {"start": v(-464.57, 123.75) * mm, "end": v(-471.98, 124.93) * mm});
            skLineSegment(sketch, "E5936", {"start": v(-471.98, 124.93) * mm, "end": v(-478.9, 126.03) * mm});
            skLineSegment(sketch, "E5937", {"start": v(-478.9, 126.03) * mm, "end": v(-485.17, 127.04) * mm});
            skLineSegment(sketch, "E5938", {"start": v(-485.17, 127.04) * mm, "end": v(-490.65, 127.91) * mm});
            skLineSegment(sketch, "E5939", {"start": v(-490.65, 127.91) * mm, "end": v(-495.18, 128.64) * mm});
            skLineSegment(sketch, "E5940", {"start": v(-495.18, 128.64) * mm, "end": v(-498.6, 129.18) * mm});
            skLineSegment(sketch, "E5941", {"start": v(-498.6, 129.18) * mm, "end": v(-500.77, 129.53) * mm});
            skLineSegment(sketch, "E5942", {"start": v(-500.77, 129.53) * mm, "end": v(-501.52, 129.65) * mm});
            skLineSegment(sketch, "E5943", {"start": v(611.1, -251.04) * mm, "end": v(606.44, -249.8) * mm});
            skLineSegment(sketch, "E5944", {"start": v(606.44, -249.8) * mm, "end": v(592.5, -246) * mm});
            skLineSegment(sketch, "E5945", {"start": v(592.5, -246) * mm, "end": v(573.73, -240.69) * mm});
            skLineSegment(sketch, "E5946", {"start": v(573.73, -240.69) * mm, "end": v(554.91, -235.13) * mm});
            skLineSegment(sketch, "E5947", {"start": v(554.91, -235.13) * mm, "end": v(536.12, -229.37) * mm});
            skLineSegment(sketch, "E5948", {"start": v(536.12, -229.37) * mm, "end": v(517.45, -223.44) * mm});
            skLineSegment(sketch, "E5949", {"start": v(517.45, -223.44) * mm, "end": v(498.98, -217.37) * mm});
            skLineSegment(sketch, "E5950", {"start": v(498.98, -217.37) * mm, "end": v(480.81, -211.2) * mm});
            skLineSegment(sketch, "E5951", {"start": v(480.81, -211.2) * mm, "end": v(463.03, -204.94) * mm});
            skLineSegment(sketch, "E5952", {"start": v(463.03, -204.94) * mm, "end": v(445.72, -198.64) * mm});
            skLineSegment(sketch, "E5953", {"start": v(445.72, -198.64) * mm, "end": v(428.98, -192.34) * mm});
            skLineSegment(sketch, "E5954", {"start": v(428.98, -192.34) * mm, "end": v(412.9, -186.06) * mm});
            skLineSegment(sketch, "E5955", {"start": v(412.9, -186.06) * mm, "end": v(397.56, -179.83) * mm});
            skLineSegment(sketch, "E5956", {"start": v(397.56, -179.83) * mm, "end": v(383.05, -173.7) * mm});
            skLineSegment(sketch, "E5957", {"start": v(383.05, -173.7) * mm, "end": v(369.47, -167.68) * mm});
            skLineSegment(sketch, "E5958", {"start": v(369.47, -167.68) * mm, "end": v(356.9, -161.82) * mm});
            skLineSegment(sketch, "E5959", {"start": v(356.9, -161.82) * mm, "end": v(348.27, -157.6) * mm});
            skLineSegment(sketch, "E5960", {"start": v(348.27, -157.6) * mm, "end": v(345.43, -156.14) * mm});
            skLineSegment(sketch, "E5961", {"start": v(345.43, -156.14) * mm, "end": v(342.52, -154.66) * mm});
            skLineSegment(sketch, "E5962", {"start": v(342.52, -154.66) * mm, "end": v(333.84, -150.13) * mm});
            skLineSegment(sketch, "E5963", {"start": v(333.84, -150.13) * mm, "end": v(320.97, -143.33) * mm});
            skLineSegment(sketch, "E5964", {"start": v(320.97, -143.33) * mm, "end": v(307.04, -135.83) * mm});
            skLineSegment(sketch, "E5965", {"start": v(307.04, -135.83) * mm, "end": v(292.24, -127.75) * mm});
            skLineSegment(sketch, "E5966", {"start": v(292.24, -127.75) * mm, "end": v(276.77, -119.2) * mm});
            skLineSegment(sketch, "E5967", {"start": v(276.77, -119.2) * mm, "end": v(260.83, -110.3) * mm});
            skLineSegment(sketch, "E5968", {"start": v(260.83, -110.3) * mm, "end": v(244.62, -101.14) * mm});
            skLineSegment(sketch, "E5969", {"start": v(244.62, -101.14) * mm, "end": v(228.34, -91.84) * mm});
            skLineSegment(sketch, "E5970", {"start": v(228.34, -91.84) * mm, "end": v(212.2, -82.51) * mm});
            skLineSegment(sketch, "E5971", {"start": v(212.2, -82.51) * mm, "end": v(196.38, -73.26) * mm});
            skLineSegment(sketch, "E5972", {"start": v(196.38, -73.26) * mm, "end": v(181.1, -64.2) * mm});
            skLineSegment(sketch, "E5973", {"start": v(181.1, -64.2) * mm, "end": v(166.54, -55.45) * mm});
            skLineSegment(sketch, "E5974", {"start": v(166.54, -55.45) * mm, "end": v(152.92, -47.1) * mm});
            skLineSegment(sketch, "E5975", {"start": v(152.92, -47.1) * mm, "end": v(140.43, -39.27) * mm});
            skLineSegment(sketch, "E5976", {"start": v(140.43, -39.27) * mm, "end": v(129.27, -32.07) * mm});
            skLineSegment(sketch, "E5977", {"start": v(129.27, -32.07) * mm, "end": v(122.03, -27.26) * mm});
            skLineSegment(sketch, "E5978", {"start": v(122.03, -27.26) * mm, "end": v(119.65, -25.61) * mm});
            skLineSegment(sketch, "E5979", {"start": v(119.65, -25.61) * mm, "end": v(117.27, -23.97) * mm});
            skLineSegment(sketch, "E5980", {"start": v(117.27, -23.97) * mm, "end": v(110.37, -18.7) * mm});
            skLineSegment(sketch, "E5981", {"start": v(110.37, -18.7) * mm, "end": v(100.78, -10.68) * mm});
            skLineSegment(sketch, "E5982", {"start": v(100.78, -10.68) * mm, "end": v(90.91, -1.76) * mm});
            skLineSegment(sketch, "E5983", {"start": v(90.91, -1.76) * mm, "end": v(80.76, 7.85) * mm});
            skLineSegment(sketch, "E5984", {"start": v(80.76, 7.85) * mm, "end": v(70.36, 17.92) * mm});
            skLineSegment(sketch, "E5985", {"start": v(70.36, 17.92) * mm, "end": v(59.7, 28.25) * mm});
            skLineSegment(sketch, "E5986", {"start": v(59.7, 28.25) * mm, "end": v(48.8, 38.6) * mm});
            skLineSegment(sketch, "E5987", {"start": v(48.8, 38.6) * mm, "end": v(37.68, 48.8) * mm});
            skLineSegment(sketch, "E5988", {"start": v(37.68, 48.8) * mm, "end": v(26.35, 58.58) * mm});
            skLineSegment(sketch, "E5989", {"start": v(26.35, 58.58) * mm, "end": v(14.82, 67.77) * mm});
            skLineSegment(sketch, "E5990", {"start": v(14.82, 67.77) * mm, "end": v(3.1, 76.13) * mm});
            skLineSegment(sketch, "E5991", {"start": v(3.1, 76.13) * mm, "end": v(-8.78, 83.45) * mm});
            skLineSegment(sketch, "E5992", {"start": v(-8.78, 83.45) * mm, "end": v(-20.82, 89.52) * mm});
            skLineSegment(sketch, "E5993", {"start": v(-20.82, 89.52) * mm, "end": v(-33.02, 94.12) * mm});
            skLineSegment(sketch, "E5994", {"start": v(-33.02, 94.12) * mm, "end": v(-45.35, 97.04) * mm});
            skLineSegment(sketch, "E5995", {"start": v(-45.35, 97.04) * mm, "end": v(-54.7, 98.06) * mm});
            skLineSegment(sketch, "E5996", {"start": v(-54.7, 98.06) * mm, "end": v(-57.8, 98.06) * mm});
            skLineSegment(sketch, "E5997", {"start": v(-57.8, 98.06) * mm, "end": v(-59.81, 98.06) * mm});
            skLineSegment(sketch, "E5998", {"start": v(-59.81, 98.06) * mm, "end": v(-65.85, 97.97) * mm});
            skLineSegment(sketch, "E5999", {"start": v(-65.85, 97.97) * mm, "end": v(-73.37, 97.7) * mm});
            skLineSegment(sketch, "E6000", {"start": v(-73.37, 97.7) * mm, "end": v(-80.4, 97.26) * mm});
            skLineSegment(sketch, "E6001", {"start": v(-80.4, 97.26) * mm, "end": v(-86.96, 96.66) * mm});
            skLineSegment(sketch, "E6002", {"start": v(-86.96, 96.66) * mm, "end": v(-93.08, 95.92) * mm});
            skLineSegment(sketch, "E6003", {"start": v(-93.08, 95.92) * mm, "end": v(-98.8, 95.05) * mm});
            skLineSegment(sketch, "E6004", {"start": v(-98.8, 95.05) * mm, "end": v(-104.12, 94.06) * mm});
            skLineSegment(sketch, "E6005", {"start": v(-104.12, 94.06) * mm, "end": v(-109.1, 92.96) * mm});
            skLineSegment(sketch, "E6006", {"start": v(-109.1, 92.96) * mm, "end": v(-113.76, 91.76) * mm});
            skLineSegment(sketch, "E6007", {"start": v(-113.76, 91.76) * mm, "end": v(-118.12, 90.48) * mm});
            skLineSegment(sketch, "E6008", {"start": v(-118.12, 90.48) * mm, "end": v(-122.22, 89.13) * mm});
            skLineSegment(sketch, "E6009", {"start": v(-122.22, 89.13) * mm, "end": v(-126.08, 87.72) * mm});
            skLineSegment(sketch, "E6010", {"start": v(-126.08, 87.72) * mm, "end": v(-129.72, 86.26) * mm});
            skLineSegment(sketch, "E6011", {"start": v(-129.72, 86.26) * mm, "end": v(-133.19, 84.76) * mm});
            skLineSegment(sketch, "E6012", {"start": v(-133.19, 84.76) * mm, "end": v(-136.5, 83.24) * mm});
            skLineSegment(sketch, "E6013", {"start": v(-136.5, 83.24) * mm, "end": v(-139.69, 81.7) * mm});
            skLineSegment(sketch, "E6014", {"start": v(-139.69, 81.7) * mm, "end": v(-142.78, 80.17) * mm});
            skLineSegment(sketch, "E6015", {"start": v(-142.78, 80.17) * mm, "end": v(-145.8, 78.65) * mm});
            skLineSegment(sketch, "E6016", {"start": v(-145.8, 78.65) * mm, "end": v(-148.8, 77.15) * mm});
            skLineSegment(sketch, "E6017", {"start": v(-148.8, 77.15) * mm, "end": v(-151.77, 75.69) * mm});
            skLineSegment(sketch, "E6018", {"start": v(-151.77, 75.69) * mm, "end": v(-154.76, 74.27) * mm});
            skLineSegment(sketch, "E6019", {"start": v(-154.76, 74.27) * mm, "end": v(-157.8, 72.91) * mm});
            skLineSegment(sketch, "E6020", {"start": v(-157.8, 72.91) * mm, "end": v(-160.91, 71.62) * mm});
            skLineSegment(sketch, "E6021", {"start": v(-160.91, 71.62) * mm, "end": v(-164.13, 70.42) * mm});
            skLineSegment(sketch, "E6022", {"start": v(-164.13, 70.42) * mm, "end": v(-167.49, 69.3) * mm});
            skLineSegment(sketch, "E6023", {"start": v(-167.49, 69.3) * mm, "end": v(-171, 68.3) * mm});
            skLineSegment(sketch, "E6024", {"start": v(-171, 68.3) * mm, "end": v(-174.7, 67.42) * mm});
            skLineSegment(sketch, "E6025", {"start": v(-174.7, 67.42) * mm, "end": v(-178.62, 66.66) * mm});
            skLineSegment(sketch, "E6026", {"start": v(-178.62, 66.66) * mm, "end": v(-182.78, 66.05) * mm});
            skLineSegment(sketch, "E6027", {"start": v(-182.78, 66.05) * mm, "end": v(-187.22, 65.6) * mm});
            skLineSegment(sketch, "E6028", {"start": v(-187.22, 65.6) * mm, "end": v(-191.96, 65.3) * mm});
            skLineSegment(sketch, "E6029", {"start": v(-191.96, 65.3) * mm, "end": v(-195.76, 65.2) * mm});
            skLineSegment(sketch, "E6030", {"start": v(-195.76, 65.2) * mm, "end": v(-197.03, 65.2) * mm});
            skLineSegment(sketch, "E6031", {"start": v(-197.03, 65.2) * mm, "end": v(-200.64, 65.38) * mm});
            skLineSegment(sketch, "E6032", {"start": v(-200.64, 65.38) * mm, "end": v(-211.45, 66.3) * mm});
            skLineSegment(sketch, "E6033", {"start": v(-211.45, 66.3) * mm, "end": v(-225.09, 68) * mm});
            skLineSegment(sketch, "E6034", {"start": v(-225.09, 68) * mm, "end": v(-238.1, 70.13) * mm});
            skLineSegment(sketch, "E6035", {"start": v(-238.1, 70.13) * mm, "end": v(-250.66, 72.55) * mm});
            skLineSegment(sketch, "E6036", {"start": v(-250.66, 72.55) * mm, "end": v(-262.91, 75.12) * mm});
            skLineSegment(sketch, "E6037", {"start": v(-262.91, 75.12) * mm, "end": v(-275, 77.68) * mm});
            skLineSegment(sketch, "E6038", {"start": v(-275, 77.68) * mm, "end": v(-287.1, 80.08) * mm});
            skLineSegment(sketch, "E6039", {"start": v(-287.1, 80.08) * mm, "end": v(-296.26, 81.7) * mm});
            skLineSegment(sketch, "E6040", {"start": v(-296.26, 81.7) * mm, "end": v(-299.33, 82.17) * mm});
            skLineSegment(sketch, "E6041", {"start": v(-299.33, 82.17) * mm, "end": v(-300.61, 82.37) * mm});
            skLineSegment(sketch, "E6042", {"start": v(-300.61, 82.37) * mm, "end": v(-304.41, 83.25) * mm});
            skLineSegment(sketch, "E6043", {"start": v(-304.41, 83.25) * mm, "end": v(-309.54, 84.8) * mm});
            skLineSegment(sketch, "E6044", {"start": v(-309.54, 84.8) * mm, "end": v(-314.82, 86.66) * mm});
            skLineSegment(sketch, "E6045", {"start": v(-314.82, 86.66) * mm, "end": v(-320.33, 88.67) * mm});
            skLineSegment(sketch, "E6046", {"start": v(-320.33, 88.67) * mm, "end": v(-326.2, 90.66) * mm});
            skLineSegment(sketch, "E6047", {"start": v(-326.2, 90.66) * mm, "end": v(-332.49, 92.48) * mm});
            skLineSegment(sketch, "E6048", {"start": v(-332.49, 92.48) * mm, "end": v(-339.32, 93.95) * mm});
            skLineSegment(sketch, "E6049", {"start": v(-339.32, 93.95) * mm, "end": v(-344.9, 94.75) * mm});
            skLineSegment(sketch, "E6050", {"start": v(-344.9, 94.75) * mm, "end": v(-346.78, 94.9) * mm});
            skLineSegment(sketch, "E6051", {"start": v(-346.78, 94.9) * mm, "end": v(-349.04, 95.1) * mm});
            skLineSegment(sketch, "E6052", {"start": v(-349.04, 95.1) * mm, "end": v(-355.83, 95.37) * mm});
            skLineSegment(sketch, "E6053", {"start": v(-355.83, 95.37) * mm, "end": v(-363.81, 95.3) * mm});
            skLineSegment(sketch, "E6054", {"start": v(-363.81, 95.3) * mm, "end": v(-371.05, 94.87) * mm});
            skLineSegment(sketch, "E6055", {"start": v(-371.05, 94.87) * mm, "end": v(-377.9, 94.32) * mm});
            skLineSegment(sketch, "E6056", {"start": v(-377.9, 94.32) * mm, "end": v(-384.69, 93.83) * mm});
            skLineSegment(sketch, "E6057", {"start": v(-384.69, 93.83) * mm, "end": v(-391.76, 93.63) * mm});
            skLineSegment(sketch, "E6058", {"start": v(-391.76, 93.63) * mm, "end": v(-399.45, 93.92) * mm});
            skLineSegment(sketch, "E6059", {"start": v(-399.45, 93.92) * mm, "end": v(-405.96, 94.58) * mm});
            skLineSegment(sketch, "E6060", {"start": v(-405.96, 94.58) * mm, "end": v(-408.11, 94.9) * mm});
            skLineSegment(sketch, "E6061", {"start": v(-408.11, 94.9) * mm, "end": v(-409.55, 95.12) * mm});
            skLineSegment(sketch, "E6062", {"start": v(-409.55, 95.12) * mm, "end": v(-413.89, 95.78) * mm});
            skLineSegment(sketch, "E6063", {"start": v(-413.89, 95.78) * mm, "end": v(-420.28, 96.77) * mm});
            skLineSegment(sketch, "E6064", {"start": v(-420.28, 96.77) * mm, "end": v(-427.14, 97.83) * mm});
            skLineSegment(sketch, "E6065", {"start": v(-427.14, 97.83) * mm, "end": v(-434.35, 98.96) * mm});
            skLineSegment(sketch, "E6066", {"start": v(-434.35, 98.96) * mm, "end": v(-441.77, 100.13) * mm});
            skLineSegment(sketch, "E6067", {"start": v(-441.77, 100.13) * mm, "end": v(-449.25, 101.3) * mm});
            skLineSegment(sketch, "E6068", {"start": v(-449.25, 101.3) * mm, "end": v(-456.67, 102.48) * mm});
            skLineSegment(sketch, "E6069", {"start": v(-456.67, 102.48) * mm, "end": v(-463.88, 103.62) * mm});
            skLineSegment(sketch, "E6070", {"start": v(-463.88, 103.62) * mm, "end": v(-470.75, 104.72) * mm});
            skLineSegment(sketch, "E6071", {"start": v(-470.75, 104.72) * mm, "end": v(-477.15, 105.74) * mm});
            skLineSegment(sketch, "E6072", {"start": v(-477.15, 105.74) * mm, "end": v(-482.94, 106.66) * mm});
            skLineSegment(sketch, "E6073", {"start": v(-482.94, 106.66) * mm, "end": v(-487.98, 107.47) * mm});
            skLineSegment(sketch, "E6074", {"start": v(-487.98, 107.47) * mm, "end": v(-492.14, 108.14) * mm});
            skLineSegment(sketch, "E6075", {"start": v(-492.14, 108.14) * mm, "end": v(-495.28, 108.64) * mm});
            skLineSegment(sketch, "E6076", {"start": v(-495.28, 108.64) * mm, "end": v(-497.26, 108.96) * mm});
            skLineSegment(sketch, "E6077", {"start": v(-497.26, 108.96) * mm, "end": v(-497.95, 109.06) * mm});
            skLineSegment(sketch, "E6078", {"start": v(611.1, -271.07) * mm, "end": v(606.45, -269.84) * mm});
            skLineSegment(sketch, "E6079", {"start": v(606.45, -269.84) * mm, "end": v(592.5, -266.07) * mm});
            skLineSegment(sketch, "E6080", {"start": v(592.5, -266.07) * mm, "end": v(573.76, -260.87) * mm});
            skLineSegment(sketch, "E6081", {"start": v(573.76, -260.87) * mm, "end": v(554.98, -255.5) * mm});
            skLineSegment(sketch, "E6082", {"start": v(554.98, -255.5) * mm, "end": v(536.23, -249.97) * mm});
            skLineSegment(sketch, "E6083", {"start": v(536.23, -249.97) * mm, "end": v(517.61, -244.31) * mm});
            skLineSegment(sketch, "E6084", {"start": v(517.61, -244.31) * mm, "end": v(499.2, -238.54) * mm});
            skLineSegment(sketch, "E6085", {"start": v(499.2, -238.54) * mm, "end": v(481.1, -232.7) * mm});
            skLineSegment(sketch, "E6086", {"start": v(481.1, -232.7) * mm, "end": v(463.38, -226.78) * mm});
            skLineSegment(sketch, "E6087", {"start": v(463.38, -226.78) * mm, "end": v(446.14, -220.81) * mm});
            skLineSegment(sketch, "E6088", {"start": v(446.14, -220.81) * mm, "end": v(429.47, -214.83) * mm});
            skLineSegment(sketch, "E6089", {"start": v(429.47, -214.83) * mm, "end": v(413.44, -208.85) * mm});
            skLineSegment(sketch, "E6090", {"start": v(413.44, -208.85) * mm, "end": v(398.15, -202.9) * mm});
            skLineSegment(sketch, "E6091", {"start": v(398.15, -202.9) * mm, "end": v(383.7, -197) * mm});
            skLineSegment(sketch, "E6092", {"start": v(383.7, -197) * mm, "end": v(370.14, -191.16) * mm});
            skLineSegment(sketch, "E6093", {"start": v(370.14, -191.16) * mm, "end": v(357.6, -185.41) * mm});
            skLineSegment(sketch, "E6094", {"start": v(357.6, -185.41) * mm, "end": v(348.97, -181.23) * mm});
            skLineSegment(sketch, "E6095", {"start": v(348.97, -181.23) * mm, "end": v(346.13, -179.78) * mm});
            skLineSegment(sketch, "E6096", {"start": v(346.13, -179.78) * mm, "end": v(344.72, -179.06) * mm});
            skLineSegment(sketch, "E6097", {"start": v(344.72, -179.06) * mm, "end": v(340.49, -176.88) * mm});
            skLineSegment(sketch, "E6098", {"start": v(340.49, -176.88) * mm, "end": v(334.46, -173.75) * mm});
            skLineSegment(sketch, "E6099", {"start": v(334.46, -173.75) * mm, "end": v(328.08, -170.42) * mm});
            skLineSegment(sketch, "E6100", {"start": v(328.08, -170.42) * mm, "end": v(321.37, -166.9) * mm});
            skLineSegment(sketch, "E6101", {"start": v(321.37, -166.9) * mm, "end": v(314.36, -163.2) * mm});
            skLineSegment(sketch, "E6102", {"start": v(314.36, -163.2) * mm, "end": v(307.08, -159.33) * mm});
            skLineSegment(sketch, "E6103", {"start": v(307.08, -159.33) * mm, "end": v(299.55, -155.32) * mm});
            skLineSegment(sketch, "E6104", {"start": v(299.55, -155.32) * mm, "end": v(291.8, -151.19) * mm});
            skLineSegment(sketch, "E6105", {"start": v(291.8, -151.19) * mm, "end": v(283.87, -146.93) * mm});
            skLineSegment(sketch, "E6106", {"start": v(283.87, -146.93) * mm, "end": v(275.76, -142.57) * mm});
            skLineSegment(sketch, "E6107", {"start": v(275.76, -142.57) * mm, "end": v(267.52, -138.13) * mm});
            skLineSegment(sketch, "E6108", {"start": v(267.52, -138.13) * mm, "end": v(259.17, -133.61) * mm});
            skLineSegment(sketch, "E6109", {"start": v(259.17, -133.61) * mm, "end": v(250.72, -129.05) * mm});
            skLineSegment(sketch, "E6110", {"start": v(250.72, -129.05) * mm, "end": v(242.23, -124.44) * mm});
            skLineSegment(sketch, "E6111", {"start": v(242.23, -124.44) * mm, "end": v(233.7, -119.8) * mm});
            skLineSegment(sketch, "E6112", {"start": v(233.7, -119.8) * mm, "end": v(225.18, -115.16) * mm});
            skLineSegment(sketch, "E6113", {"start": v(225.18, -115.16) * mm, "end": v(216.68, -110.53) * mm});
            skLineSegment(sketch, "E6114", {"start": v(216.68, -110.53) * mm, "end": v(208.22, -105.91) * mm});
            skLineSegment(sketch, "E6115", {"start": v(208.22, -105.91) * mm, "end": v(199.85, -101.33) * mm});
            skLineSegment(sketch, "E6116", {"start": v(199.85, -101.33) * mm, "end": v(191.59, -96.8) * mm});
            skLineSegment(sketch, "E6117", {"start": v(191.59, -96.8) * mm, "end": v(183.45, -92.35) * mm});
            skLineSegment(sketch, "E6118", {"start": v(183.45, -92.35) * mm, "end": v(175.47, -87.97) * mm});
            skLineSegment(sketch, "E6119", {"start": v(175.47, -87.97) * mm, "end": v(167.69, -83.7) * mm});
            skLineSegment(sketch, "E6120", {"start": v(167.69, -83.7) * mm, "end": v(160.12, -79.53) * mm});
            skLineSegment(sketch, "E6121", {"start": v(160.12, -79.53) * mm, "end": v(152.78, -75.48) * mm});
            skLineSegment(sketch, "E6122", {"start": v(152.78, -75.48) * mm, "end": v(145.72, -71.59) * mm});
            skLineSegment(sketch, "E6123", {"start": v(145.72, -71.59) * mm, "end": v(138.95, -67.85) * mm});
            skLineSegment(sketch, "E6124", {"start": v(138.95, -67.85) * mm, "end": v(132.5, -64.29) * mm});
            skLineSegment(sketch, "E6125", {"start": v(132.5, -64.29) * mm, "end": v(126.4, -60.9) * mm});
            skLineSegment(sketch, "E6126", {"start": v(126.4, -60.9) * mm, "end": v(120.68, -57.74) * mm});
            skLineSegment(sketch, "E6127", {"start": v(120.68, -57.74) * mm, "end": v(115.36, -54.79) * mm});
            skLineSegment(sketch, "E6128", {"start": v(115.36, -54.79) * mm, "end": v(111.7, -52.75) * mm});
            skLineSegment(sketch, "E6129", {"start": v(111.7, -52.75) * mm, "end": v(110.48, -52.07) * mm});
            skLineSegment(sketch, "E6130", {"start": v(110.48, -52.07) * mm, "end": v(107.84, -50.6) * mm});
            skLineSegment(sketch, "E6131", {"start": v(107.84, -50.6) * mm, "end": v(100.23, -45.68) * mm});
            skLineSegment(sketch, "E6132", {"start": v(100.23, -45.68) * mm, "end": v(89.72, -37.92) * mm});
            skLineSegment(sketch, "E6133", {"start": v(89.72, -37.92) * mm, "end": v(79.02, -29.04) * mm});
            skLineSegment(sketch, "E6134", {"start": v(79.02, -29.04) * mm, "end": v(68.14, -19.28) * mm});
            skLineSegment(sketch, "E6135", {"start": v(68.14, -19.28) * mm, "end": v(57.16, -8.88) * mm});
            skLineSegment(sketch, "E6136", {"start": v(57.16, -8.88) * mm, "end": v(46.11, 1.92) * mm});
            skLineSegment(sketch, "E6137", {"start": v(46.11, 1.92) * mm, "end": v(35.04, 12.87) * mm});
            skLineSegment(sketch, "E6138", {"start": v(35.04, 12.87) * mm, "end": v(24, 23.73) * mm});
            skLineSegment(sketch, "E6139", {"start": v(24, 23.73) * mm, "end": v(13.02, 34.24) * mm});
            skLineSegment(sketch, "E6140", {"start": v(13.02, 34.24) * mm, "end": v(2.17, 44.19) * mm});
            skLineSegment(sketch, "E6141", {"start": v(2.17, 44.19) * mm, "end": v(-8.51, 53.3) * mm});
            skLineSegment(sketch, "E6142", {"start": v(-8.51, 53.3) * mm, "end": v(-18.98, 61.36) * mm});
            skLineSegment(sketch, "E6143", {"start": v(-18.98, 61.36) * mm, "end": v(-29.2, 68.1) * mm});
            skLineSegment(sketch, "E6144", {"start": v(-29.2, 68.1) * mm, "end": v(-39.1, 73.29) * mm});
            skLineSegment(sketch, "E6145", {"start": v(-39.1, 73.29) * mm, "end": v(-48.65, 76.68) * mm});
            skLineSegment(sketch, "E6146", {"start": v(-48.65, 76.68) * mm, "end": v(-55.5, 77.97) * mm});
            skLineSegment(sketch, "E6147", {"start": v(-55.5, 77.97) * mm, "end": v(-57.8, 78.03) * mm});
            skLineSegment(sketch, "E6148", {"start": v(-57.8, 78.03) * mm, "end": v(-60.97, 78.12) * mm});
            skLineSegment(sketch, "E6149", {"start": v(-60.97, 78.12) * mm, "end": v(-70.5, 78) * mm});
            skLineSegment(sketch, "E6150", {"start": v(-70.5, 78) * mm, "end": v(-81.95, 77.2) * mm});
            skLineSegment(sketch, "E6151", {"start": v(-81.95, 77.2) * mm, "end": v(-92.31, 75.76) * mm});
            skLineSegment(sketch, "E6152", {"start": v(-92.31, 75.76) * mm, "end": v(-101.75, 73.77) * mm});
            skLineSegment(sketch, "E6153", {"start": v(-101.75, 73.77) * mm, "end": v(-110.4, 71.34) * mm});
            skLineSegment(sketch, "E6154", {"start": v(-110.4, 71.34) * mm, "end": v(-118.41, 68.56) * mm});
            skLineSegment(sketch, "E6155", {"start": v(-118.41, 68.56) * mm, "end": v(-125.95, 65.56) * mm});
            skLineSegment(sketch, "E6156", {"start": v(-125.95, 65.56) * mm, "end": v(-133.15, 62.43) * mm});
            skLineSegment(sketch, "E6157", {"start": v(-133.15, 62.43) * mm, "end": v(-140.17, 59.26) * mm});
            skLineSegment(sketch, "E6158", {"start": v(-140.17, 59.26) * mm, "end": v(-147.17, 56.18) * mm});
            skLineSegment(sketch, "E6159", {"start": v(-147.17, 56.18) * mm, "end": v(-154.29, 53.28) * mm});
            skLineSegment(sketch, "E6160", {"start": v(-154.29, 53.28) * mm, "end": v(-161.68, 50.67) * mm});
            skLineSegment(sketch, "E6161", {"start": v(-161.68, 50.67) * mm, "end": v(-169.5, 48.45) * mm});
            skLineSegment(sketch, "E6162", {"start": v(-169.5, 48.45) * mm, "end": v(-177.9, 46.72) * mm});
            skLineSegment(sketch, "E6163", {"start": v(-177.9, 46.72) * mm, "end": v(-187.02, 45.59) * mm});
            skLineSegment(sketch, "E6164", {"start": v(-187.02, 45.59) * mm, "end": v(-194.53, 45.17) * mm});
            skLineSegment(sketch, "E6165", {"start": v(-194.53, 45.17) * mm, "end": v(-197.03, 45.16) * mm});
            skLineSegment(sketch, "E6166", {"start": v(-197.03, 45.16) * mm, "end": v(-200.65, 45.75) * mm});
            skLineSegment(sketch, "E6167", {"start": v(-200.65, 45.75) * mm, "end": v(-211.5, 47.6) * mm});
            skLineSegment(sketch, "E6168", {"start": v(-211.5, 47.6) * mm, "end": v(-224.77, 50) * mm});
            skLineSegment(sketch, "E6169", {"start": v(-224.77, 50) * mm, "end": v(-237.1, 52.43) * mm});
            skLineSegment(sketch, "E6170", {"start": v(-237.1, 52.43) * mm, "end": v(-248.8, 54.93) * mm});
            skLineSegment(sketch, "E6171", {"start": v(-248.8, 54.93) * mm, "end": v(-260.15, 57.55) * mm});
            skLineSegment(sketch, "E6172", {"start": v(-260.15, 57.55) * mm, "end": v(-271.41, 60.34) * mm});
            skLineSegment(sketch, "E6173", {"start": v(-271.41, 60.34) * mm, "end": v(-282.9, 63.34) * mm});
            skLineSegment(sketch, "E6174", {"start": v(-282.9, 63.34) * mm, "end": v(-291.88, 65.78) * mm});
            skLineSegment(sketch, "E6175", {"start": v(-291.88, 65.78) * mm, "end": v(-294.87, 66.6) * mm});
            skLineSegment(sketch, "E6176", {"start": v(-294.87, 66.6) * mm, "end": v(-297.53, 67.35) * mm});
            skLineSegment(sketch, "E6177", {"start": v(-297.53, 67.35) * mm, "end": v(-305.63, 69.2) * mm});
            skLineSegment(sketch, "E6178", {"start": v(-305.63, 69.2) * mm, "end": v(-317.97, 71.47) * mm});
            skLineSegment(sketch, "E6179", {"start": v(-317.97, 71.47) * mm, "end": v(-331.74, 73.37) * mm});
            skLineSegment(sketch, "E6180", {"start": v(-331.74, 73.37) * mm, "end": v(-343.01, 74.56) * mm});
            skLineSegment(sketch, "E6181", {"start": v(-343.01, 74.56) * mm, "end": v(-346.78, 74.87) * mm});
            skLineSegment(sketch, "E6182", {"start": v(-346.78, 74.87) * mm, "end": v(-349.04, 75.06) * mm});
            skLineSegment(sketch, "E6183", {"start": v(-349.04, 75.06) * mm, "end": v(-355.83, 75.34) * mm});
            skLineSegment(sketch, "E6184", {"start": v(-355.83, 75.34) * mm, "end": v(-363.81, 75.25) * mm});
            skLineSegment(sketch, "E6185", {"start": v(-363.81, 75.25) * mm, "end": v(-371.05, 74.84) * mm});
            skLineSegment(sketch, "E6186", {"start": v(-371.05, 74.84) * mm, "end": v(-377.9, 74.28) * mm});
            skLineSegment(sketch, "E6187", {"start": v(-377.9, 74.28) * mm, "end": v(-384.69, 73.8) * mm});
            skLineSegment(sketch, "E6188", {"start": v(-384.69, 73.8) * mm, "end": v(-391.76, 73.6) * mm});
            skLineSegment(sketch, "E6189", {"start": v(-391.76, 73.6) * mm, "end": v(-399.45, 73.9) * mm});
            skLineSegment(sketch, "E6190", {"start": v(-399.45, 73.9) * mm, "end": v(-405.96, 74.55) * mm});
            skLineSegment(sketch, "E6191", {"start": v(-405.96, 74.55) * mm, "end": v(-408.11, 74.87) * mm});
            skLineSegment(sketch, "E6192", {"start": v(-408.11, 74.87) * mm, "end": v(-409.54, 75.09) * mm});
            skLineSegment(sketch, "E6193", {"start": v(-409.54, 75.09) * mm, "end": v(-413.84, 75.75) * mm});
            skLineSegment(sketch, "E6194", {"start": v(-413.84, 75.75) * mm, "end": v(-420.1, 76.7) * mm});
            skLineSegment(sketch, "E6195", {"start": v(-420.1, 76.7) * mm, "end": v(-426.76, 77.74) * mm});
            skLineSegment(sketch, "E6196", {"start": v(-426.76, 77.74) * mm, "end": v(-433.7, 78.83) * mm});
            skLineSegment(sketch, "E6197", {"start": v(-433.7, 78.83) * mm, "end": v(-440.8, 79.94) * mm});
            skLineSegment(sketch, "E6198", {"start": v(-440.8, 79.94) * mm, "end": v(-447.93, 81.06) * mm});
            skLineSegment(sketch, "E6199", {"start": v(-447.93, 81.06) * mm, "end": v(-454.97, 82.17) * mm});
            skLineSegment(sketch, "E6200", {"start": v(-454.97, 82.17) * mm, "end": v(-461.8, 83.26) * mm});
            skLineSegment(sketch, "E6201", {"start": v(-461.8, 83.26) * mm, "end": v(-468.28, 84.29) * mm});
            skLineSegment(sketch, "E6202", {"start": v(-468.28, 84.29) * mm, "end": v(-474.3, 85.25) * mm});
            skLineSegment(sketch, "E6203", {"start": v(-474.3, 85.25) * mm, "end": v(-479.73, 86.11) * mm});
            skLineSegment(sketch, "E6204", {"start": v(-479.73, 86.11) * mm, "end": v(-484.46, 86.87) * mm});
            skLineSegment(sketch, "E6205", {"start": v(-484.46, 86.87) * mm, "end": v(-488.35, 87.5) * mm});
            skLineSegment(sketch, "E6206", {"start": v(-488.35, 87.5) * mm, "end": v(-491.28, 87.97) * mm});
            skLineSegment(sketch, "E6207", {"start": v(-491.28, 87.97) * mm, "end": v(-493.13, 88.26) * mm});
            skLineSegment(sketch, "E6208", {"start": v(-493.13, 88.26) * mm, "end": v(-493.77, 88.36) * mm});
            skLineSegment(sketch, "E6209", {"start": v(610.84, -211.08) * mm, "end": v(606.19, -209.84) * mm});
            skLineSegment(sketch, "E6210", {"start": v(606.19, -209.84) * mm, "end": v(592.27, -205.98) * mm});
            skLineSegment(sketch, "E6211", {"start": v(592.27, -205.98) * mm, "end": v(573.65, -200.5) * mm});
            skLineSegment(sketch, "E6212", {"start": v(573.65, -200.5) * mm, "end": v(555.03, -194.7) * mm});
            skLineSegment(sketch, "E6213", {"start": v(555.03, -194.7) * mm, "end": v(536.51, -188.62) * mm});
            skLineSegment(sketch, "E6214", {"start": v(536.51, -188.62) * mm, "end": v(518.17, -182.31) * mm});
            skLineSegment(sketch, "E6215", {"start": v(518.17, -182.31) * mm, "end": v(500.08, -175.84) * mm});
            skLineSegment(sketch, "E6216", {"start": v(500.08, -175.84) * mm, "end": v(482.32, -169.24) * mm});
            skLineSegment(sketch, "E6217", {"start": v(482.32, -169.24) * mm, "end": v(464.98, -162.57) * mm});
            skLineSegment(sketch, "E6218", {"start": v(464.98, -162.57) * mm, "end": v(448.13, -155.89) * mm});
            skLineSegment(sketch, "E6219", {"start": v(448.13, -155.89) * mm, "end": v(431.85, -149.23) * mm});
            skLineSegment(sketch, "E6220", {"start": v(431.85, -149.23) * mm, "end": v(416.23, -142.64) * mm});
            skLineSegment(sketch, "E6221", {"start": v(416.23, -142.64) * mm, "end": v(401.34, -136.2) * mm});
            skLineSegment(sketch, "E6222", {"start": v(401.34, -136.2) * mm, "end": v(387.27, -129.94) * mm});
            skLineSegment(sketch, "E6223", {"start": v(387.27, -129.94) * mm, "end": v(374.08, -123.9) * mm});
            skLineSegment(sketch, "E6224", {"start": v(374.08, -123.9) * mm, "end": v(361.88, -118.16) * mm});
            skLineSegment(sketch, "E6225", {"start": v(361.88, -118.16) * mm, "end": v(353.5, -114.12) * mm});
            skLineSegment(sketch, "E6226", {"start": v(353.5, -114.12) * mm, "end": v(350.72, -112.75) * mm});
            skLineSegment(sketch, "E6227", {"start": v(350.72, -112.75) * mm, "end": v(349.3, -112.05) * mm});
            skLineSegment(sketch, "E6228", {"start": v(349.3, -112.05) * mm, "end": v(345.1, -109.92) * mm});
            skLineSegment(sketch, "E6229", {"start": v(345.1, -109.92) * mm, "end": v(339.14, -106.8) * mm});
            skLineSegment(sketch, "E6230", {"start": v(339.14, -106.8) * mm, "end": v(332.88, -103.43) * mm});
            skLineSegment(sketch, "E6231", {"start": v(332.88, -103.43) * mm, "end": v(326.34, -99.8) * mm});
            skLineSegment(sketch, "E6232", {"start": v(326.34, -99.8) * mm, "end": v(319.54, -95.96) * mm});
            skLineSegment(sketch, "E6233", {"start": v(319.54, -95.96) * mm, "end": v(312.5, -91.9) * mm});
            skLineSegment(sketch, "E6234", {"start": v(312.5, -91.9) * mm, "end": v(305.26, -87.65) * mm});
            skLineSegment(sketch, "E6235", {"start": v(305.26, -87.65) * mm, "end": v(297.83, -83.22) * mm});
            skLineSegment(sketch, "E6236", {"start": v(297.83, -83.22) * mm, "end": v(290.24, -78.63) * mm});
            skLineSegment(sketch, "E6237", {"start": v(290.24, -78.63) * mm, "end": v(282.51, -73.91) * mm});
            skLineSegment(sketch, "E6238", {"start": v(282.51, -73.91) * mm, "end": v(274.68, -69.07) * mm});
            skLineSegment(sketch, "E6239", {"start": v(274.68, -69.07) * mm, "end": v(266.75, -64.12) * mm});
            skLineSegment(sketch, "E6240", {"start": v(266.75, -64.12) * mm, "end": v(258.77, -59.08) * mm});
            skLineSegment(sketch, "E6241", {"start": v(258.77, -59.08) * mm, "end": v(250.74, -53.98) * mm});
            skLineSegment(sketch, "E6242", {"start": v(250.74, -53.98) * mm, "end": v(242.7, -48.83) * mm});
            skLineSegment(sketch, "E6243", {"start": v(242.7, -48.83) * mm, "end": v(234.68, -43.64) * mm});
            skLineSegment(sketch, "E6244", {"start": v(234.68, -43.64) * mm, "end": v(226.7, -38.44) * mm});
            skLineSegment(sketch, "E6245", {"start": v(226.7, -38.44) * mm, "end": v(218.76, -33.24) * mm});
            skLineSegment(sketch, "E6246", {"start": v(218.76, -33.24) * mm, "end": v(210.92, -28.06) * mm});
            skLineSegment(sketch, "E6247", {"start": v(210.92, -28.06) * mm, "end": v(203.19, -22.93) * mm});
            skLineSegment(sketch, "E6248", {"start": v(203.19, -22.93) * mm, "end": v(195.59, -17.84) * mm});
            skLineSegment(sketch, "E6249", {"start": v(195.59, -17.84) * mm, "end": v(188.14, -12.83) * mm});
            skLineSegment(sketch, "E6250", {"start": v(188.14, -12.83) * mm, "end": v(180.88, -7.91) * mm});
            skLineSegment(sketch, "E6251", {"start": v(180.88, -7.91) * mm, "end": v(173.83, -3.1) * mm});
            skLineSegment(sketch, "E6252", {"start": v(173.83, -3.1) * mm, "end": v(167.01, 1.57) * mm});
            skLineSegment(sketch, "E6253", {"start": v(167.01, 1.57) * mm, "end": v(160.45, 6.11) * mm});
            skLineSegment(sketch, "E6254", {"start": v(160.45, 6.11) * mm, "end": v(154.17, 10.48) * mm});
            skLineSegment(sketch, "E6255", {"start": v(154.17, 10.48) * mm, "end": v(148.2, 14.68) * mm});
            skLineSegment(sketch, "E6256", {"start": v(148.2, 14.68) * mm, "end": v(142.54, 18.67) * mm});
            skLineSegment(sketch, "E6257", {"start": v(142.54, 18.67) * mm, "end": v(137.25, 22.45) * mm});
            skLineSegment(sketch, "E6258", {"start": v(137.25, 22.45) * mm, "end": v(132.34, 25.99) * mm});
            skLineSegment(sketch, "E6259", {"start": v(132.34, 25.99) * mm, "end": v(128.95, 28.46) * mm});
            skLineSegment(sketch, "E6260", {"start": v(128.95, 28.46) * mm, "end": v(127.83, 29.28) * mm});
            skLineSegment(sketch, "E6261", {"start": v(127.83, 29.28) * mm, "end": v(125.6, 30.92) * mm});
            skLineSegment(sketch, "E6262", {"start": v(125.6, 30.92) * mm, "end": v(119.02, 36.03) * mm});
            skLineSegment(sketch, "E6263", {"start": v(119.02, 36.03) * mm, "end": v(109.82, 43.5) * mm});
            skLineSegment(sketch, "E6264", {"start": v(109.82, 43.5) * mm, "end": v(100.23, 51.56) * mm});
            skLineSegment(sketch, "E6265", {"start": v(100.23, 51.56) * mm, "end": v(90.29, 60.03) * mm});
            skLineSegment(sketch, "E6266", {"start": v(90.29, 60.03) * mm, "end": v(80.02, 68.75) * mm});
            skLineSegment(sketch, "E6267", {"start": v(80.02, 68.75) * mm, "end": v(69.43, 77.56) * mm});
            skLineSegment(sketch, "E6268", {"start": v(69.43, 77.56) * mm, "end": v(58.56, 86.3) * mm});
            skLineSegment(sketch, "E6269", {"start": v(58.56, 86.3) * mm, "end": v(47.42, 94.8) * mm});
            skLineSegment(sketch, "E6270", {"start": v(47.42, 94.8) * mm, "end": v(36.03, 102.92) * mm});
            skLineSegment(sketch, "E6271", {"start": v(36.03, 102.92) * mm, "end": v(24.42, 110.47) * mm});
            skLineSegment(sketch, "E6272", {"start": v(24.42, 110.47) * mm, "end": v(12.62, 117.3) * mm});
            skLineSegment(sketch, "E6273", {"start": v(12.62, 117.3) * mm, "end": v(0.63, 123.26) * mm});
            skLineSegment(sketch, "E6274", {"start": v(0.63, 123.26) * mm, "end": v(-11.5, 128.17) * mm});
            skLineSegment(sketch, "E6275", {"start": v(-11.5, 128.17) * mm, "end": v(-23.78, 131.88) * mm});
            skLineSegment(sketch, "E6276", {"start": v(-23.78, 131.88) * mm, "end": v(-36.16, 134.23) * mm});
            skLineSegment(sketch, "E6277", {"start": v(-36.16, 134.23) * mm, "end": v(-45.52, 135.04) * mm});
            skLineSegment(sketch, "E6278", {"start": v(-45.52, 135.04) * mm, "end": v(-48.63, 135.04) * mm});
            skLineSegment(sketch, "E6279", {"start": v(-48.63, 135.04) * mm, "end": v(-52.58, 135.04) * mm});
            skLineSegment(sketch, "E6280", {"start": v(-52.58, 135.04) * mm, "end": v(-64.42, 134.67) * mm});
            skLineSegment(sketch, "E6281", {"start": v(-64.42, 134.67) * mm, "end": v(-78.6, 133.63) * mm});
            skLineSegment(sketch, "E6282", {"start": v(-78.6, 133.63) * mm, "end": v(-91.32, 132) * mm});
            skLineSegment(sketch, "E6283", {"start": v(-91.32, 132) * mm, "end": v(-102.74, 129.9) * mm});
            skLineSegment(sketch, "E6284", {"start": v(-102.74, 129.9) * mm, "end": v(-113, 127.41) * mm});
            skLineSegment(sketch, "E6285", {"start": v(-113, 127.41) * mm, "end": v(-122.27, 124.64) * mm});
            skLineSegment(sketch, "E6286", {"start": v(-122.27, 124.64) * mm, "end": v(-130.68, 121.66) * mm});
            skLineSegment(sketch, "E6287", {"start": v(-130.68, 121.66) * mm, "end": v(-138.39, 118.59) * mm});
            skLineSegment(sketch, "E6288", {"start": v(-138.39, 118.59) * mm, "end": v(-145.53, 115.52) * mm});
            skLineSegment(sketch, "E6289", {"start": v(-145.53, 115.52) * mm, "end": v(-152.27, 112.55) * mm});
            skLineSegment(sketch, "E6290", {"start": v(-152.27, 112.55) * mm, "end": v(-158.76, 109.77) * mm});
            skLineSegment(sketch, "E6291", {"start": v(-158.76, 109.77) * mm, "end": v(-165.14, 107.28) * mm});
            skLineSegment(sketch, "E6292", {"start": v(-165.14, 107.28) * mm, "end": v(-171.55, 105.18) * mm});
            skLineSegment(sketch, "E6293", {"start": v(-171.55, 105.18) * mm, "end": v(-178.17, 103.56) * mm});
            skLineSegment(sketch, "E6294", {"start": v(-178.17, 103.56) * mm, "end": v(-185.12, 102.51) * mm});
            skLineSegment(sketch, "E6295", {"start": v(-185.12, 102.51) * mm, "end": v(-190.7, 102.14) * mm});
            skLineSegment(sketch, "E6296", {"start": v(-190.7, 102.14) * mm, "end": v(-192.56, 102.14) * mm});
            skLineSegment(sketch, "E6297", {"start": v(-192.56, 102.14) * mm, "end": v(-196.17, 102.32) * mm});
            skLineSegment(sketch, "E6298", {"start": v(-196.17, 102.32) * mm, "end": v(-206.98, 103.25) * mm});
            skLineSegment(sketch, "E6299", {"start": v(-206.98, 103.25) * mm, "end": v(-220.62, 104.94) * mm});
            skLineSegment(sketch, "E6300", {"start": v(-220.62, 104.94) * mm, "end": v(-233.64, 107.07) * mm});
            skLineSegment(sketch, "E6301", {"start": v(-233.64, 107.07) * mm, "end": v(-246.2, 109.5) * mm});
            skLineSegment(sketch, "E6302", {"start": v(-246.2, 109.5) * mm, "end": v(-258.45, 112.07) * mm});
            skLineSegment(sketch, "E6303", {"start": v(-258.45, 112.07) * mm, "end": v(-270.53, 114.62) * mm});
            skLineSegment(sketch, "E6304", {"start": v(-270.53, 114.62) * mm, "end": v(-282.62, 117.03) * mm});
            skLineSegment(sketch, "E6305", {"start": v(-282.62, 117.03) * mm, "end": v(-291.8, 118.65) * mm});
            skLineSegment(sketch, "E6306", {"start": v(-291.8, 118.65) * mm, "end": v(-294.87, 119.12) * mm});
            skLineSegment(sketch, "E6307", {"start": v(-294.87, 119.12) * mm, "end": v(-296.15, 119.32) * mm});
            skLineSegment(sketch, "E6308", {"start": v(-296.15, 119.32) * mm, "end": v(-299.95, 120.2) * mm});
            skLineSegment(sketch, "E6309", {"start": v(-299.95, 120.2) * mm, "end": v(-305.08, 121.74) * mm});
            skLineSegment(sketch, "E6310", {"start": v(-305.08, 121.74) * mm, "end": v(-310.35, 123.6) * mm});
            skLineSegment(sketch, "E6311", {"start": v(-310.35, 123.6) * mm, "end": v(-315.87, 125.62) * mm});
            skLineSegment(sketch, "E6312", {"start": v(-315.87, 125.62) * mm, "end": v(-321.73, 127.61) * mm});
            skLineSegment(sketch, "E6313", {"start": v(-321.73, 127.61) * mm, "end": v(-328.02, 129.43) * mm});
            skLineSegment(sketch, "E6314", {"start": v(-328.02, 129.43) * mm, "end": v(-334.85, 130.9) * mm});
            skLineSegment(sketch, "E6315", {"start": v(-334.85, 130.9) * mm, "end": v(-340.44, 131.7) * mm});
            skLineSegment(sketch, "E6316", {"start": v(-340.44, 131.7) * mm, "end": v(-342.31, 131.85) * mm});
            skLineSegment(sketch, "E6317", {"start": v(-342.31, 131.85) * mm, "end": v(-344.57, 132.04) * mm});
            skLineSegment(sketch, "E6318", {"start": v(-344.57, 132.04) * mm, "end": v(-351.37, 132.32) * mm});
            skLineSegment(sketch, "E6319", {"start": v(-351.37, 132.32) * mm, "end": v(-359.34, 132.24) * mm});
            skLineSegment(sketch, "E6320", {"start": v(-359.34, 132.24) * mm, "end": v(-366.59, 131.82) * mm});
            skLineSegment(sketch, "E6321", {"start": v(-366.59, 131.82) * mm, "end": v(-373.43, 131.26) * mm});
            skLineSegment(sketch, "E6322", {"start": v(-373.43, 131.26) * mm, "end": v(-380.22, 130.78) * mm});
            skLineSegment(sketch, "E6323", {"start": v(-380.22, 130.78) * mm, "end": v(-387.3, 130.59) * mm});
            skLineSegment(sketch, "E6324", {"start": v(-387.3, 130.59) * mm, "end": v(-394.99, 130.87) * mm});
            skLineSegment(sketch, "E6325", {"start": v(-394.99, 130.87) * mm, "end": v(-401.5, 131.53) * mm});
            skLineSegment(sketch, "E6326", {"start": v(-401.5, 131.53) * mm, "end": v(-403.64, 131.85) * mm});
            skLineSegment(sketch, "E6327", {"start": v(-403.64, 131.85) * mm, "end": v(-405.12, 132.08) * mm});
            skLineSegment(sketch, "E6328", {"start": v(-405.12, 132.08) * mm, "end": v(-409.55, 132.76) * mm});
            skLineSegment(sketch, "E6329", {"start": v(-409.55, 132.76) * mm, "end": v(-416.31, 133.8) * mm});
            skLineSegment(sketch, "E6330", {"start": v(-416.31, 133.8) * mm, "end": v(-423.76, 134.96) * mm});
            skLineSegment(sketch, "E6331", {"start": v(-423.76, 134.96) * mm, "end": v(-431.72, 136.2) * mm});
            skLineSegment(sketch, "E6332", {"start": v(-431.72, 136.2) * mm, "end": v(-440.02, 137.51) * mm});
            skLineSegment(sketch, "E6333", {"start": v(-440.02, 137.51) * mm, "end": v(-448.5, 138.85) * mm});
            skLineSegment(sketch, "E6334", {"start": v(-448.5, 138.85) * mm, "end": v(-456.97, 140.19) * mm});
            skLineSegment(sketch, "E6335", {"start": v(-456.97, 140.19) * mm, "end": v(-465.28, 141.51) * mm});
            skLineSegment(sketch, "E6336", {"start": v(-465.28, 141.51) * mm, "end": v(-473.25, 142.78) * mm});
            skLineSegment(sketch, "E6337", {"start": v(-473.25, 142.78) * mm, "end": v(-480.7, 143.97) * mm});
            skLineSegment(sketch, "E6338", {"start": v(-480.7, 143.97) * mm, "end": v(-487.49, 145.05) * mm});
            skLineSegment(sketch, "E6339", {"start": v(-487.49, 145.05) * mm, "end": v(-493.42, 146) * mm});
            skLineSegment(sketch, "E6340", {"start": v(-493.42, 146) * mm, "end": v(-498.32, 146.79) * mm});
            skLineSegment(sketch, "E6341", {"start": v(-498.32, 146.79) * mm, "end": v(-502.04, 147.38) * mm});
            skLineSegment(sketch, "E6342", {"start": v(-502.04, 147.38) * mm, "end": v(-504.4, 147.76) * mm});
            skLineSegment(sketch, "E6343", {"start": v(-504.4, 147.76) * mm, "end": v(-505.22, 147.9) * mm});
            skLineSegment(sketch, "E6344", {"start": v(608.7, -192.89) * mm, "end": v(604.06, -191.66) * mm});
            skLineSegment(sketch, "E6345", {"start": v(604.06, -191.66) * mm, "end": v(590.2, -187.79) * mm});
            skLineSegment(sketch, "E6346", {"start": v(590.2, -187.79) * mm, "end": v(571.72, -182.32) * mm});
            skLineSegment(sketch, "E6347", {"start": v(571.72, -182.32) * mm, "end": v(553.37, -176.54) * mm});
            skLineSegment(sketch, "E6348", {"start": v(553.37, -176.54) * mm, "end": v(535.25, -170.5) * mm});
            skLineSegment(sketch, "E6349", {"start": v(535.25, -170.5) * mm, "end": v(517.42, -164.27) * mm});
            skLineSegment(sketch, "E6350", {"start": v(517.42, -164.27) * mm, "end": v(500, -157.9) * mm});
            skLineSegment(sketch, "E6351", {"start": v(500, -157.9) * mm, "end": v(483.06, -151.44) * mm});
            skLineSegment(sketch, "E6352", {"start": v(483.06, -151.44) * mm, "end": v(466.69, -144.95) * mm});
            skLineSegment(sketch, "E6353", {"start": v(466.69, -144.95) * mm, "end": v(450.98, -138.5) * mm});
            skLineSegment(sketch, "E6354", {"start": v(450.98, -138.5) * mm, "end": v(436.02, -132.13) * mm});
            skLineSegment(sketch, "E6355", {"start": v(436.02, -132.13) * mm, "end": v(421.9, -125.91) * mm});
            skLineSegment(sketch, "E6356", {"start": v(421.9, -125.91) * mm, "end": v(408.7, -119.9) * mm});
            skLineSegment(sketch, "E6357", {"start": v(408.7, -119.9) * mm, "end": v(396.52, -114.14) * mm});
            skLineSegment(sketch, "E6358", {"start": v(396.52, -114.14) * mm, "end": v(385.44, -108.7) * mm});
            skLineSegment(sketch, "E6359", {"start": v(385.44, -108.7) * mm, "end": v(375.55, -103.63) * mm});
            skLineSegment(sketch, "E6360", {"start": v(375.55, -103.63) * mm, "end": v(369.08, -100.18) * mm});
            skLineSegment(sketch, "E6361", {"start": v(369.08, -100.18) * mm, "end": v(366.95, -99) * mm});
            skLineSegment(sketch, "E6362", {"start": v(366.95, -99) * mm, "end": v(363.99, -97.35) * mm});
            skLineSegment(sketch, "E6363", {"start": v(363.99, -97.35) * mm, "end": v(355.16, -92.35) * mm});
            skLineSegment(sketch, "E6364", {"start": v(355.16, -92.35) * mm, "end": v(342.4, -84.96) * mm});
            skLineSegment(sketch, "E6365", {"start": v(342.4, -84.96) * mm, "end": v(328.83, -76.92) * mm});
            skLineSegment(sketch, "E6366", {"start": v(328.83, -76.92) * mm, "end": v(314.6, -68.35) * mm});
            skLineSegment(sketch, "E6367", {"start": v(314.6, -68.35) * mm, "end": v(299.88, -59.34) * mm});
            skLineSegment(sketch, "E6368", {"start": v(299.88, -59.34) * mm, "end": v(284.84, -50.01) * mm});
            skLineSegment(sketch, "E6369", {"start": v(284.84, -50.01) * mm, "end": v(269.64, -40.46) * mm});
            skLineSegment(sketch, "E6370", {"start": v(269.64, -40.46) * mm, "end": v(254.43, -30.8) * mm});
            skLineSegment(sketch, "E6371", {"start": v(254.43, -30.8) * mm, "end": v(239.39, -21.13) * mm});
            skLineSegment(sketch, "E6372", {"start": v(239.39, -21.13) * mm, "end": v(224.68, -11.57) * mm});
            skLineSegment(sketch, "E6373", {"start": v(224.68, -11.57) * mm, "end": v(210.46, -2.21) * mm});
            skLineSegment(sketch, "E6374", {"start": v(210.46, -2.21) * mm, "end": v(196.9, 6.83) * mm});
            skLineSegment(sketch, "E6375", {"start": v(196.9, 6.83) * mm, "end": v(184.15, 15.46) * mm});
            skLineSegment(sketch, "E6376", {"start": v(184.15, 15.46) * mm, "end": v(172.38, 23.56) * mm});
            skLineSegment(sketch, "E6377", {"start": v(172.38, 23.56) * mm, "end": v(161.77, 31.02) * mm});
            skLineSegment(sketch, "E6378", {"start": v(161.77, 31.02) * mm, "end": v(154.77, 36.05) * mm});
            skLineSegment(sketch, "E6379", {"start": v(154.77, 36.05) * mm, "end": v(152.46, 37.75) * mm});
            skLineSegment(sketch, "E6380", {"start": v(152.46, 37.75) * mm, "end": v(150.2, 39.4) * mm});
            skLineSegment(sketch, "E6381", {"start": v(150.2, 39.4) * mm, "end": v(143.54, 44.53) * mm});
            skLineSegment(sketch, "E6382", {"start": v(143.54, 44.53) * mm, "end": v(134.02, 52.11) * mm});
            skLineSegment(sketch, "E6383", {"start": v(134.02, 52.11) * mm, "end": v(123.94, 60.32) * mm});
            skLineSegment(sketch, "E6384", {"start": v(123.94, 60.32) * mm, "end": v(113.36, 69) * mm});
            skLineSegment(sketch, "E6385", {"start": v(113.36, 69) * mm, "end": v(102.33, 78) * mm});
            skLineSegment(sketch, "E6386", {"start": v(102.33, 78) * mm, "end": v(90.9, 87.1) * mm});
            skLineSegment(sketch, "E6387", {"start": v(90.9, 87.1) * mm, "end": v(79.13, 96.19) * mm});
            skLineSegment(sketch, "E6388", {"start": v(79.13, 96.19) * mm, "end": v(67.05, 105.07) * mm});
            skLineSegment(sketch, "E6389", {"start": v(67.05, 105.07) * mm, "end": v(54.74, 113.57) * mm});
            skLineSegment(sketch, "E6390", {"start": v(54.74, 113.57) * mm, "end": v(42.23, 121.54) * mm});
            skLineSegment(sketch, "E6391", {"start": v(42.23, 121.54) * mm, "end": v(29.59, 128.8) * mm});
            skLineSegment(sketch, "E6392", {"start": v(29.59, 128.8) * mm, "end": v(16.85, 135.2) * mm});
            skLineSegment(sketch, "E6393", {"start": v(16.85, 135.2) * mm, "end": v(4.07, 140.54) * mm});
            skLineSegment(sketch, "E6394", {"start": v(4.07, 140.54) * mm, "end": v(-8.69, 144.68) * mm});
            skLineSegment(sketch, "E6395", {"start": v(-8.69, 144.68) * mm, "end": v(-21.38, 147.44) * mm});
            skLineSegment(sketch, "E6396", {"start": v(-21.38, 147.44) * mm, "end": v(-30.8, 148.56) * mm});
            skLineSegment(sketch, "E6397", {"start": v(-30.8, 148.56) * mm, "end": v(-33.96, 148.65) * mm});
            skLineSegment(sketch, "E6398", {"start": v(-33.96, 148.65) * mm, "end": v(-36.3, 148.72) * mm});
            skLineSegment(sketch, "E6399", {"start": v(-36.3, 148.72) * mm, "end": v(-43.3, 148.87) * mm});
            skLineSegment(sketch, "E6400", {"start": v(-43.3, 148.87) * mm, "end": v(-52.08, 148.93) * mm});
            skLineSegment(sketch, "E6401", {"start": v(-52.08, 148.93) * mm, "end": v(-60.36, 148.84) * mm});
            skLineSegment(sketch, "E6402", {"start": v(-60.36, 148.84) * mm, "end": v(-68.15, 148.62) * mm});
            skLineSegment(sketch, "E6403", {"start": v(-68.15, 148.62) * mm, "end": v(-75.46, 148.26) * mm});
            skLineSegment(sketch, "E6404", {"start": v(-75.46, 148.26) * mm, "end": v(-82.34, 147.78) * mm});
            skLineSegment(sketch, "E6405", {"start": v(-82.34, 147.78) * mm, "end": v(-88.8, 147.19) * mm});
            skLineSegment(sketch, "E6406", {"start": v(-88.8, 147.19) * mm, "end": v(-94.85, 146.48) * mm});
            skLineSegment(sketch, "E6407", {"start": v(-94.85, 146.48) * mm, "end": v(-100.54, 145.7) * mm});
            skLineSegment(sketch, "E6408", {"start": v(-100.54, 145.7) * mm, "end": v(-105.88, 144.8) * mm});
            skLineSegment(sketch, "E6409", {"start": v(-105.88, 144.8) * mm, "end": v(-110.9, 143.84) * mm});
            skLineSegment(sketch, "E6410", {"start": v(-110.9, 143.84) * mm, "end": v(-115.62, 142.8) * mm});
            skLineSegment(sketch, "E6411", {"start": v(-115.62, 142.8) * mm, "end": v(-120.07, 141.7) * mm});
            skLineSegment(sketch, "E6412", {"start": v(-120.07, 141.7) * mm, "end": v(-124.27, 140.56) * mm});
            skLineSegment(sketch, "E6413", {"start": v(-124.27, 140.56) * mm, "end": v(-128.24, 139.36) * mm});
            skLineSegment(sketch, "E6414", {"start": v(-128.24, 139.36) * mm, "end": v(-132.01, 138.12) * mm});
            skLineSegment(sketch, "E6415", {"start": v(-132.01, 138.12) * mm, "end": v(-135.6, 136.86) * mm});
            skLineSegment(sketch, "E6416", {"start": v(-135.6, 136.86) * mm, "end": v(-139.05, 135.57) * mm});
            skLineSegment(sketch, "E6417", {"start": v(-139.05, 135.57) * mm, "end": v(-142.36, 134.28) * mm});
            skLineSegment(sketch, "E6418", {"start": v(-142.36, 134.28) * mm, "end": v(-145.57, 132.98) * mm});
            skLineSegment(sketch, "E6419", {"start": v(-145.57, 132.98) * mm, "end": v(-148.7, 131.69) * mm});
            skLineSegment(sketch, "E6420", {"start": v(-148.7, 131.69) * mm, "end": v(-151.77, 130.4) * mm});
            skLineSegment(sketch, "E6421", {"start": v(-151.77, 130.4) * mm, "end": v(-154.8, 129.15) * mm});
            skLineSegment(sketch, "E6422", {"start": v(-154.8, 129.15) * mm, "end": v(-157.83, 127.92) * mm});
            skLineSegment(sketch, "E6423", {"start": v(-157.83, 127.92) * mm, "end": v(-160.88, 126.73) * mm});
            skLineSegment(sketch, "E6424", {"start": v(-160.88, 126.73) * mm, "end": v(-163.97, 125.6) * mm});
            skLineSegment(sketch, "E6425", {"start": v(-163.97, 125.6) * mm, "end": v(-167.12, 124.51) * mm});
            skLineSegment(sketch, "E6426", {"start": v(-167.12, 124.51) * mm, "end": v(-170.36, 123.5) * mm});
            skLineSegment(sketch, "E6427", {"start": v(-170.36, 123.5) * mm, "end": v(-173.71, 122.55) * mm});
            skLineSegment(sketch, "E6428", {"start": v(-173.71, 122.55) * mm, "end": v(-177.2, 121.69) * mm});
            skLineSegment(sketch, "E6429", {"start": v(-177.2, 121.69) * mm, "end": v(-180.86, 120.92) * mm});
            skLineSegment(sketch, "E6430", {"start": v(-180.86, 120.92) * mm, "end": v(-183.73, 120.4) * mm});
            skLineSegment(sketch, "E6431", {"start": v(-183.73, 120.4) * mm, "end": v(-184.7, 120.24) * mm});
            skLineSegment(sketch, "E6432", {"start": v(-184.7, 120.24) * mm, "end": v(-188.23, 120.42) * mm});
            skLineSegment(sketch, "E6433", {"start": v(-188.23, 120.42) * mm, "end": v(-198.82, 121.15) * mm});
            skLineSegment(sketch, "E6434", {"start": v(-198.82, 121.15) * mm, "end": v(-211.69, 122.34) * mm});
            skLineSegment(sketch, "E6435", {"start": v(-211.69, 122.34) * mm, "end": v(-223.62, 123.76) * mm});
            skLineSegment(sketch, "E6436", {"start": v(-223.62, 123.76) * mm, "end": v(-234.93, 125.36) * mm});
            skLineSegment(sketch, "E6437", {"start": v(-234.93, 125.36) * mm, "end": v(-245.93, 127.1) * mm});
            skLineSegment(sketch, "E6438", {"start": v(-245.93, 127.1) * mm, "end": v(-256.92, 128.94) * mm});
            skLineSegment(sketch, "E6439", {"start": v(-256.92, 128.94) * mm, "end": v(-268.24, 130.83) * mm});
            skLineSegment(sketch, "E6440", {"start": v(-268.24, 130.83) * mm, "end": v(-277.2, 132.27) * mm});
            skLineSegment(sketch, "E6441", {"start": v(-277.2, 132.27) * mm, "end": v(-280.2, 132.73) * mm});
            skLineSegment(sketch, "E6442", {"start": v(-280.2, 132.73) * mm, "end": v(-281.65, 132.95) * mm});
            skLineSegment(sketch, "E6443", {"start": v(-281.65, 132.95) * mm, "end": v(-285.95, 134.04) * mm});
            skLineSegment(sketch, "E6444", {"start": v(-285.95, 134.04) * mm, "end": v(-292.88, 136.2) * mm});
            skLineSegment(sketch, "E6445", {"start": v(-292.88, 136.2) * mm, "end": v(-300.7, 138.94) * mm});
            skLineSegment(sketch, "E6446", {"start": v(-300.7, 138.94) * mm, "end": v(-309.13, 141.96) * mm});
            skLineSegment(sketch, "E6447", {"start": v(-309.13, 141.96) * mm, "end": v(-317.9, 144.96) * mm});
            skLineSegment(sketch, "E6448", {"start": v(-317.9, 144.96) * mm, "end": v(-326.75, 147.65) * mm});
            skLineSegment(sketch, "E6449", {"start": v(-326.75, 147.65) * mm, "end": v(-335.38, 149.74) * mm});
            skLineSegment(sketch, "E6450", {"start": v(-335.38, 149.74) * mm, "end": v(-341.47, 150.76) * mm});
            skLineSegment(sketch, "E6451", {"start": v(-341.47, 150.76) * mm, "end": v(-343.52, 150.93) * mm});
            skLineSegment(sketch, "E6452", {"start": v(-343.52, 150.93) * mm, "end": v(-345.98, 151.14) * mm});
            skLineSegment(sketch, "E6453", {"start": v(-345.98, 151.14) * mm, "end": v(-353.37, 151.53) * mm});
            skLineSegment(sketch, "E6454", {"start": v(-353.37, 151.53) * mm, "end": v(-363.45, 151.81) * mm});
            skLineSegment(sketch, "E6455", {"start": v(-363.45, 151.81) * mm, "end": v(-373.67, 151.9) * mm});
            skLineSegment(sketch, "E6456", {"start": v(-373.67, 151.9) * mm, "end": v(-383.92, 151.93) * mm});
            skLineSegment(sketch, "E6457", {"start": v(-383.92, 151.93) * mm, "end": v(-394.12, 152.03) * mm});
            skLineSegment(sketch, "E6458", {"start": v(-394.12, 152.03) * mm, "end": v(-404.16, 152.34) * mm});
            skLineSegment(sketch, "E6459", {"start": v(-404.16, 152.34) * mm, "end": v(-413.96, 152.99) * mm});
            skLineSegment(sketch, "E6460", {"start": v(-413.96, 152.99) * mm, "end": v(-421.06, 153.75) * mm});
            skLineSegment(sketch, "E6461", {"start": v(-421.06, 153.75) * mm, "end": v(-423.42, 154.1) * mm});
            skLineSegment(sketch, "E6462", {"start": v(-423.42, 154.1) * mm, "end": v(-424.85, 154.32) * mm});
            skLineSegment(sketch, "E6463", {"start": v(-424.85, 154.32) * mm, "end": v(-429.15, 154.98) * mm});
            skLineSegment(sketch, "E6464", {"start": v(-429.15, 154.98) * mm, "end": v(-435.44, 155.95) * mm});
            skLineSegment(sketch, "E6465", {"start": v(-435.44, 155.95) * mm, "end": v(-442.14, 157) * mm});
            skLineSegment(sketch, "E6466", {"start": v(-442.14, 157) * mm, "end": v(-449.13, 158.1) * mm});
            skLineSegment(sketch, "E6467", {"start": v(-449.13, 158.1) * mm, "end": v(-456.28, 159.22) * mm});
            skLineSegment(sketch, "E6468", {"start": v(-456.28, 159.22) * mm, "end": v(-463.48, 160.37) * mm});
            skLineSegment(sketch, "E6469", {"start": v(-463.48, 160.37) * mm, "end": v(-470.58, 161.5) * mm});
            skLineSegment(sketch, "E6470", {"start": v(-470.58, 161.5) * mm, "end": v(-477.48, 162.6) * mm});
            skLineSegment(sketch, "E6471", {"start": v(-477.48, 162.6) * mm, "end": v(-484.03, 163.65) * mm});
            skLineSegment(sketch, "E6472", {"start": v(-484.03, 163.65) * mm, "end": v(-490.13, 164.63) * mm});
            skLineSegment(sketch, "E6473", {"start": v(-490.13, 164.63) * mm, "end": v(-495.63, 165.52) * mm});
            skLineSegment(sketch, "E6474", {"start": v(-495.63, 165.52) * mm, "end": v(-500.4, 166.3) * mm});
            skLineSegment(sketch, "E6475", {"start": v(-500.4, 166.3) * mm, "end": v(-504.35, 166.93) * mm});
            skLineSegment(sketch, "E6476", {"start": v(-504.35, 166.93) * mm, "end": v(-507.32, 167.41) * mm});
            skLineSegment(sketch, "E6477", {"start": v(-507.32, 167.41) * mm, "end": v(-509.2, 167.72) * mm});
            skLineSegment(sketch, "E6478", {"start": v(-509.2, 167.72) * mm, "end": v(-509.84, 167.82) * mm});
            skLineSegment(sketch, "E6479", {"start": v(610.28, -175.54) * mm, "end": v(607.92, -174.92) * mm});
            skLineSegment(sketch, "E6480", {"start": v(607.92, -174.92) * mm, "end": v(600.88, -172.97) * mm});
            skLineSegment(sketch, "E6481", {"start": v(600.88, -172.97) * mm, "end": v(591.2, -170.15) * mm});
            skLineSegment(sketch, "E6482", {"start": v(591.2, -170.15) * mm, "end": v(581.28, -167.09) * mm});
            skLineSegment(sketch, "E6483", {"start": v(581.28, -167.09) * mm, "end": v(571.14, -163.81) * mm});
            skLineSegment(sketch, "E6484", {"start": v(571.14, -163.81) * mm, "end": v(560.8, -160.33) * mm});
            skLineSegment(sketch, "E6485", {"start": v(560.8, -160.33) * mm, "end": v(550.27, -156.65) * mm});
            skLineSegment(sketch, "E6486", {"start": v(550.27, -156.65) * mm, "end": v(539.6, -152.79) * mm});
            skLineSegment(sketch, "E6487", {"start": v(539.6, -152.79) * mm, "end": v(528.8, -148.76) * mm});
            skLineSegment(sketch, "E6488", {"start": v(528.8, -148.76) * mm, "end": v(517.9, -144.58) * mm});
            skLineSegment(sketch, "E6489", {"start": v(517.9, -144.58) * mm, "end": v(506.93, -140.26) * mm});
            skLineSegment(sketch, "E6490", {"start": v(506.93, -140.26) * mm, "end": v(495.92, -135.8) * mm});
            skLineSegment(sketch, "E6491", {"start": v(495.92, -135.8) * mm, "end": v(484.87, -131.24) * mm});
            skLineSegment(sketch, "E6492", {"start": v(484.87, -131.24) * mm, "end": v(473.84, -126.57) * mm});
            skLineSegment(sketch, "E6493", {"start": v(473.84, -126.57) * mm, "end": v(462.82, -121.81) * mm});
            skLineSegment(sketch, "E6494", {"start": v(462.82, -121.81) * mm, "end": v(451.86, -116.98) * mm});
            skLineSegment(sketch, "E6495", {"start": v(451.86, -116.98) * mm, "end": v(440.98, -112.1) * mm});
            skLineSegment(sketch, "E6496", {"start": v(440.98, -112.1) * mm, "end": v(430.2, -107.15) * mm});
            skLineSegment(sketch, "E6497", {"start": v(430.2, -107.15) * mm, "end": v(419.54, -102.17) * mm});
            skLineSegment(sketch, "E6498", {"start": v(419.54, -102.17) * mm, "end": v(409.04, -97.17) * mm});
            skLineSegment(sketch, "E6499", {"start": v(409.04, -97.17) * mm, "end": v(398.72, -92.16) * mm});
            skLineSegment(sketch, "E6500", {"start": v(398.72, -92.16) * mm, "end": v(388.6, -87.16) * mm});
            skLineSegment(sketch, "E6501", {"start": v(388.6, -87.16) * mm, "end": v(378.7, -82.17) * mm});
            skLineSegment(sketch, "E6502", {"start": v(378.7, -82.17) * mm, "end": v(369.07, -77.22) * mm});
            skLineSegment(sketch, "E6503", {"start": v(369.07, -77.22) * mm, "end": v(359.7, -72.3) * mm});
            skLineSegment(sketch, "E6504", {"start": v(359.7, -72.3) * mm, "end": v(350.65, -67.46) * mm});
            skLineSegment(sketch, "E6505", {"start": v(350.65, -67.46) * mm, "end": v(341.92, -62.67) * mm});
            skLineSegment(sketch, "E6506", {"start": v(341.92, -62.67) * mm, "end": v(333.54, -57.97) * mm});
            skLineSegment(sketch, "E6507", {"start": v(333.54, -57.97) * mm, "end": v(325.55, -53.37) * mm});
            skLineSegment(sketch, "E6508", {"start": v(325.55, -53.37) * mm, "end": v(317.95, -48.88) * mm});
            skLineSegment(sketch, "E6509", {"start": v(317.95, -48.88) * mm, "end": v(310.8, -44.5) * mm});
            skLineSegment(sketch, "E6510", {"start": v(310.8, -44.5) * mm, "end": v(304.08, -40.28) * mm});
            skLineSegment(sketch, "E6511", {"start": v(304.08, -40.28) * mm, "end": v(299.4, -37.23) * mm});
            skLineSegment(sketch, "E6512", {"start": v(299.4, -37.23) * mm, "end": v(297.85, -36.2) * mm});
            skLineSegment(sketch, "E6513", {"start": v(297.85, -36.2) * mm, "end": v(295.09, -34.35) * mm});
            skLineSegment(sketch, "E6514", {"start": v(295.09, -34.35) * mm, "end": v(286.76, -28.83) * mm});
            skLineSegment(sketch, "E6515", {"start": v(286.76, -28.83) * mm, "end": v(276.04, -21.8) * mm});
            skLineSegment(sketch, "E6516", {"start": v(276.04, -21.8) * mm, "end": v(265.63, -15.04) * mm});
            skLineSegment(sketch, "E6517", {"start": v(265.63, -15.04) * mm, "end": v(255.52, -8.54) * mm});
            skLineSegment(sketch, "E6518", {"start": v(255.52, -8.54) * mm, "end": v(245.67, -2.25) * mm});
            skLineSegment(sketch, "E6519", {"start": v(245.67, -2.25) * mm, "end": v(236.06, 3.86) * mm});
            skLineSegment(sketch, "E6520", {"start": v(236.06, 3.86) * mm, "end": v(226.65, 9.83) * mm});
            skLineSegment(sketch, "E6521", {"start": v(226.65, 9.83) * mm, "end": v(217.4, 15.7) * mm});
            skLineSegment(sketch, "E6522", {"start": v(217.4, 15.7) * mm, "end": v(208.29, 21.52) * mm});
            skLineSegment(sketch, "E6523", {"start": v(208.29, 21.52) * mm, "end": v(199.29, 27.3) * mm});
            skLineSegment(sketch, "E6524", {"start": v(199.29, 27.3) * mm, "end": v(190.36, 33.1) * mm});
            skLineSegment(sketch, "E6525", {"start": v(190.36, 33.1) * mm, "end": v(181.47, 38.96) * mm});
            skLineSegment(sketch, "E6526", {"start": v(181.47, 38.96) * mm, "end": v(172.6, 44.9) * mm});
            skLineSegment(sketch, "E6527", {"start": v(172.6, 44.9) * mm, "end": v(163.72, 50.97) * mm});
            skLineSegment(sketch, "E6528", {"start": v(163.72, 50.97) * mm, "end": v(154.77, 57.2) * mm});
            skLineSegment(sketch, "E6529", {"start": v(154.77, 57.2) * mm, "end": v(148, 62.02) * mm});
            skLineSegment(sketch, "E6530", {"start": v(148, 62.02) * mm, "end": v(145.75, 63.64) * mm});
            skLineSegment(sketch, "E6531", {"start": v(145.75, 63.64) * mm, "end": v(143.5, 65.27) * mm});
            skLineSegment(sketch, "E6532", {"start": v(143.5, 65.27) * mm, "end": v(136.84, 70.27) * mm});
            skLineSegment(sketch, "E6533", {"start": v(136.84, 70.27) * mm, "end": v(127.33, 77.64) * mm});
            skLineSegment(sketch, "E6534", {"start": v(127.33, 77.64) * mm, "end": v(117.3, 85.59) * mm});
            skLineSegment(sketch, "E6535", {"start": v(117.3, 85.59) * mm, "end": v(106.77, 93.93) * mm});
            skLineSegment(sketch, "E6536", {"start": v(106.77, 93.93) * mm, "end": v(95.81, 102.54) * mm});
            skLineSegment(sketch, "E6537", {"start": v(95.81, 102.54) * mm, "end": v(84.45, 111.24) * mm});
            skLineSegment(sketch, "E6538", {"start": v(84.45, 111.24) * mm, "end": v(72.76, 119.86) * mm});
            skLineSegment(sketch, "E6539", {"start": v(72.76, 119.86) * mm, "end": v(60.78, 128.26) * mm});
            skLineSegment(sketch, "E6540", {"start": v(60.78, 128.26) * mm, "end": v(48.55, 136.27) * mm});
            skLineSegment(sketch, "E6541", {"start": v(48.55, 136.27) * mm, "end": v(36.12, 143.73) * mm});
            skLineSegment(sketch, "E6542", {"start": v(36.12, 143.73) * mm, "end": v(23.55, 150.49) * mm});
            skLineSegment(sketch, "E6543", {"start": v(23.55, 150.49) * mm, "end": v(10.88, 156.37) * mm});
            skLineSegment(sketch, "E6544", {"start": v(10.88, 156.37) * mm, "end": v(-1.84, 161.23) * mm});
            skLineSegment(sketch, "E6545", {"start": v(-1.84, 161.23) * mm, "end": v(-14.56, 164.9) * mm});
            skLineSegment(sketch, "E6546", {"start": v(-14.56, 164.9) * mm, "end": v(-27.23, 167.21) * mm});
            skLineSegment(sketch, "E6547", {"start": v(-27.23, 167.21) * mm, "end": v(-36.66, 168.02) * mm});
            skLineSegment(sketch, "E6548", {"start": v(-36.66, 168.02) * mm, "end": v(-39.8, 168.02) * mm});
            skLineSegment(sketch, "E6549", {"start": v(-39.8, 168.02) * mm, "end": v(-43.76, 168.02) * mm});
            skLineSegment(sketch, "E6550", {"start": v(-43.76, 168.02) * mm, "end": v(-55.65, 167.77) * mm});
            skLineSegment(sketch, "E6551", {"start": v(-55.65, 167.77) * mm, "end": v(-70.02, 167.07) * mm});
            skLineSegment(sketch, "E6552", {"start": v(-70.02, 167.07) * mm, "end": v(-83.05, 165.96) * mm});
            skLineSegment(sketch, "E6553", {"start": v(-83.05, 165.96) * mm, "end": v(-94.87, 164.51) * mm});
            skLineSegment(sketch, "E6554", {"start": v(-94.87, 164.51) * mm, "end": v(-105.6, 162.76) * mm});
            skLineSegment(sketch, "E6555", {"start": v(-105.6, 162.76) * mm, "end": v(-115.4, 160.78) * mm});
            skLineSegment(sketch, "E6556", {"start": v(-115.4, 160.78) * mm, "end": v(-124.37, 158.6) * mm});
            skLineSegment(sketch, "E6557", {"start": v(-124.37, 158.6) * mm, "end": v(-132.68, 156.3) * mm});
            skLineSegment(sketch, "E6558", {"start": v(-132.68, 156.3) * mm, "end": v(-140.43, 153.91) * mm});
            skLineSegment(sketch, "E6559", {"start": v(-140.43, 153.91) * mm, "end": v(-147.77, 151.5) * mm});
            skLineSegment(sketch, "E6560", {"start": v(-147.77, 151.5) * mm, "end": v(-154.82, 149.13) * mm});
            skLineSegment(sketch, "E6561", {"start": v(-154.82, 149.13) * mm, "end": v(-161.73, 146.84) * mm});
            skLineSegment(sketch, "E6562", {"start": v(-161.73, 146.84) * mm, "end": v(-168.62, 144.69) * mm});
            skLineSegment(sketch, "E6563", {"start": v(-168.62, 144.69) * mm, "end": v(-175.63, 142.73) * mm});
            skLineSegment(sketch, "E6564", {"start": v(-175.63, 142.73) * mm, "end": v(-182.9, 141.02) * mm});
            skLineSegment(sketch, "E6565", {"start": v(-182.9, 141.02) * mm, "end": v(-188.62, 139.9) * mm});
            skLineSegment(sketch, "E6566", {"start": v(-188.62, 139.9) * mm, "end": v(-190.54, 139.6) * mm});
            skLineSegment(sketch, "E6567", {"start": v(-190.54, 139.6) * mm, "end": v(-194.07, 139.79) * mm});
            skLineSegment(sketch, "E6568", {"start": v(-194.07, 139.79) * mm, "end": v(-204.66, 140.52) * mm});
            skLineSegment(sketch, "E6569", {"start": v(-204.66, 140.52) * mm, "end": v(-217.53, 141.7) * mm});
            skLineSegment(sketch, "E6570", {"start": v(-217.53, 141.7) * mm, "end": v(-229.46, 143.12) * mm});
            skLineSegment(sketch, "E6571", {"start": v(-229.46, 143.12) * mm, "end": v(-240.77, 144.72) * mm});
            skLineSegment(sketch, "E6572", {"start": v(-240.77, 144.72) * mm, "end": v(-251.76, 146.46) * mm});
            skLineSegment(sketch, "E6573", {"start": v(-251.76, 146.46) * mm, "end": v(-262.76, 148.3) * mm});
            skLineSegment(sketch, "E6574", {"start": v(-262.76, 148.3) * mm, "end": v(-274.08, 150.2) * mm});
            skLineSegment(sketch, "E6575", {"start": v(-274.08, 150.2) * mm, "end": v(-283.04, 151.64) * mm});
            skLineSegment(sketch, "E6576", {"start": v(-283.04, 151.64) * mm, "end": v(-286.03, 152.1) * mm});
            skLineSegment(sketch, "E6577", {"start": v(-286.03, 152.1) * mm, "end": v(-287.49, 152.32) * mm});
            skLineSegment(sketch, "E6578", {"start": v(-287.49, 152.32) * mm, "end": v(-291.8, 153.4) * mm});
            skLineSegment(sketch, "E6579", {"start": v(-291.8, 153.4) * mm, "end": v(-298.72, 155.57) * mm});
            skLineSegment(sketch, "E6580", {"start": v(-298.72, 155.57) * mm, "end": v(-306.54, 158.31) * mm});
            skLineSegment(sketch, "E6581", {"start": v(-306.54, 158.31) * mm, "end": v(-314.97, 161.33) * mm});
            skLineSegment(sketch, "E6582", {"start": v(-314.97, 161.33) * mm, "end": v(-323.74, 164.33) * mm});
            skLineSegment(sketch, "E6583", {"start": v(-323.74, 164.33) * mm, "end": v(-332.59, 167.01) * mm});
            skLineSegment(sketch, "E6584", {"start": v(-332.59, 167.01) * mm, "end": v(-341.21, 169.1) * mm});
            skLineSegment(sketch, "E6585", {"start": v(-341.21, 169.1) * mm, "end": v(-347.31, 170.13) * mm});
            skLineSegment(sketch, "E6586", {"start": v(-347.31, 170.13) * mm, "end": v(-349.36, 170.3) * mm});
            skLineSegment(sketch, "E6587", {"start": v(-349.36, 170.3) * mm, "end": v(-351.82, 170.5) * mm});
            skLineSegment(sketch, "E6588", {"start": v(-351.82, 170.5) * mm, "end": v(-359.21, 170.9) * mm});
            skLineSegment(sketch, "E6589", {"start": v(-359.21, 170.9) * mm, "end": v(-369.29, 171.18) * mm});
            skLineSegment(sketch, "E6590", {"start": v(-369.29, 171.18) * mm, "end": v(-379.5, 171.27) * mm});
            skLineSegment(sketch, "E6591", {"start": v(-379.5, 171.27) * mm, "end": v(-389.76, 171.3) * mm});
            skLineSegment(sketch, "E6592", {"start": v(-389.76, 171.3) * mm, "end": v(-399.96, 171.4) * mm});
            skLineSegment(sketch, "E6593", {"start": v(-399.96, 171.4) * mm, "end": v(-410, 171.7) * mm});
            skLineSegment(sketch, "E6594", {"start": v(-410, 171.7) * mm, "end": v(-419.8, 172.35) * mm});
            skLineSegment(sketch, "E6595", {"start": v(-419.8, 172.35) * mm, "end": v(-426.9, 173.12) * mm});
            skLineSegment(sketch, "E6596", {"start": v(-426.9, 173.12) * mm, "end": v(-429.26, 173.47) * mm});
            skLineSegment(sketch, "E6597", {"start": v(-429.26, 173.47) * mm, "end": v(-430.7, 173.69) * mm});
            skLineSegment(sketch, "E6598", {"start": v(-430.7, 173.69) * mm, "end": v(-435, 174.35) * mm});
            skLineSegment(sketch, "E6599", {"start": v(-435, 174.35) * mm, "end": v(-441.28, 175.32) * mm});
            skLineSegment(sketch, "E6600", {"start": v(-441.28, 175.32) * mm, "end": v(-447.97, 176.36) * mm});
            skLineSegment(sketch, "E6601", {"start": v(-447.97, 176.36) * mm, "end": v(-454.96, 177.46) * mm});
            skLineSegment(sketch, "E6602", {"start": v(-454.96, 177.46) * mm, "end": v(-462.12, 178.59) * mm});
            skLineSegment(sketch, "E6603", {"start": v(-462.12, 178.59) * mm, "end": v(-469.31, 179.73) * mm});
            skLineSegment(sketch, "E6604", {"start": v(-469.31, 179.73) * mm, "end": v(-476.42, 180.87) * mm});
            skLineSegment(sketch, "E6605", {"start": v(-476.42, 180.87) * mm, "end": v(-483.32, 181.97) * mm});
            skLineSegment(sketch, "E6606", {"start": v(-483.32, 181.97) * mm, "end": v(-489.87, 183.02) * mm});
            skLineSegment(sketch, "E6607", {"start": v(-489.87, 183.02) * mm, "end": v(-495.96, 184) * mm});
            skLineSegment(sketch, "E6608", {"start": v(-495.96, 184) * mm, "end": v(-501.46, 184.89) * mm});
            skLineSegment(sketch, "E6609", {"start": v(-501.46, 184.89) * mm, "end": v(-506.25, 185.66) * mm});
            skLineSegment(sketch, "E6610", {"start": v(-506.25, 185.66) * mm, "end": v(-510.19, 186.3) * mm});
            skLineSegment(sketch, "E6611", {"start": v(-510.19, 186.3) * mm, "end": v(-513.16, 186.78) * mm});
            skLineSegment(sketch, "E6612", {"start": v(-513.16, 186.78) * mm, "end": v(-515.03, 187.08) * mm});
            skLineSegment(sketch, "E6613", {"start": v(-515.03, 187.08) * mm, "end": v(-515.68, 187.19) * mm});
            skLineSegment(sketch, "E6614", {"start": v(611.1, -340.64) * mm, "end": v(610.14, -340.57) * mm});
            skLineSegment(sketch, "E6615", {"start": v(610.14, -340.57) * mm, "end": v(607.27, -340.24) * mm});
            skLineSegment(sketch, "E6616", {"start": v(607.27, -340.24) * mm, "end": v(602.57, -339.56) * mm});
            skLineSegment(sketch, "E6617", {"start": v(602.57, -339.56) * mm, "end": v(597.05, -338.62) * mm});
            skLineSegment(sketch, "E6618", {"start": v(597.05, -338.62) * mm, "end": v(590.78, -337.43) * mm});
            skLineSegment(sketch, "E6619", {"start": v(590.78, -337.43) * mm, "end": v(583.8, -336) * mm});
            skLineSegment(sketch, "E6620", {"start": v(583.8, -336) * mm, "end": v(576.16, -334.36) * mm});
            skLineSegment(sketch, "E6621", {"start": v(576.16, -334.36) * mm, "end": v(567.91, -332.51) * mm});
            skLineSegment(sketch, "E6622", {"start": v(567.91, -332.51) * mm, "end": v(559.1, -330.47) * mm});
            skLineSegment(sketch, "E6623", {"start": v(559.1, -330.47) * mm, "end": v(549.8, -328.25) * mm});
            skLineSegment(sketch, "E6624", {"start": v(549.8, -328.25) * mm, "end": v(540.06, -325.86) * mm});
            skLineSegment(sketch, "E6625", {"start": v(540.06, -325.86) * mm, "end": v(529.9, -323.33) * mm});
            skLineSegment(sketch, "E6626", {"start": v(529.9, -323.33) * mm, "end": v(519.42, -320.64) * mm});
            skLineSegment(sketch, "E6627", {"start": v(519.42, -320.64) * mm, "end": v(508.63, -317.85) * mm});
            skLineSegment(sketch, "E6628", {"start": v(508.63, -317.85) * mm, "end": v(497.6, -314.93) * mm});
            skLineSegment(sketch, "E6629", {"start": v(497.6, -314.93) * mm, "end": v(486.38, -311.92) * mm});
            skLineSegment(sketch, "E6630", {"start": v(486.38, -311.92) * mm, "end": v(475.02, -308.82) * mm});
            skLineSegment(sketch, "E6631", {"start": v(475.02, -308.82) * mm, "end": v(463.58, -305.66) * mm});
            skLineSegment(sketch, "E6632", {"start": v(463.58, -305.66) * mm, "end": v(452.11, -302.43) * mm});
            skLineSegment(sketch, "E6633", {"start": v(452.11, -302.43) * mm, "end": v(440.66, -299.16) * mm});
            skLineSegment(sketch, "E6634", {"start": v(440.66, -299.16) * mm, "end": v(429.27, -295.86) * mm});
            skLineSegment(sketch, "E6635", {"start": v(429.27, -295.86) * mm, "end": v(418.01, -292.55) * mm});
            skLineSegment(sketch, "E6636", {"start": v(418.01, -292.55) * mm, "end": v(406.93, -289.23) * mm});
            skLineSegment(sketch, "E6637", {"start": v(406.93, -289.23) * mm, "end": v(396.07, -285.92) * mm});
            skLineSegment(sketch, "E6638", {"start": v(396.07, -285.92) * mm, "end": v(385.49, -282.64) * mm});
            skLineSegment(sketch, "E6639", {"start": v(385.49, -282.64) * mm, "end": v(375.24, -279.4) * mm});
            skLineSegment(sketch, "E6640", {"start": v(375.24, -279.4) * mm, "end": v(365.38, -276.2) * mm});
            skLineSegment(sketch, "E6641", {"start": v(365.38, -276.2) * mm, "end": v(355.95, -273.07) * mm});
            skLineSegment(sketch, "E6642", {"start": v(355.95, -273.07) * mm, "end": v(347, -270.01) * mm});
            skLineSegment(sketch, "E6643", {"start": v(347, -270.01) * mm, "end": v(338.6, -267.06) * mm});
            skLineSegment(sketch, "E6644", {"start": v(338.6, -267.06) * mm, "end": v(330.79, -264.2) * mm});
            skLineSegment(sketch, "E6645", {"start": v(330.79, -264.2) * mm, "end": v(323.62, -261.47) * mm});
            skLineSegment(sketch, "E6646", {"start": v(323.62, -261.47) * mm, "end": v(318.76, -259.53) * mm});
            skLineSegment(sketch, "E6647", {"start": v(318.76, -259.53) * mm, "end": v(317.14, -258.86) * mm});
            skLineSegment(sketch, "E6648", {"start": v(317.14, -258.86) * mm, "end": v(314.04, -257.58) * mm});
            skLineSegment(sketch, "E6649", {"start": v(314.04, -257.58) * mm, "end": v(304.8, -253.54) * mm});
            skLineSegment(sketch, "E6650", {"start": v(304.8, -253.54) * mm, "end": v(292.17, -247.72) * mm});
            skLineSegment(sketch, "E6651", {"start": v(292.17, -247.72) * mm, "end": v(279.28, -241.44) * mm});
            skLineSegment(sketch, "E6652", {"start": v(279.28, -241.44) * mm, "end": v(266.12, -234.72) * mm});
            skLineSegment(sketch, "E6653", {"start": v(266.12, -234.72) * mm, "end": v(252.68, -227.6) * mm});
            skLineSegment(sketch, "E6654", {"start": v(252.68, -227.6) * mm, "end": v(238.96, -220.12) * mm});
            skLineSegment(sketch, "E6655", {"start": v(238.96, -220.12) * mm, "end": v(224.96, -212.3) * mm});
            skLineSegment(sketch, "E6656", {"start": v(224.96, -212.3) * mm, "end": v(210.67, -204.16) * mm});
            skLineSegment(sketch, "E6657", {"start": v(210.67, -204.16) * mm, "end": v(196.1, -195.75) * mm});
            skLineSegment(sketch, "E6658", {"start": v(196.1, -195.75) * mm, "end": v(181.24, -187.1) * mm});
            skLineSegment(sketch, "E6659", {"start": v(181.24, -187.1) * mm, "end": v(166.08, -178.24) * mm});
            skLineSegment(sketch, "E6660", {"start": v(166.08, -178.24) * mm, "end": v(150.62, -169.2) * mm});
            skLineSegment(sketch, "E6661", {"start": v(150.62, -169.2) * mm, "end": v(134.87, -160) * mm});
            skLineSegment(sketch, "E6662", {"start": v(134.87, -160) * mm, "end": v(118.81, -150.69) * mm});
            skLineSegment(sketch, "E6663", {"start": v(118.81, -150.69) * mm, "end": v(102.45, -141.3) * mm});
            skLineSegment(sketch, "E6664", {"start": v(102.45, -141.3) * mm, "end": v(89.96, -134.2) * mm});
            skLineSegment(sketch, "E6665", {"start": v(89.96, -134.2) * mm, "end": v(85.78, -131.84) * mm});
            skLineSegment(sketch, "E6666", {"start": v(85.78, -131.84) * mm, "end": v(83.7, -130.67) * mm});
            skLineSegment(sketch, "E6667", {"start": v(83.7, -130.67) * mm, "end": v(77.56, -126.98) * mm});
            skLineSegment(sketch, "E6668", {"start": v(77.56, -126.98) * mm, "end": v(69.68, -121.87) * mm});
            skLineSegment(sketch, "E6669", {"start": v(69.68, -121.87) * mm, "end": v(62.14, -116.55) * mm});
            skLineSegment(sketch, "E6670", {"start": v(62.14, -116.55) * mm, "end": v(54.92, -111.04) * mm});
            skLineSegment(sketch, "E6671", {"start": v(54.92, -111.04) * mm, "end": v(48, -105.37) * mm});
            skLineSegment(sketch, "E6672", {"start": v(48, -105.37) * mm, "end": v(41.36, -99.57) * mm});
            skLineSegment(sketch, "E6673", {"start": v(41.36, -99.57) * mm, "end": v(34.98, -93.65) * mm});
            skLineSegment(sketch, "E6674", {"start": v(34.98, -93.65) * mm, "end": v(28.84, -87.65) * mm});
            skLineSegment(sketch, "E6675", {"start": v(28.84, -87.65) * mm, "end": v(22.94, -81.6) * mm});
            skLineSegment(sketch, "E6676", {"start": v(22.94, -81.6) * mm, "end": v(17.24, -75.5) * mm});
            skLineSegment(sketch, "E6677", {"start": v(17.24, -75.5) * mm, "end": v(11.74, -69.42) * mm});
            skLineSegment(sketch, "E6678", {"start": v(11.74, -69.42) * mm, "end": v(6.4, -63.36) * mm});
            skLineSegment(sketch, "E6679", {"start": v(6.4, -63.36) * mm, "end": v(1.23, -57.34) * mm});
            skLineSegment(sketch, "E6680", {"start": v(1.23, -57.34) * mm, "end": v(-3.81, -51.4) * mm});
            skLineSegment(sketch, "E6681", {"start": v(-3.81, -51.4) * mm, "end": v(-8.73, -45.57) * mm});
            skLineSegment(sketch, "E6682", {"start": v(-8.73, -45.57) * mm, "end": v(-13.55, -39.86) * mm});
            skLineSegment(sketch, "E6683", {"start": v(-13.55, -39.86) * mm, "end": v(-18.28, -34.31) * mm});
            skLineSegment(sketch, "E6684", {"start": v(-18.28, -34.31) * mm, "end": v(-22.95, -28.95) * mm});
            skLineSegment(sketch, "E6685", {"start": v(-22.95, -28.95) * mm, "end": v(-27.58, -23.79) * mm});
            skLineSegment(sketch, "E6686", {"start": v(-27.58, -23.79) * mm, "end": v(-32.17, -18.87) * mm});
            skLineSegment(sketch, "E6687", {"start": v(-32.17, -18.87) * mm, "end": v(-36.75, -14.21) * mm});
            skLineSegment(sketch, "E6688", {"start": v(-36.75, -14.21) * mm, "end": v(-41.34, -9.84) * mm});
            skLineSegment(sketch, "E6689", {"start": v(-41.34, -9.84) * mm, "end": v(-45.96, -5.79) * mm});
            skLineSegment(sketch, "E6690", {"start": v(-45.96, -5.79) * mm, "end": v(-50.61, -2.08) * mm});
            skLineSegment(sketch, "E6691", {"start": v(-50.61, -2.08) * mm, "end": v(-55.33, 1.27) * mm});
            skLineSegment(sketch, "E6692", {"start": v(-55.33, 1.27) * mm, "end": v(-60.13, 4.21) * mm});
            skLineSegment(sketch, "E6693", {"start": v(-60.13, 4.21) * mm, "end": v(-65.02, 6.74) * mm});
            skLineSegment(sketch, "E6694", {"start": v(-65.02, 6.74) * mm, "end": v(-70.03, 8.82) * mm});
            skLineSegment(sketch, "E6695", {"start": v(-70.03, 8.82) * mm, "end": v(-75.17, 10.42) * mm});
            skLineSegment(sketch, "E6696", {"start": v(-75.17, 10.42) * mm, "end": v(-80.47, 11.52) * mm});
            skLineSegment(sketch, "E6697", {"start": v(-80.47, 11.52) * mm, "end": v(-85.93, 12.1) * mm});
            skLineSegment(sketch, "E6698", {"start": v(-85.93, 12.1) * mm, "end": v(-90.17, 12.18) * mm});
            skLineSegment(sketch, "E6699", {"start": v(-90.17, 12.18) * mm, "end": v(-91.58, 12.11) * mm});
            skLineSegment(sketch, "E6700", {"start": v(-91.58, 12.11) * mm, "end": v(-92.85, 12.05) * mm});
            skLineSegment(sketch, "E6701", {"start": v(-92.85, 12.05) * mm, "end": v(-96.64, 11.78) * mm});
            skLineSegment(sketch, "E6702", {"start": v(-96.64, 11.78) * mm, "end": v(-101.32, 11.3) * mm});
            skLineSegment(sketch, "E6703", {"start": v(-101.32, 11.3) * mm, "end": v(-105.64, 10.64) * mm});
            skLineSegment(sketch, "E6704", {"start": v(-105.64, 10.64) * mm, "end": v(-109.62, 9.86) * mm});
            skLineSegment(sketch, "E6705", {"start": v(-109.62, 9.86) * mm, "end": v(-113.3, 8.94) * mm});
            skLineSegment(sketch, "E6706", {"start": v(-113.3, 8.94) * mm, "end": v(-116.7, 7.92) * mm});
            skLineSegment(sketch, "E6707", {"start": v(-116.7, 7.92) * mm, "end": v(-119.87, 6.78) * mm});
            skLineSegment(sketch, "E6708", {"start": v(-119.87, 6.78) * mm, "end": v(-122.82, 5.56) * mm});
            skLineSegment(sketch, "E6709", {"start": v(-122.82, 5.56) * mm, "end": v(-125.6, 4.25) * mm});
            skLineSegment(sketch, "E6710", {"start": v(-125.6, 4.25) * mm, "end": v(-128.2, 2.88) * mm});
            skLineSegment(sketch, "E6711", {"start": v(-128.2, 2.88) * mm, "end": v(-130.7, 1.46) * mm});
            skLineSegment(sketch, "E6712", {"start": v(-130.7, 1.46) * mm, "end": v(-133.09, -0.02) * mm});
            skLineSegment(sketch, "E6713", {"start": v(-133.09, -0.02) * mm, "end": v(-135.42, -1.53) * mm});
            skLineSegment(sketch, "E6714", {"start": v(-135.42, -1.53) * mm, "end": v(-137.7, -3.05) * mm});
            skLineSegment(sketch, "E6715", {"start": v(-137.7, -3.05) * mm, "end": v(-140, -4.59) * mm});
            skLineSegment(sketch, "E6716", {"start": v(-140, -4.59) * mm, "end": v(-142.31, -6.12) * mm});
            skLineSegment(sketch, "E6717", {"start": v(-142.31, -6.12) * mm, "end": v(-144.68, -7.64) * mm});
            skLineSegment(sketch, "E6718", {"start": v(-144.68, -7.64) * mm, "end": v(-147.14, -9.13) * mm});
            skLineSegment(sketch, "E6719", {"start": v(-147.14, -9.13) * mm, "end": v(-149.7, -10.58) * mm});
            skLineSegment(sketch, "E6720", {"start": v(-149.7, -10.58) * mm, "end": v(-152.41, -11.98) * mm});
            skLineSegment(sketch, "E6721", {"start": v(-152.41, -11.98) * mm, "end": v(-155.3, -13.32) * mm});
            skLineSegment(sketch, "E6722", {"start": v(-155.3, -13.32) * mm, "end": v(-158.39, -14.58) * mm});
            skLineSegment(sketch, "E6723", {"start": v(-158.39, -14.58) * mm, "end": v(-161.7, -15.76) * mm});
            skLineSegment(sketch, "E6724", {"start": v(-161.7, -15.76) * mm, "end": v(-165.3, -16.84) * mm});
            skLineSegment(sketch, "E6725", {"start": v(-165.3, -16.84) * mm, "end": v(-169.17, -17.8) * mm});
            skLineSegment(sketch, "E6726", {"start": v(-169.17, -17.8) * mm, "end": v(-173.37, -18.65) * mm});
            skLineSegment(sketch, "E6727", {"start": v(-173.37, -18.65) * mm, "end": v(-177.92, -19.37) * mm});
            skLineSegment(sketch, "E6728", {"start": v(-177.92, -19.37) * mm, "end": v(-182.85, -19.93) * mm});
            skLineSegment(sketch, "E6729", {"start": v(-182.85, -19.93) * mm, "end": v(-188.2, -20.34) * mm});
            skLineSegment(sketch, "E6730", {"start": v(-188.2, -20.34) * mm, "end": v(-193.98, -20.58) * mm});
            skLineSegment(sketch, "E6731", {"start": v(-193.98, -20.58) * mm, "end": v(-200.24, -20.64) * mm});
            skLineSegment(sketch, "E6732", {"start": v(-200.24, -20.64) * mm, "end": v(-205.3, -20.57) * mm});
            skLineSegment(sketch, "E6733", {"start": v(-205.3, -20.57) * mm, "end": v(-207, -20.51) * mm});
            skLineSegment(sketch, "E6734", {"start": v(-207, -20.51) * mm, "end": v(-211.35, -20.36) * mm});
            skLineSegment(sketch, "E6735", {"start": v(-211.35, -20.36) * mm, "end": v(-224.39, -18.9) * mm});
            skLineSegment(sketch, "E6736", {"start": v(-224.39, -18.9) * mm, "end": v(-241.67, -15.67) * mm});
            skLineSegment(sketch, "E6737", {"start": v(-241.67, -15.67) * mm, "end": v(-258.83, -11.4) * mm});
            skLineSegment(sketch, "E6738", {"start": v(-258.83, -11.4) * mm, "end": v(-275.85, -6.69) * mm});
            skLineSegment(sketch, "E6739", {"start": v(-275.85, -6.69) * mm, "end": v(-292.7, -2.15) * mm});
            skLineSegment(sketch, "E6740", {"start": v(-292.7, -2.15) * mm, "end": v(-309.38, 1.61) * mm});
            skLineSegment(sketch, "E6741", {"start": v(-309.38, 1.61) * mm, "end": v(-325.86, 4) * mm});
            skLineSegment(sketch, "E6742", {"start": v(-325.86, 4) * mm, "end": v(-338.06, 4.61) * mm});
            skLineSegment(sketch, "E6743", {"start": v(-338.06, 4.61) * mm, "end": v(-342.12, 4.41) * mm});
            skLineSegment(sketch, "E6744", {"start": v(-342.12, 4.41) * mm, "end": v(-344.34, 4.3) * mm});
            skLineSegment(sketch, "E6745", {"start": v(-344.34, 4.3) * mm, "end": v(-351.02, 4.02) * mm});
            skLineSegment(sketch, "E6746", {"start": v(-351.02, 4.02) * mm, "end": v(-358.62, 3.75) * mm});
            skLineSegment(sketch, "E6747", {"start": v(-358.62, 3.75) * mm, "end": v(-365.4, 3.63) * mm});
            skLineSegment(sketch, "E6748", {"start": v(-365.4, 3.63) * mm, "end": v(-371.86, 3.66) * mm});
            skLineSegment(sketch, "E6749", {"start": v(-371.86, 3.66) * mm, "end": v(-378.5, 3.85) * mm});
            skLineSegment(sketch, "E6750", {"start": v(-378.5, 3.85) * mm, "end": v(-385.79, 4.2) * mm});
            skLineSegment(sketch, "E6751", {"start": v(-385.79, 4.2) * mm, "end": v(-394.25, 4.72) * mm});
            skLineSegment(sketch, "E6752", {"start": v(-394.25, 4.72) * mm, "end": v(-401.84, 5.24) * mm});
            skLineSegment(sketch, "E6753", {"start": v(-401.84, 5.24) * mm, "end": v(-404.37, 5.42) * mm});
            skLineSegment(sketch, "E6754", {"start": v(-404.37, 5.42) * mm, "end": v(-405.78, 5.52) * mm});
            skLineSegment(sketch, "E6755", {"start": v(-405.78, 5.52) * mm, "end": v(-410.01, 5.89) * mm});
            skLineSegment(sketch, "E6756", {"start": v(-410.01, 5.89) * mm, "end": v(-415.94, 6.5) * mm});
            skLineSegment(sketch, "E6757", {"start": v(-415.94, 6.5) * mm, "end": v(-422.06, 7.22) * mm});
            skLineSegment(sketch, "E6758", {"start": v(-422.06, 7.22) * mm, "end": v(-428.29, 8.04) * mm});
            skLineSegment(sketch, "E6759", {"start": v(-428.29, 8.04) * mm, "end": v(-434.53, 8.93) * mm});
            skLineSegment(sketch, "E6760", {"start": v(-434.53, 8.93) * mm, "end": v(-440.7, 9.86) * mm});
            skLineSegment(sketch, "E6761", {"start": v(-440.7, 9.86) * mm, "end": v(-446.7, 10.82) * mm});
            skLineSegment(sketch, "E6762", {"start": v(-446.7, 10.82) * mm, "end": v(-452.45, 11.77) * mm});
            skLineSegment(sketch, "E6763", {"start": v(-452.45, 11.77) * mm, "end": v(-457.86, 12.7) * mm});
            skLineSegment(sketch, "E6764", {"start": v(-457.86, 12.7) * mm, "end": v(-462.84, 13.58) * mm});
            skLineSegment(sketch, "E6765", {"start": v(-462.84, 13.58) * mm, "end": v(-467.3, 14.4) * mm});
            skLineSegment(sketch, "E6766", {"start": v(-467.3, 14.4) * mm, "end": v(-471.15, 15.11) * mm});
            skLineSegment(sketch, "E6767", {"start": v(-471.15, 15.11) * mm, "end": v(-474.3, 15.7) * mm});
            skLineSegment(sketch, "E6768", {"start": v(-474.3, 15.7) * mm, "end": v(-476.66, 16.16) * mm});
            skLineSegment(sketch, "E6769", {"start": v(-476.66, 16.16) * mm, "end": v(-478.14, 16.45) * mm});
            skLineSegment(sketch, "E6770", {"start": v(-478.14, 16.45) * mm, "end": v(-478.65, 16.56) * mm});
            skLineSegment(sketch, "E6771", {"start": v(611.67, -318.5) * mm, "end": v(610.71, -318.42) * mm});
            skLineSegment(sketch, "E6772", {"start": v(610.71, -318.42) * mm, "end": v(607.85, -318.08) * mm});
            skLineSegment(sketch, "E6773", {"start": v(607.85, -318.08) * mm, "end": v(603.17, -317.38) * mm});
            skLineSegment(sketch, "E6774", {"start": v(603.17, -317.38) * mm, "end": v(597.7, -316.4) * mm});
            skLineSegment(sketch, "E6775", {"start": v(597.7, -316.4) * mm, "end": v(591.5, -315.17) * mm});
            skLineSegment(sketch, "E6776", {"start": v(591.5, -315.17) * mm, "end": v(584.58, -313.69) * mm});
            skLineSegment(sketch, "E6777", {"start": v(584.58, -313.69) * mm, "end": v(577.03, -311.98) * mm});
            skLineSegment(sketch, "E6778", {"start": v(577.03, -311.98) * mm, "end": v(568.89, -310.05) * mm});
            skLineSegment(sketch, "E6779", {"start": v(568.89, -310.05) * mm, "end": v(560.2, -307.92) * mm});
            skLineSegment(sketch, "E6780", {"start": v(560.2, -307.92) * mm, "end": v(551.02, -305.6) * mm});
            skLineSegment(sketch, "E6781", {"start": v(551.02, -305.6) * mm, "end": v(541.4, -303.11) * mm});
            skLineSegment(sketch, "E6782", {"start": v(541.4, -303.11) * mm, "end": v(531.4, -300.47) * mm});
            skLineSegment(sketch, "E6783", {"start": v(531.4, -300.47) * mm, "end": v(521.04, -297.68) * mm});
            skLineSegment(sketch, "E6784", {"start": v(521.04, -297.68) * mm, "end": v(510.4, -294.75) * mm});
            skLineSegment(sketch, "E6785", {"start": v(510.4, -294.75) * mm, "end": v(499.53, -291.72) * mm});
            skLineSegment(sketch, "E6786", {"start": v(499.53, -291.72) * mm, "end": v(488.47, -288.6) * mm});
            skLineSegment(sketch, "E6787", {"start": v(488.47, -288.6) * mm, "end": v(477.27, -285.37) * mm});
            skLineSegment(sketch, "E6788", {"start": v(477.27, -285.37) * mm, "end": v(465.99, -282.08) * mm});
            skLineSegment(sketch, "E6789", {"start": v(465.99, -282.08) * mm, "end": v(454.67, -278.74) * mm});
            skLineSegment(sketch, "E6790", {"start": v(454.67, -278.74) * mm, "end": v(443.37, -275.35) * mm});
            skLineSegment(sketch, "E6791", {"start": v(443.37, -275.35) * mm, "end": v(432.14, -271.94) * mm});
            skLineSegment(sketch, "E6792", {"start": v(432.14, -271.94) * mm, "end": v(421.03, -268.5) * mm});
            skLineSegment(sketch, "E6793", {"start": v(421.03, -268.5) * mm, "end": v(410.07, -265.08) * mm});
            skLineSegment(sketch, "E6794", {"start": v(410.07, -265.08) * mm, "end": v(399.35, -261.67) * mm});
            skLineSegment(sketch, "E6795", {"start": v(399.35, -261.67) * mm, "end": v(388.9, -258.3) * mm});
            skLineSegment(sketch, "E6796", {"start": v(388.9, -258.3) * mm, "end": v(378.76, -254.96) * mm});
            skLineSegment(sketch, "E6797", {"start": v(378.76, -254.96) * mm, "end": v(369, -251.69) * mm});
            skLineSegment(sketch, "E6798", {"start": v(369, -251.69) * mm, "end": v(359.65, -248.49) * mm});
            skLineSegment(sketch, "E6799", {"start": v(359.65, -248.49) * mm, "end": v(350.79, -245.38) * mm});
            skLineSegment(sketch, "E6800", {"start": v(350.79, -245.38) * mm, "end": v(342.44, -242.37) * mm});
            skLineSegment(sketch, "E6801", {"start": v(342.44, -242.37) * mm, "end": v(334.68, -239.48) * mm});
            skLineSegment(sketch, "E6802", {"start": v(334.68, -239.48) * mm, "end": v(327.54, -236.73) * mm});
            skLineSegment(sketch, "E6803", {"start": v(327.54, -236.73) * mm, "end": v(322.68, -234.78) * mm});
            skLineSegment(sketch, "E6804", {"start": v(322.68, -234.78) * mm, "end": v(321.07, -234.12) * mm});
            skLineSegment(sketch, "E6805", {"start": v(321.07, -234.12) * mm, "end": v(318.02, -232.85) * mm});
            skLineSegment(sketch, "E6806", {"start": v(318.02, -232.85) * mm, "end": v(308.94, -228.86) * mm});
            skLineSegment(sketch, "E6807", {"start": v(308.94, -228.86) * mm, "end": v(296.93, -223.24) * mm});
            skLineSegment(sketch, "E6808", {"start": v(296.93, -223.24) * mm, "end": v(284.98, -217.26) * mm});
            skLineSegment(sketch, "E6809", {"start": v(284.98, -217.26) * mm, "end": v(273.04, -210.95) * mm});
            skLineSegment(sketch, "E6810", {"start": v(273.04, -210.95) * mm, "end": v(261.03, -204.33) * mm});
            skLineSegment(sketch, "E6811", {"start": v(261.03, -204.33) * mm, "end": v(248.91, -197.4) * mm});
            skLineSegment(sketch, "E6812", {"start": v(248.91, -197.4) * mm, "end": v(236.6, -190.2) * mm});
            skLineSegment(sketch, "E6813", {"start": v(236.6, -190.2) * mm, "end": v(224.06, -182.74) * mm});
            skLineSegment(sketch, "E6814", {"start": v(224.06, -182.74) * mm, "end": v(211.21, -175.03) * mm});
            skLineSegment(sketch, "E6815", {"start": v(211.21, -175.03) * mm, "end": v(198, -167.1) * mm});
            skLineSegment(sketch, "E6816", {"start": v(198, -167.1) * mm, "end": v(184.35, -158.95) * mm});
            skLineSegment(sketch, "E6817", {"start": v(184.35, -158.95) * mm, "end": v(170.21, -150.6) * mm});
            skLineSegment(sketch, "E6818", {"start": v(170.21, -150.6) * mm, "end": v(155.53, -142.1) * mm});
            skLineSegment(sketch, "E6819", {"start": v(155.53, -142.1) * mm, "end": v(140.24, -133.43) * mm});
            skLineSegment(sketch, "E6820", {"start": v(140.24, -133.43) * mm, "end": v(124.27, -124.63) * mm});
            skLineSegment(sketch, "E6821", {"start": v(124.27, -124.63) * mm, "end": v(111.76, -117.9) * mm});
            skLineSegment(sketch, "E6822", {"start": v(111.76, -117.9) * mm, "end": v(107.57, -115.7) * mm});
            skLineSegment(sketch, "E6823", {"start": v(107.57, -115.7) * mm, "end": v(105.45, -114.6) * mm});
            skLineSegment(sketch, "E6824", {"start": v(105.45, -114.6) * mm, "end": v(99.2, -111.07) * mm});
            skLineSegment(sketch, "E6825", {"start": v(99.2, -111.07) * mm, "end": v(91.07, -106.13) * mm});
            skLineSegment(sketch, "E6826", {"start": v(91.07, -106.13) * mm, "end": v(83.17, -100.91) * mm});
            skLineSegment(sketch, "E6827", {"start": v(83.17, -100.91) * mm, "end": v(75.49, -95.44) * mm});
            skLineSegment(sketch, "E6828", {"start": v(75.49, -95.44) * mm, "end": v(68.02, -89.74) * mm});
            skLineSegment(sketch, "E6829", {"start": v(68.02, -89.74) * mm, "end": v(60.76, -83.85) * mm});
            skLineSegment(sketch, "E6830", {"start": v(60.76, -83.85) * mm, "end": v(53.7, -77.8) * mm});
            skLineSegment(sketch, "E6831", {"start": v(53.7, -77.8) * mm, "end": v(46.83, -71.61) * mm});
            skLineSegment(sketch, "E6832", {"start": v(46.83, -71.61) * mm, "end": v(40.14, -65.33) * mm});
            skLineSegment(sketch, "E6833", {"start": v(40.14, -65.33) * mm, "end": v(33.63, -58.97) * mm});
            skLineSegment(sketch, "E6834", {"start": v(33.63, -58.97) * mm, "end": v(27.29, -52.57) * mm});
            skLineSegment(sketch, "E6835", {"start": v(27.29, -52.57) * mm, "end": v(21.1, -46.15) * mm});
            skLineSegment(sketch, "E6836", {"start": v(21.1, -46.15) * mm, "end": v(15.07, -39.76) * mm});
            skLineSegment(sketch, "E6837", {"start": v(15.07, -39.76) * mm, "end": v(9.18, -33.4) * mm});
            skLineSegment(sketch, "E6838", {"start": v(9.18, -33.4) * mm, "end": v(3.43, -27.14) * mm});
            skLineSegment(sketch, "E6839", {"start": v(3.43, -27.14) * mm, "end": v(-2.2, -20.97) * mm});
            skLineSegment(sketch, "E6840", {"start": v(-2.2, -20.97) * mm, "end": v(-7.7, -14.95) * mm});
            skLineSegment(sketch, "E6841", {"start": v(-7.7, -14.95) * mm, "end": v(-13.1, -9.09) * mm});
            skLineSegment(sketch, "E6842", {"start": v(-13.1, -9.09) * mm, "end": v(-18.38, -3.42) * mm});
            skLineSegment(sketch, "E6843", {"start": v(-18.38, -3.42) * mm, "end": v(-23.57, 2.01) * mm});
            skLineSegment(sketch, "E6844", {"start": v(-23.57, 2.01) * mm, "end": v(-28.67, 7.19) * mm});
            skLineSegment(sketch, "E6845", {"start": v(-28.67, 7.19) * mm, "end": v(-33.69, 12.08) * mm});
            skLineSegment(sketch, "E6846", {"start": v(-33.69, 12.08) * mm, "end": v(-38.63, 16.65) * mm});
            skLineSegment(sketch, "E6847", {"start": v(-38.63, 16.65) * mm, "end": v(-43.5, 20.88) * mm});
            skLineSegment(sketch, "E6848", {"start": v(-43.5, 20.88) * mm, "end": v(-48.33, 24.73) * mm});
            skLineSegment(sketch, "E6849", {"start": v(-48.33, 24.73) * mm, "end": v(-53.1, 28.17) * mm});
            skLineSegment(sketch, "E6850", {"start": v(-53.1, 28.17) * mm, "end": v(-57.82, 31.18) * mm});
            skLineSegment(sketch, "E6851", {"start": v(-57.82, 31.18) * mm, "end": v(-62.51, 33.71) * mm});
            skLineSegment(sketch, "E6852", {"start": v(-62.51, 33.71) * mm, "end": v(-67.18, 35.75) * mm});
            skLineSegment(sketch, "E6853", {"start": v(-67.18, 35.75) * mm, "end": v(-71.82, 37.26) * mm});
            skLineSegment(sketch, "E6854", {"start": v(-71.82, 37.26) * mm, "end": v(-76.46, 38.22) * mm});
            skLineSegment(sketch, "E6855", {"start": v(-76.46, 38.22) * mm, "end": v(-79.92, 38.57) * mm});
            skLineSegment(sketch, "E6856", {"start": v(-79.92, 38.57) * mm, "end": v(-81.08, 38.59) * mm});
            skLineSegment(sketch, "E6857", {"start": v(-81.08, 38.59) * mm, "end": v(-83.55, 38.63) * mm});
            skLineSegment(sketch, "E6858", {"start": v(-83.55, 38.63) * mm, "end": v(-90.96, 38.37) * mm});
            skLineSegment(sketch, "E6859", {"start": v(-90.96, 38.37) * mm, "end": v(-99.6, 37.45) * mm});
            skLineSegment(sketch, "E6860", {"start": v(-99.6, 37.45) * mm, "end": v(-107.2, 35.95) * mm});
            skLineSegment(sketch, "E6861", {"start": v(-107.2, 35.95) * mm, "end": v(-114, 33.96) * mm});
            skLineSegment(sketch, "E6862", {"start": v(-114, 33.96) * mm, "end": v(-120.17, 31.6) * mm});
            skLineSegment(sketch, "E6863", {"start": v(-120.17, 31.6) * mm, "end": v(-125.94, 28.94) * mm});
            skLineSegment(sketch, "E6864", {"start": v(-125.94, 28.94) * mm, "end": v(-131.5, 26.1) * mm});
            skLineSegment(sketch, "E6865", {"start": v(-131.5, 26.1) * mm, "end": v(-137.1, 23.19) * mm});
            skLineSegment(sketch, "E6866", {"start": v(-137.1, 23.19) * mm, "end": v(-142.89, 20.29) * mm});
            skLineSegment(sketch, "E6867", {"start": v(-142.89, 20.29) * mm, "end": v(-149.1, 17.51) * mm});
            skLineSegment(sketch, "E6868", {"start": v(-149.1, 17.51) * mm, "end": v(-155.96, 14.96) * mm});
            skLineSegment(sketch, "E6869", {"start": v(-155.96, 14.96) * mm, "end": v(-163.66, 12.73) * mm});
            skLineSegment(sketch, "E6870", {"start": v(-163.66, 12.73) * mm, "end": v(-172.4, 10.92) * mm});
            skLineSegment(sketch, "E6871", {"start": v(-172.4, 10.92) * mm, "end": v(-182.4, 9.64) * mm});
            skLineSegment(sketch, "E6872", {"start": v(-182.4, 9.64) * mm, "end": v(-193.87, 8.99) * mm});
            skLineSegment(sketch, "E6873", {"start": v(-193.87, 8.99) * mm, "end": v(-203.72, 8.95) * mm});
            skLineSegment(sketch, "E6874", {"start": v(-203.72, 8.95) * mm, "end": v(-207, 9.06) * mm});
            skLineSegment(sketch, "E6875", {"start": v(-207, 9.06) * mm, "end": v(-211.35, 9.2) * mm});
            skLineSegment(sketch, "E6876", {"start": v(-211.35, 9.2) * mm, "end": v(-224.39, 10.67) * mm});
            skLineSegment(sketch, "E6877", {"start": v(-224.39, 10.67) * mm, "end": v(-241.67, 13.9) * mm});
            skLineSegment(sketch, "E6878", {"start": v(-241.67, 13.9) * mm, "end": v(-258.83, 18.18) * mm});
            skLineSegment(sketch, "E6879", {"start": v(-258.83, 18.18) * mm, "end": v(-275.85, 22.88) * mm});
            skLineSegment(sketch, "E6880", {"start": v(-275.85, 22.88) * mm, "end": v(-292.7, 27.42) * mm});
            skLineSegment(sketch, "E6881", {"start": v(-292.7, 27.42) * mm, "end": v(-309.38, 31.18) * mm});
            skLineSegment(sketch, "E6882", {"start": v(-309.38, 31.18) * mm, "end": v(-325.86, 33.57) * mm});
            skLineSegment(sketch, "E6883", {"start": v(-325.86, 33.57) * mm, "end": v(-338.06, 34.18) * mm});
            skLineSegment(sketch, "E6884", {"start": v(-338.06, 34.18) * mm, "end": v(-342.12, 33.98) * mm});
            skLineSegment(sketch, "E6885", {"start": v(-342.12, 33.98) * mm, "end": v(-344.31, 33.88) * mm});
            skLineSegment(sketch, "E6886", {"start": v(-344.31, 33.88) * mm, "end": v(-350.9, 33.54) * mm});
            skLineSegment(sketch, "E6887", {"start": v(-350.9, 33.54) * mm, "end": v(-358.1, 33.13) * mm});
            skLineSegment(sketch, "E6888", {"start": v(-358.1, 33.13) * mm, "end": v(-364.25, 32.78) * mm});
            skLineSegment(sketch, "E6889", {"start": v(-364.25, 32.78) * mm, "end": v(-369.84, 32.5) * mm});
            skLineSegment(sketch, "E6890", {"start": v(-369.84, 32.5) * mm, "end": v(-375.39, 32.3) * mm});
            skLineSegment(sketch, "E6891", {"start": v(-375.39, 32.3) * mm, "end": v(-381.4, 32.18) * mm});
            skLineSegment(sketch, "E6892", {"start": v(-381.4, 32.18) * mm, "end": v(-388.37, 32.16) * mm});
            skLineSegment(sketch, "E6893", {"start": v(-388.37, 32.16) * mm, "end": v(-394.7, 32.2) * mm});
            skLineSegment(sketch, "E6894", {"start": v(-394.7, 32.2) * mm, "end": v(-396.82, 32.24) * mm});
            skLineSegment(sketch, "E6895", {"start": v(-396.82, 32.24) * mm, "end": v(-398.2, 32.26) * mm});
            skLineSegment(sketch, "E6896", {"start": v(-398.2, 32.26) * mm, "end": v(-402.38, 32.42) * mm});
            skLineSegment(sketch, "E6897", {"start": v(-402.38, 32.42) * mm, "end": v(-408.56, 32.77) * mm});
            skLineSegment(sketch, "E6898", {"start": v(-408.56, 32.77) * mm, "end": v(-415.22, 33.28) * mm});
            skLineSegment(sketch, "E6899", {"start": v(-415.22, 33.28) * mm, "end": v(-422.24, 33.9) * mm});
            skLineSegment(sketch, "E6900", {"start": v(-422.24, 33.9) * mm, "end": v(-429.48, 34.64) * mm});
            skLineSegment(sketch, "E6901", {"start": v(-429.48, 34.64) * mm, "end": v(-436.8, 35.45) * mm});
            skLineSegment(sketch, "E6902", {"start": v(-436.8, 35.45) * mm, "end": v(-444.06, 36.3) * mm});
            skLineSegment(sketch, "E6903", {"start": v(-444.06, 36.3) * mm, "end": v(-451.14, 37.17) * mm});
            skLineSegment(sketch, "E6904", {"start": v(-451.14, 37.17) * mm, "end": v(-457.89, 38.03) * mm});
            skLineSegment(sketch, "E6905", {"start": v(-457.89, 38.03) * mm, "end": v(-464.18, 38.87) * mm});
            skLineSegment(sketch, "E6906", {"start": v(-464.18, 38.87) * mm, "end": v(-469.87, 39.64) * mm});
            skLineSegment(sketch, "E6907", {"start": v(-469.87, 39.64) * mm, "end": v(-474.83, 40.34) * mm});
            skLineSegment(sketch, "E6908", {"start": v(-474.83, 40.34) * mm, "end": v(-478.93, 40.92) * mm});
            skLineSegment(sketch, "E6909", {"start": v(-478.93, 40.92) * mm, "end": v(-482.02, 41.37) * mm});
            skLineSegment(sketch, "E6910", {"start": v(-482.02, 41.37) * mm, "end": v(-483.98, 41.66) * mm});
            skLineSegment(sketch, "E6911", {"start": v(-483.98, 41.66) * mm, "end": v(-484.66, 41.76) * mm});
            skLineSegment(sketch, "E6912", {"start": v(611.67, -296.2) * mm, "end": v(607.36, -295.23) * mm});
            skLineSegment(sketch, "E6913", {"start": v(607.36, -295.23) * mm, "end": v(594.47, -292.24) * mm});
            skLineSegment(sketch, "E6914", {"start": v(594.47, -292.24) * mm, "end": v(576.33, -287.87) * mm});
            skLineSegment(sketch, "E6915", {"start": v(576.33, -287.87) * mm, "end": v(557.45, -283.1) * mm});
            skLineSegment(sketch, "E6916", {"start": v(557.45, -283.1) * mm, "end": v(537.98, -277.98) * mm});
            skLineSegment(sketch, "E6917", {"start": v(537.98, -277.98) * mm, "end": v(518.1, -272.54) * mm});
            skLineSegment(sketch, "E6918", {"start": v(518.1, -272.54) * mm, "end": v(498, -266.83) * mm});
            skLineSegment(sketch, "E6919", {"start": v(498, -266.83) * mm, "end": v(477.82, -260.9) * mm});
            skLineSegment(sketch, "E6920", {"start": v(477.82, -260.9) * mm, "end": v(457.74, -254.76) * mm});
            skLineSegment(sketch, "E6921", {"start": v(457.74, -254.76) * mm, "end": v(437.95, -248.48) * mm});
            skLineSegment(sketch, "E6922", {"start": v(437.95, -248.48) * mm, "end": v(418.6, -242.08) * mm});
            skLineSegment(sketch, "E6923", {"start": v(418.6, -242.08) * mm, "end": v(399.88, -235.62) * mm});
            skLineSegment(sketch, "E6924", {"start": v(399.88, -235.62) * mm, "end": v(381.95, -229.11) * mm});
            skLineSegment(sketch, "E6925", {"start": v(381.95, -229.11) * mm, "end": v(364.99, -222.62) * mm});
            skLineSegment(sketch, "E6926", {"start": v(364.99, -222.62) * mm, "end": v(349.16, -216.18) * mm});
            skLineSegment(sketch, "E6927", {"start": v(349.16, -216.18) * mm, "end": v(334.64, -209.82) * mm});
            skLineSegment(sketch, "E6928", {"start": v(334.64, -209.82) * mm, "end": v(324.84, -205.21) * mm});
            skLineSegment(sketch, "E6929", {"start": v(324.84, -205.21) * mm, "end": v(321.61, -203.6) * mm});
            skLineSegment(sketch, "E6930", {"start": v(321.61, -203.6) * mm, "end": v(318.4, -201.98) * mm});
            skLineSegment(sketch, "E6931", {"start": v(318.4, -201.98) * mm, "end": v(308.78, -197.1) * mm});
            skLineSegment(sketch, "E6932", {"start": v(308.78, -197.1) * mm, "end": v(295.85, -190.47) * mm});
            skLineSegment(sketch, "E6933", {"start": v(295.85, -190.47) * mm, "end": v(282.82, -183.7) * mm});
            skLineSegment(sketch, "E6934", {"start": v(282.82, -183.7) * mm, "end": v(269.66, -176.76) * mm});
            skLineSegment(sketch, "E6935", {"start": v(269.66, -176.76) * mm, "end": v(256.35, -169.65) * mm});
            skLineSegment(sketch, "E6936", {"start": v(256.35, -169.65) * mm, "end": v(242.87, -162.35) * mm});
            skLineSegment(sketch, "E6937", {"start": v(242.87, -162.35) * mm, "end": v(229.2, -154.85) * mm});
            skLineSegment(sketch, "E6938", {"start": v(229.2, -154.85) * mm, "end": v(215.33, -147.12) * mm});
            skLineSegment(sketch, "E6939", {"start": v(215.33, -147.12) * mm, "end": v(201.23, -139.17) * mm});
            skLineSegment(sketch, "E6940", {"start": v(201.23, -139.17) * mm, "end": v(186.89, -130.96) * mm});
            skLineSegment(sketch, "E6941", {"start": v(186.89, -130.96) * mm, "end": v(172.28, -122.5) * mm});
            skLineSegment(sketch, "E6942", {"start": v(172.28, -122.5) * mm, "end": v(157.39, -113.75) * mm});
            skLineSegment(sketch, "E6943", {"start": v(157.39, -113.75) * mm, "end": v(142.2, -104.71) * mm});
            skLineSegment(sketch, "E6944", {"start": v(142.2, -104.71) * mm, "end": v(126.68, -95.37) * mm});
            skLineSegment(sketch, "E6945", {"start": v(126.68, -95.37) * mm, "end": v(110.82, -85.7) * mm});
            skLineSegment(sketch, "E6946", {"start": v(110.82, -85.7) * mm, "end": v(98.65, -78.22) * mm});
            skLineSegment(sketch, "E6947", {"start": v(98.65, -78.22) * mm, "end": v(94.6, -75.7) * mm});
            skLineSegment(sketch, "E6948", {"start": v(94.6, -75.7) * mm, "end": v(92.63, -74.49) * mm});
            skLineSegment(sketch, "E6949", {"start": v(92.63, -74.49) * mm, "end": v(86.8, -70.68) * mm});
            skLineSegment(sketch, "E6950", {"start": v(86.8, -70.68) * mm, "end": v(79.38, -65.52) * mm});
            skLineSegment(sketch, "E6951", {"start": v(79.38, -65.52) * mm, "end": v(72.34, -60.26) * mm});
            skLineSegment(sketch, "E6952", {"start": v(72.34, -60.26) * mm, "end": v(65.64, -54.9) * mm});
            skLineSegment(sketch, "E6953", {"start": v(65.64, -54.9) * mm, "end": v(59.26, -49.49) * mm});
            skLineSegment(sketch, "E6954", {"start": v(59.26, -49.49) * mm, "end": v(53.2, -44.01) * mm});
            skLineSegment(sketch, "E6955", {"start": v(53.2, -44.01) * mm, "end": v(47.4, -38.5) * mm});
            skLineSegment(sketch, "E6956", {"start": v(47.4, -38.5) * mm, "end": v(41.87, -32.98) * mm});
            skLineSegment(sketch, "E6957", {"start": v(41.87, -32.98) * mm, "end": v(36.6, -27.46) * mm});
            skLineSegment(sketch, "E6958", {"start": v(36.6, -27.46) * mm, "end": v(31.52, -21.95) * mm});
            skLineSegment(sketch, "E6959", {"start": v(31.52, -21.95) * mm, "end": v(26.66, -16.5) * mm});
            skLineSegment(sketch, "E6960", {"start": v(26.66, -16.5) * mm, "end": v(21.96, -11.08) * mm});
            skLineSegment(sketch, "E6961", {"start": v(21.96, -11.08) * mm, "end": v(17.43, -5.75) * mm});
            skLineSegment(sketch, "E6962", {"start": v(17.43, -5.75) * mm, "end": v(13.03, -0.52) * mm});
            skLineSegment(sketch, "E6963", {"start": v(13.03, -0.52) * mm, "end": v(8.74, 4.6) * mm});
            skLineSegment(sketch, "E6964", {"start": v(8.74, 4.6) * mm, "end": v(4.55, 9.6) * mm});
            skLineSegment(sketch, "E6965", {"start": v(4.55, 9.6) * mm, "end": v(0.43, 14.45) * mm});
            skLineSegment(sketch, "E6966", {"start": v(0.43, 14.45) * mm, "end": v(-3.64, 19.13) * mm});
            skLineSegment(sketch, "E6967", {"start": v(-3.64, 19.13) * mm, "end": v(-7.68, 23.62) * mm});
            skLineSegment(sketch, "E6968", {"start": v(-7.68, 23.62) * mm, "end": v(-11.7, 27.91) * mm});
            skLineSegment(sketch, "E6969", {"start": v(-11.7, 27.91) * mm, "end": v(-15.75, 31.98) * mm});
            skLineSegment(sketch, "E6970", {"start": v(-15.75, 31.98) * mm, "end": v(-19.83, 35.8) * mm});
            skLineSegment(sketch, "E6971", {"start": v(-19.83, 35.8) * mm, "end": v(-23.96, 39.38) * mm});
            skLineSegment(sketch, "E6972", {"start": v(-23.96, 39.38) * mm, "end": v(-28.17, 42.67) * mm});
            skLineSegment(sketch, "E6973", {"start": v(-28.17, 42.67) * mm, "end": v(-32.48, 45.67) * mm});
            skLineSegment(sketch, "E6974", {"start": v(-32.48, 45.67) * mm, "end": v(-36.9, 48.36) * mm});
            skLineSegment(sketch, "E6975", {"start": v(-36.9, 48.36) * mm, "end": v(-41.46, 50.72) * mm});
            skLineSegment(sketch, "E6976", {"start": v(-41.46, 50.72) * mm, "end": v(-46.18, 52.72) * mm});
            skLineSegment(sketch, "E6977", {"start": v(-46.18, 52.72) * mm, "end": v(-51.09, 54.36) * mm});
            skLineSegment(sketch, "E6978", {"start": v(-51.09, 54.36) * mm, "end": v(-56.2, 55.61) * mm});
            skLineSegment(sketch, "E6979", {"start": v(-56.2, 55.61) * mm, "end": v(-61.52, 56.46) * mm});
            skLineSegment(sketch, "E6980", {"start": v(-61.52, 56.46) * mm, "end": v(-65.7, 56.84) * mm});
            skLineSegment(sketch, "E6981", {"start": v(-65.7, 56.84) * mm, "end": v(-67.1, 56.89) * mm});
            skLineSegment(sketch, "E6982", {"start": v(-67.1, 56.89) * mm, "end": v(-69.6, 56.98) * mm});
            skLineSegment(sketch, "E6983", {"start": v(-69.6, 56.98) * mm, "end": v(-77.13, 56.9) * mm});
            skLineSegment(sketch, "E6984", {"start": v(-77.13, 56.9) * mm, "end": v(-86.2, 56.2) * mm});
            skLineSegment(sketch, "E6985", {"start": v(-86.2, 56.2) * mm, "end": v(-94.5, 54.9) * mm});
            skLineSegment(sketch, "E6986", {"start": v(-94.5, 54.9) * mm, "end": v(-102.18, 53.13) * mm});
            skLineSegment(sketch, "E6987", {"start": v(-102.18, 53.13) * mm, "end": v(-109.41, 50.95) * mm});
            skLineSegment(sketch, "E6988", {"start": v(-109.41, 50.95) * mm, "end": v(-116.36, 48.48) * mm});
            skLineSegment(sketch, "E6989", {"start": v(-116.36, 48.48) * mm, "end": v(-123.2, 45.8) * mm});
            skLineSegment(sketch, "E6990", {"start": v(-123.2, 45.8) * mm, "end": v(-130.08, 43.04) * mm});
            skLineSegment(sketch, "E6991", {"start": v(-130.08, 43.04) * mm, "end": v(-137.19, 40.28) * mm});
            skLineSegment(sketch, "E6992", {"start": v(-137.19, 40.28) * mm, "end": v(-144.67, 37.63) * mm});
            skLineSegment(sketch, "E6993", {"start": v(-144.67, 37.63) * mm, "end": v(-152.71, 35.19) * mm});
            skLineSegment(sketch, "E6994", {"start": v(-152.71, 35.19) * mm, "end": v(-161.47, 33.05) * mm});
            skLineSegment(sketch, "E6995", {"start": v(-161.47, 33.05) * mm, "end": v(-171.11, 31.31) * mm});
            skLineSegment(sketch, "E6996", {"start": v(-171.11, 31.31) * mm, "end": v(-181.8, 30.08) * mm});
            skLineSegment(sketch, "E6997", {"start": v(-181.8, 30.08) * mm, "end": v(-193.71, 29.46) * mm});
            skLineSegment(sketch, "E6998", {"start": v(-193.71, 29.46) * mm, "end": v(-203.68, 29.43) * mm});
            skLineSegment(sketch, "E6999", {"start": v(-203.68, 29.43) * mm, "end": v(-207, 29.54) * mm});
            skLineSegment(sketch, "E7000", {"start": v(-207, 29.54) * mm, "end": v(-211.35, 29.69) * mm});
            skLineSegment(sketch, "E7001", {"start": v(-211.35, 29.69) * mm, "end": v(-224.39, 31.15) * mm});
            skLineSegment(sketch, "E7002", {"start": v(-224.39, 31.15) * mm, "end": v(-241.67, 34.39) * mm});
            skLineSegment(sketch, "E7003", {"start": v(-241.67, 34.39) * mm, "end": v(-258.83, 38.66) * mm});
            skLineSegment(sketch, "E7004", {"start": v(-258.83, 38.66) * mm, "end": v(-275.85, 43.37) * mm});
            skLineSegment(sketch, "E7005", {"start": v(-275.85, 43.37) * mm, "end": v(-292.7, 47.9) * mm});
            skLineSegment(sketch, "E7006", {"start": v(-292.7, 47.9) * mm, "end": v(-309.38, 51.66) * mm});
            skLineSegment(sketch, "E7007", {"start": v(-309.38, 51.66) * mm, "end": v(-325.86, 54.05) * mm});
            skLineSegment(sketch, "E7008", {"start": v(-325.86, 54.05) * mm, "end": v(-338.06, 54.66) * mm});
            skLineSegment(sketch, "E7009", {"start": v(-338.06, 54.66) * mm, "end": v(-342.12, 54.46) * mm});
            skLineSegment(sketch, "E7010", {"start": v(-342.12, 54.46) * mm, "end": v(-344.4, 54.36) * mm});
            skLineSegment(sketch, "E7011", {"start": v(-344.4, 54.36) * mm, "end": v(-351.23, 54) * mm});
            skLineSegment(sketch, "E7012", {"start": v(-351.23, 54) * mm, "end": v(-359.32, 53.58) * mm});
            skLineSegment(sketch, "E7013", {"start": v(-359.32, 53.58) * mm, "end": v(-366.7, 53.26) * mm});
            skLineSegment(sketch, "E7014", {"start": v(-366.7, 53.26) * mm, "end": v(-373.72, 53.1) * mm});
            skLineSegment(sketch, "E7015", {"start": v(-373.72, 53.1) * mm, "end": v(-380.67, 53.19) * mm});
            skLineSegment(sketch, "E7016", {"start": v(-380.67, 53.19) * mm, "end": v(-387.88, 53.57) * mm});
            skLineSegment(sketch, "E7017", {"start": v(-387.88, 53.57) * mm, "end": v(-395.67, 54.3) * mm});
            skLineSegment(sketch, "E7018", {"start": v(-395.67, 54.3) * mm, "end": v(-402.2, 55.14) * mm});
            skLineSegment(sketch, "E7019", {"start": v(-402.2, 55.14) * mm, "end": v(-404.37, 55.47) * mm});
            skLineSegment(sketch, "E7020", {"start": v(-404.37, 55.47) * mm, "end": v(-405.8, 55.69) * mm});
            skLineSegment(sketch, "E7021", {"start": v(-405.8, 55.69) * mm, "end": v(-410.08, 56.32) * mm});
            skLineSegment(sketch, "E7022", {"start": v(-410.08, 56.32) * mm, "end": v(-416.3, 57.2) * mm});
            skLineSegment(sketch, "E7023", {"start": v(-416.3, 57.2) * mm, "end": v(-422.9, 58.12) * mm});
            skLineSegment(sketch, "E7024", {"start": v(-422.9, 58.12) * mm, "end": v(-429.76, 59.05) * mm});
            skLineSegment(sketch, "E7025", {"start": v(-429.76, 59.05) * mm, "end": v(-436.76, 60) * mm});
            skLineSegment(sketch, "E7026", {"start": v(-436.76, 60) * mm, "end": v(-443.78, 60.91) * mm});
            skLineSegment(sketch, "E7027", {"start": v(-443.78, 60.91) * mm, "end": v(-450.7, 61.82) * mm});
            skLineSegment(sketch, "E7028", {"start": v(-450.7, 61.82) * mm, "end": v(-457.41, 62.68) * mm});
            skLineSegment(sketch, "E7029", {"start": v(-457.41, 62.68) * mm, "end": v(-463.78, 63.49) * mm});
            skLineSegment(sketch, "E7030", {"start": v(-463.78, 63.49) * mm, "end": v(-469.69, 64.24) * mm});
            skLineSegment(sketch, "E7031", {"start": v(-469.69, 64.24) * mm, "end": v(-475.02, 64.9) * mm});
            skLineSegment(sketch, "E7032", {"start": v(-475.02, 64.9) * mm, "end": v(-479.65, 65.48) * mm});
            skLineSegment(sketch, "E7033", {"start": v(-479.65, 65.48) * mm, "end": v(-483.46, 65.96) * mm});
            skLineSegment(sketch, "E7034", {"start": v(-483.46, 65.96) * mm, "end": v(-486.33, 66.3) * mm});
            skLineSegment(sketch, "E7035", {"start": v(-486.33, 66.3) * mm, "end": v(-488.14, 66.54) * mm});
            skLineSegment(sketch, "E7036", {"start": v(-488.14, 66.54) * mm, "end": v(-488.76, 66.6) * mm});
            skLineSegment(sketch, "E7037", {"start": v(613.18, -473.64) * mm, "end": v(612.15, -473.56) * mm});
            skLineSegment(sketch, "E7038", {"start": v(612.15, -473.56) * mm, "end": v(609.04, -473.17) * mm});
            skLineSegment(sketch, "E7039", {"start": v(609.04, -473.17) * mm, "end": v(603.43, -472.3) * mm});
            skLineSegment(sketch, "E7040", {"start": v(603.43, -472.3) * mm, "end": v(596.45, -471.04) * mm});
            skLineSegment(sketch, "E7041", {"start": v(596.45, -471.04) * mm, "end": v(588.2, -469.43) * mm});
            skLineSegment(sketch, "E7042", {"start": v(588.2, -469.43) * mm, "end": v(578.75, -467.48) * mm});
            skLineSegment(sketch, "E7043", {"start": v(578.75, -467.48) * mm, "end": v(568.2, -465.23) * mm});
            skLineSegment(sketch, "E7044", {"start": v(568.2, -465.23) * mm, "end": v(556.66, -462.7) * mm});
            skLineSegment(sketch, "E7045", {"start": v(556.66, -462.7) * mm, "end": v(544.2, -459.9) * mm});
            skLineSegment(sketch, "E7046", {"start": v(544.2, -459.9) * mm, "end": v(530.9, -456.84) * mm});
            skLineSegment(sketch, "E7047", {"start": v(530.9, -456.84) * mm, "end": v(516.89, -453.58) * mm});
            skLineSegment(sketch, "E7048", {"start": v(516.89, -453.58) * mm, "end": v(502.24, -450.12) * mm});
            skLineSegment(sketch, "E7049", {"start": v(502.24, -450.12) * mm, "end": v(487.03, -446.5) * mm});
            skLineSegment(sketch, "E7050", {"start": v(487.03, -446.5) * mm, "end": v(471.37, -442.71) * mm});
            skLineSegment(sketch, "E7051", {"start": v(471.37, -442.71) * mm, "end": v(455.35, -438.8) * mm});
            skLineSegment(sketch, "E7052", {"start": v(455.35, -438.8) * mm, "end": v(439.05, -434.8) * mm});
            skLineSegment(sketch, "E7053", {"start": v(439.05, -434.8) * mm, "end": v(422.57, -430.71) * mm});
            skLineSegment(sketch, "E7054", {"start": v(422.57, -430.71) * mm, "end": v(406, -426.57) * mm});
            skLineSegment(sketch, "E7055", {"start": v(406, -426.57) * mm, "end": v(389.44, -422.38) * mm});
            skLineSegment(sketch, "E7056", {"start": v(389.44, -422.38) * mm, "end": v(372.96, -418.2) * mm});
            skLineSegment(sketch, "E7057", {"start": v(372.96, -418.2) * mm, "end": v(356.67, -414.01) * mm});
            skLineSegment(sketch, "E7058", {"start": v(356.67, -414.01) * mm, "end": v(340.66, -409.86) * mm});
            skLineSegment(sketch, "E7059", {"start": v(340.66, -409.86) * mm, "end": v(325, -405.78) * mm});
            skLineSegment(sketch, "E7060", {"start": v(325, -405.78) * mm, "end": v(309.82, -401.77) * mm});
            skLineSegment(sketch, "E7061", {"start": v(309.82, -401.77) * mm, "end": v(295.18, -397.86) * mm});
            skLineSegment(sketch, "E7062", {"start": v(295.18, -397.86) * mm, "end": v(281.18, -394.08) * mm});
            skLineSegment(sketch, "E7063", {"start": v(281.18, -394.08) * mm, "end": v(267.92, -390.45) * mm});
            skLineSegment(sketch, "E7064", {"start": v(267.92, -390.45) * mm, "end": v(255.48, -387) * mm});
            skLineSegment(sketch, "E7065", {"start": v(255.48, -387) * mm, "end": v(243.96, -383.73) * mm});
            skLineSegment(sketch, "E7066", {"start": v(243.96, -383.73) * mm, "end": v(233.45, -380.7) * mm});
            skLineSegment(sketch, "E7067", {"start": v(233.45, -380.7) * mm, "end": v(224.03, -377.89) * mm});
            skLineSegment(sketch, "E7068", {"start": v(224.03, -377.89) * mm, "end": v(215.8, -375.35) * mm});
            skLineSegment(sketch, "E7069", {"start": v(215.8, -375.35) * mm, "end": v(210.6, -373.68) * mm});
            skLineSegment(sketch, "E7070", {"start": v(210.6, -373.68) * mm, "end": v(208.87, -373.1) * mm});
            skLineSegment(sketch, "E7071", {"start": v(208.87, -373.1) * mm, "end": v(206.15, -372.19) * mm});
            skLineSegment(sketch, "E7072", {"start": v(206.15, -372.19) * mm, "end": v(198.05, -369.35) * mm});
            skLineSegment(sketch, "E7073", {"start": v(198.05, -369.35) * mm, "end": v(187.86, -365.57) * mm});
            skLineSegment(sketch, "E7074", {"start": v(187.86, -365.57) * mm, "end": v(178.28, -361.76) * mm});
            skLineSegment(sketch, "E7075", {"start": v(178.28, -361.76) * mm, "end": v(169.26, -357.92) * mm});
            skLineSegment(sketch, "E7076", {"start": v(169.26, -357.92) * mm, "end": v(160.79, -354.07) * mm});
            skLineSegment(sketch, "E7077", {"start": v(160.79, -354.07) * mm, "end": v(152.84, -350.2) * mm});
            skLineSegment(sketch, "E7078", {"start": v(152.84, -350.2) * mm, "end": v(145.37, -346.33) * mm});
            skLineSegment(sketch, "E7079", {"start": v(145.37, -346.33) * mm, "end": v(138.37, -342.46) * mm});
            skLineSegment(sketch, "E7080", {"start": v(138.37, -342.46) * mm, "end": v(131.81, -338.6) * mm});
            skLineSegment(sketch, "E7081", {"start": v(131.81, -338.6) * mm, "end": v(125.66, -334.73) * mm});
            skLineSegment(sketch, "E7082", {"start": v(125.66, -334.73) * mm, "end": v(119.88, -330.88) * mm});
            skLineSegment(sketch, "E7083", {"start": v(119.88, -330.88) * mm, "end": v(114.47, -327.05) * mm});
            skLineSegment(sketch, "E7084", {"start": v(114.47, -327.05) * mm, "end": v(109.38, -323.25) * mm});
            skLineSegment(sketch, "E7085", {"start": v(109.38, -323.25) * mm, "end": v(104.6, -319.48) * mm});
            skLineSegment(sketch, "E7086", {"start": v(104.6, -319.48) * mm, "end": v(100.07, -315.74) * mm});
            skLineSegment(sketch, "E7087", {"start": v(100.07, -315.74) * mm, "end": v(95.8, -312.04) * mm});
            skLineSegment(sketch, "E7088", {"start": v(95.8, -312.04) * mm, "end": v(91.76, -308.39) * mm});
            skLineSegment(sketch, "E7089", {"start": v(91.76, -308.39) * mm, "end": v(87.9, -304.8) * mm});
            skLineSegment(sketch, "E7090", {"start": v(87.9, -304.8) * mm, "end": v(84.2, -301.25) * mm});
            skLineSegment(sketch, "E7091", {"start": v(84.2, -301.25) * mm, "end": v(80.65, -297.77) * mm});
            skLineSegment(sketch, "E7092", {"start": v(80.65, -297.77) * mm, "end": v(77.21, -294.36) * mm});
            skLineSegment(sketch, "E7093", {"start": v(77.21, -294.36) * mm, "end": v(73.85, -291.02) * mm});
            skLineSegment(sketch, "E7094", {"start": v(73.85, -291.02) * mm, "end": v(70.55, -287.76) * mm});
            skLineSegment(sketch, "E7095", {"start": v(70.55, -287.76) * mm, "end": v(67.27, -284.59) * mm});
            skLineSegment(sketch, "E7096", {"start": v(67.27, -284.59) * mm, "end": v(64, -281.5) * mm});
            skLineSegment(sketch, "E7097", {"start": v(64, -281.5) * mm, "end": v(60.7, -278.51) * mm});
            skLineSegment(sketch, "E7098", {"start": v(60.7, -278.51) * mm, "end": v(57.36, -275.62) * mm});
            skLineSegment(sketch, "E7099", {"start": v(57.36, -275.62) * mm, "end": v(53.93, -272.83) * mm});
            skLineSegment(sketch, "E7100", {"start": v(53.93, -272.83) * mm, "end": v(50.4, -270.16) * mm});
            skLineSegment(sketch, "E7101", {"start": v(50.4, -270.16) * mm, "end": v(46.73, -267.6) * mm});
            skLineSegment(sketch, "E7102", {"start": v(46.73, -267.6) * mm, "end": v(42.9, -265.16) * mm});
            skLineSegment(sketch, "E7103", {"start": v(42.9, -265.16) * mm, "end": v(39.9, -263.4) * mm});
            skLineSegment(sketch, "E7104", {"start": v(39.9, -263.4) * mm, "end": v(38.89, -262.85) * mm});
            skLineSegment(sketch, "E7105", {"start": v(38.89, -262.85) * mm, "end": v(36.8, -261.7) * mm});
            skLineSegment(sketch, "E7106", {"start": v(36.8, -261.7) * mm, "end": v(30.6, -258.16) * mm});
            skLineSegment(sketch, "E7107", {"start": v(30.6, -258.16) * mm, "end": v(22.64, -253.35) * mm});
            skLineSegment(sketch, "E7108", {"start": v(22.64, -253.35) * mm, "end": v(15.01, -248.44) * mm});
            skLineSegment(sketch, "E7109", {"start": v(15.01, -248.44) * mm, "end": v(7.72, -243.45) * mm});
            skLineSegment(sketch, "E7110", {"start": v(7.72, -243.45) * mm, "end": v(0.73, -238.38) * mm});
            skLineSegment(sketch, "E7111", {"start": v(0.73, -238.38) * mm, "end": v(-5.96, -233.26) * mm});
            skLineSegment(sketch, "E7112", {"start": v(-5.96, -233.26) * mm, "end": v(-12.36, -228.1) * mm});
            skLineSegment(sketch, "E7113", {"start": v(-12.36, -228.1) * mm, "end": v(-18.47, -222.9) * mm});
            skLineSegment(sketch, "E7114", {"start": v(-18.47, -222.9) * mm, "end": v(-24.31, -217.7) * mm});
            skLineSegment(sketch, "E7115", {"start": v(-24.31, -217.7) * mm, "end": v(-29.9, -212.5) * mm});
            skLineSegment(sketch, "E7116", {"start": v(-29.9, -212.5) * mm, "end": v(-35.23, -207.33) * mm});
            skLineSegment(sketch, "E7117", {"start": v(-35.23, -207.33) * mm, "end": v(-40.33, -202.19) * mm});
            skLineSegment(sketch, "E7118", {"start": v(-40.33, -202.19) * mm, "end": v(-45.2, -197.1) * mm});
            skLineSegment(sketch, "E7119", {"start": v(-45.2, -197.1) * mm, "end": v(-49.84, -192.09) * mm});
            skLineSegment(sketch, "E7120", {"start": v(-49.84, -192.09) * mm, "end": v(-54.28, -187.15) * mm});
            skLineSegment(sketch, "E7121", {"start": v(-54.28, -187.15) * mm, "end": v(-58.52, -182.32) * mm});
            skLineSegment(sketch, "E7122", {"start": v(-58.52, -182.32) * mm, "end": v(-62.58, -177.6) * mm});
            skLineSegment(sketch, "E7123", {"start": v(-62.58, -177.6) * mm, "end": v(-66.45, -173) * mm});
            skLineSegment(sketch, "E7124", {"start": v(-66.45, -173) * mm, "end": v(-70.16, -168.56) * mm});
            skLineSegment(sketch, "E7125", {"start": v(-70.16, -168.56) * mm, "end": v(-73.72, -164.27) * mm});
            skLineSegment(sketch, "E7126", {"start": v(-73.72, -164.27) * mm, "end": v(-77.13, -160.16) * mm});
            skLineSegment(sketch, "E7127", {"start": v(-77.13, -160.16) * mm, "end": v(-80.4, -156.24) * mm});
            skLineSegment(sketch, "E7128", {"start": v(-80.4, -156.24) * mm, "end": v(-83.54, -152.53) * mm});
            skLineSegment(sketch, "E7129", {"start": v(-83.54, -152.53) * mm, "end": v(-86.58, -149.04) * mm});
            skLineSegment(sketch, "E7130", {"start": v(-86.58, -149.04) * mm, "end": v(-89.5, -145.79) * mm});
            skLineSegment(sketch, "E7131", {"start": v(-89.5, -145.79) * mm, "end": v(-92.34, -142.8) * mm});
            skLineSegment(sketch, "E7132", {"start": v(-92.34, -142.8) * mm, "end": v(-95.09, -140.07) * mm});
            skLineSegment(sketch, "E7133", {"start": v(-95.09, -140.07) * mm, "end": v(-97.76, -137.62) * mm});
            skLineSegment(sketch, "E7134", {"start": v(-97.76, -137.62) * mm, "end": v(-100.38, -135.48) * mm});
            skLineSegment(sketch, "E7135", {"start": v(-100.38, -135.48) * mm, "end": v(-102.94, -133.65) * mm});
            skLineSegment(sketch, "E7136", {"start": v(-102.94, -133.65) * mm, "end": v(-105.45, -132.16) * mm});
            skLineSegment(sketch, "E7137", {"start": v(-105.45, -132.16) * mm, "end": v(-107.3, -131.26) * mm});
            skLineSegment(sketch, "E7138", {"start": v(-107.3, -131.26) * mm, "end": v(-107.94, -131) * mm});
            skLineSegment(sketch, "E7139", {"start": v(-107.94, -131) * mm, "end": v(-109.16, -130.53) * mm});
            skLineSegment(sketch, "E7140", {"start": v(-109.16, -130.53) * mm, "end": v(-112.93, -129.42) * mm});
            skLineSegment(sketch, "E7141", {"start": v(-112.93, -129.42) * mm, "end": v(-118, -128.48) * mm});
            skLineSegment(sketch, "E7142", {"start": v(-118, -128.48) * mm, "end": v(-123.16, -128.13) * mm});
            skLineSegment(sketch, "E7143", {"start": v(-123.16, -128.13) * mm, "end": v(-128.4, -128.28) * mm});
            skLineSegment(sketch, "E7144", {"start": v(-128.4, -128.28) * mm, "end": v(-133.72, -128.86) * mm});
            skLineSegment(sketch, "E7145", {"start": v(-133.72, -128.86) * mm, "end": v(-139.11, -129.82) * mm});
            skLineSegment(sketch, "E7146", {"start": v(-139.11, -129.82) * mm, "end": v(-144.58, -131.06) * mm});
            skLineSegment(sketch, "E7147", {"start": v(-144.58, -131.06) * mm, "end": v(-150.12, -132.53) * mm});
            skLineSegment(sketch, "E7148", {"start": v(-150.12, -132.53) * mm, "end": v(-155.73, -134.14) * mm});
            skLineSegment(sketch, "E7149", {"start": v(-155.73, -134.14) * mm, "end": v(-161.4, -135.83) * mm});
            skLineSegment(sketch, "E7150", {"start": v(-161.4, -135.83) * mm, "end": v(-167.15, -137.51) * mm});
            skLineSegment(sketch, "E7151", {"start": v(-167.15, -137.51) * mm, "end": v(-172.96, -139.13) * mm});
            skLineSegment(sketch, "E7152", {"start": v(-172.96, -139.13) * mm, "end": v(-178.83, -140.6) * mm});
            skLineSegment(sketch, "E7153", {"start": v(-178.83, -140.6) * mm, "end": v(-184.76, -141.86) * mm});
            skLineSegment(sketch, "E7154", {"start": v(-184.76, -141.86) * mm, "end": v(-190.75, -142.83) * mm});
            skLineSegment(sketch, "E7155", {"start": v(-190.75, -142.83) * mm, "end": v(-195.28, -143.34) * mm});
            skLineSegment(sketch, "E7156", {"start": v(-195.28, -143.34) * mm, "end": v(-196.8, -143.44) * mm});
            skLineSegment(sketch, "E7157", {"start": v(-196.8, -143.44) * mm, "end": v(-201.03, -143.72) * mm});
            skLineSegment(sketch, "E7158", {"start": v(-201.03, -143.72) * mm, "end": v(-213.78, -144.22) * mm});
            skLineSegment(sketch, "E7159", {"start": v(-213.78, -144.22) * mm, "end": v(-230.14, -144.3) * mm});
            skLineSegment(sketch, "E7160", {"start": v(-230.14, -144.3) * mm, "end": v(-245.84, -143.76) * mm});
            skLineSegment(sketch, "E7161", {"start": v(-245.84, -143.76) * mm, "end": v(-260.84, -142.69) * mm});
            skLineSegment(sketch, "E7162", {"start": v(-260.84, -142.69) * mm, "end": v(-275.14, -141.18) * mm});
            skLineSegment(sketch, "E7163", {"start": v(-275.14, -141.18) * mm, "end": v(-288.68, -139.31) * mm});
            skLineSegment(sketch, "E7164", {"start": v(-288.68, -139.31) * mm, "end": v(-301.45, -137.19) * mm});
            skLineSegment(sketch, "E7165", {"start": v(-301.45, -137.19) * mm, "end": v(-313.4, -134.88) * mm});
            skLineSegment(sketch, "E7166", {"start": v(-313.4, -134.88) * mm, "end": v(-324.53, -132.47) * mm});
            skLineSegment(sketch, "E7167", {"start": v(-324.53, -132.47) * mm, "end": v(-334.78, -130.07) * mm});
            skLineSegment(sketch, "E7168", {"start": v(-334.78, -130.07) * mm, "end": v(-344.15, -127.74) * mm});
            skLineSegment(sketch, "E7169", {"start": v(-344.15, -127.74) * mm, "end": v(-352.58, -125.58) * mm});
            skLineSegment(sketch, "E7170", {"start": v(-352.58, -125.58) * mm, "end": v(-360.06, -123.68) * mm});
            skLineSegment(sketch, "E7171", {"start": v(-360.06, -123.68) * mm, "end": v(-366.55, -122.12) * mm});
            skLineSegment(sketch, "E7172", {"start": v(-366.55, -122.12) * mm, "end": v(-372.03, -121) * mm});
            skLineSegment(sketch, "E7173", {"start": v(-372.03, -121) * mm, "end": v(-375.35, -120.47) * mm});
            skLineSegment(sketch, "E7174", {"start": v(-375.35, -120.47) * mm, "end": v(-376.47, -120.38) * mm});
            skLineSegment(sketch, "E7175", {"start": v(-376.47, -120.38) * mm, "end": v(-377.75, -120.27) * mm});
            skLineSegment(sketch, "E7176", {"start": v(-377.75, -120.27) * mm, "end": v(-381.58, -120) * mm});
            skLineSegment(sketch, "E7177", {"start": v(-381.58, -120) * mm, "end": v(-387.13, -119.65) * mm});
            skLineSegment(sketch, "E7178", {"start": v(-387.13, -119.65) * mm, "end": v(-393.01, -119.34) * mm});
            skLineSegment(sketch, "E7179", {"start": v(-393.01, -119.34) * mm, "end": v(-399.12, -119.07) * mm});
            skLineSegment(sketch, "E7180", {"start": v(-399.12, -119.07) * mm, "end": v(-405.35, -118.83) * mm});
            skLineSegment(sketch, "E7181", {"start": v(-405.35, -118.83) * mm, "end": v(-411.6, -118.62) * mm});
            skLineSegment(sketch, "E7182", {"start": v(-411.6, -118.62) * mm, "end": v(-417.76, -118.44) * mm});
            skLineSegment(sketch, "E7183", {"start": v(-417.76, -118.44) * mm, "end": v(-423.72, -118.29) * mm});
            skLineSegment(sketch, "E7184", {"start": v(-423.72, -118.29) * mm, "end": v(-429.38, -118.16) * mm});
            skLineSegment(sketch, "E7185", {"start": v(-429.38, -118.16) * mm, "end": v(-434.62, -118.06) * mm});
            skLineSegment(sketch, "E7186", {"start": v(-434.62, -118.06) * mm, "end": v(-439.35, -117.97) * mm});
            skLineSegment(sketch, "E7187", {"start": v(-439.35, -117.97) * mm, "end": v(-443.46, -117.9) * mm});
            skLineSegment(sketch, "E7188", {"start": v(-443.46, -117.9) * mm, "end": v(-446.84, -117.86) * mm});
            skLineSegment(sketch, "E7189", {"start": v(-446.84, -117.86) * mm, "end": v(-449.39, -117.83) * mm});
            skLineSegment(sketch, "E7190", {"start": v(-449.39, -117.83) * mm, "end": v(-451, -117.82) * mm});
            skLineSegment(sketch, "E7191", {"start": v(-451, -117.82) * mm, "end": v(-451.55, -117.81) * mm});
            skLineSegment(sketch, "E7192", {"start": v(612.4, -450) * mm, "end": v(611.42, -449.93) * mm});
            skLineSegment(sketch, "E7193", {"start": v(611.42, -449.93) * mm, "end": v(608.47, -449.59) * mm});
            skLineSegment(sketch, "E7194", {"start": v(608.47, -449.59) * mm, "end": v(603.47, -448.87) * mm});
            skLineSegment(sketch, "E7195", {"start": v(603.47, -448.87) * mm, "end": v(597.48, -447.87) * mm});
            skLineSegment(sketch, "E7196", {"start": v(597.48, -447.87) * mm, "end": v(590.55, -446.6) * mm});
            skLineSegment(sketch, "E7197", {"start": v(590.55, -446.6) * mm, "end": v(582.75, -445.1) * mm});
            skLineSegment(sketch, "E7198", {"start": v(582.75, -445.1) * mm, "end": v(574.16, -443.35) * mm});
            skLineSegment(sketch, "E7199", {"start": v(574.16, -443.35) * mm, "end": v(564.82, -441.39) * mm});
            skLineSegment(sketch, "E7200", {"start": v(564.82, -441.39) * mm, "end": v(554.8, -439.22) * mm});
            skLineSegment(sketch, "E7201", {"start": v(554.8, -439.22) * mm, "end": v(544.2, -436.87) * mm});
            skLineSegment(sketch, "E7202", {"start": v(544.2, -436.87) * mm, "end": v(533.03, -434.35) * mm});
            skLineSegment(sketch, "E7203", {"start": v(533.03, -434.35) * mm, "end": v(521.4, -431.67) * mm});
            skLineSegment(sketch, "E7204", {"start": v(521.4, -431.67) * mm, "end": v(509.34, -428.85) * mm});
            skLineSegment(sketch, "E7205", {"start": v(509.34, -428.85) * mm, "end": v(496.94, -425.9) * mm});
            skLineSegment(sketch, "E7206", {"start": v(496.94, -425.9) * mm, "end": v(484.26, -422.86) * mm});
            skLineSegment(sketch, "E7207", {"start": v(484.26, -422.86) * mm, "end": v(471.35, -419.72) * mm});
            skLineSegment(sketch, "E7208", {"start": v(471.35, -419.72) * mm, "end": v(458.3, -416.5) * mm});
            skLineSegment(sketch, "E7209", {"start": v(458.3, -416.5) * mm, "end": v(445.15, -413.23) * mm});
            skLineSegment(sketch, "E7210", {"start": v(445.15, -413.23) * mm, "end": v(431.98, -409.91) * mm});
            skLineSegment(sketch, "E7211", {"start": v(431.98, -409.91) * mm, "end": v(418.84, -406.57) * mm});
            skLineSegment(sketch, "E7212", {"start": v(418.84, -406.57) * mm, "end": v(405.82, -403.2) * mm});
            skLineSegment(sketch, "E7213", {"start": v(405.82, -403.2) * mm, "end": v(392.96, -399.85) * mm});
            skLineSegment(sketch, "E7214", {"start": v(392.96, -399.85) * mm, "end": v(380.34, -396.51) * mm});
            skLineSegment(sketch, "E7215", {"start": v(380.34, -396.51) * mm, "end": v(368.02, -393.2) * mm});
            skLineSegment(sketch, "E7216", {"start": v(368.02, -393.2) * mm, "end": v(356.06, -389.96) * mm});
            skLineSegment(sketch, "E7217", {"start": v(356.06, -389.96) * mm, "end": v(344.54, -386.77) * mm});
            skLineSegment(sketch, "E7218", {"start": v(344.54, -386.77) * mm, "end": v(333.5, -383.67) * mm});
            skLineSegment(sketch, "E7219", {"start": v(333.5, -383.67) * mm, "end": v(323.03, -380.66) * mm});
            skLineSegment(sketch, "E7220", {"start": v(323.03, -380.66) * mm, "end": v(313.18, -377.77) * mm});
            skLineSegment(sketch, "E7221", {"start": v(313.18, -377.77) * mm, "end": v(304.02, -375.01) * mm});
            skLineSegment(sketch, "E7222", {"start": v(304.02, -375.01) * mm, "end": v(295.6, -372.4) * mm});
            skLineSegment(sketch, "E7223", {"start": v(295.6, -372.4) * mm, "end": v(288.02, -369.94) * mm});
            skLineSegment(sketch, "E7224", {"start": v(288.02, -369.94) * mm, "end": v(282.99, -368.25) * mm});
            skLineSegment(sketch, "E7225", {"start": v(282.99, -368.25) * mm, "end": v(281.31, -367.67) * mm});
            skLineSegment(sketch, "E7226", {"start": v(281.31, -367.67) * mm, "end": v(279.82, -367.14) * mm});
            skLineSegment(sketch, "E7227", {"start": v(279.82, -367.14) * mm, "end": v(275.3, -365.67) * mm});
            skLineSegment(sketch, "E7228", {"start": v(275.3, -365.67) * mm, "end": v(269.28, -363.84) * mm});
            skLineSegment(sketch, "E7229", {"start": v(269.28, -363.84) * mm, "end": v(263.19, -362.09) * mm});
            skLineSegment(sketch, "E7230", {"start": v(263.19, -362.09) * mm, "end": v(256.96, -360.35) * mm});
            skLineSegment(sketch, "E7231", {"start": v(256.96, -360.35) * mm, "end": v(250.55, -358.54) * mm});
            skLineSegment(sketch, "E7232", {"start": v(250.55, -358.54) * mm, "end": v(243.9, -356.58) * mm});
            skLineSegment(sketch, "E7233", {"start": v(243.9, -356.58) * mm, "end": v(236.95, -354.39) * mm});
            skLineSegment(sketch, "E7234", {"start": v(236.95, -354.39) * mm, "end": v(229.66, -351.88) * mm});
            skLineSegment(sketch, "E7235", {"start": v(229.66, -351.88) * mm, "end": v(221.96, -349) * mm});
            skLineSegment(sketch, "E7236", {"start": v(221.96, -349) * mm, "end": v(213.8, -345.65) * mm});
            skLineSegment(sketch, "E7237", {"start": v(213.8, -345.65) * mm, "end": v(205.12, -341.75) * mm});
            skLineSegment(sketch, "E7238", {"start": v(205.12, -341.75) * mm, "end": v(195.88, -337.23) * mm});
            skLineSegment(sketch, "E7239", {"start": v(195.88, -337.23) * mm, "end": v(186, -332.01) * mm});
            skLineSegment(sketch, "E7240", {"start": v(186, -332.01) * mm, "end": v(175.46, -326.01) * mm});
            skLineSegment(sketch, "E7241", {"start": v(175.46, -326.01) * mm, "end": v(164.18, -319.16) * mm});
            skLineSegment(sketch, "E7242", {"start": v(164.18, -319.16) * mm, "end": v(155.1, -313.35) * mm});
            skLineSegment(sketch, "E7243", {"start": v(155.1, -313.35) * mm, "end": v(152.1, -311.36) * mm});
            skLineSegment(sketch, "E7244", {"start": v(152.1, -311.36) * mm, "end": v(151.12, -310.71) * mm});
            skLineSegment(sketch, "E7245", {"start": v(151.12, -310.71) * mm, "end": v(148.3, -308.57) * mm});
            skLineSegment(sketch, "E7246", {"start": v(148.3, -308.57) * mm, "end": v(143.72, -304.76) * mm});
            skLineSegment(sketch, "E7247", {"start": v(143.72, -304.76) * mm, "end": v(138.47, -300.1) * mm});
            skLineSegment(sketch, "E7248", {"start": v(138.47, -300.1) * mm, "end": v(132.69, -294.7) * mm});
            skLineSegment(sketch, "E7249", {"start": v(132.69, -294.7) * mm, "end": v(126.47, -288.76) * mm});
            skLineSegment(sketch, "E7250", {"start": v(126.47, -288.76) * mm, "end": v(119.94, -282.39) * mm});
            skLineSegment(sketch, "E7251", {"start": v(119.94, -282.39) * mm, "end": v(113.22, -275.76) * mm});
            skLineSegment(sketch, "E7252", {"start": v(113.22, -275.76) * mm, "end": v(106.42, -269.01) * mm});
            skLineSegment(sketch, "E7253", {"start": v(106.42, -269.01) * mm, "end": v(99.67, -262.3) * mm});
            skLineSegment(sketch, "E7254", {"start": v(99.67, -262.3) * mm, "end": v(93.08, -255.77) * mm});
            skLineSegment(sketch, "E7255", {"start": v(93.08, -255.77) * mm, "end": v(86.77, -249.58) * mm});
            skLineSegment(sketch, "E7256", {"start": v(86.77, -249.58) * mm, "end": v(80.85, -243.86) * mm});
            skLineSegment(sketch, "E7257", {"start": v(80.85, -243.86) * mm, "end": v(75.45, -238.78) * mm});
            skLineSegment(sketch, "E7258", {"start": v(75.45, -238.78) * mm, "end": v(70.68, -234.47) * mm});
            skLineSegment(sketch, "E7259", {"start": v(70.68, -234.47) * mm, "end": v(66.66, -231.1) * mm});
            skLineSegment(sketch, "E7260", {"start": v(66.66, -231.1) * mm, "end": v(64.32, -229.33) * mm});
            skLineSegment(sketch, "E7261", {"start": v(64.32, -229.33) * mm, "end": v(63.5, -228.81) * mm});
            skLineSegment(sketch, "E7262", {"start": v(63.5, -228.81) * mm, "end": v(59.16, -226.06) * mm});
            skLineSegment(sketch, "E7263", {"start": v(59.16, -226.06) * mm, "end": v(46.31, -217.55) * mm});
            skLineSegment(sketch, "E7264", {"start": v(46.31, -217.55) * mm, "end": v(30.28, -206.35) * mm});
            skLineSegment(sketch, "E7265", {"start": v(30.28, -206.35) * mm, "end": v(15.35, -195.3) * mm});
            skLineSegment(sketch, "E7266", {"start": v(15.35, -195.3) * mm, "end": v(1.47, -184.47) * mm});
            skLineSegment(sketch, "E7267", {"start": v(1.47, -184.47) * mm, "end": v(-11.4, -173.93) * mm});
            skLineSegment(sketch, "E7268", {"start": v(-11.4, -173.93) * mm, "end": v(-23.32, -163.76) * mm});
            skLineSegment(sketch, "E7269", {"start": v(-23.32, -163.76) * mm, "end": v(-34.33, -154.02) * mm});
            skLineSegment(sketch, "E7270", {"start": v(-34.33, -154.02) * mm, "end": v(-44.49, -144.8) * mm});
            skLineSegment(sketch, "E7271", {"start": v(-44.49, -144.8) * mm, "end": v(-53.84, -136.15) * mm});
            skLineSegment(sketch, "E7272", {"start": v(-53.84, -136.15) * mm, "end": v(-62.45, -128.17) * mm});
            skLineSegment(sketch, "E7273", {"start": v(-62.45, -128.17) * mm, "end": v(-70.36, -120.9) * mm});
            skLineSegment(sketch, "E7274", {"start": v(-70.36, -120.9) * mm, "end": v(-77.61, -114.46) * mm});
            skLineSegment(sketch, "E7275", {"start": v(-77.61, -114.46) * mm, "end": v(-84.27, -108.88) * mm});
            skLineSegment(sketch, "E7276", {"start": v(-84.27, -108.88) * mm, "end": v(-90.37, -104.25) * mm});
            skLineSegment(sketch, "E7277", {"start": v(-90.37, -104.25) * mm, "end": v(-95.98, -100.64) * mm});
            skLineSegment(sketch, "E7278", {"start": v(-95.98, -100.64) * mm, "end": v(-99.8, -98.65) * mm});
            skLineSegment(sketch, "E7279", {"start": v(-99.8, -98.65) * mm, "end": v(-101.13, -98.13) * mm});
            skLineSegment(sketch, "E7280", {"start": v(-101.13, -98.13) * mm, "end": v(-102.36, -97.65) * mm});
            skLineSegment(sketch, "E7281", {"start": v(-102.36, -97.65) * mm, "end": v(-106.24, -96.65) * mm});
            skLineSegment(sketch, "E7282", {"start": v(-106.24, -96.65) * mm, "end": v(-111.65, -96) * mm});
            skLineSegment(sketch, "E7283", {"start": v(-111.65, -96) * mm, "end": v(-117.33, -96.1) * mm});
            skLineSegment(sketch, "E7284", {"start": v(-117.33, -96.1) * mm, "end": v(-123.24, -96.84) * mm});
            skLineSegment(sketch, "E7285", {"start": v(-123.24, -96.84) * mm, "end": v(-129.36, -98.1) * mm});
            skLineSegment(sketch, "E7286", {"start": v(-129.36, -98.1) * mm, "end": v(-135.65, -99.8) * mm});
            skLineSegment(sketch, "E7287", {"start": v(-135.65, -99.8) * mm, "end": v(-142.08, -101.84) * mm});
            skLineSegment(sketch, "E7288", {"start": v(-142.08, -101.84) * mm, "end": v(-148.61, -104.09) * mm});
            skLineSegment(sketch, "E7289", {"start": v(-148.61, -104.09) * mm, "end": v(-155.21, -106.46) * mm});
            skLineSegment(sketch, "E7290", {"start": v(-155.21, -106.46) * mm, "end": v(-161.86, -108.85) * mm});
            skLineSegment(sketch, "E7291", {"start": v(-161.86, -108.85) * mm, "end": v(-168.5, -111.16) * mm});
            skLineSegment(sketch, "E7292", {"start": v(-168.5, -111.16) * mm, "end": v(-175.12, -113.28) * mm});
            skLineSegment(sketch, "E7293", {"start": v(-175.12, -113.28) * mm, "end": v(-181.67, -115.1) * mm});
            skLineSegment(sketch, "E7294", {"start": v(-181.67, -115.1) * mm, "end": v(-188.14, -116.54) * mm});
            skLineSegment(sketch, "E7295", {"start": v(-188.14, -116.54) * mm, "end": v(-194.47, -117.48) * mm});
            skLineSegment(sketch, "E7296", {"start": v(-194.47, -117.48) * mm, "end": v(-199.1, -117.81) * mm});
            skLineSegment(sketch, "E7297", {"start": v(-199.1, -117.81) * mm, "end": v(-200.65, -117.81) * mm});
            skLineSegment(sketch, "E7298", {"start": v(-200.65, -117.81) * mm, "end": v(-202.6, -117.81) * mm});
            skLineSegment(sketch, "E7299", {"start": v(-202.6, -117.81) * mm, "end": v(-208.42, -117.76) * mm});
            skLineSegment(sketch, "E7300", {"start": v(-208.42, -117.76) * mm, "end": v(-217.44, -117.56) * mm});
            skLineSegment(sketch, "E7301", {"start": v(-217.44, -117.56) * mm, "end": v(-227.64, -117.13) * mm});
            skLineSegment(sketch, "E7302", {"start": v(-227.64, -117.13) * mm, "end": v(-238.9, -116.4) * mm});
            skLineSegment(sketch, "E7303", {"start": v(-238.9, -116.4) * mm, "end": v(-251.15, -115.3) * mm});
            skLineSegment(sketch, "E7304", {"start": v(-251.15, -115.3) * mm, "end": v(-264.27, -113.72) * mm});
            skLineSegment(sketch, "E7305", {"start": v(-264.27, -113.72) * mm, "end": v(-278.17, -111.6) * mm});
            skLineSegment(sketch, "E7306", {"start": v(-278.17, -111.6) * mm, "end": v(-289.12, -109.62) * mm});
            skLineSegment(sketch, "E7307", {"start": v(-289.12, -109.62) * mm, "end": v(-292.75, -108.88) * mm});
            skLineSegment(sketch, "E7308", {"start": v(-292.75, -108.88) * mm, "end": v(-296.27, -108.15) * mm});
            skLineSegment(sketch, "E7309", {"start": v(-296.27, -108.15) * mm, "end": v(-306.88, -106.15) * mm});
            skLineSegment(sketch, "E7310", {"start": v(-306.88, -106.15) * mm, "end": v(-321.21, -103.72) * mm});
            skLineSegment(sketch, "E7311", {"start": v(-321.21, -103.72) * mm, "end": v(-335.6, -101.56) * mm});
            skLineSegment(sketch, "E7312", {"start": v(-335.6, -101.56) * mm, "end": v(-349.86, -99.66) * mm});
            skLineSegment(sketch, "E7313", {"start": v(-349.86, -99.66) * mm, "end": v(-363.86, -98.01) * mm});
            skLineSegment(sketch, "E7314", {"start": v(-363.86, -98.01) * mm, "end": v(-377.46, -96.59) * mm});
            skLineSegment(sketch, "E7315", {"start": v(-377.46, -96.59) * mm, "end": v(-390.48, -95.38) * mm});
            skLineSegment(sketch, "E7316", {"start": v(-390.48, -95.38) * mm, "end": v(-402.78, -94.36) * mm});
            skLineSegment(sketch, "E7317", {"start": v(-402.78, -94.36) * mm, "end": v(-414.21, -93.52) * mm});
            skLineSegment(sketch, "E7318", {"start": v(-414.21, -93.52) * mm, "end": v(-424.62, -92.85) * mm});
            skLineSegment(sketch, "E7319", {"start": v(-424.62, -92.85) * mm, "end": v(-433.84, -92.33) * mm});
            skLineSegment(sketch, "E7320", {"start": v(-433.84, -92.33) * mm, "end": v(-441.72, -91.93) * mm});
            skLineSegment(sketch, "E7321", {"start": v(-441.72, -91.93) * mm, "end": v(-448.13, -91.65) * mm});
            skLineSegment(sketch, "E7322", {"start": v(-448.13, -91.65) * mm, "end": v(-452.89, -91.48) * mm});
            skLineSegment(sketch, "E7323", {"start": v(-452.89, -91.48) * mm, "end": v(-455.86, -91.38) * mm});
            skLineSegment(sketch, "E7324", {"start": v(-455.86, -91.38) * mm, "end": v(-456.88, -91.35) * mm});
            skLineSegment(sketch, "E7325", {"start": v(611.1, -421.79) * mm, "end": v(610.13, -421.7) * mm});
            skLineSegment(sketch, "E7326", {"start": v(610.13, -421.7) * mm, "end": v(607.23, -421.38) * mm});
            skLineSegment(sketch, "E7327", {"start": v(607.23, -421.38) * mm, "end": v(602.42, -420.72) * mm});
            skLineSegment(sketch, "E7328", {"start": v(602.42, -420.72) * mm, "end": v(596.73, -419.8) * mm});
            skLineSegment(sketch, "E7329", {"start": v(596.73, -419.8) * mm, "end": v(590.22, -418.65) * mm});
            skLineSegment(sketch, "E7330", {"start": v(590.22, -418.65) * mm, "end": v(582.94, -417.28) * mm});
            skLineSegment(sketch, "E7331", {"start": v(582.94, -417.28) * mm, "end": v(574.95, -415.7) * mm});
            skLineSegment(sketch, "E7332", {"start": v(574.95, -415.7) * mm, "end": v(566.3, -413.92) * mm});
            skLineSegment(sketch, "E7333", {"start": v(566.3, -413.92) * mm, "end": v(557.06, -411.96) * mm});
            skLineSegment(sketch, "E7334", {"start": v(557.06, -411.96) * mm, "end": v(547.27, -409.83) * mm});
            skLineSegment(sketch, "E7335", {"start": v(547.27, -409.83) * mm, "end": v(537, -407.55) * mm});
            skLineSegment(sketch, "E7336", {"start": v(537, -407.55) * mm, "end": v(526.3, -405.13) * mm});
            skLineSegment(sketch, "E7337", {"start": v(526.3, -405.13) * mm, "end": v(515.23, -402.57) * mm});
            skLineSegment(sketch, "E7338", {"start": v(515.23, -402.57) * mm, "end": v(503.84, -399.9) * mm});
            skLineSegment(sketch, "E7339", {"start": v(503.84, -399.9) * mm, "end": v(492.2, -397.14) * mm});
            skLineSegment(sketch, "E7340", {"start": v(492.2, -397.14) * mm, "end": v(480.35, -394.28) * mm});
            skLineSegment(sketch, "E7341", {"start": v(480.35, -394.28) * mm, "end": v(468.35, -391.36) * mm});
            skLineSegment(sketch, "E7342", {"start": v(468.35, -391.36) * mm, "end": v(456.27, -388.37) * mm});
            skLineSegment(sketch, "E7343", {"start": v(456.27, -388.37) * mm, "end": v(444.16, -385.33) * mm});
            skLineSegment(sketch, "E7344", {"start": v(444.16, -385.33) * mm, "end": v(432.06, -382.27) * mm});
            skLineSegment(sketch, "E7345", {"start": v(432.06, -382.27) * mm, "end": v(420.05, -379.18) * mm});
            skLineSegment(sketch, "E7346", {"start": v(420.05, -379.18) * mm, "end": v(408.17, -376.1) * mm});
            skLineSegment(sketch, "E7347", {"start": v(408.17, -376.1) * mm, "end": v(396.5, -373) * mm});
            skLineSegment(sketch, "E7348", {"start": v(396.5, -373) * mm, "end": v(385.06, -369.94) * mm});
            skLineSegment(sketch, "E7349", {"start": v(385.06, -369.94) * mm, "end": v(373.93, -366.92) * mm});
            skLineSegment(sketch, "E7350", {"start": v(373.93, -366.92) * mm, "end": v(363.17, -363.94) * mm});
            skLineSegment(sketch, "E7351", {"start": v(363.17, -363.94) * mm, "end": v(352.83, -361.02) * mm});
            skLineSegment(sketch, "E7352", {"start": v(352.83, -361.02) * mm, "end": v(342.96, -358.18) * mm});
            skLineSegment(sketch, "E7353", {"start": v(342.96, -358.18) * mm, "end": v(333.63, -355.43) * mm});
            skLineSegment(sketch, "E7354", {"start": v(333.63, -355.43) * mm, "end": v(324.88, -352.78) * mm});
            skLineSegment(sketch, "E7355", {"start": v(324.88, -352.78) * mm, "end": v(316.78, -350.25) * mm});
            skLineSegment(sketch, "E7356", {"start": v(316.78, -350.25) * mm, "end": v(309.38, -347.84) * mm});
            skLineSegment(sketch, "E7357", {"start": v(309.38, -347.84) * mm, "end": v(304.4, -346.16) * mm});
            skLineSegment(sketch, "E7358", {"start": v(304.4, -346.16) * mm, "end": v(302.74, -345.58) * mm});
            skLineSegment(sketch, "E7359", {"start": v(302.74, -345.58) * mm, "end": v(300.49, -344.8) * mm});
            skLineSegment(sketch, "E7360", {"start": v(300.49, -344.8) * mm, "end": v(293.72, -342.46) * mm});
            skLineSegment(sketch, "E7361", {"start": v(293.72, -342.46) * mm, "end": v(285.25, -339.56) * mm});
            skLineSegment(sketch, "E7362", {"start": v(285.25, -339.56) * mm, "end": v(277.24, -336.84) * mm});
            skLineSegment(sketch, "E7363", {"start": v(277.24, -336.84) * mm, "end": v(269.6, -334.25) * mm});
            skLineSegment(sketch, "E7364", {"start": v(269.6, -334.25) * mm, "end": v(262.28, -331.71) * mm});
            skLineSegment(sketch, "E7365", {"start": v(262.28, -331.71) * mm, "end": v(255.15, -329.19) * mm});
            skLineSegment(sketch, "E7366", {"start": v(255.15, -329.19) * mm, "end": v(248.15, -326.61) * mm});
            skLineSegment(sketch, "E7367", {"start": v(248.15, -326.61) * mm, "end": v(241.2, -323.94) * mm});
            skLineSegment(sketch, "E7368", {"start": v(241.2, -323.94) * mm, "end": v(234.2, -321.1) * mm});
            skLineSegment(sketch, "E7369", {"start": v(234.2, -321.1) * mm, "end": v(227.07, -318.05) * mm});
            skLineSegment(sketch, "E7370", {"start": v(227.07, -318.05) * mm, "end": v(219.74, -314.73) * mm});
            skLineSegment(sketch, "E7371", {"start": v(219.74, -314.73) * mm, "end": v(212.12, -311.08) * mm});
            skLineSegment(sketch, "E7372", {"start": v(212.12, -311.08) * mm, "end": v(204.12, -307.04) * mm});
            skLineSegment(sketch, "E7373", {"start": v(204.12, -307.04) * mm, "end": v(195.65, -302.57) * mm});
            skLineSegment(sketch, "E7374", {"start": v(195.65, -302.57) * mm, "end": v(186.64, -297.6) * mm});
            skLineSegment(sketch, "E7375", {"start": v(186.64, -297.6) * mm, "end": v(179.4, -293.48) * mm});
            skLineSegment(sketch, "E7376", {"start": v(179.4, -293.48) * mm, "end": v(177, -292.09) * mm});
            skLineSegment(sketch, "E7377", {"start": v(177, -292.09) * mm, "end": v(176.5, -291.8) * mm});
            skLineSegment(sketch, "E7378", {"start": v(176.5, -291.8) * mm, "end": v(175.04, -290.86) * mm});
            skLineSegment(sketch, "E7379", {"start": v(175.04, -290.86) * mm, "end": v(172.68, -289.24) * mm});
            skLineSegment(sketch, "E7380", {"start": v(172.68, -289.24) * mm, "end": v(169.94, -287.25) * mm});
            skLineSegment(sketch, "E7381", {"start": v(169.94, -287.25) * mm, "end": v(166.86, -284.92) * mm});
            skLineSegment(sketch, "E7382", {"start": v(166.86, -284.92) * mm, "end": v(163.45, -282.27) * mm});
            skLineSegment(sketch, "E7383", {"start": v(163.45, -282.27) * mm, "end": v(159.75, -279.32) * mm});
            skLineSegment(sketch, "E7384", {"start": v(159.75, -279.32) * mm, "end": v(155.8, -276.13) * mm});
            skLineSegment(sketch, "E7385", {"start": v(155.8, -276.13) * mm, "end": v(151.6, -272.69) * mm});
            skLineSegment(sketch, "E7386", {"start": v(151.6, -272.69) * mm, "end": v(147.18, -269.04) * mm});
            skLineSegment(sketch, "E7387", {"start": v(147.18, -269.04) * mm, "end": v(142.6, -265.21) * mm});
            skLineSegment(sketch, "E7388", {"start": v(142.6, -265.21) * mm, "end": v(137.86, -261.23) * mm});
            skLineSegment(sketch, "E7389", {"start": v(137.86, -261.23) * mm, "end": v(132.99, -257.12) * mm});
            skLineSegment(sketch, "E7390", {"start": v(132.99, -257.12) * mm, "end": v(128.02, -252.9) * mm});
            skLineSegment(sketch, "E7391", {"start": v(128.02, -252.9) * mm, "end": v(122.99, -248.62) * mm});
            skLineSegment(sketch, "E7392", {"start": v(122.99, -248.62) * mm, "end": v(117.9, -244.28) * mm});
            skLineSegment(sketch, "E7393", {"start": v(117.9, -244.28) * mm, "end": v(112.8, -239.92) * mm});
            skLineSegment(sketch, "E7394", {"start": v(112.8, -239.92) * mm, "end": v(107.73, -235.56) * mm});
            skLineSegment(sketch, "E7395", {"start": v(107.73, -235.56) * mm, "end": v(102.69, -231.24) * mm});
            skLineSegment(sketch, "E7396", {"start": v(102.69, -231.24) * mm, "end": v(97.71, -226.98) * mm});
            skLineSegment(sketch, "E7397", {"start": v(97.71, -226.98) * mm, "end": v(92.83, -222.8) * mm});
            skLineSegment(sketch, "E7398", {"start": v(92.83, -222.8) * mm, "end": v(88.08, -218.73) * mm});
            skLineSegment(sketch, "E7399", {"start": v(88.08, -218.73) * mm, "end": v(83.48, -214.8) * mm});
            skLineSegment(sketch, "E7400", {"start": v(83.48, -214.8) * mm, "end": v(79.05, -211.05) * mm});
            skLineSegment(sketch, "E7401", {"start": v(79.05, -211.05) * mm, "end": v(74.84, -207.48) * mm});
            skLineSegment(sketch, "E7402", {"start": v(74.84, -207.48) * mm, "end": v(70.85, -204.13) * mm});
            skLineSegment(sketch, "E7403", {"start": v(70.85, -204.13) * mm, "end": v(67.13, -201.03) * mm});
            skLineSegment(sketch, "E7404", {"start": v(67.13, -201.03) * mm, "end": v(63.7, -198.2) * mm});
            skLineSegment(sketch, "E7405", {"start": v(63.7, -198.2) * mm, "end": v(60.6, -195.67) * mm});
            skLineSegment(sketch, "E7406", {"start": v(60.6, -195.67) * mm, "end": v(57.83, -193.47) * mm});
            skLineSegment(sketch, "E7407", {"start": v(57.83, -193.47) * mm, "end": v(55.43, -191.62) * mm});
            skLineSegment(sketch, "E7408", {"start": v(55.43, -191.62) * mm, "end": v(53.44, -190.15) * mm});
            skLineSegment(sketch, "E7409", {"start": v(53.44, -190.15) * mm, "end": v(52.27, -189.34) * mm});
            skLineSegment(sketch, "E7410", {"start": v(52.27, -189.34) * mm, "end": v(51.88, -189.1) * mm});
            skLineSegment(sketch, "E7411", {"start": v(51.88, -189.1) * mm, "end": v(47.6, -186.38) * mm});
            skLineSegment(sketch, "E7412", {"start": v(47.6, -186.38) * mm, "end": v(34.91, -177.95) * mm});
            skLineSegment(sketch, "E7413", {"start": v(34.91, -177.95) * mm, "end": v(19.52, -167.1) * mm});
            skLineSegment(sketch, "E7414", {"start": v(19.52, -167.1) * mm, "end": v(5.58, -156.6) * mm});
            skLineSegment(sketch, "E7415", {"start": v(5.58, -156.6) * mm, "end": v(-7, -146.49) * mm});
            skLineSegment(sketch, "E7416", {"start": v(-7, -146.49) * mm, "end": v(-18.34, -136.8) * mm});
            skLineSegment(sketch, "E7417", {"start": v(-18.34, -136.8) * mm, "end": v(-28.55, -127.56) * mm});
            skLineSegment(sketch, "E7418", {"start": v(-28.55, -127.56) * mm, "end": v(-37.74, -118.83) * mm});
            skLineSegment(sketch, "E7419", {"start": v(-37.74, -118.83) * mm, "end": v(-46.02, -110.64) * mm});
            skLineSegment(sketch, "E7420", {"start": v(-46.02, -110.64) * mm, "end": v(-53.5, -103.03) * mm});
            skLineSegment(sketch, "E7421", {"start": v(-53.5, -103.03) * mm, "end": v(-60.28, -96.05) * mm});
            skLineSegment(sketch, "E7422", {"start": v(-60.28, -96.05) * mm, "end": v(-66.48, -89.74) * mm});
            skLineSegment(sketch, "E7423", {"start": v(-66.48, -89.74) * mm, "end": v(-72.21, -84.13) * mm});
            skLineSegment(sketch, "E7424", {"start": v(-72.21, -84.13) * mm, "end": v(-77.57, -79.26) * mm});
            skLineSegment(sketch, "E7425", {"start": v(-77.57, -79.26) * mm, "end": v(-82.68, -75.18) * mm});
            skLineSegment(sketch, "E7426", {"start": v(-82.68, -75.18) * mm, "end": v(-87.64, -71.92) * mm});
            skLineSegment(sketch, "E7427", {"start": v(-87.64, -71.92) * mm, "end": v(-91.3, -70.03) * mm});
            skLineSegment(sketch, "E7428", {"start": v(-91.3, -70.03) * mm, "end": v(-92.57, -69.54) * mm});
            skLineSegment(sketch, "E7429", {"start": v(-92.57, -69.54) * mm, "end": v(-93.81, -69.05) * mm});
            skLineSegment(sketch, "E7430", {"start": v(-93.81, -69.05) * mm, "end": v(-97.72, -68.07) * mm});
            skLineSegment(sketch, "E7431", {"start": v(-97.72, -68.07) * mm, "end": v(-103.25, -67.5) * mm});
            skLineSegment(sketch, "E7432", {"start": v(-103.25, -67.5) * mm, "end": v(-109.12, -67.7) * mm});
            skLineSegment(sketch, "E7433", {"start": v(-109.12, -67.7) * mm, "end": v(-115.28, -68.58) * mm});
            skLineSegment(sketch, "E7434", {"start": v(-115.28, -68.58) * mm, "end": v(-121.69, -70) * mm});
            skLineSegment(sketch, "E7435", {"start": v(-121.69, -70) * mm, "end": v(-128.3, -71.89) * mm});
            skLineSegment(sketch, "E7436", {"start": v(-128.3, -71.89) * mm, "end": v(-135.07, -74.1) * mm});
            skLineSegment(sketch, "E7437", {"start": v(-135.07, -74.1) * mm, "end": v(-141.95, -76.56) * mm});
            skLineSegment(sketch, "E7438", {"start": v(-141.95, -76.56) * mm, "end": v(-148.9, -79.13) * mm});
            skLineSegment(sketch, "E7439", {"start": v(-148.9, -79.13) * mm, "end": v(-155.9, -81.72) * mm});
            skLineSegment(sketch, "E7440", {"start": v(-155.9, -81.72) * mm, "end": v(-162.86, -84.2) * mm});
            skLineSegment(sketch, "E7441", {"start": v(-162.86, -84.2) * mm, "end": v(-169.76, -86.49) * mm});
            skLineSegment(sketch, "E7442", {"start": v(-169.76, -86.49) * mm, "end": v(-176.56, -88.46) * mm});
            skLineSegment(sketch, "E7443", {"start": v(-176.56, -88.46) * mm, "end": v(-183.21, -89.99) * mm});
            skLineSegment(sketch, "E7444", {"start": v(-183.21, -89.99) * mm, "end": v(-189.67, -91) * mm});
            skLineSegment(sketch, "E7445", {"start": v(-189.67, -91) * mm, "end": v(-194.33, -91.35) * mm});
            skLineSegment(sketch, "E7446", {"start": v(-194.33, -91.35) * mm, "end": v(-195.89, -91.35) * mm});
            skLineSegment(sketch, "E7447", {"start": v(-195.89, -91.35) * mm, "end": v(-197.86, -91.35) * mm});
            skLineSegment(sketch, "E7448", {"start": v(-197.86, -91.35) * mm, "end": v(-203.77, -91.18) * mm});
            skLineSegment(sketch, "E7449", {"start": v(-203.77, -91.18) * mm, "end": v(-213.14, -90.65) * mm});
            skLineSegment(sketch, "E7450", {"start": v(-213.14, -90.65) * mm, "end": v(-223.9, -89.75) * mm});
            skLineSegment(sketch, "E7451", {"start": v(-223.9, -89.75) * mm, "end": v(-235.95, -88.44) * mm});
            skLineSegment(sketch, "E7452", {"start": v(-235.95, -88.44) * mm, "end": v(-249.18, -86.72) * mm});
            skLineSegment(sketch, "E7453", {"start": v(-249.18, -86.72) * mm, "end": v(-263.47, -84.57) * mm});
            skLineSegment(sketch, "E7454", {"start": v(-263.47, -84.57) * mm, "end": v(-278.74, -81.96) * mm});
            skLineSegment(sketch, "E7455", {"start": v(-278.74, -81.96) * mm, "end": v(-290.84, -79.7) * mm});
            skLineSegment(sketch, "E7456", {"start": v(-290.84, -79.7) * mm, "end": v(-294.87, -78.88) * mm});
            skLineSegment(sketch, "E7457", {"start": v(-294.87, -78.88) * mm, "end": v(-297.66, -78.32) * mm});
            skLineSegment(sketch, "E7458", {"start": v(-297.66, -78.32) * mm, "end": v(-306.07, -76.76) * mm});
            skLineSegment(sketch, "E7459", {"start": v(-306.07, -76.76) * mm, "end": v(-317.62, -74.82) * mm});
            skLineSegment(sketch, "E7460", {"start": v(-317.62, -74.82) * mm, "end": v(-329.42, -73.06) * mm});
            skLineSegment(sketch, "E7461", {"start": v(-329.42, -73.06) * mm, "end": v(-341.36, -71.46) * mm});
            skLineSegment(sketch, "E7462", {"start": v(-341.36, -71.46) * mm, "end": v(-353.36, -70.03) * mm});
            skLineSegment(sketch, "E7463", {"start": v(-353.36, -70.03) * mm, "end": v(-365.33, -68.75) * mm});
            skLineSegment(sketch, "E7464", {"start": v(-365.33, -68.75) * mm, "end": v(-377.17, -67.62) * mm});
            skLineSegment(sketch, "E7465", {"start": v(-377.17, -67.62) * mm, "end": v(-388.78, -66.64) * mm});
            skLineSegment(sketch, "E7466", {"start": v(-388.78, -66.64) * mm, "end": v(-400.09, -65.8) * mm});
            skLineSegment(sketch, "E7467", {"start": v(-400.09, -65.8) * mm, "end": v(-410.98, -65.09) * mm});
            skLineSegment(sketch, "E7468", {"start": v(-410.98, -65.09) * mm, "end": v(-421.37, -64.5) * mm});
            skLineSegment(sketch, "E7469", {"start": v(-421.37, -64.5) * mm, "end": v(-431.17, -64.04) * mm});
            skLineSegment(sketch, "E7470", {"start": v(-431.17, -64.04) * mm, "end": v(-440.28, -63.69) * mm});
            skLineSegment(sketch, "E7471", {"start": v(-440.28, -63.69) * mm, "end": v(-448.6, -63.44) * mm});
            skLineSegment(sketch, "E7472", {"start": v(-448.6, -63.44) * mm, "end": v(-456.06, -63.3) * mm});
            skLineSegment(sketch, "E7473", {"start": v(-456.06, -63.3) * mm, "end": v(-460.92, -63.26) * mm});
            skLineSegment(sketch, "E7474", {"start": v(-460.92, -63.26) * mm, "end": v(-462.55, -63.26) * mm});
            skLineSegment(sketch, "E7475", {"start": v(612.03, -392.5) * mm, "end": v(611.07, -392.43) * mm});
            skLineSegment(sketch, "E7476", {"start": v(611.07, -392.43) * mm, "end": v(608.19, -392.1) * mm});
            skLineSegment(sketch, "E7477", {"start": v(608.19, -392.1) * mm, "end": v(603.47, -391.46) * mm});
            skLineSegment(sketch, "E7478", {"start": v(603.47, -391.46) * mm, "end": v(597.93, -390.58) * mm});
            skLineSegment(sketch, "E7479", {"start": v(597.93, -390.58) * mm, "end": v(591.62, -389.47) * mm});
            skLineSegment(sketch, "E7480", {"start": v(591.62, -389.47) * mm, "end": v(584.6, -388.14) * mm});
            skLineSegment(sketch, "E7481", {"start": v(584.6, -388.14) * mm, "end": v(576.9, -386.62) * mm});
            skLineSegment(sketch, "E7482", {"start": v(576.9, -386.62) * mm, "end": v(568.59, -384.9) * mm});
            skLineSegment(sketch, "E7483", {"start": v(568.59, -384.9) * mm, "end": v(559.71, -383.02) * mm});
            skLineSegment(sketch, "E7484", {"start": v(559.71, -383.02) * mm, "end": v(550.33, -380.97) * mm});
            skLineSegment(sketch, "E7485", {"start": v(550.33, -380.97) * mm, "end": v(540.5, -378.78) * mm});
            skLineSegment(sketch, "E7486", {"start": v(540.5, -378.78) * mm, "end": v(530.25, -376.45) * mm});
            skLineSegment(sketch, "E7487", {"start": v(530.25, -376.45) * mm, "end": v(519.66, -373.98) * mm});
            skLineSegment(sketch, "E7488", {"start": v(519.66, -373.98) * mm, "end": v(508.77, -371.42) * mm});
            skLineSegment(sketch, "E7489", {"start": v(508.77, -371.42) * mm, "end": v(497.63, -368.75) * mm});
            skLineSegment(sketch, "E7490", {"start": v(497.63, -368.75) * mm, "end": v(486.3, -366) * mm});
            skLineSegment(sketch, "E7491", {"start": v(486.3, -366) * mm, "end": v(474.82, -363.17) * mm});
            skLineSegment(sketch, "E7492", {"start": v(474.82, -363.17) * mm, "end": v(463.25, -360.29) * mm});
            skLineSegment(sketch, "E7493", {"start": v(463.25, -360.29) * mm, "end": v(451.65, -357.36) * mm});
            skLineSegment(sketch, "E7494", {"start": v(451.65, -357.36) * mm, "end": v(440.06, -354.4) * mm});
            skLineSegment(sketch, "E7495", {"start": v(440.06, -354.4) * mm, "end": v(428.54, -351.4) * mm});
            skLineSegment(sketch, "E7496", {"start": v(428.54, -351.4) * mm, "end": v(417.15, -348.4) * mm});
            skLineSegment(sketch, "E7497", {"start": v(417.15, -348.4) * mm, "end": v(405.92, -345.4) * mm});
            skLineSegment(sketch, "E7498", {"start": v(405.92, -345.4) * mm, "end": v(394.92, -342.43) * mm});
            skLineSegment(sketch, "E7499", {"start": v(394.92, -342.43) * mm, "end": v(384.2, -339.49) * mm});
            skLineSegment(sketch, "E7500", {"start": v(384.2, -339.49) * mm, "end": v(373.81, -336.58) * mm});
            skLineSegment(sketch, "E7501", {"start": v(373.81, -336.58) * mm, "end": v(363.8, -333.73) * mm});
            skLineSegment(sketch, "E7502", {"start": v(363.8, -333.73) * mm, "end": v(354.23, -330.95) * mm});
            skLineSegment(sketch, "E7503", {"start": v(354.23, -330.95) * mm, "end": v(345.14, -328.25) * mm});
            skLineSegment(sketch, "E7504", {"start": v(345.14, -328.25) * mm, "end": v(336.6, -325.64) * mm});
            skLineSegment(sketch, "E7505", {"start": v(336.6, -325.64) * mm, "end": v(328.65, -323.13) * mm});
            skLineSegment(sketch, "E7506", {"start": v(328.65, -323.13) * mm, "end": v(321.34, -320.75) * mm});
            skLineSegment(sketch, "E7507", {"start": v(321.34, -320.75) * mm, "end": v(316.38, -319.07) * mm});
            skLineSegment(sketch, "E7508", {"start": v(316.38, -319.07) * mm, "end": v(314.73, -318.5) * mm});
            skLineSegment(sketch, "E7509", {"start": v(314.73, -318.5) * mm, "end": v(310.16, -316.9) * mm});
            skLineSegment(sketch, "E7510", {"start": v(310.16, -316.9) * mm, "end": v(296.42, -312.1) * mm});
            skLineSegment(sketch, "E7511", {"start": v(296.42, -312.1) * mm, "end": v(278.62, -305.75) * mm});
            skLineSegment(sketch, "E7512", {"start": v(278.62, -305.75) * mm, "end": v(261.14, -299.18) * mm});
            skLineSegment(sketch, "E7513", {"start": v(261.14, -299.18) * mm, "end": v(243.78, -292.11) * mm});
            skLineSegment(sketch, "E7514", {"start": v(243.78, -292.11) * mm, "end": v(226.34, -284.25) * mm});
            skLineSegment(sketch, "E7515", {"start": v(226.34, -284.25) * mm, "end": v(208.62, -275.32) * mm});
            skLineSegment(sketch, "E7516", {"start": v(208.62, -275.32) * mm, "end": v(190.42, -265.06) * mm});
            skLineSegment(sketch, "E7517", {"start": v(190.42, -265.06) * mm, "end": v(176.19, -256.25) * mm});
            skLineSegment(sketch, "E7518", {"start": v(176.19, -256.25) * mm, "end": v(171.54, -253.16) * mm});
            skLineSegment(sketch, "E7519", {"start": v(171.54, -253.16) * mm, "end": v(171.07, -252.85) * mm});
            skLineSegment(sketch, "E7520", {"start": v(171.07, -252.85) * mm, "end": v(169.66, -251.88) * mm});
            skLineSegment(sketch, "E7521", {"start": v(169.66, -251.88) * mm, "end": v(167.4, -250.28) * mm});
            skLineSegment(sketch, "E7522", {"start": v(167.4, -250.28) * mm, "end": v(164.79, -248.39) * mm});
            skLineSegment(sketch, "E7523", {"start": v(164.79, -248.39) * mm, "end": v(161.85, -246.22) * mm});
            skLineSegment(sketch, "E7524", {"start": v(161.85, -246.22) * mm, "end": v(158.61, -243.8) * mm});
            skLineSegment(sketch, "E7525", {"start": v(158.61, -243.8) * mm, "end": v(155.1, -241.15) * mm});
            skLineSegment(sketch, "E7526", {"start": v(155.1, -241.15) * mm, "end": v(151.34, -238.3) * mm});
            skLineSegment(sketch, "E7527", {"start": v(151.34, -238.3) * mm, "end": v(147.36, -235.25) * mm});
            skLineSegment(sketch, "E7528", {"start": v(147.36, -235.25) * mm, "end": v(143.19, -232.04) * mm});
            skLineSegment(sketch, "E7529", {"start": v(143.19, -232.04) * mm, "end": v(138.84, -228.68) * mm});
            skLineSegment(sketch, "E7530", {"start": v(138.84, -228.68) * mm, "end": v(134.35, -225.2) * mm});
            skLineSegment(sketch, "E7531", {"start": v(134.35, -225.2) * mm, "end": v(129.74, -221.63) * mm});
            skLineSegment(sketch, "E7532", {"start": v(129.74, -221.63) * mm, "end": v(125.05, -217.97) * mm});
            skLineSegment(sketch, "E7533", {"start": v(125.05, -217.97) * mm, "end": v(120.28, -214.26) * mm});
            skLineSegment(sketch, "E7534", {"start": v(120.28, -214.26) * mm, "end": v(115.47, -210.5) * mm});
            skLineSegment(sketch, "E7535", {"start": v(115.47, -210.5) * mm, "end": v(110.65, -206.74) * mm});
            skLineSegment(sketch, "E7536", {"start": v(110.65, -206.74) * mm, "end": v(105.84, -202.99) * mm});
            skLineSegment(sketch, "E7537", {"start": v(105.84, -202.99) * mm, "end": v(101.07, -199.26) * mm});
            skLineSegment(sketch, "E7538", {"start": v(101.07, -199.26) * mm, "end": v(96.37, -195.58) * mm});
            skLineSegment(sketch, "E7539", {"start": v(96.37, -195.58) * mm, "end": v(91.75, -191.97) * mm});
            skLineSegment(sketch, "E7540", {"start": v(91.75, -191.97) * mm, "end": v(87.25, -188.45) * mm});
            skLineSegment(sketch, "E7541", {"start": v(87.25, -188.45) * mm, "end": v(82.9, -185.04) * mm});
            skLineSegment(sketch, "E7542", {"start": v(82.9, -185.04) * mm, "end": v(78.7, -181.78) * mm});
            skLineSegment(sketch, "E7543", {"start": v(78.7, -181.78) * mm, "end": v(74.7, -178.67) * mm});
            skLineSegment(sketch, "E7544", {"start": v(74.7, -178.67) * mm, "end": v(70.93, -175.74) * mm});
            skLineSegment(sketch, "E7545", {"start": v(70.93, -175.74) * mm, "end": v(67.4, -173.01) * mm});
            skLineSegment(sketch, "E7546", {"start": v(67.4, -173.01) * mm, "end": v(64.13, -170.5) * mm});
            skLineSegment(sketch, "E7547", {"start": v(64.13, -170.5) * mm, "end": v(61.17, -168.24) * mm});
            skLineSegment(sketch, "E7548", {"start": v(61.17, -168.24) * mm, "end": v(58.53, -166.24) * mm});
            skLineSegment(sketch, "E7549", {"start": v(58.53, -166.24) * mm, "end": v(56.24, -164.52) * mm});
            skLineSegment(sketch, "E7550", {"start": v(56.24, -164.52) * mm, "end": v(54.32, -163.12) * mm});
            skLineSegment(sketch, "E7551", {"start": v(54.32, -163.12) * mm, "end": v(53.2, -162.3) * mm});
            skLineSegment(sketch, "E7552", {"start": v(53.2, -162.3) * mm, "end": v(52.81, -162.04) * mm});
            skLineSegment(sketch, "E7553", {"start": v(52.81, -162.04) * mm, "end": v(48.72, -159.21) * mm});
            skLineSegment(sketch, "E7554", {"start": v(48.72, -159.21) * mm, "end": v(36.63, -150.45) * mm});
            skLineSegment(sketch, "E7555", {"start": v(36.63, -150.45) * mm, "end": v(21.95, -139.2) * mm});
            skLineSegment(sketch, "E7556", {"start": v(21.95, -139.2) * mm, "end": v(8.66, -128.36) * mm});
            skLineSegment(sketch, "E7557", {"start": v(8.66, -128.36) * mm, "end": v(-3.34, -117.93) * mm});
            skLineSegment(sketch, "E7558", {"start": v(-3.34, -117.93) * mm, "end": v(-14.17, -107.97) * mm});
            skLineSegment(sketch, "E7559", {"start": v(-14.17, -107.97) * mm, "end": v(-23.92, -98.5) * mm});
            skLineSegment(sketch, "E7560", {"start": v(-23.92, -98.5) * mm, "end": v(-32.7, -89.58) * mm});
            skLineSegment(sketch, "E7561", {"start": v(-32.7, -89.58) * mm, "end": v(-40.64, -81.23) * mm});
            skLineSegment(sketch, "E7562", {"start": v(-40.64, -81.23) * mm, "end": v(-47.81, -73.5) * mm});
            skLineSegment(sketch, "E7563", {"start": v(-47.81, -73.5) * mm, "end": v(-54.35, -66.4) * mm});
            skLineSegment(sketch, "E7564", {"start": v(-54.35, -66.4) * mm, "end": v(-60.34, -60.02) * mm});
            skLineSegment(sketch, "E7565", {"start": v(-60.34, -60.02) * mm, "end": v(-65.9, -54.34) * mm});
            skLineSegment(sketch, "E7566", {"start": v(-65.9, -54.34) * mm, "end": v(-71.15, -49.44) * mm});
            skLineSegment(sketch, "E7567", {"start": v(-71.15, -49.44) * mm, "end": v(-76.18, -45.33) * mm});
            skLineSegment(sketch, "E7568", {"start": v(-76.18, -45.33) * mm, "end": v(-81.1, -42.07) * mm});
            skLineSegment(sketch, "E7569", {"start": v(-81.1, -42.07) * mm, "end": v(-84.74, -40.17) * mm});
            skLineSegment(sketch, "E7570", {"start": v(-84.74, -40.17) * mm, "end": v(-86, -39.68) * mm});
            skLineSegment(sketch, "E7571", {"start": v(-86, -39.68) * mm, "end": v(-87.25, -39.18) * mm});
            skLineSegment(sketch, "E7572", {"start": v(-87.25, -39.18) * mm, "end": v(-91.2, -38.28) * mm});
            skLineSegment(sketch, "E7573", {"start": v(-91.2, -38.28) * mm, "end": v(-96.86, -37.88) * mm});
            skLineSegment(sketch, "E7574", {"start": v(-96.86, -37.88) * mm, "end": v(-102.92, -38.36) * mm});
            skLineSegment(sketch, "E7575", {"start": v(-102.92, -38.36) * mm, "end": v(-109.33, -39.59) * mm});
            skLineSegment(sketch, "E7576", {"start": v(-109.33, -39.59) * mm, "end": v(-116.03, -41.44) * mm});
            skLineSegment(sketch, "E7577", {"start": v(-116.03, -41.44) * mm, "end": v(-122.97, -43.8) * mm});
            skLineSegment(sketch, "E7578", {"start": v(-122.97, -43.8) * mm, "end": v(-130.1, -46.52) * mm});
            skLineSegment(sketch, "E7579", {"start": v(-130.1, -46.52) * mm, "end": v(-137.35, -49.5) * mm});
            skLineSegment(sketch, "E7580", {"start": v(-137.35, -49.5) * mm, "end": v(-144.67, -52.59) * mm});
            skLineSegment(sketch, "E7581", {"start": v(-144.67, -52.59) * mm, "end": v(-152, -55.68) * mm});
            skLineSegment(sketch, "E7582", {"start": v(-152, -55.68) * mm, "end": v(-159.3, -58.64) * mm});
            skLineSegment(sketch, "E7583", {"start": v(-159.3, -58.64) * mm, "end": v(-166.5, -61.34) * mm});
            skLineSegment(sketch, "E7584", {"start": v(-166.5, -61.34) * mm, "end": v(-173.55, -63.66) * mm});
            skLineSegment(sketch, "E7585", {"start": v(-173.55, -63.66) * mm, "end": v(-180.4, -65.47) * mm});
            skLineSegment(sketch, "E7586", {"start": v(-180.4, -65.47) * mm, "end": v(-186.98, -66.66) * mm});
            skLineSegment(sketch, "E7587", {"start": v(-186.98, -66.66) * mm, "end": v(-191.67, -67.08) * mm});
            skLineSegment(sketch, "E7588", {"start": v(-191.67, -67.08) * mm, "end": v(-193.24, -67.08) * mm});
            skLineSegment(sketch, "E7589", {"start": v(-193.24, -67.08) * mm, "end": v(-194.13, -67.08) * mm});
            skLineSegment(sketch, "E7590", {"start": v(-194.13, -67.08) * mm, "end": v(-196.78, -66.96) * mm});
            skLineSegment(sketch, "E7591", {"start": v(-196.78, -66.96) * mm, "end": v(-200.78, -66.63) * mm});
            skLineSegment(sketch, "E7592", {"start": v(-200.78, -66.63) * mm, "end": v(-205.25, -66.1) * mm});
            skLineSegment(sketch, "E7593", {"start": v(-205.25, -66.1) * mm, "end": v(-210.17, -65.4) * mm});
            skLineSegment(sketch, "E7594", {"start": v(-210.17, -65.4) * mm, "end": v(-215.52, -64.53) * mm});
            skLineSegment(sketch, "E7595", {"start": v(-215.52, -64.53) * mm, "end": v(-221.28, -63.51) * mm});
            skLineSegment(sketch, "E7596", {"start": v(-221.28, -63.51) * mm, "end": v(-227.44, -62.38) * mm});
            skLineSegment(sketch, "E7597", {"start": v(-227.44, -62.38) * mm, "end": v(-233.98, -61.14) * mm});
            skLineSegment(sketch, "E7598", {"start": v(-233.98, -61.14) * mm, "end": v(-240.9, -59.8) * mm});
            skLineSegment(sketch, "E7599", {"start": v(-240.9, -59.8) * mm, "end": v(-248.17, -58.4) * mm});
            skLineSegment(sketch, "E7600", {"start": v(-248.17, -58.4) * mm, "end": v(-255.78, -56.95) * mm});
            skLineSegment(sketch, "E7601", {"start": v(-255.78, -56.95) * mm, "end": v(-263.72, -55.47) * mm});
            skLineSegment(sketch, "E7602", {"start": v(-263.72, -55.47) * mm, "end": v(-271.96, -53.98) * mm});
            skLineSegment(sketch, "E7603", {"start": v(-271.96, -53.98) * mm, "end": v(-280.5, -52.48) * mm});
            skLineSegment(sketch, "E7604", {"start": v(-280.5, -52.48) * mm, "end": v(-289.31, -51.01) * mm});
            skLineSegment(sketch, "E7605", {"start": v(-289.31, -51.01) * mm, "end": v(-296.12, -49.93) * mm});
            skLineSegment(sketch, "E7606", {"start": v(-296.12, -49.93) * mm, "end": v(-298.4, -49.58) * mm});
            skLineSegment(sketch, "E7607", {"start": v(-298.4, -49.58) * mm, "end": v(-301.57, -49.1) * mm});
            skLineSegment(sketch, "E7608", {"start": v(-301.57, -49.1) * mm, "end": v(-311.13, -47.82) * mm});
            skLineSegment(sketch, "E7609", {"start": v(-311.13, -47.82) * mm, "end": v(-324.56, -46.27) * mm});
            skLineSegment(sketch, "E7610", {"start": v(-324.56, -46.27) * mm, "end": v(-338.46, -44.93) * mm});
            skLineSegment(sketch, "E7611", {"start": v(-338.46, -44.93) * mm, "end": v(-352.63, -43.77) * mm});
            skLineSegment(sketch, "E7612", {"start": v(-352.63, -43.77) * mm, "end": v(-366.86, -42.8) * mm});
            skLineSegment(sketch, "E7613", {"start": v(-366.86, -42.8) * mm, "end": v(-380.95, -41.98) * mm});
            skLineSegment(sketch, "E7614", {"start": v(-380.95, -41.98) * mm, "end": v(-394.67, -41.31) * mm});
            skLineSegment(sketch, "E7615", {"start": v(-394.67, -41.31) * mm, "end": v(-407.84, -40.78) * mm});
            skLineSegment(sketch, "E7616", {"start": v(-407.84, -40.78) * mm, "end": v(-420.23, -40.36) * mm});
            skLineSegment(sketch, "E7617", {"start": v(-420.23, -40.36) * mm, "end": v(-431.65, -40.04) * mm});
            skLineSegment(sketch, "E7618", {"start": v(-431.65, -40.04) * mm, "end": v(-441.88, -39.81) * mm});
            skLineSegment(sketch, "E7619", {"start": v(-441.88, -39.81) * mm, "end": v(-450.71, -39.66) * mm});
            skLineSegment(sketch, "E7620", {"start": v(-450.71, -39.66) * mm, "end": v(-457.95, -39.56) * mm});
            skLineSegment(sketch, "E7621", {"start": v(-457.95, -39.56) * mm, "end": v(-463.37, -39.51) * mm});
            skLineSegment(sketch, "E7622", {"start": v(-463.37, -39.51) * mm, "end": v(-466.78, -39.5) * mm});
            skLineSegment(sketch, "E7623", {"start": v(-466.78, -39.5) * mm, "end": v(-467.96, -39.5) * mm});
            skLineSegment(sketch, "E7624", {"start": v(611.86, -367.1) * mm, "end": v(610.6, -367) * mm});
            skLineSegment(sketch, "E7625", {"start": v(610.6, -367) * mm, "end": v(606.8, -366.62) * mm});
            skLineSegment(sketch, "E7626", {"start": v(606.8, -366.62) * mm, "end": v(601.18, -365.94) * mm});
            skLineSegment(sketch, "E7627", {"start": v(601.18, -365.94) * mm, "end": v(595.06, -365.05) * mm});
            skLineSegment(sketch, "E7628", {"start": v(595.06, -365.05) * mm, "end": v(588.46, -363.99) * mm});
            skLineSegment(sketch, "E7629", {"start": v(588.46, -363.99) * mm, "end": v(581.42, -362.75) * mm});
            skLineSegment(sketch, "E7630", {"start": v(581.42, -362.75) * mm, "end": v(573.98, -361.35) * mm});
            skLineSegment(sketch, "E7631", {"start": v(573.98, -361.35) * mm, "end": v(566.16, -359.8) * mm});
            skLineSegment(sketch, "E7632", {"start": v(566.16, -359.8) * mm, "end": v(558, -358.09) * mm});
            skLineSegment(sketch, "E7633", {"start": v(558, -358.09) * mm, "end": v(549.55, -356.26) * mm});
            skLineSegment(sketch, "E7634", {"start": v(549.55, -356.26) * mm, "end": v(540.83, -354.3) * mm});
            skLineSegment(sketch, "E7635", {"start": v(540.83, -354.3) * mm, "end": v(531.87, -352.24) * mm});
            skLineSegment(sketch, "E7636", {"start": v(531.87, -352.24) * mm, "end": v(522.72, -350.07) * mm});
            skLineSegment(sketch, "E7637", {"start": v(522.72, -350.07) * mm, "end": v(513.4, -347.81) * mm});
            skLineSegment(sketch, "E7638", {"start": v(513.4, -347.81) * mm, "end": v(503.95, -345.47) * mm});
            skLineSegment(sketch, "E7639", {"start": v(503.95, -345.47) * mm, "end": v(494.41, -343.07) * mm});
            skLineSegment(sketch, "E7640", {"start": v(494.41, -343.07) * mm, "end": v(484.81, -340.6) * mm});
            skLineSegment(sketch, "E7641", {"start": v(484.81, -340.6) * mm, "end": v(475.19, -338.08) * mm});
            skLineSegment(sketch, "E7642", {"start": v(475.19, -338.08) * mm, "end": v(465.57, -335.53) * mm});
            skLineSegment(sketch, "E7643", {"start": v(465.57, -335.53) * mm, "end": v(456, -332.94) * mm});
            skLineSegment(sketch, "E7644", {"start": v(456, -332.94) * mm, "end": v(446.51, -330.34) * mm});
            skLineSegment(sketch, "E7645", {"start": v(446.51, -330.34) * mm, "end": v(437.14, -327.73) * mm});
            skLineSegment(sketch, "E7646", {"start": v(437.14, -327.73) * mm, "end": v(427.9, -325.12) * mm});
            skLineSegment(sketch, "E7647", {"start": v(427.9, -325.12) * mm, "end": v(418.86, -322.53) * mm});
            skLineSegment(sketch, "E7648", {"start": v(418.86, -322.53) * mm, "end": v(410.04, -319.95) * mm});
            skLineSegment(sketch, "E7649", {"start": v(410.04, -319.95) * mm, "end": v(401.46, -317.42) * mm});
            skLineSegment(sketch, "E7650", {"start": v(401.46, -317.42) * mm, "end": v(393.17, -314.92) * mm});
            skLineSegment(sketch, "E7651", {"start": v(393.17, -314.92) * mm, "end": v(385.2, -312.49) * mm});
            skLineSegment(sketch, "E7652", {"start": v(385.2, -312.49) * mm, "end": v(377.6, -310.12) * mm});
            skLineSegment(sketch, "E7653", {"start": v(377.6, -310.12) * mm, "end": v(370.38, -307.82) * mm});
            skLineSegment(sketch, "E7654", {"start": v(370.38, -307.82) * mm, "end": v(363.59, -305.6) * mm});
            skLineSegment(sketch, "E7655", {"start": v(363.59, -305.6) * mm, "end": v(357.26, -303.5) * mm});
            skLineSegment(sketch, "E7656", {"start": v(357.26, -303.5) * mm, "end": v(352.88, -302) * mm});
            skLineSegment(sketch, "E7657", {"start": v(352.88, -302) * mm, "end": v(351.42, -301.49) * mm});
            skLineSegment(sketch, "E7658", {"start": v(351.42, -301.49) * mm, "end": v(346.66, -299.82) * mm});
            skLineSegment(sketch, "E7659", {"start": v(346.66, -299.82) * mm, "end": v(332.46, -294.5) * mm});
            skLineSegment(sketch, "E7660", {"start": v(332.46, -294.5) * mm, "end": v(313.04, -286.7) * mm});
            skLineSegment(sketch, "E7661", {"start": v(313.04, -286.7) * mm, "end": v(293.42, -278.3) * mm});
            skLineSegment(sketch, "E7662", {"start": v(293.42, -278.3) * mm, "end": v(273.88, -269.46) * mm});
            skLineSegment(sketch, "E7663", {"start": v(273.88, -269.46) * mm, "end": v(254.68, -260.41) * mm});
            skLineSegment(sketch, "E7664", {"start": v(254.68, -260.41) * mm, "end": v(236.1, -251.32) * mm});
            skLineSegment(sketch, "E7665", {"start": v(236.1, -251.32) * mm, "end": v(218.4, -242.4) * mm});
            skLineSegment(sketch, "E7666", {"start": v(218.4, -242.4) * mm, "end": v(206, -235.99) * mm});
            skLineSegment(sketch, "E7667", {"start": v(206, -235.99) * mm, "end": v(201.87, -233.82) * mm});
            skLineSegment(sketch, "E7668", {"start": v(201.87, -233.82) * mm, "end": v(201.38, -233.57) * mm});
            skLineSegment(sketch, "E7669", {"start": v(201.38, -233.57) * mm, "end": v(199.96, -232.77) * mm});
            skLineSegment(sketch, "E7670", {"start": v(199.96, -232.77) * mm, "end": v(197.57, -231.35) * mm});
            skLineSegment(sketch, "E7671", {"start": v(197.57, -231.35) * mm, "end": v(194.73, -229.6) * mm});
            skLineSegment(sketch, "E7672", {"start": v(194.73, -229.6) * mm, "end": v(191.46, -227.54) * mm});
            skLineSegment(sketch, "E7673", {"start": v(191.46, -227.54) * mm, "end": v(187.8, -225.18) * mm});
            skLineSegment(sketch, "E7674", {"start": v(187.8, -225.18) * mm, "end": v(183.8, -222.57) * mm});
            skLineSegment(sketch, "E7675", {"start": v(183.8, -222.57) * mm, "end": v(179.46, -219.71) * mm});
            skLineSegment(sketch, "E7676", {"start": v(179.46, -219.71) * mm, "end": v(174.84, -216.64) * mm});
            skLineSegment(sketch, "E7677", {"start": v(174.84, -216.64) * mm, "end": v(169.96, -213.37) * mm});
            skLineSegment(sketch, "E7678", {"start": v(169.96, -213.37) * mm, "end": v(164.86, -209.94) * mm});
            skLineSegment(sketch, "E7679", {"start": v(164.86, -209.94) * mm, "end": v(159.57, -206.36) * mm});
            skLineSegment(sketch, "E7680", {"start": v(159.57, -206.36) * mm, "end": v(154.13, -202.67) * mm});
            skLineSegment(sketch, "E7681", {"start": v(154.13, -202.67) * mm, "end": v(148.56, -198.87) * mm});
            skLineSegment(sketch, "E7682", {"start": v(148.56, -198.87) * mm, "end": v(142.9, -195) * mm});
            skLineSegment(sketch, "E7683", {"start": v(142.9, -195) * mm, "end": v(137.2, -191.1) * mm});
            skLineSegment(sketch, "E7684", {"start": v(137.2, -191.1) * mm, "end": v(131.45, -187.16) * mm});
            skLineSegment(sketch, "E7685", {"start": v(131.45, -187.16) * mm, "end": v(125.73, -183.22) * mm});
            skLineSegment(sketch, "E7686", {"start": v(125.73, -183.22) * mm, "end": v(120.04, -179.31) * mm});
            skLineSegment(sketch, "E7687", {"start": v(120.04, -179.31) * mm, "end": v(114.43, -175.45) * mm});
            skLineSegment(sketch, "E7688", {"start": v(114.43, -175.45) * mm, "end": v(108.93, -171.66) * mm});
            skLineSegment(sketch, "E7689", {"start": v(108.93, -171.66) * mm, "end": v(103.57, -167.97) * mm});
            skLineSegment(sketch, "E7690", {"start": v(103.57, -167.97) * mm, "end": v(98.39, -164.4) * mm});
            skLineSegment(sketch, "E7691", {"start": v(98.39, -164.4) * mm, "end": v(93.41, -160.97) * mm});
            skLineSegment(sketch, "E7692", {"start": v(93.41, -160.97) * mm, "end": v(88.68, -157.7) * mm});
            skLineSegment(sketch, "E7693", {"start": v(88.68, -157.7) * mm, "end": v(84.22, -154.64) * mm});
            skLineSegment(sketch, "E7694", {"start": v(84.22, -154.64) * mm, "end": v(80.07, -151.8) * mm});
            skLineSegment(sketch, "E7695", {"start": v(80.07, -151.8) * mm, "end": v(76.27, -149.19) * mm});
            skLineSegment(sketch, "E7696", {"start": v(76.27, -149.19) * mm, "end": v(72.83, -146.85) * mm});
            skLineSegment(sketch, "E7697", {"start": v(72.83, -146.85) * mm, "end": v(69.8, -144.8) * mm});
            skLineSegment(sketch, "E7698", {"start": v(69.8, -144.8) * mm, "end": v(67.22, -143.06) * mm});
            skLineSegment(sketch, "E7699", {"start": v(67.22, -143.06) * mm, "end": v(65.1, -141.66) * mm});
            skLineSegment(sketch, "E7700", {"start": v(65.1, -141.66) * mm, "end": v(63.9, -140.87) * mm});
            skLineSegment(sketch, "E7701", {"start": v(63.9, -140.87) * mm, "end": v(63.5, -140.62) * mm});
            skLineSegment(sketch, "E7702", {"start": v(63.5, -140.62) * mm, "end": v(59.2, -137.9) * mm});
            skLineSegment(sketch, "E7703", {"start": v(59.2, -137.9) * mm, "end": v(46.5, -129.39) * mm});
            skLineSegment(sketch, "E7704", {"start": v(46.5, -129.39) * mm, "end": v(30.97, -118.3) * mm});
            skLineSegment(sketch, "E7705", {"start": v(30.97, -118.3) * mm, "end": v(16.84, -107.4) * mm});
            skLineSegment(sketch, "E7706", {"start": v(16.84, -107.4) * mm, "end": v(4, -96.8) * mm});
            skLineSegment(sketch, "E7707", {"start": v(4, -96.8) * mm, "end": v(-7.67, -86.55) * mm});
            skLineSegment(sketch, "E7708", {"start": v(-7.67, -86.55) * mm, "end": v(-18.24, -76.72) * mm});
            skLineSegment(sketch, "E7709", {"start": v(-18.24, -76.72) * mm, "end": v(-27.82, -67.38) * mm});
            skLineSegment(sketch, "E7710", {"start": v(-27.82, -67.38) * mm, "end": v(-36.52, -58.61) * mm});
            skLineSegment(sketch, "E7711", {"start": v(-36.52, -58.61) * mm, "end": v(-44.43, -50.47) * mm});
            skLineSegment(sketch, "E7712", {"start": v(-44.43, -50.47) * mm, "end": v(-51.66, -43.04) * mm});
            skLineSegment(sketch, "E7713", {"start": v(-51.66, -43.04) * mm, "end": v(-58.3, -36.38) * mm});
            skLineSegment(sketch, "E7714", {"start": v(-58.3, -36.38) * mm, "end": v(-64.45, -30.57) * mm});
            skLineSegment(sketch, "E7715", {"start": v(-64.45, -30.57) * mm, "end": v(-70.21, -25.68) * mm});
            skLineSegment(sketch, "E7716", {"start": v(-70.21, -25.68) * mm, "end": v(-75.69, -21.78) * mm});
            skLineSegment(sketch, "E7717", {"start": v(-75.69, -21.78) * mm, "end": v(-80.98, -18.94) * mm});
            skLineSegment(sketch, "E7718", {"start": v(-80.98, -18.94) * mm, "end": v(-84.85, -17.52) * mm});
            skLineSegment(sketch, "E7719", {"start": v(-84.85, -17.52) * mm, "end": v(-86.18, -17.23) * mm});
            skLineSegment(sketch, "E7720", {"start": v(-86.18, -17.23) * mm, "end": v(-87.61, -16.92) * mm});
            skLineSegment(sketch, "E7721", {"start": v(-87.61, -16.92) * mm, "end": v(-91.98, -16.39) * mm});
            skLineSegment(sketch, "E7722", {"start": v(-91.98, -16.39) * mm, "end": v(-97.53, -16.36) * mm});
            skLineSegment(sketch, "E7723", {"start": v(-97.53, -16.36) * mm, "end": v(-102.91, -17.05) * mm});
            skLineSegment(sketch, "E7724", {"start": v(-102.91, -17.05) * mm, "end": v(-108.2, -18.34) * mm});
            skLineSegment(sketch, "E7725", {"start": v(-108.2, -18.34) * mm, "end": v(-113.45, -20.16) * mm});
            skLineSegment(sketch, "E7726", {"start": v(-113.45, -20.16) * mm, "end": v(-118.75, -22.4) * mm});
            skLineSegment(sketch, "E7727", {"start": v(-118.75, -22.4) * mm, "end": v(-124.16, -24.97) * mm});
            skLineSegment(sketch, "E7728", {"start": v(-124.16, -24.97) * mm, "end": v(-129.77, -27.75) * mm});
            skLineSegment(sketch, "E7729", {"start": v(-129.77, -27.75) * mm, "end": v(-135.63, -30.67) * mm});
            skLineSegment(sketch, "E7730", {"start": v(-135.63, -30.67) * mm, "end": v(-141.83, -33.62) * mm});
            skLineSegment(sketch, "E7731", {"start": v(-141.83, -33.62) * mm, "end": v(-148.44, -36.5) * mm});
            skLineSegment(sketch, "E7732", {"start": v(-148.44, -36.5) * mm, "end": v(-155.52, -39.2) * mm});
            skLineSegment(sketch, "E7733", {"start": v(-155.52, -39.2) * mm, "end": v(-163.15, -41.66) * mm});
            skLineSegment(sketch, "E7734", {"start": v(-163.15, -41.66) * mm, "end": v(-171.4, -43.74) * mm});
            skLineSegment(sketch, "E7735", {"start": v(-171.4, -43.74) * mm, "end": v(-180.35, -45.37) * mm});
            skLineSegment(sketch, "E7736", {"start": v(-180.35, -45.37) * mm, "end": v(-187.63, -46.25) * mm});
            skLineSegment(sketch, "E7737", {"start": v(-187.63, -46.25) * mm, "end": v(-190.07, -46.43) * mm});
            skLineSegment(sketch, "E7738", {"start": v(-190.07, -46.43) * mm, "end": v(-191.06, -46.51) * mm});
            skLineSegment(sketch, "E7739", {"start": v(-191.06, -46.51) * mm, "end": v(-194.07, -46.36) * mm});
            skLineSegment(sketch, "E7740", {"start": v(-194.07, -46.36) * mm, "end": v(-199.88, -45.7) * mm});
            skLineSegment(sketch, "E7741", {"start": v(-199.88, -45.7) * mm, "end": v(-207.24, -44.57) * mm});
            skLineSegment(sketch, "E7742", {"start": v(-207.24, -44.57) * mm, "end": v(-215.9, -43.03) * mm});
            skLineSegment(sketch, "E7743", {"start": v(-215.9, -43.03) * mm, "end": v(-225.6, -41.14) * mm});
            skLineSegment(sketch, "E7744", {"start": v(-225.6, -41.14) * mm, "end": v(-236.1, -39) * mm});
            skLineSegment(sketch, "E7745", {"start": v(-236.1, -39) * mm, "end": v(-247.16, -36.66) * mm});
            skLineSegment(sketch, "E7746", {"start": v(-247.16, -36.66) * mm, "end": v(-258.53, -34.21) * mm});
            skLineSegment(sketch, "E7747", {"start": v(-258.53, -34.21) * mm, "end": v(-269.94, -31.74) * mm});
            skLineSegment(sketch, "E7748", {"start": v(-269.94, -31.74) * mm, "end": v(-281.17, -29.3) * mm});
            skLineSegment(sketch, "E7749", {"start": v(-281.17, -29.3) * mm, "end": v(-291.95, -26.98) * mm});
            skLineSegment(sketch, "E7750", {"start": v(-291.95, -26.98) * mm, "end": v(-302.04, -24.85) * mm});
            skLineSegment(sketch, "E7751", {"start": v(-302.04, -24.85) * mm, "end": v(-311.19, -23) * mm});
            skLineSegment(sketch, "E7752", {"start": v(-311.19, -23) * mm, "end": v(-319.15, -21.48) * mm});
            skLineSegment(sketch, "E7753", {"start": v(-319.15, -21.48) * mm, "end": v(-325.67, -20.39) * mm});
            skLineSegment(sketch, "E7754", {"start": v(-325.67, -20.39) * mm, "end": v(-329.28, -19.89) * mm});
            skLineSegment(sketch, "E7755", {"start": v(-329.28, -19.89) * mm, "end": v(-330.5, -19.79) * mm});
            skLineSegment(sketch, "E7756", {"start": v(-330.5, -19.79) * mm, "end": v(-331.17, -19.73) * mm});
            skLineSegment(sketch, "E7757", {"start": v(-331.17, -19.73) * mm, "end": v(-333.19, -19.57) * mm});
            skLineSegment(sketch, "E7758", {"start": v(-333.19, -19.57) * mm, "end": v(-336.37, -19.33) * mm});
            skLineSegment(sketch, "E7759", {"start": v(-336.37, -19.33) * mm, "end": v(-340.02, -19.08) * mm});
            skLineSegment(sketch, "E7760", {"start": v(-340.02, -19.08) * mm, "end": v(-344.08, -18.8) * mm});
            skLineSegment(sketch, "E7761", {"start": v(-344.08, -18.8) * mm, "end": v(-348.53, -18.5) * mm});
            skLineSegment(sketch, "E7762", {"start": v(-348.53, -18.5) * mm, "end": v(-353.32, -18.19) * mm});
            skLineSegment(sketch, "E7763", {"start": v(-353.32, -18.19) * mm, "end": v(-358.42, -17.86) * mm});
            skLineSegment(sketch, "E7764", {"start": v(-358.42, -17.86) * mm, "end": v(-363.8, -17.53) * mm});
            skLineSegment(sketch, "E7765", {"start": v(-363.8, -17.53) * mm, "end": v(-369.39, -17.18) * mm});
            skLineSegment(sketch, "E7766", {"start": v(-369.39, -17.18) * mm, "end": v(-375.18, -16.82) * mm});
            skLineSegment(sketch, "E7767", {"start": v(-375.18, -16.82) * mm, "end": v(-381.12, -16.46) * mm});
            skLineSegment(sketch, "E7768", {"start": v(-381.12, -16.46) * mm, "end": v(-387.18, -16.1) * mm});
            skLineSegment(sketch, "E7769", {"start": v(-387.18, -16.1) * mm, "end": v(-393.31, -15.73) * mm});
            skLineSegment(sketch, "E7770", {"start": v(-393.31, -15.73) * mm, "end": v(-399.49, -15.37) * mm});
            skLineSegment(sketch, "E7771", {"start": v(-399.49, -15.37) * mm, "end": v(-405.66, -15) * mm});
            skLineSegment(sketch, "E7772", {"start": v(-405.66, -15) * mm, "end": v(-411.8, -14.64) * mm});
            skLineSegment(sketch, "E7773", {"start": v(-411.8, -14.64) * mm, "end": v(-417.86, -14.3) * mm});
            skLineSegment(sketch, "E7774", {"start": v(-417.86, -14.3) * mm, "end": v(-423.8, -13.95) * mm});
            skLineSegment(sketch, "E7775", {"start": v(-423.8, -13.95) * mm, "end": v(-429.6, -13.61) * mm});
            skLineSegment(sketch, "E7776", {"start": v(-429.6, -13.61) * mm, "end": v(-435.2, -13.3) * mm});
            skLineSegment(sketch, "E7777", {"start": v(-435.2, -13.3) * mm, "end": v(-440.58, -12.98) * mm});
            skLineSegment(sketch, "E7778", {"start": v(-440.58, -12.98) * mm, "end": v(-445.69, -12.7) * mm});
            skLineSegment(sketch, "E7779", {"start": v(-445.69, -12.7) * mm, "end": v(-450.5, -12.42) * mm});
            skLineSegment(sketch, "E7780", {"start": v(-450.5, -12.42) * mm, "end": v(-454.95, -12.17) * mm});
            skLineSegment(sketch, "E7781", {"start": v(-454.95, -12.17) * mm, "end": v(-459.03, -11.93) * mm});
            skLineSegment(sketch, "E7782", {"start": v(-459.03, -11.93) * mm, "end": v(-462.69, -11.73) * mm});
            skLineSegment(sketch, "E7783", {"start": v(-462.69, -11.73) * mm, "end": v(-465.89, -11.55) * mm});
            skLineSegment(sketch, "E7784", {"start": v(-465.89, -11.55) * mm, "end": v(-468.6, -11.4) * mm});
            skLineSegment(sketch, "E7785", {"start": v(-468.6, -11.4) * mm, "end": v(-470.76, -11.28) * mm});
            skLineSegment(sketch, "E7786", {"start": v(-470.76, -11.28) * mm, "end": v(-472.36, -11.19) * mm});
            skLineSegment(sketch, "E7787", {"start": v(-472.36, -11.19) * mm, "end": v(-473.35, -11.13) * mm});
            skLineSegment(sketch, "E7788", {"start": v(-473.35, -11.13) * mm, "end": v(-473.68, -11.11) * mm});
            skLineSegment(sketch, "E7789", {"start": v(435.87, -589.68) * mm, "end": v(433.96, -589.53) * mm});
            skLineSegment(sketch, "E7790", {"start": v(433.96, -589.53) * mm, "end": v(428.24, -588.81) * mm});
            skLineSegment(sketch, "E7791", {"start": v(428.24, -588.81) * mm, "end": v(418.98, -587.3) * mm});
            skLineSegment(sketch, "E7792", {"start": v(418.98, -587.3) * mm, "end": v(408.3, -585.19) * mm});
            skLineSegment(sketch, "E7793", {"start": v(408.3, -585.19) * mm, "end": v(396.35, -582.54) * mm});
            skLineSegment(sketch, "E7794", {"start": v(396.35, -582.54) * mm, "end": v(383.34, -579.4) * mm});
            skLineSegment(sketch, "E7795", {"start": v(383.34, -579.4) * mm, "end": v(369.44, -575.82) * mm});
            skLineSegment(sketch, "E7796", {"start": v(369.44, -575.82) * mm, "end": v(354.83, -571.86) * mm});
            skLineSegment(sketch, "E7797", {"start": v(354.83, -571.86) * mm, "end": v(339.7, -567.56) * mm});
            skLineSegment(sketch, "E7798", {"start": v(339.7, -567.56) * mm, "end": v(324.24, -562.98) * mm});
            skLineSegment(sketch, "E7799", {"start": v(324.24, -562.98) * mm, "end": v(308.6, -558.16) * mm});
            skLineSegment(sketch, "E7800", {"start": v(308.6, -558.16) * mm, "end": v(293, -553.17) * mm});
            skLineSegment(sketch, "E7801", {"start": v(293, -553.17) * mm, "end": v(277.6, -548.04) * mm});
            skLineSegment(sketch, "E7802", {"start": v(277.6, -548.04) * mm, "end": v(262.6, -542.84) * mm});
            skLineSegment(sketch, "E7803", {"start": v(262.6, -542.84) * mm, "end": v(248.16, -537.62) * mm});
            skLineSegment(sketch, "E7804", {"start": v(248.16, -537.62) * mm, "end": v(234.48, -532.42) * mm});
            skLineSegment(sketch, "E7805", {"start": v(234.48, -532.42) * mm, "end": v(224.9, -528.61) * mm});
            skLineSegment(sketch, "E7806", {"start": v(224.9, -528.61) * mm, "end": v(221.73, -527.3) * mm});
            skLineSegment(sketch, "E7807", {"start": v(221.73, -527.3) * mm, "end": v(218.63, -526.01) * mm});
            skLineSegment(sketch, "E7808", {"start": v(218.63, -526.01) * mm, "end": v(209.38, -521.98) * mm});
            skLineSegment(sketch, "E7809", {"start": v(209.38, -521.98) * mm, "end": v(196.76, -516.16) * mm});
            skLineSegment(sketch, "E7810", {"start": v(196.76, -516.16) * mm, "end": v(183.87, -509.88) * mm});
            skLineSegment(sketch, "E7811", {"start": v(183.87, -509.88) * mm, "end": v(170.7, -503.16) * mm});
            skLineSegment(sketch, "E7812", {"start": v(170.7, -503.16) * mm, "end": v(157.27, -496.04) * mm});
            skLineSegment(sketch, "E7813", {"start": v(157.27, -496.04) * mm, "end": v(143.55, -488.55) * mm});
            skLineSegment(sketch, "E7814", {"start": v(143.55, -488.55) * mm, "end": v(129.55, -480.73) * mm});
            skLineSegment(sketch, "E7815", {"start": v(129.55, -480.73) * mm, "end": v(115.26, -472.6) * mm});
            skLineSegment(sketch, "E7816", {"start": v(115.26, -472.6) * mm, "end": v(100.68, -464.19) * mm});
            skLineSegment(sketch, "E7817", {"start": v(100.68, -464.19) * mm, "end": v(85.82, -455.53) * mm});
            skLineSegment(sketch, "E7818", {"start": v(85.82, -455.53) * mm, "end": v(70.66, -446.67) * mm});
            skLineSegment(sketch, "E7819", {"start": v(70.66, -446.67) * mm, "end": v(55.2, -437.63) * mm});
            skLineSegment(sketch, "E7820", {"start": v(55.2, -437.63) * mm, "end": v(39.46, -428.43) * mm});
            skLineSegment(sketch, "E7821", {"start": v(39.46, -428.43) * mm, "end": v(23.4, -419.12) * mm});
            skLineSegment(sketch, "E7822", {"start": v(23.4, -419.12) * mm, "end": v(7.04, -409.73) * mm});
            skLineSegment(sketch, "E7823", {"start": v(7.04, -409.73) * mm, "end": v(-5.45, -402.63) * mm});
            skLineSegment(sketch, "E7824", {"start": v(-5.45, -402.63) * mm, "end": v(-9.63, -400.28) * mm});
            skLineSegment(sketch, "E7825", {"start": v(-9.63, -400.28) * mm, "end": v(-11.7, -399.11) * mm});
            skLineSegment(sketch, "E7826", {"start": v(-11.7, -399.11) * mm, "end": v(-17.85, -395.47) * mm});
            skLineSegment(sketch, "E7827", {"start": v(-17.85, -395.47) * mm, "end": v(-25.73, -390.54) * mm});
            skLineSegment(sketch, "E7828", {"start": v(-25.73, -390.54) * mm, "end": v(-33.26, -385.48) * mm});
            skLineSegment(sketch, "E7829", {"start": v(-33.26, -385.48) * mm, "end": v(-40.46, -380.32) * mm});
            skLineSegment(sketch, "E7830", {"start": v(-40.46, -380.32) * mm, "end": v(-47.33, -375.08) * mm});
            skLineSegment(sketch, "E7831", {"start": v(-47.33, -375.08) * mm, "end": v(-53.9, -369.77) * mm});
            skLineSegment(sketch, "E7832", {"start": v(-53.9, -369.77) * mm, "end": v(-60.16, -364.41) * mm});
            skLineSegment(sketch, "E7833", {"start": v(-60.16, -364.41) * mm, "end": v(-66.14, -359.02) * mm});
            skLineSegment(sketch, "E7834", {"start": v(-66.14, -359.02) * mm, "end": v(-71.84, -353.62) * mm});
            skLineSegment(sketch, "E7835", {"start": v(-71.84, -353.62) * mm, "end": v(-77.27, -348.2) * mm});
            skLineSegment(sketch, "E7836", {"start": v(-77.27, -348.2) * mm, "end": v(-82.45, -342.82) * mm});
            skLineSegment(sketch, "E7837", {"start": v(-82.45, -342.82) * mm, "end": v(-87.4, -337.46) * mm});
            skLineSegment(sketch, "E7838", {"start": v(-87.4, -337.46) * mm, "end": v(-92.1, -332.15) * mm});
            skLineSegment(sketch, "E7839", {"start": v(-92.1, -332.15) * mm, "end": v(-96.6, -326.92) * mm});
            skLineSegment(sketch, "E7840", {"start": v(-96.6, -326.92) * mm, "end": v(-100.87, -321.76) * mm});
            skLineSegment(sketch, "E7841", {"start": v(-100.87, -321.76) * mm, "end": v(-104.96, -316.7) * mm});
            skLineSegment(sketch, "E7842", {"start": v(-104.96, -316.7) * mm, "end": v(-108.86, -311.77) * mm});
            skLineSegment(sketch, "E7843", {"start": v(-108.86, -311.77) * mm, "end": v(-112.58, -306.97) * mm});
            skLineSegment(sketch, "E7844", {"start": v(-112.58, -306.97) * mm, "end": v(-116.14, -302.32) * mm});
            skLineSegment(sketch, "E7845", {"start": v(-116.14, -302.32) * mm, "end": v(-119.55, -297.83) * mm});
            skLineSegment(sketch, "E7846", {"start": v(-119.55, -297.83) * mm, "end": v(-122.82, -293.54) * mm});
            skLineSegment(sketch, "E7847", {"start": v(-122.82, -293.54) * mm, "end": v(-125.96, -289.44) * mm});
            skLineSegment(sketch, "E7848", {"start": v(-125.96, -289.44) * mm, "end": v(-128.99, -285.56) * mm});
            skLineSegment(sketch, "E7849", {"start": v(-128.99, -285.56) * mm, "end": v(-131.9, -281.91) * mm});
            skLineSegment(sketch, "E7850", {"start": v(-131.9, -281.91) * mm, "end": v(-134.73, -278.52) * mm});
            skLineSegment(sketch, "E7851", {"start": v(-134.73, -278.52) * mm, "end": v(-137.47, -275.4) * mm});
            skLineSegment(sketch, "E7852", {"start": v(-137.47, -275.4) * mm, "end": v(-140.14, -272.56) * mm});
            skLineSegment(sketch, "E7853", {"start": v(-140.14, -272.56) * mm, "end": v(-142.74, -270.03) * mm});
            skLineSegment(sketch, "E7854", {"start": v(-142.74, -270.03) * mm, "end": v(-145.3, -267.81) * mm});
            skLineSegment(sketch, "E7855", {"start": v(-145.3, -267.81) * mm, "end": v(-147.82, -265.93) * mm});
            skLineSegment(sketch, "E7856", {"start": v(-147.82, -265.93) * mm, "end": v(-150.3, -264.4) * mm});
            skLineSegment(sketch, "E7857", {"start": v(-150.3, -264.4) * mm, "end": v(-152.15, -263.48) * mm});
            skLineSegment(sketch, "E7858", {"start": v(-152.15, -263.48) * mm, "end": v(-152.78, -263.24) * mm});
            skLineSegment(sketch, "E7859", {"start": v(-152.78, -263.24) * mm, "end": v(-155.2, -262.29) * mm});
            skLineSegment(sketch, "E7860", {"start": v(-155.2, -262.29) * mm, "end": v(-162.62, -259.93) * mm});
            skLineSegment(sketch, "E7861", {"start": v(-162.62, -259.93) * mm, "end": v(-172.22, -257.7) * mm});
            skLineSegment(sketch, "E7862", {"start": v(-172.22, -257.7) * mm, "end": v(-181.45, -256.43) * mm});
            skLineSegment(sketch, "E7863", {"start": v(-181.45, -256.43) * mm, "end": v(-190.15, -256.01) * mm});
            skLineSegment(sketch, "E7864", {"start": v(-190.15, -256.01) * mm, "end": v(-198.18, -256.33) * mm});
            skLineSegment(sketch, "E7865", {"start": v(-198.18, -256.33) * mm, "end": v(-205.38, -257.26) * mm});
            skLineSegment(sketch, "E7866", {"start": v(-205.38, -257.26) * mm, "end": v(-211.6, -258.7) * mm});
            skLineSegment(sketch, "E7867", {"start": v(-211.6, -258.7) * mm, "end": v(-215.48, -259.99) * mm});
            skLineSegment(sketch, "E7868", {"start": v(-215.48, -259.99) * mm, "end": v(-216.71, -260.54) * mm});
            skLineSegment(sketch, "E7869", {"start": v(-216.71, -260.54) * mm, "end": v(-218.4, -261.28) * mm});
            skLineSegment(sketch, "E7870", {"start": v(-218.4, -261.28) * mm, "end": v(-223.52, -263.34) * mm});
            skLineSegment(sketch, "E7871", {"start": v(-223.52, -263.34) * mm, "end": v(-230.98, -265.95) * mm});
            skLineSegment(sketch, "E7872", {"start": v(-230.98, -265.95) * mm, "end": v(-239.07, -268.3) * mm});
            skLineSegment(sketch, "E7873", {"start": v(-239.07, -268.3) * mm, "end": v(-247.82, -270.3) * mm});
            skLineSegment(sketch, "E7874", {"start": v(-247.82, -270.3) * mm, "end": v(-257.2, -271.88) * mm});
            skLineSegment(sketch, "E7875", {"start": v(-257.2, -271.88) * mm, "end": v(-267.24, -272.96) * mm});
            skLineSegment(sketch, "E7876", {"start": v(-267.24, -272.96) * mm, "end": v(-277.93, -273.46) * mm});
            skLineSegment(sketch, "E7877", {"start": v(-277.93, -273.46) * mm, "end": v(-286.43, -273.43) * mm});
            skLineSegment(sketch, "E7878", {"start": v(-286.43, -273.43) * mm, "end": v(-289.26, -273.3) * mm});
            skLineSegment(sketch, "E7879", {"start": v(-289.26, -273.3) * mm, "end": v(-292.78, -273.13) * mm});
            skLineSegment(sketch, "E7880", {"start": v(-292.78, -273.13) * mm, "end": v(-303.33, -272.37) * mm});
            skLineSegment(sketch, "E7881", {"start": v(-303.33, -272.37) * mm, "end": v(-316.09, -271.06) * mm});
            skLineSegment(sketch, "E7882", {"start": v(-316.09, -271.06) * mm, "end": v(-327.9, -269.38) * mm});
            skLineSegment(sketch, "E7883", {"start": v(-327.9, -269.38) * mm, "end": v(-339.17, -267.32) * mm});
            skLineSegment(sketch, "E7884", {"start": v(-339.17, -267.32) * mm, "end": v(-350.26, -264.88) * mm});
            skLineSegment(sketch, "E7885", {"start": v(-350.26, -264.88) * mm, "end": v(-361.56, -262.06) * mm});
            skLineSegment(sketch, "E7886", {"start": v(-361.56, -262.06) * mm, "end": v(-373.45, -258.84) * mm});
            skLineSegment(sketch, "E7887", {"start": v(-373.45, -258.84) * mm, "end": v(-383.1, -256.13) * mm});
            skLineSegment(sketch, "E7888", {"start": v(-383.1, -256.13) * mm, "end": v(-386.3, -255.22) * mm});
            skLineSegment(sketch, "E7889", {"start": v(-386.3, -255.22) * mm, "end": v(-387.4, -254.91) * mm});
            skLineSegment(sketch, "E7890", {"start": v(-387.4, -254.91) * mm, "end": v(-390.66, -253.88) * mm});
            skLineSegment(sketch, "E7891", {"start": v(-390.66, -253.88) * mm, "end": v(-395.08, -252.36) * mm});
            skLineSegment(sketch, "E7892", {"start": v(-395.08, -252.36) * mm, "end": v(-399.63, -250.73) * mm});
            skLineSegment(sketch, "E7893", {"start": v(-399.63, -250.73) * mm, "end": v(-404.37, -249.05) * mm});
            skLineSegment(sketch, "E7894", {"start": v(-404.37, -249.05) * mm, "end": v(-409.35, -247.4) * mm});
            skLineSegment(sketch, "E7895", {"start": v(-409.35, -247.4) * mm, "end": v(-414.62, -245.87) * mm});
            skLineSegment(sketch, "E7896", {"start": v(-414.62, -245.87) * mm, "end": v(-420.25, -244.5) * mm});
            skLineSegment(sketch, "E7897", {"start": v(-420.25, -244.5) * mm, "end": v(-424.77, -243.62) * mm});
            skLineSegment(sketch, "E7898", {"start": v(-424.77, -243.62) * mm, "end": v(-426.29, -243.38) * mm});
            skLineSegment(sketch, "E7899", {"start": v(125.65, -626.75) * mm, "end": v(122.54, -625.46) * mm});
            skLineSegment(sketch, "E7900", {"start": v(122.54, -625.46) * mm, "end": v(113.3, -621.42) * mm});
            skLineSegment(sketch, "E7901", {"start": v(113.3, -621.42) * mm, "end": v(100.67, -615.6) * mm});
            skLineSegment(sketch, "E7902", {"start": v(100.67, -615.6) * mm, "end": v(87.78, -609.32) * mm});
            skLineSegment(sketch, "E7903", {"start": v(87.78, -609.32) * mm, "end": v(74.62, -602.6) * mm});
            skLineSegment(sketch, "E7904", {"start": v(74.62, -602.6) * mm, "end": v(61.18, -595.49) * mm});
            skLineSegment(sketch, "E7905", {"start": v(61.18, -595.49) * mm, "end": v(47.46, -588) * mm});
            skLineSegment(sketch, "E7906", {"start": v(47.46, -588) * mm, "end": v(33.46, -580.17) * mm});
            skLineSegment(sketch, "E7907", {"start": v(33.46, -580.17) * mm, "end": v(19.17, -572.04) * mm});
            skLineSegment(sketch, "E7908", {"start": v(19.17, -572.04) * mm, "end": v(4.6, -563.63) * mm});
            skLineSegment(sketch, "E7909", {"start": v(4.6, -563.63) * mm, "end": v(-10.27, -554.98) * mm});
            skLineSegment(sketch, "E7910", {"start": v(-10.27, -554.98) * mm, "end": v(-25.42, -546.12) * mm});
            skLineSegment(sketch, "E7911", {"start": v(-25.42, -546.12) * mm, "end": v(-40.88, -537.07) * mm});
            skLineSegment(sketch, "E7912", {"start": v(-40.88, -537.07) * mm, "end": v(-56.63, -527.88) * mm});
            skLineSegment(sketch, "E7913", {"start": v(-56.63, -527.88) * mm, "end": v(-72.69, -518.57) * mm});
            skLineSegment(sketch, "E7914", {"start": v(-72.69, -518.57) * mm, "end": v(-89.05, -509.18) * mm});
            skLineSegment(sketch, "E7915", {"start": v(-89.05, -509.18) * mm, "end": v(-101.54, -502.07) * mm});
            skLineSegment(sketch, "E7916", {"start": v(-101.54, -502.07) * mm, "end": v(-105.71, -499.72) * mm});
            skLineSegment(sketch, "E7917", {"start": v(-105.71, -499.72) * mm, "end": v(-107.79, -498.56) * mm});
            skLineSegment(sketch, "E7918", {"start": v(-107.79, -498.56) * mm, "end": v(-113.94, -494.92) * mm});
            skLineSegment(sketch, "E7919", {"start": v(-113.94, -494.92) * mm, "end": v(-121.82, -489.98) * mm});
            skLineSegment(sketch, "E7920", {"start": v(-121.82, -489.98) * mm, "end": v(-129.35, -484.92) * mm});
            skLineSegment(sketch, "E7921", {"start": v(-129.35, -484.92) * mm, "end": v(-136.54, -479.77) * mm});
            skLineSegment(sketch, "E7922", {"start": v(-136.54, -479.77) * mm, "end": v(-143.41, -474.53) * mm});
            skLineSegment(sketch, "E7923", {"start": v(-143.41, -474.53) * mm, "end": v(-149.98, -469.22) * mm});
            skLineSegment(sketch, "E7924", {"start": v(-149.98, -469.22) * mm, "end": v(-156.25, -463.86) * mm});
            skLineSegment(sketch, "E7925", {"start": v(-156.25, -463.86) * mm, "end": v(-162.22, -458.47) * mm});
            skLineSegment(sketch, "E7926", {"start": v(-162.22, -458.47) * mm, "end": v(-167.92, -453.06) * mm});
            skLineSegment(sketch, "E7927", {"start": v(-167.92, -453.06) * mm, "end": v(-173.36, -447.65) * mm});
            skLineSegment(sketch, "E7928", {"start": v(-173.36, -447.65) * mm, "end": v(-178.54, -442.26) * mm});
            skLineSegment(sketch, "E7929", {"start": v(-178.54, -442.26) * mm, "end": v(-183.48, -436.9) * mm});
            skLineSegment(sketch, "E7930", {"start": v(-183.48, -436.9) * mm, "end": v(-188.19, -431.6) * mm});
            skLineSegment(sketch, "E7931", {"start": v(-188.19, -431.6) * mm, "end": v(-192.68, -426.36) * mm});
            skLineSegment(sketch, "E7932", {"start": v(-192.68, -426.36) * mm, "end": v(-196.96, -421.2) * mm});
            skLineSegment(sketch, "E7933", {"start": v(-196.96, -421.2) * mm, "end": v(-201.04, -416.15) * mm});
            skLineSegment(sketch, "E7934", {"start": v(-201.04, -416.15) * mm, "end": v(-204.94, -411.22) * mm});
            skLineSegment(sketch, "E7935", {"start": v(-204.94, -411.22) * mm, "end": v(-208.67, -406.42) * mm});
            skLineSegment(sketch, "E7936", {"start": v(-208.67, -406.42) * mm, "end": v(-212.23, -401.76) * mm});
            skLineSegment(sketch, "E7937", {"start": v(-212.23, -401.76) * mm, "end": v(-215.64, -397.28) * mm});
            skLineSegment(sketch, "E7938", {"start": v(-215.64, -397.28) * mm, "end": v(-218.91, -392.98) * mm});
            skLineSegment(sketch, "E7939", {"start": v(-218.91, -392.98) * mm, "end": v(-222.05, -388.89) * mm});
            skLineSegment(sketch, "E7940", {"start": v(-222.05, -388.89) * mm, "end": v(-225.07, -385) * mm});
            skLineSegment(sketch, "E7941", {"start": v(-225.07, -385) * mm, "end": v(-228, -381.36) * mm});
            skLineSegment(sketch, "E7942", {"start": v(-228, -381.36) * mm, "end": v(-230.81, -377.97) * mm});
            skLineSegment(sketch, "E7943", {"start": v(-230.81, -377.97) * mm, "end": v(-233.55, -374.85) * mm});
            skLineSegment(sketch, "E7944", {"start": v(-233.55, -374.85) * mm, "end": v(-236.22, -372.01) * mm});
            skLineSegment(sketch, "E7945", {"start": v(-236.22, -372.01) * mm, "end": v(-238.83, -369.47) * mm});
            skLineSegment(sketch, "E7946", {"start": v(-238.83, -369.47) * mm, "end": v(-241.38, -367.25) * mm});
            skLineSegment(sketch, "E7947", {"start": v(-241.38, -367.25) * mm, "end": v(-243.9, -365.37) * mm});
            skLineSegment(sketch, "E7948", {"start": v(-243.9, -365.37) * mm, "end": v(-246.4, -363.84) * mm});
            skLineSegment(sketch, "E7949", {"start": v(-246.4, -363.84) * mm, "end": v(-248.24, -362.93) * mm});
            skLineSegment(sketch, "E7950", {"start": v(-248.24, -362.93) * mm, "end": v(-248.87, -362.68) * mm});
            skLineSegment(sketch, "E7951", {"start": v(-248.87, -362.68) * mm, "end": v(-251.28, -361.74) * mm});
            skLineSegment(sketch, "E7952", {"start": v(-251.28, -361.74) * mm, "end": v(-258.7, -359.38) * mm});
            skLineSegment(sketch, "E7953", {"start": v(-258.7, -359.38) * mm, "end": v(-268.3, -357.15) * mm});
            skLineSegment(sketch, "E7954", {"start": v(-268.3, -357.15) * mm, "end": v(-277.53, -355.88) * mm});
            skLineSegment(sketch, "E7955", {"start": v(-277.53, -355.88) * mm, "end": v(-286.23, -355.46) * mm});
            skLineSegment(sketch, "E7956", {"start": v(-286.23, -355.46) * mm, "end": v(-294.26, -355.77) * mm});
            skLineSegment(sketch, "E7957", {"start": v(-294.26, -355.77) * mm, "end": v(-301.46, -356.71) * mm});
            skLineSegment(sketch, "E7958", {"start": v(-301.46, -356.71) * mm, "end": v(-307.7, -358.15) * mm});
            skLineSegment(sketch, "E7959", {"start": v(-307.7, -358.15) * mm, "end": v(-311.56, -359.43) * mm});
            skLineSegment(sketch, "E7960", {"start": v(-311.56, -359.43) * mm, "end": v(-312.8, -359.98) * mm});
            skLineSegment(sketch, "E7961", {"start": v(-312.8, -359.98) * mm, "end": v(-314.48, -360.73) * mm});
            skLineSegment(sketch, "E7962", {"start": v(-314.48, -360.73) * mm, "end": v(-319.6, -362.79) * mm});
            skLineSegment(sketch, "E7963", {"start": v(-319.6, -362.79) * mm, "end": v(-327.06, -365.4) * mm});
            skLineSegment(sketch, "E7964", {"start": v(-327.06, -365.4) * mm, "end": v(-335.16, -367.75) * mm});
            skLineSegment(sketch, "E7965", {"start": v(-335.16, -367.75) * mm, "end": v(-343.9, -369.75) * mm});
            skLineSegment(sketch, "E7966", {"start": v(-343.9, -369.75) * mm, "end": v(-353.3, -371.33) * mm});
            skLineSegment(sketch, "E7967", {"start": v(-353.3, -371.33) * mm, "end": v(-363.33, -372.4) * mm});
            skLineSegment(sketch, "E7968", {"start": v(-363.33, -372.4) * mm, "end": v(-374.01, -372.91) * mm});
            skLineSegment(sketch, "E7969", {"start": v(-374.01, -372.91) * mm, "end": v(-382.52, -372.88) * mm});
            skLineSegment(sketch, "E7970", {"start": v(-382.52, -372.88) * mm, "end": v(-385.35, -372.76) * mm});
            skLineSegment(sketch, "E7971", {"start": v(-385.35, -372.76) * mm, "end": v(-386.69, -372.7) * mm});
            skLineSegment(sketch, "E7972", {"start": v(-386.69, -372.7) * mm, "end": v(-399.32, -371.83) * mm});
            skLineSegment(sketch, "E7973", {"start": v(-399.32, -371.83) * mm, "end": v(-400.51, -371.72) * mm});
            skLineSegment(sketch, "E7974", {"start": v(-117.5, -654.71) * mm, "end": v(-119.52, -653.54) * mm});
            skLineSegment(sketch, "E7975", {"start": v(-119.52, -653.54) * mm, "end": v(-125.53, -649.9) * mm});
            skLineSegment(sketch, "E7976", {"start": v(-125.53, -649.9) * mm, "end": v(-133.22, -644.98) * mm});
            skLineSegment(sketch, "E7977", {"start": v(-133.22, -644.98) * mm, "end": v(-140.58, -639.94) * mm});
            skLineSegment(sketch, "E7978", {"start": v(-140.58, -639.94) * mm, "end": v(-147.62, -634.81) * mm});
            skLineSegment(sketch, "E7979", {"start": v(-147.62, -634.81) * mm, "end": v(-154.34, -629.6) * mm});
            skLineSegment(sketch, "E7980", {"start": v(-154.34, -629.6) * mm, "end": v(-160.76, -624.33) * mm});
            skLineSegment(sketch, "E7981", {"start": v(-160.76, -624.33) * mm, "end": v(-166.89, -619.02) * mm});
            skLineSegment(sketch, "E7982", {"start": v(-166.89, -619.02) * mm, "end": v(-172.74, -613.68) * mm});
            skLineSegment(sketch, "E7983", {"start": v(-172.74, -613.68) * mm, "end": v(-178.32, -608.32) * mm});
            skLineSegment(sketch, "E7984", {"start": v(-178.32, -608.32) * mm, "end": v(-183.65, -602.97) * mm});
            skLineSegment(sketch, "E7985", {"start": v(-183.65, -602.97) * mm, "end": v(-188.73, -597.64) * mm});
            skLineSegment(sketch, "E7986", {"start": v(-188.73, -597.64) * mm, "end": v(-193.57, -592.34) * mm});
            skLineSegment(sketch, "E7987", {"start": v(-193.57, -592.34) * mm, "end": v(-198.2, -587.1) * mm});
            skLineSegment(sketch, "E7988", {"start": v(-198.2, -587.1) * mm, "end": v(-202.6, -581.93) * mm});
            skLineSegment(sketch, "E7989", {"start": v(-202.6, -581.93) * mm, "end": v(-206.8, -576.84) * mm});
            skLineSegment(sketch, "E7990", {"start": v(-206.8, -576.84) * mm, "end": v(-210.81, -571.85) * mm});
            skLineSegment(sketch, "E7991", {"start": v(-210.81, -571.85) * mm, "end": v(-214.65, -566.98) * mm});
            skLineSegment(sketch, "E7992", {"start": v(-214.65, -566.98) * mm, "end": v(-218.3, -562.25) * mm});
            skLineSegment(sketch, "E7993", {"start": v(-218.3, -562.25) * mm, "end": v(-221.82, -557.67) * mm});
            skLineSegment(sketch, "E7994", {"start": v(-221.82, -557.67) * mm, "end": v(-225.17, -553.25) * mm});
            skLineSegment(sketch, "E7995", {"start": v(-225.17, -553.25) * mm, "end": v(-228.4, -549.01) * mm});
            skLineSegment(sketch, "E7996", {"start": v(-228.4, -549.01) * mm, "end": v(-231.5, -544.98) * mm});
            skLineSegment(sketch, "E7997", {"start": v(-231.5, -544.98) * mm, "end": v(-234.48, -541.16) * mm});
            skLineSegment(sketch, "E7998", {"start": v(-234.48, -541.16) * mm, "end": v(-237.36, -537.57) * mm});
            skLineSegment(sketch, "E7999", {"start": v(-237.36, -537.57) * mm, "end": v(-240.15, -534.23) * mm});
            skLineSegment(sketch, "E8000", {"start": v(-240.15, -534.23) * mm, "end": v(-242.86, -531.16) * mm});
            skLineSegment(sketch, "E8001", {"start": v(-242.86, -531.16) * mm, "end": v(-245.5, -528.36) * mm});
            skLineSegment(sketch, "E8002", {"start": v(-245.5, -528.36) * mm, "end": v(-248.07, -525.86) * mm});
            skLineSegment(sketch, "E8003", {"start": v(-248.07, -525.86) * mm, "end": v(-250.6, -523.68) * mm});
            skLineSegment(sketch, "E8004", {"start": v(-250.6, -523.68) * mm, "end": v(-253.1, -521.83) * mm});
            skLineSegment(sketch, "E8005", {"start": v(-253.1, -521.83) * mm, "end": v(-255.56, -520.31) * mm});
            skLineSegment(sketch, "E8006", {"start": v(-255.56, -520.31) * mm, "end": v(-257.39, -519.42) * mm});
            skLineSegment(sketch, "E8007", {"start": v(-257.39, -519.42) * mm, "end": v(-258.01, -519.17) * mm});
            skLineSegment(sketch, "E8008", {"start": v(-258.01, -519.17) * mm, "end": v(-260.43, -518.22) * mm});
            skLineSegment(sketch, "E8009", {"start": v(-260.43, -518.22) * mm, "end": v(-267.85, -515.86) * mm});
            skLineSegment(sketch, "E8010", {"start": v(-267.85, -515.86) * mm, "end": v(-277.45, -513.63) * mm});
            skLineSegment(sketch, "E8011", {"start": v(-277.45, -513.63) * mm, "end": v(-286.68, -512.36) * mm});
            skLineSegment(sketch, "E8012", {"start": v(-286.68, -512.36) * mm, "end": v(-295.38, -511.94) * mm});
            skLineSegment(sketch, "E8013", {"start": v(-295.38, -511.94) * mm, "end": v(-303.4, -512.26) * mm});
            skLineSegment(sketch, "E8014", {"start": v(-303.4, -512.26) * mm, "end": v(-310.6, -513.2) * mm});
            skLineSegment(sketch, "E8015", {"start": v(-310.6, -513.2) * mm, "end": v(-316.84, -514.63) * mm});
            skLineSegment(sketch, "E8016", {"start": v(-316.84, -514.63) * mm, "end": v(-320.7, -515.92) * mm});
            skLineSegment(sketch, "E8017", {"start": v(-320.7, -515.92) * mm, "end": v(-321.95, -516.47) * mm});
            skLineSegment(sketch, "E8018", {"start": v(-321.95, -516.47) * mm, "end": v(-324.36, -517.54) * mm});
            skLineSegment(sketch, "E8019", {"start": v(-324.36, -517.54) * mm, "end": v(-331.78, -520.4) * mm});
            skLineSegment(sketch, "E8020", {"start": v(-331.78, -520.4) * mm, "end": v(-342.92, -523.86) * mm});
            skLineSegment(sketch, "E8021", {"start": v(-342.92, -523.86) * mm, "end": v(-355.35, -526.67) * mm});
            skLineSegment(sketch, "E8022", {"start": v(-355.35, -526.67) * mm, "end": v(-365.63, -528.26) * mm});
            skLineSegment(sketch, "E8023", {"start": v(-365.63, -528.26) * mm, "end": v(-369.07, -528.6) * mm});
            skLineSegment(sketch, "E8024", {"start": v(421.64, 662.1) * mm, "end": v(420.87, 661.84) * mm});
            skLineSegment(sketch, "E8025", {"start": v(420.87, 661.84) * mm, "end": v(418.58, 661.02) * mm});
            skLineSegment(sketch, "E8026", {"start": v(418.58, 661.02) * mm, "end": v(415.25, 659.82) * mm});
            skLineSegment(sketch, "E8027", {"start": v(415.25, 659.82) * mm, "end": v(411.67, 658.58) * mm});
            skLineSegment(sketch, "E8028", {"start": v(411.67, 658.58) * mm, "end": v(407.87, 657.38) * mm});
            skLineSegment(sketch, "E8029", {"start": v(407.87, 657.38) * mm, "end": v(403.87, 656.33) * mm});
            skLineSegment(sketch, "E8030", {"start": v(403.87, 656.33) * mm, "end": v(399.7, 655.5) * mm});
            skLineSegment(sketch, "E8031", {"start": v(399.7, 655.5) * mm, "end": v(395.38, 655) * mm});
            skLineSegment(sketch, "E8032", {"start": v(395.38, 655) * mm, "end": v(392.05, 654.86) * mm});
            skLineSegment(sketch, "E8033", {"start": v(392.05, 654.86) * mm, "end": v(390.93, 654.9) * mm});
            skLineSegment(sketch, "E8034", {"start": v(390.93, 654.9) * mm, "end": v(390.33, 654.91) * mm});
            skLineSegment(sketch, "E8035", {"start": v(390.33, 654.91) * mm, "end": v(388.52, 655.05) * mm});
            skLineSegment(sketch, "E8036", {"start": v(388.52, 655.05) * mm, "end": v(385.82, 655.35) * mm});
            skLineSegment(sketch, "E8037", {"start": v(385.82, 655.35) * mm, "end": v(382.9, 655.79) * mm});
            skLineSegment(sketch, "E8038", {"start": v(382.9, 655.79) * mm, "end": v(379.8, 656.34) * mm});
            skLineSegment(sketch, "E8039", {"start": v(379.8, 656.34) * mm, "end": v(376.6, 656.97) * mm});
            skLineSegment(sketch, "E8040", {"start": v(376.6, 656.97) * mm, "end": v(373.37, 657.67) * mm});
            skLineSegment(sketch, "E8041", {"start": v(373.37, 657.67) * mm, "end": v(370.14, 658.41) * mm});
            skLineSegment(sketch, "E8042", {"start": v(370.14, 658.41) * mm, "end": v(367, 659.17) * mm});
            skLineSegment(sketch, "E8043", {"start": v(367, 659.17) * mm, "end": v(364, 659.93) * mm});
            skLineSegment(sketch, "E8044", {"start": v(364, 659.93) * mm, "end": v(361.2, 660.65) * mm});
            skLineSegment(sketch, "E8045", {"start": v(361.2, 660.65) * mm, "end": v(358.66, 661.33) * mm});
            skLineSegment(sketch, "E8046", {"start": v(358.66, 661.33) * mm, "end": v(356.45, 661.94) * mm});
            skLineSegment(sketch, "E8047", {"start": v(356.45, 661.94) * mm, "end": v(354.62, 662.45) * mm});
            skLineSegment(sketch, "E8048", {"start": v(354.62, 662.45) * mm, "end": v(353.24, 662.84) * mm});
            skLineSegment(sketch, "E8049", {"start": v(353.24, 662.84) * mm, "end": v(352.37, 663.1) * mm});
            skLineSegment(sketch, "E8050", {"start": v(352.37, 663.1) * mm, "end": v(352.07, 663.18) * mm});
            skSolve(sketch);
        }
        {
            var Q0;
            {var subQ0=sQuery(id+"F0.wireOp",EDGE,"E52");Q0=makeQuery(id+"F0.imprint","IMPRINT",FACE,{"disambiguationData":[TD([[makeQuery(id+"F0.imprint","IMPRINT",EDGE,{"derivedFrom":subQ0}),1.0]])]});}
            extrude(context, id + "F1", {"entities" : qUnion([Q0]), "depth" : 31.75 * mm});
        }
        {
            var Q0;
            {var subQ5=sQuery(id+"F0.wireOp",EDGE,"E46");Q0=makeQuery(id+"F0.imprint","IMPRINT",FACE,{"disambiguationData":[TD([[makeQuery(id+"F0.imprint","IMPRINT",EDGE,{"derivedFrom":subQ5}),1.0]])]});}
            var Q1;
            {var subQ8=sQuery(id+"F0.wireOp",EDGE,"E7900");Q1=makeQuery(id+"F0.imprint","IMPRINT",FACE,{"disambiguationData":[TD([[makeQuery(id+"F0.imprint","IMPRINT",EDGE,{"derivedFrom":subQ8}),1.0]])]});}
            extrude(context, id + "F2", {"entities" : qUnion([Q0, Q1]), "operationType" : NewBodyOperationType.ADD, "depth" : 63.5 * mm});
        }
        {
            var Q0;
            {var subQ10=sQuery(id+"F0.wireOp",EDGE,"E7801");Q0=makeQuery(id+"F0.imprint","IMPRINT",FACE,{"disambiguationData":[TD([[makeQuery(id+"F0.imprint","IMPRINT",EDGE,{"derivedFrom":subQ10}),1.0]])]});}
            var Q1;
            {var subQ4=sQuery(id+"F0.wireOp",EDGE,"E41");Q1=makeQuery(id+"F0.imprint","IMPRINT",FACE,{"disambiguationData":[TD([[makeQuery(id+"F0.imprint","IMPRINT",EDGE,{"derivedFrom":subQ4}),1.0]])]});}
            extrude(context, id + "F3", {"entities" : qUnion([Q0, Q1]), "operationType" : NewBodyOperationType.ADD, "depth" : 95.25 * mm});
        }
        {
            var Q0;
            {var subQ9=sQuery(id+"F0.wireOp",EDGE,"E7063");Q0=makeQuery(id+"F0.imprint","IMPRINT",FACE,{"disambiguationData":[TD([[makeQuery(id+"F0.imprint","IMPRINT",EDGE,{"derivedFrom":subQ9}),1.0]])]});}
            var Q1;
            {var subQ12=sQuery(id+"F0.wireOp",EDGE,"E37");Q1=makeQuery(id+"F0.imprint","IMPRINT",FACE,{"disambiguationData":[TD([[makeQuery(id+"F0.imprint","IMPRINT",EDGE,{"derivedFrom":subQ12}),1.0]])]});}
            var Q2;
            {var subQ10=sQuery(id+"F0.wireOp",EDGE,"E7038");Q2=makeQuery(id+"F0.imprint","IMPRINT",FACE,{"disambiguationData":[TD([[makeQuery(id+"F0.imprint","IMPRINT",EDGE,{"derivedFrom":subQ10}),1.0]])]});}
            extrude(context, id + "F4", {"entities" : qUnion([Q0, Q1, Q2]), "operationType" : NewBodyOperationType.ADD, "depth" : 127 * mm});
        }
        {
            var Q0;
            {var subQ11=sQuery(id+"F0.wireOp",EDGE,"E7063");Q0=makeQuery(id+"F0.imprint","IMPRINT",FACE,{"disambiguationData":[TD([[makeQuery(id+"F0.imprint","IMPRINT",EDGE,{"derivedFrom":subQ11}),-1.0]])]});}
            var Q1;
            {var subQ8=sQuery(id+"F0.wireOp",EDGE,"E7129");Q1=makeQuery(id+"F0.imprint","IMPRINT",FACE,{"disambiguationData":[TD([[makeQuery(id+"F0.imprint","IMPRINT",EDGE,{"derivedFrom":subQ8}),-1.0]])]});}
            var Q2;
            {var subQ9=sQuery(id+"F0.wireOp",EDGE,"E6913");Q2=makeQuery(id+"F0.imprint","IMPRINT",FACE,{"disambiguationData":[TD([[makeQuery(id+"F0.imprint","IMPRINT",EDGE,{"derivedFrom":subQ9}),1.0]])]});}
            extrude(context, id + "F5", {"entities" : qUnion([Q0, Q1, Q2]), "operationType" : NewBodyOperationType.ADD, "depth" : 133.35 * mm});
        }
        {
            var Q0;
            {var subQ4=sQuery(id+"F0.wireOp",EDGE,"E7226");Q0=makeQuery(id+"F0.imprint","IMPRINT",FACE,{"disambiguationData":[TD([[makeQuery(id+"F0.imprint","IMPRINT",EDGE,{"derivedFrom":subQ4}),-1.0]])]});}
            var Q1;
            {var subQ12=sQuery(id+"F0.wireOp",EDGE,"E7277");Q1=makeQuery(id+"F0.imprint","IMPRINT",FACE,{"disambiguationData":[TD([[makeQuery(id+"F0.imprint","IMPRINT",EDGE,{"derivedFrom":subQ12}),-1.0]])]});}
            extrude(context, id + "F6", {"entities" : qUnion([Q0, Q1]), "operationType" : NewBodyOperationType.ADD, "depth" : 139.7 * mm});
        }
        {
            var Q0;
            {var subQ8=sQuery(id+"F0.wireOp",EDGE,"E7363");Q0=makeQuery(id+"F0.imprint","IMPRINT",FACE,{"disambiguationData":[TD([[makeQuery(id+"F0.imprint","IMPRINT",EDGE,{"derivedFrom":subQ8}),-1.0]])]});}
            var Q1;
            {var subQ8=sQuery(id+"F0.wireOp",EDGE,"E7429");Q1=makeQuery(id+"F0.imprint","IMPRINT",FACE,{"disambiguationData":[TD([[makeQuery(id+"F0.imprint","IMPRINT",EDGE,{"derivedFrom":subQ8}),-1.0]])]});}
            extrude(context, id + "F7", {"entities" : qUnion([Q0, Q1]), "operationType" : NewBodyOperationType.ADD, "depth" : 146.05 * mm});
        }
        {
            var Q0;
            {var subQ8=sQuery(id+"F0.wireOp",EDGE,"E7513");Q0=makeQuery(id+"F0.imprint","IMPRINT",FACE,{"disambiguationData":[TD([[makeQuery(id+"F0.imprint","IMPRINT",EDGE,{"derivedFrom":subQ8}),-1.0]])]});}
            var Q1;
            {var subQ8=sQuery(id+"F0.wireOp",EDGE,"E7574");Q1=makeQuery(id+"F0.imprint","IMPRINT",FACE,{"disambiguationData":[TD([[makeQuery(id+"F0.imprint","IMPRINT",EDGE,{"derivedFrom":subQ8}),-1.0]])]});}
            extrude(context, id + "F8", {"entities" : qUnion([Q0, Q1]), "operationType" : NewBodyOperationType.ADD, "depth" : 152.4 * mm});
        }
        {
            var Q0;
            {var subQ14=sQuery(id+"F0.wireOp",EDGE,"E6704");Q0=makeQuery(id+"F0.imprint","IMPRINT",FACE,{"disambiguationData":[TD([[makeQuery(id+"F0.imprint","IMPRINT",EDGE,{"derivedFrom":subQ14}),1.0]])]});}
            var Q1;
            {var subQ8=sQuery(id+"F0.wireOp",EDGE,"E6653");Q1=makeQuery(id+"F0.imprint","IMPRINT",FACE,{"disambiguationData":[TD([[makeQuery(id+"F0.imprint","IMPRINT",EDGE,{"derivedFrom":subQ8}),1.0]])]});}
            extrude(context, id + "F9", {"entities" : qUnion([Q0, Q1]), "operationType" : NewBodyOperationType.ADD, "depth" : 158.75 * mm});
        }
        {
            var Q0;
            {var subQ4=sQuery(id+"F0.wireOp",EDGE,"E6653");Q0=makeQuery(id+"F0.imprint","IMPRINT",FACE,{"disambiguationData":[TD([[makeQuery(id+"F0.imprint","IMPRINT",EDGE,{"derivedFrom":subQ4}),-1.0]])]});}
            var Q1;
            {var subQ13=sQuery(id+"F0.wireOp",EDGE,"E6704");Q1=makeQuery(id+"F0.imprint","IMPRINT",FACE,{"disambiguationData":[TD([[makeQuery(id+"F0.imprint","IMPRINT",EDGE,{"derivedFrom":subQ13}),-1.0]])]});}
            extrude(context, id + "F10", {"entities" : qUnion([Q0, Q1]), "operationType" : NewBodyOperationType.ADD, "depth" : 165.1 * mm});
        }
        {
            var Q0;
            {var subQ4=sQuery(id+"F0.wireOp",EDGE,"E6811");Q0=makeQuery(id+"F0.imprint","IMPRINT",FACE,{"disambiguationData":[TD([[makeQuery(id+"F0.imprint","IMPRINT",EDGE,{"derivedFrom":subQ4}),-1.0]])]});}
            var Q1;
            {var subQ10=sQuery(id+"F0.wireOp",EDGE,"E6861");Q1=makeQuery(id+"F0.imprint","IMPRINT",FACE,{"disambiguationData":[TD([[makeQuery(id+"F0.imprint","IMPRINT",EDGE,{"derivedFrom":subQ10}),-1.0]])]});}
            extrude(context, id + "F11", {"entities" : qUnion([Q0, Q1]), "operationType" : NewBodyOperationType.ADD, "depth" : 171.45 * mm});
        }
        {
            var Q0;
            {var subQ8=sQuery(id+"F0.wireOp",EDGE,"E6109");Q0=makeQuery(id+"F0.imprint","IMPRINT",FACE,{"disambiguationData":[TD([[makeQuery(id+"F0.imprint","IMPRINT",EDGE,{"derivedFrom":subQ8}),1.0]])]});}
            var Q1;
            {var subQ10=sQuery(id+"F0.wireOp",EDGE,"E6154");Q1=makeQuery(id+"F0.imprint","IMPRINT",FACE,{"disambiguationData":[TD([[makeQuery(id+"F0.imprint","IMPRINT",EDGE,{"derivedFrom":subQ10}),1.0]])]});}
            var Q2;
            {var subQ15=sQuery(id+"F0.wireOp",EDGE,"E2807");Q2=makeQuery(id+"F0.imprint","IMPRINT",FACE,{"disambiguationData":[TD([[makeQuery(id+"F0.imprint","IMPRINT",EDGE,{"derivedFrom":subQ15}),1.0]])]});}
            extrude(context, id + "F12", {"entities" : qUnion([Q0, Q1, Q2]), "operationType" : NewBodyOperationType.ADD, "depth" : 177.8 * mm});
        }
        {
            var Q0;
            {var subQ9=sQuery(id+"F0.wireOp",EDGE,"E5968");Q0=makeQuery(id+"F0.imprint","IMPRINT",FACE,{"disambiguationData":[TD([[makeQuery(id+"F0.imprint","IMPRINT",EDGE,{"derivedFrom":subQ9}),1.0]])]});}
            var Q1;
            {var subQ9=sQuery(id+"F0.wireOp",EDGE,"E6007");Q1=makeQuery(id+"F0.imprint","IMPRINT",FACE,{"disambiguationData":[TD([[makeQuery(id+"F0.imprint","IMPRINT",EDGE,{"derivedFrom":subQ9}),1.0]])]});}
            extrude(context, id + "F13", {"entities" : qUnion([Q0, Q1]), "operationType" : NewBodyOperationType.ADD, "depth" : 190.5 * mm});
        }
        {
            var Q0;
            {var subQ4=sQuery(id+"F0.wireOp",EDGE,"E5850");Q0=makeQuery(id+"F0.imprint","IMPRINT",FACE,{"disambiguationData":[TD([[makeQuery(id+"F0.imprint","IMPRINT",EDGE,{"derivedFrom":subQ4}),1.0]])]});}
            var Q1;
            {var subQ4=sQuery(id+"F0.wireOp",EDGE,"E5884");Q1=makeQuery(id+"F0.imprint","IMPRINT",FACE,{"disambiguationData":[TD([[makeQuery(id+"F0.imprint","IMPRINT",EDGE,{"derivedFrom":subQ4}),1.0]])]});}
            extrude(context, id + "F14", {"entities" : qUnion([Q0, Q1]), "operationType" : NewBodyOperationType.ADD, "depth" : 196.85 * mm});
        }
        {
            var Q0;
            {var subQ4=sQuery(id+"F0.wireOp",EDGE,"E5884");Q0=makeQuery(id+"F0.imprint","IMPRINT",FACE,{"disambiguationData":[TD([[makeQuery(id+"F0.imprint","IMPRINT",EDGE,{"derivedFrom":subQ4}),-1.0]])]});}
            var Q1;
            {var subQ10=sQuery(id+"F0.wireOp",EDGE,"E5850");Q1=makeQuery(id+"F0.imprint","IMPRINT",FACE,{"disambiguationData":[TD([[makeQuery(id+"F0.imprint","IMPRINT",EDGE,{"derivedFrom":subQ10}),-1.0]])]});}
            extrude(context, id + "F15", {"entities" : qUnion([Q0, Q1]), "operationType" : NewBodyOperationType.ADD, "depth" : 203.2 * mm});
        }
        {
            var Q0;
            {var subQ5=sQuery(id+"F0.wireOp",EDGE,"E6241");Q0=makeQuery(id+"F0.imprint","IMPRINT",FACE,{"disambiguationData":[TD([[makeQuery(id+"F0.imprint","IMPRINT",EDGE,{"derivedFrom":subQ5}),-1.0]])]});}
            var Q1;
            {var subQ8=sQuery(id+"F0.wireOp",EDGE,"E6286");Q1=makeQuery(id+"F0.imprint","IMPRINT",FACE,{"disambiguationData":[TD([[makeQuery(id+"F0.imprint","IMPRINT",EDGE,{"derivedFrom":subQ8}),-1.0]])]});}
            extrude(context, id + "F16", {"entities" : qUnion([Q0, Q1]), "operationType" : NewBodyOperationType.ADD, "depth" : 209.55 * mm});
        }
        {
            var Q0;
            {var subQ11=sQuery(id+"F0.wireOp",EDGE,"E6371");Q0=makeQuery(id+"F0.imprint","IMPRINT",FACE,{"disambiguationData":[TD([[makeQuery(id+"F0.imprint","IMPRINT",EDGE,{"derivedFrom":subQ11}),-1.0]])]});}
            var Q1;
            {var subQ10=sQuery(id+"F0.wireOp",EDGE,"E6412");Q1=makeQuery(id+"F0.imprint","IMPRINT",FACE,{"disambiguationData":[TD([[makeQuery(id+"F0.imprint","IMPRINT",EDGE,{"derivedFrom":subQ10}),-1.0]])]});}
            extrude(context, id + "F17", {"entities" : qUnion([Q0, Q1]), "operationType" : NewBodyOperationType.ADD, "depth" : 215.9 * mm});
        }
        {
            var Q0;
            {var subQ5=sQuery(id+"F0.wireOp",EDGE,"E5408");Q0=makeQuery(id+"F0.imprint","IMPRINT",FACE,{"disambiguationData":[TD([[makeQuery(id+"F0.imprint","IMPRINT",EDGE,{"derivedFrom":subQ5}),1.0]])]});}
            var Q1;
            {var subQ13=sQuery(id+"F0.wireOp",EDGE,"E5455");Q1=makeQuery(id+"F0.imprint","IMPRINT",FACE,{"disambiguationData":[TD([[makeQuery(id+"F0.imprint","IMPRINT",EDGE,{"derivedFrom":subQ13}),1.0]])]});}
            extrude(context, id + "F18", {"entities" : qUnion([Q0, Q1]), "operationType" : NewBodyOperationType.ADD, "depth" : 222.25 * mm});
        }
        {
            var Q0;
            {var subQ10=sQuery(id+"F0.wireOp",EDGE,"E5323");Q0=makeQuery(id+"F0.imprint","IMPRINT",FACE,{"disambiguationData":[TD([[makeQuery(id+"F0.imprint","IMPRINT",EDGE,{"derivedFrom":subQ10}),1.0]])]});}
            var Q1;
            {var subQ4=sQuery(id+"F0.wireOp",EDGE,"E5272");Q1=makeQuery(id+"F0.imprint","IMPRINT",FACE,{"disambiguationData":[TD([[makeQuery(id+"F0.imprint","IMPRINT",EDGE,{"derivedFrom":subQ4}),1.0]])]});}
            extrude(context, id + "F19", {"entities" : qUnion([Q0, Q1]), "operationType" : NewBodyOperationType.ADD, "depth" : 228.6 * mm});
        }
        {
            var Q0;
            {var subQ6=sQuery(id+"F0.wireOp",EDGE,"E5272");Q0=makeQuery(id+"F0.imprint","IMPRINT",FACE,{"disambiguationData":[TD([[makeQuery(id+"F0.imprint","IMPRINT",EDGE,{"derivedFrom":subQ6}),-1.0]])]});}
            var Q1;
            {var subQ9=sQuery(id+"F0.wireOp",EDGE,"E5323");Q1=makeQuery(id+"F0.imprint","IMPRINT",FACE,{"disambiguationData":[TD([[makeQuery(id+"F0.imprint","IMPRINT",EDGE,{"derivedFrom":subQ9}),-1.0]])]});}
            extrude(context, id + "F20", {"entities" : qUnion([Q0, Q1]), "operationType" : NewBodyOperationType.ADD, "depth" : 234.95 * mm});
        }
        {
            var Q0;
            {var subQ4=sQuery(id+"F0.wireOp",EDGE,"E5548");Q0=makeQuery(id+"F0.imprint","IMPRINT",FACE,{"disambiguationData":[TD([[makeQuery(id+"F0.imprint","IMPRINT",EDGE,{"derivedFrom":subQ4}),-1.0]])]});}
            var Q1;
            {var subQ13=sQuery(id+"F0.wireOp",EDGE,"E5598");Q1=makeQuery(id+"F0.imprint","IMPRINT",FACE,{"disambiguationData":[TD([[makeQuery(id+"F0.imprint","IMPRINT",EDGE,{"derivedFrom":subQ13}),-1.0]])]});}
            extrude(context, id + "F21", {"entities" : qUnion([Q0, Q1]), "operationType" : NewBodyOperationType.ADD, "depth" : 241.3 * mm});
        }
        {
            var Q0;
            {var subQ10=sQuery(id+"F0.wireOp",EDGE,"E5146");Q0=makeQuery(id+"F0.imprint","IMPRINT",FACE,{"disambiguationData":[TD([[makeQuery(id+"F0.imprint","IMPRINT",EDGE,{"derivedFrom":subQ10}),1.0]])]});}
            var Q1;
            {var subQ8=sQuery(id+"F0.wireOp",EDGE,"E5194");Q1=makeQuery(id+"F0.imprint","IMPRINT",FACE,{"disambiguationData":[TD([[makeQuery(id+"F0.imprint","IMPRINT",EDGE,{"derivedFrom":subQ8}),1.0]])]});}
            extrude(context, id + "F22", {"entities" : qUnion([Q0, Q1]), "operationType" : NewBodyOperationType.ADD, "depth" : 247.65 * mm});
        }
        {
            var Q0;
            {var subQ8=sQuery(id+"F0.wireOp",EDGE,"E4976");Q0=makeQuery(id+"F0.imprint","IMPRINT",FACE,{"disambiguationData":[TD([[makeQuery(id+"F0.imprint","IMPRINT",EDGE,{"derivedFrom":subQ8}),1.0]])]});}
            var Q1;
            {var subQ8=sQuery(id+"F0.wireOp",EDGE,"E5024");Q1=makeQuery(id+"F0.imprint","IMPRINT",FACE,{"disambiguationData":[TD([[makeQuery(id+"F0.imprint","IMPRINT",EDGE,{"derivedFrom":subQ8}),1.0]])]});}
            extrude(context, id + "F23", {"entities" : qUnion([Q0, Q1]), "operationType" : NewBodyOperationType.ADD, "depth" : 254 * mm});
        }
        {
            var Q0;
            {var subQ10=sQuery(id+"F0.wireOp",EDGE,"E4806");Q0=makeQuery(id+"F0.imprint","IMPRINT",FACE,{"disambiguationData":[TD([[makeQuery(id+"F0.imprint","IMPRINT",EDGE,{"derivedFrom":subQ10}),1.0]])]});}
            var Q1;
            {var subQ12=sQuery(id+"F0.wireOp",EDGE,"E4854");Q1=makeQuery(id+"F0.imprint","IMPRINT",FACE,{"disambiguationData":[TD([[makeQuery(id+"F0.imprint","IMPRINT",EDGE,{"derivedFrom":subQ12}),1.0]])]});}
            extrude(context, id + "F24", {"entities" : qUnion([Q0, Q1]), "operationType" : NewBodyOperationType.ADD, "depth" : 260.35 * mm});
        }
        {
            var Q0;
            {var subQ9=sQuery(id+"F0.wireOp",EDGE,"E4309");Q0=makeQuery(id+"F0.imprint","IMPRINT",FACE,{"disambiguationData":[TD([[makeQuery(id+"F0.imprint","IMPRINT",EDGE,{"derivedFrom":subQ9}),1.0]])]});}
            var Q1;
            {var subQ6=sQuery(id+"F0.wireOp",EDGE,"E4362");Q1=makeQuery(id+"F0.imprint","IMPRINT",FACE,{"disambiguationData":[TD([[makeQuery(id+"F0.imprint","IMPRINT",EDGE,{"derivedFrom":subQ6}),1.0]])]});}
            extrude(context, id + "F25", {"entities" : qUnion([Q0, Q1]), "operationType" : NewBodyOperationType.ADD, "depth" : 266.7 * mm});
        }
        {
            var Q0;
            {var subQ12=sQuery(id+"F0.wireOp",EDGE,"E4168");Q0=makeQuery(id+"F0.imprint","IMPRINT",FACE,{"disambiguationData":[TD([[makeQuery(id+"F0.imprint","IMPRINT",EDGE,{"derivedFrom":subQ12}),1.0]])]});}
            var Q1;
            {var subQ13=sQuery(id+"F0.wireOp",EDGE,"E4207");Q1=makeQuery(id+"F0.imprint","IMPRINT",FACE,{"disambiguationData":[TD([[makeQuery(id+"F0.imprint","IMPRINT",EDGE,{"derivedFrom":subQ13}),1.0]])]});}
            extrude(context, id + "F26", {"entities" : qUnion([Q0, Q1]), "operationType" : NewBodyOperationType.ADD, "depth" : 273.05 * mm});
        }
        {
            var Q0;
            {var subQ12=sQuery(id+"F0.wireOp",EDGE,"E4011");Q0=makeQuery(id+"F0.imprint","IMPRINT",FACE,{"disambiguationData":[TD([[makeQuery(id+"F0.imprint","IMPRINT",EDGE,{"derivedFrom":subQ12}),1.0]])]});}
            var Q1;
            {var subQ8=sQuery(id+"F0.wireOp",EDGE,"E4049");Q1=makeQuery(id+"F0.imprint","IMPRINT",FACE,{"disambiguationData":[TD([[makeQuery(id+"F0.imprint","IMPRINT",EDGE,{"derivedFrom":subQ8}),1.0]])]});}
            extrude(context, id + "F27", {"entities" : qUnion([Q0, Q1]), "operationType" : NewBodyOperationType.ADD, "depth" : 279.4 * mm});
        }
        {
            var Q0;
            {var subQ7=sQuery(id+"F0.wireOp",EDGE,"E3867");Q0=makeQuery(id+"F0.imprint","IMPRINT",FACE,{"disambiguationData":[TD([[makeQuery(id+"F0.imprint","IMPRINT",EDGE,{"derivedFrom":subQ7}),1.0]])]});}
            var Q1;
            {var subQ12=sQuery(id+"F0.wireOp",EDGE,"E3904");Q1=makeQuery(id+"F0.imprint","IMPRINT",FACE,{"disambiguationData":[TD([[makeQuery(id+"F0.imprint","IMPRINT",EDGE,{"derivedFrom":subQ12}),1.0]])]});}
            extrude(context, id + "F28", {"entities" : qUnion([Q0, Q1]), "operationType" : NewBodyOperationType.ADD, "depth" : 285.75 * mm});
        }
        {
            var Q0;
            {var subQ14=sQuery(id+"F0.wireOp",EDGE,"E3747");Q0=makeQuery(id+"F0.imprint","IMPRINT",FACE,{"disambiguationData":[TD([[makeQuery(id+"F0.imprint","IMPRINT",EDGE,{"derivedFrom":subQ14}),1.0]])]});}
            var Q1;
            {var subQ11=sQuery(id+"F0.wireOp",EDGE,"E3692");Q1=makeQuery(id+"F0.imprint","IMPRINT",FACE,{"disambiguationData":[TD([[makeQuery(id+"F0.imprint","IMPRINT",EDGE,{"derivedFrom":subQ11}),1.0]])]});}
            extrude(context, id + "F29", {"entities" : qUnion([Q0, Q1]), "operationType" : NewBodyOperationType.ADD, "depth" : 292.1 * mm});
        }
        {
            var Q0;
            {var subQ11=sQuery(id+"F0.wireOp",EDGE,"E3692");Q0=makeQuery(id+"F0.imprint","IMPRINT",FACE,{"disambiguationData":[TD([[makeQuery(id+"F0.imprint","IMPRINT",EDGE,{"derivedFrom":subQ11}),-1.0]])]});}
            var Q1;
            {var subQ6=sQuery(id+"F0.wireOp",EDGE,"E3747");Q1=makeQuery(id+"F0.imprint","IMPRINT",FACE,{"disambiguationData":[TD([[makeQuery(id+"F0.imprint","IMPRINT",EDGE,{"derivedFrom":subQ6}),-1.0]])]});}
            extrude(context, id + "F30", {"entities" : qUnion([Q0, Q1]), "operationType" : NewBodyOperationType.ADD, "depth" : 298.45 * mm});
        }
        {
            var Q0;
            {var subQ12=sQuery(id+"F0.wireOp",EDGE,"E4473");Q0=makeQuery(id+"F0.imprint","IMPRINT",FACE,{"disambiguationData":[TD([[makeQuery(id+"F0.imprint","IMPRINT",EDGE,{"derivedFrom":subQ12}),-1.0]])]});}
            var Q1;
            {var subQ8=sQuery(id+"F0.wireOp",EDGE,"E4511");Q1=makeQuery(id+"F0.imprint","IMPRINT",FACE,{"disambiguationData":[TD([[makeQuery(id+"F0.imprint","IMPRINT",EDGE,{"derivedFrom":subQ8}),-1.0]])]});}
            extrude(context, id + "F31", {"entities" : qUnion([Q0, Q1]), "operationType" : NewBodyOperationType.ADD, "depth" : 304.8 * mm});
        }
        {
            var Q0;
            {var subQ10=sQuery(id+"F0.wireOp",EDGE,"E3012");Q0=makeQuery(id+"F0.imprint","IMPRINT",FACE,{"disambiguationData":[TD([[makeQuery(id+"F0.imprint","IMPRINT",EDGE,{"derivedFrom":subQ10}),1.0]])]});}
            var Q1;
            {var subQ8=sQuery(id+"F0.wireOp",EDGE,"E3070");Q1=makeQuery(id+"F0.imprint","IMPRINT",FACE,{"disambiguationData":[TD([[makeQuery(id+"F0.imprint","IMPRINT",EDGE,{"derivedFrom":subQ8}),1.0]])]});}
            extrude(context, id + "F32", {"entities" : qUnion([Q0, Q1]), "operationType" : NewBodyOperationType.ADD, "depth" : 311.15 * mm});
        }
        {
            var Q0;
            {var subQ10=sQuery(id+"F0.wireOp",EDGE,"E2849");Q0=makeQuery(id+"F0.imprint","IMPRINT",FACE,{"disambiguationData":[TD([[makeQuery(id+"F0.imprint","IMPRINT",EDGE,{"derivedFrom":subQ10}),1.0]])]});}
            var Q1;
            {var subQ4=sQuery(id+"F0.wireOp",EDGE,"E2879");Q1=makeQuery(id+"F0.imprint","IMPRINT",FACE,{"disambiguationData":[TD([[makeQuery(id+"F0.imprint","IMPRINT",EDGE,{"derivedFrom":subQ4}),1.0]])]});}
            extrude(context, id + "F33", {"entities" : qUnion([Q0, Q1]), "operationType" : NewBodyOperationType.ADD, "depth" : 317.5 * mm});
        }
        {
            var Q0;
            {var subQ12=sQuery(id+"F0.wireOp",EDGE,"E2707");Q0=makeQuery(id+"F0.imprint","IMPRINT",FACE,{"disambiguationData":[TD([[makeQuery(id+"F0.imprint","IMPRINT",EDGE,{"derivedFrom":subQ12}),1.0]])]});}
            var Q1;
            {var subQ15=sQuery(id+"F0.wireOp",EDGE,"E2737");Q1=makeQuery(id+"F0.imprint","IMPRINT",FACE,{"disambiguationData":[TD([[makeQuery(id+"F0.imprint","IMPRINT",EDGE,{"derivedFrom":subQ15}),1.0]])]});}
            var Q2;
            {var subQ6=sQuery(id+"F0.wireOp",EDGE,"E2664");Q2=makeQuery(id+"F0.imprint","IMPRINT",FACE,{"disambiguationData":[TD([[makeQuery(id+"F0.imprint","IMPRINT",EDGE,{"derivedFrom":subQ6}),1.0]])]});}
            extrude(context, id + "F34", {"entities" : qUnion([Q0, Q1, Q2]), "operationType" : NewBodyOperationType.ADD, "depth" : 323.85 * mm});
        }
        {
            var Q0;
            {var subQ8=sQuery(id+"F0.wireOp",EDGE,"E2707");Q0=makeQuery(id+"F0.imprint","IMPRINT",FACE,{"disambiguationData":[TD([[makeQuery(id+"F0.imprint","IMPRINT",EDGE,{"derivedFrom":subQ8}),-1.0]])]});}
            var Q1;
            {var subQ8=sQuery(id+"F0.wireOp",EDGE,"E2737");Q1=makeQuery(id+"F0.imprint","IMPRINT",FACE,{"disambiguationData":[TD([[makeQuery(id+"F0.imprint","IMPRINT",EDGE,{"derivedFrom":subQ8}),-1.0]])]});}
            var Q2;
            {var subQ10=sQuery(id+"F0.wireOp",EDGE,"E2664");Q2=makeQuery(id+"F0.imprint","IMPRINT",FACE,{"disambiguationData":[TD([[makeQuery(id+"F0.imprint","IMPRINT",EDGE,{"derivedFrom":subQ10}),-1.0]])]});}
            extrude(context, id + "F35", {"entities" : qUnion([Q0, Q1, Q2]), "operationType" : NewBodyOperationType.ADD, "depth" : 330.2 * mm});
        }
        {
            var Q0;
            {var subQ12=sQuery(id+"F0.wireOp",EDGE,"E3185");Q0=makeQuery(id+"F0.imprint","IMPRINT",FACE,{"disambiguationData":[TD([[makeQuery(id+"F0.imprint","IMPRINT",EDGE,{"derivedFrom":subQ12}),-1.0]])]});}
            var Q1;
            {var subQ12=sQuery(id+"F0.wireOp",EDGE,"E3215");Q1=makeQuery(id+"F0.imprint","IMPRINT",FACE,{"disambiguationData":[TD([[makeQuery(id+"F0.imprint","IMPRINT",EDGE,{"derivedFrom":subQ12}),-1.0]])]});}
            var Q2;
            {var subQ10=sQuery(id+"F0.wireOp",EDGE,"E3142");Q2=makeQuery(id+"F0.imprint","IMPRINT",FACE,{"disambiguationData":[TD([[makeQuery(id+"F0.imprint","IMPRINT",EDGE,{"derivedFrom":subQ10}),-1.0]])]});}
            var Q3;
            {var subQ10=sQuery(id+"F0.wireOp",EDGE,"E3142");Q3=makeQuery(id+"F0.imprint","IMPRINT",FACE,{"disambiguationData":[TD([[makeQuery(id+"F0.imprint","IMPRINT",EDGE,{"derivedFrom":subQ10}),-1.0]])]});}
            extrude(context, id + "F36", {"entities" : qUnion([Q0, Q1, Q2, Q3]), "operationType" : NewBodyOperationType.ADD, "depth" : 336.55 * mm});
        }
        {
            var Q0;
            {var subQ10=sQuery(id+"F0.wireOp",EDGE,"E3399");Q0=makeQuery(id+"F0.imprint","IMPRINT",FACE,{"disambiguationData":[TD([[makeQuery(id+"F0.imprint","IMPRINT",EDGE,{"derivedFrom":subQ10}),-1.0]])]});}
            var Q1;
            {var subQ12=sQuery(id+"F0.wireOp",EDGE,"E3361");Q1=makeQuery(id+"F0.imprint","IMPRINT",FACE,{"disambiguationData":[TD([[makeQuery(id+"F0.imprint","IMPRINT",EDGE,{"derivedFrom":subQ12}),-1.0]])]});}
            var Q2;
            {var subQ12=sQuery(id+"F0.wireOp",EDGE,"E3293");Q2=makeQuery(id+"F0.imprint","IMPRINT",FACE,{"disambiguationData":[TD([[makeQuery(id+"F0.imprint","IMPRINT",EDGE,{"derivedFrom":subQ12}),-1.0]])]});}
            extrude(context, id + "F37", {"entities" : qUnion([Q0, Q1, Q2]), "operationType" : NewBodyOperationType.ADD, "depth" : 342.9 * mm});
        }
        {
            var Q0;
            {var subQ9=sQuery(id+"F0.wireOp",EDGE,"E2524");Q0=makeQuery(id+"F0.imprint","IMPRINT",FACE,{"disambiguationData":[TD([[makeQuery(id+"F0.imprint","IMPRINT",EDGE,{"derivedFrom":subQ9}),1.0]])]});}
            var Q1;
            {var subQ10=sQuery(id+"F0.wireOp",EDGE,"E2580");Q1=makeQuery(id+"F0.imprint","IMPRINT",FACE,{"disambiguationData":[TD([[makeQuery(id+"F0.imprint","IMPRINT",EDGE,{"derivedFrom":subQ10}),1.0]])]});}
            var Q2;
            {var subQ4=sQuery(id+"F0.wireOp",EDGE,"E2437");Q2=makeQuery(id+"F0.imprint","IMPRINT",FACE,{"disambiguationData":[TD([[makeQuery(id+"F0.imprint","IMPRINT",EDGE,{"derivedFrom":subQ4}),1.0]])]});}
            extrude(context, id + "F38", {"entities" : qUnion([Q0, Q1, Q2]), "operationType" : NewBodyOperationType.ADD, "depth" : 349.25 * mm});
        }
        {
            var Q0;
            {var subQ10=sQuery(id+"F0.wireOp",EDGE,"E2307");Q0=makeQuery(id+"F0.imprint","IMPRINT",FACE,{"disambiguationData":[TD([[makeQuery(id+"F0.imprint","IMPRINT",EDGE,{"derivedFrom":subQ10}),1.0]])]});}
            var Q1;
            {var subQ12=sQuery(id+"F0.wireOp",EDGE,"E2363");Q1=makeQuery(id+"F0.imprint","IMPRINT",FACE,{"disambiguationData":[TD([[makeQuery(id+"F0.imprint","IMPRINT",EDGE,{"derivedFrom":subQ12}),1.0]])]});}
            var Q2;
            {var subQ11=sQuery(id+"F0.wireOp",EDGE,"E2181");Q2=makeQuery(id+"F0.imprint","IMPRINT",FACE,{"disambiguationData":[TD([[makeQuery(id+"F0.imprint","IMPRINT",EDGE,{"derivedFrom":subQ11}),1.0]])]});}
            extrude(context, id + "F39", {"entities" : qUnion([Q0, Q1, Q2]), "operationType" : NewBodyOperationType.ADD, "depth" : 355.6 * mm});
        }
        {
            var Q0;
            {var subQ8=sQuery(id+"F0.wireOp",EDGE,"E950");Q0=makeQuery(id+"F0.imprint","IMPRINT",FACE,{"disambiguationData":[TD([[makeQuery(id+"F0.imprint","IMPRINT",EDGE,{"derivedFrom":subQ8}),1.0]])]});}
            var Q1;
            {var subQ8=sQuery(id+"F0.wireOp",EDGE,"E997");Q1=makeQuery(id+"F0.imprint","IMPRINT",FACE,{"disambiguationData":[TD([[makeQuery(id+"F0.imprint","IMPRINT",EDGE,{"derivedFrom":subQ8}),1.0]])]});}
            var Q2;
            {var subQ11=sQuery(id+"F0.wireOp",EDGE,"E887");Q2=makeQuery(id+"F0.imprint","IMPRINT",FACE,{"disambiguationData":[TD([[makeQuery(id+"F0.imprint","IMPRINT",EDGE,{"derivedFrom":subQ11}),1.0]])]});}
            extrude(context, id + "F40", {"entities" : qUnion([Q0, Q1, Q2]), "operationType" : NewBodyOperationType.ADD, "depth" : 361.95 * mm});
        }
        {
            var Q0;
            {var subQ11=sQuery(id+"F0.wireOp",EDGE,"E762");Q0=makeQuery(id+"F0.imprint","IMPRINT",FACE,{"disambiguationData":[TD([[makeQuery(id+"F0.imprint","IMPRINT",EDGE,{"derivedFrom":subQ11}),1.0]])]});}
            var Q1;
            {var subQ7=sQuery(id+"F0.wireOp",EDGE,"E502");Q1=makeQuery(id+"F0.imprint","IMPRINT",FACE,{"disambiguationData":[TD([[makeQuery(id+"F0.imprint","IMPRINT",EDGE,{"derivedFrom":subQ7}),1.0]])]});}
            var Q2;
            {var subQ13=sQuery(id+"F0.wireOp",EDGE,"E807");Q2=makeQuery(id+"F0.imprint","IMPRINT",FACE,{"disambiguationData":[TD([[makeQuery(id+"F0.imprint","IMPRINT",EDGE,{"derivedFrom":subQ13}),1.0]])]});}
            extrude(context, id + "F41", {"entities" : qUnion([Q0, Q1, Q2]), "operationType" : NewBodyOperationType.ADD, "depth" : 368.3 * mm});
        }
        {
            var Q0;
            {var subQ7=sQuery(id+"F0.wireOp",EDGE,"E579");Q0=makeQuery(id+"F0.imprint","IMPRINT",FACE,{"disambiguationData":[TD([[makeQuery(id+"F0.imprint","IMPRINT",EDGE,{"derivedFrom":subQ7}),1.0]])]});}
            var Q1;
            {var subQ13=sQuery(id+"F0.wireOp",EDGE,"E623");Q1=makeQuery(id+"F0.imprint","IMPRINT",FACE,{"disambiguationData":[TD([[makeQuery(id+"F0.imprint","IMPRINT",EDGE,{"derivedFrom":subQ13}),1.0]])]});}
            extrude(context, id + "F42", {"entities" : qUnion([Q0, Q1]), "operationType" : NewBodyOperationType.ADD, "depth" : 374.65 * mm});
        }
        {
            var Q0;
            {var subQ14=sQuery(id+"F0.wireOp",EDGE,"E431");Q0=makeQuery(id+"F0.imprint","IMPRINT",FACE,{"disambiguationData":[TD([[makeQuery(id+"F0.imprint","IMPRINT",EDGE,{"derivedFrom":subQ14}),1.0]])]});}
            var Q1;
            {var subQ7=sQuery(id+"F0.wireOp",EDGE,"E358");Q1=makeQuery(id+"F0.imprint","IMPRINT",FACE,{"disambiguationData":[TD([[makeQuery(id+"F0.imprint","IMPRINT",EDGE,{"derivedFrom":subQ7}),1.0]])]});}
            var Q2;
            {var subQ6=sQuery(id+"F0.wireOp",EDGE,"E279");Q2=makeQuery(id+"F0.imprint","IMPRINT",FACE,{"disambiguationData":[TD([[makeQuery(id+"F0.imprint","IMPRINT",EDGE,{"derivedFrom":subQ6}),1.0]])]});}
            extrude(context, id + "F43", {"entities" : qUnion([Q0, Q1, Q2]), "operationType" : NewBodyOperationType.ADD, "depth" : 381 * mm});
        }
        {
            var Q0;
            {var subQ8=sQuery(id+"F0.wireOp",EDGE,"E164");Q0=makeQuery(id+"F0.imprint","IMPRINT",FACE,{"disambiguationData":[TD([[makeQuery(id+"F0.imprint","IMPRINT",EDGE,{"derivedFrom":subQ8}),1.0]])]});}
            var Q1;
            {var subQ13=sQuery(id+"F0.wireOp",EDGE,"E209");Q1=makeQuery(id+"F0.imprint","IMPRINT",FACE,{"disambiguationData":[TD([[makeQuery(id+"F0.imprint","IMPRINT",EDGE,{"derivedFrom":subQ13}),1.0]])]});}
            var Q2;
            {var subQ17=sQuery(id+"F0.wireOp",EDGE,"E279");Q2=makeQuery(id+"F0.imprint","IMPRINT",FACE,{"disambiguationData":[TD([[makeQuery(id+"F0.imprint","IMPRINT",EDGE,{"derivedFrom":subQ17}),-1.0]])]});}
            extrude(context, id + "F44", {"entities" : qUnion([Q0, Q1, Q2]), "operationType" : NewBodyOperationType.ADD, "depth" : 387.35 * mm});
        }
        {
            var Q0;
            {var subQ11=sQuery(id+"F0.wireOp",EDGE,"E164");Q0=makeQuery(id+"F0.imprint","IMPRINT",FACE,{"disambiguationData":[TD([[makeQuery(id+"F0.imprint","IMPRINT",EDGE,{"derivedFrom":subQ11}),-1.0]])]});}
            var Q1;
            {var subQ10=sQuery(id+"F0.wireOp",EDGE,"E209");Q1=makeQuery(id+"F0.imprint","IMPRINT",FACE,{"disambiguationData":[TD([[makeQuery(id+"F0.imprint","IMPRINT",EDGE,{"derivedFrom":subQ10}),-1.0]])]});}
            extrude(context, id + "F45", {"entities" : qUnion([Q0, Q1]), "operationType" : NewBodyOperationType.ADD, "depth" : 393.7 * mm});
        }
        {
            var Q0;
            {var subQ12=sQuery(id+"F0.wireOp",EDGE,"E1415");Q0=makeQuery(id+"F0.imprint","IMPRINT",FACE,{"disambiguationData":[TD([[makeQuery(id+"F0.imprint","IMPRINT",EDGE,{"derivedFrom":subQ12}),1.0]])]});}
            var Q1;
            {var subQ5=sQuery(id+"F0.wireOp",EDGE,"E6");Q1=makeQuery(id+"F0.imprint","IMPRINT",FACE,{"disambiguationData":[TD([[makeQuery(id+"F0.imprint","IMPRINT",EDGE,{"derivedFrom":subQ5}),1.0]])]});}
            extrude(context, id + "F46", {"entities" : qUnion([Q0, Q1]), "operationType" : NewBodyOperationType.ADD, "depth" : 400.05 * mm});
        }
        {
            var Q0;
            {var subQ12=sQuery(id+"F0.wireOp",EDGE,"E1415");Q0=makeQuery(id+"F0.imprint","IMPRINT",FACE,{"disambiguationData":[TD([[makeQuery(id+"F0.imprint","IMPRINT",EDGE,{"derivedFrom":subQ12}),-1.0]])]});}
            var Q1;
            {var subQ4=sQuery(id+"F0.wireOp",EDGE,"E1452");Q1=makeQuery(id+"F0.imprint","IMPRINT",FACE,{"disambiguationData":[TD([[makeQuery(id+"F0.imprint","IMPRINT",EDGE,{"derivedFrom":subQ4}),-1.0]])]});}
            extrude(context, id + "F47", {"entities" : qUnion([Q0, Q1]), "operationType" : NewBodyOperationType.ADD, "depth" : 406.4 * mm});
        }
        {
            var Q0;
            {var subQ5=sQuery(id+"F0.wireOp",EDGE,"E1127");Q0=makeQuery(id+"F0.imprint","IMPRINT",FACE,{"disambiguationData":[TD([[makeQuery(id+"F0.imprint","IMPRINT",EDGE,{"derivedFrom":subQ5}),1.0]])]});}
            var Q1;
            {var subQ12=sQuery(id+"F0.wireOp",EDGE,"E2");Q1=makeQuery(id+"F0.imprint","IMPRINT",FACE,{"disambiguationData":[TD([[makeQuery(id+"F0.imprint","IMPRINT",EDGE,{"derivedFrom":subQ12}),1.0]])]});}
            var Q2;
            {var subQ4=sQuery(id+"F0.wireOp",EDGE,"E1071");Q2=makeQuery(id+"F0.imprint","IMPRINT",FACE,{"disambiguationData":[TD([[makeQuery(id+"F0.imprint","IMPRINT",EDGE,{"derivedFrom":subQ4}),1.0]])]});}
            extrude(context, id + "F48", {"entities" : qUnion([Q0, Q1, Q2]), "operationType" : NewBodyOperationType.ADD, "depth" : 412.75 * mm});
        }
        {
            var Q0;
            {var subQ8=sQuery(id+"F0.wireOp",EDGE,"E1167");Q0=makeQuery(id+"F0.imprint","IMPRINT",FACE,{"disambiguationData":[TD([[makeQuery(id+"F0.imprint","IMPRINT",EDGE,{"derivedFrom":subQ8}),-1.0]])]});}
            var Q1;
            {var subQ18=sQuery(id+"F0.wireOp",EDGE,"E1071");Q1=makeQuery(id+"F0.imprint","IMPRINT",FACE,{"disambiguationData":[TD([[makeQuery(id+"F0.imprint","IMPRINT",EDGE,{"derivedFrom":subQ18}),-1.0]])]});}
            extrude(context, id + "F49", {"entities" : qUnion([Q0, Q1]), "operationType" : NewBodyOperationType.ADD, "depth" : 425.45 * mm});
        }
        {
            var Q0;
            {var subQ8=sQuery(id+"F0.wireOp",EDGE,"E1972");Q0=makeQuery(id+"F0.imprint","IMPRINT",FACE,{"disambiguationData":[TD([[makeQuery(id+"F0.imprint","IMPRINT",EDGE,{"derivedFrom":subQ8}),-1.0]])]});}
            var Q1;
            {var subQ11=sQuery(id+"F0.wireOp",EDGE,"E2004");Q1=makeQuery(id+"F0.imprint","IMPRINT",FACE,{"disambiguationData":[TD([[makeQuery(id+"F0.imprint","IMPRINT",EDGE,{"derivedFrom":subQ11}),-1.0]])]});}
            var Q2;
            {var subQ11=sQuery(id+"F0.wireOp",EDGE,"E1224");Q2=makeQuery(id+"F0.imprint","IMPRINT",FACE,{"disambiguationData":[TD([[makeQuery(id+"F0.imprint","IMPRINT",EDGE,{"derivedFrom":subQ11}),1.0]])]});}
            extrude(context, id + "F50", {"entities" : qUnion([Q0, Q1, Q2]), "operationType" : NewBodyOperationType.ADD, "depth" : 431.8 * mm});
        }
        {
            var Q0;
            {var subQ8=sQuery(id+"F0.wireOp",EDGE,"E2112");Q0=makeQuery(id+"F0.imprint","IMPRINT",FACE,{"disambiguationData":[TD([[makeQuery(id+"F0.imprint","IMPRINT",EDGE,{"derivedFrom":subQ8}),-1.0]])]});}
            var Q1;
            {var subQ8=sQuery(id+"F0.wireOp",EDGE,"E2141");Q1=makeQuery(id+"F0.imprint","IMPRINT",FACE,{"disambiguationData":[TD([[makeQuery(id+"F0.imprint","IMPRINT",EDGE,{"derivedFrom":subQ8}),-1.0]])]});}
            var Q2;
            {var subQ5=sQuery(id+"F0.wireOp",EDGE,"E1224");Q2=makeQuery(id+"F0.imprint","IMPRINT",FACE,{"disambiguationData":[TD([[makeQuery(id+"F0.imprint","IMPRINT",EDGE,{"derivedFrom":subQ5}),-1.0]])]});}
            extrude(context, id + "F51", {"entities" : qUnion([Q0, Q1, Q2]), "operationType" : NewBodyOperationType.ADD, "depth" : 438.15 * mm});
        }
        {
            var Q0;
            {var subQ5=sQuery(id+"F0.wireOp",EDGE,"E2159");Q0=makeQuery(id+"F0.imprint","IMPRINT",FACE,{"disambiguationData":[TD([[makeQuery(id+"F0.imprint","IMPRINT",EDGE,{"derivedFrom":subQ5}),-1.0]])]});}
            var Q1;
            {var subQ0=sQuery(id+"F0.wireOp",EDGE,"E2173");Q1=makeQuery(id+"F0.imprint","IMPRINT",FACE,{"disambiguationData":[TD([[makeQuery(id+"F0.imprint","IMPRINT",EDGE,{"derivedFrom":subQ0}),-1.0]])]});}
            var Q2;
            {var subQ5=sQuery(id+"F0.wireOp",EDGE,"E2089");Q2=makeQuery(id+"F0.imprint","IMPRINT",FACE,{"disambiguationData":[TD([[makeQuery(id+"F0.imprint","IMPRINT",EDGE,{"derivedFrom":subQ5}),-1.0]])]});}
            extrude(context, id + "F52", {"entities" : qUnion([Q0, Q1, Q2]), "operationType" : NewBodyOperationType.ADD, "depth" : 444.5 * mm});
        }
        {
            var Q0;
            {var subQ0=sQuery(id+"F0.wireOp",EDGE,"E70");Q0=makeQuery(id+"F33.boolean.opBoolean","MERGE",FACE,{"derivedFrom":[makeQuery(id+"F32.boolean.opBoolean","MERGE",FACE,{"derivedFrom":[makeQuery(id+"F31.boolean.opBoolean","MERGE",FACE,{"derivedFrom":[makeQuery(id+"F30.boolean.opBoolean","MERGE",FACE,{"derivedFrom":[makeQuery(id+"F29.boolean.opBoolean","MERGE",FACE,{"derivedFrom":[makeQuery(id+"F28.boolean.opBoolean","MERGE",FACE,{"derivedFrom":[makeQuery(id+"F27.boolean.opBoolean","MERGE",FACE,{"derivedFrom":[makeQuery(id+"F26.boolean.opBoolean","MERGE",FACE,{"derivedFrom":[makeQuery(id+"F25.boolean.opBoolean","MERGE",FACE,{"derivedFrom":[makeQuery(id+"F24.boolean.opBoolean","MERGE",FACE,{"derivedFrom":[makeQuery(id+"F23.boolean.opBoolean","MERGE",FACE,{"derivedFrom":[makeQuery(id+"F22.boolean.opBoolean","MERGE",FACE,{"derivedFrom":[makeQuery(id+"F21.boolean.opBoolean","MERGE",FACE,{"derivedFrom":[makeQuery(id+"F20.boolean.opBoolean","MERGE",FACE,{"derivedFrom":[makeQuery(id+"F19.boolean.opBoolean","MERGE",FACE,{"derivedFrom":[makeQuery(id+"F18.boolean.opBoolean","MERGE",FACE,{"derivedFrom":[makeQuery(id+"F17.boolean.opBoolean","MERGE",FACE,{"derivedFrom":[makeQuery(id+"F16.boolean.opBoolean","MERGE",FACE,{"derivedFrom":[makeQuery(id+"F15.boolean.opBoolean","MERGE",FACE,{"derivedFrom":[makeQuery(id+"F14.boolean.opBoolean","MERGE",FACE,{"derivedFrom":[makeQuery(id+"F13.opExtrude","SWEPT_FACE",FACE,{"disambiguationData":[OSD([subQ0])]}),makeQuery(id+"F14.opExtrude","SWEPT_FACE",FACE,{"disambiguationData":[OSD([subQ0])]})]}),makeQuery(id+"F15.opExtrude","SWEPT_FACE",FACE,{"disambiguationData":[OSD([subQ0])]})]}),makeQuery(id+"F16.opExtrude","SWEPT_FACE",FACE,{"disambiguationData":[OSD([subQ0])]})]}),makeQuery(id+"F17.opExtrude","SWEPT_FACE",FACE,{"disambiguationData":[OSD([subQ0])]})]}),makeQuery(id+"F18.opExtrude","SWEPT_FACE",FACE,{"disambiguationData":[OSD([subQ0])]})]}),makeQuery(id+"F19.opExtrude","SWEPT_FACE",FACE,{"disambiguationData":[OSD([subQ0])]})]}),makeQuery(id+"F20.opExtrude","SWEPT_FACE",FACE,{"disambiguationData":[OSD([subQ0])]})]}),makeQuery(id+"F21.opExtrude","SWEPT_FACE",FACE,{"disambiguationData":[OSD([subQ0])]})]}),makeQuery(id+"F22.opExtrude","SWEPT_FACE",FACE,{"disambiguationData":[OSD([subQ0])]})]}),makeQuery(id+"F23.opExtrude","SWEPT_FACE",FACE,{"disambiguationData":[OSD([subQ0])]})]}),makeQuery(id+"F24.opExtrude","SWEPT_FACE",FACE,{"disambiguationData":[OSD([subQ0])]})]}),makeQuery(id+"F25.opExtrude","SWEPT_FACE",FACE,{"disambiguationData":[OSD([subQ0])]})]}),makeQuery(id+"F26.opExtrude","SWEPT_FACE",FACE,{"disambiguationData":[OSD([subQ0])]})]}),makeQuery(id+"F27.opExtrude","SWEPT_FACE",FACE,{"disambiguationData":[OSD([subQ0])]})]}),makeQuery(id+"F28.opExtrude","SWEPT_FACE",FACE,{"disambiguationData":[OSD([subQ0])]})]}),makeQuery(id+"F29.opExtrude","SWEPT_FACE",FACE,{"disambiguationData":[OSD([subQ0])]})]}),makeQuery(id+"F30.opExtrude","SWEPT_FACE",FACE,{"disambiguationData":[OSD([subQ0])]})]}),makeQuery(id+"F31.opExtrude","SWEPT_FACE",FACE,{"disambiguationData":[OSD([subQ0])]})]}),makeQuery(id+"F32.opExtrude","SWEPT_FACE",FACE,{"disambiguationData":[OSD([subQ0])]})]}),makeQuery(id+"F33.opExtrude","SWEPT_FACE",FACE,{"disambiguationData":[OSD([subQ0])]})]});}
            var sketch = newSketch(context, id + "F53", { "sketchPlane" : qUnion([Q0])});
            skLineSegment(sketch, "E8051", {"start": v(744, 396.25) * mm, "end": v(-726.54, 38.93) * mm});
            skLineSegment(sketch, "E8052", {"start": v(-726.54, 38.93) * mm, "end": v(-726.54, 534.78) * mm});
            skLineSegment(sketch, "E8053", {"start": v(-726.54, 534.78) * mm, "end": v(744, 534.78) * mm});
            skLineSegment(sketch, "E8054", {"start": v(744, 534.78) * mm, "end": v(744, 396.25) * mm});
            skSolve(sketch);
        }
        {
            var Q0;
            Q0 = qSketchRegion(id + "F53", true);
            extrude(context, id + "F54", {"entities" : qUnion([Q0]), "operationType" : NewBodyOperationType.REMOVE, "depth" : 6.35 * mm});
        }
        {
            var Q0;
            Q0=makeQuery(id+"F51.opExtrude","CAP_FACE",FACE,{"disambiguationData":[OSD([sQuery(id+"F0.wireOp",EDGE,"E68"),sQuery(id+"F0.wireOp",EDGE,"E1223"),sQuery(id+"F0.wireOp",EDGE,"E1224"),sQuery(id+"F0.wireOp",EDGE,"E1225"),sQuery(id+"F0.wireOp",EDGE,"E1226"),sQuery(id+"F0.wireOp",EDGE,"E1227"),sQuery(id+"F0.wireOp",EDGE,"E1228"),sQuery(id+"F0.wireOp",EDGE,"E1229"),sQuery(id+"F0.wireOp",EDGE,"E1230"),sQuery(id+"F0.wireOp",EDGE,"E1231"),sQuery(id+"F0.wireOp",EDGE,"E1232"),sQuery(id+"F0.wireOp",EDGE,"E1233"),sQuery(id+"F0.wireOp",EDGE,"E1234"),sQuery(id+"F0.wireOp",EDGE,"E1235"),sQuery(id+"F0.wireOp",EDGE,"E1236"),sQuery(id+"F0.wireOp",EDGE,"E1237"),sQuery(id+"F0.wireOp",EDGE,"E1238"),sQuery(id+"F0.wireOp",EDGE,"E1239"),sQuery(id+"F0.wireOp",EDGE,"E1240"),sQuery(id+"F0.wireOp",EDGE,"E1241"),sQuery(id+"F0.wireOp",EDGE,"E1242"),sQuery(id+"F0.wireOp",EDGE,"E1243"),sQuery(id+"F0.wireOp",EDGE,"E1244"),sQuery(id+"F0.wireOp",EDGE,"E1245"),sQuery(id+"F0.wireOp",EDGE,"E1246"),sQuery(id+"F0.wireOp",EDGE,"E1247"),sQuery(id+"F0.wireOp",EDGE,"E1248"),sQuery(id+"F0.wireOp",EDGE,"E1249"),sQuery(id+"F0.wireOp",EDGE,"E1250"),sQuery(id+"F0.wireOp",EDGE,"E1251"),sQuery(id+"F0.wireOp",EDGE,"E1252"),sQuery(id+"F0.wireOp",EDGE,"E1253"),sQuery(id+"F0.wireOp",EDGE,"E1254"),sQuery(id+"F0.wireOp",EDGE,"E1255"),sQuery(id+"F0.wireOp",EDGE,"E1256"),sQuery(id+"F0.wireOp",EDGE,"E1257"),sQuery(id+"F0.wireOp",EDGE,"E1258"),sQuery(id+"F0.wireOp",EDGE,"E1259"),sQuery(id+"F0.wireOp",EDGE,"E1260"),sQuery(id+"F0.wireOp",EDGE,"E1261"),sQuery(id+"F0.wireOp",EDGE,"E1262"),sQuery(id+"F0.wireOp",EDGE,"E1263"),sQuery(id+"F0.wireOp",EDGE,"E1264"),sQuery(id+"F0.wireOp",EDGE,"E1265"),sQuery(id+"F0.wireOp",EDGE,"E1266"),sQuery(id+"F0.wireOp",EDGE,"E1267"),sQuery(id+"F0.wireOp",EDGE,"E1268"),sQuery(id+"F0.wireOp",EDGE,"E1269"),sQuery(id+"F0.wireOp",EDGE,"E1270"),sQuery(id+"F0.wireOp",EDGE,"E1271"),sQuery(id+"F0.wireOp",EDGE,"E1272"),sQuery(id+"F0.wireOp",EDGE,"E1273"),sQuery(id+"F0.wireOp",EDGE,"E1274")])],"isStart":false});
            var sketch = newSketch(context, id + "F55", { "sketchPlane" : qUnion([Q0])});
            skLineSegment(sketch, "E8055.0", {"start": v(-185.14, 673.3) * mm, "end": v(-19.73, -643.77) * mm});
            skSolve(sketch);
        }
        {
            var Q0;
            Q0=sQuery(id+"F0.wireOp",VERTEX,"E69.end");
            var Q1;
            Q1=sQuery(id+"F55.wireOp",VERTEX,"E8055.0.start");
            var Q2;
            Q2=sQuery(id+"F55.wireOp",VERTEX,"E8055.0.end");
            cPlane(context, id + "F56", {"entities" : qUnion([Q0, Q1, Q2]), "cplaneType" : CPlaneType.THREE_POINT, "offset" : 0 * mm, "width" : 152.4 * mm, "height" : 152.4 * mm});
        }
        {
            var Q0;
            Q0=qCreatedBy(id+"F56.planeOp",FACE);
            var sketch = newSketch(context, id + "F57", { "sketchPlane" : qUnion([Q0])});
            skLineSegment(sketch, "E8056.0.1", {"start": v(-728.3, 396.25) * mm, "end": v(-728.3, 534.78) * mm});
            skLineSegment(sketch, "E8056.0.2", {"start": v(-728.3, 534.78) * mm, "end": v(739.88, 534.78) * mm});
            skLineSegment(sketch, "E8056.0.3", {"start": v(739.88, 534.78) * mm, "end": v(739.88, -9.5) * mm});
            skFitSpline(sketch, "E8057", {"points": [v(-728.3, 396.25) * mm, v(-320.69, 199.86) * mm, v(260.86, 54.11) * mm, v(739.88, -9.5) * mm], "startDerivative": vector(1383.59, -277.47) * mm, "endDerivative": vector(1801.57, -577.4) * mm});
            skSolve(sketch);
        }
        {
            var Q0;
            Q0 = qSketchRegion(id + "F57", true);
            extrude(context, id + "F58", {"entities" : qUnion([Q0]), "operationType" : NewBodyOperationType.REMOVE, "depth" : 6.35 * mm});
        }
    });
